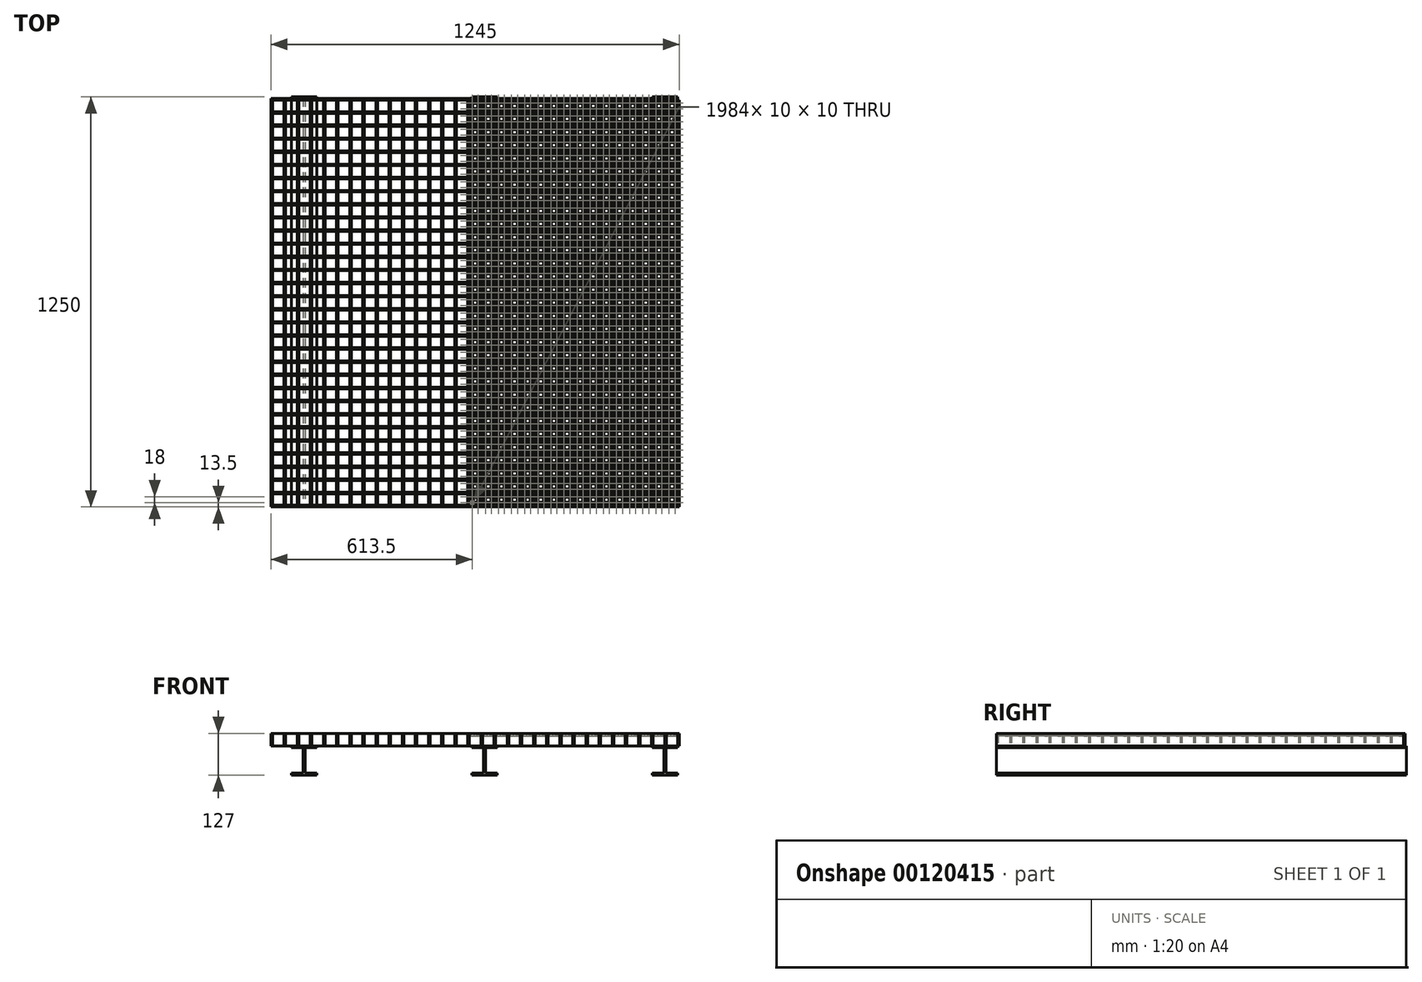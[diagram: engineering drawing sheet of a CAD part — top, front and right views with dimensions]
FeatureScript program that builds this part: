
annotation { "Feature Type Name" : "Feature", "Feature Type Description" : "" }
export const myFeature = defineFeature(function(context is Context, id is Id, definition is map)
    precondition{}
    {
        {
            var Q0;
            Q0=qCreatedBy(makeId("Top.planeOp"),FACE);
            var sketch = newSketch(context, id + "F0", { "sketchPlane" : qUnion([Q0])});
            skLineSegment(sketch, "E0.bottom", {"start": v(0, 0) * mm, "end": v(-1240, 0) * mm});
            skLineSegment(sketch, "E0.top", {"start": v(0, 5) * mm, "end": v(-1240, 5) * mm});
            skLineSegment(sketch, "E0.left", {"start": v(0, 0) * mm, "end": v(0, 5) * mm});
            skLineSegment(sketch, "E0.right", {"start": v(-1240, 0) * mm, "end": v(-1240, 5) * mm});
            skSolve(sketch);
        }
        {
            var Q0;
            Q0 = qSketchRegion(id + "F0", true);
            extrude(context, id + "F1", {"entities" : qUnion([Q0]), "depth" : 38 * mm});
        }
        {
            var Q0;
            Q0=makeQuery(id+"F1.opExtrude","SWEPT_BODY",BODY,{"disambiguationData":[OSD([sQuery(id+"F0.wireOp",EDGE,"E0.bottom"),sQuery(id+"F0.wireOp",EDGE,"E0.top"),sQuery(id+"F0.wireOp",EDGE,"E0.left"),sQuery(id+"F0.wireOp",EDGE,"E0.right")])]});
            transform(context, id + "F2", {"entities" : qUnion([Q0]), "transformType" : TransformType.TRANSLATION_3D, "dx" : 0 * mm, "dy" : 40 * mm, "dz" : 0 * mm, "makeCopy" : true});
        }
        {
            var Q0;
            Q0=makeQuery(id+"F1.opExtrude","SWEPT_BODY",BODY,{"disambiguationData":[OSD([sQuery(id+"F0.wireOp",EDGE,"E0.bottom"),sQuery(id+"F0.wireOp",EDGE,"E0.top"),sQuery(id+"F0.wireOp",EDGE,"E0.left"),sQuery(id+"F0.wireOp",EDGE,"E0.right")])]});
            var Q1;
            Q1=makeQuery(id+"F2.opPattern","COPY",BODY,{"derivedFrom":makeQuery(id+"F1.opExtrude","SWEPT_BODY",BODY,{"disambiguationData":[OSD([sQuery(id+"F0.wireOp",EDGE,"E0.bottom"),sQuery(id+"F0.wireOp",EDGE,"E0.top"),sQuery(id+"F0.wireOp",EDGE,"E0.left"),sQuery(id+"F0.wireOp",EDGE,"E0.right")])]}),"instanceName":"1"});
            transform(context, id + "F3", {"entities" : qUnion([Q0, Q1]), "transformType" : TransformType.TRANSLATION_3D, "dx" : 0 * mm, "dy" : 80 * mm, "dz" : 0 * mm, "makeCopy" : true});
        }
        {
            var Q0;
            Q0=makeQuery(id+"F1.opExtrude","SWEPT_BODY",BODY,{"disambiguationData":[OSD([sQuery(id+"F0.wireOp",EDGE,"E0.bottom"),sQuery(id+"F0.wireOp",EDGE,"E0.top"),sQuery(id+"F0.wireOp",EDGE,"E0.left"),sQuery(id+"F0.wireOp",EDGE,"E0.right")])]});
            var Q1;
            Q1=makeQuery(id+"F2.opPattern","COPY",BODY,{"derivedFrom":makeQuery(id+"F1.opExtrude","SWEPT_BODY",BODY,{"disambiguationData":[OSD([sQuery(id+"F0.wireOp",EDGE,"E0.bottom"),sQuery(id+"F0.wireOp",EDGE,"E0.top"),sQuery(id+"F0.wireOp",EDGE,"E0.left"),sQuery(id+"F0.wireOp",EDGE,"E0.right")])]}),"instanceName":"1"});
            var Q2;
            Q2=makeQuery(id+"F3.opPattern","COPY",BODY,{"derivedFrom":makeQuery(id+"F1.opExtrude","SWEPT_BODY",BODY,{"disambiguationData":[OSD([sQuery(id+"F0.wireOp",EDGE,"E0.bottom"),sQuery(id+"F0.wireOp",EDGE,"E0.top"),sQuery(id+"F0.wireOp",EDGE,"E0.left"),sQuery(id+"F0.wireOp",EDGE,"E0.right")])]}),"instanceName":"1"});
            var Q3;
            Q3=makeQuery(id+"F3.opPattern","COPY",BODY,{"derivedFrom":makeQuery(id+"F2.opPattern","COPY",BODY,{"derivedFrom":makeQuery(id+"F1.opExtrude","SWEPT_BODY",BODY,{"disambiguationData":[OSD([sQuery(id+"F0.wireOp",EDGE,"E0.bottom"),sQuery(id+"F0.wireOp",EDGE,"E0.top"),sQuery(id+"F0.wireOp",EDGE,"E0.left"),sQuery(id+"F0.wireOp",EDGE,"E0.right")])]}),"instanceName":"1"}),"instanceName":"1"});
            transform(context, id + "F4", {"entities" : qUnion([Q0, Q1, Q2, Q3]), "transformType" : TransformType.TRANSLATION_3D, "dx" : 0 * mm, "dy" : 160 * mm, "dz" : 0 * mm, "makeCopy" : true});
        }
        {
            var Q0;
            Q0=makeQuery(id+"F1.opExtrude","SWEPT_BODY",BODY,{"disambiguationData":[OSD([sQuery(id+"F0.wireOp",EDGE,"E0.bottom"),sQuery(id+"F0.wireOp",EDGE,"E0.top"),sQuery(id+"F0.wireOp",EDGE,"E0.left"),sQuery(id+"F0.wireOp",EDGE,"E0.right")])]});
            var Q1;
            Q1=makeQuery(id+"F2.opPattern","COPY",BODY,{"derivedFrom":makeQuery(id+"F1.opExtrude","SWEPT_BODY",BODY,{"disambiguationData":[OSD([sQuery(id+"F0.wireOp",EDGE,"E0.bottom"),sQuery(id+"F0.wireOp",EDGE,"E0.top"),sQuery(id+"F0.wireOp",EDGE,"E0.left"),sQuery(id+"F0.wireOp",EDGE,"E0.right")])]}),"instanceName":"1"});
            var Q2;
            Q2=makeQuery(id+"F4.opPattern","COPY",BODY,{"derivedFrom":makeQuery(id+"F3.opPattern","COPY",BODY,{"derivedFrom":makeQuery(id+"F2.opPattern","COPY",BODY,{"derivedFrom":makeQuery(id+"F1.opExtrude","SWEPT_BODY",BODY,{"disambiguationData":[OSD([sQuery(id+"F0.wireOp",EDGE,"E0.bottom"),sQuery(id+"F0.wireOp",EDGE,"E0.top"),sQuery(id+"F0.wireOp",EDGE,"E0.left"),sQuery(id+"F0.wireOp",EDGE,"E0.right")])]}),"instanceName":"1"}),"instanceName":"1"}),"instanceName":"1"});
            var Q3;
            Q3=makeQuery(id+"F4.opPattern","COPY",BODY,{"derivedFrom":makeQuery(id+"F3.opPattern","COPY",BODY,{"derivedFrom":makeQuery(id+"F1.opExtrude","SWEPT_BODY",BODY,{"disambiguationData":[OSD([sQuery(id+"F0.wireOp",EDGE,"E0.bottom"),sQuery(id+"F0.wireOp",EDGE,"E0.top"),sQuery(id+"F0.wireOp",EDGE,"E0.left"),sQuery(id+"F0.wireOp",EDGE,"E0.right")])]}),"instanceName":"1"}),"instanceName":"1"});
            var Q4;
            Q4=makeQuery(id+"F4.opPattern","COPY",BODY,{"derivedFrom":makeQuery(id+"F2.opPattern","COPY",BODY,{"derivedFrom":makeQuery(id+"F1.opExtrude","SWEPT_BODY",BODY,{"disambiguationData":[OSD([sQuery(id+"F0.wireOp",EDGE,"E0.bottom"),sQuery(id+"F0.wireOp",EDGE,"E0.top"),sQuery(id+"F0.wireOp",EDGE,"E0.left"),sQuery(id+"F0.wireOp",EDGE,"E0.right")])]}),"instanceName":"1"}),"instanceName":"1"});
            var Q5;
            Q5=makeQuery(id+"F4.opPattern","COPY",BODY,{"derivedFrom":makeQuery(id+"F1.opExtrude","SWEPT_BODY",BODY,{"disambiguationData":[OSD([sQuery(id+"F0.wireOp",EDGE,"E0.bottom"),sQuery(id+"F0.wireOp",EDGE,"E0.top"),sQuery(id+"F0.wireOp",EDGE,"E0.left"),sQuery(id+"F0.wireOp",EDGE,"E0.right")])]}),"instanceName":"1"});
            var Q6;
            Q6=makeQuery(id+"F3.opPattern","COPY",BODY,{"derivedFrom":makeQuery(id+"F1.opExtrude","SWEPT_BODY",BODY,{"disambiguationData":[OSD([sQuery(id+"F0.wireOp",EDGE,"E0.bottom"),sQuery(id+"F0.wireOp",EDGE,"E0.top"),sQuery(id+"F0.wireOp",EDGE,"E0.left"),sQuery(id+"F0.wireOp",EDGE,"E0.right")])]}),"instanceName":"1"});
            var Q7;
            Q7=makeQuery(id+"F3.opPattern","COPY",BODY,{"derivedFrom":makeQuery(id+"F2.opPattern","COPY",BODY,{"derivedFrom":makeQuery(id+"F1.opExtrude","SWEPT_BODY",BODY,{"disambiguationData":[OSD([sQuery(id+"F0.wireOp",EDGE,"E0.bottom"),sQuery(id+"F0.wireOp",EDGE,"E0.top"),sQuery(id+"F0.wireOp",EDGE,"E0.left"),sQuery(id+"F0.wireOp",EDGE,"E0.right")])]}),"instanceName":"1"}),"instanceName":"1"});
            transform(context, id + "F5", {"entities" : qUnion([Q0, Q1, Q2, Q3, Q4, Q5, Q6, Q7]), "transformType" : TransformType.TRANSLATION_3D, "dx" : 0 * mm, "dy" : 320 * mm, "dz" : 0 * mm, "makeCopy" : true});
        }
        {
            var Q0;
            Q0=makeQuery(id+"F1.opExtrude","SWEPT_BODY",BODY,{"disambiguationData":[OSD([sQuery(id+"F0.wireOp",EDGE,"E0.bottom"),sQuery(id+"F0.wireOp",EDGE,"E0.top"),sQuery(id+"F0.wireOp",EDGE,"E0.left"),sQuery(id+"F0.wireOp",EDGE,"E0.right")])]});
            var Q1;
            Q1=makeQuery(id+"F2.opPattern","COPY",BODY,{"derivedFrom":makeQuery(id+"F1.opExtrude","SWEPT_BODY",BODY,{"disambiguationData":[OSD([sQuery(id+"F0.wireOp",EDGE,"E0.bottom"),sQuery(id+"F0.wireOp",EDGE,"E0.top"),sQuery(id+"F0.wireOp",EDGE,"E0.left"),sQuery(id+"F0.wireOp",EDGE,"E0.right")])]}),"instanceName":"1"});
            var Q2;
            Q2=makeQuery(id+"F5.opPattern","COPY",BODY,{"derivedFrom":makeQuery(id+"F4.opPattern","COPY",BODY,{"derivedFrom":makeQuery(id+"F1.opExtrude","SWEPT_BODY",BODY,{"disambiguationData":[OSD([sQuery(id+"F0.wireOp",EDGE,"E0.bottom"),sQuery(id+"F0.wireOp",EDGE,"E0.top"),sQuery(id+"F0.wireOp",EDGE,"E0.left"),sQuery(id+"F0.wireOp",EDGE,"E0.right")])]}),"instanceName":"1"}),"instanceName":"1"});
            var Q3;
            Q3=makeQuery(id+"F5.opPattern","COPY",BODY,{"derivedFrom":makeQuery(id+"F4.opPattern","COPY",BODY,{"derivedFrom":makeQuery(id+"F2.opPattern","COPY",BODY,{"derivedFrom":makeQuery(id+"F1.opExtrude","SWEPT_BODY",BODY,{"disambiguationData":[OSD([sQuery(id+"F0.wireOp",EDGE,"E0.bottom"),sQuery(id+"F0.wireOp",EDGE,"E0.top"),sQuery(id+"F0.wireOp",EDGE,"E0.left"),sQuery(id+"F0.wireOp",EDGE,"E0.right")])]}),"instanceName":"1"}),"instanceName":"1"}),"instanceName":"1"});
            var Q4;
            Q4=makeQuery(id+"F5.opPattern","COPY",BODY,{"derivedFrom":makeQuery(id+"F4.opPattern","COPY",BODY,{"derivedFrom":makeQuery(id+"F3.opPattern","COPY",BODY,{"derivedFrom":makeQuery(id+"F1.opExtrude","SWEPT_BODY",BODY,{"disambiguationData":[OSD([sQuery(id+"F0.wireOp",EDGE,"E0.bottom"),sQuery(id+"F0.wireOp",EDGE,"E0.top"),sQuery(id+"F0.wireOp",EDGE,"E0.left"),sQuery(id+"F0.wireOp",EDGE,"E0.right")])]}),"instanceName":"1"}),"instanceName":"1"}),"instanceName":"1"});
            var Q5;
            Q5=makeQuery(id+"F4.opPattern","COPY",BODY,{"derivedFrom":makeQuery(id+"F3.opPattern","COPY",BODY,{"derivedFrom":makeQuery(id+"F2.opPattern","COPY",BODY,{"derivedFrom":makeQuery(id+"F1.opExtrude","SWEPT_BODY",BODY,{"disambiguationData":[OSD([sQuery(id+"F0.wireOp",EDGE,"E0.bottom"),sQuery(id+"F0.wireOp",EDGE,"E0.top"),sQuery(id+"F0.wireOp",EDGE,"E0.left"),sQuery(id+"F0.wireOp",EDGE,"E0.right")])]}),"instanceName":"1"}),"instanceName":"1"}),"instanceName":"1"});
            var Q6;
            Q6=makeQuery(id+"F4.opPattern","COPY",BODY,{"derivedFrom":makeQuery(id+"F3.opPattern","COPY",BODY,{"derivedFrom":makeQuery(id+"F1.opExtrude","SWEPT_BODY",BODY,{"disambiguationData":[OSD([sQuery(id+"F0.wireOp",EDGE,"E0.bottom"),sQuery(id+"F0.wireOp",EDGE,"E0.top"),sQuery(id+"F0.wireOp",EDGE,"E0.left"),sQuery(id+"F0.wireOp",EDGE,"E0.right")])]}),"instanceName":"1"}),"instanceName":"1"});
            var Q7;
            Q7=makeQuery(id+"F4.opPattern","COPY",BODY,{"derivedFrom":makeQuery(id+"F2.opPattern","COPY",BODY,{"derivedFrom":makeQuery(id+"F1.opExtrude","SWEPT_BODY",BODY,{"disambiguationData":[OSD([sQuery(id+"F0.wireOp",EDGE,"E0.bottom"),sQuery(id+"F0.wireOp",EDGE,"E0.top"),sQuery(id+"F0.wireOp",EDGE,"E0.left"),sQuery(id+"F0.wireOp",EDGE,"E0.right")])]}),"instanceName":"1"}),"instanceName":"1"});
            var Q8;
            Q8=makeQuery(id+"F4.opPattern","COPY",BODY,{"derivedFrom":makeQuery(id+"F1.opExtrude","SWEPT_BODY",BODY,{"disambiguationData":[OSD([sQuery(id+"F0.wireOp",EDGE,"E0.bottom"),sQuery(id+"F0.wireOp",EDGE,"E0.top"),sQuery(id+"F0.wireOp",EDGE,"E0.left"),sQuery(id+"F0.wireOp",EDGE,"E0.right")])]}),"instanceName":"1"});
            var Q9;
            Q9=makeQuery(id+"F3.opPattern","COPY",BODY,{"derivedFrom":makeQuery(id+"F1.opExtrude","SWEPT_BODY",BODY,{"disambiguationData":[OSD([sQuery(id+"F0.wireOp",EDGE,"E0.bottom"),sQuery(id+"F0.wireOp",EDGE,"E0.top"),sQuery(id+"F0.wireOp",EDGE,"E0.left"),sQuery(id+"F0.wireOp",EDGE,"E0.right")])]}),"instanceName":"1"});
            var Q10;
            Q10=makeQuery(id+"F3.opPattern","COPY",BODY,{"derivedFrom":makeQuery(id+"F2.opPattern","COPY",BODY,{"derivedFrom":makeQuery(id+"F1.opExtrude","SWEPT_BODY",BODY,{"disambiguationData":[OSD([sQuery(id+"F0.wireOp",EDGE,"E0.bottom"),sQuery(id+"F0.wireOp",EDGE,"E0.top"),sQuery(id+"F0.wireOp",EDGE,"E0.left"),sQuery(id+"F0.wireOp",EDGE,"E0.right")])]}),"instanceName":"1"}),"instanceName":"1"});
            var Q11;
            Q11=makeQuery(id+"F5.opPattern","COPY",BODY,{"derivedFrom":makeQuery(id+"F3.opPattern","COPY",BODY,{"derivedFrom":makeQuery(id+"F2.opPattern","COPY",BODY,{"derivedFrom":makeQuery(id+"F1.opExtrude","SWEPT_BODY",BODY,{"disambiguationData":[OSD([sQuery(id+"F0.wireOp",EDGE,"E0.bottom"),sQuery(id+"F0.wireOp",EDGE,"E0.top"),sQuery(id+"F0.wireOp",EDGE,"E0.left"),sQuery(id+"F0.wireOp",EDGE,"E0.right")])]}),"instanceName":"1"}),"instanceName":"1"}),"instanceName":"1"});
            var Q12;
            Q12=makeQuery(id+"F5.opPattern","COPY",BODY,{"derivedFrom":makeQuery(id+"F3.opPattern","COPY",BODY,{"derivedFrom":makeQuery(id+"F1.opExtrude","SWEPT_BODY",BODY,{"disambiguationData":[OSD([sQuery(id+"F0.wireOp",EDGE,"E0.bottom"),sQuery(id+"F0.wireOp",EDGE,"E0.top"),sQuery(id+"F0.wireOp",EDGE,"E0.left"),sQuery(id+"F0.wireOp",EDGE,"E0.right")])]}),"instanceName":"1"}),"instanceName":"1"});
            var Q13;
            Q13=makeQuery(id+"F5.opPattern","COPY",BODY,{"derivedFrom":makeQuery(id+"F2.opPattern","COPY",BODY,{"derivedFrom":makeQuery(id+"F1.opExtrude","SWEPT_BODY",BODY,{"disambiguationData":[OSD([sQuery(id+"F0.wireOp",EDGE,"E0.bottom"),sQuery(id+"F0.wireOp",EDGE,"E0.top"),sQuery(id+"F0.wireOp",EDGE,"E0.left"),sQuery(id+"F0.wireOp",EDGE,"E0.right")])]}),"instanceName":"1"}),"instanceName":"1"});
            var Q14;
            Q14=makeQuery(id+"F5.opPattern","COPY",BODY,{"derivedFrom":makeQuery(id+"F1.opExtrude","SWEPT_BODY",BODY,{"disambiguationData":[OSD([sQuery(id+"F0.wireOp",EDGE,"E0.bottom"),sQuery(id+"F0.wireOp",EDGE,"E0.top"),sQuery(id+"F0.wireOp",EDGE,"E0.left"),sQuery(id+"F0.wireOp",EDGE,"E0.right")])]}),"instanceName":"1"});
            var Q15;
            Q15=makeQuery(id+"F5.opPattern","COPY",BODY,{"derivedFrom":makeQuery(id+"F4.opPattern","COPY",BODY,{"derivedFrom":makeQuery(id+"F3.opPattern","COPY",BODY,{"derivedFrom":makeQuery(id+"F2.opPattern","COPY",BODY,{"derivedFrom":makeQuery(id+"F1.opExtrude","SWEPT_BODY",BODY,{"disambiguationData":[OSD([sQuery(id+"F0.wireOp",EDGE,"E0.bottom"),sQuery(id+"F0.wireOp",EDGE,"E0.top"),sQuery(id+"F0.wireOp",EDGE,"E0.left"),sQuery(id+"F0.wireOp",EDGE,"E0.right")])]}),"instanceName":"1"}),"instanceName":"1"}),"instanceName":"1"}),"instanceName":"1"});
            transform(context, id + "F6", {"entities" : qUnion([Q0, Q1, Q2, Q3, Q4, Q5, Q6, Q7, Q8, Q9, Q10, Q11, Q12, Q13, Q14, Q15]), "transformType" : TransformType.TRANSLATION_3D, "dx" : 0 * mm, "dy" : 640 * mm, "dz" : 0 * mm, "makeCopy" : true});
        }
        {
            var Q0;
            Q0=makeQuery(id+"F1.opExtrude","SWEPT_BODY",BODY,{"disambiguationData":[OSD([sQuery(id+"F0.wireOp",EDGE,"E0.bottom"),sQuery(id+"F0.wireOp",EDGE,"E0.top"),sQuery(id+"F0.wireOp",EDGE,"E0.left"),sQuery(id+"F0.wireOp",EDGE,"E0.right")])]});
            var Q1;
            Q1=makeQuery(id+"F2.opPattern","COPY",BODY,{"derivedFrom":makeQuery(id+"F1.opExtrude","SWEPT_BODY",BODY,{"disambiguationData":[OSD([sQuery(id+"F0.wireOp",EDGE,"E0.bottom"),sQuery(id+"F0.wireOp",EDGE,"E0.top"),sQuery(id+"F0.wireOp",EDGE,"E0.left"),sQuery(id+"F0.wireOp",EDGE,"E0.right")])]}),"instanceName":"1"});
            var Q2;
            Q2=makeQuery(id+"F5.opPattern","COPY",BODY,{"derivedFrom":makeQuery(id+"F4.opPattern","COPY",BODY,{"derivedFrom":makeQuery(id+"F1.opExtrude","SWEPT_BODY",BODY,{"disambiguationData":[OSD([sQuery(id+"F0.wireOp",EDGE,"E0.bottom"),sQuery(id+"F0.wireOp",EDGE,"E0.top"),sQuery(id+"F0.wireOp",EDGE,"E0.left"),sQuery(id+"F0.wireOp",EDGE,"E0.right")])]}),"instanceName":"1"}),"instanceName":"1"});
            var Q3;
            Q3=makeQuery(id+"F5.opPattern","COPY",BODY,{"derivedFrom":makeQuery(id+"F4.opPattern","COPY",BODY,{"derivedFrom":makeQuery(id+"F2.opPattern","COPY",BODY,{"derivedFrom":makeQuery(id+"F1.opExtrude","SWEPT_BODY",BODY,{"disambiguationData":[OSD([sQuery(id+"F0.wireOp",EDGE,"E0.bottom"),sQuery(id+"F0.wireOp",EDGE,"E0.top"),sQuery(id+"F0.wireOp",EDGE,"E0.left"),sQuery(id+"F0.wireOp",EDGE,"E0.right")])]}),"instanceName":"1"}),"instanceName":"1"}),"instanceName":"1"});
            var Q4;
            Q4=makeQuery(id+"F5.opPattern","COPY",BODY,{"derivedFrom":makeQuery(id+"F4.opPattern","COPY",BODY,{"derivedFrom":makeQuery(id+"F3.opPattern","COPY",BODY,{"derivedFrom":makeQuery(id+"F1.opExtrude","SWEPT_BODY",BODY,{"disambiguationData":[OSD([sQuery(id+"F0.wireOp",EDGE,"E0.bottom"),sQuery(id+"F0.wireOp",EDGE,"E0.top"),sQuery(id+"F0.wireOp",EDGE,"E0.left"),sQuery(id+"F0.wireOp",EDGE,"E0.right")])]}),"instanceName":"1"}),"instanceName":"1"}),"instanceName":"1"});
            var Q5;
            Q5=makeQuery(id+"F4.opPattern","COPY",BODY,{"derivedFrom":makeQuery(id+"F3.opPattern","COPY",BODY,{"derivedFrom":makeQuery(id+"F2.opPattern","COPY",BODY,{"derivedFrom":makeQuery(id+"F1.opExtrude","SWEPT_BODY",BODY,{"disambiguationData":[OSD([sQuery(id+"F0.wireOp",EDGE,"E0.bottom"),sQuery(id+"F0.wireOp",EDGE,"E0.top"),sQuery(id+"F0.wireOp",EDGE,"E0.left"),sQuery(id+"F0.wireOp",EDGE,"E0.right")])]}),"instanceName":"1"}),"instanceName":"1"}),"instanceName":"1"});
            var Q6;
            Q6=makeQuery(id+"F4.opPattern","COPY",BODY,{"derivedFrom":makeQuery(id+"F3.opPattern","COPY",BODY,{"derivedFrom":makeQuery(id+"F1.opExtrude","SWEPT_BODY",BODY,{"disambiguationData":[OSD([sQuery(id+"F0.wireOp",EDGE,"E0.bottom"),sQuery(id+"F0.wireOp",EDGE,"E0.top"),sQuery(id+"F0.wireOp",EDGE,"E0.left"),sQuery(id+"F0.wireOp",EDGE,"E0.right")])]}),"instanceName":"1"}),"instanceName":"1"});
            var Q7;
            Q7=makeQuery(id+"F4.opPattern","COPY",BODY,{"derivedFrom":makeQuery(id+"F2.opPattern","COPY",BODY,{"derivedFrom":makeQuery(id+"F1.opExtrude","SWEPT_BODY",BODY,{"disambiguationData":[OSD([sQuery(id+"F0.wireOp",EDGE,"E0.bottom"),sQuery(id+"F0.wireOp",EDGE,"E0.top"),sQuery(id+"F0.wireOp",EDGE,"E0.left"),sQuery(id+"F0.wireOp",EDGE,"E0.right")])]}),"instanceName":"1"}),"instanceName":"1"});
            var Q8;
            Q8=makeQuery(id+"F4.opPattern","COPY",BODY,{"derivedFrom":makeQuery(id+"F1.opExtrude","SWEPT_BODY",BODY,{"disambiguationData":[OSD([sQuery(id+"F0.wireOp",EDGE,"E0.bottom"),sQuery(id+"F0.wireOp",EDGE,"E0.top"),sQuery(id+"F0.wireOp",EDGE,"E0.left"),sQuery(id+"F0.wireOp",EDGE,"E0.right")])]}),"instanceName":"1"});
            var Q9;
            Q9=makeQuery(id+"F3.opPattern","COPY",BODY,{"derivedFrom":makeQuery(id+"F1.opExtrude","SWEPT_BODY",BODY,{"disambiguationData":[OSD([sQuery(id+"F0.wireOp",EDGE,"E0.bottom"),sQuery(id+"F0.wireOp",EDGE,"E0.top"),sQuery(id+"F0.wireOp",EDGE,"E0.left"),sQuery(id+"F0.wireOp",EDGE,"E0.right")])]}),"instanceName":"1"});
            var Q10;
            Q10=makeQuery(id+"F3.opPattern","COPY",BODY,{"derivedFrom":makeQuery(id+"F2.opPattern","COPY",BODY,{"derivedFrom":makeQuery(id+"F1.opExtrude","SWEPT_BODY",BODY,{"disambiguationData":[OSD([sQuery(id+"F0.wireOp",EDGE,"E0.bottom"),sQuery(id+"F0.wireOp",EDGE,"E0.top"),sQuery(id+"F0.wireOp",EDGE,"E0.left"),sQuery(id+"F0.wireOp",EDGE,"E0.right")])]}),"instanceName":"1"}),"instanceName":"1"});
            var Q11;
            Q11=makeQuery(id+"F5.opPattern","COPY",BODY,{"derivedFrom":makeQuery(id+"F3.opPattern","COPY",BODY,{"derivedFrom":makeQuery(id+"F2.opPattern","COPY",BODY,{"derivedFrom":makeQuery(id+"F1.opExtrude","SWEPT_BODY",BODY,{"disambiguationData":[OSD([sQuery(id+"F0.wireOp",EDGE,"E0.bottom"),sQuery(id+"F0.wireOp",EDGE,"E0.top"),sQuery(id+"F0.wireOp",EDGE,"E0.left"),sQuery(id+"F0.wireOp",EDGE,"E0.right")])]}),"instanceName":"1"}),"instanceName":"1"}),"instanceName":"1"});
            var Q12;
            Q12=makeQuery(id+"F5.opPattern","COPY",BODY,{"derivedFrom":makeQuery(id+"F3.opPattern","COPY",BODY,{"derivedFrom":makeQuery(id+"F1.opExtrude","SWEPT_BODY",BODY,{"disambiguationData":[OSD([sQuery(id+"F0.wireOp",EDGE,"E0.bottom"),sQuery(id+"F0.wireOp",EDGE,"E0.top"),sQuery(id+"F0.wireOp",EDGE,"E0.left"),sQuery(id+"F0.wireOp",EDGE,"E0.right")])]}),"instanceName":"1"}),"instanceName":"1"});
            var Q13;
            Q13=makeQuery(id+"F5.opPattern","COPY",BODY,{"derivedFrom":makeQuery(id+"F2.opPattern","COPY",BODY,{"derivedFrom":makeQuery(id+"F1.opExtrude","SWEPT_BODY",BODY,{"disambiguationData":[OSD([sQuery(id+"F0.wireOp",EDGE,"E0.bottom"),sQuery(id+"F0.wireOp",EDGE,"E0.top"),sQuery(id+"F0.wireOp",EDGE,"E0.left"),sQuery(id+"F0.wireOp",EDGE,"E0.right")])]}),"instanceName":"1"}),"instanceName":"1"});
            var Q14;
            Q14=makeQuery(id+"F5.opPattern","COPY",BODY,{"derivedFrom":makeQuery(id+"F1.opExtrude","SWEPT_BODY",BODY,{"disambiguationData":[OSD([sQuery(id+"F0.wireOp",EDGE,"E0.bottom"),sQuery(id+"F0.wireOp",EDGE,"E0.top"),sQuery(id+"F0.wireOp",EDGE,"E0.left"),sQuery(id+"F0.wireOp",EDGE,"E0.right")])]}),"instanceName":"1"});
            var Q15;
            Q15=makeQuery(id+"F5.opPattern","COPY",BODY,{"derivedFrom":makeQuery(id+"F4.opPattern","COPY",BODY,{"derivedFrom":makeQuery(id+"F3.opPattern","COPY",BODY,{"derivedFrom":makeQuery(id+"F2.opPattern","COPY",BODY,{"derivedFrom":makeQuery(id+"F1.opExtrude","SWEPT_BODY",BODY,{"disambiguationData":[OSD([sQuery(id+"F0.wireOp",EDGE,"E0.bottom"),sQuery(id+"F0.wireOp",EDGE,"E0.top"),sQuery(id+"F0.wireOp",EDGE,"E0.left"),sQuery(id+"F0.wireOp",EDGE,"E0.right")])]}),"instanceName":"1"}),"instanceName":"1"}),"instanceName":"1"}),"instanceName":"1"});
            var Q16;
            Q16=makeQuery(id+"F6.opPattern","COPY",BODY,{"derivedFrom":makeQuery(id+"F1.opExtrude","SWEPT_BODY",BODY,{"disambiguationData":[OSD([sQuery(id+"F0.wireOp",EDGE,"E0.bottom"),sQuery(id+"F0.wireOp",EDGE,"E0.top"),sQuery(id+"F0.wireOp",EDGE,"E0.left"),sQuery(id+"F0.wireOp",EDGE,"E0.right")])]}),"instanceName":"1"});
            var Q17;
            Q17=makeQuery(id+"F6.opPattern","COPY",BODY,{"derivedFrom":makeQuery(id+"F2.opPattern","COPY",BODY,{"derivedFrom":makeQuery(id+"F1.opExtrude","SWEPT_BODY",BODY,{"disambiguationData":[OSD([sQuery(id+"F0.wireOp",EDGE,"E0.bottom"),sQuery(id+"F0.wireOp",EDGE,"E0.top"),sQuery(id+"F0.wireOp",EDGE,"E0.left"),sQuery(id+"F0.wireOp",EDGE,"E0.right")])]}),"instanceName":"1"}),"instanceName":"1"});
            var Q18;
            Q18=makeQuery(id+"F6.opPattern","COPY",BODY,{"derivedFrom":makeQuery(id+"F3.opPattern","COPY",BODY,{"derivedFrom":makeQuery(id+"F1.opExtrude","SWEPT_BODY",BODY,{"disambiguationData":[OSD([sQuery(id+"F0.wireOp",EDGE,"E0.bottom"),sQuery(id+"F0.wireOp",EDGE,"E0.top"),sQuery(id+"F0.wireOp",EDGE,"E0.left"),sQuery(id+"F0.wireOp",EDGE,"E0.right")])]}),"instanceName":"1"}),"instanceName":"1"});
            var Q19;
            Q19=makeQuery(id+"F6.opPattern","COPY",BODY,{"derivedFrom":makeQuery(id+"F3.opPattern","COPY",BODY,{"derivedFrom":makeQuery(id+"F2.opPattern","COPY",BODY,{"derivedFrom":makeQuery(id+"F1.opExtrude","SWEPT_BODY",BODY,{"disambiguationData":[OSD([sQuery(id+"F0.wireOp",EDGE,"E0.bottom"),sQuery(id+"F0.wireOp",EDGE,"E0.top"),sQuery(id+"F0.wireOp",EDGE,"E0.left"),sQuery(id+"F0.wireOp",EDGE,"E0.right")])]}),"instanceName":"1"}),"instanceName":"1"}),"instanceName":"1"});
            var Q20;
            Q20=makeQuery(id+"F6.opPattern","COPY",BODY,{"derivedFrom":makeQuery(id+"F4.opPattern","COPY",BODY,{"derivedFrom":makeQuery(id+"F1.opExtrude","SWEPT_BODY",BODY,{"disambiguationData":[OSD([sQuery(id+"F0.wireOp",EDGE,"E0.bottom"),sQuery(id+"F0.wireOp",EDGE,"E0.top"),sQuery(id+"F0.wireOp",EDGE,"E0.left"),sQuery(id+"F0.wireOp",EDGE,"E0.right")])]}),"instanceName":"1"}),"instanceName":"1"});
            var Q21;
            Q21=makeQuery(id+"F6.opPattern","COPY",BODY,{"derivedFrom":makeQuery(id+"F4.opPattern","COPY",BODY,{"derivedFrom":makeQuery(id+"F2.opPattern","COPY",BODY,{"derivedFrom":makeQuery(id+"F1.opExtrude","SWEPT_BODY",BODY,{"disambiguationData":[OSD([sQuery(id+"F0.wireOp",EDGE,"E0.bottom"),sQuery(id+"F0.wireOp",EDGE,"E0.top"),sQuery(id+"F0.wireOp",EDGE,"E0.left"),sQuery(id+"F0.wireOp",EDGE,"E0.right")])]}),"instanceName":"1"}),"instanceName":"1"}),"instanceName":"1"});
            var Q22;
            Q22=makeQuery(id+"F6.opPattern","COPY",BODY,{"derivedFrom":makeQuery(id+"F4.opPattern","COPY",BODY,{"derivedFrom":makeQuery(id+"F3.opPattern","COPY",BODY,{"derivedFrom":makeQuery(id+"F1.opExtrude","SWEPT_BODY",BODY,{"disambiguationData":[OSD([sQuery(id+"F0.wireOp",EDGE,"E0.bottom"),sQuery(id+"F0.wireOp",EDGE,"E0.top"),sQuery(id+"F0.wireOp",EDGE,"E0.left"),sQuery(id+"F0.wireOp",EDGE,"E0.right")])]}),"instanceName":"1"}),"instanceName":"1"}),"instanceName":"1"});
            var Q23;
            Q23=makeQuery(id+"F6.opPattern","COPY",BODY,{"derivedFrom":makeQuery(id+"F4.opPattern","COPY",BODY,{"derivedFrom":makeQuery(id+"F3.opPattern","COPY",BODY,{"derivedFrom":makeQuery(id+"F2.opPattern","COPY",BODY,{"derivedFrom":makeQuery(id+"F1.opExtrude","SWEPT_BODY",BODY,{"disambiguationData":[OSD([sQuery(id+"F0.wireOp",EDGE,"E0.bottom"),sQuery(id+"F0.wireOp",EDGE,"E0.top"),sQuery(id+"F0.wireOp",EDGE,"E0.left"),sQuery(id+"F0.wireOp",EDGE,"E0.right")])]}),"instanceName":"1"}),"instanceName":"1"}),"instanceName":"1"}),"instanceName":"1"});
            var Q24;
            Q24=makeQuery(id+"F6.opPattern","COPY",BODY,{"derivedFrom":makeQuery(id+"F5.opPattern","COPY",BODY,{"derivedFrom":makeQuery(id+"F1.opExtrude","SWEPT_BODY",BODY,{"disambiguationData":[OSD([sQuery(id+"F0.wireOp",EDGE,"E0.bottom"),sQuery(id+"F0.wireOp",EDGE,"E0.top"),sQuery(id+"F0.wireOp",EDGE,"E0.left"),sQuery(id+"F0.wireOp",EDGE,"E0.right")])]}),"instanceName":"1"}),"instanceName":"1"});
            var Q25;
            Q25=makeQuery(id+"F6.opPattern","COPY",BODY,{"derivedFrom":makeQuery(id+"F5.opPattern","COPY",BODY,{"derivedFrom":makeQuery(id+"F2.opPattern","COPY",BODY,{"derivedFrom":makeQuery(id+"F1.opExtrude","SWEPT_BODY",BODY,{"disambiguationData":[OSD([sQuery(id+"F0.wireOp",EDGE,"E0.bottom"),sQuery(id+"F0.wireOp",EDGE,"E0.top"),sQuery(id+"F0.wireOp",EDGE,"E0.left"),sQuery(id+"F0.wireOp",EDGE,"E0.right")])]}),"instanceName":"1"}),"instanceName":"1"}),"instanceName":"1"});
            var Q26;
            Q26=makeQuery(id+"F6.opPattern","COPY",BODY,{"derivedFrom":makeQuery(id+"F5.opPattern","COPY",BODY,{"derivedFrom":makeQuery(id+"F3.opPattern","COPY",BODY,{"derivedFrom":makeQuery(id+"F1.opExtrude","SWEPT_BODY",BODY,{"disambiguationData":[OSD([sQuery(id+"F0.wireOp",EDGE,"E0.bottom"),sQuery(id+"F0.wireOp",EDGE,"E0.top"),sQuery(id+"F0.wireOp",EDGE,"E0.left"),sQuery(id+"F0.wireOp",EDGE,"E0.right")])]}),"instanceName":"1"}),"instanceName":"1"}),"instanceName":"1"});
            var Q27;
            Q27=makeQuery(id+"F6.opPattern","COPY",BODY,{"derivedFrom":makeQuery(id+"F5.opPattern","COPY",BODY,{"derivedFrom":makeQuery(id+"F3.opPattern","COPY",BODY,{"derivedFrom":makeQuery(id+"F2.opPattern","COPY",BODY,{"derivedFrom":makeQuery(id+"F1.opExtrude","SWEPT_BODY",BODY,{"disambiguationData":[OSD([sQuery(id+"F0.wireOp",EDGE,"E0.bottom"),sQuery(id+"F0.wireOp",EDGE,"E0.top"),sQuery(id+"F0.wireOp",EDGE,"E0.left"),sQuery(id+"F0.wireOp",EDGE,"E0.right")])]}),"instanceName":"1"}),"instanceName":"1"}),"instanceName":"1"}),"instanceName":"1"});
            var Q28;
            Q28=makeQuery(id+"F6.opPattern","COPY",BODY,{"derivedFrom":makeQuery(id+"F5.opPattern","COPY",BODY,{"derivedFrom":makeQuery(id+"F4.opPattern","COPY",BODY,{"derivedFrom":makeQuery(id+"F1.opExtrude","SWEPT_BODY",BODY,{"disambiguationData":[OSD([sQuery(id+"F0.wireOp",EDGE,"E0.bottom"),sQuery(id+"F0.wireOp",EDGE,"E0.top"),sQuery(id+"F0.wireOp",EDGE,"E0.left"),sQuery(id+"F0.wireOp",EDGE,"E0.right")])]}),"instanceName":"1"}),"instanceName":"1"}),"instanceName":"1"});
            var Q29;
            Q29=makeQuery(id+"F6.opPattern","COPY",BODY,{"derivedFrom":makeQuery(id+"F5.opPattern","COPY",BODY,{"derivedFrom":makeQuery(id+"F4.opPattern","COPY",BODY,{"derivedFrom":makeQuery(id+"F2.opPattern","COPY",BODY,{"derivedFrom":makeQuery(id+"F1.opExtrude","SWEPT_BODY",BODY,{"disambiguationData":[OSD([sQuery(id+"F0.wireOp",EDGE,"E0.bottom"),sQuery(id+"F0.wireOp",EDGE,"E0.top"),sQuery(id+"F0.wireOp",EDGE,"E0.left"),sQuery(id+"F0.wireOp",EDGE,"E0.right")])]}),"instanceName":"1"}),"instanceName":"1"}),"instanceName":"1"}),"instanceName":"1"});
            var Q30;
            Q30=makeQuery(id+"F6.opPattern","COPY",BODY,{"derivedFrom":makeQuery(id+"F5.opPattern","COPY",BODY,{"derivedFrom":makeQuery(id+"F4.opPattern","COPY",BODY,{"derivedFrom":makeQuery(id+"F3.opPattern","COPY",BODY,{"derivedFrom":makeQuery(id+"F1.opExtrude","SWEPT_BODY",BODY,{"disambiguationData":[OSD([sQuery(id+"F0.wireOp",EDGE,"E0.bottom"),sQuery(id+"F0.wireOp",EDGE,"E0.top"),sQuery(id+"F0.wireOp",EDGE,"E0.left"),sQuery(id+"F0.wireOp",EDGE,"E0.right")])]}),"instanceName":"1"}),"instanceName":"1"}),"instanceName":"1"}),"instanceName":"1"});
            var Q31;
            Q31=makeQuery(id+"F6.opPattern","COPY",BODY,{"derivedFrom":makeQuery(id+"F5.opPattern","COPY",BODY,{"derivedFrom":makeQuery(id+"F4.opPattern","COPY",BODY,{"derivedFrom":makeQuery(id+"F3.opPattern","COPY",BODY,{"derivedFrom":makeQuery(id+"F2.opPattern","COPY",BODY,{"derivedFrom":makeQuery(id+"F1.opExtrude","SWEPT_BODY",BODY,{"disambiguationData":[OSD([sQuery(id+"F0.wireOp",EDGE,"E0.bottom"),sQuery(id+"F0.wireOp",EDGE,"E0.top"),sQuery(id+"F0.wireOp",EDGE,"E0.left"),sQuery(id+"F0.wireOp",EDGE,"E0.right")])]}),"instanceName":"1"}),"instanceName":"1"}),"instanceName":"1"}),"instanceName":"1"}),"instanceName":"1"});
            var Q32;
            Q32=makeQuery(id+"F1.opExtrude","SWEPT_EDGE",EDGE,{"disambiguationData":[OSD([sQuery(id+"F0.wireOp",EDGE,"E0.bottom"),sQuery(id+"F0.wireOp",EDGE,"E0.left")])]});
            transform(context, id + "F7", {"entities" : qUnion([Q0, Q1, Q2, Q3, Q4, Q5, Q6, Q7, Q8, Q9, Q10, Q11, Q12, Q13, Q14, Q15, Q16, Q17, Q18, Q19, Q20, Q21, Q22, Q23, Q24, Q25, Q26, Q27, Q28, Q29, Q30, Q31]), "transformType" : TransformType.ROTATION, "transformAxis" : qUnion([Q32]), "angle" : 90 * degree, "makeCopy" : true});
        }
        {
            var Q0;
            Q0=makeQuery(id+"F7.opPattern","COPY",BODY,{"derivedFrom":makeQuery(id+"F2.opPattern","COPY",BODY,{"derivedFrom":makeQuery(id+"F1.opExtrude","SWEPT_BODY",BODY,{"disambiguationData":[OSD([sQuery(id+"F0.wireOp",EDGE,"E0.bottom"),sQuery(id+"F0.wireOp",EDGE,"E0.top"),sQuery(id+"F0.wireOp",EDGE,"E0.left"),sQuery(id+"F0.wireOp",EDGE,"E0.right")])]}),"instanceName":"1"}),"instanceName":"1"});
            var Q1;
            Q1=makeQuery(id+"F7.opPattern","COPY",BODY,{"derivedFrom":makeQuery(id+"F3.opPattern","COPY",BODY,{"derivedFrom":makeQuery(id+"F1.opExtrude","SWEPT_BODY",BODY,{"disambiguationData":[OSD([sQuery(id+"F0.wireOp",EDGE,"E0.bottom"),sQuery(id+"F0.wireOp",EDGE,"E0.top"),sQuery(id+"F0.wireOp",EDGE,"E0.left"),sQuery(id+"F0.wireOp",EDGE,"E0.right")])]}),"instanceName":"1"}),"instanceName":"1"});
            var Q2;
            Q2=makeQuery(id+"F7.opPattern","COPY",BODY,{"derivedFrom":makeQuery(id+"F3.opPattern","COPY",BODY,{"derivedFrom":makeQuery(id+"F2.opPattern","COPY",BODY,{"derivedFrom":makeQuery(id+"F1.opExtrude","SWEPT_BODY",BODY,{"disambiguationData":[OSD([sQuery(id+"F0.wireOp",EDGE,"E0.bottom"),sQuery(id+"F0.wireOp",EDGE,"E0.top"),sQuery(id+"F0.wireOp",EDGE,"E0.left"),sQuery(id+"F0.wireOp",EDGE,"E0.right")])]}),"instanceName":"1"}),"instanceName":"1"}),"instanceName":"1"});
            var Q3;
            Q3=makeQuery(id+"F7.opPattern","COPY",BODY,{"derivedFrom":makeQuery(id+"F4.opPattern","COPY",BODY,{"derivedFrom":makeQuery(id+"F1.opExtrude","SWEPT_BODY",BODY,{"disambiguationData":[OSD([sQuery(id+"F0.wireOp",EDGE,"E0.bottom"),sQuery(id+"F0.wireOp",EDGE,"E0.top"),sQuery(id+"F0.wireOp",EDGE,"E0.left"),sQuery(id+"F0.wireOp",EDGE,"E0.right")])]}),"instanceName":"1"}),"instanceName":"1"});
            var Q4;
            Q4=makeQuery(id+"F7.opPattern","COPY",BODY,{"derivedFrom":makeQuery(id+"F4.opPattern","COPY",BODY,{"derivedFrom":makeQuery(id+"F2.opPattern","COPY",BODY,{"derivedFrom":makeQuery(id+"F1.opExtrude","SWEPT_BODY",BODY,{"disambiguationData":[OSD([sQuery(id+"F0.wireOp",EDGE,"E0.bottom"),sQuery(id+"F0.wireOp",EDGE,"E0.top"),sQuery(id+"F0.wireOp",EDGE,"E0.left"),sQuery(id+"F0.wireOp",EDGE,"E0.right")])]}),"instanceName":"1"}),"instanceName":"1"}),"instanceName":"1"});
            var Q5;
            Q5=makeQuery(id+"F7.opPattern","COPY",BODY,{"derivedFrom":makeQuery(id+"F4.opPattern","COPY",BODY,{"derivedFrom":makeQuery(id+"F3.opPattern","COPY",BODY,{"derivedFrom":makeQuery(id+"F1.opExtrude","SWEPT_BODY",BODY,{"disambiguationData":[OSD([sQuery(id+"F0.wireOp",EDGE,"E0.bottom"),sQuery(id+"F0.wireOp",EDGE,"E0.top"),sQuery(id+"F0.wireOp",EDGE,"E0.left"),sQuery(id+"F0.wireOp",EDGE,"E0.right")])]}),"instanceName":"1"}),"instanceName":"1"}),"instanceName":"1"});
            var Q6;
            Q6=makeQuery(id+"F7.opPattern","COPY",BODY,{"derivedFrom":makeQuery(id+"F4.opPattern","COPY",BODY,{"derivedFrom":makeQuery(id+"F3.opPattern","COPY",BODY,{"derivedFrom":makeQuery(id+"F2.opPattern","COPY",BODY,{"derivedFrom":makeQuery(id+"F1.opExtrude","SWEPT_BODY",BODY,{"disambiguationData":[OSD([sQuery(id+"F0.wireOp",EDGE,"E0.bottom"),sQuery(id+"F0.wireOp",EDGE,"E0.top"),sQuery(id+"F0.wireOp",EDGE,"E0.left"),sQuery(id+"F0.wireOp",EDGE,"E0.right")])]}),"instanceName":"1"}),"instanceName":"1"}),"instanceName":"1"}),"instanceName":"1"});
            var Q7;
            Q7=makeQuery(id+"F7.opPattern","COPY",BODY,{"derivedFrom":makeQuery(id+"F5.opPattern","COPY",BODY,{"derivedFrom":makeQuery(id+"F1.opExtrude","SWEPT_BODY",BODY,{"disambiguationData":[OSD([sQuery(id+"F0.wireOp",EDGE,"E0.bottom"),sQuery(id+"F0.wireOp",EDGE,"E0.top"),sQuery(id+"F0.wireOp",EDGE,"E0.left"),sQuery(id+"F0.wireOp",EDGE,"E0.right")])]}),"instanceName":"1"}),"instanceName":"1"});
            var Q8;
            Q8=makeQuery(id+"F7.opPattern","COPY",BODY,{"derivedFrom":makeQuery(id+"F5.opPattern","COPY",BODY,{"derivedFrom":makeQuery(id+"F2.opPattern","COPY",BODY,{"derivedFrom":makeQuery(id+"F1.opExtrude","SWEPT_BODY",BODY,{"disambiguationData":[OSD([sQuery(id+"F0.wireOp",EDGE,"E0.bottom"),sQuery(id+"F0.wireOp",EDGE,"E0.top"),sQuery(id+"F0.wireOp",EDGE,"E0.left"),sQuery(id+"F0.wireOp",EDGE,"E0.right")])]}),"instanceName":"1"}),"instanceName":"1"}),"instanceName":"1"});
            var Q9;
            Q9=makeQuery(id+"F7.opPattern","COPY",BODY,{"derivedFrom":makeQuery(id+"F5.opPattern","COPY",BODY,{"derivedFrom":makeQuery(id+"F3.opPattern","COPY",BODY,{"derivedFrom":makeQuery(id+"F1.opExtrude","SWEPT_BODY",BODY,{"disambiguationData":[OSD([sQuery(id+"F0.wireOp",EDGE,"E0.bottom"),sQuery(id+"F0.wireOp",EDGE,"E0.top"),sQuery(id+"F0.wireOp",EDGE,"E0.left"),sQuery(id+"F0.wireOp",EDGE,"E0.right")])]}),"instanceName":"1"}),"instanceName":"1"}),"instanceName":"1"});
            var Q10;
            Q10=makeQuery(id+"F7.opPattern","COPY",BODY,{"derivedFrom":makeQuery(id+"F5.opPattern","COPY",BODY,{"derivedFrom":makeQuery(id+"F3.opPattern","COPY",BODY,{"derivedFrom":makeQuery(id+"F2.opPattern","COPY",BODY,{"derivedFrom":makeQuery(id+"F1.opExtrude","SWEPT_BODY",BODY,{"disambiguationData":[OSD([sQuery(id+"F0.wireOp",EDGE,"E0.bottom"),sQuery(id+"F0.wireOp",EDGE,"E0.top"),sQuery(id+"F0.wireOp",EDGE,"E0.left"),sQuery(id+"F0.wireOp",EDGE,"E0.right")])]}),"instanceName":"1"}),"instanceName":"1"}),"instanceName":"1"}),"instanceName":"1"});
            var Q11;
            Q11=makeQuery(id+"F7.opPattern","COPY",BODY,{"derivedFrom":makeQuery(id+"F5.opPattern","COPY",BODY,{"derivedFrom":makeQuery(id+"F4.opPattern","COPY",BODY,{"derivedFrom":makeQuery(id+"F1.opExtrude","SWEPT_BODY",BODY,{"disambiguationData":[OSD([sQuery(id+"F0.wireOp",EDGE,"E0.bottom"),sQuery(id+"F0.wireOp",EDGE,"E0.top"),sQuery(id+"F0.wireOp",EDGE,"E0.left"),sQuery(id+"F0.wireOp",EDGE,"E0.right")])]}),"instanceName":"1"}),"instanceName":"1"}),"instanceName":"1"});
            var Q12;
            Q12=makeQuery(id+"F7.opPattern","COPY",BODY,{"derivedFrom":makeQuery(id+"F5.opPattern","COPY",BODY,{"derivedFrom":makeQuery(id+"F4.opPattern","COPY",BODY,{"derivedFrom":makeQuery(id+"F2.opPattern","COPY",BODY,{"derivedFrom":makeQuery(id+"F1.opExtrude","SWEPT_BODY",BODY,{"disambiguationData":[OSD([sQuery(id+"F0.wireOp",EDGE,"E0.bottom"),sQuery(id+"F0.wireOp",EDGE,"E0.top"),sQuery(id+"F0.wireOp",EDGE,"E0.left"),sQuery(id+"F0.wireOp",EDGE,"E0.right")])]}),"instanceName":"1"}),"instanceName":"1"}),"instanceName":"1"}),"instanceName":"1"});
            var Q13;
            Q13=makeQuery(id+"F7.opPattern","COPY",BODY,{"derivedFrom":makeQuery(id+"F5.opPattern","COPY",BODY,{"derivedFrom":makeQuery(id+"F4.opPattern","COPY",BODY,{"derivedFrom":makeQuery(id+"F3.opPattern","COPY",BODY,{"derivedFrom":makeQuery(id+"F1.opExtrude","SWEPT_BODY",BODY,{"disambiguationData":[OSD([sQuery(id+"F0.wireOp",EDGE,"E0.bottom"),sQuery(id+"F0.wireOp",EDGE,"E0.top"),sQuery(id+"F0.wireOp",EDGE,"E0.left"),sQuery(id+"F0.wireOp",EDGE,"E0.right")])]}),"instanceName":"1"}),"instanceName":"1"}),"instanceName":"1"}),"instanceName":"1"});
            var Q14;
            Q14=makeQuery(id+"F7.opPattern","COPY",BODY,{"derivedFrom":makeQuery(id+"F5.opPattern","COPY",BODY,{"derivedFrom":makeQuery(id+"F4.opPattern","COPY",BODY,{"derivedFrom":makeQuery(id+"F3.opPattern","COPY",BODY,{"derivedFrom":makeQuery(id+"F2.opPattern","COPY",BODY,{"derivedFrom":makeQuery(id+"F1.opExtrude","SWEPT_BODY",BODY,{"disambiguationData":[OSD([sQuery(id+"F0.wireOp",EDGE,"E0.bottom"),sQuery(id+"F0.wireOp",EDGE,"E0.top"),sQuery(id+"F0.wireOp",EDGE,"E0.left"),sQuery(id+"F0.wireOp",EDGE,"E0.right")])]}),"instanceName":"1"}),"instanceName":"1"}),"instanceName":"1"}),"instanceName":"1"}),"instanceName":"1"});
            var Q15;
            Q15=makeQuery(id+"F7.opPattern","COPY",BODY,{"derivedFrom":makeQuery(id+"F6.opPattern","COPY",BODY,{"derivedFrom":makeQuery(id+"F1.opExtrude","SWEPT_BODY",BODY,{"disambiguationData":[OSD([sQuery(id+"F0.wireOp",EDGE,"E0.bottom"),sQuery(id+"F0.wireOp",EDGE,"E0.top"),sQuery(id+"F0.wireOp",EDGE,"E0.left"),sQuery(id+"F0.wireOp",EDGE,"E0.right")])]}),"instanceName":"1"}),"instanceName":"1"});
            var Q16;
            Q16=makeQuery(id+"F7.opPattern","COPY",BODY,{"derivedFrom":makeQuery(id+"F6.opPattern","COPY",BODY,{"derivedFrom":makeQuery(id+"F2.opPattern","COPY",BODY,{"derivedFrom":makeQuery(id+"F1.opExtrude","SWEPT_BODY",BODY,{"disambiguationData":[OSD([sQuery(id+"F0.wireOp",EDGE,"E0.bottom"),sQuery(id+"F0.wireOp",EDGE,"E0.top"),sQuery(id+"F0.wireOp",EDGE,"E0.left"),sQuery(id+"F0.wireOp",EDGE,"E0.right")])]}),"instanceName":"1"}),"instanceName":"1"}),"instanceName":"1"});
            var Q17;
            Q17=makeQuery(id+"F7.opPattern","COPY",BODY,{"derivedFrom":makeQuery(id+"F6.opPattern","COPY",BODY,{"derivedFrom":makeQuery(id+"F3.opPattern","COPY",BODY,{"derivedFrom":makeQuery(id+"F1.opExtrude","SWEPT_BODY",BODY,{"disambiguationData":[OSD([sQuery(id+"F0.wireOp",EDGE,"E0.bottom"),sQuery(id+"F0.wireOp",EDGE,"E0.top"),sQuery(id+"F0.wireOp",EDGE,"E0.left"),sQuery(id+"F0.wireOp",EDGE,"E0.right")])]}),"instanceName":"1"}),"instanceName":"1"}),"instanceName":"1"});
            var Q18;
            Q18=makeQuery(id+"F7.opPattern","COPY",BODY,{"derivedFrom":makeQuery(id+"F6.opPattern","COPY",BODY,{"derivedFrom":makeQuery(id+"F3.opPattern","COPY",BODY,{"derivedFrom":makeQuery(id+"F2.opPattern","COPY",BODY,{"derivedFrom":makeQuery(id+"F1.opExtrude","SWEPT_BODY",BODY,{"disambiguationData":[OSD([sQuery(id+"F0.wireOp",EDGE,"E0.bottom"),sQuery(id+"F0.wireOp",EDGE,"E0.top"),sQuery(id+"F0.wireOp",EDGE,"E0.left"),sQuery(id+"F0.wireOp",EDGE,"E0.right")])]}),"instanceName":"1"}),"instanceName":"1"}),"instanceName":"1"}),"instanceName":"1"});
            var Q19;
            Q19=makeQuery(id+"F7.opPattern","COPY",BODY,{"derivedFrom":makeQuery(id+"F6.opPattern","COPY",BODY,{"derivedFrom":makeQuery(id+"F4.opPattern","COPY",BODY,{"derivedFrom":makeQuery(id+"F1.opExtrude","SWEPT_BODY",BODY,{"disambiguationData":[OSD([sQuery(id+"F0.wireOp",EDGE,"E0.bottom"),sQuery(id+"F0.wireOp",EDGE,"E0.top"),sQuery(id+"F0.wireOp",EDGE,"E0.left"),sQuery(id+"F0.wireOp",EDGE,"E0.right")])]}),"instanceName":"1"}),"instanceName":"1"}),"instanceName":"1"});
            var Q20;
            Q20=makeQuery(id+"F7.opPattern","COPY",BODY,{"derivedFrom":makeQuery(id+"F6.opPattern","COPY",BODY,{"derivedFrom":makeQuery(id+"F4.opPattern","COPY",BODY,{"derivedFrom":makeQuery(id+"F2.opPattern","COPY",BODY,{"derivedFrom":makeQuery(id+"F1.opExtrude","SWEPT_BODY",BODY,{"disambiguationData":[OSD([sQuery(id+"F0.wireOp",EDGE,"E0.bottom"),sQuery(id+"F0.wireOp",EDGE,"E0.top"),sQuery(id+"F0.wireOp",EDGE,"E0.left"),sQuery(id+"F0.wireOp",EDGE,"E0.right")])]}),"instanceName":"1"}),"instanceName":"1"}),"instanceName":"1"}),"instanceName":"1"});
            var Q21;
            Q21=makeQuery(id+"F7.opPattern","COPY",BODY,{"derivedFrom":makeQuery(id+"F6.opPattern","COPY",BODY,{"derivedFrom":makeQuery(id+"F4.opPattern","COPY",BODY,{"derivedFrom":makeQuery(id+"F3.opPattern","COPY",BODY,{"derivedFrom":makeQuery(id+"F1.opExtrude","SWEPT_BODY",BODY,{"disambiguationData":[OSD([sQuery(id+"F0.wireOp",EDGE,"E0.bottom"),sQuery(id+"F0.wireOp",EDGE,"E0.top"),sQuery(id+"F0.wireOp",EDGE,"E0.left"),sQuery(id+"F0.wireOp",EDGE,"E0.right")])]}),"instanceName":"1"}),"instanceName":"1"}),"instanceName":"1"}),"instanceName":"1"});
            var Q22;
            Q22=makeQuery(id+"F7.opPattern","COPY",BODY,{"derivedFrom":makeQuery(id+"F6.opPattern","COPY",BODY,{"derivedFrom":makeQuery(id+"F4.opPattern","COPY",BODY,{"derivedFrom":makeQuery(id+"F3.opPattern","COPY",BODY,{"derivedFrom":makeQuery(id+"F2.opPattern","COPY",BODY,{"derivedFrom":makeQuery(id+"F1.opExtrude","SWEPT_BODY",BODY,{"disambiguationData":[OSD([sQuery(id+"F0.wireOp",EDGE,"E0.bottom"),sQuery(id+"F0.wireOp",EDGE,"E0.top"),sQuery(id+"F0.wireOp",EDGE,"E0.left"),sQuery(id+"F0.wireOp",EDGE,"E0.right")])]}),"instanceName":"1"}),"instanceName":"1"}),"instanceName":"1"}),"instanceName":"1"}),"instanceName":"1"});
            var Q23;
            Q23=makeQuery(id+"F7.opPattern","COPY",BODY,{"derivedFrom":makeQuery(id+"F6.opPattern","COPY",BODY,{"derivedFrom":makeQuery(id+"F5.opPattern","COPY",BODY,{"derivedFrom":makeQuery(id+"F1.opExtrude","SWEPT_BODY",BODY,{"disambiguationData":[OSD([sQuery(id+"F0.wireOp",EDGE,"E0.bottom"),sQuery(id+"F0.wireOp",EDGE,"E0.top"),sQuery(id+"F0.wireOp",EDGE,"E0.left"),sQuery(id+"F0.wireOp",EDGE,"E0.right")])]}),"instanceName":"1"}),"instanceName":"1"}),"instanceName":"1"});
            var Q24;
            Q24=makeQuery(id+"F7.opPattern","COPY",BODY,{"derivedFrom":makeQuery(id+"F6.opPattern","COPY",BODY,{"derivedFrom":makeQuery(id+"F5.opPattern","COPY",BODY,{"derivedFrom":makeQuery(id+"F2.opPattern","COPY",BODY,{"derivedFrom":makeQuery(id+"F1.opExtrude","SWEPT_BODY",BODY,{"disambiguationData":[OSD([sQuery(id+"F0.wireOp",EDGE,"E0.bottom"),sQuery(id+"F0.wireOp",EDGE,"E0.top"),sQuery(id+"F0.wireOp",EDGE,"E0.left"),sQuery(id+"F0.wireOp",EDGE,"E0.right")])]}),"instanceName":"1"}),"instanceName":"1"}),"instanceName":"1"}),"instanceName":"1"});
            var Q25;
            Q25=makeQuery(id+"F7.opPattern","COPY",BODY,{"derivedFrom":makeQuery(id+"F6.opPattern","COPY",BODY,{"derivedFrom":makeQuery(id+"F5.opPattern","COPY",BODY,{"derivedFrom":makeQuery(id+"F3.opPattern","COPY",BODY,{"derivedFrom":makeQuery(id+"F1.opExtrude","SWEPT_BODY",BODY,{"disambiguationData":[OSD([sQuery(id+"F0.wireOp",EDGE,"E0.bottom"),sQuery(id+"F0.wireOp",EDGE,"E0.top"),sQuery(id+"F0.wireOp",EDGE,"E0.left"),sQuery(id+"F0.wireOp",EDGE,"E0.right")])]}),"instanceName":"1"}),"instanceName":"1"}),"instanceName":"1"}),"instanceName":"1"});
            var Q26;
            Q26=makeQuery(id+"F7.opPattern","COPY",BODY,{"derivedFrom":makeQuery(id+"F6.opPattern","COPY",BODY,{"derivedFrom":makeQuery(id+"F5.opPattern","COPY",BODY,{"derivedFrom":makeQuery(id+"F3.opPattern","COPY",BODY,{"derivedFrom":makeQuery(id+"F2.opPattern","COPY",BODY,{"derivedFrom":makeQuery(id+"F1.opExtrude","SWEPT_BODY",BODY,{"disambiguationData":[OSD([sQuery(id+"F0.wireOp",EDGE,"E0.bottom"),sQuery(id+"F0.wireOp",EDGE,"E0.top"),sQuery(id+"F0.wireOp",EDGE,"E0.left"),sQuery(id+"F0.wireOp",EDGE,"E0.right")])]}),"instanceName":"1"}),"instanceName":"1"}),"instanceName":"1"}),"instanceName":"1"}),"instanceName":"1"});
            var Q27;
            Q27=makeQuery(id+"F7.opPattern","COPY",BODY,{"derivedFrom":makeQuery(id+"F6.opPattern","COPY",BODY,{"derivedFrom":makeQuery(id+"F5.opPattern","COPY",BODY,{"derivedFrom":makeQuery(id+"F4.opPattern","COPY",BODY,{"derivedFrom":makeQuery(id+"F1.opExtrude","SWEPT_BODY",BODY,{"disambiguationData":[OSD([sQuery(id+"F0.wireOp",EDGE,"E0.bottom"),sQuery(id+"F0.wireOp",EDGE,"E0.top"),sQuery(id+"F0.wireOp",EDGE,"E0.left"),sQuery(id+"F0.wireOp",EDGE,"E0.right")])]}),"instanceName":"1"}),"instanceName":"1"}),"instanceName":"1"}),"instanceName":"1"});
            var Q28;
            Q28=makeQuery(id+"F7.opPattern","COPY",BODY,{"derivedFrom":makeQuery(id+"F6.opPattern","COPY",BODY,{"derivedFrom":makeQuery(id+"F5.opPattern","COPY",BODY,{"derivedFrom":makeQuery(id+"F4.opPattern","COPY",BODY,{"derivedFrom":makeQuery(id+"F2.opPattern","COPY",BODY,{"derivedFrom":makeQuery(id+"F1.opExtrude","SWEPT_BODY",BODY,{"disambiguationData":[OSD([sQuery(id+"F0.wireOp",EDGE,"E0.bottom"),sQuery(id+"F0.wireOp",EDGE,"E0.top"),sQuery(id+"F0.wireOp",EDGE,"E0.left"),sQuery(id+"F0.wireOp",EDGE,"E0.right")])]}),"instanceName":"1"}),"instanceName":"1"}),"instanceName":"1"}),"instanceName":"1"}),"instanceName":"1"});
            var Q29;
            Q29=makeQuery(id+"F7.opPattern","COPY",BODY,{"derivedFrom":makeQuery(id+"F6.opPattern","COPY",BODY,{"derivedFrom":makeQuery(id+"F5.opPattern","COPY",BODY,{"derivedFrom":makeQuery(id+"F4.opPattern","COPY",BODY,{"derivedFrom":makeQuery(id+"F3.opPattern","COPY",BODY,{"derivedFrom":makeQuery(id+"F1.opExtrude","SWEPT_BODY",BODY,{"disambiguationData":[OSD([sQuery(id+"F0.wireOp",EDGE,"E0.bottom"),sQuery(id+"F0.wireOp",EDGE,"E0.top"),sQuery(id+"F0.wireOp",EDGE,"E0.left"),sQuery(id+"F0.wireOp",EDGE,"E0.right")])]}),"instanceName":"1"}),"instanceName":"1"}),"instanceName":"1"}),"instanceName":"1"}),"instanceName":"1"});
            var Q30;
            Q30=makeQuery(id+"F7.opPattern","COPY",BODY,{"derivedFrom":makeQuery(id+"F6.opPattern","COPY",BODY,{"derivedFrom":makeQuery(id+"F5.opPattern","COPY",BODY,{"derivedFrom":makeQuery(id+"F4.opPattern","COPY",BODY,{"derivedFrom":makeQuery(id+"F3.opPattern","COPY",BODY,{"derivedFrom":makeQuery(id+"F2.opPattern","COPY",BODY,{"derivedFrom":makeQuery(id+"F1.opExtrude","SWEPT_BODY",BODY,{"disambiguationData":[OSD([sQuery(id+"F0.wireOp",EDGE,"E0.bottom"),sQuery(id+"F0.wireOp",EDGE,"E0.top"),sQuery(id+"F0.wireOp",EDGE,"E0.left"),sQuery(id+"F0.wireOp",EDGE,"E0.right")])]}),"instanceName":"1"}),"instanceName":"1"}),"instanceName":"1"}),"instanceName":"1"}),"instanceName":"1"}),"instanceName":"1"});
            var Q31;
            Q31=makeQuery(id+"F7.opPattern","COPY",BODY,{"derivedFrom":makeQuery(id+"F1.opExtrude","SWEPT_BODY",BODY,{"disambiguationData":[OSD([sQuery(id+"F0.wireOp",EDGE,"E0.bottom"),sQuery(id+"F0.wireOp",EDGE,"E0.top"),sQuery(id+"F0.wireOp",EDGE,"E0.left"),sQuery(id+"F0.wireOp",EDGE,"E0.right")])]}),"instanceName":"1"});
            transform(context, id + "F8", {"entities" : qUnion([Q0, Q1, Q2, Q3, Q4, Q5, Q6, Q7, Q8, Q9, Q10, Q11, Q12, Q13, Q14, Q15, Q16, Q17, Q18, Q19, Q20, Q21, Q22, Q23, Q24, Q25, Q26, Q27, Q28, Q29, Q30, Q31]), "transformType" : TransformType.TRANSLATION_3D, "dx" : -1000 * mm, "dy" : 0 * mm, "dz" : 0 * mm, "makeCopy" : false});
        }
        {
            var Q0;
            Q0=makeQuery(id+"F7.opPattern","COPY",BODY,{"derivedFrom":makeQuery(id+"F1.opExtrude","SWEPT_BODY",BODY,{"disambiguationData":[OSD([sQuery(id+"F0.wireOp",EDGE,"E0.bottom"),sQuery(id+"F0.wireOp",EDGE,"E0.top"),sQuery(id+"F0.wireOp",EDGE,"E0.left"),sQuery(id+"F0.wireOp",EDGE,"E0.right")])]}),"instanceName":"1"});
            var Q1;
            Q1=makeQuery(id+"F7.opPattern","COPY",BODY,{"derivedFrom":makeQuery(id+"F2.opPattern","COPY",BODY,{"derivedFrom":makeQuery(id+"F1.opExtrude","SWEPT_BODY",BODY,{"disambiguationData":[OSD([sQuery(id+"F0.wireOp",EDGE,"E0.bottom"),sQuery(id+"F0.wireOp",EDGE,"E0.top"),sQuery(id+"F0.wireOp",EDGE,"E0.left"),sQuery(id+"F0.wireOp",EDGE,"E0.right")])]}),"instanceName":"1"}),"instanceName":"1"});
            var Q2;
            Q2=makeQuery(id+"F7.opPattern","COPY",BODY,{"derivedFrom":makeQuery(id+"F3.opPattern","COPY",BODY,{"derivedFrom":makeQuery(id+"F1.opExtrude","SWEPT_BODY",BODY,{"disambiguationData":[OSD([sQuery(id+"F0.wireOp",EDGE,"E0.bottom"),sQuery(id+"F0.wireOp",EDGE,"E0.top"),sQuery(id+"F0.wireOp",EDGE,"E0.left"),sQuery(id+"F0.wireOp",EDGE,"E0.right")])]}),"instanceName":"1"}),"instanceName":"1"});
            var Q3;
            Q3=makeQuery(id+"F7.opPattern","COPY",BODY,{"derivedFrom":makeQuery(id+"F3.opPattern","COPY",BODY,{"derivedFrom":makeQuery(id+"F2.opPattern","COPY",BODY,{"derivedFrom":makeQuery(id+"F1.opExtrude","SWEPT_BODY",BODY,{"disambiguationData":[OSD([sQuery(id+"F0.wireOp",EDGE,"E0.bottom"),sQuery(id+"F0.wireOp",EDGE,"E0.top"),sQuery(id+"F0.wireOp",EDGE,"E0.left"),sQuery(id+"F0.wireOp",EDGE,"E0.right")])]}),"instanceName":"1"}),"instanceName":"1"}),"instanceName":"1"});
            var Q4;
            Q4=makeQuery(id+"F7.opPattern","COPY",BODY,{"derivedFrom":makeQuery(id+"F4.opPattern","COPY",BODY,{"derivedFrom":makeQuery(id+"F1.opExtrude","SWEPT_BODY",BODY,{"disambiguationData":[OSD([sQuery(id+"F0.wireOp",EDGE,"E0.bottom"),sQuery(id+"F0.wireOp",EDGE,"E0.top"),sQuery(id+"F0.wireOp",EDGE,"E0.left"),sQuery(id+"F0.wireOp",EDGE,"E0.right")])]}),"instanceName":"1"}),"instanceName":"1"});
            var Q5;
            Q5=makeQuery(id+"F7.opPattern","COPY",BODY,{"derivedFrom":makeQuery(id+"F4.opPattern","COPY",BODY,{"derivedFrom":makeQuery(id+"F2.opPattern","COPY",BODY,{"derivedFrom":makeQuery(id+"F1.opExtrude","SWEPT_BODY",BODY,{"disambiguationData":[OSD([sQuery(id+"F0.wireOp",EDGE,"E0.bottom"),sQuery(id+"F0.wireOp",EDGE,"E0.top"),sQuery(id+"F0.wireOp",EDGE,"E0.left"),sQuery(id+"F0.wireOp",EDGE,"E0.right")])]}),"instanceName":"1"}),"instanceName":"1"}),"instanceName":"1"});
            var Q6;
            Q6=makeQuery(id+"F7.opPattern","COPY",BODY,{"derivedFrom":makeQuery(id+"F4.opPattern","COPY",BODY,{"derivedFrom":makeQuery(id+"F3.opPattern","COPY",BODY,{"derivedFrom":makeQuery(id+"F1.opExtrude","SWEPT_BODY",BODY,{"disambiguationData":[OSD([sQuery(id+"F0.wireOp",EDGE,"E0.bottom"),sQuery(id+"F0.wireOp",EDGE,"E0.top"),sQuery(id+"F0.wireOp",EDGE,"E0.left"),sQuery(id+"F0.wireOp",EDGE,"E0.right")])]}),"instanceName":"1"}),"instanceName":"1"}),"instanceName":"1"});
            var Q7;
            Q7=makeQuery(id+"F7.opPattern","COPY",BODY,{"derivedFrom":makeQuery(id+"F4.opPattern","COPY",BODY,{"derivedFrom":makeQuery(id+"F3.opPattern","COPY",BODY,{"derivedFrom":makeQuery(id+"F2.opPattern","COPY",BODY,{"derivedFrom":makeQuery(id+"F1.opExtrude","SWEPT_BODY",BODY,{"disambiguationData":[OSD([sQuery(id+"F0.wireOp",EDGE,"E0.bottom"),sQuery(id+"F0.wireOp",EDGE,"E0.top"),sQuery(id+"F0.wireOp",EDGE,"E0.left"),sQuery(id+"F0.wireOp",EDGE,"E0.right")])]}),"instanceName":"1"}),"instanceName":"1"}),"instanceName":"1"}),"instanceName":"1"});
            var Q8;
            Q8=makeQuery(id+"F7.opPattern","COPY",BODY,{"derivedFrom":makeQuery(id+"F5.opPattern","COPY",BODY,{"derivedFrom":makeQuery(id+"F1.opExtrude","SWEPT_BODY",BODY,{"disambiguationData":[OSD([sQuery(id+"F0.wireOp",EDGE,"E0.bottom"),sQuery(id+"F0.wireOp",EDGE,"E0.top"),sQuery(id+"F0.wireOp",EDGE,"E0.left"),sQuery(id+"F0.wireOp",EDGE,"E0.right")])]}),"instanceName":"1"}),"instanceName":"1"});
            var Q9;
            Q9=makeQuery(id+"F7.opPattern","COPY",BODY,{"derivedFrom":makeQuery(id+"F5.opPattern","COPY",BODY,{"derivedFrom":makeQuery(id+"F2.opPattern","COPY",BODY,{"derivedFrom":makeQuery(id+"F1.opExtrude","SWEPT_BODY",BODY,{"disambiguationData":[OSD([sQuery(id+"F0.wireOp",EDGE,"E0.bottom"),sQuery(id+"F0.wireOp",EDGE,"E0.top"),sQuery(id+"F0.wireOp",EDGE,"E0.left"),sQuery(id+"F0.wireOp",EDGE,"E0.right")])]}),"instanceName":"1"}),"instanceName":"1"}),"instanceName":"1"});
            var Q10;
            Q10=makeQuery(id+"F7.opPattern","COPY",BODY,{"derivedFrom":makeQuery(id+"F5.opPattern","COPY",BODY,{"derivedFrom":makeQuery(id+"F3.opPattern","COPY",BODY,{"derivedFrom":makeQuery(id+"F1.opExtrude","SWEPT_BODY",BODY,{"disambiguationData":[OSD([sQuery(id+"F0.wireOp",EDGE,"E0.bottom"),sQuery(id+"F0.wireOp",EDGE,"E0.top"),sQuery(id+"F0.wireOp",EDGE,"E0.left"),sQuery(id+"F0.wireOp",EDGE,"E0.right")])]}),"instanceName":"1"}),"instanceName":"1"}),"instanceName":"1"});
            var Q11;
            Q11=makeQuery(id+"F7.opPattern","COPY",BODY,{"derivedFrom":makeQuery(id+"F5.opPattern","COPY",BODY,{"derivedFrom":makeQuery(id+"F3.opPattern","COPY",BODY,{"derivedFrom":makeQuery(id+"F2.opPattern","COPY",BODY,{"derivedFrom":makeQuery(id+"F1.opExtrude","SWEPT_BODY",BODY,{"disambiguationData":[OSD([sQuery(id+"F0.wireOp",EDGE,"E0.bottom"),sQuery(id+"F0.wireOp",EDGE,"E0.top"),sQuery(id+"F0.wireOp",EDGE,"E0.left"),sQuery(id+"F0.wireOp",EDGE,"E0.right")])]}),"instanceName":"1"}),"instanceName":"1"}),"instanceName":"1"}),"instanceName":"1"});
            var Q12;
            Q12=makeQuery(id+"F7.opPattern","COPY",BODY,{"derivedFrom":makeQuery(id+"F5.opPattern","COPY",BODY,{"derivedFrom":makeQuery(id+"F4.opPattern","COPY",BODY,{"derivedFrom":makeQuery(id+"F1.opExtrude","SWEPT_BODY",BODY,{"disambiguationData":[OSD([sQuery(id+"F0.wireOp",EDGE,"E0.bottom"),sQuery(id+"F0.wireOp",EDGE,"E0.top"),sQuery(id+"F0.wireOp",EDGE,"E0.left"),sQuery(id+"F0.wireOp",EDGE,"E0.right")])]}),"instanceName":"1"}),"instanceName":"1"}),"instanceName":"1"});
            var Q13;
            Q13=makeQuery(id+"F7.opPattern","COPY",BODY,{"derivedFrom":makeQuery(id+"F5.opPattern","COPY",BODY,{"derivedFrom":makeQuery(id+"F4.opPattern","COPY",BODY,{"derivedFrom":makeQuery(id+"F2.opPattern","COPY",BODY,{"derivedFrom":makeQuery(id+"F1.opExtrude","SWEPT_BODY",BODY,{"disambiguationData":[OSD([sQuery(id+"F0.wireOp",EDGE,"E0.bottom"),sQuery(id+"F0.wireOp",EDGE,"E0.top"),sQuery(id+"F0.wireOp",EDGE,"E0.left"),sQuery(id+"F0.wireOp",EDGE,"E0.right")])]}),"instanceName":"1"}),"instanceName":"1"}),"instanceName":"1"}),"instanceName":"1"});
            var Q14;
            Q14=makeQuery(id+"F7.opPattern","COPY",BODY,{"derivedFrom":makeQuery(id+"F5.opPattern","COPY",BODY,{"derivedFrom":makeQuery(id+"F4.opPattern","COPY",BODY,{"derivedFrom":makeQuery(id+"F3.opPattern","COPY",BODY,{"derivedFrom":makeQuery(id+"F1.opExtrude","SWEPT_BODY",BODY,{"disambiguationData":[OSD([sQuery(id+"F0.wireOp",EDGE,"E0.bottom"),sQuery(id+"F0.wireOp",EDGE,"E0.top"),sQuery(id+"F0.wireOp",EDGE,"E0.left"),sQuery(id+"F0.wireOp",EDGE,"E0.right")])]}),"instanceName":"1"}),"instanceName":"1"}),"instanceName":"1"}),"instanceName":"1"});
            var Q15;
            Q15=makeQuery(id+"F7.opPattern","COPY",BODY,{"derivedFrom":makeQuery(id+"F5.opPattern","COPY",BODY,{"derivedFrom":makeQuery(id+"F4.opPattern","COPY",BODY,{"derivedFrom":makeQuery(id+"F3.opPattern","COPY",BODY,{"derivedFrom":makeQuery(id+"F2.opPattern","COPY",BODY,{"derivedFrom":makeQuery(id+"F1.opExtrude","SWEPT_BODY",BODY,{"disambiguationData":[OSD([sQuery(id+"F0.wireOp",EDGE,"E0.bottom"),sQuery(id+"F0.wireOp",EDGE,"E0.top"),sQuery(id+"F0.wireOp",EDGE,"E0.left"),sQuery(id+"F0.wireOp",EDGE,"E0.right")])]}),"instanceName":"1"}),"instanceName":"1"}),"instanceName":"1"}),"instanceName":"1"}),"instanceName":"1"});
            var Q16;
            Q16=makeQuery(id+"F7.opPattern","COPY",BODY,{"derivedFrom":makeQuery(id+"F6.opPattern","COPY",BODY,{"derivedFrom":makeQuery(id+"F1.opExtrude","SWEPT_BODY",BODY,{"disambiguationData":[OSD([sQuery(id+"F0.wireOp",EDGE,"E0.bottom"),sQuery(id+"F0.wireOp",EDGE,"E0.top"),sQuery(id+"F0.wireOp",EDGE,"E0.left"),sQuery(id+"F0.wireOp",EDGE,"E0.right")])]}),"instanceName":"1"}),"instanceName":"1"});
            var Q17;
            Q17=makeQuery(id+"F7.opPattern","COPY",BODY,{"derivedFrom":makeQuery(id+"F6.opPattern","COPY",BODY,{"derivedFrom":makeQuery(id+"F2.opPattern","COPY",BODY,{"derivedFrom":makeQuery(id+"F1.opExtrude","SWEPT_BODY",BODY,{"disambiguationData":[OSD([sQuery(id+"F0.wireOp",EDGE,"E0.bottom"),sQuery(id+"F0.wireOp",EDGE,"E0.top"),sQuery(id+"F0.wireOp",EDGE,"E0.left"),sQuery(id+"F0.wireOp",EDGE,"E0.right")])]}),"instanceName":"1"}),"instanceName":"1"}),"instanceName":"1"});
            var Q18;
            Q18=makeQuery(id+"F7.opPattern","COPY",BODY,{"derivedFrom":makeQuery(id+"F6.opPattern","COPY",BODY,{"derivedFrom":makeQuery(id+"F3.opPattern","COPY",BODY,{"derivedFrom":makeQuery(id+"F1.opExtrude","SWEPT_BODY",BODY,{"disambiguationData":[OSD([sQuery(id+"F0.wireOp",EDGE,"E0.bottom"),sQuery(id+"F0.wireOp",EDGE,"E0.top"),sQuery(id+"F0.wireOp",EDGE,"E0.left"),sQuery(id+"F0.wireOp",EDGE,"E0.right")])]}),"instanceName":"1"}),"instanceName":"1"}),"instanceName":"1"});
            var Q19;
            Q19=makeQuery(id+"F7.opPattern","COPY",BODY,{"derivedFrom":makeQuery(id+"F6.opPattern","COPY",BODY,{"derivedFrom":makeQuery(id+"F3.opPattern","COPY",BODY,{"derivedFrom":makeQuery(id+"F2.opPattern","COPY",BODY,{"derivedFrom":makeQuery(id+"F1.opExtrude","SWEPT_BODY",BODY,{"disambiguationData":[OSD([sQuery(id+"F0.wireOp",EDGE,"E0.bottom"),sQuery(id+"F0.wireOp",EDGE,"E0.top"),sQuery(id+"F0.wireOp",EDGE,"E0.left"),sQuery(id+"F0.wireOp",EDGE,"E0.right")])]}),"instanceName":"1"}),"instanceName":"1"}),"instanceName":"1"}),"instanceName":"1"});
            var Q20;
            Q20=makeQuery(id+"F7.opPattern","COPY",BODY,{"derivedFrom":makeQuery(id+"F6.opPattern","COPY",BODY,{"derivedFrom":makeQuery(id+"F4.opPattern","COPY",BODY,{"derivedFrom":makeQuery(id+"F1.opExtrude","SWEPT_BODY",BODY,{"disambiguationData":[OSD([sQuery(id+"F0.wireOp",EDGE,"E0.bottom"),sQuery(id+"F0.wireOp",EDGE,"E0.top"),sQuery(id+"F0.wireOp",EDGE,"E0.left"),sQuery(id+"F0.wireOp",EDGE,"E0.right")])]}),"instanceName":"1"}),"instanceName":"1"}),"instanceName":"1"});
            var Q21;
            Q21=makeQuery(id+"F7.opPattern","COPY",BODY,{"derivedFrom":makeQuery(id+"F6.opPattern","COPY",BODY,{"derivedFrom":makeQuery(id+"F4.opPattern","COPY",BODY,{"derivedFrom":makeQuery(id+"F2.opPattern","COPY",BODY,{"derivedFrom":makeQuery(id+"F1.opExtrude","SWEPT_BODY",BODY,{"disambiguationData":[OSD([sQuery(id+"F0.wireOp",EDGE,"E0.bottom"),sQuery(id+"F0.wireOp",EDGE,"E0.top"),sQuery(id+"F0.wireOp",EDGE,"E0.left"),sQuery(id+"F0.wireOp",EDGE,"E0.right")])]}),"instanceName":"1"}),"instanceName":"1"}),"instanceName":"1"}),"instanceName":"1"});
            var Q22;
            Q22=makeQuery(id+"F7.opPattern","COPY",BODY,{"derivedFrom":makeQuery(id+"F6.opPattern","COPY",BODY,{"derivedFrom":makeQuery(id+"F4.opPattern","COPY",BODY,{"derivedFrom":makeQuery(id+"F3.opPattern","COPY",BODY,{"derivedFrom":makeQuery(id+"F1.opExtrude","SWEPT_BODY",BODY,{"disambiguationData":[OSD([sQuery(id+"F0.wireOp",EDGE,"E0.bottom"),sQuery(id+"F0.wireOp",EDGE,"E0.top"),sQuery(id+"F0.wireOp",EDGE,"E0.left"),sQuery(id+"F0.wireOp",EDGE,"E0.right")])]}),"instanceName":"1"}),"instanceName":"1"}),"instanceName":"1"}),"instanceName":"1"});
            var Q23;
            Q23=makeQuery(id+"F7.opPattern","COPY",BODY,{"derivedFrom":makeQuery(id+"F6.opPattern","COPY",BODY,{"derivedFrom":makeQuery(id+"F4.opPattern","COPY",BODY,{"derivedFrom":makeQuery(id+"F3.opPattern","COPY",BODY,{"derivedFrom":makeQuery(id+"F2.opPattern","COPY",BODY,{"derivedFrom":makeQuery(id+"F1.opExtrude","SWEPT_BODY",BODY,{"disambiguationData":[OSD([sQuery(id+"F0.wireOp",EDGE,"E0.bottom"),sQuery(id+"F0.wireOp",EDGE,"E0.top"),sQuery(id+"F0.wireOp",EDGE,"E0.left"),sQuery(id+"F0.wireOp",EDGE,"E0.right")])]}),"instanceName":"1"}),"instanceName":"1"}),"instanceName":"1"}),"instanceName":"1"}),"instanceName":"1"});
            var Q24;
            Q24=makeQuery(id+"F7.opPattern","COPY",BODY,{"derivedFrom":makeQuery(id+"F6.opPattern","COPY",BODY,{"derivedFrom":makeQuery(id+"F5.opPattern","COPY",BODY,{"derivedFrom":makeQuery(id+"F1.opExtrude","SWEPT_BODY",BODY,{"disambiguationData":[OSD([sQuery(id+"F0.wireOp",EDGE,"E0.bottom"),sQuery(id+"F0.wireOp",EDGE,"E0.top"),sQuery(id+"F0.wireOp",EDGE,"E0.left"),sQuery(id+"F0.wireOp",EDGE,"E0.right")])]}),"instanceName":"1"}),"instanceName":"1"}),"instanceName":"1"});
            var Q25;
            Q25=makeQuery(id+"F7.opPattern","COPY",BODY,{"derivedFrom":makeQuery(id+"F6.opPattern","COPY",BODY,{"derivedFrom":makeQuery(id+"F5.opPattern","COPY",BODY,{"derivedFrom":makeQuery(id+"F2.opPattern","COPY",BODY,{"derivedFrom":makeQuery(id+"F1.opExtrude","SWEPT_BODY",BODY,{"disambiguationData":[OSD([sQuery(id+"F0.wireOp",EDGE,"E0.bottom"),sQuery(id+"F0.wireOp",EDGE,"E0.top"),sQuery(id+"F0.wireOp",EDGE,"E0.left"),sQuery(id+"F0.wireOp",EDGE,"E0.right")])]}),"instanceName":"1"}),"instanceName":"1"}),"instanceName":"1"}),"instanceName":"1"});
            var Q26;
            Q26=makeQuery(id+"F7.opPattern","COPY",BODY,{"derivedFrom":makeQuery(id+"F6.opPattern","COPY",BODY,{"derivedFrom":makeQuery(id+"F5.opPattern","COPY",BODY,{"derivedFrom":makeQuery(id+"F3.opPattern","COPY",BODY,{"derivedFrom":makeQuery(id+"F1.opExtrude","SWEPT_BODY",BODY,{"disambiguationData":[OSD([sQuery(id+"F0.wireOp",EDGE,"E0.bottom"),sQuery(id+"F0.wireOp",EDGE,"E0.top"),sQuery(id+"F0.wireOp",EDGE,"E0.left"),sQuery(id+"F0.wireOp",EDGE,"E0.right")])]}),"instanceName":"1"}),"instanceName":"1"}),"instanceName":"1"}),"instanceName":"1"});
            var Q27;
            Q27=makeQuery(id+"F7.opPattern","COPY",BODY,{"derivedFrom":makeQuery(id+"F6.opPattern","COPY",BODY,{"derivedFrom":makeQuery(id+"F5.opPattern","COPY",BODY,{"derivedFrom":makeQuery(id+"F3.opPattern","COPY",BODY,{"derivedFrom":makeQuery(id+"F2.opPattern","COPY",BODY,{"derivedFrom":makeQuery(id+"F1.opExtrude","SWEPT_BODY",BODY,{"disambiguationData":[OSD([sQuery(id+"F0.wireOp",EDGE,"E0.bottom"),sQuery(id+"F0.wireOp",EDGE,"E0.top"),sQuery(id+"F0.wireOp",EDGE,"E0.left"),sQuery(id+"F0.wireOp",EDGE,"E0.right")])]}),"instanceName":"1"}),"instanceName":"1"}),"instanceName":"1"}),"instanceName":"1"}),"instanceName":"1"});
            var Q28;
            Q28=makeQuery(id+"F7.opPattern","COPY",BODY,{"derivedFrom":makeQuery(id+"F6.opPattern","COPY",BODY,{"derivedFrom":makeQuery(id+"F5.opPattern","COPY",BODY,{"derivedFrom":makeQuery(id+"F4.opPattern","COPY",BODY,{"derivedFrom":makeQuery(id+"F1.opExtrude","SWEPT_BODY",BODY,{"disambiguationData":[OSD([sQuery(id+"F0.wireOp",EDGE,"E0.bottom"),sQuery(id+"F0.wireOp",EDGE,"E0.top"),sQuery(id+"F0.wireOp",EDGE,"E0.left"),sQuery(id+"F0.wireOp",EDGE,"E0.right")])]}),"instanceName":"1"}),"instanceName":"1"}),"instanceName":"1"}),"instanceName":"1"});
            var Q29;
            Q29=makeQuery(id+"F7.opPattern","COPY",BODY,{"derivedFrom":makeQuery(id+"F6.opPattern","COPY",BODY,{"derivedFrom":makeQuery(id+"F5.opPattern","COPY",BODY,{"derivedFrom":makeQuery(id+"F4.opPattern","COPY",BODY,{"derivedFrom":makeQuery(id+"F2.opPattern","COPY",BODY,{"derivedFrom":makeQuery(id+"F1.opExtrude","SWEPT_BODY",BODY,{"disambiguationData":[OSD([sQuery(id+"F0.wireOp",EDGE,"E0.bottom"),sQuery(id+"F0.wireOp",EDGE,"E0.top"),sQuery(id+"F0.wireOp",EDGE,"E0.left"),sQuery(id+"F0.wireOp",EDGE,"E0.right")])]}),"instanceName":"1"}),"instanceName":"1"}),"instanceName":"1"}),"instanceName":"1"}),"instanceName":"1"});
            var Q30;
            Q30=makeQuery(id+"F7.opPattern","COPY",BODY,{"derivedFrom":makeQuery(id+"F6.opPattern","COPY",BODY,{"derivedFrom":makeQuery(id+"F5.opPattern","COPY",BODY,{"derivedFrom":makeQuery(id+"F4.opPattern","COPY",BODY,{"derivedFrom":makeQuery(id+"F3.opPattern","COPY",BODY,{"derivedFrom":makeQuery(id+"F1.opExtrude","SWEPT_BODY",BODY,{"disambiguationData":[OSD([sQuery(id+"F0.wireOp",EDGE,"E0.bottom"),sQuery(id+"F0.wireOp",EDGE,"E0.top"),sQuery(id+"F0.wireOp",EDGE,"E0.left"),sQuery(id+"F0.wireOp",EDGE,"E0.right")])]}),"instanceName":"1"}),"instanceName":"1"}),"instanceName":"1"}),"instanceName":"1"}),"instanceName":"1"});
            var Q31;
            Q31=makeQuery(id+"F7.opPattern","COPY",BODY,{"derivedFrom":makeQuery(id+"F6.opPattern","COPY",BODY,{"derivedFrom":makeQuery(id+"F5.opPattern","COPY",BODY,{"derivedFrom":makeQuery(id+"F4.opPattern","COPY",BODY,{"derivedFrom":makeQuery(id+"F3.opPattern","COPY",BODY,{"derivedFrom":makeQuery(id+"F2.opPattern","COPY",BODY,{"derivedFrom":makeQuery(id+"F1.opExtrude","SWEPT_BODY",BODY,{"disambiguationData":[OSD([sQuery(id+"F0.wireOp",EDGE,"E0.bottom"),sQuery(id+"F0.wireOp",EDGE,"E0.top"),sQuery(id+"F0.wireOp",EDGE,"E0.left"),sQuery(id+"F0.wireOp",EDGE,"E0.right")])]}),"instanceName":"1"}),"instanceName":"1"}),"instanceName":"1"}),"instanceName":"1"}),"instanceName":"1"}),"instanceName":"1"});
            transform(context, id + "F9", {"entities" : qUnion([Q0, Q1, Q2, Q3, Q4, Q5, Q6, Q7, Q8, Q9, Q10, Q11, Q12, Q13, Q14, Q15, Q16, Q17, Q18, Q19, Q20, Q21, Q22, Q23, Q24, Q25, Q26, Q27, Q28, Q29, Q30, Q31]), "transformType" : TransformType.TRANSLATION_3D, "dx" : -240 * mm, "dy" : 0 * mm, "dz" : 0 * mm, "makeCopy" : false});
        }
        {
            var Q0;
            Q0=qCreatedBy(makeId("Front.planeOp"),FACE);
            var sketch = newSketch(context, id + "F10", { "sketchPlane" : qUnion([Q0])});
            skLineSegment(sketch, "E1", {"start": v(0, 0) * mm, "end": v(-78.09, 0) * mm});
            skLineSegment(sketch, "E2", {"start": v(-78.09, 0) * mm, "end": v(-78.09, -6) * mm});
            skLineSegment(sketch, "E3", {"start": v(-78.09, -6) * mm, "end": v(-41.83, -6) * mm});
            skLineSegment(sketch, "E4", {"start": v(-41.83, -6) * mm, "end": v(-41.83, -83) * mm});
            skLineSegment(sketch, "E5", {"start": v(-41.83, -83) * mm, "end": v(-78.09, -83) * mm});
            skLineSegment(sketch, "E6", {"start": v(-78.09, -83) * mm, "end": v(-78.09, -89) * mm});
            skLineSegment(sketch, "E7", {"start": v(-78.09, -89) * mm, "end": v(0, -89) * mm});
            skLineSegment(sketch, "E8", {"start": v(0, -89) * mm, "end": v(0, -83) * mm});
            skLineSegment(sketch, "E9", {"start": v(0, -83) * mm, "end": v(-36.26, -83) * mm});
            skLineSegment(sketch, "E10", {"start": v(-36.26, -83) * mm, "end": v(-36.26, -6) * mm});
            skLineSegment(sketch, "E11", {"start": v(-36.26, -6) * mm, "end": v(0, -6) * mm});
            skLineSegment(sketch, "E12", {"start": v(0, -6) * mm, "end": v(0, 0) * mm});
            skSolve(sketch);
        }
        {
            var Q0;
            Q0 = qSketchRegion(id + "F10", true);
            extrude(context, id + "F11", {"entities" : qUnion([Q0]), "oppositeDirection" : true, "depth" : 1250 * mm});
        }
        {
            var Q0;
            Q0=makeQuery(id+"F11.opExtrude","SWEPT_BODY",BODY,{"disambiguationData":[OSD([sQuery(id+"F10.wireOp",EDGE,"E1"),sQuery(id+"F10.wireOp",EDGE,"E2"),sQuery(id+"F10.wireOp",EDGE,"E3"),sQuery(id+"F10.wireOp",EDGE,"E4"),sQuery(id+"F10.wireOp",EDGE,"E5"),sQuery(id+"F10.wireOp",EDGE,"E6"),sQuery(id+"F10.wireOp",EDGE,"E7"),sQuery(id+"F10.wireOp",EDGE,"E8"),sQuery(id+"F10.wireOp",EDGE,"E9"),sQuery(id+"F10.wireOp",EDGE,"E10"),sQuery(id+"F10.wireOp",EDGE,"E11"),sQuery(id+"F10.wireOp",EDGE,"E12")])]});
            transform(context, id + "F12", {"entities" : qUnion([Q0]), "transformType" : TransformType.TRANSLATION_3D, "dx" : -550 * mm, "dy" : 0 * mm, "dz" : 0 * mm, "makeCopy" : true});
        }
        {
            var Q0;
            Q0=makeQuery(id+"F12.opPattern","COPY",BODY,{"derivedFrom":makeQuery(id+"F11.opExtrude","SWEPT_BODY",BODY,{"disambiguationData":[OSD([sQuery(id+"F10.wireOp",EDGE,"E1"),sQuery(id+"F10.wireOp",EDGE,"E2"),sQuery(id+"F10.wireOp",EDGE,"E3"),sQuery(id+"F10.wireOp",EDGE,"E4"),sQuery(id+"F10.wireOp",EDGE,"E5"),sQuery(id+"F10.wireOp",EDGE,"E6"),sQuery(id+"F10.wireOp",EDGE,"E7"),sQuery(id+"F10.wireOp",EDGE,"E8"),sQuery(id+"F10.wireOp",EDGE,"E9"),sQuery(id+"F10.wireOp",EDGE,"E10"),sQuery(id+"F10.wireOp",EDGE,"E11"),sQuery(id+"F10.wireOp",EDGE,"E12")])]}),"instanceName":"1"});
            transform(context, id + "F13", {"entities" : qUnion([Q0]), "transformType" : TransformType.TRANSLATION_3D, "dx" : -550 * mm, "dy" : 0 * mm, "dz" : 0 * mm, "makeCopy" : true});
        }
        {
            var Q0;
            Q0=qCreatedBy(makeId("Top.planeOp"),FACE);
            cPlane(context, id + "F14", {"entities" : qUnion([Q0]), "cplaneType" : CPlaneType.OFFSET, "offset" : 30 * mm, "width" : 150 * mm, "height" : 150 * mm});
        }
        {
            var Q0;
            Q0=qCreatedBy(id+"F14.planeOp",FACE);
            var sketch = newSketch(context, id + "F15", { "sketchPlane" : qUnion([Q0])});
            skLineSegment(sketch, "E13.bottom", {"start": v(-31.5, 18.5) * mm, "end": v(-21.5, 18.5) * mm});
            skLineSegment(sketch, "E13.top", {"start": v(-31.5, 8.5) * mm, "end": v(-21.5, 8.5) * mm});
            skLineSegment(sketch, "E13.left", {"start": v(-31.5, 18.5) * mm, "end": v(-31.5, 8.5) * mm});
            skLineSegment(sketch, "E13.right", {"start": v(-21.5, 18.5) * mm, "end": v(-21.5, 8.5) * mm});
            skLineSegment(sketch, "E14.bottom", {"start": v(-35, 40) * mm, "end": v(0, 40) * mm});
            skLineSegment(sketch, "E14.top", {"start": v(-35, 5) * mm, "end": v(0, 5) * mm});
            skLineSegment(sketch, "E14.left", {"start": v(-35, 40) * mm, "end": v(-35, 5) * mm});
            skLineSegment(sketch, "E14.right", {"start": v(0, 40) * mm, "end": v(0, 5) * mm});
            skLineSegment(sketch, "E15.MirrorCS", {"start": v(-3.5, 18.5) * mm, "end": v(-3.5, 8.5) * mm});
            skLineSegment(sketch, "E16.MirrorCS", {"start": v(-13.5, 18.5) * mm, "end": v(-13.5, 8.5) * mm});
            skLineSegment(sketch, "E17.MirrorCS", {"start": v(-3.5, 18.5) * mm, "end": v(-13.5, 18.5) * mm});
            skLineSegment(sketch, "E18.MirrorCS", {"start": v(-3.5, 8.5) * mm, "end": v(-13.5, 8.5) * mm});
            skLineSegment(sketch, "E19.MirrorCS", {"start": v(-31.5, 26.5) * mm, "end": v(-21.5, 26.5) * mm});
            skLineSegment(sketch, "E20.MirrorCS", {"start": v(-31.5, 26.5) * mm, "end": v(-31.5, 36.5) * mm});
            skLineSegment(sketch, "E21.MirrorCS", {"start": v(-31.5, 36.5) * mm, "end": v(-21.5, 36.5) * mm});
            skLineSegment(sketch, "E22.MirrorCS", {"start": v(-21.5, 26.5) * mm, "end": v(-21.5, 36.5) * mm});
            skLineSegment(sketch, "E23.MirrorCS", {"start": v(-3.5, 36.5) * mm, "end": v(-13.5, 36.5) * mm});
            skLineSegment(sketch, "E24.MirrorCS", {"start": v(-3.5, 26.5) * mm, "end": v(-3.5, 36.5) * mm});
            skLineSegment(sketch, "E25.MirrorCS", {"start": v(-13.5, 26.5) * mm, "end": v(-13.5, 36.5) * mm});
            skLineSegment(sketch, "E26.MirrorCS", {"start": v(-3.5, 26.5) * mm, "end": v(-13.5, 26.5) * mm});
            skSolve(sketch);
        }
        {
            var Q0;
            Q0 = qSketchRegion(id + "F15", true);
            extrude(context, id + "F16", {"entities" : qUnion([Q0]), "depth" : 8 * mm});
        }
        {
            var Q0;
            Q0=makeQuery(id+"F16.opExtrude","SWEPT_BODY",BODY,{"disambiguationData":[OSD([sQuery(id+"F15.wireOp",EDGE,"E13.bottom"),sQuery(id+"F15.wireOp",EDGE,"E13.top"),sQuery(id+"F15.wireOp",EDGE,"E13.left"),sQuery(id+"F15.wireOp",EDGE,"E13.right"),sQuery(id+"F15.wireOp",EDGE,"E14.bottom"),sQuery(id+"F15.wireOp",EDGE,"E14.top"),sQuery(id+"F15.wireOp",EDGE,"E14.left"),sQuery(id+"F15.wireOp",EDGE,"E14.right"),sQuery(id+"F15.wireOp",EDGE,"E15.MirrorCS"),sQuery(id+"F15.wireOp",EDGE,"E16.MirrorCS"),sQuery(id+"F15.wireOp",EDGE,"E17.MirrorCS"),sQuery(id+"F15.wireOp",EDGE,"E18.MirrorCS"),sQuery(id+"F15.wireOp",EDGE,"E19.MirrorCS"),sQuery(id+"F15.wireOp",EDGE,"E20.MirrorCS"),sQuery(id+"F15.wireOp",EDGE,"E21.MirrorCS"),sQuery(id+"F15.wireOp",EDGE,"E22.MirrorCS"),sQuery(id+"F15.wireOp",EDGE,"E23.MirrorCS"),sQuery(id+"F15.wireOp",EDGE,"E24.MirrorCS"),sQuery(id+"F15.wireOp",EDGE,"E25.MirrorCS"),sQuery(id+"F15.wireOp",EDGE,"E26.MirrorCS")])]});
            transform(context, id + "F17", {"entities" : qUnion([Q0]), "transformType" : TransformType.TRANSLATION_3D, "dx" : 0 * mm, "dy" : 40 * mm, "dz" : 0 * mm, "makeCopy" : true});
        }
        {
            var Q0;
            Q0=makeQuery(id+"F17.opPattern","COPY",BODY,{"derivedFrom":makeQuery(id+"F16.opExtrude","SWEPT_BODY",BODY,{"disambiguationData":[OSD([sQuery(id+"F15.wireOp",EDGE,"E13.bottom"),sQuery(id+"F15.wireOp",EDGE,"E13.top"),sQuery(id+"F15.wireOp",EDGE,"E13.left"),sQuery(id+"F15.wireOp",EDGE,"E13.right"),sQuery(id+"F15.wireOp",EDGE,"E14.bottom"),sQuery(id+"F15.wireOp",EDGE,"E14.top"),sQuery(id+"F15.wireOp",EDGE,"E14.left"),sQuery(id+"F15.wireOp",EDGE,"E14.right"),sQuery(id+"F15.wireOp",EDGE,"E15.MirrorCS"),sQuery(id+"F15.wireOp",EDGE,"E16.MirrorCS"),sQuery(id+"F15.wireOp",EDGE,"E17.MirrorCS"),sQuery(id+"F15.wireOp",EDGE,"E18.MirrorCS"),sQuery(id+"F15.wireOp",EDGE,"E19.MirrorCS"),sQuery(id+"F15.wireOp",EDGE,"E20.MirrorCS"),sQuery(id+"F15.wireOp",EDGE,"E21.MirrorCS"),sQuery(id+"F15.wireOp",EDGE,"E22.MirrorCS"),sQuery(id+"F15.wireOp",EDGE,"E23.MirrorCS"),sQuery(id+"F15.wireOp",EDGE,"E24.MirrorCS"),sQuery(id+"F15.wireOp",EDGE,"E25.MirrorCS"),sQuery(id+"F15.wireOp",EDGE,"E26.MirrorCS")])]}),"instanceName":"1"});
            var Q1;
            Q1=makeQuery(id+"F16.opExtrude","SWEPT_BODY",BODY,{"disambiguationData":[OSD([sQuery(id+"F15.wireOp",EDGE,"E13.bottom"),sQuery(id+"F15.wireOp",EDGE,"E13.top"),sQuery(id+"F15.wireOp",EDGE,"E13.left"),sQuery(id+"F15.wireOp",EDGE,"E13.right"),sQuery(id+"F15.wireOp",EDGE,"E14.bottom"),sQuery(id+"F15.wireOp",EDGE,"E14.top"),sQuery(id+"F15.wireOp",EDGE,"E14.left"),sQuery(id+"F15.wireOp",EDGE,"E14.right"),sQuery(id+"F15.wireOp",EDGE,"E15.MirrorCS"),sQuery(id+"F15.wireOp",EDGE,"E16.MirrorCS"),sQuery(id+"F15.wireOp",EDGE,"E17.MirrorCS"),sQuery(id+"F15.wireOp",EDGE,"E18.MirrorCS"),sQuery(id+"F15.wireOp",EDGE,"E19.MirrorCS"),sQuery(id+"F15.wireOp",EDGE,"E20.MirrorCS"),sQuery(id+"F15.wireOp",EDGE,"E21.MirrorCS"),sQuery(id+"F15.wireOp",EDGE,"E22.MirrorCS"),sQuery(id+"F15.wireOp",EDGE,"E23.MirrorCS"),sQuery(id+"F15.wireOp",EDGE,"E24.MirrorCS"),sQuery(id+"F15.wireOp",EDGE,"E25.MirrorCS"),sQuery(id+"F15.wireOp",EDGE,"E26.MirrorCS")])]});
            transform(context, id + "F18", {"entities" : qUnion([Q0, Q1]), "transformType" : TransformType.TRANSLATION_3D, "dx" : 0 * mm, "dy" : 80 * mm, "dz" : 0 * mm, "makeCopy" : true});
        }
        {
            var Q0;
            Q0=makeQuery(id+"F18.opPattern","COPY",BODY,{"derivedFrom":makeQuery(id+"F17.opPattern","COPY",BODY,{"derivedFrom":makeQuery(id+"F16.opExtrude","SWEPT_BODY",BODY,{"disambiguationData":[OSD([sQuery(id+"F15.wireOp",EDGE,"E13.bottom"),sQuery(id+"F15.wireOp",EDGE,"E13.top"),sQuery(id+"F15.wireOp",EDGE,"E13.left"),sQuery(id+"F15.wireOp",EDGE,"E13.right"),sQuery(id+"F15.wireOp",EDGE,"E14.bottom"),sQuery(id+"F15.wireOp",EDGE,"E14.top"),sQuery(id+"F15.wireOp",EDGE,"E14.left"),sQuery(id+"F15.wireOp",EDGE,"E14.right"),sQuery(id+"F15.wireOp",EDGE,"E15.MirrorCS"),sQuery(id+"F15.wireOp",EDGE,"E16.MirrorCS"),sQuery(id+"F15.wireOp",EDGE,"E17.MirrorCS"),sQuery(id+"F15.wireOp",EDGE,"E18.MirrorCS"),sQuery(id+"F15.wireOp",EDGE,"E19.MirrorCS"),sQuery(id+"F15.wireOp",EDGE,"E20.MirrorCS"),sQuery(id+"F15.wireOp",EDGE,"E21.MirrorCS"),sQuery(id+"F15.wireOp",EDGE,"E22.MirrorCS"),sQuery(id+"F15.wireOp",EDGE,"E23.MirrorCS"),sQuery(id+"F15.wireOp",EDGE,"E24.MirrorCS"),sQuery(id+"F15.wireOp",EDGE,"E25.MirrorCS"),sQuery(id+"F15.wireOp",EDGE,"E26.MirrorCS")])]}),"instanceName":"1"}),"instanceName":"1"});
            var Q1;
            Q1=makeQuery(id+"F18.opPattern","COPY",BODY,{"derivedFrom":makeQuery(id+"F16.opExtrude","SWEPT_BODY",BODY,{"disambiguationData":[OSD([sQuery(id+"F15.wireOp",EDGE,"E13.bottom"),sQuery(id+"F15.wireOp",EDGE,"E13.top"),sQuery(id+"F15.wireOp",EDGE,"E13.left"),sQuery(id+"F15.wireOp",EDGE,"E13.right"),sQuery(id+"F15.wireOp",EDGE,"E14.bottom"),sQuery(id+"F15.wireOp",EDGE,"E14.top"),sQuery(id+"F15.wireOp",EDGE,"E14.left"),sQuery(id+"F15.wireOp",EDGE,"E14.right"),sQuery(id+"F15.wireOp",EDGE,"E15.MirrorCS"),sQuery(id+"F15.wireOp",EDGE,"E16.MirrorCS"),sQuery(id+"F15.wireOp",EDGE,"E17.MirrorCS"),sQuery(id+"F15.wireOp",EDGE,"E18.MirrorCS"),sQuery(id+"F15.wireOp",EDGE,"E19.MirrorCS"),sQuery(id+"F15.wireOp",EDGE,"E20.MirrorCS"),sQuery(id+"F15.wireOp",EDGE,"E21.MirrorCS"),sQuery(id+"F15.wireOp",EDGE,"E22.MirrorCS"),sQuery(id+"F15.wireOp",EDGE,"E23.MirrorCS"),sQuery(id+"F15.wireOp",EDGE,"E24.MirrorCS"),sQuery(id+"F15.wireOp",EDGE,"E25.MirrorCS"),sQuery(id+"F15.wireOp",EDGE,"E26.MirrorCS")])]}),"instanceName":"1"});
            var Q2;
            Q2=makeQuery(id+"F17.opPattern","COPY",BODY,{"derivedFrom":makeQuery(id+"F16.opExtrude","SWEPT_BODY",BODY,{"disambiguationData":[OSD([sQuery(id+"F15.wireOp",EDGE,"E13.bottom"),sQuery(id+"F15.wireOp",EDGE,"E13.top"),sQuery(id+"F15.wireOp",EDGE,"E13.left"),sQuery(id+"F15.wireOp",EDGE,"E13.right"),sQuery(id+"F15.wireOp",EDGE,"E14.bottom"),sQuery(id+"F15.wireOp",EDGE,"E14.top"),sQuery(id+"F15.wireOp",EDGE,"E14.left"),sQuery(id+"F15.wireOp",EDGE,"E14.right"),sQuery(id+"F15.wireOp",EDGE,"E15.MirrorCS"),sQuery(id+"F15.wireOp",EDGE,"E16.MirrorCS"),sQuery(id+"F15.wireOp",EDGE,"E17.MirrorCS"),sQuery(id+"F15.wireOp",EDGE,"E18.MirrorCS"),sQuery(id+"F15.wireOp",EDGE,"E19.MirrorCS"),sQuery(id+"F15.wireOp",EDGE,"E20.MirrorCS"),sQuery(id+"F15.wireOp",EDGE,"E21.MirrorCS"),sQuery(id+"F15.wireOp",EDGE,"E22.MirrorCS"),sQuery(id+"F15.wireOp",EDGE,"E23.MirrorCS"),sQuery(id+"F15.wireOp",EDGE,"E24.MirrorCS"),sQuery(id+"F15.wireOp",EDGE,"E25.MirrorCS"),sQuery(id+"F15.wireOp",EDGE,"E26.MirrorCS")])]}),"instanceName":"1"});
            var Q3;
            Q3=makeQuery(id+"F16.opExtrude","SWEPT_BODY",BODY,{"disambiguationData":[OSD([sQuery(id+"F15.wireOp",EDGE,"E13.bottom"),sQuery(id+"F15.wireOp",EDGE,"E13.top"),sQuery(id+"F15.wireOp",EDGE,"E13.left"),sQuery(id+"F15.wireOp",EDGE,"E13.right"),sQuery(id+"F15.wireOp",EDGE,"E14.bottom"),sQuery(id+"F15.wireOp",EDGE,"E14.top"),sQuery(id+"F15.wireOp",EDGE,"E14.left"),sQuery(id+"F15.wireOp",EDGE,"E14.right"),sQuery(id+"F15.wireOp",EDGE,"E15.MirrorCS"),sQuery(id+"F15.wireOp",EDGE,"E16.MirrorCS"),sQuery(id+"F15.wireOp",EDGE,"E17.MirrorCS"),sQuery(id+"F15.wireOp",EDGE,"E18.MirrorCS"),sQuery(id+"F15.wireOp",EDGE,"E19.MirrorCS"),sQuery(id+"F15.wireOp",EDGE,"E20.MirrorCS"),sQuery(id+"F15.wireOp",EDGE,"E21.MirrorCS"),sQuery(id+"F15.wireOp",EDGE,"E22.MirrorCS"),sQuery(id+"F15.wireOp",EDGE,"E23.MirrorCS"),sQuery(id+"F15.wireOp",EDGE,"E24.MirrorCS"),sQuery(id+"F15.wireOp",EDGE,"E25.MirrorCS"),sQuery(id+"F15.wireOp",EDGE,"E26.MirrorCS")])]});
            transform(context, id + "F19", {"entities" : qUnion([Q0, Q1, Q2, Q3]), "transformType" : TransformType.TRANSLATION_3D, "dx" : 0 * mm, "dy" : 160 * mm, "dz" : 0 * mm, "makeCopy" : true});
        }
        {
            var Q0;
            Q0=makeQuery(id+"F19.opPattern","COPY",BODY,{"derivedFrom":makeQuery(id+"F18.opPattern","COPY",BODY,{"derivedFrom":makeQuery(id+"F17.opPattern","COPY",BODY,{"derivedFrom":makeQuery(id+"F16.opExtrude","SWEPT_BODY",BODY,{"disambiguationData":[OSD([sQuery(id+"F15.wireOp",EDGE,"E13.bottom"),sQuery(id+"F15.wireOp",EDGE,"E13.top"),sQuery(id+"F15.wireOp",EDGE,"E13.left"),sQuery(id+"F15.wireOp",EDGE,"E13.right"),sQuery(id+"F15.wireOp",EDGE,"E14.bottom"),sQuery(id+"F15.wireOp",EDGE,"E14.top"),sQuery(id+"F15.wireOp",EDGE,"E14.left"),sQuery(id+"F15.wireOp",EDGE,"E14.right"),sQuery(id+"F15.wireOp",EDGE,"E15.MirrorCS"),sQuery(id+"F15.wireOp",EDGE,"E16.MirrorCS"),sQuery(id+"F15.wireOp",EDGE,"E17.MirrorCS"),sQuery(id+"F15.wireOp",EDGE,"E18.MirrorCS"),sQuery(id+"F15.wireOp",EDGE,"E19.MirrorCS"),sQuery(id+"F15.wireOp",EDGE,"E20.MirrorCS"),sQuery(id+"F15.wireOp",EDGE,"E21.MirrorCS"),sQuery(id+"F15.wireOp",EDGE,"E22.MirrorCS"),sQuery(id+"F15.wireOp",EDGE,"E23.MirrorCS"),sQuery(id+"F15.wireOp",EDGE,"E24.MirrorCS"),sQuery(id+"F15.wireOp",EDGE,"E25.MirrorCS"),sQuery(id+"F15.wireOp",EDGE,"E26.MirrorCS")])]}),"instanceName":"1"}),"instanceName":"1"}),"instanceName":"1"});
            var Q1;
            Q1=makeQuery(id+"F19.opPattern","COPY",BODY,{"derivedFrom":makeQuery(id+"F18.opPattern","COPY",BODY,{"derivedFrom":makeQuery(id+"F16.opExtrude","SWEPT_BODY",BODY,{"disambiguationData":[OSD([sQuery(id+"F15.wireOp",EDGE,"E13.bottom"),sQuery(id+"F15.wireOp",EDGE,"E13.top"),sQuery(id+"F15.wireOp",EDGE,"E13.left"),sQuery(id+"F15.wireOp",EDGE,"E13.right"),sQuery(id+"F15.wireOp",EDGE,"E14.bottom"),sQuery(id+"F15.wireOp",EDGE,"E14.top"),sQuery(id+"F15.wireOp",EDGE,"E14.left"),sQuery(id+"F15.wireOp",EDGE,"E14.right"),sQuery(id+"F15.wireOp",EDGE,"E15.MirrorCS"),sQuery(id+"F15.wireOp",EDGE,"E16.MirrorCS"),sQuery(id+"F15.wireOp",EDGE,"E17.MirrorCS"),sQuery(id+"F15.wireOp",EDGE,"E18.MirrorCS"),sQuery(id+"F15.wireOp",EDGE,"E19.MirrorCS"),sQuery(id+"F15.wireOp",EDGE,"E20.MirrorCS"),sQuery(id+"F15.wireOp",EDGE,"E21.MirrorCS"),sQuery(id+"F15.wireOp",EDGE,"E22.MirrorCS"),sQuery(id+"F15.wireOp",EDGE,"E23.MirrorCS"),sQuery(id+"F15.wireOp",EDGE,"E24.MirrorCS"),sQuery(id+"F15.wireOp",EDGE,"E25.MirrorCS"),sQuery(id+"F15.wireOp",EDGE,"E26.MirrorCS")])]}),"instanceName":"1"}),"instanceName":"1"});
            var Q2;
            Q2=makeQuery(id+"F19.opPattern","COPY",BODY,{"derivedFrom":makeQuery(id+"F17.opPattern","COPY",BODY,{"derivedFrom":makeQuery(id+"F16.opExtrude","SWEPT_BODY",BODY,{"disambiguationData":[OSD([sQuery(id+"F15.wireOp",EDGE,"E13.bottom"),sQuery(id+"F15.wireOp",EDGE,"E13.top"),sQuery(id+"F15.wireOp",EDGE,"E13.left"),sQuery(id+"F15.wireOp",EDGE,"E13.right"),sQuery(id+"F15.wireOp",EDGE,"E14.bottom"),sQuery(id+"F15.wireOp",EDGE,"E14.top"),sQuery(id+"F15.wireOp",EDGE,"E14.left"),sQuery(id+"F15.wireOp",EDGE,"E14.right"),sQuery(id+"F15.wireOp",EDGE,"E15.MirrorCS"),sQuery(id+"F15.wireOp",EDGE,"E16.MirrorCS"),sQuery(id+"F15.wireOp",EDGE,"E17.MirrorCS"),sQuery(id+"F15.wireOp",EDGE,"E18.MirrorCS"),sQuery(id+"F15.wireOp",EDGE,"E19.MirrorCS"),sQuery(id+"F15.wireOp",EDGE,"E20.MirrorCS"),sQuery(id+"F15.wireOp",EDGE,"E21.MirrorCS"),sQuery(id+"F15.wireOp",EDGE,"E22.MirrorCS"),sQuery(id+"F15.wireOp",EDGE,"E23.MirrorCS"),sQuery(id+"F15.wireOp",EDGE,"E24.MirrorCS"),sQuery(id+"F15.wireOp",EDGE,"E25.MirrorCS"),sQuery(id+"F15.wireOp",EDGE,"E26.MirrorCS")])]}),"instanceName":"1"}),"instanceName":"1"});
            var Q3;
            Q3=makeQuery(id+"F19.opPattern","COPY",BODY,{"derivedFrom":makeQuery(id+"F16.opExtrude","SWEPT_BODY",BODY,{"disambiguationData":[OSD([sQuery(id+"F15.wireOp",EDGE,"E13.bottom"),sQuery(id+"F15.wireOp",EDGE,"E13.top"),sQuery(id+"F15.wireOp",EDGE,"E13.left"),sQuery(id+"F15.wireOp",EDGE,"E13.right"),sQuery(id+"F15.wireOp",EDGE,"E14.bottom"),sQuery(id+"F15.wireOp",EDGE,"E14.top"),sQuery(id+"F15.wireOp",EDGE,"E14.left"),sQuery(id+"F15.wireOp",EDGE,"E14.right"),sQuery(id+"F15.wireOp",EDGE,"E15.MirrorCS"),sQuery(id+"F15.wireOp",EDGE,"E16.MirrorCS"),sQuery(id+"F15.wireOp",EDGE,"E17.MirrorCS"),sQuery(id+"F15.wireOp",EDGE,"E18.MirrorCS"),sQuery(id+"F15.wireOp",EDGE,"E19.MirrorCS"),sQuery(id+"F15.wireOp",EDGE,"E20.MirrorCS"),sQuery(id+"F15.wireOp",EDGE,"E21.MirrorCS"),sQuery(id+"F15.wireOp",EDGE,"E22.MirrorCS"),sQuery(id+"F15.wireOp",EDGE,"E23.MirrorCS"),sQuery(id+"F15.wireOp",EDGE,"E24.MirrorCS"),sQuery(id+"F15.wireOp",EDGE,"E25.MirrorCS"),sQuery(id+"F15.wireOp",EDGE,"E26.MirrorCS")])]}),"instanceName":"1"});
            var Q4;
            Q4=makeQuery(id+"F18.opPattern","COPY",BODY,{"derivedFrom":makeQuery(id+"F17.opPattern","COPY",BODY,{"derivedFrom":makeQuery(id+"F16.opExtrude","SWEPT_BODY",BODY,{"disambiguationData":[OSD([sQuery(id+"F15.wireOp",EDGE,"E13.bottom"),sQuery(id+"F15.wireOp",EDGE,"E13.top"),sQuery(id+"F15.wireOp",EDGE,"E13.left"),sQuery(id+"F15.wireOp",EDGE,"E13.right"),sQuery(id+"F15.wireOp",EDGE,"E14.bottom"),sQuery(id+"F15.wireOp",EDGE,"E14.top"),sQuery(id+"F15.wireOp",EDGE,"E14.left"),sQuery(id+"F15.wireOp",EDGE,"E14.right"),sQuery(id+"F15.wireOp",EDGE,"E15.MirrorCS"),sQuery(id+"F15.wireOp",EDGE,"E16.MirrorCS"),sQuery(id+"F15.wireOp",EDGE,"E17.MirrorCS"),sQuery(id+"F15.wireOp",EDGE,"E18.MirrorCS"),sQuery(id+"F15.wireOp",EDGE,"E19.MirrorCS"),sQuery(id+"F15.wireOp",EDGE,"E20.MirrorCS"),sQuery(id+"F15.wireOp",EDGE,"E21.MirrorCS"),sQuery(id+"F15.wireOp",EDGE,"E22.MirrorCS"),sQuery(id+"F15.wireOp",EDGE,"E23.MirrorCS"),sQuery(id+"F15.wireOp",EDGE,"E24.MirrorCS"),sQuery(id+"F15.wireOp",EDGE,"E25.MirrorCS"),sQuery(id+"F15.wireOp",EDGE,"E26.MirrorCS")])]}),"instanceName":"1"}),"instanceName":"1"});
            var Q5;
            Q5=makeQuery(id+"F18.opPattern","COPY",BODY,{"derivedFrom":makeQuery(id+"F16.opExtrude","SWEPT_BODY",BODY,{"disambiguationData":[OSD([sQuery(id+"F15.wireOp",EDGE,"E13.bottom"),sQuery(id+"F15.wireOp",EDGE,"E13.top"),sQuery(id+"F15.wireOp",EDGE,"E13.left"),sQuery(id+"F15.wireOp",EDGE,"E13.right"),sQuery(id+"F15.wireOp",EDGE,"E14.bottom"),sQuery(id+"F15.wireOp",EDGE,"E14.top"),sQuery(id+"F15.wireOp",EDGE,"E14.left"),sQuery(id+"F15.wireOp",EDGE,"E14.right"),sQuery(id+"F15.wireOp",EDGE,"E15.MirrorCS"),sQuery(id+"F15.wireOp",EDGE,"E16.MirrorCS"),sQuery(id+"F15.wireOp",EDGE,"E17.MirrorCS"),sQuery(id+"F15.wireOp",EDGE,"E18.MirrorCS"),sQuery(id+"F15.wireOp",EDGE,"E19.MirrorCS"),sQuery(id+"F15.wireOp",EDGE,"E20.MirrorCS"),sQuery(id+"F15.wireOp",EDGE,"E21.MirrorCS"),sQuery(id+"F15.wireOp",EDGE,"E22.MirrorCS"),sQuery(id+"F15.wireOp",EDGE,"E23.MirrorCS"),sQuery(id+"F15.wireOp",EDGE,"E24.MirrorCS"),sQuery(id+"F15.wireOp",EDGE,"E25.MirrorCS"),sQuery(id+"F15.wireOp",EDGE,"E26.MirrorCS")])]}),"instanceName":"1"});
            var Q6;
            Q6=makeQuery(id+"F17.opPattern","COPY",BODY,{"derivedFrom":makeQuery(id+"F16.opExtrude","SWEPT_BODY",BODY,{"disambiguationData":[OSD([sQuery(id+"F15.wireOp",EDGE,"E13.bottom"),sQuery(id+"F15.wireOp",EDGE,"E13.top"),sQuery(id+"F15.wireOp",EDGE,"E13.left"),sQuery(id+"F15.wireOp",EDGE,"E13.right"),sQuery(id+"F15.wireOp",EDGE,"E14.bottom"),sQuery(id+"F15.wireOp",EDGE,"E14.top"),sQuery(id+"F15.wireOp",EDGE,"E14.left"),sQuery(id+"F15.wireOp",EDGE,"E14.right"),sQuery(id+"F15.wireOp",EDGE,"E15.MirrorCS"),sQuery(id+"F15.wireOp",EDGE,"E16.MirrorCS"),sQuery(id+"F15.wireOp",EDGE,"E17.MirrorCS"),sQuery(id+"F15.wireOp",EDGE,"E18.MirrorCS"),sQuery(id+"F15.wireOp",EDGE,"E19.MirrorCS"),sQuery(id+"F15.wireOp",EDGE,"E20.MirrorCS"),sQuery(id+"F15.wireOp",EDGE,"E21.MirrorCS"),sQuery(id+"F15.wireOp",EDGE,"E22.MirrorCS"),sQuery(id+"F15.wireOp",EDGE,"E23.MirrorCS"),sQuery(id+"F15.wireOp",EDGE,"E24.MirrorCS"),sQuery(id+"F15.wireOp",EDGE,"E25.MirrorCS"),sQuery(id+"F15.wireOp",EDGE,"E26.MirrorCS")])]}),"instanceName":"1"});
            var Q7;
            Q7=makeQuery(id+"F16.opExtrude","SWEPT_BODY",BODY,{"disambiguationData":[OSD([sQuery(id+"F15.wireOp",EDGE,"E13.bottom"),sQuery(id+"F15.wireOp",EDGE,"E13.top"),sQuery(id+"F15.wireOp",EDGE,"E13.left"),sQuery(id+"F15.wireOp",EDGE,"E13.right"),sQuery(id+"F15.wireOp",EDGE,"E14.bottom"),sQuery(id+"F15.wireOp",EDGE,"E14.top"),sQuery(id+"F15.wireOp",EDGE,"E14.left"),sQuery(id+"F15.wireOp",EDGE,"E14.right"),sQuery(id+"F15.wireOp",EDGE,"E15.MirrorCS"),sQuery(id+"F15.wireOp",EDGE,"E16.MirrorCS"),sQuery(id+"F15.wireOp",EDGE,"E17.MirrorCS"),sQuery(id+"F15.wireOp",EDGE,"E18.MirrorCS"),sQuery(id+"F15.wireOp",EDGE,"E19.MirrorCS"),sQuery(id+"F15.wireOp",EDGE,"E20.MirrorCS"),sQuery(id+"F15.wireOp",EDGE,"E21.MirrorCS"),sQuery(id+"F15.wireOp",EDGE,"E22.MirrorCS"),sQuery(id+"F15.wireOp",EDGE,"E23.MirrorCS"),sQuery(id+"F15.wireOp",EDGE,"E24.MirrorCS"),sQuery(id+"F15.wireOp",EDGE,"E25.MirrorCS"),sQuery(id+"F15.wireOp",EDGE,"E26.MirrorCS")])]});
            transform(context, id + "F20", {"entities" : qUnion([Q0, Q1, Q2, Q3, Q4, Q5, Q6, Q7]), "transformType" : TransformType.TRANSLATION_3D, "dx" : 0 * mm, "dy" : 320 * mm, "dz" : 0 * mm, "makeCopy" : true});
        }
        {
            var Q0;
            Q0=makeQuery(id+"F16.opExtrude","SWEPT_BODY",BODY,{"disambiguationData":[OSD([sQuery(id+"F15.wireOp",EDGE,"E13.bottom"),sQuery(id+"F15.wireOp",EDGE,"E13.top"),sQuery(id+"F15.wireOp",EDGE,"E13.left"),sQuery(id+"F15.wireOp",EDGE,"E13.right"),sQuery(id+"F15.wireOp",EDGE,"E14.bottom"),sQuery(id+"F15.wireOp",EDGE,"E14.top"),sQuery(id+"F15.wireOp",EDGE,"E14.left"),sQuery(id+"F15.wireOp",EDGE,"E14.right"),sQuery(id+"F15.wireOp",EDGE,"E15.MirrorCS"),sQuery(id+"F15.wireOp",EDGE,"E16.MirrorCS"),sQuery(id+"F15.wireOp",EDGE,"E17.MirrorCS"),sQuery(id+"F15.wireOp",EDGE,"E18.MirrorCS"),sQuery(id+"F15.wireOp",EDGE,"E19.MirrorCS"),sQuery(id+"F15.wireOp",EDGE,"E20.MirrorCS"),sQuery(id+"F15.wireOp",EDGE,"E21.MirrorCS"),sQuery(id+"F15.wireOp",EDGE,"E22.MirrorCS"),sQuery(id+"F15.wireOp",EDGE,"E23.MirrorCS"),sQuery(id+"F15.wireOp",EDGE,"E24.MirrorCS"),sQuery(id+"F15.wireOp",EDGE,"E25.MirrorCS"),sQuery(id+"F15.wireOp",EDGE,"E26.MirrorCS")])]});
            var Q1;
            Q1=makeQuery(id+"F17.opPattern","COPY",BODY,{"derivedFrom":makeQuery(id+"F16.opExtrude","SWEPT_BODY",BODY,{"disambiguationData":[OSD([sQuery(id+"F15.wireOp",EDGE,"E13.bottom"),sQuery(id+"F15.wireOp",EDGE,"E13.top"),sQuery(id+"F15.wireOp",EDGE,"E13.left"),sQuery(id+"F15.wireOp",EDGE,"E13.right"),sQuery(id+"F15.wireOp",EDGE,"E14.bottom"),sQuery(id+"F15.wireOp",EDGE,"E14.top"),sQuery(id+"F15.wireOp",EDGE,"E14.left"),sQuery(id+"F15.wireOp",EDGE,"E14.right"),sQuery(id+"F15.wireOp",EDGE,"E15.MirrorCS"),sQuery(id+"F15.wireOp",EDGE,"E16.MirrorCS"),sQuery(id+"F15.wireOp",EDGE,"E17.MirrorCS"),sQuery(id+"F15.wireOp",EDGE,"E18.MirrorCS"),sQuery(id+"F15.wireOp",EDGE,"E19.MirrorCS"),sQuery(id+"F15.wireOp",EDGE,"E20.MirrorCS"),sQuery(id+"F15.wireOp",EDGE,"E21.MirrorCS"),sQuery(id+"F15.wireOp",EDGE,"E22.MirrorCS"),sQuery(id+"F15.wireOp",EDGE,"E23.MirrorCS"),sQuery(id+"F15.wireOp",EDGE,"E24.MirrorCS"),sQuery(id+"F15.wireOp",EDGE,"E25.MirrorCS"),sQuery(id+"F15.wireOp",EDGE,"E26.MirrorCS")])]}),"instanceName":"1"});
            var Q2;
            Q2=makeQuery(id+"F18.opPattern","COPY",BODY,{"derivedFrom":makeQuery(id+"F16.opExtrude","SWEPT_BODY",BODY,{"disambiguationData":[OSD([sQuery(id+"F15.wireOp",EDGE,"E13.bottom"),sQuery(id+"F15.wireOp",EDGE,"E13.top"),sQuery(id+"F15.wireOp",EDGE,"E13.left"),sQuery(id+"F15.wireOp",EDGE,"E13.right"),sQuery(id+"F15.wireOp",EDGE,"E14.bottom"),sQuery(id+"F15.wireOp",EDGE,"E14.top"),sQuery(id+"F15.wireOp",EDGE,"E14.left"),sQuery(id+"F15.wireOp",EDGE,"E14.right"),sQuery(id+"F15.wireOp",EDGE,"E15.MirrorCS"),sQuery(id+"F15.wireOp",EDGE,"E16.MirrorCS"),sQuery(id+"F15.wireOp",EDGE,"E17.MirrorCS"),sQuery(id+"F15.wireOp",EDGE,"E18.MirrorCS"),sQuery(id+"F15.wireOp",EDGE,"E19.MirrorCS"),sQuery(id+"F15.wireOp",EDGE,"E20.MirrorCS"),sQuery(id+"F15.wireOp",EDGE,"E21.MirrorCS"),sQuery(id+"F15.wireOp",EDGE,"E22.MirrorCS"),sQuery(id+"F15.wireOp",EDGE,"E23.MirrorCS"),sQuery(id+"F15.wireOp",EDGE,"E24.MirrorCS"),sQuery(id+"F15.wireOp",EDGE,"E25.MirrorCS"),sQuery(id+"F15.wireOp",EDGE,"E26.MirrorCS")])]}),"instanceName":"1"});
            var Q3;
            Q3=makeQuery(id+"F18.opPattern","COPY",BODY,{"derivedFrom":makeQuery(id+"F17.opPattern","COPY",BODY,{"derivedFrom":makeQuery(id+"F16.opExtrude","SWEPT_BODY",BODY,{"disambiguationData":[OSD([sQuery(id+"F15.wireOp",EDGE,"E13.bottom"),sQuery(id+"F15.wireOp",EDGE,"E13.top"),sQuery(id+"F15.wireOp",EDGE,"E13.left"),sQuery(id+"F15.wireOp",EDGE,"E13.right"),sQuery(id+"F15.wireOp",EDGE,"E14.bottom"),sQuery(id+"F15.wireOp",EDGE,"E14.top"),sQuery(id+"F15.wireOp",EDGE,"E14.left"),sQuery(id+"F15.wireOp",EDGE,"E14.right"),sQuery(id+"F15.wireOp",EDGE,"E15.MirrorCS"),sQuery(id+"F15.wireOp",EDGE,"E16.MirrorCS"),sQuery(id+"F15.wireOp",EDGE,"E17.MirrorCS"),sQuery(id+"F15.wireOp",EDGE,"E18.MirrorCS"),sQuery(id+"F15.wireOp",EDGE,"E19.MirrorCS"),sQuery(id+"F15.wireOp",EDGE,"E20.MirrorCS"),sQuery(id+"F15.wireOp",EDGE,"E21.MirrorCS"),sQuery(id+"F15.wireOp",EDGE,"E22.MirrorCS"),sQuery(id+"F15.wireOp",EDGE,"E23.MirrorCS"),sQuery(id+"F15.wireOp",EDGE,"E24.MirrorCS"),sQuery(id+"F15.wireOp",EDGE,"E25.MirrorCS"),sQuery(id+"F15.wireOp",EDGE,"E26.MirrorCS")])]}),"instanceName":"1"}),"instanceName":"1"});
            var Q4;
            Q4=makeQuery(id+"F19.opPattern","COPY",BODY,{"derivedFrom":makeQuery(id+"F16.opExtrude","SWEPT_BODY",BODY,{"disambiguationData":[OSD([sQuery(id+"F15.wireOp",EDGE,"E13.bottom"),sQuery(id+"F15.wireOp",EDGE,"E13.top"),sQuery(id+"F15.wireOp",EDGE,"E13.left"),sQuery(id+"F15.wireOp",EDGE,"E13.right"),sQuery(id+"F15.wireOp",EDGE,"E14.bottom"),sQuery(id+"F15.wireOp",EDGE,"E14.top"),sQuery(id+"F15.wireOp",EDGE,"E14.left"),sQuery(id+"F15.wireOp",EDGE,"E14.right"),sQuery(id+"F15.wireOp",EDGE,"E15.MirrorCS"),sQuery(id+"F15.wireOp",EDGE,"E16.MirrorCS"),sQuery(id+"F15.wireOp",EDGE,"E17.MirrorCS"),sQuery(id+"F15.wireOp",EDGE,"E18.MirrorCS"),sQuery(id+"F15.wireOp",EDGE,"E19.MirrorCS"),sQuery(id+"F15.wireOp",EDGE,"E20.MirrorCS"),sQuery(id+"F15.wireOp",EDGE,"E21.MirrorCS"),sQuery(id+"F15.wireOp",EDGE,"E22.MirrorCS"),sQuery(id+"F15.wireOp",EDGE,"E23.MirrorCS"),sQuery(id+"F15.wireOp",EDGE,"E24.MirrorCS"),sQuery(id+"F15.wireOp",EDGE,"E25.MirrorCS"),sQuery(id+"F15.wireOp",EDGE,"E26.MirrorCS")])]}),"instanceName":"1"});
            var Q5;
            Q5=makeQuery(id+"F19.opPattern","COPY",BODY,{"derivedFrom":makeQuery(id+"F17.opPattern","COPY",BODY,{"derivedFrom":makeQuery(id+"F16.opExtrude","SWEPT_BODY",BODY,{"disambiguationData":[OSD([sQuery(id+"F15.wireOp",EDGE,"E13.bottom"),sQuery(id+"F15.wireOp",EDGE,"E13.top"),sQuery(id+"F15.wireOp",EDGE,"E13.left"),sQuery(id+"F15.wireOp",EDGE,"E13.right"),sQuery(id+"F15.wireOp",EDGE,"E14.bottom"),sQuery(id+"F15.wireOp",EDGE,"E14.top"),sQuery(id+"F15.wireOp",EDGE,"E14.left"),sQuery(id+"F15.wireOp",EDGE,"E14.right"),sQuery(id+"F15.wireOp",EDGE,"E15.MirrorCS"),sQuery(id+"F15.wireOp",EDGE,"E16.MirrorCS"),sQuery(id+"F15.wireOp",EDGE,"E17.MirrorCS"),sQuery(id+"F15.wireOp",EDGE,"E18.MirrorCS"),sQuery(id+"F15.wireOp",EDGE,"E19.MirrorCS"),sQuery(id+"F15.wireOp",EDGE,"E20.MirrorCS"),sQuery(id+"F15.wireOp",EDGE,"E21.MirrorCS"),sQuery(id+"F15.wireOp",EDGE,"E22.MirrorCS"),sQuery(id+"F15.wireOp",EDGE,"E23.MirrorCS"),sQuery(id+"F15.wireOp",EDGE,"E24.MirrorCS"),sQuery(id+"F15.wireOp",EDGE,"E25.MirrorCS"),sQuery(id+"F15.wireOp",EDGE,"E26.MirrorCS")])]}),"instanceName":"1"}),"instanceName":"1"});
            var Q6;
            Q6=makeQuery(id+"F19.opPattern","COPY",BODY,{"derivedFrom":makeQuery(id+"F18.opPattern","COPY",BODY,{"derivedFrom":makeQuery(id+"F16.opExtrude","SWEPT_BODY",BODY,{"disambiguationData":[OSD([sQuery(id+"F15.wireOp",EDGE,"E13.bottom"),sQuery(id+"F15.wireOp",EDGE,"E13.top"),sQuery(id+"F15.wireOp",EDGE,"E13.left"),sQuery(id+"F15.wireOp",EDGE,"E13.right"),sQuery(id+"F15.wireOp",EDGE,"E14.bottom"),sQuery(id+"F15.wireOp",EDGE,"E14.top"),sQuery(id+"F15.wireOp",EDGE,"E14.left"),sQuery(id+"F15.wireOp",EDGE,"E14.right"),sQuery(id+"F15.wireOp",EDGE,"E15.MirrorCS"),sQuery(id+"F15.wireOp",EDGE,"E16.MirrorCS"),sQuery(id+"F15.wireOp",EDGE,"E17.MirrorCS"),sQuery(id+"F15.wireOp",EDGE,"E18.MirrorCS"),sQuery(id+"F15.wireOp",EDGE,"E19.MirrorCS"),sQuery(id+"F15.wireOp",EDGE,"E20.MirrorCS"),sQuery(id+"F15.wireOp",EDGE,"E21.MirrorCS"),sQuery(id+"F15.wireOp",EDGE,"E22.MirrorCS"),sQuery(id+"F15.wireOp",EDGE,"E23.MirrorCS"),sQuery(id+"F15.wireOp",EDGE,"E24.MirrorCS"),sQuery(id+"F15.wireOp",EDGE,"E25.MirrorCS"),sQuery(id+"F15.wireOp",EDGE,"E26.MirrorCS")])]}),"instanceName":"1"}),"instanceName":"1"});
            var Q7;
            Q7=makeQuery(id+"F19.opPattern","COPY",BODY,{"derivedFrom":makeQuery(id+"F18.opPattern","COPY",BODY,{"derivedFrom":makeQuery(id+"F17.opPattern","COPY",BODY,{"derivedFrom":makeQuery(id+"F16.opExtrude","SWEPT_BODY",BODY,{"disambiguationData":[OSD([sQuery(id+"F15.wireOp",EDGE,"E13.bottom"),sQuery(id+"F15.wireOp",EDGE,"E13.top"),sQuery(id+"F15.wireOp",EDGE,"E13.left"),sQuery(id+"F15.wireOp",EDGE,"E13.right"),sQuery(id+"F15.wireOp",EDGE,"E14.bottom"),sQuery(id+"F15.wireOp",EDGE,"E14.top"),sQuery(id+"F15.wireOp",EDGE,"E14.left"),sQuery(id+"F15.wireOp",EDGE,"E14.right"),sQuery(id+"F15.wireOp",EDGE,"E15.MirrorCS"),sQuery(id+"F15.wireOp",EDGE,"E16.MirrorCS"),sQuery(id+"F15.wireOp",EDGE,"E17.MirrorCS"),sQuery(id+"F15.wireOp",EDGE,"E18.MirrorCS"),sQuery(id+"F15.wireOp",EDGE,"E19.MirrorCS"),sQuery(id+"F15.wireOp",EDGE,"E20.MirrorCS"),sQuery(id+"F15.wireOp",EDGE,"E21.MirrorCS"),sQuery(id+"F15.wireOp",EDGE,"E22.MirrorCS"),sQuery(id+"F15.wireOp",EDGE,"E23.MirrorCS"),sQuery(id+"F15.wireOp",EDGE,"E24.MirrorCS"),sQuery(id+"F15.wireOp",EDGE,"E25.MirrorCS"),sQuery(id+"F15.wireOp",EDGE,"E26.MirrorCS")])]}),"instanceName":"1"}),"instanceName":"1"}),"instanceName":"1"});
            var Q8;
            Q8=makeQuery(id+"F20.opPattern","COPY",BODY,{"derivedFrom":makeQuery(id+"F16.opExtrude","SWEPT_BODY",BODY,{"disambiguationData":[OSD([sQuery(id+"F15.wireOp",EDGE,"E13.bottom"),sQuery(id+"F15.wireOp",EDGE,"E13.top"),sQuery(id+"F15.wireOp",EDGE,"E13.left"),sQuery(id+"F15.wireOp",EDGE,"E13.right"),sQuery(id+"F15.wireOp",EDGE,"E14.bottom"),sQuery(id+"F15.wireOp",EDGE,"E14.top"),sQuery(id+"F15.wireOp",EDGE,"E14.left"),sQuery(id+"F15.wireOp",EDGE,"E14.right"),sQuery(id+"F15.wireOp",EDGE,"E15.MirrorCS"),sQuery(id+"F15.wireOp",EDGE,"E16.MirrorCS"),sQuery(id+"F15.wireOp",EDGE,"E17.MirrorCS"),sQuery(id+"F15.wireOp",EDGE,"E18.MirrorCS"),sQuery(id+"F15.wireOp",EDGE,"E19.MirrorCS"),sQuery(id+"F15.wireOp",EDGE,"E20.MirrorCS"),sQuery(id+"F15.wireOp",EDGE,"E21.MirrorCS"),sQuery(id+"F15.wireOp",EDGE,"E22.MirrorCS"),sQuery(id+"F15.wireOp",EDGE,"E23.MirrorCS"),sQuery(id+"F15.wireOp",EDGE,"E24.MirrorCS"),sQuery(id+"F15.wireOp",EDGE,"E25.MirrorCS"),sQuery(id+"F15.wireOp",EDGE,"E26.MirrorCS")])]}),"instanceName":"1"});
            var Q9;
            Q9=makeQuery(id+"F20.opPattern","COPY",BODY,{"derivedFrom":makeQuery(id+"F17.opPattern","COPY",BODY,{"derivedFrom":makeQuery(id+"F16.opExtrude","SWEPT_BODY",BODY,{"disambiguationData":[OSD([sQuery(id+"F15.wireOp",EDGE,"E13.bottom"),sQuery(id+"F15.wireOp",EDGE,"E13.top"),sQuery(id+"F15.wireOp",EDGE,"E13.left"),sQuery(id+"F15.wireOp",EDGE,"E13.right"),sQuery(id+"F15.wireOp",EDGE,"E14.bottom"),sQuery(id+"F15.wireOp",EDGE,"E14.top"),sQuery(id+"F15.wireOp",EDGE,"E14.left"),sQuery(id+"F15.wireOp",EDGE,"E14.right"),sQuery(id+"F15.wireOp",EDGE,"E15.MirrorCS"),sQuery(id+"F15.wireOp",EDGE,"E16.MirrorCS"),sQuery(id+"F15.wireOp",EDGE,"E17.MirrorCS"),sQuery(id+"F15.wireOp",EDGE,"E18.MirrorCS"),sQuery(id+"F15.wireOp",EDGE,"E19.MirrorCS"),sQuery(id+"F15.wireOp",EDGE,"E20.MirrorCS"),sQuery(id+"F15.wireOp",EDGE,"E21.MirrorCS"),sQuery(id+"F15.wireOp",EDGE,"E22.MirrorCS"),sQuery(id+"F15.wireOp",EDGE,"E23.MirrorCS"),sQuery(id+"F15.wireOp",EDGE,"E24.MirrorCS"),sQuery(id+"F15.wireOp",EDGE,"E25.MirrorCS"),sQuery(id+"F15.wireOp",EDGE,"E26.MirrorCS")])]}),"instanceName":"1"}),"instanceName":"1"});
            var Q10;
            Q10=makeQuery(id+"F20.opPattern","COPY",BODY,{"derivedFrom":makeQuery(id+"F18.opPattern","COPY",BODY,{"derivedFrom":makeQuery(id+"F16.opExtrude","SWEPT_BODY",BODY,{"disambiguationData":[OSD([sQuery(id+"F15.wireOp",EDGE,"E13.bottom"),sQuery(id+"F15.wireOp",EDGE,"E13.top"),sQuery(id+"F15.wireOp",EDGE,"E13.left"),sQuery(id+"F15.wireOp",EDGE,"E13.right"),sQuery(id+"F15.wireOp",EDGE,"E14.bottom"),sQuery(id+"F15.wireOp",EDGE,"E14.top"),sQuery(id+"F15.wireOp",EDGE,"E14.left"),sQuery(id+"F15.wireOp",EDGE,"E14.right"),sQuery(id+"F15.wireOp",EDGE,"E15.MirrorCS"),sQuery(id+"F15.wireOp",EDGE,"E16.MirrorCS"),sQuery(id+"F15.wireOp",EDGE,"E17.MirrorCS"),sQuery(id+"F15.wireOp",EDGE,"E18.MirrorCS"),sQuery(id+"F15.wireOp",EDGE,"E19.MirrorCS"),sQuery(id+"F15.wireOp",EDGE,"E20.MirrorCS"),sQuery(id+"F15.wireOp",EDGE,"E21.MirrorCS"),sQuery(id+"F15.wireOp",EDGE,"E22.MirrorCS"),sQuery(id+"F15.wireOp",EDGE,"E23.MirrorCS"),sQuery(id+"F15.wireOp",EDGE,"E24.MirrorCS"),sQuery(id+"F15.wireOp",EDGE,"E25.MirrorCS"),sQuery(id+"F15.wireOp",EDGE,"E26.MirrorCS")])]}),"instanceName":"1"}),"instanceName":"1"});
            var Q11;
            Q11=makeQuery(id+"F20.opPattern","COPY",BODY,{"derivedFrom":makeQuery(id+"F18.opPattern","COPY",BODY,{"derivedFrom":makeQuery(id+"F17.opPattern","COPY",BODY,{"derivedFrom":makeQuery(id+"F16.opExtrude","SWEPT_BODY",BODY,{"disambiguationData":[OSD([sQuery(id+"F15.wireOp",EDGE,"E13.bottom"),sQuery(id+"F15.wireOp",EDGE,"E13.top"),sQuery(id+"F15.wireOp",EDGE,"E13.left"),sQuery(id+"F15.wireOp",EDGE,"E13.right"),sQuery(id+"F15.wireOp",EDGE,"E14.bottom"),sQuery(id+"F15.wireOp",EDGE,"E14.top"),sQuery(id+"F15.wireOp",EDGE,"E14.left"),sQuery(id+"F15.wireOp",EDGE,"E14.right"),sQuery(id+"F15.wireOp",EDGE,"E15.MirrorCS"),sQuery(id+"F15.wireOp",EDGE,"E16.MirrorCS"),sQuery(id+"F15.wireOp",EDGE,"E17.MirrorCS"),sQuery(id+"F15.wireOp",EDGE,"E18.MirrorCS"),sQuery(id+"F15.wireOp",EDGE,"E19.MirrorCS"),sQuery(id+"F15.wireOp",EDGE,"E20.MirrorCS"),sQuery(id+"F15.wireOp",EDGE,"E21.MirrorCS"),sQuery(id+"F15.wireOp",EDGE,"E22.MirrorCS"),sQuery(id+"F15.wireOp",EDGE,"E23.MirrorCS"),sQuery(id+"F15.wireOp",EDGE,"E24.MirrorCS"),sQuery(id+"F15.wireOp",EDGE,"E25.MirrorCS"),sQuery(id+"F15.wireOp",EDGE,"E26.MirrorCS")])]}),"instanceName":"1"}),"instanceName":"1"}),"instanceName":"1"});
            var Q12;
            Q12=makeQuery(id+"F20.opPattern","COPY",BODY,{"derivedFrom":makeQuery(id+"F19.opPattern","COPY",BODY,{"derivedFrom":makeQuery(id+"F16.opExtrude","SWEPT_BODY",BODY,{"disambiguationData":[OSD([sQuery(id+"F15.wireOp",EDGE,"E13.bottom"),sQuery(id+"F15.wireOp",EDGE,"E13.top"),sQuery(id+"F15.wireOp",EDGE,"E13.left"),sQuery(id+"F15.wireOp",EDGE,"E13.right"),sQuery(id+"F15.wireOp",EDGE,"E14.bottom"),sQuery(id+"F15.wireOp",EDGE,"E14.top"),sQuery(id+"F15.wireOp",EDGE,"E14.left"),sQuery(id+"F15.wireOp",EDGE,"E14.right"),sQuery(id+"F15.wireOp",EDGE,"E15.MirrorCS"),sQuery(id+"F15.wireOp",EDGE,"E16.MirrorCS"),sQuery(id+"F15.wireOp",EDGE,"E17.MirrorCS"),sQuery(id+"F15.wireOp",EDGE,"E18.MirrorCS"),sQuery(id+"F15.wireOp",EDGE,"E19.MirrorCS"),sQuery(id+"F15.wireOp",EDGE,"E20.MirrorCS"),sQuery(id+"F15.wireOp",EDGE,"E21.MirrorCS"),sQuery(id+"F15.wireOp",EDGE,"E22.MirrorCS"),sQuery(id+"F15.wireOp",EDGE,"E23.MirrorCS"),sQuery(id+"F15.wireOp",EDGE,"E24.MirrorCS"),sQuery(id+"F15.wireOp",EDGE,"E25.MirrorCS"),sQuery(id+"F15.wireOp",EDGE,"E26.MirrorCS")])]}),"instanceName":"1"}),"instanceName":"1"});
            var Q13;
            Q13=makeQuery(id+"F20.opPattern","COPY",BODY,{"derivedFrom":makeQuery(id+"F19.opPattern","COPY",BODY,{"derivedFrom":makeQuery(id+"F17.opPattern","COPY",BODY,{"derivedFrom":makeQuery(id+"F16.opExtrude","SWEPT_BODY",BODY,{"disambiguationData":[OSD([sQuery(id+"F15.wireOp",EDGE,"E13.bottom"),sQuery(id+"F15.wireOp",EDGE,"E13.top"),sQuery(id+"F15.wireOp",EDGE,"E13.left"),sQuery(id+"F15.wireOp",EDGE,"E13.right"),sQuery(id+"F15.wireOp",EDGE,"E14.bottom"),sQuery(id+"F15.wireOp",EDGE,"E14.top"),sQuery(id+"F15.wireOp",EDGE,"E14.left"),sQuery(id+"F15.wireOp",EDGE,"E14.right"),sQuery(id+"F15.wireOp",EDGE,"E15.MirrorCS"),sQuery(id+"F15.wireOp",EDGE,"E16.MirrorCS"),sQuery(id+"F15.wireOp",EDGE,"E17.MirrorCS"),sQuery(id+"F15.wireOp",EDGE,"E18.MirrorCS"),sQuery(id+"F15.wireOp",EDGE,"E19.MirrorCS"),sQuery(id+"F15.wireOp",EDGE,"E20.MirrorCS"),sQuery(id+"F15.wireOp",EDGE,"E21.MirrorCS"),sQuery(id+"F15.wireOp",EDGE,"E22.MirrorCS"),sQuery(id+"F15.wireOp",EDGE,"E23.MirrorCS"),sQuery(id+"F15.wireOp",EDGE,"E24.MirrorCS"),sQuery(id+"F15.wireOp",EDGE,"E25.MirrorCS"),sQuery(id+"F15.wireOp",EDGE,"E26.MirrorCS")])]}),"instanceName":"1"}),"instanceName":"1"}),"instanceName":"1"});
            var Q14;
            Q14=makeQuery(id+"F20.opPattern","COPY",BODY,{"derivedFrom":makeQuery(id+"F19.opPattern","COPY",BODY,{"derivedFrom":makeQuery(id+"F18.opPattern","COPY",BODY,{"derivedFrom":makeQuery(id+"F16.opExtrude","SWEPT_BODY",BODY,{"disambiguationData":[OSD([sQuery(id+"F15.wireOp",EDGE,"E13.bottom"),sQuery(id+"F15.wireOp",EDGE,"E13.top"),sQuery(id+"F15.wireOp",EDGE,"E13.left"),sQuery(id+"F15.wireOp",EDGE,"E13.right"),sQuery(id+"F15.wireOp",EDGE,"E14.bottom"),sQuery(id+"F15.wireOp",EDGE,"E14.top"),sQuery(id+"F15.wireOp",EDGE,"E14.left"),sQuery(id+"F15.wireOp",EDGE,"E14.right"),sQuery(id+"F15.wireOp",EDGE,"E15.MirrorCS"),sQuery(id+"F15.wireOp",EDGE,"E16.MirrorCS"),sQuery(id+"F15.wireOp",EDGE,"E17.MirrorCS"),sQuery(id+"F15.wireOp",EDGE,"E18.MirrorCS"),sQuery(id+"F15.wireOp",EDGE,"E19.MirrorCS"),sQuery(id+"F15.wireOp",EDGE,"E20.MirrorCS"),sQuery(id+"F15.wireOp",EDGE,"E21.MirrorCS"),sQuery(id+"F15.wireOp",EDGE,"E22.MirrorCS"),sQuery(id+"F15.wireOp",EDGE,"E23.MirrorCS"),sQuery(id+"F15.wireOp",EDGE,"E24.MirrorCS"),sQuery(id+"F15.wireOp",EDGE,"E25.MirrorCS"),sQuery(id+"F15.wireOp",EDGE,"E26.MirrorCS")])]}),"instanceName":"1"}),"instanceName":"1"}),"instanceName":"1"});
            transform(context, id + "F21", {"entities" : qUnion([Q0, Q1, Q2, Q3, Q4, Q5, Q6, Q7, Q8, Q9, Q10, Q11, Q12, Q13, Q14]), "transformType" : TransformType.TRANSLATION_3D, "dx" : 0 * mm, "dy" : 640 * mm, "dz" : 0 * mm, "makeCopy" : true});
        }
        {
            var Q0;
            Q0=makeQuery(id+"F16.opExtrude","SWEPT_BODY",BODY,{"disambiguationData":[OSD([sQuery(id+"F15.wireOp",EDGE,"E13.bottom"),sQuery(id+"F15.wireOp",EDGE,"E13.top"),sQuery(id+"F15.wireOp",EDGE,"E13.left"),sQuery(id+"F15.wireOp",EDGE,"E13.right"),sQuery(id+"F15.wireOp",EDGE,"E14.bottom"),sQuery(id+"F15.wireOp",EDGE,"E14.top"),sQuery(id+"F15.wireOp",EDGE,"E14.left"),sQuery(id+"F15.wireOp",EDGE,"E14.right"),sQuery(id+"F15.wireOp",EDGE,"E15.MirrorCS"),sQuery(id+"F15.wireOp",EDGE,"E16.MirrorCS"),sQuery(id+"F15.wireOp",EDGE,"E17.MirrorCS"),sQuery(id+"F15.wireOp",EDGE,"E18.MirrorCS"),sQuery(id+"F15.wireOp",EDGE,"E19.MirrorCS"),sQuery(id+"F15.wireOp",EDGE,"E20.MirrorCS"),sQuery(id+"F15.wireOp",EDGE,"E21.MirrorCS"),sQuery(id+"F15.wireOp",EDGE,"E22.MirrorCS"),sQuery(id+"F15.wireOp",EDGE,"E23.MirrorCS"),sQuery(id+"F15.wireOp",EDGE,"E24.MirrorCS"),sQuery(id+"F15.wireOp",EDGE,"E25.MirrorCS"),sQuery(id+"F15.wireOp",EDGE,"E26.MirrorCS")])]});
            var Q1;
            Q1=makeQuery(id+"F17.opPattern","COPY",BODY,{"derivedFrom":makeQuery(id+"F16.opExtrude","SWEPT_BODY",BODY,{"disambiguationData":[OSD([sQuery(id+"F15.wireOp",EDGE,"E13.bottom"),sQuery(id+"F15.wireOp",EDGE,"E13.top"),sQuery(id+"F15.wireOp",EDGE,"E13.left"),sQuery(id+"F15.wireOp",EDGE,"E13.right"),sQuery(id+"F15.wireOp",EDGE,"E14.bottom"),sQuery(id+"F15.wireOp",EDGE,"E14.top"),sQuery(id+"F15.wireOp",EDGE,"E14.left"),sQuery(id+"F15.wireOp",EDGE,"E14.right"),sQuery(id+"F15.wireOp",EDGE,"E15.MirrorCS"),sQuery(id+"F15.wireOp",EDGE,"E16.MirrorCS"),sQuery(id+"F15.wireOp",EDGE,"E17.MirrorCS"),sQuery(id+"F15.wireOp",EDGE,"E18.MirrorCS"),sQuery(id+"F15.wireOp",EDGE,"E19.MirrorCS"),sQuery(id+"F15.wireOp",EDGE,"E20.MirrorCS"),sQuery(id+"F15.wireOp",EDGE,"E21.MirrorCS"),sQuery(id+"F15.wireOp",EDGE,"E22.MirrorCS"),sQuery(id+"F15.wireOp",EDGE,"E23.MirrorCS"),sQuery(id+"F15.wireOp",EDGE,"E24.MirrorCS"),sQuery(id+"F15.wireOp",EDGE,"E25.MirrorCS"),sQuery(id+"F15.wireOp",EDGE,"E26.MirrorCS")])]}),"instanceName":"1"});
            var Q2;
            Q2=makeQuery(id+"F18.opPattern","COPY",BODY,{"derivedFrom":makeQuery(id+"F16.opExtrude","SWEPT_BODY",BODY,{"disambiguationData":[OSD([sQuery(id+"F15.wireOp",EDGE,"E13.bottom"),sQuery(id+"F15.wireOp",EDGE,"E13.top"),sQuery(id+"F15.wireOp",EDGE,"E13.left"),sQuery(id+"F15.wireOp",EDGE,"E13.right"),sQuery(id+"F15.wireOp",EDGE,"E14.bottom"),sQuery(id+"F15.wireOp",EDGE,"E14.top"),sQuery(id+"F15.wireOp",EDGE,"E14.left"),sQuery(id+"F15.wireOp",EDGE,"E14.right"),sQuery(id+"F15.wireOp",EDGE,"E15.MirrorCS"),sQuery(id+"F15.wireOp",EDGE,"E16.MirrorCS"),sQuery(id+"F15.wireOp",EDGE,"E17.MirrorCS"),sQuery(id+"F15.wireOp",EDGE,"E18.MirrorCS"),sQuery(id+"F15.wireOp",EDGE,"E19.MirrorCS"),sQuery(id+"F15.wireOp",EDGE,"E20.MirrorCS"),sQuery(id+"F15.wireOp",EDGE,"E21.MirrorCS"),sQuery(id+"F15.wireOp",EDGE,"E22.MirrorCS"),sQuery(id+"F15.wireOp",EDGE,"E23.MirrorCS"),sQuery(id+"F15.wireOp",EDGE,"E24.MirrorCS"),sQuery(id+"F15.wireOp",EDGE,"E25.MirrorCS"),sQuery(id+"F15.wireOp",EDGE,"E26.MirrorCS")])]}),"instanceName":"1"});
            var Q3;
            Q3=makeQuery(id+"F18.opPattern","COPY",BODY,{"derivedFrom":makeQuery(id+"F17.opPattern","COPY",BODY,{"derivedFrom":makeQuery(id+"F16.opExtrude","SWEPT_BODY",BODY,{"disambiguationData":[OSD([sQuery(id+"F15.wireOp",EDGE,"E13.bottom"),sQuery(id+"F15.wireOp",EDGE,"E13.top"),sQuery(id+"F15.wireOp",EDGE,"E13.left"),sQuery(id+"F15.wireOp",EDGE,"E13.right"),sQuery(id+"F15.wireOp",EDGE,"E14.bottom"),sQuery(id+"F15.wireOp",EDGE,"E14.top"),sQuery(id+"F15.wireOp",EDGE,"E14.left"),sQuery(id+"F15.wireOp",EDGE,"E14.right"),sQuery(id+"F15.wireOp",EDGE,"E15.MirrorCS"),sQuery(id+"F15.wireOp",EDGE,"E16.MirrorCS"),sQuery(id+"F15.wireOp",EDGE,"E17.MirrorCS"),sQuery(id+"F15.wireOp",EDGE,"E18.MirrorCS"),sQuery(id+"F15.wireOp",EDGE,"E19.MirrorCS"),sQuery(id+"F15.wireOp",EDGE,"E20.MirrorCS"),sQuery(id+"F15.wireOp",EDGE,"E21.MirrorCS"),sQuery(id+"F15.wireOp",EDGE,"E22.MirrorCS"),sQuery(id+"F15.wireOp",EDGE,"E23.MirrorCS"),sQuery(id+"F15.wireOp",EDGE,"E24.MirrorCS"),sQuery(id+"F15.wireOp",EDGE,"E25.MirrorCS"),sQuery(id+"F15.wireOp",EDGE,"E26.MirrorCS")])]}),"instanceName":"1"}),"instanceName":"1"});
            var Q4;
            Q4=makeQuery(id+"F19.opPattern","COPY",BODY,{"derivedFrom":makeQuery(id+"F16.opExtrude","SWEPT_BODY",BODY,{"disambiguationData":[OSD([sQuery(id+"F15.wireOp",EDGE,"E13.bottom"),sQuery(id+"F15.wireOp",EDGE,"E13.top"),sQuery(id+"F15.wireOp",EDGE,"E13.left"),sQuery(id+"F15.wireOp",EDGE,"E13.right"),sQuery(id+"F15.wireOp",EDGE,"E14.bottom"),sQuery(id+"F15.wireOp",EDGE,"E14.top"),sQuery(id+"F15.wireOp",EDGE,"E14.left"),sQuery(id+"F15.wireOp",EDGE,"E14.right"),sQuery(id+"F15.wireOp",EDGE,"E15.MirrorCS"),sQuery(id+"F15.wireOp",EDGE,"E16.MirrorCS"),sQuery(id+"F15.wireOp",EDGE,"E17.MirrorCS"),sQuery(id+"F15.wireOp",EDGE,"E18.MirrorCS"),sQuery(id+"F15.wireOp",EDGE,"E19.MirrorCS"),sQuery(id+"F15.wireOp",EDGE,"E20.MirrorCS"),sQuery(id+"F15.wireOp",EDGE,"E21.MirrorCS"),sQuery(id+"F15.wireOp",EDGE,"E22.MirrorCS"),sQuery(id+"F15.wireOp",EDGE,"E23.MirrorCS"),sQuery(id+"F15.wireOp",EDGE,"E24.MirrorCS"),sQuery(id+"F15.wireOp",EDGE,"E25.MirrorCS"),sQuery(id+"F15.wireOp",EDGE,"E26.MirrorCS")])]}),"instanceName":"1"});
            var Q5;
            Q5=makeQuery(id+"F19.opPattern","COPY",BODY,{"derivedFrom":makeQuery(id+"F17.opPattern","COPY",BODY,{"derivedFrom":makeQuery(id+"F16.opExtrude","SWEPT_BODY",BODY,{"disambiguationData":[OSD([sQuery(id+"F15.wireOp",EDGE,"E13.bottom"),sQuery(id+"F15.wireOp",EDGE,"E13.top"),sQuery(id+"F15.wireOp",EDGE,"E13.left"),sQuery(id+"F15.wireOp",EDGE,"E13.right"),sQuery(id+"F15.wireOp",EDGE,"E14.bottom"),sQuery(id+"F15.wireOp",EDGE,"E14.top"),sQuery(id+"F15.wireOp",EDGE,"E14.left"),sQuery(id+"F15.wireOp",EDGE,"E14.right"),sQuery(id+"F15.wireOp",EDGE,"E15.MirrorCS"),sQuery(id+"F15.wireOp",EDGE,"E16.MirrorCS"),sQuery(id+"F15.wireOp",EDGE,"E17.MirrorCS"),sQuery(id+"F15.wireOp",EDGE,"E18.MirrorCS"),sQuery(id+"F15.wireOp",EDGE,"E19.MirrorCS"),sQuery(id+"F15.wireOp",EDGE,"E20.MirrorCS"),sQuery(id+"F15.wireOp",EDGE,"E21.MirrorCS"),sQuery(id+"F15.wireOp",EDGE,"E22.MirrorCS"),sQuery(id+"F15.wireOp",EDGE,"E23.MirrorCS"),sQuery(id+"F15.wireOp",EDGE,"E24.MirrorCS"),sQuery(id+"F15.wireOp",EDGE,"E25.MirrorCS"),sQuery(id+"F15.wireOp",EDGE,"E26.MirrorCS")])]}),"instanceName":"1"}),"instanceName":"1"});
            var Q6;
            Q6=makeQuery(id+"F19.opPattern","COPY",BODY,{"derivedFrom":makeQuery(id+"F18.opPattern","COPY",BODY,{"derivedFrom":makeQuery(id+"F16.opExtrude","SWEPT_BODY",BODY,{"disambiguationData":[OSD([sQuery(id+"F15.wireOp",EDGE,"E13.bottom"),sQuery(id+"F15.wireOp",EDGE,"E13.top"),sQuery(id+"F15.wireOp",EDGE,"E13.left"),sQuery(id+"F15.wireOp",EDGE,"E13.right"),sQuery(id+"F15.wireOp",EDGE,"E14.bottom"),sQuery(id+"F15.wireOp",EDGE,"E14.top"),sQuery(id+"F15.wireOp",EDGE,"E14.left"),sQuery(id+"F15.wireOp",EDGE,"E14.right"),sQuery(id+"F15.wireOp",EDGE,"E15.MirrorCS"),sQuery(id+"F15.wireOp",EDGE,"E16.MirrorCS"),sQuery(id+"F15.wireOp",EDGE,"E17.MirrorCS"),sQuery(id+"F15.wireOp",EDGE,"E18.MirrorCS"),sQuery(id+"F15.wireOp",EDGE,"E19.MirrorCS"),sQuery(id+"F15.wireOp",EDGE,"E20.MirrorCS"),sQuery(id+"F15.wireOp",EDGE,"E21.MirrorCS"),sQuery(id+"F15.wireOp",EDGE,"E22.MirrorCS"),sQuery(id+"F15.wireOp",EDGE,"E23.MirrorCS"),sQuery(id+"F15.wireOp",EDGE,"E24.MirrorCS"),sQuery(id+"F15.wireOp",EDGE,"E25.MirrorCS"),sQuery(id+"F15.wireOp",EDGE,"E26.MirrorCS")])]}),"instanceName":"1"}),"instanceName":"1"});
            var Q7;
            Q7=makeQuery(id+"F19.opPattern","COPY",BODY,{"derivedFrom":makeQuery(id+"F18.opPattern","COPY",BODY,{"derivedFrom":makeQuery(id+"F17.opPattern","COPY",BODY,{"derivedFrom":makeQuery(id+"F16.opExtrude","SWEPT_BODY",BODY,{"disambiguationData":[OSD([sQuery(id+"F15.wireOp",EDGE,"E13.bottom"),sQuery(id+"F15.wireOp",EDGE,"E13.top"),sQuery(id+"F15.wireOp",EDGE,"E13.left"),sQuery(id+"F15.wireOp",EDGE,"E13.right"),sQuery(id+"F15.wireOp",EDGE,"E14.bottom"),sQuery(id+"F15.wireOp",EDGE,"E14.top"),sQuery(id+"F15.wireOp",EDGE,"E14.left"),sQuery(id+"F15.wireOp",EDGE,"E14.right"),sQuery(id+"F15.wireOp",EDGE,"E15.MirrorCS"),sQuery(id+"F15.wireOp",EDGE,"E16.MirrorCS"),sQuery(id+"F15.wireOp",EDGE,"E17.MirrorCS"),sQuery(id+"F15.wireOp",EDGE,"E18.MirrorCS"),sQuery(id+"F15.wireOp",EDGE,"E19.MirrorCS"),sQuery(id+"F15.wireOp",EDGE,"E20.MirrorCS"),sQuery(id+"F15.wireOp",EDGE,"E21.MirrorCS"),sQuery(id+"F15.wireOp",EDGE,"E22.MirrorCS"),sQuery(id+"F15.wireOp",EDGE,"E23.MirrorCS"),sQuery(id+"F15.wireOp",EDGE,"E24.MirrorCS"),sQuery(id+"F15.wireOp",EDGE,"E25.MirrorCS"),sQuery(id+"F15.wireOp",EDGE,"E26.MirrorCS")])]}),"instanceName":"1"}),"instanceName":"1"}),"instanceName":"1"});
            var Q8;
            Q8=makeQuery(id+"F20.opPattern","COPY",BODY,{"derivedFrom":makeQuery(id+"F16.opExtrude","SWEPT_BODY",BODY,{"disambiguationData":[OSD([sQuery(id+"F15.wireOp",EDGE,"E13.bottom"),sQuery(id+"F15.wireOp",EDGE,"E13.top"),sQuery(id+"F15.wireOp",EDGE,"E13.left"),sQuery(id+"F15.wireOp",EDGE,"E13.right"),sQuery(id+"F15.wireOp",EDGE,"E14.bottom"),sQuery(id+"F15.wireOp",EDGE,"E14.top"),sQuery(id+"F15.wireOp",EDGE,"E14.left"),sQuery(id+"F15.wireOp",EDGE,"E14.right"),sQuery(id+"F15.wireOp",EDGE,"E15.MirrorCS"),sQuery(id+"F15.wireOp",EDGE,"E16.MirrorCS"),sQuery(id+"F15.wireOp",EDGE,"E17.MirrorCS"),sQuery(id+"F15.wireOp",EDGE,"E18.MirrorCS"),sQuery(id+"F15.wireOp",EDGE,"E19.MirrorCS"),sQuery(id+"F15.wireOp",EDGE,"E20.MirrorCS"),sQuery(id+"F15.wireOp",EDGE,"E21.MirrorCS"),sQuery(id+"F15.wireOp",EDGE,"E22.MirrorCS"),sQuery(id+"F15.wireOp",EDGE,"E23.MirrorCS"),sQuery(id+"F15.wireOp",EDGE,"E24.MirrorCS"),sQuery(id+"F15.wireOp",EDGE,"E25.MirrorCS"),sQuery(id+"F15.wireOp",EDGE,"E26.MirrorCS")])]}),"instanceName":"1"});
            var Q9;
            Q9=makeQuery(id+"F20.opPattern","COPY",BODY,{"derivedFrom":makeQuery(id+"F17.opPattern","COPY",BODY,{"derivedFrom":makeQuery(id+"F16.opExtrude","SWEPT_BODY",BODY,{"disambiguationData":[OSD([sQuery(id+"F15.wireOp",EDGE,"E13.bottom"),sQuery(id+"F15.wireOp",EDGE,"E13.top"),sQuery(id+"F15.wireOp",EDGE,"E13.left"),sQuery(id+"F15.wireOp",EDGE,"E13.right"),sQuery(id+"F15.wireOp",EDGE,"E14.bottom"),sQuery(id+"F15.wireOp",EDGE,"E14.top"),sQuery(id+"F15.wireOp",EDGE,"E14.left"),sQuery(id+"F15.wireOp",EDGE,"E14.right"),sQuery(id+"F15.wireOp",EDGE,"E15.MirrorCS"),sQuery(id+"F15.wireOp",EDGE,"E16.MirrorCS"),sQuery(id+"F15.wireOp",EDGE,"E17.MirrorCS"),sQuery(id+"F15.wireOp",EDGE,"E18.MirrorCS"),sQuery(id+"F15.wireOp",EDGE,"E19.MirrorCS"),sQuery(id+"F15.wireOp",EDGE,"E20.MirrorCS"),sQuery(id+"F15.wireOp",EDGE,"E21.MirrorCS"),sQuery(id+"F15.wireOp",EDGE,"E22.MirrorCS"),sQuery(id+"F15.wireOp",EDGE,"E23.MirrorCS"),sQuery(id+"F15.wireOp",EDGE,"E24.MirrorCS"),sQuery(id+"F15.wireOp",EDGE,"E25.MirrorCS"),sQuery(id+"F15.wireOp",EDGE,"E26.MirrorCS")])]}),"instanceName":"1"}),"instanceName":"1"});
            var Q10;
            Q10=makeQuery(id+"F20.opPattern","COPY",BODY,{"derivedFrom":makeQuery(id+"F18.opPattern","COPY",BODY,{"derivedFrom":makeQuery(id+"F16.opExtrude","SWEPT_BODY",BODY,{"disambiguationData":[OSD([sQuery(id+"F15.wireOp",EDGE,"E13.bottom"),sQuery(id+"F15.wireOp",EDGE,"E13.top"),sQuery(id+"F15.wireOp",EDGE,"E13.left"),sQuery(id+"F15.wireOp",EDGE,"E13.right"),sQuery(id+"F15.wireOp",EDGE,"E14.bottom"),sQuery(id+"F15.wireOp",EDGE,"E14.top"),sQuery(id+"F15.wireOp",EDGE,"E14.left"),sQuery(id+"F15.wireOp",EDGE,"E14.right"),sQuery(id+"F15.wireOp",EDGE,"E15.MirrorCS"),sQuery(id+"F15.wireOp",EDGE,"E16.MirrorCS"),sQuery(id+"F15.wireOp",EDGE,"E17.MirrorCS"),sQuery(id+"F15.wireOp",EDGE,"E18.MirrorCS"),sQuery(id+"F15.wireOp",EDGE,"E19.MirrorCS"),sQuery(id+"F15.wireOp",EDGE,"E20.MirrorCS"),sQuery(id+"F15.wireOp",EDGE,"E21.MirrorCS"),sQuery(id+"F15.wireOp",EDGE,"E22.MirrorCS"),sQuery(id+"F15.wireOp",EDGE,"E23.MirrorCS"),sQuery(id+"F15.wireOp",EDGE,"E24.MirrorCS"),sQuery(id+"F15.wireOp",EDGE,"E25.MirrorCS"),sQuery(id+"F15.wireOp",EDGE,"E26.MirrorCS")])]}),"instanceName":"1"}),"instanceName":"1"});
            var Q11;
            Q11=makeQuery(id+"F20.opPattern","COPY",BODY,{"derivedFrom":makeQuery(id+"F18.opPattern","COPY",BODY,{"derivedFrom":makeQuery(id+"F17.opPattern","COPY",BODY,{"derivedFrom":makeQuery(id+"F16.opExtrude","SWEPT_BODY",BODY,{"disambiguationData":[OSD([sQuery(id+"F15.wireOp",EDGE,"E13.bottom"),sQuery(id+"F15.wireOp",EDGE,"E13.top"),sQuery(id+"F15.wireOp",EDGE,"E13.left"),sQuery(id+"F15.wireOp",EDGE,"E13.right"),sQuery(id+"F15.wireOp",EDGE,"E14.bottom"),sQuery(id+"F15.wireOp",EDGE,"E14.top"),sQuery(id+"F15.wireOp",EDGE,"E14.left"),sQuery(id+"F15.wireOp",EDGE,"E14.right"),sQuery(id+"F15.wireOp",EDGE,"E15.MirrorCS"),sQuery(id+"F15.wireOp",EDGE,"E16.MirrorCS"),sQuery(id+"F15.wireOp",EDGE,"E17.MirrorCS"),sQuery(id+"F15.wireOp",EDGE,"E18.MirrorCS"),sQuery(id+"F15.wireOp",EDGE,"E19.MirrorCS"),sQuery(id+"F15.wireOp",EDGE,"E20.MirrorCS"),sQuery(id+"F15.wireOp",EDGE,"E21.MirrorCS"),sQuery(id+"F15.wireOp",EDGE,"E22.MirrorCS"),sQuery(id+"F15.wireOp",EDGE,"E23.MirrorCS"),sQuery(id+"F15.wireOp",EDGE,"E24.MirrorCS"),sQuery(id+"F15.wireOp",EDGE,"E25.MirrorCS"),sQuery(id+"F15.wireOp",EDGE,"E26.MirrorCS")])]}),"instanceName":"1"}),"instanceName":"1"}),"instanceName":"1"});
            var Q12;
            Q12=makeQuery(id+"F20.opPattern","COPY",BODY,{"derivedFrom":makeQuery(id+"F19.opPattern","COPY",BODY,{"derivedFrom":makeQuery(id+"F16.opExtrude","SWEPT_BODY",BODY,{"disambiguationData":[OSD([sQuery(id+"F15.wireOp",EDGE,"E13.bottom"),sQuery(id+"F15.wireOp",EDGE,"E13.top"),sQuery(id+"F15.wireOp",EDGE,"E13.left"),sQuery(id+"F15.wireOp",EDGE,"E13.right"),sQuery(id+"F15.wireOp",EDGE,"E14.bottom"),sQuery(id+"F15.wireOp",EDGE,"E14.top"),sQuery(id+"F15.wireOp",EDGE,"E14.left"),sQuery(id+"F15.wireOp",EDGE,"E14.right"),sQuery(id+"F15.wireOp",EDGE,"E15.MirrorCS"),sQuery(id+"F15.wireOp",EDGE,"E16.MirrorCS"),sQuery(id+"F15.wireOp",EDGE,"E17.MirrorCS"),sQuery(id+"F15.wireOp",EDGE,"E18.MirrorCS"),sQuery(id+"F15.wireOp",EDGE,"E19.MirrorCS"),sQuery(id+"F15.wireOp",EDGE,"E20.MirrorCS"),sQuery(id+"F15.wireOp",EDGE,"E21.MirrorCS"),sQuery(id+"F15.wireOp",EDGE,"E22.MirrorCS"),sQuery(id+"F15.wireOp",EDGE,"E23.MirrorCS"),sQuery(id+"F15.wireOp",EDGE,"E24.MirrorCS"),sQuery(id+"F15.wireOp",EDGE,"E25.MirrorCS"),sQuery(id+"F15.wireOp",EDGE,"E26.MirrorCS")])]}),"instanceName":"1"}),"instanceName":"1"});
            var Q13;
            Q13=makeQuery(id+"F20.opPattern","COPY",BODY,{"derivedFrom":makeQuery(id+"F19.opPattern","COPY",BODY,{"derivedFrom":makeQuery(id+"F17.opPattern","COPY",BODY,{"derivedFrom":makeQuery(id+"F16.opExtrude","SWEPT_BODY",BODY,{"disambiguationData":[OSD([sQuery(id+"F15.wireOp",EDGE,"E13.bottom"),sQuery(id+"F15.wireOp",EDGE,"E13.top"),sQuery(id+"F15.wireOp",EDGE,"E13.left"),sQuery(id+"F15.wireOp",EDGE,"E13.right"),sQuery(id+"F15.wireOp",EDGE,"E14.bottom"),sQuery(id+"F15.wireOp",EDGE,"E14.top"),sQuery(id+"F15.wireOp",EDGE,"E14.left"),sQuery(id+"F15.wireOp",EDGE,"E14.right"),sQuery(id+"F15.wireOp",EDGE,"E15.MirrorCS"),sQuery(id+"F15.wireOp",EDGE,"E16.MirrorCS"),sQuery(id+"F15.wireOp",EDGE,"E17.MirrorCS"),sQuery(id+"F15.wireOp",EDGE,"E18.MirrorCS"),sQuery(id+"F15.wireOp",EDGE,"E19.MirrorCS"),sQuery(id+"F15.wireOp",EDGE,"E20.MirrorCS"),sQuery(id+"F15.wireOp",EDGE,"E21.MirrorCS"),sQuery(id+"F15.wireOp",EDGE,"E22.MirrorCS"),sQuery(id+"F15.wireOp",EDGE,"E23.MirrorCS"),sQuery(id+"F15.wireOp",EDGE,"E24.MirrorCS"),sQuery(id+"F15.wireOp",EDGE,"E25.MirrorCS"),sQuery(id+"F15.wireOp",EDGE,"E26.MirrorCS")])]}),"instanceName":"1"}),"instanceName":"1"}),"instanceName":"1"});
            var Q14;
            Q14=makeQuery(id+"F20.opPattern","COPY",BODY,{"derivedFrom":makeQuery(id+"F19.opPattern","COPY",BODY,{"derivedFrom":makeQuery(id+"F18.opPattern","COPY",BODY,{"derivedFrom":makeQuery(id+"F16.opExtrude","SWEPT_BODY",BODY,{"disambiguationData":[OSD([sQuery(id+"F15.wireOp",EDGE,"E13.bottom"),sQuery(id+"F15.wireOp",EDGE,"E13.top"),sQuery(id+"F15.wireOp",EDGE,"E13.left"),sQuery(id+"F15.wireOp",EDGE,"E13.right"),sQuery(id+"F15.wireOp",EDGE,"E14.bottom"),sQuery(id+"F15.wireOp",EDGE,"E14.top"),sQuery(id+"F15.wireOp",EDGE,"E14.left"),sQuery(id+"F15.wireOp",EDGE,"E14.right"),sQuery(id+"F15.wireOp",EDGE,"E15.MirrorCS"),sQuery(id+"F15.wireOp",EDGE,"E16.MirrorCS"),sQuery(id+"F15.wireOp",EDGE,"E17.MirrorCS"),sQuery(id+"F15.wireOp",EDGE,"E18.MirrorCS"),sQuery(id+"F15.wireOp",EDGE,"E19.MirrorCS"),sQuery(id+"F15.wireOp",EDGE,"E20.MirrorCS"),sQuery(id+"F15.wireOp",EDGE,"E21.MirrorCS"),sQuery(id+"F15.wireOp",EDGE,"E22.MirrorCS"),sQuery(id+"F15.wireOp",EDGE,"E23.MirrorCS"),sQuery(id+"F15.wireOp",EDGE,"E24.MirrorCS"),sQuery(id+"F15.wireOp",EDGE,"E25.MirrorCS"),sQuery(id+"F15.wireOp",EDGE,"E26.MirrorCS")])]}),"instanceName":"1"}),"instanceName":"1"}),"instanceName":"1"});
            var Q15;
            Q15=makeQuery(id+"F20.opPattern","COPY",BODY,{"derivedFrom":makeQuery(id+"F19.opPattern","COPY",BODY,{"derivedFrom":makeQuery(id+"F18.opPattern","COPY",BODY,{"derivedFrom":makeQuery(id+"F17.opPattern","COPY",BODY,{"derivedFrom":makeQuery(id+"F16.opExtrude","SWEPT_BODY",BODY,{"disambiguationData":[OSD([sQuery(id+"F15.wireOp",EDGE,"E13.bottom"),sQuery(id+"F15.wireOp",EDGE,"E13.top"),sQuery(id+"F15.wireOp",EDGE,"E13.left"),sQuery(id+"F15.wireOp",EDGE,"E13.right"),sQuery(id+"F15.wireOp",EDGE,"E14.bottom"),sQuery(id+"F15.wireOp",EDGE,"E14.top"),sQuery(id+"F15.wireOp",EDGE,"E14.left"),sQuery(id+"F15.wireOp",EDGE,"E14.right"),sQuery(id+"F15.wireOp",EDGE,"E15.MirrorCS"),sQuery(id+"F15.wireOp",EDGE,"E16.MirrorCS"),sQuery(id+"F15.wireOp",EDGE,"E17.MirrorCS"),sQuery(id+"F15.wireOp",EDGE,"E18.MirrorCS"),sQuery(id+"F15.wireOp",EDGE,"E19.MirrorCS"),sQuery(id+"F15.wireOp",EDGE,"E20.MirrorCS"),sQuery(id+"F15.wireOp",EDGE,"E21.MirrorCS"),sQuery(id+"F15.wireOp",EDGE,"E22.MirrorCS"),sQuery(id+"F15.wireOp",EDGE,"E23.MirrorCS"),sQuery(id+"F15.wireOp",EDGE,"E24.MirrorCS"),sQuery(id+"F15.wireOp",EDGE,"E25.MirrorCS"),sQuery(id+"F15.wireOp",EDGE,"E26.MirrorCS")])]}),"instanceName":"1"}),"instanceName":"1"}),"instanceName":"1"}),"instanceName":"1"});
            var Q16;
            Q16=makeQuery(id+"F21.opPattern","COPY",BODY,{"derivedFrom":makeQuery(id+"F16.opExtrude","SWEPT_BODY",BODY,{"disambiguationData":[OSD([sQuery(id+"F15.wireOp",EDGE,"E13.bottom"),sQuery(id+"F15.wireOp",EDGE,"E13.top"),sQuery(id+"F15.wireOp",EDGE,"E13.left"),sQuery(id+"F15.wireOp",EDGE,"E13.right"),sQuery(id+"F15.wireOp",EDGE,"E14.bottom"),sQuery(id+"F15.wireOp",EDGE,"E14.top"),sQuery(id+"F15.wireOp",EDGE,"E14.left"),sQuery(id+"F15.wireOp",EDGE,"E14.right"),sQuery(id+"F15.wireOp",EDGE,"E15.MirrorCS"),sQuery(id+"F15.wireOp",EDGE,"E16.MirrorCS"),sQuery(id+"F15.wireOp",EDGE,"E17.MirrorCS"),sQuery(id+"F15.wireOp",EDGE,"E18.MirrorCS"),sQuery(id+"F15.wireOp",EDGE,"E19.MirrorCS"),sQuery(id+"F15.wireOp",EDGE,"E20.MirrorCS"),sQuery(id+"F15.wireOp",EDGE,"E21.MirrorCS"),sQuery(id+"F15.wireOp",EDGE,"E22.MirrorCS"),sQuery(id+"F15.wireOp",EDGE,"E23.MirrorCS"),sQuery(id+"F15.wireOp",EDGE,"E24.MirrorCS"),sQuery(id+"F15.wireOp",EDGE,"E25.MirrorCS"),sQuery(id+"F15.wireOp",EDGE,"E26.MirrorCS")])]}),"instanceName":"1"});
            var Q17;
            Q17=makeQuery(id+"F21.opPattern","COPY",BODY,{"derivedFrom":makeQuery(id+"F17.opPattern","COPY",BODY,{"derivedFrom":makeQuery(id+"F16.opExtrude","SWEPT_BODY",BODY,{"disambiguationData":[OSD([sQuery(id+"F15.wireOp",EDGE,"E13.bottom"),sQuery(id+"F15.wireOp",EDGE,"E13.top"),sQuery(id+"F15.wireOp",EDGE,"E13.left"),sQuery(id+"F15.wireOp",EDGE,"E13.right"),sQuery(id+"F15.wireOp",EDGE,"E14.bottom"),sQuery(id+"F15.wireOp",EDGE,"E14.top"),sQuery(id+"F15.wireOp",EDGE,"E14.left"),sQuery(id+"F15.wireOp",EDGE,"E14.right"),sQuery(id+"F15.wireOp",EDGE,"E15.MirrorCS"),sQuery(id+"F15.wireOp",EDGE,"E16.MirrorCS"),sQuery(id+"F15.wireOp",EDGE,"E17.MirrorCS"),sQuery(id+"F15.wireOp",EDGE,"E18.MirrorCS"),sQuery(id+"F15.wireOp",EDGE,"E19.MirrorCS"),sQuery(id+"F15.wireOp",EDGE,"E20.MirrorCS"),sQuery(id+"F15.wireOp",EDGE,"E21.MirrorCS"),sQuery(id+"F15.wireOp",EDGE,"E22.MirrorCS"),sQuery(id+"F15.wireOp",EDGE,"E23.MirrorCS"),sQuery(id+"F15.wireOp",EDGE,"E24.MirrorCS"),sQuery(id+"F15.wireOp",EDGE,"E25.MirrorCS"),sQuery(id+"F15.wireOp",EDGE,"E26.MirrorCS")])]}),"instanceName":"1"}),"instanceName":"1"});
            var Q18;
            Q18=makeQuery(id+"F21.opPattern","COPY",BODY,{"derivedFrom":makeQuery(id+"F18.opPattern","COPY",BODY,{"derivedFrom":makeQuery(id+"F16.opExtrude","SWEPT_BODY",BODY,{"disambiguationData":[OSD([sQuery(id+"F15.wireOp",EDGE,"E13.bottom"),sQuery(id+"F15.wireOp",EDGE,"E13.top"),sQuery(id+"F15.wireOp",EDGE,"E13.left"),sQuery(id+"F15.wireOp",EDGE,"E13.right"),sQuery(id+"F15.wireOp",EDGE,"E14.bottom"),sQuery(id+"F15.wireOp",EDGE,"E14.top"),sQuery(id+"F15.wireOp",EDGE,"E14.left"),sQuery(id+"F15.wireOp",EDGE,"E14.right"),sQuery(id+"F15.wireOp",EDGE,"E15.MirrorCS"),sQuery(id+"F15.wireOp",EDGE,"E16.MirrorCS"),sQuery(id+"F15.wireOp",EDGE,"E17.MirrorCS"),sQuery(id+"F15.wireOp",EDGE,"E18.MirrorCS"),sQuery(id+"F15.wireOp",EDGE,"E19.MirrorCS"),sQuery(id+"F15.wireOp",EDGE,"E20.MirrorCS"),sQuery(id+"F15.wireOp",EDGE,"E21.MirrorCS"),sQuery(id+"F15.wireOp",EDGE,"E22.MirrorCS"),sQuery(id+"F15.wireOp",EDGE,"E23.MirrorCS"),sQuery(id+"F15.wireOp",EDGE,"E24.MirrorCS"),sQuery(id+"F15.wireOp",EDGE,"E25.MirrorCS"),sQuery(id+"F15.wireOp",EDGE,"E26.MirrorCS")])]}),"instanceName":"1"}),"instanceName":"1"});
            var Q19;
            Q19=makeQuery(id+"F21.opPattern","COPY",BODY,{"derivedFrom":makeQuery(id+"F18.opPattern","COPY",BODY,{"derivedFrom":makeQuery(id+"F17.opPattern","COPY",BODY,{"derivedFrom":makeQuery(id+"F16.opExtrude","SWEPT_BODY",BODY,{"disambiguationData":[OSD([sQuery(id+"F15.wireOp",EDGE,"E13.bottom"),sQuery(id+"F15.wireOp",EDGE,"E13.top"),sQuery(id+"F15.wireOp",EDGE,"E13.left"),sQuery(id+"F15.wireOp",EDGE,"E13.right"),sQuery(id+"F15.wireOp",EDGE,"E14.bottom"),sQuery(id+"F15.wireOp",EDGE,"E14.top"),sQuery(id+"F15.wireOp",EDGE,"E14.left"),sQuery(id+"F15.wireOp",EDGE,"E14.right"),sQuery(id+"F15.wireOp",EDGE,"E15.MirrorCS"),sQuery(id+"F15.wireOp",EDGE,"E16.MirrorCS"),sQuery(id+"F15.wireOp",EDGE,"E17.MirrorCS"),sQuery(id+"F15.wireOp",EDGE,"E18.MirrorCS"),sQuery(id+"F15.wireOp",EDGE,"E19.MirrorCS"),sQuery(id+"F15.wireOp",EDGE,"E20.MirrorCS"),sQuery(id+"F15.wireOp",EDGE,"E21.MirrorCS"),sQuery(id+"F15.wireOp",EDGE,"E22.MirrorCS"),sQuery(id+"F15.wireOp",EDGE,"E23.MirrorCS"),sQuery(id+"F15.wireOp",EDGE,"E24.MirrorCS"),sQuery(id+"F15.wireOp",EDGE,"E25.MirrorCS"),sQuery(id+"F15.wireOp",EDGE,"E26.MirrorCS")])]}),"instanceName":"1"}),"instanceName":"1"}),"instanceName":"1"});
            var Q20;
            Q20=makeQuery(id+"F21.opPattern","COPY",BODY,{"derivedFrom":makeQuery(id+"F19.opPattern","COPY",BODY,{"derivedFrom":makeQuery(id+"F16.opExtrude","SWEPT_BODY",BODY,{"disambiguationData":[OSD([sQuery(id+"F15.wireOp",EDGE,"E13.bottom"),sQuery(id+"F15.wireOp",EDGE,"E13.top"),sQuery(id+"F15.wireOp",EDGE,"E13.left"),sQuery(id+"F15.wireOp",EDGE,"E13.right"),sQuery(id+"F15.wireOp",EDGE,"E14.bottom"),sQuery(id+"F15.wireOp",EDGE,"E14.top"),sQuery(id+"F15.wireOp",EDGE,"E14.left"),sQuery(id+"F15.wireOp",EDGE,"E14.right"),sQuery(id+"F15.wireOp",EDGE,"E15.MirrorCS"),sQuery(id+"F15.wireOp",EDGE,"E16.MirrorCS"),sQuery(id+"F15.wireOp",EDGE,"E17.MirrorCS"),sQuery(id+"F15.wireOp",EDGE,"E18.MirrorCS"),sQuery(id+"F15.wireOp",EDGE,"E19.MirrorCS"),sQuery(id+"F15.wireOp",EDGE,"E20.MirrorCS"),sQuery(id+"F15.wireOp",EDGE,"E21.MirrorCS"),sQuery(id+"F15.wireOp",EDGE,"E22.MirrorCS"),sQuery(id+"F15.wireOp",EDGE,"E23.MirrorCS"),sQuery(id+"F15.wireOp",EDGE,"E24.MirrorCS"),sQuery(id+"F15.wireOp",EDGE,"E25.MirrorCS"),sQuery(id+"F15.wireOp",EDGE,"E26.MirrorCS")])]}),"instanceName":"1"}),"instanceName":"1"});
            var Q21;
            Q21=makeQuery(id+"F21.opPattern","COPY",BODY,{"derivedFrom":makeQuery(id+"F19.opPattern","COPY",BODY,{"derivedFrom":makeQuery(id+"F17.opPattern","COPY",BODY,{"derivedFrom":makeQuery(id+"F16.opExtrude","SWEPT_BODY",BODY,{"disambiguationData":[OSD([sQuery(id+"F15.wireOp",EDGE,"E13.bottom"),sQuery(id+"F15.wireOp",EDGE,"E13.top"),sQuery(id+"F15.wireOp",EDGE,"E13.left"),sQuery(id+"F15.wireOp",EDGE,"E13.right"),sQuery(id+"F15.wireOp",EDGE,"E14.bottom"),sQuery(id+"F15.wireOp",EDGE,"E14.top"),sQuery(id+"F15.wireOp",EDGE,"E14.left"),sQuery(id+"F15.wireOp",EDGE,"E14.right"),sQuery(id+"F15.wireOp",EDGE,"E15.MirrorCS"),sQuery(id+"F15.wireOp",EDGE,"E16.MirrorCS"),sQuery(id+"F15.wireOp",EDGE,"E17.MirrorCS"),sQuery(id+"F15.wireOp",EDGE,"E18.MirrorCS"),sQuery(id+"F15.wireOp",EDGE,"E19.MirrorCS"),sQuery(id+"F15.wireOp",EDGE,"E20.MirrorCS"),sQuery(id+"F15.wireOp",EDGE,"E21.MirrorCS"),sQuery(id+"F15.wireOp",EDGE,"E22.MirrorCS"),sQuery(id+"F15.wireOp",EDGE,"E23.MirrorCS"),sQuery(id+"F15.wireOp",EDGE,"E24.MirrorCS"),sQuery(id+"F15.wireOp",EDGE,"E25.MirrorCS"),sQuery(id+"F15.wireOp",EDGE,"E26.MirrorCS")])]}),"instanceName":"1"}),"instanceName":"1"}),"instanceName":"1"});
            var Q22;
            Q22=makeQuery(id+"F21.opPattern","COPY",BODY,{"derivedFrom":makeQuery(id+"F19.opPattern","COPY",BODY,{"derivedFrom":makeQuery(id+"F18.opPattern","COPY",BODY,{"derivedFrom":makeQuery(id+"F16.opExtrude","SWEPT_BODY",BODY,{"disambiguationData":[OSD([sQuery(id+"F15.wireOp",EDGE,"E13.bottom"),sQuery(id+"F15.wireOp",EDGE,"E13.top"),sQuery(id+"F15.wireOp",EDGE,"E13.left"),sQuery(id+"F15.wireOp",EDGE,"E13.right"),sQuery(id+"F15.wireOp",EDGE,"E14.bottom"),sQuery(id+"F15.wireOp",EDGE,"E14.top"),sQuery(id+"F15.wireOp",EDGE,"E14.left"),sQuery(id+"F15.wireOp",EDGE,"E14.right"),sQuery(id+"F15.wireOp",EDGE,"E15.MirrorCS"),sQuery(id+"F15.wireOp",EDGE,"E16.MirrorCS"),sQuery(id+"F15.wireOp",EDGE,"E17.MirrorCS"),sQuery(id+"F15.wireOp",EDGE,"E18.MirrorCS"),sQuery(id+"F15.wireOp",EDGE,"E19.MirrorCS"),sQuery(id+"F15.wireOp",EDGE,"E20.MirrorCS"),sQuery(id+"F15.wireOp",EDGE,"E21.MirrorCS"),sQuery(id+"F15.wireOp",EDGE,"E22.MirrorCS"),sQuery(id+"F15.wireOp",EDGE,"E23.MirrorCS"),sQuery(id+"F15.wireOp",EDGE,"E24.MirrorCS"),sQuery(id+"F15.wireOp",EDGE,"E25.MirrorCS"),sQuery(id+"F15.wireOp",EDGE,"E26.MirrorCS")])]}),"instanceName":"1"}),"instanceName":"1"}),"instanceName":"1"});
            var Q23;
            Q23=makeQuery(id+"F21.opPattern","COPY",BODY,{"derivedFrom":makeQuery(id+"F19.opPattern","COPY",BODY,{"derivedFrom":makeQuery(id+"F18.opPattern","COPY",BODY,{"derivedFrom":makeQuery(id+"F17.opPattern","COPY",BODY,{"derivedFrom":makeQuery(id+"F16.opExtrude","SWEPT_BODY",BODY,{"disambiguationData":[OSD([sQuery(id+"F15.wireOp",EDGE,"E13.bottom"),sQuery(id+"F15.wireOp",EDGE,"E13.top"),sQuery(id+"F15.wireOp",EDGE,"E13.left"),sQuery(id+"F15.wireOp",EDGE,"E13.right"),sQuery(id+"F15.wireOp",EDGE,"E14.bottom"),sQuery(id+"F15.wireOp",EDGE,"E14.top"),sQuery(id+"F15.wireOp",EDGE,"E14.left"),sQuery(id+"F15.wireOp",EDGE,"E14.right"),sQuery(id+"F15.wireOp",EDGE,"E15.MirrorCS"),sQuery(id+"F15.wireOp",EDGE,"E16.MirrorCS"),sQuery(id+"F15.wireOp",EDGE,"E17.MirrorCS"),sQuery(id+"F15.wireOp",EDGE,"E18.MirrorCS"),sQuery(id+"F15.wireOp",EDGE,"E19.MirrorCS"),sQuery(id+"F15.wireOp",EDGE,"E20.MirrorCS"),sQuery(id+"F15.wireOp",EDGE,"E21.MirrorCS"),sQuery(id+"F15.wireOp",EDGE,"E22.MirrorCS"),sQuery(id+"F15.wireOp",EDGE,"E23.MirrorCS"),sQuery(id+"F15.wireOp",EDGE,"E24.MirrorCS"),sQuery(id+"F15.wireOp",EDGE,"E25.MirrorCS"),sQuery(id+"F15.wireOp",EDGE,"E26.MirrorCS")])]}),"instanceName":"1"}),"instanceName":"1"}),"instanceName":"1"}),"instanceName":"1"});
            var Q24;
            Q24=makeQuery(id+"F21.opPattern","COPY",BODY,{"derivedFrom":makeQuery(id+"F20.opPattern","COPY",BODY,{"derivedFrom":makeQuery(id+"F16.opExtrude","SWEPT_BODY",BODY,{"disambiguationData":[OSD([sQuery(id+"F15.wireOp",EDGE,"E13.bottom"),sQuery(id+"F15.wireOp",EDGE,"E13.top"),sQuery(id+"F15.wireOp",EDGE,"E13.left"),sQuery(id+"F15.wireOp",EDGE,"E13.right"),sQuery(id+"F15.wireOp",EDGE,"E14.bottom"),sQuery(id+"F15.wireOp",EDGE,"E14.top"),sQuery(id+"F15.wireOp",EDGE,"E14.left"),sQuery(id+"F15.wireOp",EDGE,"E14.right"),sQuery(id+"F15.wireOp",EDGE,"E15.MirrorCS"),sQuery(id+"F15.wireOp",EDGE,"E16.MirrorCS"),sQuery(id+"F15.wireOp",EDGE,"E17.MirrorCS"),sQuery(id+"F15.wireOp",EDGE,"E18.MirrorCS"),sQuery(id+"F15.wireOp",EDGE,"E19.MirrorCS"),sQuery(id+"F15.wireOp",EDGE,"E20.MirrorCS"),sQuery(id+"F15.wireOp",EDGE,"E21.MirrorCS"),sQuery(id+"F15.wireOp",EDGE,"E22.MirrorCS"),sQuery(id+"F15.wireOp",EDGE,"E23.MirrorCS"),sQuery(id+"F15.wireOp",EDGE,"E24.MirrorCS"),sQuery(id+"F15.wireOp",EDGE,"E25.MirrorCS"),sQuery(id+"F15.wireOp",EDGE,"E26.MirrorCS")])]}),"instanceName":"1"}),"instanceName":"1"});
            var Q25;
            Q25=makeQuery(id+"F21.opPattern","COPY",BODY,{"derivedFrom":makeQuery(id+"F20.opPattern","COPY",BODY,{"derivedFrom":makeQuery(id+"F17.opPattern","COPY",BODY,{"derivedFrom":makeQuery(id+"F16.opExtrude","SWEPT_BODY",BODY,{"disambiguationData":[OSD([sQuery(id+"F15.wireOp",EDGE,"E13.bottom"),sQuery(id+"F15.wireOp",EDGE,"E13.top"),sQuery(id+"F15.wireOp",EDGE,"E13.left"),sQuery(id+"F15.wireOp",EDGE,"E13.right"),sQuery(id+"F15.wireOp",EDGE,"E14.bottom"),sQuery(id+"F15.wireOp",EDGE,"E14.top"),sQuery(id+"F15.wireOp",EDGE,"E14.left"),sQuery(id+"F15.wireOp",EDGE,"E14.right"),sQuery(id+"F15.wireOp",EDGE,"E15.MirrorCS"),sQuery(id+"F15.wireOp",EDGE,"E16.MirrorCS"),sQuery(id+"F15.wireOp",EDGE,"E17.MirrorCS"),sQuery(id+"F15.wireOp",EDGE,"E18.MirrorCS"),sQuery(id+"F15.wireOp",EDGE,"E19.MirrorCS"),sQuery(id+"F15.wireOp",EDGE,"E20.MirrorCS"),sQuery(id+"F15.wireOp",EDGE,"E21.MirrorCS"),sQuery(id+"F15.wireOp",EDGE,"E22.MirrorCS"),sQuery(id+"F15.wireOp",EDGE,"E23.MirrorCS"),sQuery(id+"F15.wireOp",EDGE,"E24.MirrorCS"),sQuery(id+"F15.wireOp",EDGE,"E25.MirrorCS"),sQuery(id+"F15.wireOp",EDGE,"E26.MirrorCS")])]}),"instanceName":"1"}),"instanceName":"1"}),"instanceName":"1"});
            var Q26;
            Q26=makeQuery(id+"F21.opPattern","COPY",BODY,{"derivedFrom":makeQuery(id+"F20.opPattern","COPY",BODY,{"derivedFrom":makeQuery(id+"F18.opPattern","COPY",BODY,{"derivedFrom":makeQuery(id+"F16.opExtrude","SWEPT_BODY",BODY,{"disambiguationData":[OSD([sQuery(id+"F15.wireOp",EDGE,"E13.bottom"),sQuery(id+"F15.wireOp",EDGE,"E13.top"),sQuery(id+"F15.wireOp",EDGE,"E13.left"),sQuery(id+"F15.wireOp",EDGE,"E13.right"),sQuery(id+"F15.wireOp",EDGE,"E14.bottom"),sQuery(id+"F15.wireOp",EDGE,"E14.top"),sQuery(id+"F15.wireOp",EDGE,"E14.left"),sQuery(id+"F15.wireOp",EDGE,"E14.right"),sQuery(id+"F15.wireOp",EDGE,"E15.MirrorCS"),sQuery(id+"F15.wireOp",EDGE,"E16.MirrorCS"),sQuery(id+"F15.wireOp",EDGE,"E17.MirrorCS"),sQuery(id+"F15.wireOp",EDGE,"E18.MirrorCS"),sQuery(id+"F15.wireOp",EDGE,"E19.MirrorCS"),sQuery(id+"F15.wireOp",EDGE,"E20.MirrorCS"),sQuery(id+"F15.wireOp",EDGE,"E21.MirrorCS"),sQuery(id+"F15.wireOp",EDGE,"E22.MirrorCS"),sQuery(id+"F15.wireOp",EDGE,"E23.MirrorCS"),sQuery(id+"F15.wireOp",EDGE,"E24.MirrorCS"),sQuery(id+"F15.wireOp",EDGE,"E25.MirrorCS"),sQuery(id+"F15.wireOp",EDGE,"E26.MirrorCS")])]}),"instanceName":"1"}),"instanceName":"1"}),"instanceName":"1"});
            var Q27;
            Q27=makeQuery(id+"F21.opPattern","COPY",BODY,{"derivedFrom":makeQuery(id+"F20.opPattern","COPY",BODY,{"derivedFrom":makeQuery(id+"F18.opPattern","COPY",BODY,{"derivedFrom":makeQuery(id+"F17.opPattern","COPY",BODY,{"derivedFrom":makeQuery(id+"F16.opExtrude","SWEPT_BODY",BODY,{"disambiguationData":[OSD([sQuery(id+"F15.wireOp",EDGE,"E13.bottom"),sQuery(id+"F15.wireOp",EDGE,"E13.top"),sQuery(id+"F15.wireOp",EDGE,"E13.left"),sQuery(id+"F15.wireOp",EDGE,"E13.right"),sQuery(id+"F15.wireOp",EDGE,"E14.bottom"),sQuery(id+"F15.wireOp",EDGE,"E14.top"),sQuery(id+"F15.wireOp",EDGE,"E14.left"),sQuery(id+"F15.wireOp",EDGE,"E14.right"),sQuery(id+"F15.wireOp",EDGE,"E15.MirrorCS"),sQuery(id+"F15.wireOp",EDGE,"E16.MirrorCS"),sQuery(id+"F15.wireOp",EDGE,"E17.MirrorCS"),sQuery(id+"F15.wireOp",EDGE,"E18.MirrorCS"),sQuery(id+"F15.wireOp",EDGE,"E19.MirrorCS"),sQuery(id+"F15.wireOp",EDGE,"E20.MirrorCS"),sQuery(id+"F15.wireOp",EDGE,"E21.MirrorCS"),sQuery(id+"F15.wireOp",EDGE,"E22.MirrorCS"),sQuery(id+"F15.wireOp",EDGE,"E23.MirrorCS"),sQuery(id+"F15.wireOp",EDGE,"E24.MirrorCS"),sQuery(id+"F15.wireOp",EDGE,"E25.MirrorCS"),sQuery(id+"F15.wireOp",EDGE,"E26.MirrorCS")])]}),"instanceName":"1"}),"instanceName":"1"}),"instanceName":"1"}),"instanceName":"1"});
            var Q28;
            Q28=makeQuery(id+"F21.opPattern","COPY",BODY,{"derivedFrom":makeQuery(id+"F20.opPattern","COPY",BODY,{"derivedFrom":makeQuery(id+"F19.opPattern","COPY",BODY,{"derivedFrom":makeQuery(id+"F16.opExtrude","SWEPT_BODY",BODY,{"disambiguationData":[OSD([sQuery(id+"F15.wireOp",EDGE,"E13.bottom"),sQuery(id+"F15.wireOp",EDGE,"E13.top"),sQuery(id+"F15.wireOp",EDGE,"E13.left"),sQuery(id+"F15.wireOp",EDGE,"E13.right"),sQuery(id+"F15.wireOp",EDGE,"E14.bottom"),sQuery(id+"F15.wireOp",EDGE,"E14.top"),sQuery(id+"F15.wireOp",EDGE,"E14.left"),sQuery(id+"F15.wireOp",EDGE,"E14.right"),sQuery(id+"F15.wireOp",EDGE,"E15.MirrorCS"),sQuery(id+"F15.wireOp",EDGE,"E16.MirrorCS"),sQuery(id+"F15.wireOp",EDGE,"E17.MirrorCS"),sQuery(id+"F15.wireOp",EDGE,"E18.MirrorCS"),sQuery(id+"F15.wireOp",EDGE,"E19.MirrorCS"),sQuery(id+"F15.wireOp",EDGE,"E20.MirrorCS"),sQuery(id+"F15.wireOp",EDGE,"E21.MirrorCS"),sQuery(id+"F15.wireOp",EDGE,"E22.MirrorCS"),sQuery(id+"F15.wireOp",EDGE,"E23.MirrorCS"),sQuery(id+"F15.wireOp",EDGE,"E24.MirrorCS"),sQuery(id+"F15.wireOp",EDGE,"E25.MirrorCS"),sQuery(id+"F15.wireOp",EDGE,"E26.MirrorCS")])]}),"instanceName":"1"}),"instanceName":"1"}),"instanceName":"1"});
            var Q29;
            Q29=makeQuery(id+"F21.opPattern","COPY",BODY,{"derivedFrom":makeQuery(id+"F20.opPattern","COPY",BODY,{"derivedFrom":makeQuery(id+"F19.opPattern","COPY",BODY,{"derivedFrom":makeQuery(id+"F17.opPattern","COPY",BODY,{"derivedFrom":makeQuery(id+"F16.opExtrude","SWEPT_BODY",BODY,{"disambiguationData":[OSD([sQuery(id+"F15.wireOp",EDGE,"E13.bottom"),sQuery(id+"F15.wireOp",EDGE,"E13.top"),sQuery(id+"F15.wireOp",EDGE,"E13.left"),sQuery(id+"F15.wireOp",EDGE,"E13.right"),sQuery(id+"F15.wireOp",EDGE,"E14.bottom"),sQuery(id+"F15.wireOp",EDGE,"E14.top"),sQuery(id+"F15.wireOp",EDGE,"E14.left"),sQuery(id+"F15.wireOp",EDGE,"E14.right"),sQuery(id+"F15.wireOp",EDGE,"E15.MirrorCS"),sQuery(id+"F15.wireOp",EDGE,"E16.MirrorCS"),sQuery(id+"F15.wireOp",EDGE,"E17.MirrorCS"),sQuery(id+"F15.wireOp",EDGE,"E18.MirrorCS"),sQuery(id+"F15.wireOp",EDGE,"E19.MirrorCS"),sQuery(id+"F15.wireOp",EDGE,"E20.MirrorCS"),sQuery(id+"F15.wireOp",EDGE,"E21.MirrorCS"),sQuery(id+"F15.wireOp",EDGE,"E22.MirrorCS"),sQuery(id+"F15.wireOp",EDGE,"E23.MirrorCS"),sQuery(id+"F15.wireOp",EDGE,"E24.MirrorCS"),sQuery(id+"F15.wireOp",EDGE,"E25.MirrorCS"),sQuery(id+"F15.wireOp",EDGE,"E26.MirrorCS")])]}),"instanceName":"1"}),"instanceName":"1"}),"instanceName":"1"}),"instanceName":"1"});
            var Q30;
            Q30=makeQuery(id+"F21.opPattern","COPY",BODY,{"derivedFrom":makeQuery(id+"F20.opPattern","COPY",BODY,{"derivedFrom":makeQuery(id+"F19.opPattern","COPY",BODY,{"derivedFrom":makeQuery(id+"F18.opPattern","COPY",BODY,{"derivedFrom":makeQuery(id+"F16.opExtrude","SWEPT_BODY",BODY,{"disambiguationData":[OSD([sQuery(id+"F15.wireOp",EDGE,"E13.bottom"),sQuery(id+"F15.wireOp",EDGE,"E13.top"),sQuery(id+"F15.wireOp",EDGE,"E13.left"),sQuery(id+"F15.wireOp",EDGE,"E13.right"),sQuery(id+"F15.wireOp",EDGE,"E14.bottom"),sQuery(id+"F15.wireOp",EDGE,"E14.top"),sQuery(id+"F15.wireOp",EDGE,"E14.left"),sQuery(id+"F15.wireOp",EDGE,"E14.right"),sQuery(id+"F15.wireOp",EDGE,"E15.MirrorCS"),sQuery(id+"F15.wireOp",EDGE,"E16.MirrorCS"),sQuery(id+"F15.wireOp",EDGE,"E17.MirrorCS"),sQuery(id+"F15.wireOp",EDGE,"E18.MirrorCS"),sQuery(id+"F15.wireOp",EDGE,"E19.MirrorCS"),sQuery(id+"F15.wireOp",EDGE,"E20.MirrorCS"),sQuery(id+"F15.wireOp",EDGE,"E21.MirrorCS"),sQuery(id+"F15.wireOp",EDGE,"E22.MirrorCS"),sQuery(id+"F15.wireOp",EDGE,"E23.MirrorCS"),sQuery(id+"F15.wireOp",EDGE,"E24.MirrorCS"),sQuery(id+"F15.wireOp",EDGE,"E25.MirrorCS"),sQuery(id+"F15.wireOp",EDGE,"E26.MirrorCS")])]}),"instanceName":"1"}),"instanceName":"1"}),"instanceName":"1"}),"instanceName":"1"});
            transform(context, id + "F22", {"entities" : qUnion([Q0, Q1, Q2, Q3, Q4, Q5, Q6, Q7, Q8, Q9, Q10, Q11, Q12, Q13, Q14, Q15, Q16, Q17, Q18, Q19, Q20, Q21, Q22, Q23, Q24, Q25, Q26, Q27, Q28, Q29, Q30]), "transformType" : TransformType.TRANSLATION_3D, "dx" : -40 * mm, "dy" : 0 * mm, "dz" : 0 * mm, "makeCopy" : true});
        }
        {
            var Q0;
            Q0=makeQuery(id+"F16.opExtrude","SWEPT_BODY",BODY,{"disambiguationData":[OSD([sQuery(id+"F15.wireOp",EDGE,"E13.bottom"),sQuery(id+"F15.wireOp",EDGE,"E13.top"),sQuery(id+"F15.wireOp",EDGE,"E13.left"),sQuery(id+"F15.wireOp",EDGE,"E13.right"),sQuery(id+"F15.wireOp",EDGE,"E14.bottom"),sQuery(id+"F15.wireOp",EDGE,"E14.top"),sQuery(id+"F15.wireOp",EDGE,"E14.left"),sQuery(id+"F15.wireOp",EDGE,"E14.right"),sQuery(id+"F15.wireOp",EDGE,"E15.MirrorCS"),sQuery(id+"F15.wireOp",EDGE,"E16.MirrorCS"),sQuery(id+"F15.wireOp",EDGE,"E17.MirrorCS"),sQuery(id+"F15.wireOp",EDGE,"E18.MirrorCS"),sQuery(id+"F15.wireOp",EDGE,"E19.MirrorCS"),sQuery(id+"F15.wireOp",EDGE,"E20.MirrorCS"),sQuery(id+"F15.wireOp",EDGE,"E21.MirrorCS"),sQuery(id+"F15.wireOp",EDGE,"E22.MirrorCS"),sQuery(id+"F15.wireOp",EDGE,"E23.MirrorCS"),sQuery(id+"F15.wireOp",EDGE,"E24.MirrorCS"),sQuery(id+"F15.wireOp",EDGE,"E25.MirrorCS"),sQuery(id+"F15.wireOp",EDGE,"E26.MirrorCS")])]});
            var Q1;
            Q1=makeQuery(id+"F17.opPattern","COPY",BODY,{"derivedFrom":makeQuery(id+"F16.opExtrude","SWEPT_BODY",BODY,{"disambiguationData":[OSD([sQuery(id+"F15.wireOp",EDGE,"E13.bottom"),sQuery(id+"F15.wireOp",EDGE,"E13.top"),sQuery(id+"F15.wireOp",EDGE,"E13.left"),sQuery(id+"F15.wireOp",EDGE,"E13.right"),sQuery(id+"F15.wireOp",EDGE,"E14.bottom"),sQuery(id+"F15.wireOp",EDGE,"E14.top"),sQuery(id+"F15.wireOp",EDGE,"E14.left"),sQuery(id+"F15.wireOp",EDGE,"E14.right"),sQuery(id+"F15.wireOp",EDGE,"E15.MirrorCS"),sQuery(id+"F15.wireOp",EDGE,"E16.MirrorCS"),sQuery(id+"F15.wireOp",EDGE,"E17.MirrorCS"),sQuery(id+"F15.wireOp",EDGE,"E18.MirrorCS"),sQuery(id+"F15.wireOp",EDGE,"E19.MirrorCS"),sQuery(id+"F15.wireOp",EDGE,"E20.MirrorCS"),sQuery(id+"F15.wireOp",EDGE,"E21.MirrorCS"),sQuery(id+"F15.wireOp",EDGE,"E22.MirrorCS"),sQuery(id+"F15.wireOp",EDGE,"E23.MirrorCS"),sQuery(id+"F15.wireOp",EDGE,"E24.MirrorCS"),sQuery(id+"F15.wireOp",EDGE,"E25.MirrorCS"),sQuery(id+"F15.wireOp",EDGE,"E26.MirrorCS")])]}),"instanceName":"1"});
            var Q2;
            Q2=makeQuery(id+"F18.opPattern","COPY",BODY,{"derivedFrom":makeQuery(id+"F16.opExtrude","SWEPT_BODY",BODY,{"disambiguationData":[OSD([sQuery(id+"F15.wireOp",EDGE,"E13.bottom"),sQuery(id+"F15.wireOp",EDGE,"E13.top"),sQuery(id+"F15.wireOp",EDGE,"E13.left"),sQuery(id+"F15.wireOp",EDGE,"E13.right"),sQuery(id+"F15.wireOp",EDGE,"E14.bottom"),sQuery(id+"F15.wireOp",EDGE,"E14.top"),sQuery(id+"F15.wireOp",EDGE,"E14.left"),sQuery(id+"F15.wireOp",EDGE,"E14.right"),sQuery(id+"F15.wireOp",EDGE,"E15.MirrorCS"),sQuery(id+"F15.wireOp",EDGE,"E16.MirrorCS"),sQuery(id+"F15.wireOp",EDGE,"E17.MirrorCS"),sQuery(id+"F15.wireOp",EDGE,"E18.MirrorCS"),sQuery(id+"F15.wireOp",EDGE,"E19.MirrorCS"),sQuery(id+"F15.wireOp",EDGE,"E20.MirrorCS"),sQuery(id+"F15.wireOp",EDGE,"E21.MirrorCS"),sQuery(id+"F15.wireOp",EDGE,"E22.MirrorCS"),sQuery(id+"F15.wireOp",EDGE,"E23.MirrorCS"),sQuery(id+"F15.wireOp",EDGE,"E24.MirrorCS"),sQuery(id+"F15.wireOp",EDGE,"E25.MirrorCS"),sQuery(id+"F15.wireOp",EDGE,"E26.MirrorCS")])]}),"instanceName":"1"});
            var Q3;
            Q3=makeQuery(id+"F18.opPattern","COPY",BODY,{"derivedFrom":makeQuery(id+"F17.opPattern","COPY",BODY,{"derivedFrom":makeQuery(id+"F16.opExtrude","SWEPT_BODY",BODY,{"disambiguationData":[OSD([sQuery(id+"F15.wireOp",EDGE,"E13.bottom"),sQuery(id+"F15.wireOp",EDGE,"E13.top"),sQuery(id+"F15.wireOp",EDGE,"E13.left"),sQuery(id+"F15.wireOp",EDGE,"E13.right"),sQuery(id+"F15.wireOp",EDGE,"E14.bottom"),sQuery(id+"F15.wireOp",EDGE,"E14.top"),sQuery(id+"F15.wireOp",EDGE,"E14.left"),sQuery(id+"F15.wireOp",EDGE,"E14.right"),sQuery(id+"F15.wireOp",EDGE,"E15.MirrorCS"),sQuery(id+"F15.wireOp",EDGE,"E16.MirrorCS"),sQuery(id+"F15.wireOp",EDGE,"E17.MirrorCS"),sQuery(id+"F15.wireOp",EDGE,"E18.MirrorCS"),sQuery(id+"F15.wireOp",EDGE,"E19.MirrorCS"),sQuery(id+"F15.wireOp",EDGE,"E20.MirrorCS"),sQuery(id+"F15.wireOp",EDGE,"E21.MirrorCS"),sQuery(id+"F15.wireOp",EDGE,"E22.MirrorCS"),sQuery(id+"F15.wireOp",EDGE,"E23.MirrorCS"),sQuery(id+"F15.wireOp",EDGE,"E24.MirrorCS"),sQuery(id+"F15.wireOp",EDGE,"E25.MirrorCS"),sQuery(id+"F15.wireOp",EDGE,"E26.MirrorCS")])]}),"instanceName":"1"}),"instanceName":"1"});
            var Q4;
            Q4=makeQuery(id+"F19.opPattern","COPY",BODY,{"derivedFrom":makeQuery(id+"F16.opExtrude","SWEPT_BODY",BODY,{"disambiguationData":[OSD([sQuery(id+"F15.wireOp",EDGE,"E13.bottom"),sQuery(id+"F15.wireOp",EDGE,"E13.top"),sQuery(id+"F15.wireOp",EDGE,"E13.left"),sQuery(id+"F15.wireOp",EDGE,"E13.right"),sQuery(id+"F15.wireOp",EDGE,"E14.bottom"),sQuery(id+"F15.wireOp",EDGE,"E14.top"),sQuery(id+"F15.wireOp",EDGE,"E14.left"),sQuery(id+"F15.wireOp",EDGE,"E14.right"),sQuery(id+"F15.wireOp",EDGE,"E15.MirrorCS"),sQuery(id+"F15.wireOp",EDGE,"E16.MirrorCS"),sQuery(id+"F15.wireOp",EDGE,"E17.MirrorCS"),sQuery(id+"F15.wireOp",EDGE,"E18.MirrorCS"),sQuery(id+"F15.wireOp",EDGE,"E19.MirrorCS"),sQuery(id+"F15.wireOp",EDGE,"E20.MirrorCS"),sQuery(id+"F15.wireOp",EDGE,"E21.MirrorCS"),sQuery(id+"F15.wireOp",EDGE,"E22.MirrorCS"),sQuery(id+"F15.wireOp",EDGE,"E23.MirrorCS"),sQuery(id+"F15.wireOp",EDGE,"E24.MirrorCS"),sQuery(id+"F15.wireOp",EDGE,"E25.MirrorCS"),sQuery(id+"F15.wireOp",EDGE,"E26.MirrorCS")])]}),"instanceName":"1"});
            var Q5;
            Q5=makeQuery(id+"F19.opPattern","COPY",BODY,{"derivedFrom":makeQuery(id+"F17.opPattern","COPY",BODY,{"derivedFrom":makeQuery(id+"F16.opExtrude","SWEPT_BODY",BODY,{"disambiguationData":[OSD([sQuery(id+"F15.wireOp",EDGE,"E13.bottom"),sQuery(id+"F15.wireOp",EDGE,"E13.top"),sQuery(id+"F15.wireOp",EDGE,"E13.left"),sQuery(id+"F15.wireOp",EDGE,"E13.right"),sQuery(id+"F15.wireOp",EDGE,"E14.bottom"),sQuery(id+"F15.wireOp",EDGE,"E14.top"),sQuery(id+"F15.wireOp",EDGE,"E14.left"),sQuery(id+"F15.wireOp",EDGE,"E14.right"),sQuery(id+"F15.wireOp",EDGE,"E15.MirrorCS"),sQuery(id+"F15.wireOp",EDGE,"E16.MirrorCS"),sQuery(id+"F15.wireOp",EDGE,"E17.MirrorCS"),sQuery(id+"F15.wireOp",EDGE,"E18.MirrorCS"),sQuery(id+"F15.wireOp",EDGE,"E19.MirrorCS"),sQuery(id+"F15.wireOp",EDGE,"E20.MirrorCS"),sQuery(id+"F15.wireOp",EDGE,"E21.MirrorCS"),sQuery(id+"F15.wireOp",EDGE,"E22.MirrorCS"),sQuery(id+"F15.wireOp",EDGE,"E23.MirrorCS"),sQuery(id+"F15.wireOp",EDGE,"E24.MirrorCS"),sQuery(id+"F15.wireOp",EDGE,"E25.MirrorCS"),sQuery(id+"F15.wireOp",EDGE,"E26.MirrorCS")])]}),"instanceName":"1"}),"instanceName":"1"});
            var Q6;
            Q6=makeQuery(id+"F19.opPattern","COPY",BODY,{"derivedFrom":makeQuery(id+"F18.opPattern","COPY",BODY,{"derivedFrom":makeQuery(id+"F16.opExtrude","SWEPT_BODY",BODY,{"disambiguationData":[OSD([sQuery(id+"F15.wireOp",EDGE,"E13.bottom"),sQuery(id+"F15.wireOp",EDGE,"E13.top"),sQuery(id+"F15.wireOp",EDGE,"E13.left"),sQuery(id+"F15.wireOp",EDGE,"E13.right"),sQuery(id+"F15.wireOp",EDGE,"E14.bottom"),sQuery(id+"F15.wireOp",EDGE,"E14.top"),sQuery(id+"F15.wireOp",EDGE,"E14.left"),sQuery(id+"F15.wireOp",EDGE,"E14.right"),sQuery(id+"F15.wireOp",EDGE,"E15.MirrorCS"),sQuery(id+"F15.wireOp",EDGE,"E16.MirrorCS"),sQuery(id+"F15.wireOp",EDGE,"E17.MirrorCS"),sQuery(id+"F15.wireOp",EDGE,"E18.MirrorCS"),sQuery(id+"F15.wireOp",EDGE,"E19.MirrorCS"),sQuery(id+"F15.wireOp",EDGE,"E20.MirrorCS"),sQuery(id+"F15.wireOp",EDGE,"E21.MirrorCS"),sQuery(id+"F15.wireOp",EDGE,"E22.MirrorCS"),sQuery(id+"F15.wireOp",EDGE,"E23.MirrorCS"),sQuery(id+"F15.wireOp",EDGE,"E24.MirrorCS"),sQuery(id+"F15.wireOp",EDGE,"E25.MirrorCS"),sQuery(id+"F15.wireOp",EDGE,"E26.MirrorCS")])]}),"instanceName":"1"}),"instanceName":"1"});
            var Q7;
            Q7=makeQuery(id+"F19.opPattern","COPY",BODY,{"derivedFrom":makeQuery(id+"F18.opPattern","COPY",BODY,{"derivedFrom":makeQuery(id+"F17.opPattern","COPY",BODY,{"derivedFrom":makeQuery(id+"F16.opExtrude","SWEPT_BODY",BODY,{"disambiguationData":[OSD([sQuery(id+"F15.wireOp",EDGE,"E13.bottom"),sQuery(id+"F15.wireOp",EDGE,"E13.top"),sQuery(id+"F15.wireOp",EDGE,"E13.left"),sQuery(id+"F15.wireOp",EDGE,"E13.right"),sQuery(id+"F15.wireOp",EDGE,"E14.bottom"),sQuery(id+"F15.wireOp",EDGE,"E14.top"),sQuery(id+"F15.wireOp",EDGE,"E14.left"),sQuery(id+"F15.wireOp",EDGE,"E14.right"),sQuery(id+"F15.wireOp",EDGE,"E15.MirrorCS"),sQuery(id+"F15.wireOp",EDGE,"E16.MirrorCS"),sQuery(id+"F15.wireOp",EDGE,"E17.MirrorCS"),sQuery(id+"F15.wireOp",EDGE,"E18.MirrorCS"),sQuery(id+"F15.wireOp",EDGE,"E19.MirrorCS"),sQuery(id+"F15.wireOp",EDGE,"E20.MirrorCS"),sQuery(id+"F15.wireOp",EDGE,"E21.MirrorCS"),sQuery(id+"F15.wireOp",EDGE,"E22.MirrorCS"),sQuery(id+"F15.wireOp",EDGE,"E23.MirrorCS"),sQuery(id+"F15.wireOp",EDGE,"E24.MirrorCS"),sQuery(id+"F15.wireOp",EDGE,"E25.MirrorCS"),sQuery(id+"F15.wireOp",EDGE,"E26.MirrorCS")])]}),"instanceName":"1"}),"instanceName":"1"}),"instanceName":"1"});
            var Q8;
            Q8=makeQuery(id+"F20.opPattern","COPY",BODY,{"derivedFrom":makeQuery(id+"F16.opExtrude","SWEPT_BODY",BODY,{"disambiguationData":[OSD([sQuery(id+"F15.wireOp",EDGE,"E13.bottom"),sQuery(id+"F15.wireOp",EDGE,"E13.top"),sQuery(id+"F15.wireOp",EDGE,"E13.left"),sQuery(id+"F15.wireOp",EDGE,"E13.right"),sQuery(id+"F15.wireOp",EDGE,"E14.bottom"),sQuery(id+"F15.wireOp",EDGE,"E14.top"),sQuery(id+"F15.wireOp",EDGE,"E14.left"),sQuery(id+"F15.wireOp",EDGE,"E14.right"),sQuery(id+"F15.wireOp",EDGE,"E15.MirrorCS"),sQuery(id+"F15.wireOp",EDGE,"E16.MirrorCS"),sQuery(id+"F15.wireOp",EDGE,"E17.MirrorCS"),sQuery(id+"F15.wireOp",EDGE,"E18.MirrorCS"),sQuery(id+"F15.wireOp",EDGE,"E19.MirrorCS"),sQuery(id+"F15.wireOp",EDGE,"E20.MirrorCS"),sQuery(id+"F15.wireOp",EDGE,"E21.MirrorCS"),sQuery(id+"F15.wireOp",EDGE,"E22.MirrorCS"),sQuery(id+"F15.wireOp",EDGE,"E23.MirrorCS"),sQuery(id+"F15.wireOp",EDGE,"E24.MirrorCS"),sQuery(id+"F15.wireOp",EDGE,"E25.MirrorCS"),sQuery(id+"F15.wireOp",EDGE,"E26.MirrorCS")])]}),"instanceName":"1"});
            var Q9;
            Q9=makeQuery(id+"F20.opPattern","COPY",BODY,{"derivedFrom":makeQuery(id+"F17.opPattern","COPY",BODY,{"derivedFrom":makeQuery(id+"F16.opExtrude","SWEPT_BODY",BODY,{"disambiguationData":[OSD([sQuery(id+"F15.wireOp",EDGE,"E13.bottom"),sQuery(id+"F15.wireOp",EDGE,"E13.top"),sQuery(id+"F15.wireOp",EDGE,"E13.left"),sQuery(id+"F15.wireOp",EDGE,"E13.right"),sQuery(id+"F15.wireOp",EDGE,"E14.bottom"),sQuery(id+"F15.wireOp",EDGE,"E14.top"),sQuery(id+"F15.wireOp",EDGE,"E14.left"),sQuery(id+"F15.wireOp",EDGE,"E14.right"),sQuery(id+"F15.wireOp",EDGE,"E15.MirrorCS"),sQuery(id+"F15.wireOp",EDGE,"E16.MirrorCS"),sQuery(id+"F15.wireOp",EDGE,"E17.MirrorCS"),sQuery(id+"F15.wireOp",EDGE,"E18.MirrorCS"),sQuery(id+"F15.wireOp",EDGE,"E19.MirrorCS"),sQuery(id+"F15.wireOp",EDGE,"E20.MirrorCS"),sQuery(id+"F15.wireOp",EDGE,"E21.MirrorCS"),sQuery(id+"F15.wireOp",EDGE,"E22.MirrorCS"),sQuery(id+"F15.wireOp",EDGE,"E23.MirrorCS"),sQuery(id+"F15.wireOp",EDGE,"E24.MirrorCS"),sQuery(id+"F15.wireOp",EDGE,"E25.MirrorCS"),sQuery(id+"F15.wireOp",EDGE,"E26.MirrorCS")])]}),"instanceName":"1"}),"instanceName":"1"});
            var Q10;
            Q10=makeQuery(id+"F20.opPattern","COPY",BODY,{"derivedFrom":makeQuery(id+"F18.opPattern","COPY",BODY,{"derivedFrom":makeQuery(id+"F16.opExtrude","SWEPT_BODY",BODY,{"disambiguationData":[OSD([sQuery(id+"F15.wireOp",EDGE,"E13.bottom"),sQuery(id+"F15.wireOp",EDGE,"E13.top"),sQuery(id+"F15.wireOp",EDGE,"E13.left"),sQuery(id+"F15.wireOp",EDGE,"E13.right"),sQuery(id+"F15.wireOp",EDGE,"E14.bottom"),sQuery(id+"F15.wireOp",EDGE,"E14.top"),sQuery(id+"F15.wireOp",EDGE,"E14.left"),sQuery(id+"F15.wireOp",EDGE,"E14.right"),sQuery(id+"F15.wireOp",EDGE,"E15.MirrorCS"),sQuery(id+"F15.wireOp",EDGE,"E16.MirrorCS"),sQuery(id+"F15.wireOp",EDGE,"E17.MirrorCS"),sQuery(id+"F15.wireOp",EDGE,"E18.MirrorCS"),sQuery(id+"F15.wireOp",EDGE,"E19.MirrorCS"),sQuery(id+"F15.wireOp",EDGE,"E20.MirrorCS"),sQuery(id+"F15.wireOp",EDGE,"E21.MirrorCS"),sQuery(id+"F15.wireOp",EDGE,"E22.MirrorCS"),sQuery(id+"F15.wireOp",EDGE,"E23.MirrorCS"),sQuery(id+"F15.wireOp",EDGE,"E24.MirrorCS"),sQuery(id+"F15.wireOp",EDGE,"E25.MirrorCS"),sQuery(id+"F15.wireOp",EDGE,"E26.MirrorCS")])]}),"instanceName":"1"}),"instanceName":"1"});
            var Q11;
            Q11=makeQuery(id+"F20.opPattern","COPY",BODY,{"derivedFrom":makeQuery(id+"F18.opPattern","COPY",BODY,{"derivedFrom":makeQuery(id+"F17.opPattern","COPY",BODY,{"derivedFrom":makeQuery(id+"F16.opExtrude","SWEPT_BODY",BODY,{"disambiguationData":[OSD([sQuery(id+"F15.wireOp",EDGE,"E13.bottom"),sQuery(id+"F15.wireOp",EDGE,"E13.top"),sQuery(id+"F15.wireOp",EDGE,"E13.left"),sQuery(id+"F15.wireOp",EDGE,"E13.right"),sQuery(id+"F15.wireOp",EDGE,"E14.bottom"),sQuery(id+"F15.wireOp",EDGE,"E14.top"),sQuery(id+"F15.wireOp",EDGE,"E14.left"),sQuery(id+"F15.wireOp",EDGE,"E14.right"),sQuery(id+"F15.wireOp",EDGE,"E15.MirrorCS"),sQuery(id+"F15.wireOp",EDGE,"E16.MirrorCS"),sQuery(id+"F15.wireOp",EDGE,"E17.MirrorCS"),sQuery(id+"F15.wireOp",EDGE,"E18.MirrorCS"),sQuery(id+"F15.wireOp",EDGE,"E19.MirrorCS"),sQuery(id+"F15.wireOp",EDGE,"E20.MirrorCS"),sQuery(id+"F15.wireOp",EDGE,"E21.MirrorCS"),sQuery(id+"F15.wireOp",EDGE,"E22.MirrorCS"),sQuery(id+"F15.wireOp",EDGE,"E23.MirrorCS"),sQuery(id+"F15.wireOp",EDGE,"E24.MirrorCS"),sQuery(id+"F15.wireOp",EDGE,"E25.MirrorCS"),sQuery(id+"F15.wireOp",EDGE,"E26.MirrorCS")])]}),"instanceName":"1"}),"instanceName":"1"}),"instanceName":"1"});
            var Q12;
            Q12=makeQuery(id+"F20.opPattern","COPY",BODY,{"derivedFrom":makeQuery(id+"F19.opPattern","COPY",BODY,{"derivedFrom":makeQuery(id+"F16.opExtrude","SWEPT_BODY",BODY,{"disambiguationData":[OSD([sQuery(id+"F15.wireOp",EDGE,"E13.bottom"),sQuery(id+"F15.wireOp",EDGE,"E13.top"),sQuery(id+"F15.wireOp",EDGE,"E13.left"),sQuery(id+"F15.wireOp",EDGE,"E13.right"),sQuery(id+"F15.wireOp",EDGE,"E14.bottom"),sQuery(id+"F15.wireOp",EDGE,"E14.top"),sQuery(id+"F15.wireOp",EDGE,"E14.left"),sQuery(id+"F15.wireOp",EDGE,"E14.right"),sQuery(id+"F15.wireOp",EDGE,"E15.MirrorCS"),sQuery(id+"F15.wireOp",EDGE,"E16.MirrorCS"),sQuery(id+"F15.wireOp",EDGE,"E17.MirrorCS"),sQuery(id+"F15.wireOp",EDGE,"E18.MirrorCS"),sQuery(id+"F15.wireOp",EDGE,"E19.MirrorCS"),sQuery(id+"F15.wireOp",EDGE,"E20.MirrorCS"),sQuery(id+"F15.wireOp",EDGE,"E21.MirrorCS"),sQuery(id+"F15.wireOp",EDGE,"E22.MirrorCS"),sQuery(id+"F15.wireOp",EDGE,"E23.MirrorCS"),sQuery(id+"F15.wireOp",EDGE,"E24.MirrorCS"),sQuery(id+"F15.wireOp",EDGE,"E25.MirrorCS"),sQuery(id+"F15.wireOp",EDGE,"E26.MirrorCS")])]}),"instanceName":"1"}),"instanceName":"1"});
            var Q13;
            Q13=makeQuery(id+"F20.opPattern","COPY",BODY,{"derivedFrom":makeQuery(id+"F19.opPattern","COPY",BODY,{"derivedFrom":makeQuery(id+"F17.opPattern","COPY",BODY,{"derivedFrom":makeQuery(id+"F16.opExtrude","SWEPT_BODY",BODY,{"disambiguationData":[OSD([sQuery(id+"F15.wireOp",EDGE,"E13.bottom"),sQuery(id+"F15.wireOp",EDGE,"E13.top"),sQuery(id+"F15.wireOp",EDGE,"E13.left"),sQuery(id+"F15.wireOp",EDGE,"E13.right"),sQuery(id+"F15.wireOp",EDGE,"E14.bottom"),sQuery(id+"F15.wireOp",EDGE,"E14.top"),sQuery(id+"F15.wireOp",EDGE,"E14.left"),sQuery(id+"F15.wireOp",EDGE,"E14.right"),sQuery(id+"F15.wireOp",EDGE,"E15.MirrorCS"),sQuery(id+"F15.wireOp",EDGE,"E16.MirrorCS"),sQuery(id+"F15.wireOp",EDGE,"E17.MirrorCS"),sQuery(id+"F15.wireOp",EDGE,"E18.MirrorCS"),sQuery(id+"F15.wireOp",EDGE,"E19.MirrorCS"),sQuery(id+"F15.wireOp",EDGE,"E20.MirrorCS"),sQuery(id+"F15.wireOp",EDGE,"E21.MirrorCS"),sQuery(id+"F15.wireOp",EDGE,"E22.MirrorCS"),sQuery(id+"F15.wireOp",EDGE,"E23.MirrorCS"),sQuery(id+"F15.wireOp",EDGE,"E24.MirrorCS"),sQuery(id+"F15.wireOp",EDGE,"E25.MirrorCS"),sQuery(id+"F15.wireOp",EDGE,"E26.MirrorCS")])]}),"instanceName":"1"}),"instanceName":"1"}),"instanceName":"1"});
            var Q14;
            Q14=makeQuery(id+"F20.opPattern","COPY",BODY,{"derivedFrom":makeQuery(id+"F19.opPattern","COPY",BODY,{"derivedFrom":makeQuery(id+"F18.opPattern","COPY",BODY,{"derivedFrom":makeQuery(id+"F16.opExtrude","SWEPT_BODY",BODY,{"disambiguationData":[OSD([sQuery(id+"F15.wireOp",EDGE,"E13.bottom"),sQuery(id+"F15.wireOp",EDGE,"E13.top"),sQuery(id+"F15.wireOp",EDGE,"E13.left"),sQuery(id+"F15.wireOp",EDGE,"E13.right"),sQuery(id+"F15.wireOp",EDGE,"E14.bottom"),sQuery(id+"F15.wireOp",EDGE,"E14.top"),sQuery(id+"F15.wireOp",EDGE,"E14.left"),sQuery(id+"F15.wireOp",EDGE,"E14.right"),sQuery(id+"F15.wireOp",EDGE,"E15.MirrorCS"),sQuery(id+"F15.wireOp",EDGE,"E16.MirrorCS"),sQuery(id+"F15.wireOp",EDGE,"E17.MirrorCS"),sQuery(id+"F15.wireOp",EDGE,"E18.MirrorCS"),sQuery(id+"F15.wireOp",EDGE,"E19.MirrorCS"),sQuery(id+"F15.wireOp",EDGE,"E20.MirrorCS"),sQuery(id+"F15.wireOp",EDGE,"E21.MirrorCS"),sQuery(id+"F15.wireOp",EDGE,"E22.MirrorCS"),sQuery(id+"F15.wireOp",EDGE,"E23.MirrorCS"),sQuery(id+"F15.wireOp",EDGE,"E24.MirrorCS"),sQuery(id+"F15.wireOp",EDGE,"E25.MirrorCS"),sQuery(id+"F15.wireOp",EDGE,"E26.MirrorCS")])]}),"instanceName":"1"}),"instanceName":"1"}),"instanceName":"1"});
            var Q15;
            Q15=makeQuery(id+"F20.opPattern","COPY",BODY,{"derivedFrom":makeQuery(id+"F19.opPattern","COPY",BODY,{"derivedFrom":makeQuery(id+"F18.opPattern","COPY",BODY,{"derivedFrom":makeQuery(id+"F17.opPattern","COPY",BODY,{"derivedFrom":makeQuery(id+"F16.opExtrude","SWEPT_BODY",BODY,{"disambiguationData":[OSD([sQuery(id+"F15.wireOp",EDGE,"E13.bottom"),sQuery(id+"F15.wireOp",EDGE,"E13.top"),sQuery(id+"F15.wireOp",EDGE,"E13.left"),sQuery(id+"F15.wireOp",EDGE,"E13.right"),sQuery(id+"F15.wireOp",EDGE,"E14.bottom"),sQuery(id+"F15.wireOp",EDGE,"E14.top"),sQuery(id+"F15.wireOp",EDGE,"E14.left"),sQuery(id+"F15.wireOp",EDGE,"E14.right"),sQuery(id+"F15.wireOp",EDGE,"E15.MirrorCS"),sQuery(id+"F15.wireOp",EDGE,"E16.MirrorCS"),sQuery(id+"F15.wireOp",EDGE,"E17.MirrorCS"),sQuery(id+"F15.wireOp",EDGE,"E18.MirrorCS"),sQuery(id+"F15.wireOp",EDGE,"E19.MirrorCS"),sQuery(id+"F15.wireOp",EDGE,"E20.MirrorCS"),sQuery(id+"F15.wireOp",EDGE,"E21.MirrorCS"),sQuery(id+"F15.wireOp",EDGE,"E22.MirrorCS"),sQuery(id+"F15.wireOp",EDGE,"E23.MirrorCS"),sQuery(id+"F15.wireOp",EDGE,"E24.MirrorCS"),sQuery(id+"F15.wireOp",EDGE,"E25.MirrorCS"),sQuery(id+"F15.wireOp",EDGE,"E26.MirrorCS")])]}),"instanceName":"1"}),"instanceName":"1"}),"instanceName":"1"}),"instanceName":"1"});
            var Q16;
            Q16=makeQuery(id+"F21.opPattern","COPY",BODY,{"derivedFrom":makeQuery(id+"F16.opExtrude","SWEPT_BODY",BODY,{"disambiguationData":[OSD([sQuery(id+"F15.wireOp",EDGE,"E13.bottom"),sQuery(id+"F15.wireOp",EDGE,"E13.top"),sQuery(id+"F15.wireOp",EDGE,"E13.left"),sQuery(id+"F15.wireOp",EDGE,"E13.right"),sQuery(id+"F15.wireOp",EDGE,"E14.bottom"),sQuery(id+"F15.wireOp",EDGE,"E14.top"),sQuery(id+"F15.wireOp",EDGE,"E14.left"),sQuery(id+"F15.wireOp",EDGE,"E14.right"),sQuery(id+"F15.wireOp",EDGE,"E15.MirrorCS"),sQuery(id+"F15.wireOp",EDGE,"E16.MirrorCS"),sQuery(id+"F15.wireOp",EDGE,"E17.MirrorCS"),sQuery(id+"F15.wireOp",EDGE,"E18.MirrorCS"),sQuery(id+"F15.wireOp",EDGE,"E19.MirrorCS"),sQuery(id+"F15.wireOp",EDGE,"E20.MirrorCS"),sQuery(id+"F15.wireOp",EDGE,"E21.MirrorCS"),sQuery(id+"F15.wireOp",EDGE,"E22.MirrorCS"),sQuery(id+"F15.wireOp",EDGE,"E23.MirrorCS"),sQuery(id+"F15.wireOp",EDGE,"E24.MirrorCS"),sQuery(id+"F15.wireOp",EDGE,"E25.MirrorCS"),sQuery(id+"F15.wireOp",EDGE,"E26.MirrorCS")])]}),"instanceName":"1"});
            var Q17;
            Q17=makeQuery(id+"F21.opPattern","COPY",BODY,{"derivedFrom":makeQuery(id+"F17.opPattern","COPY",BODY,{"derivedFrom":makeQuery(id+"F16.opExtrude","SWEPT_BODY",BODY,{"disambiguationData":[OSD([sQuery(id+"F15.wireOp",EDGE,"E13.bottom"),sQuery(id+"F15.wireOp",EDGE,"E13.top"),sQuery(id+"F15.wireOp",EDGE,"E13.left"),sQuery(id+"F15.wireOp",EDGE,"E13.right"),sQuery(id+"F15.wireOp",EDGE,"E14.bottom"),sQuery(id+"F15.wireOp",EDGE,"E14.top"),sQuery(id+"F15.wireOp",EDGE,"E14.left"),sQuery(id+"F15.wireOp",EDGE,"E14.right"),sQuery(id+"F15.wireOp",EDGE,"E15.MirrorCS"),sQuery(id+"F15.wireOp",EDGE,"E16.MirrorCS"),sQuery(id+"F15.wireOp",EDGE,"E17.MirrorCS"),sQuery(id+"F15.wireOp",EDGE,"E18.MirrorCS"),sQuery(id+"F15.wireOp",EDGE,"E19.MirrorCS"),sQuery(id+"F15.wireOp",EDGE,"E20.MirrorCS"),sQuery(id+"F15.wireOp",EDGE,"E21.MirrorCS"),sQuery(id+"F15.wireOp",EDGE,"E22.MirrorCS"),sQuery(id+"F15.wireOp",EDGE,"E23.MirrorCS"),sQuery(id+"F15.wireOp",EDGE,"E24.MirrorCS"),sQuery(id+"F15.wireOp",EDGE,"E25.MirrorCS"),sQuery(id+"F15.wireOp",EDGE,"E26.MirrorCS")])]}),"instanceName":"1"}),"instanceName":"1"});
            var Q18;
            Q18=makeQuery(id+"F21.opPattern","COPY",BODY,{"derivedFrom":makeQuery(id+"F18.opPattern","COPY",BODY,{"derivedFrom":makeQuery(id+"F16.opExtrude","SWEPT_BODY",BODY,{"disambiguationData":[OSD([sQuery(id+"F15.wireOp",EDGE,"E13.bottom"),sQuery(id+"F15.wireOp",EDGE,"E13.top"),sQuery(id+"F15.wireOp",EDGE,"E13.left"),sQuery(id+"F15.wireOp",EDGE,"E13.right"),sQuery(id+"F15.wireOp",EDGE,"E14.bottom"),sQuery(id+"F15.wireOp",EDGE,"E14.top"),sQuery(id+"F15.wireOp",EDGE,"E14.left"),sQuery(id+"F15.wireOp",EDGE,"E14.right"),sQuery(id+"F15.wireOp",EDGE,"E15.MirrorCS"),sQuery(id+"F15.wireOp",EDGE,"E16.MirrorCS"),sQuery(id+"F15.wireOp",EDGE,"E17.MirrorCS"),sQuery(id+"F15.wireOp",EDGE,"E18.MirrorCS"),sQuery(id+"F15.wireOp",EDGE,"E19.MirrorCS"),sQuery(id+"F15.wireOp",EDGE,"E20.MirrorCS"),sQuery(id+"F15.wireOp",EDGE,"E21.MirrorCS"),sQuery(id+"F15.wireOp",EDGE,"E22.MirrorCS"),sQuery(id+"F15.wireOp",EDGE,"E23.MirrorCS"),sQuery(id+"F15.wireOp",EDGE,"E24.MirrorCS"),sQuery(id+"F15.wireOp",EDGE,"E25.MirrorCS"),sQuery(id+"F15.wireOp",EDGE,"E26.MirrorCS")])]}),"instanceName":"1"}),"instanceName":"1"});
            var Q19;
            Q19=makeQuery(id+"F21.opPattern","COPY",BODY,{"derivedFrom":makeQuery(id+"F18.opPattern","COPY",BODY,{"derivedFrom":makeQuery(id+"F17.opPattern","COPY",BODY,{"derivedFrom":makeQuery(id+"F16.opExtrude","SWEPT_BODY",BODY,{"disambiguationData":[OSD([sQuery(id+"F15.wireOp",EDGE,"E13.bottom"),sQuery(id+"F15.wireOp",EDGE,"E13.top"),sQuery(id+"F15.wireOp",EDGE,"E13.left"),sQuery(id+"F15.wireOp",EDGE,"E13.right"),sQuery(id+"F15.wireOp",EDGE,"E14.bottom"),sQuery(id+"F15.wireOp",EDGE,"E14.top"),sQuery(id+"F15.wireOp",EDGE,"E14.left"),sQuery(id+"F15.wireOp",EDGE,"E14.right"),sQuery(id+"F15.wireOp",EDGE,"E15.MirrorCS"),sQuery(id+"F15.wireOp",EDGE,"E16.MirrorCS"),sQuery(id+"F15.wireOp",EDGE,"E17.MirrorCS"),sQuery(id+"F15.wireOp",EDGE,"E18.MirrorCS"),sQuery(id+"F15.wireOp",EDGE,"E19.MirrorCS"),sQuery(id+"F15.wireOp",EDGE,"E20.MirrorCS"),sQuery(id+"F15.wireOp",EDGE,"E21.MirrorCS"),sQuery(id+"F15.wireOp",EDGE,"E22.MirrorCS"),sQuery(id+"F15.wireOp",EDGE,"E23.MirrorCS"),sQuery(id+"F15.wireOp",EDGE,"E24.MirrorCS"),sQuery(id+"F15.wireOp",EDGE,"E25.MirrorCS"),sQuery(id+"F15.wireOp",EDGE,"E26.MirrorCS")])]}),"instanceName":"1"}),"instanceName":"1"}),"instanceName":"1"});
            var Q20;
            Q20=makeQuery(id+"F21.opPattern","COPY",BODY,{"derivedFrom":makeQuery(id+"F19.opPattern","COPY",BODY,{"derivedFrom":makeQuery(id+"F16.opExtrude","SWEPT_BODY",BODY,{"disambiguationData":[OSD([sQuery(id+"F15.wireOp",EDGE,"E13.bottom"),sQuery(id+"F15.wireOp",EDGE,"E13.top"),sQuery(id+"F15.wireOp",EDGE,"E13.left"),sQuery(id+"F15.wireOp",EDGE,"E13.right"),sQuery(id+"F15.wireOp",EDGE,"E14.bottom"),sQuery(id+"F15.wireOp",EDGE,"E14.top"),sQuery(id+"F15.wireOp",EDGE,"E14.left"),sQuery(id+"F15.wireOp",EDGE,"E14.right"),sQuery(id+"F15.wireOp",EDGE,"E15.MirrorCS"),sQuery(id+"F15.wireOp",EDGE,"E16.MirrorCS"),sQuery(id+"F15.wireOp",EDGE,"E17.MirrorCS"),sQuery(id+"F15.wireOp",EDGE,"E18.MirrorCS"),sQuery(id+"F15.wireOp",EDGE,"E19.MirrorCS"),sQuery(id+"F15.wireOp",EDGE,"E20.MirrorCS"),sQuery(id+"F15.wireOp",EDGE,"E21.MirrorCS"),sQuery(id+"F15.wireOp",EDGE,"E22.MirrorCS"),sQuery(id+"F15.wireOp",EDGE,"E23.MirrorCS"),sQuery(id+"F15.wireOp",EDGE,"E24.MirrorCS"),sQuery(id+"F15.wireOp",EDGE,"E25.MirrorCS"),sQuery(id+"F15.wireOp",EDGE,"E26.MirrorCS")])]}),"instanceName":"1"}),"instanceName":"1"});
            var Q21;
            Q21=makeQuery(id+"F21.opPattern","COPY",BODY,{"derivedFrom":makeQuery(id+"F19.opPattern","COPY",BODY,{"derivedFrom":makeQuery(id+"F17.opPattern","COPY",BODY,{"derivedFrom":makeQuery(id+"F16.opExtrude","SWEPT_BODY",BODY,{"disambiguationData":[OSD([sQuery(id+"F15.wireOp",EDGE,"E13.bottom"),sQuery(id+"F15.wireOp",EDGE,"E13.top"),sQuery(id+"F15.wireOp",EDGE,"E13.left"),sQuery(id+"F15.wireOp",EDGE,"E13.right"),sQuery(id+"F15.wireOp",EDGE,"E14.bottom"),sQuery(id+"F15.wireOp",EDGE,"E14.top"),sQuery(id+"F15.wireOp",EDGE,"E14.left"),sQuery(id+"F15.wireOp",EDGE,"E14.right"),sQuery(id+"F15.wireOp",EDGE,"E15.MirrorCS"),sQuery(id+"F15.wireOp",EDGE,"E16.MirrorCS"),sQuery(id+"F15.wireOp",EDGE,"E17.MirrorCS"),sQuery(id+"F15.wireOp",EDGE,"E18.MirrorCS"),sQuery(id+"F15.wireOp",EDGE,"E19.MirrorCS"),sQuery(id+"F15.wireOp",EDGE,"E20.MirrorCS"),sQuery(id+"F15.wireOp",EDGE,"E21.MirrorCS"),sQuery(id+"F15.wireOp",EDGE,"E22.MirrorCS"),sQuery(id+"F15.wireOp",EDGE,"E23.MirrorCS"),sQuery(id+"F15.wireOp",EDGE,"E24.MirrorCS"),sQuery(id+"F15.wireOp",EDGE,"E25.MirrorCS"),sQuery(id+"F15.wireOp",EDGE,"E26.MirrorCS")])]}),"instanceName":"1"}),"instanceName":"1"}),"instanceName":"1"});
            var Q22;
            Q22=makeQuery(id+"F21.opPattern","COPY",BODY,{"derivedFrom":makeQuery(id+"F19.opPattern","COPY",BODY,{"derivedFrom":makeQuery(id+"F18.opPattern","COPY",BODY,{"derivedFrom":makeQuery(id+"F16.opExtrude","SWEPT_BODY",BODY,{"disambiguationData":[OSD([sQuery(id+"F15.wireOp",EDGE,"E13.bottom"),sQuery(id+"F15.wireOp",EDGE,"E13.top"),sQuery(id+"F15.wireOp",EDGE,"E13.left"),sQuery(id+"F15.wireOp",EDGE,"E13.right"),sQuery(id+"F15.wireOp",EDGE,"E14.bottom"),sQuery(id+"F15.wireOp",EDGE,"E14.top"),sQuery(id+"F15.wireOp",EDGE,"E14.left"),sQuery(id+"F15.wireOp",EDGE,"E14.right"),sQuery(id+"F15.wireOp",EDGE,"E15.MirrorCS"),sQuery(id+"F15.wireOp",EDGE,"E16.MirrorCS"),sQuery(id+"F15.wireOp",EDGE,"E17.MirrorCS"),sQuery(id+"F15.wireOp",EDGE,"E18.MirrorCS"),sQuery(id+"F15.wireOp",EDGE,"E19.MirrorCS"),sQuery(id+"F15.wireOp",EDGE,"E20.MirrorCS"),sQuery(id+"F15.wireOp",EDGE,"E21.MirrorCS"),sQuery(id+"F15.wireOp",EDGE,"E22.MirrorCS"),sQuery(id+"F15.wireOp",EDGE,"E23.MirrorCS"),sQuery(id+"F15.wireOp",EDGE,"E24.MirrorCS"),sQuery(id+"F15.wireOp",EDGE,"E25.MirrorCS"),sQuery(id+"F15.wireOp",EDGE,"E26.MirrorCS")])]}),"instanceName":"1"}),"instanceName":"1"}),"instanceName":"1"});
            var Q23;
            Q23=makeQuery(id+"F21.opPattern","COPY",BODY,{"derivedFrom":makeQuery(id+"F19.opPattern","COPY",BODY,{"derivedFrom":makeQuery(id+"F18.opPattern","COPY",BODY,{"derivedFrom":makeQuery(id+"F17.opPattern","COPY",BODY,{"derivedFrom":makeQuery(id+"F16.opExtrude","SWEPT_BODY",BODY,{"disambiguationData":[OSD([sQuery(id+"F15.wireOp",EDGE,"E13.bottom"),sQuery(id+"F15.wireOp",EDGE,"E13.top"),sQuery(id+"F15.wireOp",EDGE,"E13.left"),sQuery(id+"F15.wireOp",EDGE,"E13.right"),sQuery(id+"F15.wireOp",EDGE,"E14.bottom"),sQuery(id+"F15.wireOp",EDGE,"E14.top"),sQuery(id+"F15.wireOp",EDGE,"E14.left"),sQuery(id+"F15.wireOp",EDGE,"E14.right"),sQuery(id+"F15.wireOp",EDGE,"E15.MirrorCS"),sQuery(id+"F15.wireOp",EDGE,"E16.MirrorCS"),sQuery(id+"F15.wireOp",EDGE,"E17.MirrorCS"),sQuery(id+"F15.wireOp",EDGE,"E18.MirrorCS"),sQuery(id+"F15.wireOp",EDGE,"E19.MirrorCS"),sQuery(id+"F15.wireOp",EDGE,"E20.MirrorCS"),sQuery(id+"F15.wireOp",EDGE,"E21.MirrorCS"),sQuery(id+"F15.wireOp",EDGE,"E22.MirrorCS"),sQuery(id+"F15.wireOp",EDGE,"E23.MirrorCS"),sQuery(id+"F15.wireOp",EDGE,"E24.MirrorCS"),sQuery(id+"F15.wireOp",EDGE,"E25.MirrorCS"),sQuery(id+"F15.wireOp",EDGE,"E26.MirrorCS")])]}),"instanceName":"1"}),"instanceName":"1"}),"instanceName":"1"}),"instanceName":"1"});
            var Q24;
            Q24=makeQuery(id+"F21.opPattern","COPY",BODY,{"derivedFrom":makeQuery(id+"F20.opPattern","COPY",BODY,{"derivedFrom":makeQuery(id+"F16.opExtrude","SWEPT_BODY",BODY,{"disambiguationData":[OSD([sQuery(id+"F15.wireOp",EDGE,"E13.bottom"),sQuery(id+"F15.wireOp",EDGE,"E13.top"),sQuery(id+"F15.wireOp",EDGE,"E13.left"),sQuery(id+"F15.wireOp",EDGE,"E13.right"),sQuery(id+"F15.wireOp",EDGE,"E14.bottom"),sQuery(id+"F15.wireOp",EDGE,"E14.top"),sQuery(id+"F15.wireOp",EDGE,"E14.left"),sQuery(id+"F15.wireOp",EDGE,"E14.right"),sQuery(id+"F15.wireOp",EDGE,"E15.MirrorCS"),sQuery(id+"F15.wireOp",EDGE,"E16.MirrorCS"),sQuery(id+"F15.wireOp",EDGE,"E17.MirrorCS"),sQuery(id+"F15.wireOp",EDGE,"E18.MirrorCS"),sQuery(id+"F15.wireOp",EDGE,"E19.MirrorCS"),sQuery(id+"F15.wireOp",EDGE,"E20.MirrorCS"),sQuery(id+"F15.wireOp",EDGE,"E21.MirrorCS"),sQuery(id+"F15.wireOp",EDGE,"E22.MirrorCS"),sQuery(id+"F15.wireOp",EDGE,"E23.MirrorCS"),sQuery(id+"F15.wireOp",EDGE,"E24.MirrorCS"),sQuery(id+"F15.wireOp",EDGE,"E25.MirrorCS"),sQuery(id+"F15.wireOp",EDGE,"E26.MirrorCS")])]}),"instanceName":"1"}),"instanceName":"1"});
            var Q25;
            Q25=makeQuery(id+"F21.opPattern","COPY",BODY,{"derivedFrom":makeQuery(id+"F20.opPattern","COPY",BODY,{"derivedFrom":makeQuery(id+"F17.opPattern","COPY",BODY,{"derivedFrom":makeQuery(id+"F16.opExtrude","SWEPT_BODY",BODY,{"disambiguationData":[OSD([sQuery(id+"F15.wireOp",EDGE,"E13.bottom"),sQuery(id+"F15.wireOp",EDGE,"E13.top"),sQuery(id+"F15.wireOp",EDGE,"E13.left"),sQuery(id+"F15.wireOp",EDGE,"E13.right"),sQuery(id+"F15.wireOp",EDGE,"E14.bottom"),sQuery(id+"F15.wireOp",EDGE,"E14.top"),sQuery(id+"F15.wireOp",EDGE,"E14.left"),sQuery(id+"F15.wireOp",EDGE,"E14.right"),sQuery(id+"F15.wireOp",EDGE,"E15.MirrorCS"),sQuery(id+"F15.wireOp",EDGE,"E16.MirrorCS"),sQuery(id+"F15.wireOp",EDGE,"E17.MirrorCS"),sQuery(id+"F15.wireOp",EDGE,"E18.MirrorCS"),sQuery(id+"F15.wireOp",EDGE,"E19.MirrorCS"),sQuery(id+"F15.wireOp",EDGE,"E20.MirrorCS"),sQuery(id+"F15.wireOp",EDGE,"E21.MirrorCS"),sQuery(id+"F15.wireOp",EDGE,"E22.MirrorCS"),sQuery(id+"F15.wireOp",EDGE,"E23.MirrorCS"),sQuery(id+"F15.wireOp",EDGE,"E24.MirrorCS"),sQuery(id+"F15.wireOp",EDGE,"E25.MirrorCS"),sQuery(id+"F15.wireOp",EDGE,"E26.MirrorCS")])]}),"instanceName":"1"}),"instanceName":"1"}),"instanceName":"1"});
            var Q26;
            Q26=makeQuery(id+"F21.opPattern","COPY",BODY,{"derivedFrom":makeQuery(id+"F20.opPattern","COPY",BODY,{"derivedFrom":makeQuery(id+"F18.opPattern","COPY",BODY,{"derivedFrom":makeQuery(id+"F16.opExtrude","SWEPT_BODY",BODY,{"disambiguationData":[OSD([sQuery(id+"F15.wireOp",EDGE,"E13.bottom"),sQuery(id+"F15.wireOp",EDGE,"E13.top"),sQuery(id+"F15.wireOp",EDGE,"E13.left"),sQuery(id+"F15.wireOp",EDGE,"E13.right"),sQuery(id+"F15.wireOp",EDGE,"E14.bottom"),sQuery(id+"F15.wireOp",EDGE,"E14.top"),sQuery(id+"F15.wireOp",EDGE,"E14.left"),sQuery(id+"F15.wireOp",EDGE,"E14.right"),sQuery(id+"F15.wireOp",EDGE,"E15.MirrorCS"),sQuery(id+"F15.wireOp",EDGE,"E16.MirrorCS"),sQuery(id+"F15.wireOp",EDGE,"E17.MirrorCS"),sQuery(id+"F15.wireOp",EDGE,"E18.MirrorCS"),sQuery(id+"F15.wireOp",EDGE,"E19.MirrorCS"),sQuery(id+"F15.wireOp",EDGE,"E20.MirrorCS"),sQuery(id+"F15.wireOp",EDGE,"E21.MirrorCS"),sQuery(id+"F15.wireOp",EDGE,"E22.MirrorCS"),sQuery(id+"F15.wireOp",EDGE,"E23.MirrorCS"),sQuery(id+"F15.wireOp",EDGE,"E24.MirrorCS"),sQuery(id+"F15.wireOp",EDGE,"E25.MirrorCS"),sQuery(id+"F15.wireOp",EDGE,"E26.MirrorCS")])]}),"instanceName":"1"}),"instanceName":"1"}),"instanceName":"1"});
            var Q27;
            Q27=makeQuery(id+"F21.opPattern","COPY",BODY,{"derivedFrom":makeQuery(id+"F20.opPattern","COPY",BODY,{"derivedFrom":makeQuery(id+"F18.opPattern","COPY",BODY,{"derivedFrom":makeQuery(id+"F17.opPattern","COPY",BODY,{"derivedFrom":makeQuery(id+"F16.opExtrude","SWEPT_BODY",BODY,{"disambiguationData":[OSD([sQuery(id+"F15.wireOp",EDGE,"E13.bottom"),sQuery(id+"F15.wireOp",EDGE,"E13.top"),sQuery(id+"F15.wireOp",EDGE,"E13.left"),sQuery(id+"F15.wireOp",EDGE,"E13.right"),sQuery(id+"F15.wireOp",EDGE,"E14.bottom"),sQuery(id+"F15.wireOp",EDGE,"E14.top"),sQuery(id+"F15.wireOp",EDGE,"E14.left"),sQuery(id+"F15.wireOp",EDGE,"E14.right"),sQuery(id+"F15.wireOp",EDGE,"E15.MirrorCS"),sQuery(id+"F15.wireOp",EDGE,"E16.MirrorCS"),sQuery(id+"F15.wireOp",EDGE,"E17.MirrorCS"),sQuery(id+"F15.wireOp",EDGE,"E18.MirrorCS"),sQuery(id+"F15.wireOp",EDGE,"E19.MirrorCS"),sQuery(id+"F15.wireOp",EDGE,"E20.MirrorCS"),sQuery(id+"F15.wireOp",EDGE,"E21.MirrorCS"),sQuery(id+"F15.wireOp",EDGE,"E22.MirrorCS"),sQuery(id+"F15.wireOp",EDGE,"E23.MirrorCS"),sQuery(id+"F15.wireOp",EDGE,"E24.MirrorCS"),sQuery(id+"F15.wireOp",EDGE,"E25.MirrorCS"),sQuery(id+"F15.wireOp",EDGE,"E26.MirrorCS")])]}),"instanceName":"1"}),"instanceName":"1"}),"instanceName":"1"}),"instanceName":"1"});
            var Q28;
            Q28=makeQuery(id+"F21.opPattern","COPY",BODY,{"derivedFrom":makeQuery(id+"F20.opPattern","COPY",BODY,{"derivedFrom":makeQuery(id+"F19.opPattern","COPY",BODY,{"derivedFrom":makeQuery(id+"F16.opExtrude","SWEPT_BODY",BODY,{"disambiguationData":[OSD([sQuery(id+"F15.wireOp",EDGE,"E13.bottom"),sQuery(id+"F15.wireOp",EDGE,"E13.top"),sQuery(id+"F15.wireOp",EDGE,"E13.left"),sQuery(id+"F15.wireOp",EDGE,"E13.right"),sQuery(id+"F15.wireOp",EDGE,"E14.bottom"),sQuery(id+"F15.wireOp",EDGE,"E14.top"),sQuery(id+"F15.wireOp",EDGE,"E14.left"),sQuery(id+"F15.wireOp",EDGE,"E14.right"),sQuery(id+"F15.wireOp",EDGE,"E15.MirrorCS"),sQuery(id+"F15.wireOp",EDGE,"E16.MirrorCS"),sQuery(id+"F15.wireOp",EDGE,"E17.MirrorCS"),sQuery(id+"F15.wireOp",EDGE,"E18.MirrorCS"),sQuery(id+"F15.wireOp",EDGE,"E19.MirrorCS"),sQuery(id+"F15.wireOp",EDGE,"E20.MirrorCS"),sQuery(id+"F15.wireOp",EDGE,"E21.MirrorCS"),sQuery(id+"F15.wireOp",EDGE,"E22.MirrorCS"),sQuery(id+"F15.wireOp",EDGE,"E23.MirrorCS"),sQuery(id+"F15.wireOp",EDGE,"E24.MirrorCS"),sQuery(id+"F15.wireOp",EDGE,"E25.MirrorCS"),sQuery(id+"F15.wireOp",EDGE,"E26.MirrorCS")])]}),"instanceName":"1"}),"instanceName":"1"}),"instanceName":"1"});
            var Q29;
            Q29=makeQuery(id+"F21.opPattern","COPY",BODY,{"derivedFrom":makeQuery(id+"F20.opPattern","COPY",BODY,{"derivedFrom":makeQuery(id+"F19.opPattern","COPY",BODY,{"derivedFrom":makeQuery(id+"F17.opPattern","COPY",BODY,{"derivedFrom":makeQuery(id+"F16.opExtrude","SWEPT_BODY",BODY,{"disambiguationData":[OSD([sQuery(id+"F15.wireOp",EDGE,"E13.bottom"),sQuery(id+"F15.wireOp",EDGE,"E13.top"),sQuery(id+"F15.wireOp",EDGE,"E13.left"),sQuery(id+"F15.wireOp",EDGE,"E13.right"),sQuery(id+"F15.wireOp",EDGE,"E14.bottom"),sQuery(id+"F15.wireOp",EDGE,"E14.top"),sQuery(id+"F15.wireOp",EDGE,"E14.left"),sQuery(id+"F15.wireOp",EDGE,"E14.right"),sQuery(id+"F15.wireOp",EDGE,"E15.MirrorCS"),sQuery(id+"F15.wireOp",EDGE,"E16.MirrorCS"),sQuery(id+"F15.wireOp",EDGE,"E17.MirrorCS"),sQuery(id+"F15.wireOp",EDGE,"E18.MirrorCS"),sQuery(id+"F15.wireOp",EDGE,"E19.MirrorCS"),sQuery(id+"F15.wireOp",EDGE,"E20.MirrorCS"),sQuery(id+"F15.wireOp",EDGE,"E21.MirrorCS"),sQuery(id+"F15.wireOp",EDGE,"E22.MirrorCS"),sQuery(id+"F15.wireOp",EDGE,"E23.MirrorCS"),sQuery(id+"F15.wireOp",EDGE,"E24.MirrorCS"),sQuery(id+"F15.wireOp",EDGE,"E25.MirrorCS"),sQuery(id+"F15.wireOp",EDGE,"E26.MirrorCS")])]}),"instanceName":"1"}),"instanceName":"1"}),"instanceName":"1"}),"instanceName":"1"});
            var Q30;
            Q30=makeQuery(id+"F21.opPattern","COPY",BODY,{"derivedFrom":makeQuery(id+"F20.opPattern","COPY",BODY,{"derivedFrom":makeQuery(id+"F19.opPattern","COPY",BODY,{"derivedFrom":makeQuery(id+"F18.opPattern","COPY",BODY,{"derivedFrom":makeQuery(id+"F16.opExtrude","SWEPT_BODY",BODY,{"disambiguationData":[OSD([sQuery(id+"F15.wireOp",EDGE,"E13.bottom"),sQuery(id+"F15.wireOp",EDGE,"E13.top"),sQuery(id+"F15.wireOp",EDGE,"E13.left"),sQuery(id+"F15.wireOp",EDGE,"E13.right"),sQuery(id+"F15.wireOp",EDGE,"E14.bottom"),sQuery(id+"F15.wireOp",EDGE,"E14.top"),sQuery(id+"F15.wireOp",EDGE,"E14.left"),sQuery(id+"F15.wireOp",EDGE,"E14.right"),sQuery(id+"F15.wireOp",EDGE,"E15.MirrorCS"),sQuery(id+"F15.wireOp",EDGE,"E16.MirrorCS"),sQuery(id+"F15.wireOp",EDGE,"E17.MirrorCS"),sQuery(id+"F15.wireOp",EDGE,"E18.MirrorCS"),sQuery(id+"F15.wireOp",EDGE,"E19.MirrorCS"),sQuery(id+"F15.wireOp",EDGE,"E20.MirrorCS"),sQuery(id+"F15.wireOp",EDGE,"E21.MirrorCS"),sQuery(id+"F15.wireOp",EDGE,"E22.MirrorCS"),sQuery(id+"F15.wireOp",EDGE,"E23.MirrorCS"),sQuery(id+"F15.wireOp",EDGE,"E24.MirrorCS"),sQuery(id+"F15.wireOp",EDGE,"E25.MirrorCS"),sQuery(id+"F15.wireOp",EDGE,"E26.MirrorCS")])]}),"instanceName":"1"}),"instanceName":"1"}),"instanceName":"1"}),"instanceName":"1"});
            var Q31;
            Q31=makeQuery(id+"F22.opPattern","COPY",BODY,{"derivedFrom":makeQuery(id+"F16.opExtrude","SWEPT_BODY",BODY,{"disambiguationData":[OSD([sQuery(id+"F15.wireOp",EDGE,"E13.bottom"),sQuery(id+"F15.wireOp",EDGE,"E13.top"),sQuery(id+"F15.wireOp",EDGE,"E13.left"),sQuery(id+"F15.wireOp",EDGE,"E13.right"),sQuery(id+"F15.wireOp",EDGE,"E14.bottom"),sQuery(id+"F15.wireOp",EDGE,"E14.top"),sQuery(id+"F15.wireOp",EDGE,"E14.left"),sQuery(id+"F15.wireOp",EDGE,"E14.right"),sQuery(id+"F15.wireOp",EDGE,"E15.MirrorCS"),sQuery(id+"F15.wireOp",EDGE,"E16.MirrorCS"),sQuery(id+"F15.wireOp",EDGE,"E17.MirrorCS"),sQuery(id+"F15.wireOp",EDGE,"E18.MirrorCS"),sQuery(id+"F15.wireOp",EDGE,"E19.MirrorCS"),sQuery(id+"F15.wireOp",EDGE,"E20.MirrorCS"),sQuery(id+"F15.wireOp",EDGE,"E21.MirrorCS"),sQuery(id+"F15.wireOp",EDGE,"E22.MirrorCS"),sQuery(id+"F15.wireOp",EDGE,"E23.MirrorCS"),sQuery(id+"F15.wireOp",EDGE,"E24.MirrorCS"),sQuery(id+"F15.wireOp",EDGE,"E25.MirrorCS"),sQuery(id+"F15.wireOp",EDGE,"E26.MirrorCS")])]}),"instanceName":"1"});
            var Q32;
            Q32=makeQuery(id+"F22.opPattern","COPY",BODY,{"derivedFrom":makeQuery(id+"F17.opPattern","COPY",BODY,{"derivedFrom":makeQuery(id+"F16.opExtrude","SWEPT_BODY",BODY,{"disambiguationData":[OSD([sQuery(id+"F15.wireOp",EDGE,"E13.bottom"),sQuery(id+"F15.wireOp",EDGE,"E13.top"),sQuery(id+"F15.wireOp",EDGE,"E13.left"),sQuery(id+"F15.wireOp",EDGE,"E13.right"),sQuery(id+"F15.wireOp",EDGE,"E14.bottom"),sQuery(id+"F15.wireOp",EDGE,"E14.top"),sQuery(id+"F15.wireOp",EDGE,"E14.left"),sQuery(id+"F15.wireOp",EDGE,"E14.right"),sQuery(id+"F15.wireOp",EDGE,"E15.MirrorCS"),sQuery(id+"F15.wireOp",EDGE,"E16.MirrorCS"),sQuery(id+"F15.wireOp",EDGE,"E17.MirrorCS"),sQuery(id+"F15.wireOp",EDGE,"E18.MirrorCS"),sQuery(id+"F15.wireOp",EDGE,"E19.MirrorCS"),sQuery(id+"F15.wireOp",EDGE,"E20.MirrorCS"),sQuery(id+"F15.wireOp",EDGE,"E21.MirrorCS"),sQuery(id+"F15.wireOp",EDGE,"E22.MirrorCS"),sQuery(id+"F15.wireOp",EDGE,"E23.MirrorCS"),sQuery(id+"F15.wireOp",EDGE,"E24.MirrorCS"),sQuery(id+"F15.wireOp",EDGE,"E25.MirrorCS"),sQuery(id+"F15.wireOp",EDGE,"E26.MirrorCS")])]}),"instanceName":"1"}),"instanceName":"1"});
            var Q33;
            Q33=makeQuery(id+"F22.opPattern","COPY",BODY,{"derivedFrom":makeQuery(id+"F18.opPattern","COPY",BODY,{"derivedFrom":makeQuery(id+"F16.opExtrude","SWEPT_BODY",BODY,{"disambiguationData":[OSD([sQuery(id+"F15.wireOp",EDGE,"E13.bottom"),sQuery(id+"F15.wireOp",EDGE,"E13.top"),sQuery(id+"F15.wireOp",EDGE,"E13.left"),sQuery(id+"F15.wireOp",EDGE,"E13.right"),sQuery(id+"F15.wireOp",EDGE,"E14.bottom"),sQuery(id+"F15.wireOp",EDGE,"E14.top"),sQuery(id+"F15.wireOp",EDGE,"E14.left"),sQuery(id+"F15.wireOp",EDGE,"E14.right"),sQuery(id+"F15.wireOp",EDGE,"E15.MirrorCS"),sQuery(id+"F15.wireOp",EDGE,"E16.MirrorCS"),sQuery(id+"F15.wireOp",EDGE,"E17.MirrorCS"),sQuery(id+"F15.wireOp",EDGE,"E18.MirrorCS"),sQuery(id+"F15.wireOp",EDGE,"E19.MirrorCS"),sQuery(id+"F15.wireOp",EDGE,"E20.MirrorCS"),sQuery(id+"F15.wireOp",EDGE,"E21.MirrorCS"),sQuery(id+"F15.wireOp",EDGE,"E22.MirrorCS"),sQuery(id+"F15.wireOp",EDGE,"E23.MirrorCS"),sQuery(id+"F15.wireOp",EDGE,"E24.MirrorCS"),sQuery(id+"F15.wireOp",EDGE,"E25.MirrorCS"),sQuery(id+"F15.wireOp",EDGE,"E26.MirrorCS")])]}),"instanceName":"1"}),"instanceName":"1"});
            var Q34;
            Q34=makeQuery(id+"F22.opPattern","COPY",BODY,{"derivedFrom":makeQuery(id+"F18.opPattern","COPY",BODY,{"derivedFrom":makeQuery(id+"F17.opPattern","COPY",BODY,{"derivedFrom":makeQuery(id+"F16.opExtrude","SWEPT_BODY",BODY,{"disambiguationData":[OSD([sQuery(id+"F15.wireOp",EDGE,"E13.bottom"),sQuery(id+"F15.wireOp",EDGE,"E13.top"),sQuery(id+"F15.wireOp",EDGE,"E13.left"),sQuery(id+"F15.wireOp",EDGE,"E13.right"),sQuery(id+"F15.wireOp",EDGE,"E14.bottom"),sQuery(id+"F15.wireOp",EDGE,"E14.top"),sQuery(id+"F15.wireOp",EDGE,"E14.left"),sQuery(id+"F15.wireOp",EDGE,"E14.right"),sQuery(id+"F15.wireOp",EDGE,"E15.MirrorCS"),sQuery(id+"F15.wireOp",EDGE,"E16.MirrorCS"),sQuery(id+"F15.wireOp",EDGE,"E17.MirrorCS"),sQuery(id+"F15.wireOp",EDGE,"E18.MirrorCS"),sQuery(id+"F15.wireOp",EDGE,"E19.MirrorCS"),sQuery(id+"F15.wireOp",EDGE,"E20.MirrorCS"),sQuery(id+"F15.wireOp",EDGE,"E21.MirrorCS"),sQuery(id+"F15.wireOp",EDGE,"E22.MirrorCS"),sQuery(id+"F15.wireOp",EDGE,"E23.MirrorCS"),sQuery(id+"F15.wireOp",EDGE,"E24.MirrorCS"),sQuery(id+"F15.wireOp",EDGE,"E25.MirrorCS"),sQuery(id+"F15.wireOp",EDGE,"E26.MirrorCS")])]}),"instanceName":"1"}),"instanceName":"1"}),"instanceName":"1"});
            var Q35;
            Q35=makeQuery(id+"F22.opPattern","COPY",BODY,{"derivedFrom":makeQuery(id+"F19.opPattern","COPY",BODY,{"derivedFrom":makeQuery(id+"F16.opExtrude","SWEPT_BODY",BODY,{"disambiguationData":[OSD([sQuery(id+"F15.wireOp",EDGE,"E13.bottom"),sQuery(id+"F15.wireOp",EDGE,"E13.top"),sQuery(id+"F15.wireOp",EDGE,"E13.left"),sQuery(id+"F15.wireOp",EDGE,"E13.right"),sQuery(id+"F15.wireOp",EDGE,"E14.bottom"),sQuery(id+"F15.wireOp",EDGE,"E14.top"),sQuery(id+"F15.wireOp",EDGE,"E14.left"),sQuery(id+"F15.wireOp",EDGE,"E14.right"),sQuery(id+"F15.wireOp",EDGE,"E15.MirrorCS"),sQuery(id+"F15.wireOp",EDGE,"E16.MirrorCS"),sQuery(id+"F15.wireOp",EDGE,"E17.MirrorCS"),sQuery(id+"F15.wireOp",EDGE,"E18.MirrorCS"),sQuery(id+"F15.wireOp",EDGE,"E19.MirrorCS"),sQuery(id+"F15.wireOp",EDGE,"E20.MirrorCS"),sQuery(id+"F15.wireOp",EDGE,"E21.MirrorCS"),sQuery(id+"F15.wireOp",EDGE,"E22.MirrorCS"),sQuery(id+"F15.wireOp",EDGE,"E23.MirrorCS"),sQuery(id+"F15.wireOp",EDGE,"E24.MirrorCS"),sQuery(id+"F15.wireOp",EDGE,"E25.MirrorCS"),sQuery(id+"F15.wireOp",EDGE,"E26.MirrorCS")])]}),"instanceName":"1"}),"instanceName":"1"});
            var Q36;
            Q36=makeQuery(id+"F22.opPattern","COPY",BODY,{"derivedFrom":makeQuery(id+"F19.opPattern","COPY",BODY,{"derivedFrom":makeQuery(id+"F17.opPattern","COPY",BODY,{"derivedFrom":makeQuery(id+"F16.opExtrude","SWEPT_BODY",BODY,{"disambiguationData":[OSD([sQuery(id+"F15.wireOp",EDGE,"E13.bottom"),sQuery(id+"F15.wireOp",EDGE,"E13.top"),sQuery(id+"F15.wireOp",EDGE,"E13.left"),sQuery(id+"F15.wireOp",EDGE,"E13.right"),sQuery(id+"F15.wireOp",EDGE,"E14.bottom"),sQuery(id+"F15.wireOp",EDGE,"E14.top"),sQuery(id+"F15.wireOp",EDGE,"E14.left"),sQuery(id+"F15.wireOp",EDGE,"E14.right"),sQuery(id+"F15.wireOp",EDGE,"E15.MirrorCS"),sQuery(id+"F15.wireOp",EDGE,"E16.MirrorCS"),sQuery(id+"F15.wireOp",EDGE,"E17.MirrorCS"),sQuery(id+"F15.wireOp",EDGE,"E18.MirrorCS"),sQuery(id+"F15.wireOp",EDGE,"E19.MirrorCS"),sQuery(id+"F15.wireOp",EDGE,"E20.MirrorCS"),sQuery(id+"F15.wireOp",EDGE,"E21.MirrorCS"),sQuery(id+"F15.wireOp",EDGE,"E22.MirrorCS"),sQuery(id+"F15.wireOp",EDGE,"E23.MirrorCS"),sQuery(id+"F15.wireOp",EDGE,"E24.MirrorCS"),sQuery(id+"F15.wireOp",EDGE,"E25.MirrorCS"),sQuery(id+"F15.wireOp",EDGE,"E26.MirrorCS")])]}),"instanceName":"1"}),"instanceName":"1"}),"instanceName":"1"});
            var Q37;
            Q37=makeQuery(id+"F22.opPattern","COPY",BODY,{"derivedFrom":makeQuery(id+"F19.opPattern","COPY",BODY,{"derivedFrom":makeQuery(id+"F18.opPattern","COPY",BODY,{"derivedFrom":makeQuery(id+"F16.opExtrude","SWEPT_BODY",BODY,{"disambiguationData":[OSD([sQuery(id+"F15.wireOp",EDGE,"E13.bottom"),sQuery(id+"F15.wireOp",EDGE,"E13.top"),sQuery(id+"F15.wireOp",EDGE,"E13.left"),sQuery(id+"F15.wireOp",EDGE,"E13.right"),sQuery(id+"F15.wireOp",EDGE,"E14.bottom"),sQuery(id+"F15.wireOp",EDGE,"E14.top"),sQuery(id+"F15.wireOp",EDGE,"E14.left"),sQuery(id+"F15.wireOp",EDGE,"E14.right"),sQuery(id+"F15.wireOp",EDGE,"E15.MirrorCS"),sQuery(id+"F15.wireOp",EDGE,"E16.MirrorCS"),sQuery(id+"F15.wireOp",EDGE,"E17.MirrorCS"),sQuery(id+"F15.wireOp",EDGE,"E18.MirrorCS"),sQuery(id+"F15.wireOp",EDGE,"E19.MirrorCS"),sQuery(id+"F15.wireOp",EDGE,"E20.MirrorCS"),sQuery(id+"F15.wireOp",EDGE,"E21.MirrorCS"),sQuery(id+"F15.wireOp",EDGE,"E22.MirrorCS"),sQuery(id+"F15.wireOp",EDGE,"E23.MirrorCS"),sQuery(id+"F15.wireOp",EDGE,"E24.MirrorCS"),sQuery(id+"F15.wireOp",EDGE,"E25.MirrorCS"),sQuery(id+"F15.wireOp",EDGE,"E26.MirrorCS")])]}),"instanceName":"1"}),"instanceName":"1"}),"instanceName":"1"});
            var Q38;
            Q38=makeQuery(id+"F22.opPattern","COPY",BODY,{"derivedFrom":makeQuery(id+"F19.opPattern","COPY",BODY,{"derivedFrom":makeQuery(id+"F18.opPattern","COPY",BODY,{"derivedFrom":makeQuery(id+"F17.opPattern","COPY",BODY,{"derivedFrom":makeQuery(id+"F16.opExtrude","SWEPT_BODY",BODY,{"disambiguationData":[OSD([sQuery(id+"F15.wireOp",EDGE,"E13.bottom"),sQuery(id+"F15.wireOp",EDGE,"E13.top"),sQuery(id+"F15.wireOp",EDGE,"E13.left"),sQuery(id+"F15.wireOp",EDGE,"E13.right"),sQuery(id+"F15.wireOp",EDGE,"E14.bottom"),sQuery(id+"F15.wireOp",EDGE,"E14.top"),sQuery(id+"F15.wireOp",EDGE,"E14.left"),sQuery(id+"F15.wireOp",EDGE,"E14.right"),sQuery(id+"F15.wireOp",EDGE,"E15.MirrorCS"),sQuery(id+"F15.wireOp",EDGE,"E16.MirrorCS"),sQuery(id+"F15.wireOp",EDGE,"E17.MirrorCS"),sQuery(id+"F15.wireOp",EDGE,"E18.MirrorCS"),sQuery(id+"F15.wireOp",EDGE,"E19.MirrorCS"),sQuery(id+"F15.wireOp",EDGE,"E20.MirrorCS"),sQuery(id+"F15.wireOp",EDGE,"E21.MirrorCS"),sQuery(id+"F15.wireOp",EDGE,"E22.MirrorCS"),sQuery(id+"F15.wireOp",EDGE,"E23.MirrorCS"),sQuery(id+"F15.wireOp",EDGE,"E24.MirrorCS"),sQuery(id+"F15.wireOp",EDGE,"E25.MirrorCS"),sQuery(id+"F15.wireOp",EDGE,"E26.MirrorCS")])]}),"instanceName":"1"}),"instanceName":"1"}),"instanceName":"1"}),"instanceName":"1"});
            var Q39;
            Q39=makeQuery(id+"F22.opPattern","COPY",BODY,{"derivedFrom":makeQuery(id+"F20.opPattern","COPY",BODY,{"derivedFrom":makeQuery(id+"F16.opExtrude","SWEPT_BODY",BODY,{"disambiguationData":[OSD([sQuery(id+"F15.wireOp",EDGE,"E13.bottom"),sQuery(id+"F15.wireOp",EDGE,"E13.top"),sQuery(id+"F15.wireOp",EDGE,"E13.left"),sQuery(id+"F15.wireOp",EDGE,"E13.right"),sQuery(id+"F15.wireOp",EDGE,"E14.bottom"),sQuery(id+"F15.wireOp",EDGE,"E14.top"),sQuery(id+"F15.wireOp",EDGE,"E14.left"),sQuery(id+"F15.wireOp",EDGE,"E14.right"),sQuery(id+"F15.wireOp",EDGE,"E15.MirrorCS"),sQuery(id+"F15.wireOp",EDGE,"E16.MirrorCS"),sQuery(id+"F15.wireOp",EDGE,"E17.MirrorCS"),sQuery(id+"F15.wireOp",EDGE,"E18.MirrorCS"),sQuery(id+"F15.wireOp",EDGE,"E19.MirrorCS"),sQuery(id+"F15.wireOp",EDGE,"E20.MirrorCS"),sQuery(id+"F15.wireOp",EDGE,"E21.MirrorCS"),sQuery(id+"F15.wireOp",EDGE,"E22.MirrorCS"),sQuery(id+"F15.wireOp",EDGE,"E23.MirrorCS"),sQuery(id+"F15.wireOp",EDGE,"E24.MirrorCS"),sQuery(id+"F15.wireOp",EDGE,"E25.MirrorCS"),sQuery(id+"F15.wireOp",EDGE,"E26.MirrorCS")])]}),"instanceName":"1"}),"instanceName":"1"});
            var Q40;
            Q40=makeQuery(id+"F22.opPattern","COPY",BODY,{"derivedFrom":makeQuery(id+"F20.opPattern","COPY",BODY,{"derivedFrom":makeQuery(id+"F17.opPattern","COPY",BODY,{"derivedFrom":makeQuery(id+"F16.opExtrude","SWEPT_BODY",BODY,{"disambiguationData":[OSD([sQuery(id+"F15.wireOp",EDGE,"E13.bottom"),sQuery(id+"F15.wireOp",EDGE,"E13.top"),sQuery(id+"F15.wireOp",EDGE,"E13.left"),sQuery(id+"F15.wireOp",EDGE,"E13.right"),sQuery(id+"F15.wireOp",EDGE,"E14.bottom"),sQuery(id+"F15.wireOp",EDGE,"E14.top"),sQuery(id+"F15.wireOp",EDGE,"E14.left"),sQuery(id+"F15.wireOp",EDGE,"E14.right"),sQuery(id+"F15.wireOp",EDGE,"E15.MirrorCS"),sQuery(id+"F15.wireOp",EDGE,"E16.MirrorCS"),sQuery(id+"F15.wireOp",EDGE,"E17.MirrorCS"),sQuery(id+"F15.wireOp",EDGE,"E18.MirrorCS"),sQuery(id+"F15.wireOp",EDGE,"E19.MirrorCS"),sQuery(id+"F15.wireOp",EDGE,"E20.MirrorCS"),sQuery(id+"F15.wireOp",EDGE,"E21.MirrorCS"),sQuery(id+"F15.wireOp",EDGE,"E22.MirrorCS"),sQuery(id+"F15.wireOp",EDGE,"E23.MirrorCS"),sQuery(id+"F15.wireOp",EDGE,"E24.MirrorCS"),sQuery(id+"F15.wireOp",EDGE,"E25.MirrorCS"),sQuery(id+"F15.wireOp",EDGE,"E26.MirrorCS")])]}),"instanceName":"1"}),"instanceName":"1"}),"instanceName":"1"});
            var Q41;
            Q41=makeQuery(id+"F22.opPattern","COPY",BODY,{"derivedFrom":makeQuery(id+"F20.opPattern","COPY",BODY,{"derivedFrom":makeQuery(id+"F18.opPattern","COPY",BODY,{"derivedFrom":makeQuery(id+"F16.opExtrude","SWEPT_BODY",BODY,{"disambiguationData":[OSD([sQuery(id+"F15.wireOp",EDGE,"E13.bottom"),sQuery(id+"F15.wireOp",EDGE,"E13.top"),sQuery(id+"F15.wireOp",EDGE,"E13.left"),sQuery(id+"F15.wireOp",EDGE,"E13.right"),sQuery(id+"F15.wireOp",EDGE,"E14.bottom"),sQuery(id+"F15.wireOp",EDGE,"E14.top"),sQuery(id+"F15.wireOp",EDGE,"E14.left"),sQuery(id+"F15.wireOp",EDGE,"E14.right"),sQuery(id+"F15.wireOp",EDGE,"E15.MirrorCS"),sQuery(id+"F15.wireOp",EDGE,"E16.MirrorCS"),sQuery(id+"F15.wireOp",EDGE,"E17.MirrorCS"),sQuery(id+"F15.wireOp",EDGE,"E18.MirrorCS"),sQuery(id+"F15.wireOp",EDGE,"E19.MirrorCS"),sQuery(id+"F15.wireOp",EDGE,"E20.MirrorCS"),sQuery(id+"F15.wireOp",EDGE,"E21.MirrorCS"),sQuery(id+"F15.wireOp",EDGE,"E22.MirrorCS"),sQuery(id+"F15.wireOp",EDGE,"E23.MirrorCS"),sQuery(id+"F15.wireOp",EDGE,"E24.MirrorCS"),sQuery(id+"F15.wireOp",EDGE,"E25.MirrorCS"),sQuery(id+"F15.wireOp",EDGE,"E26.MirrorCS")])]}),"instanceName":"1"}),"instanceName":"1"}),"instanceName":"1"});
            var Q42;
            Q42=makeQuery(id+"F22.opPattern","COPY",BODY,{"derivedFrom":makeQuery(id+"F20.opPattern","COPY",BODY,{"derivedFrom":makeQuery(id+"F18.opPattern","COPY",BODY,{"derivedFrom":makeQuery(id+"F17.opPattern","COPY",BODY,{"derivedFrom":makeQuery(id+"F16.opExtrude","SWEPT_BODY",BODY,{"disambiguationData":[OSD([sQuery(id+"F15.wireOp",EDGE,"E13.bottom"),sQuery(id+"F15.wireOp",EDGE,"E13.top"),sQuery(id+"F15.wireOp",EDGE,"E13.left"),sQuery(id+"F15.wireOp",EDGE,"E13.right"),sQuery(id+"F15.wireOp",EDGE,"E14.bottom"),sQuery(id+"F15.wireOp",EDGE,"E14.top"),sQuery(id+"F15.wireOp",EDGE,"E14.left"),sQuery(id+"F15.wireOp",EDGE,"E14.right"),sQuery(id+"F15.wireOp",EDGE,"E15.MirrorCS"),sQuery(id+"F15.wireOp",EDGE,"E16.MirrorCS"),sQuery(id+"F15.wireOp",EDGE,"E17.MirrorCS"),sQuery(id+"F15.wireOp",EDGE,"E18.MirrorCS"),sQuery(id+"F15.wireOp",EDGE,"E19.MirrorCS"),sQuery(id+"F15.wireOp",EDGE,"E20.MirrorCS"),sQuery(id+"F15.wireOp",EDGE,"E21.MirrorCS"),sQuery(id+"F15.wireOp",EDGE,"E22.MirrorCS"),sQuery(id+"F15.wireOp",EDGE,"E23.MirrorCS"),sQuery(id+"F15.wireOp",EDGE,"E24.MirrorCS"),sQuery(id+"F15.wireOp",EDGE,"E25.MirrorCS"),sQuery(id+"F15.wireOp",EDGE,"E26.MirrorCS")])]}),"instanceName":"1"}),"instanceName":"1"}),"instanceName":"1"}),"instanceName":"1"});
            var Q43;
            Q43=makeQuery(id+"F22.opPattern","COPY",BODY,{"derivedFrom":makeQuery(id+"F20.opPattern","COPY",BODY,{"derivedFrom":makeQuery(id+"F19.opPattern","COPY",BODY,{"derivedFrom":makeQuery(id+"F16.opExtrude","SWEPT_BODY",BODY,{"disambiguationData":[OSD([sQuery(id+"F15.wireOp",EDGE,"E13.bottom"),sQuery(id+"F15.wireOp",EDGE,"E13.top"),sQuery(id+"F15.wireOp",EDGE,"E13.left"),sQuery(id+"F15.wireOp",EDGE,"E13.right"),sQuery(id+"F15.wireOp",EDGE,"E14.bottom"),sQuery(id+"F15.wireOp",EDGE,"E14.top"),sQuery(id+"F15.wireOp",EDGE,"E14.left"),sQuery(id+"F15.wireOp",EDGE,"E14.right"),sQuery(id+"F15.wireOp",EDGE,"E15.MirrorCS"),sQuery(id+"F15.wireOp",EDGE,"E16.MirrorCS"),sQuery(id+"F15.wireOp",EDGE,"E17.MirrorCS"),sQuery(id+"F15.wireOp",EDGE,"E18.MirrorCS"),sQuery(id+"F15.wireOp",EDGE,"E19.MirrorCS"),sQuery(id+"F15.wireOp",EDGE,"E20.MirrorCS"),sQuery(id+"F15.wireOp",EDGE,"E21.MirrorCS"),sQuery(id+"F15.wireOp",EDGE,"E22.MirrorCS"),sQuery(id+"F15.wireOp",EDGE,"E23.MirrorCS"),sQuery(id+"F15.wireOp",EDGE,"E24.MirrorCS"),sQuery(id+"F15.wireOp",EDGE,"E25.MirrorCS"),sQuery(id+"F15.wireOp",EDGE,"E26.MirrorCS")])]}),"instanceName":"1"}),"instanceName":"1"}),"instanceName":"1"});
            var Q44;
            Q44=makeQuery(id+"F22.opPattern","COPY",BODY,{"derivedFrom":makeQuery(id+"F20.opPattern","COPY",BODY,{"derivedFrom":makeQuery(id+"F19.opPattern","COPY",BODY,{"derivedFrom":makeQuery(id+"F17.opPattern","COPY",BODY,{"derivedFrom":makeQuery(id+"F16.opExtrude","SWEPT_BODY",BODY,{"disambiguationData":[OSD([sQuery(id+"F15.wireOp",EDGE,"E13.bottom"),sQuery(id+"F15.wireOp",EDGE,"E13.top"),sQuery(id+"F15.wireOp",EDGE,"E13.left"),sQuery(id+"F15.wireOp",EDGE,"E13.right"),sQuery(id+"F15.wireOp",EDGE,"E14.bottom"),sQuery(id+"F15.wireOp",EDGE,"E14.top"),sQuery(id+"F15.wireOp",EDGE,"E14.left"),sQuery(id+"F15.wireOp",EDGE,"E14.right"),sQuery(id+"F15.wireOp",EDGE,"E15.MirrorCS"),sQuery(id+"F15.wireOp",EDGE,"E16.MirrorCS"),sQuery(id+"F15.wireOp",EDGE,"E17.MirrorCS"),sQuery(id+"F15.wireOp",EDGE,"E18.MirrorCS"),sQuery(id+"F15.wireOp",EDGE,"E19.MirrorCS"),sQuery(id+"F15.wireOp",EDGE,"E20.MirrorCS"),sQuery(id+"F15.wireOp",EDGE,"E21.MirrorCS"),sQuery(id+"F15.wireOp",EDGE,"E22.MirrorCS"),sQuery(id+"F15.wireOp",EDGE,"E23.MirrorCS"),sQuery(id+"F15.wireOp",EDGE,"E24.MirrorCS"),sQuery(id+"F15.wireOp",EDGE,"E25.MirrorCS"),sQuery(id+"F15.wireOp",EDGE,"E26.MirrorCS")])]}),"instanceName":"1"}),"instanceName":"1"}),"instanceName":"1"}),"instanceName":"1"});
            var Q45;
            Q45=makeQuery(id+"F22.opPattern","COPY",BODY,{"derivedFrom":makeQuery(id+"F20.opPattern","COPY",BODY,{"derivedFrom":makeQuery(id+"F19.opPattern","COPY",BODY,{"derivedFrom":makeQuery(id+"F18.opPattern","COPY",BODY,{"derivedFrom":makeQuery(id+"F16.opExtrude","SWEPT_BODY",BODY,{"disambiguationData":[OSD([sQuery(id+"F15.wireOp",EDGE,"E13.bottom"),sQuery(id+"F15.wireOp",EDGE,"E13.top"),sQuery(id+"F15.wireOp",EDGE,"E13.left"),sQuery(id+"F15.wireOp",EDGE,"E13.right"),sQuery(id+"F15.wireOp",EDGE,"E14.bottom"),sQuery(id+"F15.wireOp",EDGE,"E14.top"),sQuery(id+"F15.wireOp",EDGE,"E14.left"),sQuery(id+"F15.wireOp",EDGE,"E14.right"),sQuery(id+"F15.wireOp",EDGE,"E15.MirrorCS"),sQuery(id+"F15.wireOp",EDGE,"E16.MirrorCS"),sQuery(id+"F15.wireOp",EDGE,"E17.MirrorCS"),sQuery(id+"F15.wireOp",EDGE,"E18.MirrorCS"),sQuery(id+"F15.wireOp",EDGE,"E19.MirrorCS"),sQuery(id+"F15.wireOp",EDGE,"E20.MirrorCS"),sQuery(id+"F15.wireOp",EDGE,"E21.MirrorCS"),sQuery(id+"F15.wireOp",EDGE,"E22.MirrorCS"),sQuery(id+"F15.wireOp",EDGE,"E23.MirrorCS"),sQuery(id+"F15.wireOp",EDGE,"E24.MirrorCS"),sQuery(id+"F15.wireOp",EDGE,"E25.MirrorCS"),sQuery(id+"F15.wireOp",EDGE,"E26.MirrorCS")])]}),"instanceName":"1"}),"instanceName":"1"}),"instanceName":"1"}),"instanceName":"1"});
            var Q46;
            Q46=makeQuery(id+"F22.opPattern","COPY",BODY,{"derivedFrom":makeQuery(id+"F20.opPattern","COPY",BODY,{"derivedFrom":makeQuery(id+"F19.opPattern","COPY",BODY,{"derivedFrom":makeQuery(id+"F18.opPattern","COPY",BODY,{"derivedFrom":makeQuery(id+"F17.opPattern","COPY",BODY,{"derivedFrom":makeQuery(id+"F16.opExtrude","SWEPT_BODY",BODY,{"disambiguationData":[OSD([sQuery(id+"F15.wireOp",EDGE,"E13.bottom"),sQuery(id+"F15.wireOp",EDGE,"E13.top"),sQuery(id+"F15.wireOp",EDGE,"E13.left"),sQuery(id+"F15.wireOp",EDGE,"E13.right"),sQuery(id+"F15.wireOp",EDGE,"E14.bottom"),sQuery(id+"F15.wireOp",EDGE,"E14.top"),sQuery(id+"F15.wireOp",EDGE,"E14.left"),sQuery(id+"F15.wireOp",EDGE,"E14.right"),sQuery(id+"F15.wireOp",EDGE,"E15.MirrorCS"),sQuery(id+"F15.wireOp",EDGE,"E16.MirrorCS"),sQuery(id+"F15.wireOp",EDGE,"E17.MirrorCS"),sQuery(id+"F15.wireOp",EDGE,"E18.MirrorCS"),sQuery(id+"F15.wireOp",EDGE,"E19.MirrorCS"),sQuery(id+"F15.wireOp",EDGE,"E20.MirrorCS"),sQuery(id+"F15.wireOp",EDGE,"E21.MirrorCS"),sQuery(id+"F15.wireOp",EDGE,"E22.MirrorCS"),sQuery(id+"F15.wireOp",EDGE,"E23.MirrorCS"),sQuery(id+"F15.wireOp",EDGE,"E24.MirrorCS"),sQuery(id+"F15.wireOp",EDGE,"E25.MirrorCS"),sQuery(id+"F15.wireOp",EDGE,"E26.MirrorCS")])]}),"instanceName":"1"}),"instanceName":"1"}),"instanceName":"1"}),"instanceName":"1"}),"instanceName":"1"});
            var Q47;
            Q47=makeQuery(id+"F22.opPattern","COPY",BODY,{"derivedFrom":makeQuery(id+"F21.opPattern","COPY",BODY,{"derivedFrom":makeQuery(id+"F16.opExtrude","SWEPT_BODY",BODY,{"disambiguationData":[OSD([sQuery(id+"F15.wireOp",EDGE,"E13.bottom"),sQuery(id+"F15.wireOp",EDGE,"E13.top"),sQuery(id+"F15.wireOp",EDGE,"E13.left"),sQuery(id+"F15.wireOp",EDGE,"E13.right"),sQuery(id+"F15.wireOp",EDGE,"E14.bottom"),sQuery(id+"F15.wireOp",EDGE,"E14.top"),sQuery(id+"F15.wireOp",EDGE,"E14.left"),sQuery(id+"F15.wireOp",EDGE,"E14.right"),sQuery(id+"F15.wireOp",EDGE,"E15.MirrorCS"),sQuery(id+"F15.wireOp",EDGE,"E16.MirrorCS"),sQuery(id+"F15.wireOp",EDGE,"E17.MirrorCS"),sQuery(id+"F15.wireOp",EDGE,"E18.MirrorCS"),sQuery(id+"F15.wireOp",EDGE,"E19.MirrorCS"),sQuery(id+"F15.wireOp",EDGE,"E20.MirrorCS"),sQuery(id+"F15.wireOp",EDGE,"E21.MirrorCS"),sQuery(id+"F15.wireOp",EDGE,"E22.MirrorCS"),sQuery(id+"F15.wireOp",EDGE,"E23.MirrorCS"),sQuery(id+"F15.wireOp",EDGE,"E24.MirrorCS"),sQuery(id+"F15.wireOp",EDGE,"E25.MirrorCS"),sQuery(id+"F15.wireOp",EDGE,"E26.MirrorCS")])]}),"instanceName":"1"}),"instanceName":"1"});
            var Q48;
            Q48=makeQuery(id+"F22.opPattern","COPY",BODY,{"derivedFrom":makeQuery(id+"F21.opPattern","COPY",BODY,{"derivedFrom":makeQuery(id+"F17.opPattern","COPY",BODY,{"derivedFrom":makeQuery(id+"F16.opExtrude","SWEPT_BODY",BODY,{"disambiguationData":[OSD([sQuery(id+"F15.wireOp",EDGE,"E13.bottom"),sQuery(id+"F15.wireOp",EDGE,"E13.top"),sQuery(id+"F15.wireOp",EDGE,"E13.left"),sQuery(id+"F15.wireOp",EDGE,"E13.right"),sQuery(id+"F15.wireOp",EDGE,"E14.bottom"),sQuery(id+"F15.wireOp",EDGE,"E14.top"),sQuery(id+"F15.wireOp",EDGE,"E14.left"),sQuery(id+"F15.wireOp",EDGE,"E14.right"),sQuery(id+"F15.wireOp",EDGE,"E15.MirrorCS"),sQuery(id+"F15.wireOp",EDGE,"E16.MirrorCS"),sQuery(id+"F15.wireOp",EDGE,"E17.MirrorCS"),sQuery(id+"F15.wireOp",EDGE,"E18.MirrorCS"),sQuery(id+"F15.wireOp",EDGE,"E19.MirrorCS"),sQuery(id+"F15.wireOp",EDGE,"E20.MirrorCS"),sQuery(id+"F15.wireOp",EDGE,"E21.MirrorCS"),sQuery(id+"F15.wireOp",EDGE,"E22.MirrorCS"),sQuery(id+"F15.wireOp",EDGE,"E23.MirrorCS"),sQuery(id+"F15.wireOp",EDGE,"E24.MirrorCS"),sQuery(id+"F15.wireOp",EDGE,"E25.MirrorCS"),sQuery(id+"F15.wireOp",EDGE,"E26.MirrorCS")])]}),"instanceName":"1"}),"instanceName":"1"}),"instanceName":"1"});
            var Q49;
            Q49=makeQuery(id+"F22.opPattern","COPY",BODY,{"derivedFrom":makeQuery(id+"F21.opPattern","COPY",BODY,{"derivedFrom":makeQuery(id+"F18.opPattern","COPY",BODY,{"derivedFrom":makeQuery(id+"F16.opExtrude","SWEPT_BODY",BODY,{"disambiguationData":[OSD([sQuery(id+"F15.wireOp",EDGE,"E13.bottom"),sQuery(id+"F15.wireOp",EDGE,"E13.top"),sQuery(id+"F15.wireOp",EDGE,"E13.left"),sQuery(id+"F15.wireOp",EDGE,"E13.right"),sQuery(id+"F15.wireOp",EDGE,"E14.bottom"),sQuery(id+"F15.wireOp",EDGE,"E14.top"),sQuery(id+"F15.wireOp",EDGE,"E14.left"),sQuery(id+"F15.wireOp",EDGE,"E14.right"),sQuery(id+"F15.wireOp",EDGE,"E15.MirrorCS"),sQuery(id+"F15.wireOp",EDGE,"E16.MirrorCS"),sQuery(id+"F15.wireOp",EDGE,"E17.MirrorCS"),sQuery(id+"F15.wireOp",EDGE,"E18.MirrorCS"),sQuery(id+"F15.wireOp",EDGE,"E19.MirrorCS"),sQuery(id+"F15.wireOp",EDGE,"E20.MirrorCS"),sQuery(id+"F15.wireOp",EDGE,"E21.MirrorCS"),sQuery(id+"F15.wireOp",EDGE,"E22.MirrorCS"),sQuery(id+"F15.wireOp",EDGE,"E23.MirrorCS"),sQuery(id+"F15.wireOp",EDGE,"E24.MirrorCS"),sQuery(id+"F15.wireOp",EDGE,"E25.MirrorCS"),sQuery(id+"F15.wireOp",EDGE,"E26.MirrorCS")])]}),"instanceName":"1"}),"instanceName":"1"}),"instanceName":"1"});
            var Q50;
            Q50=makeQuery(id+"F22.opPattern","COPY",BODY,{"derivedFrom":makeQuery(id+"F21.opPattern","COPY",BODY,{"derivedFrom":makeQuery(id+"F18.opPattern","COPY",BODY,{"derivedFrom":makeQuery(id+"F17.opPattern","COPY",BODY,{"derivedFrom":makeQuery(id+"F16.opExtrude","SWEPT_BODY",BODY,{"disambiguationData":[OSD([sQuery(id+"F15.wireOp",EDGE,"E13.bottom"),sQuery(id+"F15.wireOp",EDGE,"E13.top"),sQuery(id+"F15.wireOp",EDGE,"E13.left"),sQuery(id+"F15.wireOp",EDGE,"E13.right"),sQuery(id+"F15.wireOp",EDGE,"E14.bottom"),sQuery(id+"F15.wireOp",EDGE,"E14.top"),sQuery(id+"F15.wireOp",EDGE,"E14.left"),sQuery(id+"F15.wireOp",EDGE,"E14.right"),sQuery(id+"F15.wireOp",EDGE,"E15.MirrorCS"),sQuery(id+"F15.wireOp",EDGE,"E16.MirrorCS"),sQuery(id+"F15.wireOp",EDGE,"E17.MirrorCS"),sQuery(id+"F15.wireOp",EDGE,"E18.MirrorCS"),sQuery(id+"F15.wireOp",EDGE,"E19.MirrorCS"),sQuery(id+"F15.wireOp",EDGE,"E20.MirrorCS"),sQuery(id+"F15.wireOp",EDGE,"E21.MirrorCS"),sQuery(id+"F15.wireOp",EDGE,"E22.MirrorCS"),sQuery(id+"F15.wireOp",EDGE,"E23.MirrorCS"),sQuery(id+"F15.wireOp",EDGE,"E24.MirrorCS"),sQuery(id+"F15.wireOp",EDGE,"E25.MirrorCS"),sQuery(id+"F15.wireOp",EDGE,"E26.MirrorCS")])]}),"instanceName":"1"}),"instanceName":"1"}),"instanceName":"1"}),"instanceName":"1"});
            var Q51;
            Q51=makeQuery(id+"F22.opPattern","COPY",BODY,{"derivedFrom":makeQuery(id+"F21.opPattern","COPY",BODY,{"derivedFrom":makeQuery(id+"F19.opPattern","COPY",BODY,{"derivedFrom":makeQuery(id+"F16.opExtrude","SWEPT_BODY",BODY,{"disambiguationData":[OSD([sQuery(id+"F15.wireOp",EDGE,"E13.bottom"),sQuery(id+"F15.wireOp",EDGE,"E13.top"),sQuery(id+"F15.wireOp",EDGE,"E13.left"),sQuery(id+"F15.wireOp",EDGE,"E13.right"),sQuery(id+"F15.wireOp",EDGE,"E14.bottom"),sQuery(id+"F15.wireOp",EDGE,"E14.top"),sQuery(id+"F15.wireOp",EDGE,"E14.left"),sQuery(id+"F15.wireOp",EDGE,"E14.right"),sQuery(id+"F15.wireOp",EDGE,"E15.MirrorCS"),sQuery(id+"F15.wireOp",EDGE,"E16.MirrorCS"),sQuery(id+"F15.wireOp",EDGE,"E17.MirrorCS"),sQuery(id+"F15.wireOp",EDGE,"E18.MirrorCS"),sQuery(id+"F15.wireOp",EDGE,"E19.MirrorCS"),sQuery(id+"F15.wireOp",EDGE,"E20.MirrorCS"),sQuery(id+"F15.wireOp",EDGE,"E21.MirrorCS"),sQuery(id+"F15.wireOp",EDGE,"E22.MirrorCS"),sQuery(id+"F15.wireOp",EDGE,"E23.MirrorCS"),sQuery(id+"F15.wireOp",EDGE,"E24.MirrorCS"),sQuery(id+"F15.wireOp",EDGE,"E25.MirrorCS"),sQuery(id+"F15.wireOp",EDGE,"E26.MirrorCS")])]}),"instanceName":"1"}),"instanceName":"1"}),"instanceName":"1"});
            var Q52;
            Q52=makeQuery(id+"F22.opPattern","COPY",BODY,{"derivedFrom":makeQuery(id+"F21.opPattern","COPY",BODY,{"derivedFrom":makeQuery(id+"F19.opPattern","COPY",BODY,{"derivedFrom":makeQuery(id+"F17.opPattern","COPY",BODY,{"derivedFrom":makeQuery(id+"F16.opExtrude","SWEPT_BODY",BODY,{"disambiguationData":[OSD([sQuery(id+"F15.wireOp",EDGE,"E13.bottom"),sQuery(id+"F15.wireOp",EDGE,"E13.top"),sQuery(id+"F15.wireOp",EDGE,"E13.left"),sQuery(id+"F15.wireOp",EDGE,"E13.right"),sQuery(id+"F15.wireOp",EDGE,"E14.bottom"),sQuery(id+"F15.wireOp",EDGE,"E14.top"),sQuery(id+"F15.wireOp",EDGE,"E14.left"),sQuery(id+"F15.wireOp",EDGE,"E14.right"),sQuery(id+"F15.wireOp",EDGE,"E15.MirrorCS"),sQuery(id+"F15.wireOp",EDGE,"E16.MirrorCS"),sQuery(id+"F15.wireOp",EDGE,"E17.MirrorCS"),sQuery(id+"F15.wireOp",EDGE,"E18.MirrorCS"),sQuery(id+"F15.wireOp",EDGE,"E19.MirrorCS"),sQuery(id+"F15.wireOp",EDGE,"E20.MirrorCS"),sQuery(id+"F15.wireOp",EDGE,"E21.MirrorCS"),sQuery(id+"F15.wireOp",EDGE,"E22.MirrorCS"),sQuery(id+"F15.wireOp",EDGE,"E23.MirrorCS"),sQuery(id+"F15.wireOp",EDGE,"E24.MirrorCS"),sQuery(id+"F15.wireOp",EDGE,"E25.MirrorCS"),sQuery(id+"F15.wireOp",EDGE,"E26.MirrorCS")])]}),"instanceName":"1"}),"instanceName":"1"}),"instanceName":"1"}),"instanceName":"1"});
            var Q53;
            Q53=makeQuery(id+"F22.opPattern","COPY",BODY,{"derivedFrom":makeQuery(id+"F21.opPattern","COPY",BODY,{"derivedFrom":makeQuery(id+"F19.opPattern","COPY",BODY,{"derivedFrom":makeQuery(id+"F18.opPattern","COPY",BODY,{"derivedFrom":makeQuery(id+"F16.opExtrude","SWEPT_BODY",BODY,{"disambiguationData":[OSD([sQuery(id+"F15.wireOp",EDGE,"E13.bottom"),sQuery(id+"F15.wireOp",EDGE,"E13.top"),sQuery(id+"F15.wireOp",EDGE,"E13.left"),sQuery(id+"F15.wireOp",EDGE,"E13.right"),sQuery(id+"F15.wireOp",EDGE,"E14.bottom"),sQuery(id+"F15.wireOp",EDGE,"E14.top"),sQuery(id+"F15.wireOp",EDGE,"E14.left"),sQuery(id+"F15.wireOp",EDGE,"E14.right"),sQuery(id+"F15.wireOp",EDGE,"E15.MirrorCS"),sQuery(id+"F15.wireOp",EDGE,"E16.MirrorCS"),sQuery(id+"F15.wireOp",EDGE,"E17.MirrorCS"),sQuery(id+"F15.wireOp",EDGE,"E18.MirrorCS"),sQuery(id+"F15.wireOp",EDGE,"E19.MirrorCS"),sQuery(id+"F15.wireOp",EDGE,"E20.MirrorCS"),sQuery(id+"F15.wireOp",EDGE,"E21.MirrorCS"),sQuery(id+"F15.wireOp",EDGE,"E22.MirrorCS"),sQuery(id+"F15.wireOp",EDGE,"E23.MirrorCS"),sQuery(id+"F15.wireOp",EDGE,"E24.MirrorCS"),sQuery(id+"F15.wireOp",EDGE,"E25.MirrorCS"),sQuery(id+"F15.wireOp",EDGE,"E26.MirrorCS")])]}),"instanceName":"1"}),"instanceName":"1"}),"instanceName":"1"}),"instanceName":"1"});
            var Q54;
            Q54=makeQuery(id+"F22.opPattern","COPY",BODY,{"derivedFrom":makeQuery(id+"F21.opPattern","COPY",BODY,{"derivedFrom":makeQuery(id+"F19.opPattern","COPY",BODY,{"derivedFrom":makeQuery(id+"F18.opPattern","COPY",BODY,{"derivedFrom":makeQuery(id+"F17.opPattern","COPY",BODY,{"derivedFrom":makeQuery(id+"F16.opExtrude","SWEPT_BODY",BODY,{"disambiguationData":[OSD([sQuery(id+"F15.wireOp",EDGE,"E13.bottom"),sQuery(id+"F15.wireOp",EDGE,"E13.top"),sQuery(id+"F15.wireOp",EDGE,"E13.left"),sQuery(id+"F15.wireOp",EDGE,"E13.right"),sQuery(id+"F15.wireOp",EDGE,"E14.bottom"),sQuery(id+"F15.wireOp",EDGE,"E14.top"),sQuery(id+"F15.wireOp",EDGE,"E14.left"),sQuery(id+"F15.wireOp",EDGE,"E14.right"),sQuery(id+"F15.wireOp",EDGE,"E15.MirrorCS"),sQuery(id+"F15.wireOp",EDGE,"E16.MirrorCS"),sQuery(id+"F15.wireOp",EDGE,"E17.MirrorCS"),sQuery(id+"F15.wireOp",EDGE,"E18.MirrorCS"),sQuery(id+"F15.wireOp",EDGE,"E19.MirrorCS"),sQuery(id+"F15.wireOp",EDGE,"E20.MirrorCS"),sQuery(id+"F15.wireOp",EDGE,"E21.MirrorCS"),sQuery(id+"F15.wireOp",EDGE,"E22.MirrorCS"),sQuery(id+"F15.wireOp",EDGE,"E23.MirrorCS"),sQuery(id+"F15.wireOp",EDGE,"E24.MirrorCS"),sQuery(id+"F15.wireOp",EDGE,"E25.MirrorCS"),sQuery(id+"F15.wireOp",EDGE,"E26.MirrorCS")])]}),"instanceName":"1"}),"instanceName":"1"}),"instanceName":"1"}),"instanceName":"1"}),"instanceName":"1"});
            var Q55;
            Q55=makeQuery(id+"F22.opPattern","COPY",BODY,{"derivedFrom":makeQuery(id+"F21.opPattern","COPY",BODY,{"derivedFrom":makeQuery(id+"F20.opPattern","COPY",BODY,{"derivedFrom":makeQuery(id+"F16.opExtrude","SWEPT_BODY",BODY,{"disambiguationData":[OSD([sQuery(id+"F15.wireOp",EDGE,"E13.bottom"),sQuery(id+"F15.wireOp",EDGE,"E13.top"),sQuery(id+"F15.wireOp",EDGE,"E13.left"),sQuery(id+"F15.wireOp",EDGE,"E13.right"),sQuery(id+"F15.wireOp",EDGE,"E14.bottom"),sQuery(id+"F15.wireOp",EDGE,"E14.top"),sQuery(id+"F15.wireOp",EDGE,"E14.left"),sQuery(id+"F15.wireOp",EDGE,"E14.right"),sQuery(id+"F15.wireOp",EDGE,"E15.MirrorCS"),sQuery(id+"F15.wireOp",EDGE,"E16.MirrorCS"),sQuery(id+"F15.wireOp",EDGE,"E17.MirrorCS"),sQuery(id+"F15.wireOp",EDGE,"E18.MirrorCS"),sQuery(id+"F15.wireOp",EDGE,"E19.MirrorCS"),sQuery(id+"F15.wireOp",EDGE,"E20.MirrorCS"),sQuery(id+"F15.wireOp",EDGE,"E21.MirrorCS"),sQuery(id+"F15.wireOp",EDGE,"E22.MirrorCS"),sQuery(id+"F15.wireOp",EDGE,"E23.MirrorCS"),sQuery(id+"F15.wireOp",EDGE,"E24.MirrorCS"),sQuery(id+"F15.wireOp",EDGE,"E25.MirrorCS"),sQuery(id+"F15.wireOp",EDGE,"E26.MirrorCS")])]}),"instanceName":"1"}),"instanceName":"1"}),"instanceName":"1"});
            var Q56;
            Q56=makeQuery(id+"F22.opPattern","COPY",BODY,{"derivedFrom":makeQuery(id+"F21.opPattern","COPY",BODY,{"derivedFrom":makeQuery(id+"F20.opPattern","COPY",BODY,{"derivedFrom":makeQuery(id+"F17.opPattern","COPY",BODY,{"derivedFrom":makeQuery(id+"F16.opExtrude","SWEPT_BODY",BODY,{"disambiguationData":[OSD([sQuery(id+"F15.wireOp",EDGE,"E13.bottom"),sQuery(id+"F15.wireOp",EDGE,"E13.top"),sQuery(id+"F15.wireOp",EDGE,"E13.left"),sQuery(id+"F15.wireOp",EDGE,"E13.right"),sQuery(id+"F15.wireOp",EDGE,"E14.bottom"),sQuery(id+"F15.wireOp",EDGE,"E14.top"),sQuery(id+"F15.wireOp",EDGE,"E14.left"),sQuery(id+"F15.wireOp",EDGE,"E14.right"),sQuery(id+"F15.wireOp",EDGE,"E15.MirrorCS"),sQuery(id+"F15.wireOp",EDGE,"E16.MirrorCS"),sQuery(id+"F15.wireOp",EDGE,"E17.MirrorCS"),sQuery(id+"F15.wireOp",EDGE,"E18.MirrorCS"),sQuery(id+"F15.wireOp",EDGE,"E19.MirrorCS"),sQuery(id+"F15.wireOp",EDGE,"E20.MirrorCS"),sQuery(id+"F15.wireOp",EDGE,"E21.MirrorCS"),sQuery(id+"F15.wireOp",EDGE,"E22.MirrorCS"),sQuery(id+"F15.wireOp",EDGE,"E23.MirrorCS"),sQuery(id+"F15.wireOp",EDGE,"E24.MirrorCS"),sQuery(id+"F15.wireOp",EDGE,"E25.MirrorCS"),sQuery(id+"F15.wireOp",EDGE,"E26.MirrorCS")])]}),"instanceName":"1"}),"instanceName":"1"}),"instanceName":"1"}),"instanceName":"1"});
            var Q57;
            Q57=makeQuery(id+"F22.opPattern","COPY",BODY,{"derivedFrom":makeQuery(id+"F21.opPattern","COPY",BODY,{"derivedFrom":makeQuery(id+"F20.opPattern","COPY",BODY,{"derivedFrom":makeQuery(id+"F18.opPattern","COPY",BODY,{"derivedFrom":makeQuery(id+"F16.opExtrude","SWEPT_BODY",BODY,{"disambiguationData":[OSD([sQuery(id+"F15.wireOp",EDGE,"E13.bottom"),sQuery(id+"F15.wireOp",EDGE,"E13.top"),sQuery(id+"F15.wireOp",EDGE,"E13.left"),sQuery(id+"F15.wireOp",EDGE,"E13.right"),sQuery(id+"F15.wireOp",EDGE,"E14.bottom"),sQuery(id+"F15.wireOp",EDGE,"E14.top"),sQuery(id+"F15.wireOp",EDGE,"E14.left"),sQuery(id+"F15.wireOp",EDGE,"E14.right"),sQuery(id+"F15.wireOp",EDGE,"E15.MirrorCS"),sQuery(id+"F15.wireOp",EDGE,"E16.MirrorCS"),sQuery(id+"F15.wireOp",EDGE,"E17.MirrorCS"),sQuery(id+"F15.wireOp",EDGE,"E18.MirrorCS"),sQuery(id+"F15.wireOp",EDGE,"E19.MirrorCS"),sQuery(id+"F15.wireOp",EDGE,"E20.MirrorCS"),sQuery(id+"F15.wireOp",EDGE,"E21.MirrorCS"),sQuery(id+"F15.wireOp",EDGE,"E22.MirrorCS"),sQuery(id+"F15.wireOp",EDGE,"E23.MirrorCS"),sQuery(id+"F15.wireOp",EDGE,"E24.MirrorCS"),sQuery(id+"F15.wireOp",EDGE,"E25.MirrorCS"),sQuery(id+"F15.wireOp",EDGE,"E26.MirrorCS")])]}),"instanceName":"1"}),"instanceName":"1"}),"instanceName":"1"}),"instanceName":"1"});
            var Q58;
            Q58=makeQuery(id+"F22.opPattern","COPY",BODY,{"derivedFrom":makeQuery(id+"F21.opPattern","COPY",BODY,{"derivedFrom":makeQuery(id+"F20.opPattern","COPY",BODY,{"derivedFrom":makeQuery(id+"F18.opPattern","COPY",BODY,{"derivedFrom":makeQuery(id+"F17.opPattern","COPY",BODY,{"derivedFrom":makeQuery(id+"F16.opExtrude","SWEPT_BODY",BODY,{"disambiguationData":[OSD([sQuery(id+"F15.wireOp",EDGE,"E13.bottom"),sQuery(id+"F15.wireOp",EDGE,"E13.top"),sQuery(id+"F15.wireOp",EDGE,"E13.left"),sQuery(id+"F15.wireOp",EDGE,"E13.right"),sQuery(id+"F15.wireOp",EDGE,"E14.bottom"),sQuery(id+"F15.wireOp",EDGE,"E14.top"),sQuery(id+"F15.wireOp",EDGE,"E14.left"),sQuery(id+"F15.wireOp",EDGE,"E14.right"),sQuery(id+"F15.wireOp",EDGE,"E15.MirrorCS"),sQuery(id+"F15.wireOp",EDGE,"E16.MirrorCS"),sQuery(id+"F15.wireOp",EDGE,"E17.MirrorCS"),sQuery(id+"F15.wireOp",EDGE,"E18.MirrorCS"),sQuery(id+"F15.wireOp",EDGE,"E19.MirrorCS"),sQuery(id+"F15.wireOp",EDGE,"E20.MirrorCS"),sQuery(id+"F15.wireOp",EDGE,"E21.MirrorCS"),sQuery(id+"F15.wireOp",EDGE,"E22.MirrorCS"),sQuery(id+"F15.wireOp",EDGE,"E23.MirrorCS"),sQuery(id+"F15.wireOp",EDGE,"E24.MirrorCS"),sQuery(id+"F15.wireOp",EDGE,"E25.MirrorCS"),sQuery(id+"F15.wireOp",EDGE,"E26.MirrorCS")])]}),"instanceName":"1"}),"instanceName":"1"}),"instanceName":"1"}),"instanceName":"1"}),"instanceName":"1"});
            var Q59;
            Q59=makeQuery(id+"F22.opPattern","COPY",BODY,{"derivedFrom":makeQuery(id+"F21.opPattern","COPY",BODY,{"derivedFrom":makeQuery(id+"F20.opPattern","COPY",BODY,{"derivedFrom":makeQuery(id+"F19.opPattern","COPY",BODY,{"derivedFrom":makeQuery(id+"F16.opExtrude","SWEPT_BODY",BODY,{"disambiguationData":[OSD([sQuery(id+"F15.wireOp",EDGE,"E13.bottom"),sQuery(id+"F15.wireOp",EDGE,"E13.top"),sQuery(id+"F15.wireOp",EDGE,"E13.left"),sQuery(id+"F15.wireOp",EDGE,"E13.right"),sQuery(id+"F15.wireOp",EDGE,"E14.bottom"),sQuery(id+"F15.wireOp",EDGE,"E14.top"),sQuery(id+"F15.wireOp",EDGE,"E14.left"),sQuery(id+"F15.wireOp",EDGE,"E14.right"),sQuery(id+"F15.wireOp",EDGE,"E15.MirrorCS"),sQuery(id+"F15.wireOp",EDGE,"E16.MirrorCS"),sQuery(id+"F15.wireOp",EDGE,"E17.MirrorCS"),sQuery(id+"F15.wireOp",EDGE,"E18.MirrorCS"),sQuery(id+"F15.wireOp",EDGE,"E19.MirrorCS"),sQuery(id+"F15.wireOp",EDGE,"E20.MirrorCS"),sQuery(id+"F15.wireOp",EDGE,"E21.MirrorCS"),sQuery(id+"F15.wireOp",EDGE,"E22.MirrorCS"),sQuery(id+"F15.wireOp",EDGE,"E23.MirrorCS"),sQuery(id+"F15.wireOp",EDGE,"E24.MirrorCS"),sQuery(id+"F15.wireOp",EDGE,"E25.MirrorCS"),sQuery(id+"F15.wireOp",EDGE,"E26.MirrorCS")])]}),"instanceName":"1"}),"instanceName":"1"}),"instanceName":"1"}),"instanceName":"1"});
            var Q60;
            Q60=makeQuery(id+"F22.opPattern","COPY",BODY,{"derivedFrom":makeQuery(id+"F21.opPattern","COPY",BODY,{"derivedFrom":makeQuery(id+"F20.opPattern","COPY",BODY,{"derivedFrom":makeQuery(id+"F19.opPattern","COPY",BODY,{"derivedFrom":makeQuery(id+"F17.opPattern","COPY",BODY,{"derivedFrom":makeQuery(id+"F16.opExtrude","SWEPT_BODY",BODY,{"disambiguationData":[OSD([sQuery(id+"F15.wireOp",EDGE,"E13.bottom"),sQuery(id+"F15.wireOp",EDGE,"E13.top"),sQuery(id+"F15.wireOp",EDGE,"E13.left"),sQuery(id+"F15.wireOp",EDGE,"E13.right"),sQuery(id+"F15.wireOp",EDGE,"E14.bottom"),sQuery(id+"F15.wireOp",EDGE,"E14.top"),sQuery(id+"F15.wireOp",EDGE,"E14.left"),sQuery(id+"F15.wireOp",EDGE,"E14.right"),sQuery(id+"F15.wireOp",EDGE,"E15.MirrorCS"),sQuery(id+"F15.wireOp",EDGE,"E16.MirrorCS"),sQuery(id+"F15.wireOp",EDGE,"E17.MirrorCS"),sQuery(id+"F15.wireOp",EDGE,"E18.MirrorCS"),sQuery(id+"F15.wireOp",EDGE,"E19.MirrorCS"),sQuery(id+"F15.wireOp",EDGE,"E20.MirrorCS"),sQuery(id+"F15.wireOp",EDGE,"E21.MirrorCS"),sQuery(id+"F15.wireOp",EDGE,"E22.MirrorCS"),sQuery(id+"F15.wireOp",EDGE,"E23.MirrorCS"),sQuery(id+"F15.wireOp",EDGE,"E24.MirrorCS"),sQuery(id+"F15.wireOp",EDGE,"E25.MirrorCS"),sQuery(id+"F15.wireOp",EDGE,"E26.MirrorCS")])]}),"instanceName":"1"}),"instanceName":"1"}),"instanceName":"1"}),"instanceName":"1"}),"instanceName":"1"});
            var Q61;
            Q61=makeQuery(id+"F22.opPattern","COPY",BODY,{"derivedFrom":makeQuery(id+"F21.opPattern","COPY",BODY,{"derivedFrom":makeQuery(id+"F20.opPattern","COPY",BODY,{"derivedFrom":makeQuery(id+"F19.opPattern","COPY",BODY,{"derivedFrom":makeQuery(id+"F18.opPattern","COPY",BODY,{"derivedFrom":makeQuery(id+"F16.opExtrude","SWEPT_BODY",BODY,{"disambiguationData":[OSD([sQuery(id+"F15.wireOp",EDGE,"E13.bottom"),sQuery(id+"F15.wireOp",EDGE,"E13.top"),sQuery(id+"F15.wireOp",EDGE,"E13.left"),sQuery(id+"F15.wireOp",EDGE,"E13.right"),sQuery(id+"F15.wireOp",EDGE,"E14.bottom"),sQuery(id+"F15.wireOp",EDGE,"E14.top"),sQuery(id+"F15.wireOp",EDGE,"E14.left"),sQuery(id+"F15.wireOp",EDGE,"E14.right"),sQuery(id+"F15.wireOp",EDGE,"E15.MirrorCS"),sQuery(id+"F15.wireOp",EDGE,"E16.MirrorCS"),sQuery(id+"F15.wireOp",EDGE,"E17.MirrorCS"),sQuery(id+"F15.wireOp",EDGE,"E18.MirrorCS"),sQuery(id+"F15.wireOp",EDGE,"E19.MirrorCS"),sQuery(id+"F15.wireOp",EDGE,"E20.MirrorCS"),sQuery(id+"F15.wireOp",EDGE,"E21.MirrorCS"),sQuery(id+"F15.wireOp",EDGE,"E22.MirrorCS"),sQuery(id+"F15.wireOp",EDGE,"E23.MirrorCS"),sQuery(id+"F15.wireOp",EDGE,"E24.MirrorCS"),sQuery(id+"F15.wireOp",EDGE,"E25.MirrorCS"),sQuery(id+"F15.wireOp",EDGE,"E26.MirrorCS")])]}),"instanceName":"1"}),"instanceName":"1"}),"instanceName":"1"}),"instanceName":"1"}),"instanceName":"1"});
            transform(context, id + "F23", {"entities" : qUnion([Q0, Q1, Q2, Q3, Q4, Q5, Q6, Q7, Q8, Q9, Q10, Q11, Q12, Q13, Q14, Q15, Q16, Q17, Q18, Q19, Q20, Q21, Q22, Q23, Q24, Q25, Q26, Q27, Q28, Q29, Q30, Q31, Q32, Q33, Q34, Q35, Q36, Q37, Q38, Q39, Q40, Q41, Q42, Q43, Q44, Q45, Q46, Q47, Q48, Q49, Q50, Q51, Q52, Q53, Q54, Q55, Q56, Q57, Q58, Q59, Q60, Q61]), "transformType" : TransformType.TRANSLATION_3D, "dx" : -80 * mm, "dy" : 0 * mm, "dz" : 0 * mm, "makeCopy" : true});
        }
        {
            var Q0;
            Q0=makeQuery(id+"F16.opExtrude","SWEPT_BODY",BODY,{"disambiguationData":[OSD([sQuery(id+"F15.wireOp",EDGE,"E13.bottom"),sQuery(id+"F15.wireOp",EDGE,"E13.top"),sQuery(id+"F15.wireOp",EDGE,"E13.left"),sQuery(id+"F15.wireOp",EDGE,"E13.right"),sQuery(id+"F15.wireOp",EDGE,"E14.bottom"),sQuery(id+"F15.wireOp",EDGE,"E14.top"),sQuery(id+"F15.wireOp",EDGE,"E14.left"),sQuery(id+"F15.wireOp",EDGE,"E14.right"),sQuery(id+"F15.wireOp",EDGE,"E15.MirrorCS"),sQuery(id+"F15.wireOp",EDGE,"E16.MirrorCS"),sQuery(id+"F15.wireOp",EDGE,"E17.MirrorCS"),sQuery(id+"F15.wireOp",EDGE,"E18.MirrorCS"),sQuery(id+"F15.wireOp",EDGE,"E19.MirrorCS"),sQuery(id+"F15.wireOp",EDGE,"E20.MirrorCS"),sQuery(id+"F15.wireOp",EDGE,"E21.MirrorCS"),sQuery(id+"F15.wireOp",EDGE,"E22.MirrorCS"),sQuery(id+"F15.wireOp",EDGE,"E23.MirrorCS"),sQuery(id+"F15.wireOp",EDGE,"E24.MirrorCS"),sQuery(id+"F15.wireOp",EDGE,"E25.MirrorCS"),sQuery(id+"F15.wireOp",EDGE,"E26.MirrorCS")])]});
            var Q1;
            Q1=makeQuery(id+"F17.opPattern","COPY",BODY,{"derivedFrom":makeQuery(id+"F16.opExtrude","SWEPT_BODY",BODY,{"disambiguationData":[OSD([sQuery(id+"F15.wireOp",EDGE,"E13.bottom"),sQuery(id+"F15.wireOp",EDGE,"E13.top"),sQuery(id+"F15.wireOp",EDGE,"E13.left"),sQuery(id+"F15.wireOp",EDGE,"E13.right"),sQuery(id+"F15.wireOp",EDGE,"E14.bottom"),sQuery(id+"F15.wireOp",EDGE,"E14.top"),sQuery(id+"F15.wireOp",EDGE,"E14.left"),sQuery(id+"F15.wireOp",EDGE,"E14.right"),sQuery(id+"F15.wireOp",EDGE,"E15.MirrorCS"),sQuery(id+"F15.wireOp",EDGE,"E16.MirrorCS"),sQuery(id+"F15.wireOp",EDGE,"E17.MirrorCS"),sQuery(id+"F15.wireOp",EDGE,"E18.MirrorCS"),sQuery(id+"F15.wireOp",EDGE,"E19.MirrorCS"),sQuery(id+"F15.wireOp",EDGE,"E20.MirrorCS"),sQuery(id+"F15.wireOp",EDGE,"E21.MirrorCS"),sQuery(id+"F15.wireOp",EDGE,"E22.MirrorCS"),sQuery(id+"F15.wireOp",EDGE,"E23.MirrorCS"),sQuery(id+"F15.wireOp",EDGE,"E24.MirrorCS"),sQuery(id+"F15.wireOp",EDGE,"E25.MirrorCS"),sQuery(id+"F15.wireOp",EDGE,"E26.MirrorCS")])]}),"instanceName":"1"});
            var Q2;
            Q2=makeQuery(id+"F18.opPattern","COPY",BODY,{"derivedFrom":makeQuery(id+"F16.opExtrude","SWEPT_BODY",BODY,{"disambiguationData":[OSD([sQuery(id+"F15.wireOp",EDGE,"E13.bottom"),sQuery(id+"F15.wireOp",EDGE,"E13.top"),sQuery(id+"F15.wireOp",EDGE,"E13.left"),sQuery(id+"F15.wireOp",EDGE,"E13.right"),sQuery(id+"F15.wireOp",EDGE,"E14.bottom"),sQuery(id+"F15.wireOp",EDGE,"E14.top"),sQuery(id+"F15.wireOp",EDGE,"E14.left"),sQuery(id+"F15.wireOp",EDGE,"E14.right"),sQuery(id+"F15.wireOp",EDGE,"E15.MirrorCS"),sQuery(id+"F15.wireOp",EDGE,"E16.MirrorCS"),sQuery(id+"F15.wireOp",EDGE,"E17.MirrorCS"),sQuery(id+"F15.wireOp",EDGE,"E18.MirrorCS"),sQuery(id+"F15.wireOp",EDGE,"E19.MirrorCS"),sQuery(id+"F15.wireOp",EDGE,"E20.MirrorCS"),sQuery(id+"F15.wireOp",EDGE,"E21.MirrorCS"),sQuery(id+"F15.wireOp",EDGE,"E22.MirrorCS"),sQuery(id+"F15.wireOp",EDGE,"E23.MirrorCS"),sQuery(id+"F15.wireOp",EDGE,"E24.MirrorCS"),sQuery(id+"F15.wireOp",EDGE,"E25.MirrorCS"),sQuery(id+"F15.wireOp",EDGE,"E26.MirrorCS")])]}),"instanceName":"1"});
            var Q3;
            Q3=makeQuery(id+"F18.opPattern","COPY",BODY,{"derivedFrom":makeQuery(id+"F17.opPattern","COPY",BODY,{"derivedFrom":makeQuery(id+"F16.opExtrude","SWEPT_BODY",BODY,{"disambiguationData":[OSD([sQuery(id+"F15.wireOp",EDGE,"E13.bottom"),sQuery(id+"F15.wireOp",EDGE,"E13.top"),sQuery(id+"F15.wireOp",EDGE,"E13.left"),sQuery(id+"F15.wireOp",EDGE,"E13.right"),sQuery(id+"F15.wireOp",EDGE,"E14.bottom"),sQuery(id+"F15.wireOp",EDGE,"E14.top"),sQuery(id+"F15.wireOp",EDGE,"E14.left"),sQuery(id+"F15.wireOp",EDGE,"E14.right"),sQuery(id+"F15.wireOp",EDGE,"E15.MirrorCS"),sQuery(id+"F15.wireOp",EDGE,"E16.MirrorCS"),sQuery(id+"F15.wireOp",EDGE,"E17.MirrorCS"),sQuery(id+"F15.wireOp",EDGE,"E18.MirrorCS"),sQuery(id+"F15.wireOp",EDGE,"E19.MirrorCS"),sQuery(id+"F15.wireOp",EDGE,"E20.MirrorCS"),sQuery(id+"F15.wireOp",EDGE,"E21.MirrorCS"),sQuery(id+"F15.wireOp",EDGE,"E22.MirrorCS"),sQuery(id+"F15.wireOp",EDGE,"E23.MirrorCS"),sQuery(id+"F15.wireOp",EDGE,"E24.MirrorCS"),sQuery(id+"F15.wireOp",EDGE,"E25.MirrorCS"),sQuery(id+"F15.wireOp",EDGE,"E26.MirrorCS")])]}),"instanceName":"1"}),"instanceName":"1"});
            var Q4;
            Q4=makeQuery(id+"F19.opPattern","COPY",BODY,{"derivedFrom":makeQuery(id+"F16.opExtrude","SWEPT_BODY",BODY,{"disambiguationData":[OSD([sQuery(id+"F15.wireOp",EDGE,"E13.bottom"),sQuery(id+"F15.wireOp",EDGE,"E13.top"),sQuery(id+"F15.wireOp",EDGE,"E13.left"),sQuery(id+"F15.wireOp",EDGE,"E13.right"),sQuery(id+"F15.wireOp",EDGE,"E14.bottom"),sQuery(id+"F15.wireOp",EDGE,"E14.top"),sQuery(id+"F15.wireOp",EDGE,"E14.left"),sQuery(id+"F15.wireOp",EDGE,"E14.right"),sQuery(id+"F15.wireOp",EDGE,"E15.MirrorCS"),sQuery(id+"F15.wireOp",EDGE,"E16.MirrorCS"),sQuery(id+"F15.wireOp",EDGE,"E17.MirrorCS"),sQuery(id+"F15.wireOp",EDGE,"E18.MirrorCS"),sQuery(id+"F15.wireOp",EDGE,"E19.MirrorCS"),sQuery(id+"F15.wireOp",EDGE,"E20.MirrorCS"),sQuery(id+"F15.wireOp",EDGE,"E21.MirrorCS"),sQuery(id+"F15.wireOp",EDGE,"E22.MirrorCS"),sQuery(id+"F15.wireOp",EDGE,"E23.MirrorCS"),sQuery(id+"F15.wireOp",EDGE,"E24.MirrorCS"),sQuery(id+"F15.wireOp",EDGE,"E25.MirrorCS"),sQuery(id+"F15.wireOp",EDGE,"E26.MirrorCS")])]}),"instanceName":"1"});
            var Q5;
            Q5=makeQuery(id+"F19.opPattern","COPY",BODY,{"derivedFrom":makeQuery(id+"F17.opPattern","COPY",BODY,{"derivedFrom":makeQuery(id+"F16.opExtrude","SWEPT_BODY",BODY,{"disambiguationData":[OSD([sQuery(id+"F15.wireOp",EDGE,"E13.bottom"),sQuery(id+"F15.wireOp",EDGE,"E13.top"),sQuery(id+"F15.wireOp",EDGE,"E13.left"),sQuery(id+"F15.wireOp",EDGE,"E13.right"),sQuery(id+"F15.wireOp",EDGE,"E14.bottom"),sQuery(id+"F15.wireOp",EDGE,"E14.top"),sQuery(id+"F15.wireOp",EDGE,"E14.left"),sQuery(id+"F15.wireOp",EDGE,"E14.right"),sQuery(id+"F15.wireOp",EDGE,"E15.MirrorCS"),sQuery(id+"F15.wireOp",EDGE,"E16.MirrorCS"),sQuery(id+"F15.wireOp",EDGE,"E17.MirrorCS"),sQuery(id+"F15.wireOp",EDGE,"E18.MirrorCS"),sQuery(id+"F15.wireOp",EDGE,"E19.MirrorCS"),sQuery(id+"F15.wireOp",EDGE,"E20.MirrorCS"),sQuery(id+"F15.wireOp",EDGE,"E21.MirrorCS"),sQuery(id+"F15.wireOp",EDGE,"E22.MirrorCS"),sQuery(id+"F15.wireOp",EDGE,"E23.MirrorCS"),sQuery(id+"F15.wireOp",EDGE,"E24.MirrorCS"),sQuery(id+"F15.wireOp",EDGE,"E25.MirrorCS"),sQuery(id+"F15.wireOp",EDGE,"E26.MirrorCS")])]}),"instanceName":"1"}),"instanceName":"1"});
            var Q6;
            Q6=makeQuery(id+"F19.opPattern","COPY",BODY,{"derivedFrom":makeQuery(id+"F18.opPattern","COPY",BODY,{"derivedFrom":makeQuery(id+"F16.opExtrude","SWEPT_BODY",BODY,{"disambiguationData":[OSD([sQuery(id+"F15.wireOp",EDGE,"E13.bottom"),sQuery(id+"F15.wireOp",EDGE,"E13.top"),sQuery(id+"F15.wireOp",EDGE,"E13.left"),sQuery(id+"F15.wireOp",EDGE,"E13.right"),sQuery(id+"F15.wireOp",EDGE,"E14.bottom"),sQuery(id+"F15.wireOp",EDGE,"E14.top"),sQuery(id+"F15.wireOp",EDGE,"E14.left"),sQuery(id+"F15.wireOp",EDGE,"E14.right"),sQuery(id+"F15.wireOp",EDGE,"E15.MirrorCS"),sQuery(id+"F15.wireOp",EDGE,"E16.MirrorCS"),sQuery(id+"F15.wireOp",EDGE,"E17.MirrorCS"),sQuery(id+"F15.wireOp",EDGE,"E18.MirrorCS"),sQuery(id+"F15.wireOp",EDGE,"E19.MirrorCS"),sQuery(id+"F15.wireOp",EDGE,"E20.MirrorCS"),sQuery(id+"F15.wireOp",EDGE,"E21.MirrorCS"),sQuery(id+"F15.wireOp",EDGE,"E22.MirrorCS"),sQuery(id+"F15.wireOp",EDGE,"E23.MirrorCS"),sQuery(id+"F15.wireOp",EDGE,"E24.MirrorCS"),sQuery(id+"F15.wireOp",EDGE,"E25.MirrorCS"),sQuery(id+"F15.wireOp",EDGE,"E26.MirrorCS")])]}),"instanceName":"1"}),"instanceName":"1"});
            var Q7;
            Q7=makeQuery(id+"F19.opPattern","COPY",BODY,{"derivedFrom":makeQuery(id+"F18.opPattern","COPY",BODY,{"derivedFrom":makeQuery(id+"F17.opPattern","COPY",BODY,{"derivedFrom":makeQuery(id+"F16.opExtrude","SWEPT_BODY",BODY,{"disambiguationData":[OSD([sQuery(id+"F15.wireOp",EDGE,"E13.bottom"),sQuery(id+"F15.wireOp",EDGE,"E13.top"),sQuery(id+"F15.wireOp",EDGE,"E13.left"),sQuery(id+"F15.wireOp",EDGE,"E13.right"),sQuery(id+"F15.wireOp",EDGE,"E14.bottom"),sQuery(id+"F15.wireOp",EDGE,"E14.top"),sQuery(id+"F15.wireOp",EDGE,"E14.left"),sQuery(id+"F15.wireOp",EDGE,"E14.right"),sQuery(id+"F15.wireOp",EDGE,"E15.MirrorCS"),sQuery(id+"F15.wireOp",EDGE,"E16.MirrorCS"),sQuery(id+"F15.wireOp",EDGE,"E17.MirrorCS"),sQuery(id+"F15.wireOp",EDGE,"E18.MirrorCS"),sQuery(id+"F15.wireOp",EDGE,"E19.MirrorCS"),sQuery(id+"F15.wireOp",EDGE,"E20.MirrorCS"),sQuery(id+"F15.wireOp",EDGE,"E21.MirrorCS"),sQuery(id+"F15.wireOp",EDGE,"E22.MirrorCS"),sQuery(id+"F15.wireOp",EDGE,"E23.MirrorCS"),sQuery(id+"F15.wireOp",EDGE,"E24.MirrorCS"),sQuery(id+"F15.wireOp",EDGE,"E25.MirrorCS"),sQuery(id+"F15.wireOp",EDGE,"E26.MirrorCS")])]}),"instanceName":"1"}),"instanceName":"1"}),"instanceName":"1"});
            var Q8;
            Q8=makeQuery(id+"F20.opPattern","COPY",BODY,{"derivedFrom":makeQuery(id+"F16.opExtrude","SWEPT_BODY",BODY,{"disambiguationData":[OSD([sQuery(id+"F15.wireOp",EDGE,"E13.bottom"),sQuery(id+"F15.wireOp",EDGE,"E13.top"),sQuery(id+"F15.wireOp",EDGE,"E13.left"),sQuery(id+"F15.wireOp",EDGE,"E13.right"),sQuery(id+"F15.wireOp",EDGE,"E14.bottom"),sQuery(id+"F15.wireOp",EDGE,"E14.top"),sQuery(id+"F15.wireOp",EDGE,"E14.left"),sQuery(id+"F15.wireOp",EDGE,"E14.right"),sQuery(id+"F15.wireOp",EDGE,"E15.MirrorCS"),sQuery(id+"F15.wireOp",EDGE,"E16.MirrorCS"),sQuery(id+"F15.wireOp",EDGE,"E17.MirrorCS"),sQuery(id+"F15.wireOp",EDGE,"E18.MirrorCS"),sQuery(id+"F15.wireOp",EDGE,"E19.MirrorCS"),sQuery(id+"F15.wireOp",EDGE,"E20.MirrorCS"),sQuery(id+"F15.wireOp",EDGE,"E21.MirrorCS"),sQuery(id+"F15.wireOp",EDGE,"E22.MirrorCS"),sQuery(id+"F15.wireOp",EDGE,"E23.MirrorCS"),sQuery(id+"F15.wireOp",EDGE,"E24.MirrorCS"),sQuery(id+"F15.wireOp",EDGE,"E25.MirrorCS"),sQuery(id+"F15.wireOp",EDGE,"E26.MirrorCS")])]}),"instanceName":"1"});
            var Q9;
            Q9=makeQuery(id+"F20.opPattern","COPY",BODY,{"derivedFrom":makeQuery(id+"F17.opPattern","COPY",BODY,{"derivedFrom":makeQuery(id+"F16.opExtrude","SWEPT_BODY",BODY,{"disambiguationData":[OSD([sQuery(id+"F15.wireOp",EDGE,"E13.bottom"),sQuery(id+"F15.wireOp",EDGE,"E13.top"),sQuery(id+"F15.wireOp",EDGE,"E13.left"),sQuery(id+"F15.wireOp",EDGE,"E13.right"),sQuery(id+"F15.wireOp",EDGE,"E14.bottom"),sQuery(id+"F15.wireOp",EDGE,"E14.top"),sQuery(id+"F15.wireOp",EDGE,"E14.left"),sQuery(id+"F15.wireOp",EDGE,"E14.right"),sQuery(id+"F15.wireOp",EDGE,"E15.MirrorCS"),sQuery(id+"F15.wireOp",EDGE,"E16.MirrorCS"),sQuery(id+"F15.wireOp",EDGE,"E17.MirrorCS"),sQuery(id+"F15.wireOp",EDGE,"E18.MirrorCS"),sQuery(id+"F15.wireOp",EDGE,"E19.MirrorCS"),sQuery(id+"F15.wireOp",EDGE,"E20.MirrorCS"),sQuery(id+"F15.wireOp",EDGE,"E21.MirrorCS"),sQuery(id+"F15.wireOp",EDGE,"E22.MirrorCS"),sQuery(id+"F15.wireOp",EDGE,"E23.MirrorCS"),sQuery(id+"F15.wireOp",EDGE,"E24.MirrorCS"),sQuery(id+"F15.wireOp",EDGE,"E25.MirrorCS"),sQuery(id+"F15.wireOp",EDGE,"E26.MirrorCS")])]}),"instanceName":"1"}),"instanceName":"1"});
            var Q10;
            Q10=makeQuery(id+"F20.opPattern","COPY",BODY,{"derivedFrom":makeQuery(id+"F18.opPattern","COPY",BODY,{"derivedFrom":makeQuery(id+"F16.opExtrude","SWEPT_BODY",BODY,{"disambiguationData":[OSD([sQuery(id+"F15.wireOp",EDGE,"E13.bottom"),sQuery(id+"F15.wireOp",EDGE,"E13.top"),sQuery(id+"F15.wireOp",EDGE,"E13.left"),sQuery(id+"F15.wireOp",EDGE,"E13.right"),sQuery(id+"F15.wireOp",EDGE,"E14.bottom"),sQuery(id+"F15.wireOp",EDGE,"E14.top"),sQuery(id+"F15.wireOp",EDGE,"E14.left"),sQuery(id+"F15.wireOp",EDGE,"E14.right"),sQuery(id+"F15.wireOp",EDGE,"E15.MirrorCS"),sQuery(id+"F15.wireOp",EDGE,"E16.MirrorCS"),sQuery(id+"F15.wireOp",EDGE,"E17.MirrorCS"),sQuery(id+"F15.wireOp",EDGE,"E18.MirrorCS"),sQuery(id+"F15.wireOp",EDGE,"E19.MirrorCS"),sQuery(id+"F15.wireOp",EDGE,"E20.MirrorCS"),sQuery(id+"F15.wireOp",EDGE,"E21.MirrorCS"),sQuery(id+"F15.wireOp",EDGE,"E22.MirrorCS"),sQuery(id+"F15.wireOp",EDGE,"E23.MirrorCS"),sQuery(id+"F15.wireOp",EDGE,"E24.MirrorCS"),sQuery(id+"F15.wireOp",EDGE,"E25.MirrorCS"),sQuery(id+"F15.wireOp",EDGE,"E26.MirrorCS")])]}),"instanceName":"1"}),"instanceName":"1"});
            var Q11;
            Q11=makeQuery(id+"F20.opPattern","COPY",BODY,{"derivedFrom":makeQuery(id+"F18.opPattern","COPY",BODY,{"derivedFrom":makeQuery(id+"F17.opPattern","COPY",BODY,{"derivedFrom":makeQuery(id+"F16.opExtrude","SWEPT_BODY",BODY,{"disambiguationData":[OSD([sQuery(id+"F15.wireOp",EDGE,"E13.bottom"),sQuery(id+"F15.wireOp",EDGE,"E13.top"),sQuery(id+"F15.wireOp",EDGE,"E13.left"),sQuery(id+"F15.wireOp",EDGE,"E13.right"),sQuery(id+"F15.wireOp",EDGE,"E14.bottom"),sQuery(id+"F15.wireOp",EDGE,"E14.top"),sQuery(id+"F15.wireOp",EDGE,"E14.left"),sQuery(id+"F15.wireOp",EDGE,"E14.right"),sQuery(id+"F15.wireOp",EDGE,"E15.MirrorCS"),sQuery(id+"F15.wireOp",EDGE,"E16.MirrorCS"),sQuery(id+"F15.wireOp",EDGE,"E17.MirrorCS"),sQuery(id+"F15.wireOp",EDGE,"E18.MirrorCS"),sQuery(id+"F15.wireOp",EDGE,"E19.MirrorCS"),sQuery(id+"F15.wireOp",EDGE,"E20.MirrorCS"),sQuery(id+"F15.wireOp",EDGE,"E21.MirrorCS"),sQuery(id+"F15.wireOp",EDGE,"E22.MirrorCS"),sQuery(id+"F15.wireOp",EDGE,"E23.MirrorCS"),sQuery(id+"F15.wireOp",EDGE,"E24.MirrorCS"),sQuery(id+"F15.wireOp",EDGE,"E25.MirrorCS"),sQuery(id+"F15.wireOp",EDGE,"E26.MirrorCS")])]}),"instanceName":"1"}),"instanceName":"1"}),"instanceName":"1"});
            var Q12;
            Q12=makeQuery(id+"F20.opPattern","COPY",BODY,{"derivedFrom":makeQuery(id+"F19.opPattern","COPY",BODY,{"derivedFrom":makeQuery(id+"F16.opExtrude","SWEPT_BODY",BODY,{"disambiguationData":[OSD([sQuery(id+"F15.wireOp",EDGE,"E13.bottom"),sQuery(id+"F15.wireOp",EDGE,"E13.top"),sQuery(id+"F15.wireOp",EDGE,"E13.left"),sQuery(id+"F15.wireOp",EDGE,"E13.right"),sQuery(id+"F15.wireOp",EDGE,"E14.bottom"),sQuery(id+"F15.wireOp",EDGE,"E14.top"),sQuery(id+"F15.wireOp",EDGE,"E14.left"),sQuery(id+"F15.wireOp",EDGE,"E14.right"),sQuery(id+"F15.wireOp",EDGE,"E15.MirrorCS"),sQuery(id+"F15.wireOp",EDGE,"E16.MirrorCS"),sQuery(id+"F15.wireOp",EDGE,"E17.MirrorCS"),sQuery(id+"F15.wireOp",EDGE,"E18.MirrorCS"),sQuery(id+"F15.wireOp",EDGE,"E19.MirrorCS"),sQuery(id+"F15.wireOp",EDGE,"E20.MirrorCS"),sQuery(id+"F15.wireOp",EDGE,"E21.MirrorCS"),sQuery(id+"F15.wireOp",EDGE,"E22.MirrorCS"),sQuery(id+"F15.wireOp",EDGE,"E23.MirrorCS"),sQuery(id+"F15.wireOp",EDGE,"E24.MirrorCS"),sQuery(id+"F15.wireOp",EDGE,"E25.MirrorCS"),sQuery(id+"F15.wireOp",EDGE,"E26.MirrorCS")])]}),"instanceName":"1"}),"instanceName":"1"});
            var Q13;
            Q13=makeQuery(id+"F20.opPattern","COPY",BODY,{"derivedFrom":makeQuery(id+"F19.opPattern","COPY",BODY,{"derivedFrom":makeQuery(id+"F17.opPattern","COPY",BODY,{"derivedFrom":makeQuery(id+"F16.opExtrude","SWEPT_BODY",BODY,{"disambiguationData":[OSD([sQuery(id+"F15.wireOp",EDGE,"E13.bottom"),sQuery(id+"F15.wireOp",EDGE,"E13.top"),sQuery(id+"F15.wireOp",EDGE,"E13.left"),sQuery(id+"F15.wireOp",EDGE,"E13.right"),sQuery(id+"F15.wireOp",EDGE,"E14.bottom"),sQuery(id+"F15.wireOp",EDGE,"E14.top"),sQuery(id+"F15.wireOp",EDGE,"E14.left"),sQuery(id+"F15.wireOp",EDGE,"E14.right"),sQuery(id+"F15.wireOp",EDGE,"E15.MirrorCS"),sQuery(id+"F15.wireOp",EDGE,"E16.MirrorCS"),sQuery(id+"F15.wireOp",EDGE,"E17.MirrorCS"),sQuery(id+"F15.wireOp",EDGE,"E18.MirrorCS"),sQuery(id+"F15.wireOp",EDGE,"E19.MirrorCS"),sQuery(id+"F15.wireOp",EDGE,"E20.MirrorCS"),sQuery(id+"F15.wireOp",EDGE,"E21.MirrorCS"),sQuery(id+"F15.wireOp",EDGE,"E22.MirrorCS"),sQuery(id+"F15.wireOp",EDGE,"E23.MirrorCS"),sQuery(id+"F15.wireOp",EDGE,"E24.MirrorCS"),sQuery(id+"F15.wireOp",EDGE,"E25.MirrorCS"),sQuery(id+"F15.wireOp",EDGE,"E26.MirrorCS")])]}),"instanceName":"1"}),"instanceName":"1"}),"instanceName":"1"});
            var Q14;
            Q14=makeQuery(id+"F20.opPattern","COPY",BODY,{"derivedFrom":makeQuery(id+"F19.opPattern","COPY",BODY,{"derivedFrom":makeQuery(id+"F18.opPattern","COPY",BODY,{"derivedFrom":makeQuery(id+"F16.opExtrude","SWEPT_BODY",BODY,{"disambiguationData":[OSD([sQuery(id+"F15.wireOp",EDGE,"E13.bottom"),sQuery(id+"F15.wireOp",EDGE,"E13.top"),sQuery(id+"F15.wireOp",EDGE,"E13.left"),sQuery(id+"F15.wireOp",EDGE,"E13.right"),sQuery(id+"F15.wireOp",EDGE,"E14.bottom"),sQuery(id+"F15.wireOp",EDGE,"E14.top"),sQuery(id+"F15.wireOp",EDGE,"E14.left"),sQuery(id+"F15.wireOp",EDGE,"E14.right"),sQuery(id+"F15.wireOp",EDGE,"E15.MirrorCS"),sQuery(id+"F15.wireOp",EDGE,"E16.MirrorCS"),sQuery(id+"F15.wireOp",EDGE,"E17.MirrorCS"),sQuery(id+"F15.wireOp",EDGE,"E18.MirrorCS"),sQuery(id+"F15.wireOp",EDGE,"E19.MirrorCS"),sQuery(id+"F15.wireOp",EDGE,"E20.MirrorCS"),sQuery(id+"F15.wireOp",EDGE,"E21.MirrorCS"),sQuery(id+"F15.wireOp",EDGE,"E22.MirrorCS"),sQuery(id+"F15.wireOp",EDGE,"E23.MirrorCS"),sQuery(id+"F15.wireOp",EDGE,"E24.MirrorCS"),sQuery(id+"F15.wireOp",EDGE,"E25.MirrorCS"),sQuery(id+"F15.wireOp",EDGE,"E26.MirrorCS")])]}),"instanceName":"1"}),"instanceName":"1"}),"instanceName":"1"});
            var Q15;
            Q15=makeQuery(id+"F20.opPattern","COPY",BODY,{"derivedFrom":makeQuery(id+"F19.opPattern","COPY",BODY,{"derivedFrom":makeQuery(id+"F18.opPattern","COPY",BODY,{"derivedFrom":makeQuery(id+"F17.opPattern","COPY",BODY,{"derivedFrom":makeQuery(id+"F16.opExtrude","SWEPT_BODY",BODY,{"disambiguationData":[OSD([sQuery(id+"F15.wireOp",EDGE,"E13.bottom"),sQuery(id+"F15.wireOp",EDGE,"E13.top"),sQuery(id+"F15.wireOp",EDGE,"E13.left"),sQuery(id+"F15.wireOp",EDGE,"E13.right"),sQuery(id+"F15.wireOp",EDGE,"E14.bottom"),sQuery(id+"F15.wireOp",EDGE,"E14.top"),sQuery(id+"F15.wireOp",EDGE,"E14.left"),sQuery(id+"F15.wireOp",EDGE,"E14.right"),sQuery(id+"F15.wireOp",EDGE,"E15.MirrorCS"),sQuery(id+"F15.wireOp",EDGE,"E16.MirrorCS"),sQuery(id+"F15.wireOp",EDGE,"E17.MirrorCS"),sQuery(id+"F15.wireOp",EDGE,"E18.MirrorCS"),sQuery(id+"F15.wireOp",EDGE,"E19.MirrorCS"),sQuery(id+"F15.wireOp",EDGE,"E20.MirrorCS"),sQuery(id+"F15.wireOp",EDGE,"E21.MirrorCS"),sQuery(id+"F15.wireOp",EDGE,"E22.MirrorCS"),sQuery(id+"F15.wireOp",EDGE,"E23.MirrorCS"),sQuery(id+"F15.wireOp",EDGE,"E24.MirrorCS"),sQuery(id+"F15.wireOp",EDGE,"E25.MirrorCS"),sQuery(id+"F15.wireOp",EDGE,"E26.MirrorCS")])]}),"instanceName":"1"}),"instanceName":"1"}),"instanceName":"1"}),"instanceName":"1"});
            var Q16;
            Q16=makeQuery(id+"F21.opPattern","COPY",BODY,{"derivedFrom":makeQuery(id+"F16.opExtrude","SWEPT_BODY",BODY,{"disambiguationData":[OSD([sQuery(id+"F15.wireOp",EDGE,"E13.bottom"),sQuery(id+"F15.wireOp",EDGE,"E13.top"),sQuery(id+"F15.wireOp",EDGE,"E13.left"),sQuery(id+"F15.wireOp",EDGE,"E13.right"),sQuery(id+"F15.wireOp",EDGE,"E14.bottom"),sQuery(id+"F15.wireOp",EDGE,"E14.top"),sQuery(id+"F15.wireOp",EDGE,"E14.left"),sQuery(id+"F15.wireOp",EDGE,"E14.right"),sQuery(id+"F15.wireOp",EDGE,"E15.MirrorCS"),sQuery(id+"F15.wireOp",EDGE,"E16.MirrorCS"),sQuery(id+"F15.wireOp",EDGE,"E17.MirrorCS"),sQuery(id+"F15.wireOp",EDGE,"E18.MirrorCS"),sQuery(id+"F15.wireOp",EDGE,"E19.MirrorCS"),sQuery(id+"F15.wireOp",EDGE,"E20.MirrorCS"),sQuery(id+"F15.wireOp",EDGE,"E21.MirrorCS"),sQuery(id+"F15.wireOp",EDGE,"E22.MirrorCS"),sQuery(id+"F15.wireOp",EDGE,"E23.MirrorCS"),sQuery(id+"F15.wireOp",EDGE,"E24.MirrorCS"),sQuery(id+"F15.wireOp",EDGE,"E25.MirrorCS"),sQuery(id+"F15.wireOp",EDGE,"E26.MirrorCS")])]}),"instanceName":"1"});
            var Q17;
            Q17=makeQuery(id+"F21.opPattern","COPY",BODY,{"derivedFrom":makeQuery(id+"F17.opPattern","COPY",BODY,{"derivedFrom":makeQuery(id+"F16.opExtrude","SWEPT_BODY",BODY,{"disambiguationData":[OSD([sQuery(id+"F15.wireOp",EDGE,"E13.bottom"),sQuery(id+"F15.wireOp",EDGE,"E13.top"),sQuery(id+"F15.wireOp",EDGE,"E13.left"),sQuery(id+"F15.wireOp",EDGE,"E13.right"),sQuery(id+"F15.wireOp",EDGE,"E14.bottom"),sQuery(id+"F15.wireOp",EDGE,"E14.top"),sQuery(id+"F15.wireOp",EDGE,"E14.left"),sQuery(id+"F15.wireOp",EDGE,"E14.right"),sQuery(id+"F15.wireOp",EDGE,"E15.MirrorCS"),sQuery(id+"F15.wireOp",EDGE,"E16.MirrorCS"),sQuery(id+"F15.wireOp",EDGE,"E17.MirrorCS"),sQuery(id+"F15.wireOp",EDGE,"E18.MirrorCS"),sQuery(id+"F15.wireOp",EDGE,"E19.MirrorCS"),sQuery(id+"F15.wireOp",EDGE,"E20.MirrorCS"),sQuery(id+"F15.wireOp",EDGE,"E21.MirrorCS"),sQuery(id+"F15.wireOp",EDGE,"E22.MirrorCS"),sQuery(id+"F15.wireOp",EDGE,"E23.MirrorCS"),sQuery(id+"F15.wireOp",EDGE,"E24.MirrorCS"),sQuery(id+"F15.wireOp",EDGE,"E25.MirrorCS"),sQuery(id+"F15.wireOp",EDGE,"E26.MirrorCS")])]}),"instanceName":"1"}),"instanceName":"1"});
            var Q18;
            Q18=makeQuery(id+"F21.opPattern","COPY",BODY,{"derivedFrom":makeQuery(id+"F18.opPattern","COPY",BODY,{"derivedFrom":makeQuery(id+"F16.opExtrude","SWEPT_BODY",BODY,{"disambiguationData":[OSD([sQuery(id+"F15.wireOp",EDGE,"E13.bottom"),sQuery(id+"F15.wireOp",EDGE,"E13.top"),sQuery(id+"F15.wireOp",EDGE,"E13.left"),sQuery(id+"F15.wireOp",EDGE,"E13.right"),sQuery(id+"F15.wireOp",EDGE,"E14.bottom"),sQuery(id+"F15.wireOp",EDGE,"E14.top"),sQuery(id+"F15.wireOp",EDGE,"E14.left"),sQuery(id+"F15.wireOp",EDGE,"E14.right"),sQuery(id+"F15.wireOp",EDGE,"E15.MirrorCS"),sQuery(id+"F15.wireOp",EDGE,"E16.MirrorCS"),sQuery(id+"F15.wireOp",EDGE,"E17.MirrorCS"),sQuery(id+"F15.wireOp",EDGE,"E18.MirrorCS"),sQuery(id+"F15.wireOp",EDGE,"E19.MirrorCS"),sQuery(id+"F15.wireOp",EDGE,"E20.MirrorCS"),sQuery(id+"F15.wireOp",EDGE,"E21.MirrorCS"),sQuery(id+"F15.wireOp",EDGE,"E22.MirrorCS"),sQuery(id+"F15.wireOp",EDGE,"E23.MirrorCS"),sQuery(id+"F15.wireOp",EDGE,"E24.MirrorCS"),sQuery(id+"F15.wireOp",EDGE,"E25.MirrorCS"),sQuery(id+"F15.wireOp",EDGE,"E26.MirrorCS")])]}),"instanceName":"1"}),"instanceName":"1"});
            var Q19;
            Q19=makeQuery(id+"F21.opPattern","COPY",BODY,{"derivedFrom":makeQuery(id+"F18.opPattern","COPY",BODY,{"derivedFrom":makeQuery(id+"F17.opPattern","COPY",BODY,{"derivedFrom":makeQuery(id+"F16.opExtrude","SWEPT_BODY",BODY,{"disambiguationData":[OSD([sQuery(id+"F15.wireOp",EDGE,"E13.bottom"),sQuery(id+"F15.wireOp",EDGE,"E13.top"),sQuery(id+"F15.wireOp",EDGE,"E13.left"),sQuery(id+"F15.wireOp",EDGE,"E13.right"),sQuery(id+"F15.wireOp",EDGE,"E14.bottom"),sQuery(id+"F15.wireOp",EDGE,"E14.top"),sQuery(id+"F15.wireOp",EDGE,"E14.left"),sQuery(id+"F15.wireOp",EDGE,"E14.right"),sQuery(id+"F15.wireOp",EDGE,"E15.MirrorCS"),sQuery(id+"F15.wireOp",EDGE,"E16.MirrorCS"),sQuery(id+"F15.wireOp",EDGE,"E17.MirrorCS"),sQuery(id+"F15.wireOp",EDGE,"E18.MirrorCS"),sQuery(id+"F15.wireOp",EDGE,"E19.MirrorCS"),sQuery(id+"F15.wireOp",EDGE,"E20.MirrorCS"),sQuery(id+"F15.wireOp",EDGE,"E21.MirrorCS"),sQuery(id+"F15.wireOp",EDGE,"E22.MirrorCS"),sQuery(id+"F15.wireOp",EDGE,"E23.MirrorCS"),sQuery(id+"F15.wireOp",EDGE,"E24.MirrorCS"),sQuery(id+"F15.wireOp",EDGE,"E25.MirrorCS"),sQuery(id+"F15.wireOp",EDGE,"E26.MirrorCS")])]}),"instanceName":"1"}),"instanceName":"1"}),"instanceName":"1"});
            var Q20;
            Q20=makeQuery(id+"F21.opPattern","COPY",BODY,{"derivedFrom":makeQuery(id+"F19.opPattern","COPY",BODY,{"derivedFrom":makeQuery(id+"F16.opExtrude","SWEPT_BODY",BODY,{"disambiguationData":[OSD([sQuery(id+"F15.wireOp",EDGE,"E13.bottom"),sQuery(id+"F15.wireOp",EDGE,"E13.top"),sQuery(id+"F15.wireOp",EDGE,"E13.left"),sQuery(id+"F15.wireOp",EDGE,"E13.right"),sQuery(id+"F15.wireOp",EDGE,"E14.bottom"),sQuery(id+"F15.wireOp",EDGE,"E14.top"),sQuery(id+"F15.wireOp",EDGE,"E14.left"),sQuery(id+"F15.wireOp",EDGE,"E14.right"),sQuery(id+"F15.wireOp",EDGE,"E15.MirrorCS"),sQuery(id+"F15.wireOp",EDGE,"E16.MirrorCS"),sQuery(id+"F15.wireOp",EDGE,"E17.MirrorCS"),sQuery(id+"F15.wireOp",EDGE,"E18.MirrorCS"),sQuery(id+"F15.wireOp",EDGE,"E19.MirrorCS"),sQuery(id+"F15.wireOp",EDGE,"E20.MirrorCS"),sQuery(id+"F15.wireOp",EDGE,"E21.MirrorCS"),sQuery(id+"F15.wireOp",EDGE,"E22.MirrorCS"),sQuery(id+"F15.wireOp",EDGE,"E23.MirrorCS"),sQuery(id+"F15.wireOp",EDGE,"E24.MirrorCS"),sQuery(id+"F15.wireOp",EDGE,"E25.MirrorCS"),sQuery(id+"F15.wireOp",EDGE,"E26.MirrorCS")])]}),"instanceName":"1"}),"instanceName":"1"});
            var Q21;
            Q21=makeQuery(id+"F21.opPattern","COPY",BODY,{"derivedFrom":makeQuery(id+"F19.opPattern","COPY",BODY,{"derivedFrom":makeQuery(id+"F17.opPattern","COPY",BODY,{"derivedFrom":makeQuery(id+"F16.opExtrude","SWEPT_BODY",BODY,{"disambiguationData":[OSD([sQuery(id+"F15.wireOp",EDGE,"E13.bottom"),sQuery(id+"F15.wireOp",EDGE,"E13.top"),sQuery(id+"F15.wireOp",EDGE,"E13.left"),sQuery(id+"F15.wireOp",EDGE,"E13.right"),sQuery(id+"F15.wireOp",EDGE,"E14.bottom"),sQuery(id+"F15.wireOp",EDGE,"E14.top"),sQuery(id+"F15.wireOp",EDGE,"E14.left"),sQuery(id+"F15.wireOp",EDGE,"E14.right"),sQuery(id+"F15.wireOp",EDGE,"E15.MirrorCS"),sQuery(id+"F15.wireOp",EDGE,"E16.MirrorCS"),sQuery(id+"F15.wireOp",EDGE,"E17.MirrorCS"),sQuery(id+"F15.wireOp",EDGE,"E18.MirrorCS"),sQuery(id+"F15.wireOp",EDGE,"E19.MirrorCS"),sQuery(id+"F15.wireOp",EDGE,"E20.MirrorCS"),sQuery(id+"F15.wireOp",EDGE,"E21.MirrorCS"),sQuery(id+"F15.wireOp",EDGE,"E22.MirrorCS"),sQuery(id+"F15.wireOp",EDGE,"E23.MirrorCS"),sQuery(id+"F15.wireOp",EDGE,"E24.MirrorCS"),sQuery(id+"F15.wireOp",EDGE,"E25.MirrorCS"),sQuery(id+"F15.wireOp",EDGE,"E26.MirrorCS")])]}),"instanceName":"1"}),"instanceName":"1"}),"instanceName":"1"});
            var Q22;
            Q22=makeQuery(id+"F21.opPattern","COPY",BODY,{"derivedFrom":makeQuery(id+"F19.opPattern","COPY",BODY,{"derivedFrom":makeQuery(id+"F18.opPattern","COPY",BODY,{"derivedFrom":makeQuery(id+"F16.opExtrude","SWEPT_BODY",BODY,{"disambiguationData":[OSD([sQuery(id+"F15.wireOp",EDGE,"E13.bottom"),sQuery(id+"F15.wireOp",EDGE,"E13.top"),sQuery(id+"F15.wireOp",EDGE,"E13.left"),sQuery(id+"F15.wireOp",EDGE,"E13.right"),sQuery(id+"F15.wireOp",EDGE,"E14.bottom"),sQuery(id+"F15.wireOp",EDGE,"E14.top"),sQuery(id+"F15.wireOp",EDGE,"E14.left"),sQuery(id+"F15.wireOp",EDGE,"E14.right"),sQuery(id+"F15.wireOp",EDGE,"E15.MirrorCS"),sQuery(id+"F15.wireOp",EDGE,"E16.MirrorCS"),sQuery(id+"F15.wireOp",EDGE,"E17.MirrorCS"),sQuery(id+"F15.wireOp",EDGE,"E18.MirrorCS"),sQuery(id+"F15.wireOp",EDGE,"E19.MirrorCS"),sQuery(id+"F15.wireOp",EDGE,"E20.MirrorCS"),sQuery(id+"F15.wireOp",EDGE,"E21.MirrorCS"),sQuery(id+"F15.wireOp",EDGE,"E22.MirrorCS"),sQuery(id+"F15.wireOp",EDGE,"E23.MirrorCS"),sQuery(id+"F15.wireOp",EDGE,"E24.MirrorCS"),sQuery(id+"F15.wireOp",EDGE,"E25.MirrorCS"),sQuery(id+"F15.wireOp",EDGE,"E26.MirrorCS")])]}),"instanceName":"1"}),"instanceName":"1"}),"instanceName":"1"});
            var Q23;
            Q23=makeQuery(id+"F21.opPattern","COPY",BODY,{"derivedFrom":makeQuery(id+"F19.opPattern","COPY",BODY,{"derivedFrom":makeQuery(id+"F18.opPattern","COPY",BODY,{"derivedFrom":makeQuery(id+"F17.opPattern","COPY",BODY,{"derivedFrom":makeQuery(id+"F16.opExtrude","SWEPT_BODY",BODY,{"disambiguationData":[OSD([sQuery(id+"F15.wireOp",EDGE,"E13.bottom"),sQuery(id+"F15.wireOp",EDGE,"E13.top"),sQuery(id+"F15.wireOp",EDGE,"E13.left"),sQuery(id+"F15.wireOp",EDGE,"E13.right"),sQuery(id+"F15.wireOp",EDGE,"E14.bottom"),sQuery(id+"F15.wireOp",EDGE,"E14.top"),sQuery(id+"F15.wireOp",EDGE,"E14.left"),sQuery(id+"F15.wireOp",EDGE,"E14.right"),sQuery(id+"F15.wireOp",EDGE,"E15.MirrorCS"),sQuery(id+"F15.wireOp",EDGE,"E16.MirrorCS"),sQuery(id+"F15.wireOp",EDGE,"E17.MirrorCS"),sQuery(id+"F15.wireOp",EDGE,"E18.MirrorCS"),sQuery(id+"F15.wireOp",EDGE,"E19.MirrorCS"),sQuery(id+"F15.wireOp",EDGE,"E20.MirrorCS"),sQuery(id+"F15.wireOp",EDGE,"E21.MirrorCS"),sQuery(id+"F15.wireOp",EDGE,"E22.MirrorCS"),sQuery(id+"F15.wireOp",EDGE,"E23.MirrorCS"),sQuery(id+"F15.wireOp",EDGE,"E24.MirrorCS"),sQuery(id+"F15.wireOp",EDGE,"E25.MirrorCS"),sQuery(id+"F15.wireOp",EDGE,"E26.MirrorCS")])]}),"instanceName":"1"}),"instanceName":"1"}),"instanceName":"1"}),"instanceName":"1"});
            var Q24;
            Q24=makeQuery(id+"F21.opPattern","COPY",BODY,{"derivedFrom":makeQuery(id+"F20.opPattern","COPY",BODY,{"derivedFrom":makeQuery(id+"F16.opExtrude","SWEPT_BODY",BODY,{"disambiguationData":[OSD([sQuery(id+"F15.wireOp",EDGE,"E13.bottom"),sQuery(id+"F15.wireOp",EDGE,"E13.top"),sQuery(id+"F15.wireOp",EDGE,"E13.left"),sQuery(id+"F15.wireOp",EDGE,"E13.right"),sQuery(id+"F15.wireOp",EDGE,"E14.bottom"),sQuery(id+"F15.wireOp",EDGE,"E14.top"),sQuery(id+"F15.wireOp",EDGE,"E14.left"),sQuery(id+"F15.wireOp",EDGE,"E14.right"),sQuery(id+"F15.wireOp",EDGE,"E15.MirrorCS"),sQuery(id+"F15.wireOp",EDGE,"E16.MirrorCS"),sQuery(id+"F15.wireOp",EDGE,"E17.MirrorCS"),sQuery(id+"F15.wireOp",EDGE,"E18.MirrorCS"),sQuery(id+"F15.wireOp",EDGE,"E19.MirrorCS"),sQuery(id+"F15.wireOp",EDGE,"E20.MirrorCS"),sQuery(id+"F15.wireOp",EDGE,"E21.MirrorCS"),sQuery(id+"F15.wireOp",EDGE,"E22.MirrorCS"),sQuery(id+"F15.wireOp",EDGE,"E23.MirrorCS"),sQuery(id+"F15.wireOp",EDGE,"E24.MirrorCS"),sQuery(id+"F15.wireOp",EDGE,"E25.MirrorCS"),sQuery(id+"F15.wireOp",EDGE,"E26.MirrorCS")])]}),"instanceName":"1"}),"instanceName":"1"});
            var Q25;
            Q25=makeQuery(id+"F21.opPattern","COPY",BODY,{"derivedFrom":makeQuery(id+"F20.opPattern","COPY",BODY,{"derivedFrom":makeQuery(id+"F17.opPattern","COPY",BODY,{"derivedFrom":makeQuery(id+"F16.opExtrude","SWEPT_BODY",BODY,{"disambiguationData":[OSD([sQuery(id+"F15.wireOp",EDGE,"E13.bottom"),sQuery(id+"F15.wireOp",EDGE,"E13.top"),sQuery(id+"F15.wireOp",EDGE,"E13.left"),sQuery(id+"F15.wireOp",EDGE,"E13.right"),sQuery(id+"F15.wireOp",EDGE,"E14.bottom"),sQuery(id+"F15.wireOp",EDGE,"E14.top"),sQuery(id+"F15.wireOp",EDGE,"E14.left"),sQuery(id+"F15.wireOp",EDGE,"E14.right"),sQuery(id+"F15.wireOp",EDGE,"E15.MirrorCS"),sQuery(id+"F15.wireOp",EDGE,"E16.MirrorCS"),sQuery(id+"F15.wireOp",EDGE,"E17.MirrorCS"),sQuery(id+"F15.wireOp",EDGE,"E18.MirrorCS"),sQuery(id+"F15.wireOp",EDGE,"E19.MirrorCS"),sQuery(id+"F15.wireOp",EDGE,"E20.MirrorCS"),sQuery(id+"F15.wireOp",EDGE,"E21.MirrorCS"),sQuery(id+"F15.wireOp",EDGE,"E22.MirrorCS"),sQuery(id+"F15.wireOp",EDGE,"E23.MirrorCS"),sQuery(id+"F15.wireOp",EDGE,"E24.MirrorCS"),sQuery(id+"F15.wireOp",EDGE,"E25.MirrorCS"),sQuery(id+"F15.wireOp",EDGE,"E26.MirrorCS")])]}),"instanceName":"1"}),"instanceName":"1"}),"instanceName":"1"});
            var Q26;
            Q26=makeQuery(id+"F21.opPattern","COPY",BODY,{"derivedFrom":makeQuery(id+"F20.opPattern","COPY",BODY,{"derivedFrom":makeQuery(id+"F18.opPattern","COPY",BODY,{"derivedFrom":makeQuery(id+"F16.opExtrude","SWEPT_BODY",BODY,{"disambiguationData":[OSD([sQuery(id+"F15.wireOp",EDGE,"E13.bottom"),sQuery(id+"F15.wireOp",EDGE,"E13.top"),sQuery(id+"F15.wireOp",EDGE,"E13.left"),sQuery(id+"F15.wireOp",EDGE,"E13.right"),sQuery(id+"F15.wireOp",EDGE,"E14.bottom"),sQuery(id+"F15.wireOp",EDGE,"E14.top"),sQuery(id+"F15.wireOp",EDGE,"E14.left"),sQuery(id+"F15.wireOp",EDGE,"E14.right"),sQuery(id+"F15.wireOp",EDGE,"E15.MirrorCS"),sQuery(id+"F15.wireOp",EDGE,"E16.MirrorCS"),sQuery(id+"F15.wireOp",EDGE,"E17.MirrorCS"),sQuery(id+"F15.wireOp",EDGE,"E18.MirrorCS"),sQuery(id+"F15.wireOp",EDGE,"E19.MirrorCS"),sQuery(id+"F15.wireOp",EDGE,"E20.MirrorCS"),sQuery(id+"F15.wireOp",EDGE,"E21.MirrorCS"),sQuery(id+"F15.wireOp",EDGE,"E22.MirrorCS"),sQuery(id+"F15.wireOp",EDGE,"E23.MirrorCS"),sQuery(id+"F15.wireOp",EDGE,"E24.MirrorCS"),sQuery(id+"F15.wireOp",EDGE,"E25.MirrorCS"),sQuery(id+"F15.wireOp",EDGE,"E26.MirrorCS")])]}),"instanceName":"1"}),"instanceName":"1"}),"instanceName":"1"});
            var Q27;
            Q27=makeQuery(id+"F21.opPattern","COPY",BODY,{"derivedFrom":makeQuery(id+"F20.opPattern","COPY",BODY,{"derivedFrom":makeQuery(id+"F18.opPattern","COPY",BODY,{"derivedFrom":makeQuery(id+"F17.opPattern","COPY",BODY,{"derivedFrom":makeQuery(id+"F16.opExtrude","SWEPT_BODY",BODY,{"disambiguationData":[OSD([sQuery(id+"F15.wireOp",EDGE,"E13.bottom"),sQuery(id+"F15.wireOp",EDGE,"E13.top"),sQuery(id+"F15.wireOp",EDGE,"E13.left"),sQuery(id+"F15.wireOp",EDGE,"E13.right"),sQuery(id+"F15.wireOp",EDGE,"E14.bottom"),sQuery(id+"F15.wireOp",EDGE,"E14.top"),sQuery(id+"F15.wireOp",EDGE,"E14.left"),sQuery(id+"F15.wireOp",EDGE,"E14.right"),sQuery(id+"F15.wireOp",EDGE,"E15.MirrorCS"),sQuery(id+"F15.wireOp",EDGE,"E16.MirrorCS"),sQuery(id+"F15.wireOp",EDGE,"E17.MirrorCS"),sQuery(id+"F15.wireOp",EDGE,"E18.MirrorCS"),sQuery(id+"F15.wireOp",EDGE,"E19.MirrorCS"),sQuery(id+"F15.wireOp",EDGE,"E20.MirrorCS"),sQuery(id+"F15.wireOp",EDGE,"E21.MirrorCS"),sQuery(id+"F15.wireOp",EDGE,"E22.MirrorCS"),sQuery(id+"F15.wireOp",EDGE,"E23.MirrorCS"),sQuery(id+"F15.wireOp",EDGE,"E24.MirrorCS"),sQuery(id+"F15.wireOp",EDGE,"E25.MirrorCS"),sQuery(id+"F15.wireOp",EDGE,"E26.MirrorCS")])]}),"instanceName":"1"}),"instanceName":"1"}),"instanceName":"1"}),"instanceName":"1"});
            var Q28;
            Q28=makeQuery(id+"F21.opPattern","COPY",BODY,{"derivedFrom":makeQuery(id+"F20.opPattern","COPY",BODY,{"derivedFrom":makeQuery(id+"F19.opPattern","COPY",BODY,{"derivedFrom":makeQuery(id+"F16.opExtrude","SWEPT_BODY",BODY,{"disambiguationData":[OSD([sQuery(id+"F15.wireOp",EDGE,"E13.bottom"),sQuery(id+"F15.wireOp",EDGE,"E13.top"),sQuery(id+"F15.wireOp",EDGE,"E13.left"),sQuery(id+"F15.wireOp",EDGE,"E13.right"),sQuery(id+"F15.wireOp",EDGE,"E14.bottom"),sQuery(id+"F15.wireOp",EDGE,"E14.top"),sQuery(id+"F15.wireOp",EDGE,"E14.left"),sQuery(id+"F15.wireOp",EDGE,"E14.right"),sQuery(id+"F15.wireOp",EDGE,"E15.MirrorCS"),sQuery(id+"F15.wireOp",EDGE,"E16.MirrorCS"),sQuery(id+"F15.wireOp",EDGE,"E17.MirrorCS"),sQuery(id+"F15.wireOp",EDGE,"E18.MirrorCS"),sQuery(id+"F15.wireOp",EDGE,"E19.MirrorCS"),sQuery(id+"F15.wireOp",EDGE,"E20.MirrorCS"),sQuery(id+"F15.wireOp",EDGE,"E21.MirrorCS"),sQuery(id+"F15.wireOp",EDGE,"E22.MirrorCS"),sQuery(id+"F15.wireOp",EDGE,"E23.MirrorCS"),sQuery(id+"F15.wireOp",EDGE,"E24.MirrorCS"),sQuery(id+"F15.wireOp",EDGE,"E25.MirrorCS"),sQuery(id+"F15.wireOp",EDGE,"E26.MirrorCS")])]}),"instanceName":"1"}),"instanceName":"1"}),"instanceName":"1"});
            var Q29;
            Q29=makeQuery(id+"F21.opPattern","COPY",BODY,{"derivedFrom":makeQuery(id+"F20.opPattern","COPY",BODY,{"derivedFrom":makeQuery(id+"F19.opPattern","COPY",BODY,{"derivedFrom":makeQuery(id+"F17.opPattern","COPY",BODY,{"derivedFrom":makeQuery(id+"F16.opExtrude","SWEPT_BODY",BODY,{"disambiguationData":[OSD([sQuery(id+"F15.wireOp",EDGE,"E13.bottom"),sQuery(id+"F15.wireOp",EDGE,"E13.top"),sQuery(id+"F15.wireOp",EDGE,"E13.left"),sQuery(id+"F15.wireOp",EDGE,"E13.right"),sQuery(id+"F15.wireOp",EDGE,"E14.bottom"),sQuery(id+"F15.wireOp",EDGE,"E14.top"),sQuery(id+"F15.wireOp",EDGE,"E14.left"),sQuery(id+"F15.wireOp",EDGE,"E14.right"),sQuery(id+"F15.wireOp",EDGE,"E15.MirrorCS"),sQuery(id+"F15.wireOp",EDGE,"E16.MirrorCS"),sQuery(id+"F15.wireOp",EDGE,"E17.MirrorCS"),sQuery(id+"F15.wireOp",EDGE,"E18.MirrorCS"),sQuery(id+"F15.wireOp",EDGE,"E19.MirrorCS"),sQuery(id+"F15.wireOp",EDGE,"E20.MirrorCS"),sQuery(id+"F15.wireOp",EDGE,"E21.MirrorCS"),sQuery(id+"F15.wireOp",EDGE,"E22.MirrorCS"),sQuery(id+"F15.wireOp",EDGE,"E23.MirrorCS"),sQuery(id+"F15.wireOp",EDGE,"E24.MirrorCS"),sQuery(id+"F15.wireOp",EDGE,"E25.MirrorCS"),sQuery(id+"F15.wireOp",EDGE,"E26.MirrorCS")])]}),"instanceName":"1"}),"instanceName":"1"}),"instanceName":"1"}),"instanceName":"1"});
            var Q30;
            Q30=makeQuery(id+"F21.opPattern","COPY",BODY,{"derivedFrom":makeQuery(id+"F20.opPattern","COPY",BODY,{"derivedFrom":makeQuery(id+"F19.opPattern","COPY",BODY,{"derivedFrom":makeQuery(id+"F18.opPattern","COPY",BODY,{"derivedFrom":makeQuery(id+"F16.opExtrude","SWEPT_BODY",BODY,{"disambiguationData":[OSD([sQuery(id+"F15.wireOp",EDGE,"E13.bottom"),sQuery(id+"F15.wireOp",EDGE,"E13.top"),sQuery(id+"F15.wireOp",EDGE,"E13.left"),sQuery(id+"F15.wireOp",EDGE,"E13.right"),sQuery(id+"F15.wireOp",EDGE,"E14.bottom"),sQuery(id+"F15.wireOp",EDGE,"E14.top"),sQuery(id+"F15.wireOp",EDGE,"E14.left"),sQuery(id+"F15.wireOp",EDGE,"E14.right"),sQuery(id+"F15.wireOp",EDGE,"E15.MirrorCS"),sQuery(id+"F15.wireOp",EDGE,"E16.MirrorCS"),sQuery(id+"F15.wireOp",EDGE,"E17.MirrorCS"),sQuery(id+"F15.wireOp",EDGE,"E18.MirrorCS"),sQuery(id+"F15.wireOp",EDGE,"E19.MirrorCS"),sQuery(id+"F15.wireOp",EDGE,"E20.MirrorCS"),sQuery(id+"F15.wireOp",EDGE,"E21.MirrorCS"),sQuery(id+"F15.wireOp",EDGE,"E22.MirrorCS"),sQuery(id+"F15.wireOp",EDGE,"E23.MirrorCS"),sQuery(id+"F15.wireOp",EDGE,"E24.MirrorCS"),sQuery(id+"F15.wireOp",EDGE,"E25.MirrorCS"),sQuery(id+"F15.wireOp",EDGE,"E26.MirrorCS")])]}),"instanceName":"1"}),"instanceName":"1"}),"instanceName":"1"}),"instanceName":"1"});
            var Q31;
            Q31=makeQuery(id+"F22.opPattern","COPY",BODY,{"derivedFrom":makeQuery(id+"F16.opExtrude","SWEPT_BODY",BODY,{"disambiguationData":[OSD([sQuery(id+"F15.wireOp",EDGE,"E13.bottom"),sQuery(id+"F15.wireOp",EDGE,"E13.top"),sQuery(id+"F15.wireOp",EDGE,"E13.left"),sQuery(id+"F15.wireOp",EDGE,"E13.right"),sQuery(id+"F15.wireOp",EDGE,"E14.bottom"),sQuery(id+"F15.wireOp",EDGE,"E14.top"),sQuery(id+"F15.wireOp",EDGE,"E14.left"),sQuery(id+"F15.wireOp",EDGE,"E14.right"),sQuery(id+"F15.wireOp",EDGE,"E15.MirrorCS"),sQuery(id+"F15.wireOp",EDGE,"E16.MirrorCS"),sQuery(id+"F15.wireOp",EDGE,"E17.MirrorCS"),sQuery(id+"F15.wireOp",EDGE,"E18.MirrorCS"),sQuery(id+"F15.wireOp",EDGE,"E19.MirrorCS"),sQuery(id+"F15.wireOp",EDGE,"E20.MirrorCS"),sQuery(id+"F15.wireOp",EDGE,"E21.MirrorCS"),sQuery(id+"F15.wireOp",EDGE,"E22.MirrorCS"),sQuery(id+"F15.wireOp",EDGE,"E23.MirrorCS"),sQuery(id+"F15.wireOp",EDGE,"E24.MirrorCS"),sQuery(id+"F15.wireOp",EDGE,"E25.MirrorCS"),sQuery(id+"F15.wireOp",EDGE,"E26.MirrorCS")])]}),"instanceName":"1"});
            var Q32;
            Q32=makeQuery(id+"F22.opPattern","COPY",BODY,{"derivedFrom":makeQuery(id+"F17.opPattern","COPY",BODY,{"derivedFrom":makeQuery(id+"F16.opExtrude","SWEPT_BODY",BODY,{"disambiguationData":[OSD([sQuery(id+"F15.wireOp",EDGE,"E13.bottom"),sQuery(id+"F15.wireOp",EDGE,"E13.top"),sQuery(id+"F15.wireOp",EDGE,"E13.left"),sQuery(id+"F15.wireOp",EDGE,"E13.right"),sQuery(id+"F15.wireOp",EDGE,"E14.bottom"),sQuery(id+"F15.wireOp",EDGE,"E14.top"),sQuery(id+"F15.wireOp",EDGE,"E14.left"),sQuery(id+"F15.wireOp",EDGE,"E14.right"),sQuery(id+"F15.wireOp",EDGE,"E15.MirrorCS"),sQuery(id+"F15.wireOp",EDGE,"E16.MirrorCS"),sQuery(id+"F15.wireOp",EDGE,"E17.MirrorCS"),sQuery(id+"F15.wireOp",EDGE,"E18.MirrorCS"),sQuery(id+"F15.wireOp",EDGE,"E19.MirrorCS"),sQuery(id+"F15.wireOp",EDGE,"E20.MirrorCS"),sQuery(id+"F15.wireOp",EDGE,"E21.MirrorCS"),sQuery(id+"F15.wireOp",EDGE,"E22.MirrorCS"),sQuery(id+"F15.wireOp",EDGE,"E23.MirrorCS"),sQuery(id+"F15.wireOp",EDGE,"E24.MirrorCS"),sQuery(id+"F15.wireOp",EDGE,"E25.MirrorCS"),sQuery(id+"F15.wireOp",EDGE,"E26.MirrorCS")])]}),"instanceName":"1"}),"instanceName":"1"});
            var Q33;
            Q33=makeQuery(id+"F22.opPattern","COPY",BODY,{"derivedFrom":makeQuery(id+"F18.opPattern","COPY",BODY,{"derivedFrom":makeQuery(id+"F16.opExtrude","SWEPT_BODY",BODY,{"disambiguationData":[OSD([sQuery(id+"F15.wireOp",EDGE,"E13.bottom"),sQuery(id+"F15.wireOp",EDGE,"E13.top"),sQuery(id+"F15.wireOp",EDGE,"E13.left"),sQuery(id+"F15.wireOp",EDGE,"E13.right"),sQuery(id+"F15.wireOp",EDGE,"E14.bottom"),sQuery(id+"F15.wireOp",EDGE,"E14.top"),sQuery(id+"F15.wireOp",EDGE,"E14.left"),sQuery(id+"F15.wireOp",EDGE,"E14.right"),sQuery(id+"F15.wireOp",EDGE,"E15.MirrorCS"),sQuery(id+"F15.wireOp",EDGE,"E16.MirrorCS"),sQuery(id+"F15.wireOp",EDGE,"E17.MirrorCS"),sQuery(id+"F15.wireOp",EDGE,"E18.MirrorCS"),sQuery(id+"F15.wireOp",EDGE,"E19.MirrorCS"),sQuery(id+"F15.wireOp",EDGE,"E20.MirrorCS"),sQuery(id+"F15.wireOp",EDGE,"E21.MirrorCS"),sQuery(id+"F15.wireOp",EDGE,"E22.MirrorCS"),sQuery(id+"F15.wireOp",EDGE,"E23.MirrorCS"),sQuery(id+"F15.wireOp",EDGE,"E24.MirrorCS"),sQuery(id+"F15.wireOp",EDGE,"E25.MirrorCS"),sQuery(id+"F15.wireOp",EDGE,"E26.MirrorCS")])]}),"instanceName":"1"}),"instanceName":"1"});
            var Q34;
            Q34=makeQuery(id+"F22.opPattern","COPY",BODY,{"derivedFrom":makeQuery(id+"F18.opPattern","COPY",BODY,{"derivedFrom":makeQuery(id+"F17.opPattern","COPY",BODY,{"derivedFrom":makeQuery(id+"F16.opExtrude","SWEPT_BODY",BODY,{"disambiguationData":[OSD([sQuery(id+"F15.wireOp",EDGE,"E13.bottom"),sQuery(id+"F15.wireOp",EDGE,"E13.top"),sQuery(id+"F15.wireOp",EDGE,"E13.left"),sQuery(id+"F15.wireOp",EDGE,"E13.right"),sQuery(id+"F15.wireOp",EDGE,"E14.bottom"),sQuery(id+"F15.wireOp",EDGE,"E14.top"),sQuery(id+"F15.wireOp",EDGE,"E14.left"),sQuery(id+"F15.wireOp",EDGE,"E14.right"),sQuery(id+"F15.wireOp",EDGE,"E15.MirrorCS"),sQuery(id+"F15.wireOp",EDGE,"E16.MirrorCS"),sQuery(id+"F15.wireOp",EDGE,"E17.MirrorCS"),sQuery(id+"F15.wireOp",EDGE,"E18.MirrorCS"),sQuery(id+"F15.wireOp",EDGE,"E19.MirrorCS"),sQuery(id+"F15.wireOp",EDGE,"E20.MirrorCS"),sQuery(id+"F15.wireOp",EDGE,"E21.MirrorCS"),sQuery(id+"F15.wireOp",EDGE,"E22.MirrorCS"),sQuery(id+"F15.wireOp",EDGE,"E23.MirrorCS"),sQuery(id+"F15.wireOp",EDGE,"E24.MirrorCS"),sQuery(id+"F15.wireOp",EDGE,"E25.MirrorCS"),sQuery(id+"F15.wireOp",EDGE,"E26.MirrorCS")])]}),"instanceName":"1"}),"instanceName":"1"}),"instanceName":"1"});
            var Q35;
            Q35=makeQuery(id+"F22.opPattern","COPY",BODY,{"derivedFrom":makeQuery(id+"F19.opPattern","COPY",BODY,{"derivedFrom":makeQuery(id+"F16.opExtrude","SWEPT_BODY",BODY,{"disambiguationData":[OSD([sQuery(id+"F15.wireOp",EDGE,"E13.bottom"),sQuery(id+"F15.wireOp",EDGE,"E13.top"),sQuery(id+"F15.wireOp",EDGE,"E13.left"),sQuery(id+"F15.wireOp",EDGE,"E13.right"),sQuery(id+"F15.wireOp",EDGE,"E14.bottom"),sQuery(id+"F15.wireOp",EDGE,"E14.top"),sQuery(id+"F15.wireOp",EDGE,"E14.left"),sQuery(id+"F15.wireOp",EDGE,"E14.right"),sQuery(id+"F15.wireOp",EDGE,"E15.MirrorCS"),sQuery(id+"F15.wireOp",EDGE,"E16.MirrorCS"),sQuery(id+"F15.wireOp",EDGE,"E17.MirrorCS"),sQuery(id+"F15.wireOp",EDGE,"E18.MirrorCS"),sQuery(id+"F15.wireOp",EDGE,"E19.MirrorCS"),sQuery(id+"F15.wireOp",EDGE,"E20.MirrorCS"),sQuery(id+"F15.wireOp",EDGE,"E21.MirrorCS"),sQuery(id+"F15.wireOp",EDGE,"E22.MirrorCS"),sQuery(id+"F15.wireOp",EDGE,"E23.MirrorCS"),sQuery(id+"F15.wireOp",EDGE,"E24.MirrorCS"),sQuery(id+"F15.wireOp",EDGE,"E25.MirrorCS"),sQuery(id+"F15.wireOp",EDGE,"E26.MirrorCS")])]}),"instanceName":"1"}),"instanceName":"1"});
            var Q36;
            Q36=makeQuery(id+"F22.opPattern","COPY",BODY,{"derivedFrom":makeQuery(id+"F19.opPattern","COPY",BODY,{"derivedFrom":makeQuery(id+"F17.opPattern","COPY",BODY,{"derivedFrom":makeQuery(id+"F16.opExtrude","SWEPT_BODY",BODY,{"disambiguationData":[OSD([sQuery(id+"F15.wireOp",EDGE,"E13.bottom"),sQuery(id+"F15.wireOp",EDGE,"E13.top"),sQuery(id+"F15.wireOp",EDGE,"E13.left"),sQuery(id+"F15.wireOp",EDGE,"E13.right"),sQuery(id+"F15.wireOp",EDGE,"E14.bottom"),sQuery(id+"F15.wireOp",EDGE,"E14.top"),sQuery(id+"F15.wireOp",EDGE,"E14.left"),sQuery(id+"F15.wireOp",EDGE,"E14.right"),sQuery(id+"F15.wireOp",EDGE,"E15.MirrorCS"),sQuery(id+"F15.wireOp",EDGE,"E16.MirrorCS"),sQuery(id+"F15.wireOp",EDGE,"E17.MirrorCS"),sQuery(id+"F15.wireOp",EDGE,"E18.MirrorCS"),sQuery(id+"F15.wireOp",EDGE,"E19.MirrorCS"),sQuery(id+"F15.wireOp",EDGE,"E20.MirrorCS"),sQuery(id+"F15.wireOp",EDGE,"E21.MirrorCS"),sQuery(id+"F15.wireOp",EDGE,"E22.MirrorCS"),sQuery(id+"F15.wireOp",EDGE,"E23.MirrorCS"),sQuery(id+"F15.wireOp",EDGE,"E24.MirrorCS"),sQuery(id+"F15.wireOp",EDGE,"E25.MirrorCS"),sQuery(id+"F15.wireOp",EDGE,"E26.MirrorCS")])]}),"instanceName":"1"}),"instanceName":"1"}),"instanceName":"1"});
            var Q37;
            Q37=makeQuery(id+"F22.opPattern","COPY",BODY,{"derivedFrom":makeQuery(id+"F19.opPattern","COPY",BODY,{"derivedFrom":makeQuery(id+"F18.opPattern","COPY",BODY,{"derivedFrom":makeQuery(id+"F16.opExtrude","SWEPT_BODY",BODY,{"disambiguationData":[OSD([sQuery(id+"F15.wireOp",EDGE,"E13.bottom"),sQuery(id+"F15.wireOp",EDGE,"E13.top"),sQuery(id+"F15.wireOp",EDGE,"E13.left"),sQuery(id+"F15.wireOp",EDGE,"E13.right"),sQuery(id+"F15.wireOp",EDGE,"E14.bottom"),sQuery(id+"F15.wireOp",EDGE,"E14.top"),sQuery(id+"F15.wireOp",EDGE,"E14.left"),sQuery(id+"F15.wireOp",EDGE,"E14.right"),sQuery(id+"F15.wireOp",EDGE,"E15.MirrorCS"),sQuery(id+"F15.wireOp",EDGE,"E16.MirrorCS"),sQuery(id+"F15.wireOp",EDGE,"E17.MirrorCS"),sQuery(id+"F15.wireOp",EDGE,"E18.MirrorCS"),sQuery(id+"F15.wireOp",EDGE,"E19.MirrorCS"),sQuery(id+"F15.wireOp",EDGE,"E20.MirrorCS"),sQuery(id+"F15.wireOp",EDGE,"E21.MirrorCS"),sQuery(id+"F15.wireOp",EDGE,"E22.MirrorCS"),sQuery(id+"F15.wireOp",EDGE,"E23.MirrorCS"),sQuery(id+"F15.wireOp",EDGE,"E24.MirrorCS"),sQuery(id+"F15.wireOp",EDGE,"E25.MirrorCS"),sQuery(id+"F15.wireOp",EDGE,"E26.MirrorCS")])]}),"instanceName":"1"}),"instanceName":"1"}),"instanceName":"1"});
            var Q38;
            Q38=makeQuery(id+"F22.opPattern","COPY",BODY,{"derivedFrom":makeQuery(id+"F19.opPattern","COPY",BODY,{"derivedFrom":makeQuery(id+"F18.opPattern","COPY",BODY,{"derivedFrom":makeQuery(id+"F17.opPattern","COPY",BODY,{"derivedFrom":makeQuery(id+"F16.opExtrude","SWEPT_BODY",BODY,{"disambiguationData":[OSD([sQuery(id+"F15.wireOp",EDGE,"E13.bottom"),sQuery(id+"F15.wireOp",EDGE,"E13.top"),sQuery(id+"F15.wireOp",EDGE,"E13.left"),sQuery(id+"F15.wireOp",EDGE,"E13.right"),sQuery(id+"F15.wireOp",EDGE,"E14.bottom"),sQuery(id+"F15.wireOp",EDGE,"E14.top"),sQuery(id+"F15.wireOp",EDGE,"E14.left"),sQuery(id+"F15.wireOp",EDGE,"E14.right"),sQuery(id+"F15.wireOp",EDGE,"E15.MirrorCS"),sQuery(id+"F15.wireOp",EDGE,"E16.MirrorCS"),sQuery(id+"F15.wireOp",EDGE,"E17.MirrorCS"),sQuery(id+"F15.wireOp",EDGE,"E18.MirrorCS"),sQuery(id+"F15.wireOp",EDGE,"E19.MirrorCS"),sQuery(id+"F15.wireOp",EDGE,"E20.MirrorCS"),sQuery(id+"F15.wireOp",EDGE,"E21.MirrorCS"),sQuery(id+"F15.wireOp",EDGE,"E22.MirrorCS"),sQuery(id+"F15.wireOp",EDGE,"E23.MirrorCS"),sQuery(id+"F15.wireOp",EDGE,"E24.MirrorCS"),sQuery(id+"F15.wireOp",EDGE,"E25.MirrorCS"),sQuery(id+"F15.wireOp",EDGE,"E26.MirrorCS")])]}),"instanceName":"1"}),"instanceName":"1"}),"instanceName":"1"}),"instanceName":"1"});
            var Q39;
            Q39=makeQuery(id+"F22.opPattern","COPY",BODY,{"derivedFrom":makeQuery(id+"F20.opPattern","COPY",BODY,{"derivedFrom":makeQuery(id+"F16.opExtrude","SWEPT_BODY",BODY,{"disambiguationData":[OSD([sQuery(id+"F15.wireOp",EDGE,"E13.bottom"),sQuery(id+"F15.wireOp",EDGE,"E13.top"),sQuery(id+"F15.wireOp",EDGE,"E13.left"),sQuery(id+"F15.wireOp",EDGE,"E13.right"),sQuery(id+"F15.wireOp",EDGE,"E14.bottom"),sQuery(id+"F15.wireOp",EDGE,"E14.top"),sQuery(id+"F15.wireOp",EDGE,"E14.left"),sQuery(id+"F15.wireOp",EDGE,"E14.right"),sQuery(id+"F15.wireOp",EDGE,"E15.MirrorCS"),sQuery(id+"F15.wireOp",EDGE,"E16.MirrorCS"),sQuery(id+"F15.wireOp",EDGE,"E17.MirrorCS"),sQuery(id+"F15.wireOp",EDGE,"E18.MirrorCS"),sQuery(id+"F15.wireOp",EDGE,"E19.MirrorCS"),sQuery(id+"F15.wireOp",EDGE,"E20.MirrorCS"),sQuery(id+"F15.wireOp",EDGE,"E21.MirrorCS"),sQuery(id+"F15.wireOp",EDGE,"E22.MirrorCS"),sQuery(id+"F15.wireOp",EDGE,"E23.MirrorCS"),sQuery(id+"F15.wireOp",EDGE,"E24.MirrorCS"),sQuery(id+"F15.wireOp",EDGE,"E25.MirrorCS"),sQuery(id+"F15.wireOp",EDGE,"E26.MirrorCS")])]}),"instanceName":"1"}),"instanceName":"1"});
            var Q40;
            Q40=makeQuery(id+"F22.opPattern","COPY",BODY,{"derivedFrom":makeQuery(id+"F20.opPattern","COPY",BODY,{"derivedFrom":makeQuery(id+"F17.opPattern","COPY",BODY,{"derivedFrom":makeQuery(id+"F16.opExtrude","SWEPT_BODY",BODY,{"disambiguationData":[OSD([sQuery(id+"F15.wireOp",EDGE,"E13.bottom"),sQuery(id+"F15.wireOp",EDGE,"E13.top"),sQuery(id+"F15.wireOp",EDGE,"E13.left"),sQuery(id+"F15.wireOp",EDGE,"E13.right"),sQuery(id+"F15.wireOp",EDGE,"E14.bottom"),sQuery(id+"F15.wireOp",EDGE,"E14.top"),sQuery(id+"F15.wireOp",EDGE,"E14.left"),sQuery(id+"F15.wireOp",EDGE,"E14.right"),sQuery(id+"F15.wireOp",EDGE,"E15.MirrorCS"),sQuery(id+"F15.wireOp",EDGE,"E16.MirrorCS"),sQuery(id+"F15.wireOp",EDGE,"E17.MirrorCS"),sQuery(id+"F15.wireOp",EDGE,"E18.MirrorCS"),sQuery(id+"F15.wireOp",EDGE,"E19.MirrorCS"),sQuery(id+"F15.wireOp",EDGE,"E20.MirrorCS"),sQuery(id+"F15.wireOp",EDGE,"E21.MirrorCS"),sQuery(id+"F15.wireOp",EDGE,"E22.MirrorCS"),sQuery(id+"F15.wireOp",EDGE,"E23.MirrorCS"),sQuery(id+"F15.wireOp",EDGE,"E24.MirrorCS"),sQuery(id+"F15.wireOp",EDGE,"E25.MirrorCS"),sQuery(id+"F15.wireOp",EDGE,"E26.MirrorCS")])]}),"instanceName":"1"}),"instanceName":"1"}),"instanceName":"1"});
            var Q41;
            Q41=makeQuery(id+"F22.opPattern","COPY",BODY,{"derivedFrom":makeQuery(id+"F20.opPattern","COPY",BODY,{"derivedFrom":makeQuery(id+"F18.opPattern","COPY",BODY,{"derivedFrom":makeQuery(id+"F16.opExtrude","SWEPT_BODY",BODY,{"disambiguationData":[OSD([sQuery(id+"F15.wireOp",EDGE,"E13.bottom"),sQuery(id+"F15.wireOp",EDGE,"E13.top"),sQuery(id+"F15.wireOp",EDGE,"E13.left"),sQuery(id+"F15.wireOp",EDGE,"E13.right"),sQuery(id+"F15.wireOp",EDGE,"E14.bottom"),sQuery(id+"F15.wireOp",EDGE,"E14.top"),sQuery(id+"F15.wireOp",EDGE,"E14.left"),sQuery(id+"F15.wireOp",EDGE,"E14.right"),sQuery(id+"F15.wireOp",EDGE,"E15.MirrorCS"),sQuery(id+"F15.wireOp",EDGE,"E16.MirrorCS"),sQuery(id+"F15.wireOp",EDGE,"E17.MirrorCS"),sQuery(id+"F15.wireOp",EDGE,"E18.MirrorCS"),sQuery(id+"F15.wireOp",EDGE,"E19.MirrorCS"),sQuery(id+"F15.wireOp",EDGE,"E20.MirrorCS"),sQuery(id+"F15.wireOp",EDGE,"E21.MirrorCS"),sQuery(id+"F15.wireOp",EDGE,"E22.MirrorCS"),sQuery(id+"F15.wireOp",EDGE,"E23.MirrorCS"),sQuery(id+"F15.wireOp",EDGE,"E24.MirrorCS"),sQuery(id+"F15.wireOp",EDGE,"E25.MirrorCS"),sQuery(id+"F15.wireOp",EDGE,"E26.MirrorCS")])]}),"instanceName":"1"}),"instanceName":"1"}),"instanceName":"1"});
            var Q42;
            Q42=makeQuery(id+"F22.opPattern","COPY",BODY,{"derivedFrom":makeQuery(id+"F20.opPattern","COPY",BODY,{"derivedFrom":makeQuery(id+"F18.opPattern","COPY",BODY,{"derivedFrom":makeQuery(id+"F17.opPattern","COPY",BODY,{"derivedFrom":makeQuery(id+"F16.opExtrude","SWEPT_BODY",BODY,{"disambiguationData":[OSD([sQuery(id+"F15.wireOp",EDGE,"E13.bottom"),sQuery(id+"F15.wireOp",EDGE,"E13.top"),sQuery(id+"F15.wireOp",EDGE,"E13.left"),sQuery(id+"F15.wireOp",EDGE,"E13.right"),sQuery(id+"F15.wireOp",EDGE,"E14.bottom"),sQuery(id+"F15.wireOp",EDGE,"E14.top"),sQuery(id+"F15.wireOp",EDGE,"E14.left"),sQuery(id+"F15.wireOp",EDGE,"E14.right"),sQuery(id+"F15.wireOp",EDGE,"E15.MirrorCS"),sQuery(id+"F15.wireOp",EDGE,"E16.MirrorCS"),sQuery(id+"F15.wireOp",EDGE,"E17.MirrorCS"),sQuery(id+"F15.wireOp",EDGE,"E18.MirrorCS"),sQuery(id+"F15.wireOp",EDGE,"E19.MirrorCS"),sQuery(id+"F15.wireOp",EDGE,"E20.MirrorCS"),sQuery(id+"F15.wireOp",EDGE,"E21.MirrorCS"),sQuery(id+"F15.wireOp",EDGE,"E22.MirrorCS"),sQuery(id+"F15.wireOp",EDGE,"E23.MirrorCS"),sQuery(id+"F15.wireOp",EDGE,"E24.MirrorCS"),sQuery(id+"F15.wireOp",EDGE,"E25.MirrorCS"),sQuery(id+"F15.wireOp",EDGE,"E26.MirrorCS")])]}),"instanceName":"1"}),"instanceName":"1"}),"instanceName":"1"}),"instanceName":"1"});
            var Q43;
            Q43=makeQuery(id+"F22.opPattern","COPY",BODY,{"derivedFrom":makeQuery(id+"F20.opPattern","COPY",BODY,{"derivedFrom":makeQuery(id+"F19.opPattern","COPY",BODY,{"derivedFrom":makeQuery(id+"F16.opExtrude","SWEPT_BODY",BODY,{"disambiguationData":[OSD([sQuery(id+"F15.wireOp",EDGE,"E13.bottom"),sQuery(id+"F15.wireOp",EDGE,"E13.top"),sQuery(id+"F15.wireOp",EDGE,"E13.left"),sQuery(id+"F15.wireOp",EDGE,"E13.right"),sQuery(id+"F15.wireOp",EDGE,"E14.bottom"),sQuery(id+"F15.wireOp",EDGE,"E14.top"),sQuery(id+"F15.wireOp",EDGE,"E14.left"),sQuery(id+"F15.wireOp",EDGE,"E14.right"),sQuery(id+"F15.wireOp",EDGE,"E15.MirrorCS"),sQuery(id+"F15.wireOp",EDGE,"E16.MirrorCS"),sQuery(id+"F15.wireOp",EDGE,"E17.MirrorCS"),sQuery(id+"F15.wireOp",EDGE,"E18.MirrorCS"),sQuery(id+"F15.wireOp",EDGE,"E19.MirrorCS"),sQuery(id+"F15.wireOp",EDGE,"E20.MirrorCS"),sQuery(id+"F15.wireOp",EDGE,"E21.MirrorCS"),sQuery(id+"F15.wireOp",EDGE,"E22.MirrorCS"),sQuery(id+"F15.wireOp",EDGE,"E23.MirrorCS"),sQuery(id+"F15.wireOp",EDGE,"E24.MirrorCS"),sQuery(id+"F15.wireOp",EDGE,"E25.MirrorCS"),sQuery(id+"F15.wireOp",EDGE,"E26.MirrorCS")])]}),"instanceName":"1"}),"instanceName":"1"}),"instanceName":"1"});
            var Q44;
            Q44=makeQuery(id+"F22.opPattern","COPY",BODY,{"derivedFrom":makeQuery(id+"F20.opPattern","COPY",BODY,{"derivedFrom":makeQuery(id+"F19.opPattern","COPY",BODY,{"derivedFrom":makeQuery(id+"F17.opPattern","COPY",BODY,{"derivedFrom":makeQuery(id+"F16.opExtrude","SWEPT_BODY",BODY,{"disambiguationData":[OSD([sQuery(id+"F15.wireOp",EDGE,"E13.bottom"),sQuery(id+"F15.wireOp",EDGE,"E13.top"),sQuery(id+"F15.wireOp",EDGE,"E13.left"),sQuery(id+"F15.wireOp",EDGE,"E13.right"),sQuery(id+"F15.wireOp",EDGE,"E14.bottom"),sQuery(id+"F15.wireOp",EDGE,"E14.top"),sQuery(id+"F15.wireOp",EDGE,"E14.left"),sQuery(id+"F15.wireOp",EDGE,"E14.right"),sQuery(id+"F15.wireOp",EDGE,"E15.MirrorCS"),sQuery(id+"F15.wireOp",EDGE,"E16.MirrorCS"),sQuery(id+"F15.wireOp",EDGE,"E17.MirrorCS"),sQuery(id+"F15.wireOp",EDGE,"E18.MirrorCS"),sQuery(id+"F15.wireOp",EDGE,"E19.MirrorCS"),sQuery(id+"F15.wireOp",EDGE,"E20.MirrorCS"),sQuery(id+"F15.wireOp",EDGE,"E21.MirrorCS"),sQuery(id+"F15.wireOp",EDGE,"E22.MirrorCS"),sQuery(id+"F15.wireOp",EDGE,"E23.MirrorCS"),sQuery(id+"F15.wireOp",EDGE,"E24.MirrorCS"),sQuery(id+"F15.wireOp",EDGE,"E25.MirrorCS"),sQuery(id+"F15.wireOp",EDGE,"E26.MirrorCS")])]}),"instanceName":"1"}),"instanceName":"1"}),"instanceName":"1"}),"instanceName":"1"});
            var Q45;
            Q45=makeQuery(id+"F22.opPattern","COPY",BODY,{"derivedFrom":makeQuery(id+"F20.opPattern","COPY",BODY,{"derivedFrom":makeQuery(id+"F19.opPattern","COPY",BODY,{"derivedFrom":makeQuery(id+"F18.opPattern","COPY",BODY,{"derivedFrom":makeQuery(id+"F16.opExtrude","SWEPT_BODY",BODY,{"disambiguationData":[OSD([sQuery(id+"F15.wireOp",EDGE,"E13.bottom"),sQuery(id+"F15.wireOp",EDGE,"E13.top"),sQuery(id+"F15.wireOp",EDGE,"E13.left"),sQuery(id+"F15.wireOp",EDGE,"E13.right"),sQuery(id+"F15.wireOp",EDGE,"E14.bottom"),sQuery(id+"F15.wireOp",EDGE,"E14.top"),sQuery(id+"F15.wireOp",EDGE,"E14.left"),sQuery(id+"F15.wireOp",EDGE,"E14.right"),sQuery(id+"F15.wireOp",EDGE,"E15.MirrorCS"),sQuery(id+"F15.wireOp",EDGE,"E16.MirrorCS"),sQuery(id+"F15.wireOp",EDGE,"E17.MirrorCS"),sQuery(id+"F15.wireOp",EDGE,"E18.MirrorCS"),sQuery(id+"F15.wireOp",EDGE,"E19.MirrorCS"),sQuery(id+"F15.wireOp",EDGE,"E20.MirrorCS"),sQuery(id+"F15.wireOp",EDGE,"E21.MirrorCS"),sQuery(id+"F15.wireOp",EDGE,"E22.MirrorCS"),sQuery(id+"F15.wireOp",EDGE,"E23.MirrorCS"),sQuery(id+"F15.wireOp",EDGE,"E24.MirrorCS"),sQuery(id+"F15.wireOp",EDGE,"E25.MirrorCS"),sQuery(id+"F15.wireOp",EDGE,"E26.MirrorCS")])]}),"instanceName":"1"}),"instanceName":"1"}),"instanceName":"1"}),"instanceName":"1"});
            var Q46;
            Q46=makeQuery(id+"F22.opPattern","COPY",BODY,{"derivedFrom":makeQuery(id+"F20.opPattern","COPY",BODY,{"derivedFrom":makeQuery(id+"F19.opPattern","COPY",BODY,{"derivedFrom":makeQuery(id+"F18.opPattern","COPY",BODY,{"derivedFrom":makeQuery(id+"F17.opPattern","COPY",BODY,{"derivedFrom":makeQuery(id+"F16.opExtrude","SWEPT_BODY",BODY,{"disambiguationData":[OSD([sQuery(id+"F15.wireOp",EDGE,"E13.bottom"),sQuery(id+"F15.wireOp",EDGE,"E13.top"),sQuery(id+"F15.wireOp",EDGE,"E13.left"),sQuery(id+"F15.wireOp",EDGE,"E13.right"),sQuery(id+"F15.wireOp",EDGE,"E14.bottom"),sQuery(id+"F15.wireOp",EDGE,"E14.top"),sQuery(id+"F15.wireOp",EDGE,"E14.left"),sQuery(id+"F15.wireOp",EDGE,"E14.right"),sQuery(id+"F15.wireOp",EDGE,"E15.MirrorCS"),sQuery(id+"F15.wireOp",EDGE,"E16.MirrorCS"),sQuery(id+"F15.wireOp",EDGE,"E17.MirrorCS"),sQuery(id+"F15.wireOp",EDGE,"E18.MirrorCS"),sQuery(id+"F15.wireOp",EDGE,"E19.MirrorCS"),sQuery(id+"F15.wireOp",EDGE,"E20.MirrorCS"),sQuery(id+"F15.wireOp",EDGE,"E21.MirrorCS"),sQuery(id+"F15.wireOp",EDGE,"E22.MirrorCS"),sQuery(id+"F15.wireOp",EDGE,"E23.MirrorCS"),sQuery(id+"F15.wireOp",EDGE,"E24.MirrorCS"),sQuery(id+"F15.wireOp",EDGE,"E25.MirrorCS"),sQuery(id+"F15.wireOp",EDGE,"E26.MirrorCS")])]}),"instanceName":"1"}),"instanceName":"1"}),"instanceName":"1"}),"instanceName":"1"}),"instanceName":"1"});
            var Q47;
            Q47=makeQuery(id+"F22.opPattern","COPY",BODY,{"derivedFrom":makeQuery(id+"F21.opPattern","COPY",BODY,{"derivedFrom":makeQuery(id+"F16.opExtrude","SWEPT_BODY",BODY,{"disambiguationData":[OSD([sQuery(id+"F15.wireOp",EDGE,"E13.bottom"),sQuery(id+"F15.wireOp",EDGE,"E13.top"),sQuery(id+"F15.wireOp",EDGE,"E13.left"),sQuery(id+"F15.wireOp",EDGE,"E13.right"),sQuery(id+"F15.wireOp",EDGE,"E14.bottom"),sQuery(id+"F15.wireOp",EDGE,"E14.top"),sQuery(id+"F15.wireOp",EDGE,"E14.left"),sQuery(id+"F15.wireOp",EDGE,"E14.right"),sQuery(id+"F15.wireOp",EDGE,"E15.MirrorCS"),sQuery(id+"F15.wireOp",EDGE,"E16.MirrorCS"),sQuery(id+"F15.wireOp",EDGE,"E17.MirrorCS"),sQuery(id+"F15.wireOp",EDGE,"E18.MirrorCS"),sQuery(id+"F15.wireOp",EDGE,"E19.MirrorCS"),sQuery(id+"F15.wireOp",EDGE,"E20.MirrorCS"),sQuery(id+"F15.wireOp",EDGE,"E21.MirrorCS"),sQuery(id+"F15.wireOp",EDGE,"E22.MirrorCS"),sQuery(id+"F15.wireOp",EDGE,"E23.MirrorCS"),sQuery(id+"F15.wireOp",EDGE,"E24.MirrorCS"),sQuery(id+"F15.wireOp",EDGE,"E25.MirrorCS"),sQuery(id+"F15.wireOp",EDGE,"E26.MirrorCS")])]}),"instanceName":"1"}),"instanceName":"1"});
            var Q48;
            Q48=makeQuery(id+"F22.opPattern","COPY",BODY,{"derivedFrom":makeQuery(id+"F21.opPattern","COPY",BODY,{"derivedFrom":makeQuery(id+"F17.opPattern","COPY",BODY,{"derivedFrom":makeQuery(id+"F16.opExtrude","SWEPT_BODY",BODY,{"disambiguationData":[OSD([sQuery(id+"F15.wireOp",EDGE,"E13.bottom"),sQuery(id+"F15.wireOp",EDGE,"E13.top"),sQuery(id+"F15.wireOp",EDGE,"E13.left"),sQuery(id+"F15.wireOp",EDGE,"E13.right"),sQuery(id+"F15.wireOp",EDGE,"E14.bottom"),sQuery(id+"F15.wireOp",EDGE,"E14.top"),sQuery(id+"F15.wireOp",EDGE,"E14.left"),sQuery(id+"F15.wireOp",EDGE,"E14.right"),sQuery(id+"F15.wireOp",EDGE,"E15.MirrorCS"),sQuery(id+"F15.wireOp",EDGE,"E16.MirrorCS"),sQuery(id+"F15.wireOp",EDGE,"E17.MirrorCS"),sQuery(id+"F15.wireOp",EDGE,"E18.MirrorCS"),sQuery(id+"F15.wireOp",EDGE,"E19.MirrorCS"),sQuery(id+"F15.wireOp",EDGE,"E20.MirrorCS"),sQuery(id+"F15.wireOp",EDGE,"E21.MirrorCS"),sQuery(id+"F15.wireOp",EDGE,"E22.MirrorCS"),sQuery(id+"F15.wireOp",EDGE,"E23.MirrorCS"),sQuery(id+"F15.wireOp",EDGE,"E24.MirrorCS"),sQuery(id+"F15.wireOp",EDGE,"E25.MirrorCS"),sQuery(id+"F15.wireOp",EDGE,"E26.MirrorCS")])]}),"instanceName":"1"}),"instanceName":"1"}),"instanceName":"1"});
            var Q49;
            Q49=makeQuery(id+"F22.opPattern","COPY",BODY,{"derivedFrom":makeQuery(id+"F21.opPattern","COPY",BODY,{"derivedFrom":makeQuery(id+"F18.opPattern","COPY",BODY,{"derivedFrom":makeQuery(id+"F16.opExtrude","SWEPT_BODY",BODY,{"disambiguationData":[OSD([sQuery(id+"F15.wireOp",EDGE,"E13.bottom"),sQuery(id+"F15.wireOp",EDGE,"E13.top"),sQuery(id+"F15.wireOp",EDGE,"E13.left"),sQuery(id+"F15.wireOp",EDGE,"E13.right"),sQuery(id+"F15.wireOp",EDGE,"E14.bottom"),sQuery(id+"F15.wireOp",EDGE,"E14.top"),sQuery(id+"F15.wireOp",EDGE,"E14.left"),sQuery(id+"F15.wireOp",EDGE,"E14.right"),sQuery(id+"F15.wireOp",EDGE,"E15.MirrorCS"),sQuery(id+"F15.wireOp",EDGE,"E16.MirrorCS"),sQuery(id+"F15.wireOp",EDGE,"E17.MirrorCS"),sQuery(id+"F15.wireOp",EDGE,"E18.MirrorCS"),sQuery(id+"F15.wireOp",EDGE,"E19.MirrorCS"),sQuery(id+"F15.wireOp",EDGE,"E20.MirrorCS"),sQuery(id+"F15.wireOp",EDGE,"E21.MirrorCS"),sQuery(id+"F15.wireOp",EDGE,"E22.MirrorCS"),sQuery(id+"F15.wireOp",EDGE,"E23.MirrorCS"),sQuery(id+"F15.wireOp",EDGE,"E24.MirrorCS"),sQuery(id+"F15.wireOp",EDGE,"E25.MirrorCS"),sQuery(id+"F15.wireOp",EDGE,"E26.MirrorCS")])]}),"instanceName":"1"}),"instanceName":"1"}),"instanceName":"1"});
            var Q50;
            Q50=makeQuery(id+"F22.opPattern","COPY",BODY,{"derivedFrom":makeQuery(id+"F21.opPattern","COPY",BODY,{"derivedFrom":makeQuery(id+"F18.opPattern","COPY",BODY,{"derivedFrom":makeQuery(id+"F17.opPattern","COPY",BODY,{"derivedFrom":makeQuery(id+"F16.opExtrude","SWEPT_BODY",BODY,{"disambiguationData":[OSD([sQuery(id+"F15.wireOp",EDGE,"E13.bottom"),sQuery(id+"F15.wireOp",EDGE,"E13.top"),sQuery(id+"F15.wireOp",EDGE,"E13.left"),sQuery(id+"F15.wireOp",EDGE,"E13.right"),sQuery(id+"F15.wireOp",EDGE,"E14.bottom"),sQuery(id+"F15.wireOp",EDGE,"E14.top"),sQuery(id+"F15.wireOp",EDGE,"E14.left"),sQuery(id+"F15.wireOp",EDGE,"E14.right"),sQuery(id+"F15.wireOp",EDGE,"E15.MirrorCS"),sQuery(id+"F15.wireOp",EDGE,"E16.MirrorCS"),sQuery(id+"F15.wireOp",EDGE,"E17.MirrorCS"),sQuery(id+"F15.wireOp",EDGE,"E18.MirrorCS"),sQuery(id+"F15.wireOp",EDGE,"E19.MirrorCS"),sQuery(id+"F15.wireOp",EDGE,"E20.MirrorCS"),sQuery(id+"F15.wireOp",EDGE,"E21.MirrorCS"),sQuery(id+"F15.wireOp",EDGE,"E22.MirrorCS"),sQuery(id+"F15.wireOp",EDGE,"E23.MirrorCS"),sQuery(id+"F15.wireOp",EDGE,"E24.MirrorCS"),sQuery(id+"F15.wireOp",EDGE,"E25.MirrorCS"),sQuery(id+"F15.wireOp",EDGE,"E26.MirrorCS")])]}),"instanceName":"1"}),"instanceName":"1"}),"instanceName":"1"}),"instanceName":"1"});
            var Q51;
            Q51=makeQuery(id+"F22.opPattern","COPY",BODY,{"derivedFrom":makeQuery(id+"F21.opPattern","COPY",BODY,{"derivedFrom":makeQuery(id+"F19.opPattern","COPY",BODY,{"derivedFrom":makeQuery(id+"F16.opExtrude","SWEPT_BODY",BODY,{"disambiguationData":[OSD([sQuery(id+"F15.wireOp",EDGE,"E13.bottom"),sQuery(id+"F15.wireOp",EDGE,"E13.top"),sQuery(id+"F15.wireOp",EDGE,"E13.left"),sQuery(id+"F15.wireOp",EDGE,"E13.right"),sQuery(id+"F15.wireOp",EDGE,"E14.bottom"),sQuery(id+"F15.wireOp",EDGE,"E14.top"),sQuery(id+"F15.wireOp",EDGE,"E14.left"),sQuery(id+"F15.wireOp",EDGE,"E14.right"),sQuery(id+"F15.wireOp",EDGE,"E15.MirrorCS"),sQuery(id+"F15.wireOp",EDGE,"E16.MirrorCS"),sQuery(id+"F15.wireOp",EDGE,"E17.MirrorCS"),sQuery(id+"F15.wireOp",EDGE,"E18.MirrorCS"),sQuery(id+"F15.wireOp",EDGE,"E19.MirrorCS"),sQuery(id+"F15.wireOp",EDGE,"E20.MirrorCS"),sQuery(id+"F15.wireOp",EDGE,"E21.MirrorCS"),sQuery(id+"F15.wireOp",EDGE,"E22.MirrorCS"),sQuery(id+"F15.wireOp",EDGE,"E23.MirrorCS"),sQuery(id+"F15.wireOp",EDGE,"E24.MirrorCS"),sQuery(id+"F15.wireOp",EDGE,"E25.MirrorCS"),sQuery(id+"F15.wireOp",EDGE,"E26.MirrorCS")])]}),"instanceName":"1"}),"instanceName":"1"}),"instanceName":"1"});
            var Q52;
            Q52=makeQuery(id+"F22.opPattern","COPY",BODY,{"derivedFrom":makeQuery(id+"F21.opPattern","COPY",BODY,{"derivedFrom":makeQuery(id+"F19.opPattern","COPY",BODY,{"derivedFrom":makeQuery(id+"F17.opPattern","COPY",BODY,{"derivedFrom":makeQuery(id+"F16.opExtrude","SWEPT_BODY",BODY,{"disambiguationData":[OSD([sQuery(id+"F15.wireOp",EDGE,"E13.bottom"),sQuery(id+"F15.wireOp",EDGE,"E13.top"),sQuery(id+"F15.wireOp",EDGE,"E13.left"),sQuery(id+"F15.wireOp",EDGE,"E13.right"),sQuery(id+"F15.wireOp",EDGE,"E14.bottom"),sQuery(id+"F15.wireOp",EDGE,"E14.top"),sQuery(id+"F15.wireOp",EDGE,"E14.left"),sQuery(id+"F15.wireOp",EDGE,"E14.right"),sQuery(id+"F15.wireOp",EDGE,"E15.MirrorCS"),sQuery(id+"F15.wireOp",EDGE,"E16.MirrorCS"),sQuery(id+"F15.wireOp",EDGE,"E17.MirrorCS"),sQuery(id+"F15.wireOp",EDGE,"E18.MirrorCS"),sQuery(id+"F15.wireOp",EDGE,"E19.MirrorCS"),sQuery(id+"F15.wireOp",EDGE,"E20.MirrorCS"),sQuery(id+"F15.wireOp",EDGE,"E21.MirrorCS"),sQuery(id+"F15.wireOp",EDGE,"E22.MirrorCS"),sQuery(id+"F15.wireOp",EDGE,"E23.MirrorCS"),sQuery(id+"F15.wireOp",EDGE,"E24.MirrorCS"),sQuery(id+"F15.wireOp",EDGE,"E25.MirrorCS"),sQuery(id+"F15.wireOp",EDGE,"E26.MirrorCS")])]}),"instanceName":"1"}),"instanceName":"1"}),"instanceName":"1"}),"instanceName":"1"});
            var Q53;
            Q53=makeQuery(id+"F22.opPattern","COPY",BODY,{"derivedFrom":makeQuery(id+"F21.opPattern","COPY",BODY,{"derivedFrom":makeQuery(id+"F19.opPattern","COPY",BODY,{"derivedFrom":makeQuery(id+"F18.opPattern","COPY",BODY,{"derivedFrom":makeQuery(id+"F16.opExtrude","SWEPT_BODY",BODY,{"disambiguationData":[OSD([sQuery(id+"F15.wireOp",EDGE,"E13.bottom"),sQuery(id+"F15.wireOp",EDGE,"E13.top"),sQuery(id+"F15.wireOp",EDGE,"E13.left"),sQuery(id+"F15.wireOp",EDGE,"E13.right"),sQuery(id+"F15.wireOp",EDGE,"E14.bottom"),sQuery(id+"F15.wireOp",EDGE,"E14.top"),sQuery(id+"F15.wireOp",EDGE,"E14.left"),sQuery(id+"F15.wireOp",EDGE,"E14.right"),sQuery(id+"F15.wireOp",EDGE,"E15.MirrorCS"),sQuery(id+"F15.wireOp",EDGE,"E16.MirrorCS"),sQuery(id+"F15.wireOp",EDGE,"E17.MirrorCS"),sQuery(id+"F15.wireOp",EDGE,"E18.MirrorCS"),sQuery(id+"F15.wireOp",EDGE,"E19.MirrorCS"),sQuery(id+"F15.wireOp",EDGE,"E20.MirrorCS"),sQuery(id+"F15.wireOp",EDGE,"E21.MirrorCS"),sQuery(id+"F15.wireOp",EDGE,"E22.MirrorCS"),sQuery(id+"F15.wireOp",EDGE,"E23.MirrorCS"),sQuery(id+"F15.wireOp",EDGE,"E24.MirrorCS"),sQuery(id+"F15.wireOp",EDGE,"E25.MirrorCS"),sQuery(id+"F15.wireOp",EDGE,"E26.MirrorCS")])]}),"instanceName":"1"}),"instanceName":"1"}),"instanceName":"1"}),"instanceName":"1"});
            var Q54;
            Q54=makeQuery(id+"F22.opPattern","COPY",BODY,{"derivedFrom":makeQuery(id+"F21.opPattern","COPY",BODY,{"derivedFrom":makeQuery(id+"F19.opPattern","COPY",BODY,{"derivedFrom":makeQuery(id+"F18.opPattern","COPY",BODY,{"derivedFrom":makeQuery(id+"F17.opPattern","COPY",BODY,{"derivedFrom":makeQuery(id+"F16.opExtrude","SWEPT_BODY",BODY,{"disambiguationData":[OSD([sQuery(id+"F15.wireOp",EDGE,"E13.bottom"),sQuery(id+"F15.wireOp",EDGE,"E13.top"),sQuery(id+"F15.wireOp",EDGE,"E13.left"),sQuery(id+"F15.wireOp",EDGE,"E13.right"),sQuery(id+"F15.wireOp",EDGE,"E14.bottom"),sQuery(id+"F15.wireOp",EDGE,"E14.top"),sQuery(id+"F15.wireOp",EDGE,"E14.left"),sQuery(id+"F15.wireOp",EDGE,"E14.right"),sQuery(id+"F15.wireOp",EDGE,"E15.MirrorCS"),sQuery(id+"F15.wireOp",EDGE,"E16.MirrorCS"),sQuery(id+"F15.wireOp",EDGE,"E17.MirrorCS"),sQuery(id+"F15.wireOp",EDGE,"E18.MirrorCS"),sQuery(id+"F15.wireOp",EDGE,"E19.MirrorCS"),sQuery(id+"F15.wireOp",EDGE,"E20.MirrorCS"),sQuery(id+"F15.wireOp",EDGE,"E21.MirrorCS"),sQuery(id+"F15.wireOp",EDGE,"E22.MirrorCS"),sQuery(id+"F15.wireOp",EDGE,"E23.MirrorCS"),sQuery(id+"F15.wireOp",EDGE,"E24.MirrorCS"),sQuery(id+"F15.wireOp",EDGE,"E25.MirrorCS"),sQuery(id+"F15.wireOp",EDGE,"E26.MirrorCS")])]}),"instanceName":"1"}),"instanceName":"1"}),"instanceName":"1"}),"instanceName":"1"}),"instanceName":"1"});
            var Q55;
            Q55=makeQuery(id+"F22.opPattern","COPY",BODY,{"derivedFrom":makeQuery(id+"F21.opPattern","COPY",BODY,{"derivedFrom":makeQuery(id+"F20.opPattern","COPY",BODY,{"derivedFrom":makeQuery(id+"F16.opExtrude","SWEPT_BODY",BODY,{"disambiguationData":[OSD([sQuery(id+"F15.wireOp",EDGE,"E13.bottom"),sQuery(id+"F15.wireOp",EDGE,"E13.top"),sQuery(id+"F15.wireOp",EDGE,"E13.left"),sQuery(id+"F15.wireOp",EDGE,"E13.right"),sQuery(id+"F15.wireOp",EDGE,"E14.bottom"),sQuery(id+"F15.wireOp",EDGE,"E14.top"),sQuery(id+"F15.wireOp",EDGE,"E14.left"),sQuery(id+"F15.wireOp",EDGE,"E14.right"),sQuery(id+"F15.wireOp",EDGE,"E15.MirrorCS"),sQuery(id+"F15.wireOp",EDGE,"E16.MirrorCS"),sQuery(id+"F15.wireOp",EDGE,"E17.MirrorCS"),sQuery(id+"F15.wireOp",EDGE,"E18.MirrorCS"),sQuery(id+"F15.wireOp",EDGE,"E19.MirrorCS"),sQuery(id+"F15.wireOp",EDGE,"E20.MirrorCS"),sQuery(id+"F15.wireOp",EDGE,"E21.MirrorCS"),sQuery(id+"F15.wireOp",EDGE,"E22.MirrorCS"),sQuery(id+"F15.wireOp",EDGE,"E23.MirrorCS"),sQuery(id+"F15.wireOp",EDGE,"E24.MirrorCS"),sQuery(id+"F15.wireOp",EDGE,"E25.MirrorCS"),sQuery(id+"F15.wireOp",EDGE,"E26.MirrorCS")])]}),"instanceName":"1"}),"instanceName":"1"}),"instanceName":"1"});
            var Q56;
            Q56=makeQuery(id+"F22.opPattern","COPY",BODY,{"derivedFrom":makeQuery(id+"F21.opPattern","COPY",BODY,{"derivedFrom":makeQuery(id+"F20.opPattern","COPY",BODY,{"derivedFrom":makeQuery(id+"F17.opPattern","COPY",BODY,{"derivedFrom":makeQuery(id+"F16.opExtrude","SWEPT_BODY",BODY,{"disambiguationData":[OSD([sQuery(id+"F15.wireOp",EDGE,"E13.bottom"),sQuery(id+"F15.wireOp",EDGE,"E13.top"),sQuery(id+"F15.wireOp",EDGE,"E13.left"),sQuery(id+"F15.wireOp",EDGE,"E13.right"),sQuery(id+"F15.wireOp",EDGE,"E14.bottom"),sQuery(id+"F15.wireOp",EDGE,"E14.top"),sQuery(id+"F15.wireOp",EDGE,"E14.left"),sQuery(id+"F15.wireOp",EDGE,"E14.right"),sQuery(id+"F15.wireOp",EDGE,"E15.MirrorCS"),sQuery(id+"F15.wireOp",EDGE,"E16.MirrorCS"),sQuery(id+"F15.wireOp",EDGE,"E17.MirrorCS"),sQuery(id+"F15.wireOp",EDGE,"E18.MirrorCS"),sQuery(id+"F15.wireOp",EDGE,"E19.MirrorCS"),sQuery(id+"F15.wireOp",EDGE,"E20.MirrorCS"),sQuery(id+"F15.wireOp",EDGE,"E21.MirrorCS"),sQuery(id+"F15.wireOp",EDGE,"E22.MirrorCS"),sQuery(id+"F15.wireOp",EDGE,"E23.MirrorCS"),sQuery(id+"F15.wireOp",EDGE,"E24.MirrorCS"),sQuery(id+"F15.wireOp",EDGE,"E25.MirrorCS"),sQuery(id+"F15.wireOp",EDGE,"E26.MirrorCS")])]}),"instanceName":"1"}),"instanceName":"1"}),"instanceName":"1"}),"instanceName":"1"});
            var Q57;
            Q57=makeQuery(id+"F22.opPattern","COPY",BODY,{"derivedFrom":makeQuery(id+"F21.opPattern","COPY",BODY,{"derivedFrom":makeQuery(id+"F20.opPattern","COPY",BODY,{"derivedFrom":makeQuery(id+"F18.opPattern","COPY",BODY,{"derivedFrom":makeQuery(id+"F16.opExtrude","SWEPT_BODY",BODY,{"disambiguationData":[OSD([sQuery(id+"F15.wireOp",EDGE,"E13.bottom"),sQuery(id+"F15.wireOp",EDGE,"E13.top"),sQuery(id+"F15.wireOp",EDGE,"E13.left"),sQuery(id+"F15.wireOp",EDGE,"E13.right"),sQuery(id+"F15.wireOp",EDGE,"E14.bottom"),sQuery(id+"F15.wireOp",EDGE,"E14.top"),sQuery(id+"F15.wireOp",EDGE,"E14.left"),sQuery(id+"F15.wireOp",EDGE,"E14.right"),sQuery(id+"F15.wireOp",EDGE,"E15.MirrorCS"),sQuery(id+"F15.wireOp",EDGE,"E16.MirrorCS"),sQuery(id+"F15.wireOp",EDGE,"E17.MirrorCS"),sQuery(id+"F15.wireOp",EDGE,"E18.MirrorCS"),sQuery(id+"F15.wireOp",EDGE,"E19.MirrorCS"),sQuery(id+"F15.wireOp",EDGE,"E20.MirrorCS"),sQuery(id+"F15.wireOp",EDGE,"E21.MirrorCS"),sQuery(id+"F15.wireOp",EDGE,"E22.MirrorCS"),sQuery(id+"F15.wireOp",EDGE,"E23.MirrorCS"),sQuery(id+"F15.wireOp",EDGE,"E24.MirrorCS"),sQuery(id+"F15.wireOp",EDGE,"E25.MirrorCS"),sQuery(id+"F15.wireOp",EDGE,"E26.MirrorCS")])]}),"instanceName":"1"}),"instanceName":"1"}),"instanceName":"1"}),"instanceName":"1"});
            var Q58;
            Q58=makeQuery(id+"F22.opPattern","COPY",BODY,{"derivedFrom":makeQuery(id+"F21.opPattern","COPY",BODY,{"derivedFrom":makeQuery(id+"F20.opPattern","COPY",BODY,{"derivedFrom":makeQuery(id+"F18.opPattern","COPY",BODY,{"derivedFrom":makeQuery(id+"F17.opPattern","COPY",BODY,{"derivedFrom":makeQuery(id+"F16.opExtrude","SWEPT_BODY",BODY,{"disambiguationData":[OSD([sQuery(id+"F15.wireOp",EDGE,"E13.bottom"),sQuery(id+"F15.wireOp",EDGE,"E13.top"),sQuery(id+"F15.wireOp",EDGE,"E13.left"),sQuery(id+"F15.wireOp",EDGE,"E13.right"),sQuery(id+"F15.wireOp",EDGE,"E14.bottom"),sQuery(id+"F15.wireOp",EDGE,"E14.top"),sQuery(id+"F15.wireOp",EDGE,"E14.left"),sQuery(id+"F15.wireOp",EDGE,"E14.right"),sQuery(id+"F15.wireOp",EDGE,"E15.MirrorCS"),sQuery(id+"F15.wireOp",EDGE,"E16.MirrorCS"),sQuery(id+"F15.wireOp",EDGE,"E17.MirrorCS"),sQuery(id+"F15.wireOp",EDGE,"E18.MirrorCS"),sQuery(id+"F15.wireOp",EDGE,"E19.MirrorCS"),sQuery(id+"F15.wireOp",EDGE,"E20.MirrorCS"),sQuery(id+"F15.wireOp",EDGE,"E21.MirrorCS"),sQuery(id+"F15.wireOp",EDGE,"E22.MirrorCS"),sQuery(id+"F15.wireOp",EDGE,"E23.MirrorCS"),sQuery(id+"F15.wireOp",EDGE,"E24.MirrorCS"),sQuery(id+"F15.wireOp",EDGE,"E25.MirrorCS"),sQuery(id+"F15.wireOp",EDGE,"E26.MirrorCS")])]}),"instanceName":"1"}),"instanceName":"1"}),"instanceName":"1"}),"instanceName":"1"}),"instanceName":"1"});
            var Q59;
            Q59=makeQuery(id+"F22.opPattern","COPY",BODY,{"derivedFrom":makeQuery(id+"F21.opPattern","COPY",BODY,{"derivedFrom":makeQuery(id+"F20.opPattern","COPY",BODY,{"derivedFrom":makeQuery(id+"F19.opPattern","COPY",BODY,{"derivedFrom":makeQuery(id+"F16.opExtrude","SWEPT_BODY",BODY,{"disambiguationData":[OSD([sQuery(id+"F15.wireOp",EDGE,"E13.bottom"),sQuery(id+"F15.wireOp",EDGE,"E13.top"),sQuery(id+"F15.wireOp",EDGE,"E13.left"),sQuery(id+"F15.wireOp",EDGE,"E13.right"),sQuery(id+"F15.wireOp",EDGE,"E14.bottom"),sQuery(id+"F15.wireOp",EDGE,"E14.top"),sQuery(id+"F15.wireOp",EDGE,"E14.left"),sQuery(id+"F15.wireOp",EDGE,"E14.right"),sQuery(id+"F15.wireOp",EDGE,"E15.MirrorCS"),sQuery(id+"F15.wireOp",EDGE,"E16.MirrorCS"),sQuery(id+"F15.wireOp",EDGE,"E17.MirrorCS"),sQuery(id+"F15.wireOp",EDGE,"E18.MirrorCS"),sQuery(id+"F15.wireOp",EDGE,"E19.MirrorCS"),sQuery(id+"F15.wireOp",EDGE,"E20.MirrorCS"),sQuery(id+"F15.wireOp",EDGE,"E21.MirrorCS"),sQuery(id+"F15.wireOp",EDGE,"E22.MirrorCS"),sQuery(id+"F15.wireOp",EDGE,"E23.MirrorCS"),sQuery(id+"F15.wireOp",EDGE,"E24.MirrorCS"),sQuery(id+"F15.wireOp",EDGE,"E25.MirrorCS"),sQuery(id+"F15.wireOp",EDGE,"E26.MirrorCS")])]}),"instanceName":"1"}),"instanceName":"1"}),"instanceName":"1"}),"instanceName":"1"});
            var Q60;
            Q60=makeQuery(id+"F22.opPattern","COPY",BODY,{"derivedFrom":makeQuery(id+"F21.opPattern","COPY",BODY,{"derivedFrom":makeQuery(id+"F20.opPattern","COPY",BODY,{"derivedFrom":makeQuery(id+"F19.opPattern","COPY",BODY,{"derivedFrom":makeQuery(id+"F17.opPattern","COPY",BODY,{"derivedFrom":makeQuery(id+"F16.opExtrude","SWEPT_BODY",BODY,{"disambiguationData":[OSD([sQuery(id+"F15.wireOp",EDGE,"E13.bottom"),sQuery(id+"F15.wireOp",EDGE,"E13.top"),sQuery(id+"F15.wireOp",EDGE,"E13.left"),sQuery(id+"F15.wireOp",EDGE,"E13.right"),sQuery(id+"F15.wireOp",EDGE,"E14.bottom"),sQuery(id+"F15.wireOp",EDGE,"E14.top"),sQuery(id+"F15.wireOp",EDGE,"E14.left"),sQuery(id+"F15.wireOp",EDGE,"E14.right"),sQuery(id+"F15.wireOp",EDGE,"E15.MirrorCS"),sQuery(id+"F15.wireOp",EDGE,"E16.MirrorCS"),sQuery(id+"F15.wireOp",EDGE,"E17.MirrorCS"),sQuery(id+"F15.wireOp",EDGE,"E18.MirrorCS"),sQuery(id+"F15.wireOp",EDGE,"E19.MirrorCS"),sQuery(id+"F15.wireOp",EDGE,"E20.MirrorCS"),sQuery(id+"F15.wireOp",EDGE,"E21.MirrorCS"),sQuery(id+"F15.wireOp",EDGE,"E22.MirrorCS"),sQuery(id+"F15.wireOp",EDGE,"E23.MirrorCS"),sQuery(id+"F15.wireOp",EDGE,"E24.MirrorCS"),sQuery(id+"F15.wireOp",EDGE,"E25.MirrorCS"),sQuery(id+"F15.wireOp",EDGE,"E26.MirrorCS")])]}),"instanceName":"1"}),"instanceName":"1"}),"instanceName":"1"}),"instanceName":"1"}),"instanceName":"1"});
            var Q61;
            Q61=makeQuery(id+"F22.opPattern","COPY",BODY,{"derivedFrom":makeQuery(id+"F21.opPattern","COPY",BODY,{"derivedFrom":makeQuery(id+"F20.opPattern","COPY",BODY,{"derivedFrom":makeQuery(id+"F19.opPattern","COPY",BODY,{"derivedFrom":makeQuery(id+"F18.opPattern","COPY",BODY,{"derivedFrom":makeQuery(id+"F16.opExtrude","SWEPT_BODY",BODY,{"disambiguationData":[OSD([sQuery(id+"F15.wireOp",EDGE,"E13.bottom"),sQuery(id+"F15.wireOp",EDGE,"E13.top"),sQuery(id+"F15.wireOp",EDGE,"E13.left"),sQuery(id+"F15.wireOp",EDGE,"E13.right"),sQuery(id+"F15.wireOp",EDGE,"E14.bottom"),sQuery(id+"F15.wireOp",EDGE,"E14.top"),sQuery(id+"F15.wireOp",EDGE,"E14.left"),sQuery(id+"F15.wireOp",EDGE,"E14.right"),sQuery(id+"F15.wireOp",EDGE,"E15.MirrorCS"),sQuery(id+"F15.wireOp",EDGE,"E16.MirrorCS"),sQuery(id+"F15.wireOp",EDGE,"E17.MirrorCS"),sQuery(id+"F15.wireOp",EDGE,"E18.MirrorCS"),sQuery(id+"F15.wireOp",EDGE,"E19.MirrorCS"),sQuery(id+"F15.wireOp",EDGE,"E20.MirrorCS"),sQuery(id+"F15.wireOp",EDGE,"E21.MirrorCS"),sQuery(id+"F15.wireOp",EDGE,"E22.MirrorCS"),sQuery(id+"F15.wireOp",EDGE,"E23.MirrorCS"),sQuery(id+"F15.wireOp",EDGE,"E24.MirrorCS"),sQuery(id+"F15.wireOp",EDGE,"E25.MirrorCS"),sQuery(id+"F15.wireOp",EDGE,"E26.MirrorCS")])]}),"instanceName":"1"}),"instanceName":"1"}),"instanceName":"1"}),"instanceName":"1"}),"instanceName":"1"});
            var Q62;
            Q62=makeQuery(id+"F23.opPattern","COPY",BODY,{"derivedFrom":makeQuery(id+"F16.opExtrude","SWEPT_BODY",BODY,{"disambiguationData":[OSD([sQuery(id+"F15.wireOp",EDGE,"E13.bottom"),sQuery(id+"F15.wireOp",EDGE,"E13.top"),sQuery(id+"F15.wireOp",EDGE,"E13.left"),sQuery(id+"F15.wireOp",EDGE,"E13.right"),sQuery(id+"F15.wireOp",EDGE,"E14.bottom"),sQuery(id+"F15.wireOp",EDGE,"E14.top"),sQuery(id+"F15.wireOp",EDGE,"E14.left"),sQuery(id+"F15.wireOp",EDGE,"E14.right"),sQuery(id+"F15.wireOp",EDGE,"E15.MirrorCS"),sQuery(id+"F15.wireOp",EDGE,"E16.MirrorCS"),sQuery(id+"F15.wireOp",EDGE,"E17.MirrorCS"),sQuery(id+"F15.wireOp",EDGE,"E18.MirrorCS"),sQuery(id+"F15.wireOp",EDGE,"E19.MirrorCS"),sQuery(id+"F15.wireOp",EDGE,"E20.MirrorCS"),sQuery(id+"F15.wireOp",EDGE,"E21.MirrorCS"),sQuery(id+"F15.wireOp",EDGE,"E22.MirrorCS"),sQuery(id+"F15.wireOp",EDGE,"E23.MirrorCS"),sQuery(id+"F15.wireOp",EDGE,"E24.MirrorCS"),sQuery(id+"F15.wireOp",EDGE,"E25.MirrorCS"),sQuery(id+"F15.wireOp",EDGE,"E26.MirrorCS")])]}),"instanceName":"1"});
            var Q63;
            Q63=makeQuery(id+"F23.opPattern","COPY",BODY,{"derivedFrom":makeQuery(id+"F17.opPattern","COPY",BODY,{"derivedFrom":makeQuery(id+"F16.opExtrude","SWEPT_BODY",BODY,{"disambiguationData":[OSD([sQuery(id+"F15.wireOp",EDGE,"E13.bottom"),sQuery(id+"F15.wireOp",EDGE,"E13.top"),sQuery(id+"F15.wireOp",EDGE,"E13.left"),sQuery(id+"F15.wireOp",EDGE,"E13.right"),sQuery(id+"F15.wireOp",EDGE,"E14.bottom"),sQuery(id+"F15.wireOp",EDGE,"E14.top"),sQuery(id+"F15.wireOp",EDGE,"E14.left"),sQuery(id+"F15.wireOp",EDGE,"E14.right"),sQuery(id+"F15.wireOp",EDGE,"E15.MirrorCS"),sQuery(id+"F15.wireOp",EDGE,"E16.MirrorCS"),sQuery(id+"F15.wireOp",EDGE,"E17.MirrorCS"),sQuery(id+"F15.wireOp",EDGE,"E18.MirrorCS"),sQuery(id+"F15.wireOp",EDGE,"E19.MirrorCS"),sQuery(id+"F15.wireOp",EDGE,"E20.MirrorCS"),sQuery(id+"F15.wireOp",EDGE,"E21.MirrorCS"),sQuery(id+"F15.wireOp",EDGE,"E22.MirrorCS"),sQuery(id+"F15.wireOp",EDGE,"E23.MirrorCS"),sQuery(id+"F15.wireOp",EDGE,"E24.MirrorCS"),sQuery(id+"F15.wireOp",EDGE,"E25.MirrorCS"),sQuery(id+"F15.wireOp",EDGE,"E26.MirrorCS")])]}),"instanceName":"1"}),"instanceName":"1"});
            var Q64;
            Q64=makeQuery(id+"F23.opPattern","COPY",BODY,{"derivedFrom":makeQuery(id+"F18.opPattern","COPY",BODY,{"derivedFrom":makeQuery(id+"F16.opExtrude","SWEPT_BODY",BODY,{"disambiguationData":[OSD([sQuery(id+"F15.wireOp",EDGE,"E13.bottom"),sQuery(id+"F15.wireOp",EDGE,"E13.top"),sQuery(id+"F15.wireOp",EDGE,"E13.left"),sQuery(id+"F15.wireOp",EDGE,"E13.right"),sQuery(id+"F15.wireOp",EDGE,"E14.bottom"),sQuery(id+"F15.wireOp",EDGE,"E14.top"),sQuery(id+"F15.wireOp",EDGE,"E14.left"),sQuery(id+"F15.wireOp",EDGE,"E14.right"),sQuery(id+"F15.wireOp",EDGE,"E15.MirrorCS"),sQuery(id+"F15.wireOp",EDGE,"E16.MirrorCS"),sQuery(id+"F15.wireOp",EDGE,"E17.MirrorCS"),sQuery(id+"F15.wireOp",EDGE,"E18.MirrorCS"),sQuery(id+"F15.wireOp",EDGE,"E19.MirrorCS"),sQuery(id+"F15.wireOp",EDGE,"E20.MirrorCS"),sQuery(id+"F15.wireOp",EDGE,"E21.MirrorCS"),sQuery(id+"F15.wireOp",EDGE,"E22.MirrorCS"),sQuery(id+"F15.wireOp",EDGE,"E23.MirrorCS"),sQuery(id+"F15.wireOp",EDGE,"E24.MirrorCS"),sQuery(id+"F15.wireOp",EDGE,"E25.MirrorCS"),sQuery(id+"F15.wireOp",EDGE,"E26.MirrorCS")])]}),"instanceName":"1"}),"instanceName":"1"});
            var Q65;
            Q65=makeQuery(id+"F23.opPattern","COPY",BODY,{"derivedFrom":makeQuery(id+"F18.opPattern","COPY",BODY,{"derivedFrom":makeQuery(id+"F17.opPattern","COPY",BODY,{"derivedFrom":makeQuery(id+"F16.opExtrude","SWEPT_BODY",BODY,{"disambiguationData":[OSD([sQuery(id+"F15.wireOp",EDGE,"E13.bottom"),sQuery(id+"F15.wireOp",EDGE,"E13.top"),sQuery(id+"F15.wireOp",EDGE,"E13.left"),sQuery(id+"F15.wireOp",EDGE,"E13.right"),sQuery(id+"F15.wireOp",EDGE,"E14.bottom"),sQuery(id+"F15.wireOp",EDGE,"E14.top"),sQuery(id+"F15.wireOp",EDGE,"E14.left"),sQuery(id+"F15.wireOp",EDGE,"E14.right"),sQuery(id+"F15.wireOp",EDGE,"E15.MirrorCS"),sQuery(id+"F15.wireOp",EDGE,"E16.MirrorCS"),sQuery(id+"F15.wireOp",EDGE,"E17.MirrorCS"),sQuery(id+"F15.wireOp",EDGE,"E18.MirrorCS"),sQuery(id+"F15.wireOp",EDGE,"E19.MirrorCS"),sQuery(id+"F15.wireOp",EDGE,"E20.MirrorCS"),sQuery(id+"F15.wireOp",EDGE,"E21.MirrorCS"),sQuery(id+"F15.wireOp",EDGE,"E22.MirrorCS"),sQuery(id+"F15.wireOp",EDGE,"E23.MirrorCS"),sQuery(id+"F15.wireOp",EDGE,"E24.MirrorCS"),sQuery(id+"F15.wireOp",EDGE,"E25.MirrorCS"),sQuery(id+"F15.wireOp",EDGE,"E26.MirrorCS")])]}),"instanceName":"1"}),"instanceName":"1"}),"instanceName":"1"});
            var Q66;
            Q66=makeQuery(id+"F23.opPattern","COPY",BODY,{"derivedFrom":makeQuery(id+"F19.opPattern","COPY",BODY,{"derivedFrom":makeQuery(id+"F16.opExtrude","SWEPT_BODY",BODY,{"disambiguationData":[OSD([sQuery(id+"F15.wireOp",EDGE,"E13.bottom"),sQuery(id+"F15.wireOp",EDGE,"E13.top"),sQuery(id+"F15.wireOp",EDGE,"E13.left"),sQuery(id+"F15.wireOp",EDGE,"E13.right"),sQuery(id+"F15.wireOp",EDGE,"E14.bottom"),sQuery(id+"F15.wireOp",EDGE,"E14.top"),sQuery(id+"F15.wireOp",EDGE,"E14.left"),sQuery(id+"F15.wireOp",EDGE,"E14.right"),sQuery(id+"F15.wireOp",EDGE,"E15.MirrorCS"),sQuery(id+"F15.wireOp",EDGE,"E16.MirrorCS"),sQuery(id+"F15.wireOp",EDGE,"E17.MirrorCS"),sQuery(id+"F15.wireOp",EDGE,"E18.MirrorCS"),sQuery(id+"F15.wireOp",EDGE,"E19.MirrorCS"),sQuery(id+"F15.wireOp",EDGE,"E20.MirrorCS"),sQuery(id+"F15.wireOp",EDGE,"E21.MirrorCS"),sQuery(id+"F15.wireOp",EDGE,"E22.MirrorCS"),sQuery(id+"F15.wireOp",EDGE,"E23.MirrorCS"),sQuery(id+"F15.wireOp",EDGE,"E24.MirrorCS"),sQuery(id+"F15.wireOp",EDGE,"E25.MirrorCS"),sQuery(id+"F15.wireOp",EDGE,"E26.MirrorCS")])]}),"instanceName":"1"}),"instanceName":"1"});
            var Q67;
            Q67=makeQuery(id+"F23.opPattern","COPY",BODY,{"derivedFrom":makeQuery(id+"F19.opPattern","COPY",BODY,{"derivedFrom":makeQuery(id+"F17.opPattern","COPY",BODY,{"derivedFrom":makeQuery(id+"F16.opExtrude","SWEPT_BODY",BODY,{"disambiguationData":[OSD([sQuery(id+"F15.wireOp",EDGE,"E13.bottom"),sQuery(id+"F15.wireOp",EDGE,"E13.top"),sQuery(id+"F15.wireOp",EDGE,"E13.left"),sQuery(id+"F15.wireOp",EDGE,"E13.right"),sQuery(id+"F15.wireOp",EDGE,"E14.bottom"),sQuery(id+"F15.wireOp",EDGE,"E14.top"),sQuery(id+"F15.wireOp",EDGE,"E14.left"),sQuery(id+"F15.wireOp",EDGE,"E14.right"),sQuery(id+"F15.wireOp",EDGE,"E15.MirrorCS"),sQuery(id+"F15.wireOp",EDGE,"E16.MirrorCS"),sQuery(id+"F15.wireOp",EDGE,"E17.MirrorCS"),sQuery(id+"F15.wireOp",EDGE,"E18.MirrorCS"),sQuery(id+"F15.wireOp",EDGE,"E19.MirrorCS"),sQuery(id+"F15.wireOp",EDGE,"E20.MirrorCS"),sQuery(id+"F15.wireOp",EDGE,"E21.MirrorCS"),sQuery(id+"F15.wireOp",EDGE,"E22.MirrorCS"),sQuery(id+"F15.wireOp",EDGE,"E23.MirrorCS"),sQuery(id+"F15.wireOp",EDGE,"E24.MirrorCS"),sQuery(id+"F15.wireOp",EDGE,"E25.MirrorCS"),sQuery(id+"F15.wireOp",EDGE,"E26.MirrorCS")])]}),"instanceName":"1"}),"instanceName":"1"}),"instanceName":"1"});
            var Q68;
            Q68=makeQuery(id+"F23.opPattern","COPY",BODY,{"derivedFrom":makeQuery(id+"F19.opPattern","COPY",BODY,{"derivedFrom":makeQuery(id+"F18.opPattern","COPY",BODY,{"derivedFrom":makeQuery(id+"F16.opExtrude","SWEPT_BODY",BODY,{"disambiguationData":[OSD([sQuery(id+"F15.wireOp",EDGE,"E13.bottom"),sQuery(id+"F15.wireOp",EDGE,"E13.top"),sQuery(id+"F15.wireOp",EDGE,"E13.left"),sQuery(id+"F15.wireOp",EDGE,"E13.right"),sQuery(id+"F15.wireOp",EDGE,"E14.bottom"),sQuery(id+"F15.wireOp",EDGE,"E14.top"),sQuery(id+"F15.wireOp",EDGE,"E14.left"),sQuery(id+"F15.wireOp",EDGE,"E14.right"),sQuery(id+"F15.wireOp",EDGE,"E15.MirrorCS"),sQuery(id+"F15.wireOp",EDGE,"E16.MirrorCS"),sQuery(id+"F15.wireOp",EDGE,"E17.MirrorCS"),sQuery(id+"F15.wireOp",EDGE,"E18.MirrorCS"),sQuery(id+"F15.wireOp",EDGE,"E19.MirrorCS"),sQuery(id+"F15.wireOp",EDGE,"E20.MirrorCS"),sQuery(id+"F15.wireOp",EDGE,"E21.MirrorCS"),sQuery(id+"F15.wireOp",EDGE,"E22.MirrorCS"),sQuery(id+"F15.wireOp",EDGE,"E23.MirrorCS"),sQuery(id+"F15.wireOp",EDGE,"E24.MirrorCS"),sQuery(id+"F15.wireOp",EDGE,"E25.MirrorCS"),sQuery(id+"F15.wireOp",EDGE,"E26.MirrorCS")])]}),"instanceName":"1"}),"instanceName":"1"}),"instanceName":"1"});
            var Q69;
            Q69=makeQuery(id+"F23.opPattern","COPY",BODY,{"derivedFrom":makeQuery(id+"F19.opPattern","COPY",BODY,{"derivedFrom":makeQuery(id+"F18.opPattern","COPY",BODY,{"derivedFrom":makeQuery(id+"F17.opPattern","COPY",BODY,{"derivedFrom":makeQuery(id+"F16.opExtrude","SWEPT_BODY",BODY,{"disambiguationData":[OSD([sQuery(id+"F15.wireOp",EDGE,"E13.bottom"),sQuery(id+"F15.wireOp",EDGE,"E13.top"),sQuery(id+"F15.wireOp",EDGE,"E13.left"),sQuery(id+"F15.wireOp",EDGE,"E13.right"),sQuery(id+"F15.wireOp",EDGE,"E14.bottom"),sQuery(id+"F15.wireOp",EDGE,"E14.top"),sQuery(id+"F15.wireOp",EDGE,"E14.left"),sQuery(id+"F15.wireOp",EDGE,"E14.right"),sQuery(id+"F15.wireOp",EDGE,"E15.MirrorCS"),sQuery(id+"F15.wireOp",EDGE,"E16.MirrorCS"),sQuery(id+"F15.wireOp",EDGE,"E17.MirrorCS"),sQuery(id+"F15.wireOp",EDGE,"E18.MirrorCS"),sQuery(id+"F15.wireOp",EDGE,"E19.MirrorCS"),sQuery(id+"F15.wireOp",EDGE,"E20.MirrorCS"),sQuery(id+"F15.wireOp",EDGE,"E21.MirrorCS"),sQuery(id+"F15.wireOp",EDGE,"E22.MirrorCS"),sQuery(id+"F15.wireOp",EDGE,"E23.MirrorCS"),sQuery(id+"F15.wireOp",EDGE,"E24.MirrorCS"),sQuery(id+"F15.wireOp",EDGE,"E25.MirrorCS"),sQuery(id+"F15.wireOp",EDGE,"E26.MirrorCS")])]}),"instanceName":"1"}),"instanceName":"1"}),"instanceName":"1"}),"instanceName":"1"});
            var Q70;
            Q70=makeQuery(id+"F23.opPattern","COPY",BODY,{"derivedFrom":makeQuery(id+"F20.opPattern","COPY",BODY,{"derivedFrom":makeQuery(id+"F16.opExtrude","SWEPT_BODY",BODY,{"disambiguationData":[OSD([sQuery(id+"F15.wireOp",EDGE,"E13.bottom"),sQuery(id+"F15.wireOp",EDGE,"E13.top"),sQuery(id+"F15.wireOp",EDGE,"E13.left"),sQuery(id+"F15.wireOp",EDGE,"E13.right"),sQuery(id+"F15.wireOp",EDGE,"E14.bottom"),sQuery(id+"F15.wireOp",EDGE,"E14.top"),sQuery(id+"F15.wireOp",EDGE,"E14.left"),sQuery(id+"F15.wireOp",EDGE,"E14.right"),sQuery(id+"F15.wireOp",EDGE,"E15.MirrorCS"),sQuery(id+"F15.wireOp",EDGE,"E16.MirrorCS"),sQuery(id+"F15.wireOp",EDGE,"E17.MirrorCS"),sQuery(id+"F15.wireOp",EDGE,"E18.MirrorCS"),sQuery(id+"F15.wireOp",EDGE,"E19.MirrorCS"),sQuery(id+"F15.wireOp",EDGE,"E20.MirrorCS"),sQuery(id+"F15.wireOp",EDGE,"E21.MirrorCS"),sQuery(id+"F15.wireOp",EDGE,"E22.MirrorCS"),sQuery(id+"F15.wireOp",EDGE,"E23.MirrorCS"),sQuery(id+"F15.wireOp",EDGE,"E24.MirrorCS"),sQuery(id+"F15.wireOp",EDGE,"E25.MirrorCS"),sQuery(id+"F15.wireOp",EDGE,"E26.MirrorCS")])]}),"instanceName":"1"}),"instanceName":"1"});
            var Q71;
            Q71=makeQuery(id+"F23.opPattern","COPY",BODY,{"derivedFrom":makeQuery(id+"F20.opPattern","COPY",BODY,{"derivedFrom":makeQuery(id+"F17.opPattern","COPY",BODY,{"derivedFrom":makeQuery(id+"F16.opExtrude","SWEPT_BODY",BODY,{"disambiguationData":[OSD([sQuery(id+"F15.wireOp",EDGE,"E13.bottom"),sQuery(id+"F15.wireOp",EDGE,"E13.top"),sQuery(id+"F15.wireOp",EDGE,"E13.left"),sQuery(id+"F15.wireOp",EDGE,"E13.right"),sQuery(id+"F15.wireOp",EDGE,"E14.bottom"),sQuery(id+"F15.wireOp",EDGE,"E14.top"),sQuery(id+"F15.wireOp",EDGE,"E14.left"),sQuery(id+"F15.wireOp",EDGE,"E14.right"),sQuery(id+"F15.wireOp",EDGE,"E15.MirrorCS"),sQuery(id+"F15.wireOp",EDGE,"E16.MirrorCS"),sQuery(id+"F15.wireOp",EDGE,"E17.MirrorCS"),sQuery(id+"F15.wireOp",EDGE,"E18.MirrorCS"),sQuery(id+"F15.wireOp",EDGE,"E19.MirrorCS"),sQuery(id+"F15.wireOp",EDGE,"E20.MirrorCS"),sQuery(id+"F15.wireOp",EDGE,"E21.MirrorCS"),sQuery(id+"F15.wireOp",EDGE,"E22.MirrorCS"),sQuery(id+"F15.wireOp",EDGE,"E23.MirrorCS"),sQuery(id+"F15.wireOp",EDGE,"E24.MirrorCS"),sQuery(id+"F15.wireOp",EDGE,"E25.MirrorCS"),sQuery(id+"F15.wireOp",EDGE,"E26.MirrorCS")])]}),"instanceName":"1"}),"instanceName":"1"}),"instanceName":"1"});
            var Q72;
            Q72=makeQuery(id+"F23.opPattern","COPY",BODY,{"derivedFrom":makeQuery(id+"F20.opPattern","COPY",BODY,{"derivedFrom":makeQuery(id+"F18.opPattern","COPY",BODY,{"derivedFrom":makeQuery(id+"F16.opExtrude","SWEPT_BODY",BODY,{"disambiguationData":[OSD([sQuery(id+"F15.wireOp",EDGE,"E13.bottom"),sQuery(id+"F15.wireOp",EDGE,"E13.top"),sQuery(id+"F15.wireOp",EDGE,"E13.left"),sQuery(id+"F15.wireOp",EDGE,"E13.right"),sQuery(id+"F15.wireOp",EDGE,"E14.bottom"),sQuery(id+"F15.wireOp",EDGE,"E14.top"),sQuery(id+"F15.wireOp",EDGE,"E14.left"),sQuery(id+"F15.wireOp",EDGE,"E14.right"),sQuery(id+"F15.wireOp",EDGE,"E15.MirrorCS"),sQuery(id+"F15.wireOp",EDGE,"E16.MirrorCS"),sQuery(id+"F15.wireOp",EDGE,"E17.MirrorCS"),sQuery(id+"F15.wireOp",EDGE,"E18.MirrorCS"),sQuery(id+"F15.wireOp",EDGE,"E19.MirrorCS"),sQuery(id+"F15.wireOp",EDGE,"E20.MirrorCS"),sQuery(id+"F15.wireOp",EDGE,"E21.MirrorCS"),sQuery(id+"F15.wireOp",EDGE,"E22.MirrorCS"),sQuery(id+"F15.wireOp",EDGE,"E23.MirrorCS"),sQuery(id+"F15.wireOp",EDGE,"E24.MirrorCS"),sQuery(id+"F15.wireOp",EDGE,"E25.MirrorCS"),sQuery(id+"F15.wireOp",EDGE,"E26.MirrorCS")])]}),"instanceName":"1"}),"instanceName":"1"}),"instanceName":"1"});
            var Q73;
            Q73=makeQuery(id+"F23.opPattern","COPY",BODY,{"derivedFrom":makeQuery(id+"F20.opPattern","COPY",BODY,{"derivedFrom":makeQuery(id+"F18.opPattern","COPY",BODY,{"derivedFrom":makeQuery(id+"F17.opPattern","COPY",BODY,{"derivedFrom":makeQuery(id+"F16.opExtrude","SWEPT_BODY",BODY,{"disambiguationData":[OSD([sQuery(id+"F15.wireOp",EDGE,"E13.bottom"),sQuery(id+"F15.wireOp",EDGE,"E13.top"),sQuery(id+"F15.wireOp",EDGE,"E13.left"),sQuery(id+"F15.wireOp",EDGE,"E13.right"),sQuery(id+"F15.wireOp",EDGE,"E14.bottom"),sQuery(id+"F15.wireOp",EDGE,"E14.top"),sQuery(id+"F15.wireOp",EDGE,"E14.left"),sQuery(id+"F15.wireOp",EDGE,"E14.right"),sQuery(id+"F15.wireOp",EDGE,"E15.MirrorCS"),sQuery(id+"F15.wireOp",EDGE,"E16.MirrorCS"),sQuery(id+"F15.wireOp",EDGE,"E17.MirrorCS"),sQuery(id+"F15.wireOp",EDGE,"E18.MirrorCS"),sQuery(id+"F15.wireOp",EDGE,"E19.MirrorCS"),sQuery(id+"F15.wireOp",EDGE,"E20.MirrorCS"),sQuery(id+"F15.wireOp",EDGE,"E21.MirrorCS"),sQuery(id+"F15.wireOp",EDGE,"E22.MirrorCS"),sQuery(id+"F15.wireOp",EDGE,"E23.MirrorCS"),sQuery(id+"F15.wireOp",EDGE,"E24.MirrorCS"),sQuery(id+"F15.wireOp",EDGE,"E25.MirrorCS"),sQuery(id+"F15.wireOp",EDGE,"E26.MirrorCS")])]}),"instanceName":"1"}),"instanceName":"1"}),"instanceName":"1"}),"instanceName":"1"});
            var Q74;
            Q74=makeQuery(id+"F23.opPattern","COPY",BODY,{"derivedFrom":makeQuery(id+"F20.opPattern","COPY",BODY,{"derivedFrom":makeQuery(id+"F19.opPattern","COPY",BODY,{"derivedFrom":makeQuery(id+"F16.opExtrude","SWEPT_BODY",BODY,{"disambiguationData":[OSD([sQuery(id+"F15.wireOp",EDGE,"E13.bottom"),sQuery(id+"F15.wireOp",EDGE,"E13.top"),sQuery(id+"F15.wireOp",EDGE,"E13.left"),sQuery(id+"F15.wireOp",EDGE,"E13.right"),sQuery(id+"F15.wireOp",EDGE,"E14.bottom"),sQuery(id+"F15.wireOp",EDGE,"E14.top"),sQuery(id+"F15.wireOp",EDGE,"E14.left"),sQuery(id+"F15.wireOp",EDGE,"E14.right"),sQuery(id+"F15.wireOp",EDGE,"E15.MirrorCS"),sQuery(id+"F15.wireOp",EDGE,"E16.MirrorCS"),sQuery(id+"F15.wireOp",EDGE,"E17.MirrorCS"),sQuery(id+"F15.wireOp",EDGE,"E18.MirrorCS"),sQuery(id+"F15.wireOp",EDGE,"E19.MirrorCS"),sQuery(id+"F15.wireOp",EDGE,"E20.MirrorCS"),sQuery(id+"F15.wireOp",EDGE,"E21.MirrorCS"),sQuery(id+"F15.wireOp",EDGE,"E22.MirrorCS"),sQuery(id+"F15.wireOp",EDGE,"E23.MirrorCS"),sQuery(id+"F15.wireOp",EDGE,"E24.MirrorCS"),sQuery(id+"F15.wireOp",EDGE,"E25.MirrorCS"),sQuery(id+"F15.wireOp",EDGE,"E26.MirrorCS")])]}),"instanceName":"1"}),"instanceName":"1"}),"instanceName":"1"});
            var Q75;
            Q75=makeQuery(id+"F23.opPattern","COPY",BODY,{"derivedFrom":makeQuery(id+"F20.opPattern","COPY",BODY,{"derivedFrom":makeQuery(id+"F19.opPattern","COPY",BODY,{"derivedFrom":makeQuery(id+"F17.opPattern","COPY",BODY,{"derivedFrom":makeQuery(id+"F16.opExtrude","SWEPT_BODY",BODY,{"disambiguationData":[OSD([sQuery(id+"F15.wireOp",EDGE,"E13.bottom"),sQuery(id+"F15.wireOp",EDGE,"E13.top"),sQuery(id+"F15.wireOp",EDGE,"E13.left"),sQuery(id+"F15.wireOp",EDGE,"E13.right"),sQuery(id+"F15.wireOp",EDGE,"E14.bottom"),sQuery(id+"F15.wireOp",EDGE,"E14.top"),sQuery(id+"F15.wireOp",EDGE,"E14.left"),sQuery(id+"F15.wireOp",EDGE,"E14.right"),sQuery(id+"F15.wireOp",EDGE,"E15.MirrorCS"),sQuery(id+"F15.wireOp",EDGE,"E16.MirrorCS"),sQuery(id+"F15.wireOp",EDGE,"E17.MirrorCS"),sQuery(id+"F15.wireOp",EDGE,"E18.MirrorCS"),sQuery(id+"F15.wireOp",EDGE,"E19.MirrorCS"),sQuery(id+"F15.wireOp",EDGE,"E20.MirrorCS"),sQuery(id+"F15.wireOp",EDGE,"E21.MirrorCS"),sQuery(id+"F15.wireOp",EDGE,"E22.MirrorCS"),sQuery(id+"F15.wireOp",EDGE,"E23.MirrorCS"),sQuery(id+"F15.wireOp",EDGE,"E24.MirrorCS"),sQuery(id+"F15.wireOp",EDGE,"E25.MirrorCS"),sQuery(id+"F15.wireOp",EDGE,"E26.MirrorCS")])]}),"instanceName":"1"}),"instanceName":"1"}),"instanceName":"1"}),"instanceName":"1"});
            var Q76;
            Q76=makeQuery(id+"F23.opPattern","COPY",BODY,{"derivedFrom":makeQuery(id+"F20.opPattern","COPY",BODY,{"derivedFrom":makeQuery(id+"F19.opPattern","COPY",BODY,{"derivedFrom":makeQuery(id+"F18.opPattern","COPY",BODY,{"derivedFrom":makeQuery(id+"F16.opExtrude","SWEPT_BODY",BODY,{"disambiguationData":[OSD([sQuery(id+"F15.wireOp",EDGE,"E13.bottom"),sQuery(id+"F15.wireOp",EDGE,"E13.top"),sQuery(id+"F15.wireOp",EDGE,"E13.left"),sQuery(id+"F15.wireOp",EDGE,"E13.right"),sQuery(id+"F15.wireOp",EDGE,"E14.bottom"),sQuery(id+"F15.wireOp",EDGE,"E14.top"),sQuery(id+"F15.wireOp",EDGE,"E14.left"),sQuery(id+"F15.wireOp",EDGE,"E14.right"),sQuery(id+"F15.wireOp",EDGE,"E15.MirrorCS"),sQuery(id+"F15.wireOp",EDGE,"E16.MirrorCS"),sQuery(id+"F15.wireOp",EDGE,"E17.MirrorCS"),sQuery(id+"F15.wireOp",EDGE,"E18.MirrorCS"),sQuery(id+"F15.wireOp",EDGE,"E19.MirrorCS"),sQuery(id+"F15.wireOp",EDGE,"E20.MirrorCS"),sQuery(id+"F15.wireOp",EDGE,"E21.MirrorCS"),sQuery(id+"F15.wireOp",EDGE,"E22.MirrorCS"),sQuery(id+"F15.wireOp",EDGE,"E23.MirrorCS"),sQuery(id+"F15.wireOp",EDGE,"E24.MirrorCS"),sQuery(id+"F15.wireOp",EDGE,"E25.MirrorCS"),sQuery(id+"F15.wireOp",EDGE,"E26.MirrorCS")])]}),"instanceName":"1"}),"instanceName":"1"}),"instanceName":"1"}),"instanceName":"1"});
            var Q77;
            Q77=makeQuery(id+"F23.opPattern","COPY",BODY,{"derivedFrom":makeQuery(id+"F20.opPattern","COPY",BODY,{"derivedFrom":makeQuery(id+"F19.opPattern","COPY",BODY,{"derivedFrom":makeQuery(id+"F18.opPattern","COPY",BODY,{"derivedFrom":makeQuery(id+"F17.opPattern","COPY",BODY,{"derivedFrom":makeQuery(id+"F16.opExtrude","SWEPT_BODY",BODY,{"disambiguationData":[OSD([sQuery(id+"F15.wireOp",EDGE,"E13.bottom"),sQuery(id+"F15.wireOp",EDGE,"E13.top"),sQuery(id+"F15.wireOp",EDGE,"E13.left"),sQuery(id+"F15.wireOp",EDGE,"E13.right"),sQuery(id+"F15.wireOp",EDGE,"E14.bottom"),sQuery(id+"F15.wireOp",EDGE,"E14.top"),sQuery(id+"F15.wireOp",EDGE,"E14.left"),sQuery(id+"F15.wireOp",EDGE,"E14.right"),sQuery(id+"F15.wireOp",EDGE,"E15.MirrorCS"),sQuery(id+"F15.wireOp",EDGE,"E16.MirrorCS"),sQuery(id+"F15.wireOp",EDGE,"E17.MirrorCS"),sQuery(id+"F15.wireOp",EDGE,"E18.MirrorCS"),sQuery(id+"F15.wireOp",EDGE,"E19.MirrorCS"),sQuery(id+"F15.wireOp",EDGE,"E20.MirrorCS"),sQuery(id+"F15.wireOp",EDGE,"E21.MirrorCS"),sQuery(id+"F15.wireOp",EDGE,"E22.MirrorCS"),sQuery(id+"F15.wireOp",EDGE,"E23.MirrorCS"),sQuery(id+"F15.wireOp",EDGE,"E24.MirrorCS"),sQuery(id+"F15.wireOp",EDGE,"E25.MirrorCS"),sQuery(id+"F15.wireOp",EDGE,"E26.MirrorCS")])]}),"instanceName":"1"}),"instanceName":"1"}),"instanceName":"1"}),"instanceName":"1"}),"instanceName":"1"});
            var Q78;
            Q78=makeQuery(id+"F23.opPattern","COPY",BODY,{"derivedFrom":makeQuery(id+"F21.opPattern","COPY",BODY,{"derivedFrom":makeQuery(id+"F16.opExtrude","SWEPT_BODY",BODY,{"disambiguationData":[OSD([sQuery(id+"F15.wireOp",EDGE,"E13.bottom"),sQuery(id+"F15.wireOp",EDGE,"E13.top"),sQuery(id+"F15.wireOp",EDGE,"E13.left"),sQuery(id+"F15.wireOp",EDGE,"E13.right"),sQuery(id+"F15.wireOp",EDGE,"E14.bottom"),sQuery(id+"F15.wireOp",EDGE,"E14.top"),sQuery(id+"F15.wireOp",EDGE,"E14.left"),sQuery(id+"F15.wireOp",EDGE,"E14.right"),sQuery(id+"F15.wireOp",EDGE,"E15.MirrorCS"),sQuery(id+"F15.wireOp",EDGE,"E16.MirrorCS"),sQuery(id+"F15.wireOp",EDGE,"E17.MirrorCS"),sQuery(id+"F15.wireOp",EDGE,"E18.MirrorCS"),sQuery(id+"F15.wireOp",EDGE,"E19.MirrorCS"),sQuery(id+"F15.wireOp",EDGE,"E20.MirrorCS"),sQuery(id+"F15.wireOp",EDGE,"E21.MirrorCS"),sQuery(id+"F15.wireOp",EDGE,"E22.MirrorCS"),sQuery(id+"F15.wireOp",EDGE,"E23.MirrorCS"),sQuery(id+"F15.wireOp",EDGE,"E24.MirrorCS"),sQuery(id+"F15.wireOp",EDGE,"E25.MirrorCS"),sQuery(id+"F15.wireOp",EDGE,"E26.MirrorCS")])]}),"instanceName":"1"}),"instanceName":"1"});
            var Q79;
            Q79=makeQuery(id+"F23.opPattern","COPY",BODY,{"derivedFrom":makeQuery(id+"F21.opPattern","COPY",BODY,{"derivedFrom":makeQuery(id+"F17.opPattern","COPY",BODY,{"derivedFrom":makeQuery(id+"F16.opExtrude","SWEPT_BODY",BODY,{"disambiguationData":[OSD([sQuery(id+"F15.wireOp",EDGE,"E13.bottom"),sQuery(id+"F15.wireOp",EDGE,"E13.top"),sQuery(id+"F15.wireOp",EDGE,"E13.left"),sQuery(id+"F15.wireOp",EDGE,"E13.right"),sQuery(id+"F15.wireOp",EDGE,"E14.bottom"),sQuery(id+"F15.wireOp",EDGE,"E14.top"),sQuery(id+"F15.wireOp",EDGE,"E14.left"),sQuery(id+"F15.wireOp",EDGE,"E14.right"),sQuery(id+"F15.wireOp",EDGE,"E15.MirrorCS"),sQuery(id+"F15.wireOp",EDGE,"E16.MirrorCS"),sQuery(id+"F15.wireOp",EDGE,"E17.MirrorCS"),sQuery(id+"F15.wireOp",EDGE,"E18.MirrorCS"),sQuery(id+"F15.wireOp",EDGE,"E19.MirrorCS"),sQuery(id+"F15.wireOp",EDGE,"E20.MirrorCS"),sQuery(id+"F15.wireOp",EDGE,"E21.MirrorCS"),sQuery(id+"F15.wireOp",EDGE,"E22.MirrorCS"),sQuery(id+"F15.wireOp",EDGE,"E23.MirrorCS"),sQuery(id+"F15.wireOp",EDGE,"E24.MirrorCS"),sQuery(id+"F15.wireOp",EDGE,"E25.MirrorCS"),sQuery(id+"F15.wireOp",EDGE,"E26.MirrorCS")])]}),"instanceName":"1"}),"instanceName":"1"}),"instanceName":"1"});
            var Q80;
            Q80=makeQuery(id+"F23.opPattern","COPY",BODY,{"derivedFrom":makeQuery(id+"F21.opPattern","COPY",BODY,{"derivedFrom":makeQuery(id+"F18.opPattern","COPY",BODY,{"derivedFrom":makeQuery(id+"F16.opExtrude","SWEPT_BODY",BODY,{"disambiguationData":[OSD([sQuery(id+"F15.wireOp",EDGE,"E13.bottom"),sQuery(id+"F15.wireOp",EDGE,"E13.top"),sQuery(id+"F15.wireOp",EDGE,"E13.left"),sQuery(id+"F15.wireOp",EDGE,"E13.right"),sQuery(id+"F15.wireOp",EDGE,"E14.bottom"),sQuery(id+"F15.wireOp",EDGE,"E14.top"),sQuery(id+"F15.wireOp",EDGE,"E14.left"),sQuery(id+"F15.wireOp",EDGE,"E14.right"),sQuery(id+"F15.wireOp",EDGE,"E15.MirrorCS"),sQuery(id+"F15.wireOp",EDGE,"E16.MirrorCS"),sQuery(id+"F15.wireOp",EDGE,"E17.MirrorCS"),sQuery(id+"F15.wireOp",EDGE,"E18.MirrorCS"),sQuery(id+"F15.wireOp",EDGE,"E19.MirrorCS"),sQuery(id+"F15.wireOp",EDGE,"E20.MirrorCS"),sQuery(id+"F15.wireOp",EDGE,"E21.MirrorCS"),sQuery(id+"F15.wireOp",EDGE,"E22.MirrorCS"),sQuery(id+"F15.wireOp",EDGE,"E23.MirrorCS"),sQuery(id+"F15.wireOp",EDGE,"E24.MirrorCS"),sQuery(id+"F15.wireOp",EDGE,"E25.MirrorCS"),sQuery(id+"F15.wireOp",EDGE,"E26.MirrorCS")])]}),"instanceName":"1"}),"instanceName":"1"}),"instanceName":"1"});
            var Q81;
            Q81=makeQuery(id+"F23.opPattern","COPY",BODY,{"derivedFrom":makeQuery(id+"F21.opPattern","COPY",BODY,{"derivedFrom":makeQuery(id+"F18.opPattern","COPY",BODY,{"derivedFrom":makeQuery(id+"F17.opPattern","COPY",BODY,{"derivedFrom":makeQuery(id+"F16.opExtrude","SWEPT_BODY",BODY,{"disambiguationData":[OSD([sQuery(id+"F15.wireOp",EDGE,"E13.bottom"),sQuery(id+"F15.wireOp",EDGE,"E13.top"),sQuery(id+"F15.wireOp",EDGE,"E13.left"),sQuery(id+"F15.wireOp",EDGE,"E13.right"),sQuery(id+"F15.wireOp",EDGE,"E14.bottom"),sQuery(id+"F15.wireOp",EDGE,"E14.top"),sQuery(id+"F15.wireOp",EDGE,"E14.left"),sQuery(id+"F15.wireOp",EDGE,"E14.right"),sQuery(id+"F15.wireOp",EDGE,"E15.MirrorCS"),sQuery(id+"F15.wireOp",EDGE,"E16.MirrorCS"),sQuery(id+"F15.wireOp",EDGE,"E17.MirrorCS"),sQuery(id+"F15.wireOp",EDGE,"E18.MirrorCS"),sQuery(id+"F15.wireOp",EDGE,"E19.MirrorCS"),sQuery(id+"F15.wireOp",EDGE,"E20.MirrorCS"),sQuery(id+"F15.wireOp",EDGE,"E21.MirrorCS"),sQuery(id+"F15.wireOp",EDGE,"E22.MirrorCS"),sQuery(id+"F15.wireOp",EDGE,"E23.MirrorCS"),sQuery(id+"F15.wireOp",EDGE,"E24.MirrorCS"),sQuery(id+"F15.wireOp",EDGE,"E25.MirrorCS"),sQuery(id+"F15.wireOp",EDGE,"E26.MirrorCS")])]}),"instanceName":"1"}),"instanceName":"1"}),"instanceName":"1"}),"instanceName":"1"});
            var Q82;
            Q82=makeQuery(id+"F23.opPattern","COPY",BODY,{"derivedFrom":makeQuery(id+"F21.opPattern","COPY",BODY,{"derivedFrom":makeQuery(id+"F19.opPattern","COPY",BODY,{"derivedFrom":makeQuery(id+"F16.opExtrude","SWEPT_BODY",BODY,{"disambiguationData":[OSD([sQuery(id+"F15.wireOp",EDGE,"E13.bottom"),sQuery(id+"F15.wireOp",EDGE,"E13.top"),sQuery(id+"F15.wireOp",EDGE,"E13.left"),sQuery(id+"F15.wireOp",EDGE,"E13.right"),sQuery(id+"F15.wireOp",EDGE,"E14.bottom"),sQuery(id+"F15.wireOp",EDGE,"E14.top"),sQuery(id+"F15.wireOp",EDGE,"E14.left"),sQuery(id+"F15.wireOp",EDGE,"E14.right"),sQuery(id+"F15.wireOp",EDGE,"E15.MirrorCS"),sQuery(id+"F15.wireOp",EDGE,"E16.MirrorCS"),sQuery(id+"F15.wireOp",EDGE,"E17.MirrorCS"),sQuery(id+"F15.wireOp",EDGE,"E18.MirrorCS"),sQuery(id+"F15.wireOp",EDGE,"E19.MirrorCS"),sQuery(id+"F15.wireOp",EDGE,"E20.MirrorCS"),sQuery(id+"F15.wireOp",EDGE,"E21.MirrorCS"),sQuery(id+"F15.wireOp",EDGE,"E22.MirrorCS"),sQuery(id+"F15.wireOp",EDGE,"E23.MirrorCS"),sQuery(id+"F15.wireOp",EDGE,"E24.MirrorCS"),sQuery(id+"F15.wireOp",EDGE,"E25.MirrorCS"),sQuery(id+"F15.wireOp",EDGE,"E26.MirrorCS")])]}),"instanceName":"1"}),"instanceName":"1"}),"instanceName":"1"});
            var Q83;
            Q83=makeQuery(id+"F23.opPattern","COPY",BODY,{"derivedFrom":makeQuery(id+"F21.opPattern","COPY",BODY,{"derivedFrom":makeQuery(id+"F19.opPattern","COPY",BODY,{"derivedFrom":makeQuery(id+"F17.opPattern","COPY",BODY,{"derivedFrom":makeQuery(id+"F16.opExtrude","SWEPT_BODY",BODY,{"disambiguationData":[OSD([sQuery(id+"F15.wireOp",EDGE,"E13.bottom"),sQuery(id+"F15.wireOp",EDGE,"E13.top"),sQuery(id+"F15.wireOp",EDGE,"E13.left"),sQuery(id+"F15.wireOp",EDGE,"E13.right"),sQuery(id+"F15.wireOp",EDGE,"E14.bottom"),sQuery(id+"F15.wireOp",EDGE,"E14.top"),sQuery(id+"F15.wireOp",EDGE,"E14.left"),sQuery(id+"F15.wireOp",EDGE,"E14.right"),sQuery(id+"F15.wireOp",EDGE,"E15.MirrorCS"),sQuery(id+"F15.wireOp",EDGE,"E16.MirrorCS"),sQuery(id+"F15.wireOp",EDGE,"E17.MirrorCS"),sQuery(id+"F15.wireOp",EDGE,"E18.MirrorCS"),sQuery(id+"F15.wireOp",EDGE,"E19.MirrorCS"),sQuery(id+"F15.wireOp",EDGE,"E20.MirrorCS"),sQuery(id+"F15.wireOp",EDGE,"E21.MirrorCS"),sQuery(id+"F15.wireOp",EDGE,"E22.MirrorCS"),sQuery(id+"F15.wireOp",EDGE,"E23.MirrorCS"),sQuery(id+"F15.wireOp",EDGE,"E24.MirrorCS"),sQuery(id+"F15.wireOp",EDGE,"E25.MirrorCS"),sQuery(id+"F15.wireOp",EDGE,"E26.MirrorCS")])]}),"instanceName":"1"}),"instanceName":"1"}),"instanceName":"1"}),"instanceName":"1"});
            var Q84;
            Q84=makeQuery(id+"F23.opPattern","COPY",BODY,{"derivedFrom":makeQuery(id+"F21.opPattern","COPY",BODY,{"derivedFrom":makeQuery(id+"F19.opPattern","COPY",BODY,{"derivedFrom":makeQuery(id+"F18.opPattern","COPY",BODY,{"derivedFrom":makeQuery(id+"F16.opExtrude","SWEPT_BODY",BODY,{"disambiguationData":[OSD([sQuery(id+"F15.wireOp",EDGE,"E13.bottom"),sQuery(id+"F15.wireOp",EDGE,"E13.top"),sQuery(id+"F15.wireOp",EDGE,"E13.left"),sQuery(id+"F15.wireOp",EDGE,"E13.right"),sQuery(id+"F15.wireOp",EDGE,"E14.bottom"),sQuery(id+"F15.wireOp",EDGE,"E14.top"),sQuery(id+"F15.wireOp",EDGE,"E14.left"),sQuery(id+"F15.wireOp",EDGE,"E14.right"),sQuery(id+"F15.wireOp",EDGE,"E15.MirrorCS"),sQuery(id+"F15.wireOp",EDGE,"E16.MirrorCS"),sQuery(id+"F15.wireOp",EDGE,"E17.MirrorCS"),sQuery(id+"F15.wireOp",EDGE,"E18.MirrorCS"),sQuery(id+"F15.wireOp",EDGE,"E19.MirrorCS"),sQuery(id+"F15.wireOp",EDGE,"E20.MirrorCS"),sQuery(id+"F15.wireOp",EDGE,"E21.MirrorCS"),sQuery(id+"F15.wireOp",EDGE,"E22.MirrorCS"),sQuery(id+"F15.wireOp",EDGE,"E23.MirrorCS"),sQuery(id+"F15.wireOp",EDGE,"E24.MirrorCS"),sQuery(id+"F15.wireOp",EDGE,"E25.MirrorCS"),sQuery(id+"F15.wireOp",EDGE,"E26.MirrorCS")])]}),"instanceName":"1"}),"instanceName":"1"}),"instanceName":"1"}),"instanceName":"1"});
            var Q85;
            Q85=makeQuery(id+"F23.opPattern","COPY",BODY,{"derivedFrom":makeQuery(id+"F21.opPattern","COPY",BODY,{"derivedFrom":makeQuery(id+"F19.opPattern","COPY",BODY,{"derivedFrom":makeQuery(id+"F18.opPattern","COPY",BODY,{"derivedFrom":makeQuery(id+"F17.opPattern","COPY",BODY,{"derivedFrom":makeQuery(id+"F16.opExtrude","SWEPT_BODY",BODY,{"disambiguationData":[OSD([sQuery(id+"F15.wireOp",EDGE,"E13.bottom"),sQuery(id+"F15.wireOp",EDGE,"E13.top"),sQuery(id+"F15.wireOp",EDGE,"E13.left"),sQuery(id+"F15.wireOp",EDGE,"E13.right"),sQuery(id+"F15.wireOp",EDGE,"E14.bottom"),sQuery(id+"F15.wireOp",EDGE,"E14.top"),sQuery(id+"F15.wireOp",EDGE,"E14.left"),sQuery(id+"F15.wireOp",EDGE,"E14.right"),sQuery(id+"F15.wireOp",EDGE,"E15.MirrorCS"),sQuery(id+"F15.wireOp",EDGE,"E16.MirrorCS"),sQuery(id+"F15.wireOp",EDGE,"E17.MirrorCS"),sQuery(id+"F15.wireOp",EDGE,"E18.MirrorCS"),sQuery(id+"F15.wireOp",EDGE,"E19.MirrorCS"),sQuery(id+"F15.wireOp",EDGE,"E20.MirrorCS"),sQuery(id+"F15.wireOp",EDGE,"E21.MirrorCS"),sQuery(id+"F15.wireOp",EDGE,"E22.MirrorCS"),sQuery(id+"F15.wireOp",EDGE,"E23.MirrorCS"),sQuery(id+"F15.wireOp",EDGE,"E24.MirrorCS"),sQuery(id+"F15.wireOp",EDGE,"E25.MirrorCS"),sQuery(id+"F15.wireOp",EDGE,"E26.MirrorCS")])]}),"instanceName":"1"}),"instanceName":"1"}),"instanceName":"1"}),"instanceName":"1"}),"instanceName":"1"});
            var Q86;
            Q86=makeQuery(id+"F23.opPattern","COPY",BODY,{"derivedFrom":makeQuery(id+"F21.opPattern","COPY",BODY,{"derivedFrom":makeQuery(id+"F20.opPattern","COPY",BODY,{"derivedFrom":makeQuery(id+"F16.opExtrude","SWEPT_BODY",BODY,{"disambiguationData":[OSD([sQuery(id+"F15.wireOp",EDGE,"E13.bottom"),sQuery(id+"F15.wireOp",EDGE,"E13.top"),sQuery(id+"F15.wireOp",EDGE,"E13.left"),sQuery(id+"F15.wireOp",EDGE,"E13.right"),sQuery(id+"F15.wireOp",EDGE,"E14.bottom"),sQuery(id+"F15.wireOp",EDGE,"E14.top"),sQuery(id+"F15.wireOp",EDGE,"E14.left"),sQuery(id+"F15.wireOp",EDGE,"E14.right"),sQuery(id+"F15.wireOp",EDGE,"E15.MirrorCS"),sQuery(id+"F15.wireOp",EDGE,"E16.MirrorCS"),sQuery(id+"F15.wireOp",EDGE,"E17.MirrorCS"),sQuery(id+"F15.wireOp",EDGE,"E18.MirrorCS"),sQuery(id+"F15.wireOp",EDGE,"E19.MirrorCS"),sQuery(id+"F15.wireOp",EDGE,"E20.MirrorCS"),sQuery(id+"F15.wireOp",EDGE,"E21.MirrorCS"),sQuery(id+"F15.wireOp",EDGE,"E22.MirrorCS"),sQuery(id+"F15.wireOp",EDGE,"E23.MirrorCS"),sQuery(id+"F15.wireOp",EDGE,"E24.MirrorCS"),sQuery(id+"F15.wireOp",EDGE,"E25.MirrorCS"),sQuery(id+"F15.wireOp",EDGE,"E26.MirrorCS")])]}),"instanceName":"1"}),"instanceName":"1"}),"instanceName":"1"});
            var Q87;
            Q87=makeQuery(id+"F23.opPattern","COPY",BODY,{"derivedFrom":makeQuery(id+"F21.opPattern","COPY",BODY,{"derivedFrom":makeQuery(id+"F20.opPattern","COPY",BODY,{"derivedFrom":makeQuery(id+"F17.opPattern","COPY",BODY,{"derivedFrom":makeQuery(id+"F16.opExtrude","SWEPT_BODY",BODY,{"disambiguationData":[OSD([sQuery(id+"F15.wireOp",EDGE,"E13.bottom"),sQuery(id+"F15.wireOp",EDGE,"E13.top"),sQuery(id+"F15.wireOp",EDGE,"E13.left"),sQuery(id+"F15.wireOp",EDGE,"E13.right"),sQuery(id+"F15.wireOp",EDGE,"E14.bottom"),sQuery(id+"F15.wireOp",EDGE,"E14.top"),sQuery(id+"F15.wireOp",EDGE,"E14.left"),sQuery(id+"F15.wireOp",EDGE,"E14.right"),sQuery(id+"F15.wireOp",EDGE,"E15.MirrorCS"),sQuery(id+"F15.wireOp",EDGE,"E16.MirrorCS"),sQuery(id+"F15.wireOp",EDGE,"E17.MirrorCS"),sQuery(id+"F15.wireOp",EDGE,"E18.MirrorCS"),sQuery(id+"F15.wireOp",EDGE,"E19.MirrorCS"),sQuery(id+"F15.wireOp",EDGE,"E20.MirrorCS"),sQuery(id+"F15.wireOp",EDGE,"E21.MirrorCS"),sQuery(id+"F15.wireOp",EDGE,"E22.MirrorCS"),sQuery(id+"F15.wireOp",EDGE,"E23.MirrorCS"),sQuery(id+"F15.wireOp",EDGE,"E24.MirrorCS"),sQuery(id+"F15.wireOp",EDGE,"E25.MirrorCS"),sQuery(id+"F15.wireOp",EDGE,"E26.MirrorCS")])]}),"instanceName":"1"}),"instanceName":"1"}),"instanceName":"1"}),"instanceName":"1"});
            var Q88;
            Q88=makeQuery(id+"F23.opPattern","COPY",BODY,{"derivedFrom":makeQuery(id+"F21.opPattern","COPY",BODY,{"derivedFrom":makeQuery(id+"F20.opPattern","COPY",BODY,{"derivedFrom":makeQuery(id+"F18.opPattern","COPY",BODY,{"derivedFrom":makeQuery(id+"F16.opExtrude","SWEPT_BODY",BODY,{"disambiguationData":[OSD([sQuery(id+"F15.wireOp",EDGE,"E13.bottom"),sQuery(id+"F15.wireOp",EDGE,"E13.top"),sQuery(id+"F15.wireOp",EDGE,"E13.left"),sQuery(id+"F15.wireOp",EDGE,"E13.right"),sQuery(id+"F15.wireOp",EDGE,"E14.bottom"),sQuery(id+"F15.wireOp",EDGE,"E14.top"),sQuery(id+"F15.wireOp",EDGE,"E14.left"),sQuery(id+"F15.wireOp",EDGE,"E14.right"),sQuery(id+"F15.wireOp",EDGE,"E15.MirrorCS"),sQuery(id+"F15.wireOp",EDGE,"E16.MirrorCS"),sQuery(id+"F15.wireOp",EDGE,"E17.MirrorCS"),sQuery(id+"F15.wireOp",EDGE,"E18.MirrorCS"),sQuery(id+"F15.wireOp",EDGE,"E19.MirrorCS"),sQuery(id+"F15.wireOp",EDGE,"E20.MirrorCS"),sQuery(id+"F15.wireOp",EDGE,"E21.MirrorCS"),sQuery(id+"F15.wireOp",EDGE,"E22.MirrorCS"),sQuery(id+"F15.wireOp",EDGE,"E23.MirrorCS"),sQuery(id+"F15.wireOp",EDGE,"E24.MirrorCS"),sQuery(id+"F15.wireOp",EDGE,"E25.MirrorCS"),sQuery(id+"F15.wireOp",EDGE,"E26.MirrorCS")])]}),"instanceName":"1"}),"instanceName":"1"}),"instanceName":"1"}),"instanceName":"1"});
            var Q89;
            Q89=makeQuery(id+"F23.opPattern","COPY",BODY,{"derivedFrom":makeQuery(id+"F21.opPattern","COPY",BODY,{"derivedFrom":makeQuery(id+"F20.opPattern","COPY",BODY,{"derivedFrom":makeQuery(id+"F18.opPattern","COPY",BODY,{"derivedFrom":makeQuery(id+"F17.opPattern","COPY",BODY,{"derivedFrom":makeQuery(id+"F16.opExtrude","SWEPT_BODY",BODY,{"disambiguationData":[OSD([sQuery(id+"F15.wireOp",EDGE,"E13.bottom"),sQuery(id+"F15.wireOp",EDGE,"E13.top"),sQuery(id+"F15.wireOp",EDGE,"E13.left"),sQuery(id+"F15.wireOp",EDGE,"E13.right"),sQuery(id+"F15.wireOp",EDGE,"E14.bottom"),sQuery(id+"F15.wireOp",EDGE,"E14.top"),sQuery(id+"F15.wireOp",EDGE,"E14.left"),sQuery(id+"F15.wireOp",EDGE,"E14.right"),sQuery(id+"F15.wireOp",EDGE,"E15.MirrorCS"),sQuery(id+"F15.wireOp",EDGE,"E16.MirrorCS"),sQuery(id+"F15.wireOp",EDGE,"E17.MirrorCS"),sQuery(id+"F15.wireOp",EDGE,"E18.MirrorCS"),sQuery(id+"F15.wireOp",EDGE,"E19.MirrorCS"),sQuery(id+"F15.wireOp",EDGE,"E20.MirrorCS"),sQuery(id+"F15.wireOp",EDGE,"E21.MirrorCS"),sQuery(id+"F15.wireOp",EDGE,"E22.MirrorCS"),sQuery(id+"F15.wireOp",EDGE,"E23.MirrorCS"),sQuery(id+"F15.wireOp",EDGE,"E24.MirrorCS"),sQuery(id+"F15.wireOp",EDGE,"E25.MirrorCS"),sQuery(id+"F15.wireOp",EDGE,"E26.MirrorCS")])]}),"instanceName":"1"}),"instanceName":"1"}),"instanceName":"1"}),"instanceName":"1"}),"instanceName":"1"});
            var Q90;
            Q90=makeQuery(id+"F23.opPattern","COPY",BODY,{"derivedFrom":makeQuery(id+"F21.opPattern","COPY",BODY,{"derivedFrom":makeQuery(id+"F20.opPattern","COPY",BODY,{"derivedFrom":makeQuery(id+"F19.opPattern","COPY",BODY,{"derivedFrom":makeQuery(id+"F16.opExtrude","SWEPT_BODY",BODY,{"disambiguationData":[OSD([sQuery(id+"F15.wireOp",EDGE,"E13.bottom"),sQuery(id+"F15.wireOp",EDGE,"E13.top"),sQuery(id+"F15.wireOp",EDGE,"E13.left"),sQuery(id+"F15.wireOp",EDGE,"E13.right"),sQuery(id+"F15.wireOp",EDGE,"E14.bottom"),sQuery(id+"F15.wireOp",EDGE,"E14.top"),sQuery(id+"F15.wireOp",EDGE,"E14.left"),sQuery(id+"F15.wireOp",EDGE,"E14.right"),sQuery(id+"F15.wireOp",EDGE,"E15.MirrorCS"),sQuery(id+"F15.wireOp",EDGE,"E16.MirrorCS"),sQuery(id+"F15.wireOp",EDGE,"E17.MirrorCS"),sQuery(id+"F15.wireOp",EDGE,"E18.MirrorCS"),sQuery(id+"F15.wireOp",EDGE,"E19.MirrorCS"),sQuery(id+"F15.wireOp",EDGE,"E20.MirrorCS"),sQuery(id+"F15.wireOp",EDGE,"E21.MirrorCS"),sQuery(id+"F15.wireOp",EDGE,"E22.MirrorCS"),sQuery(id+"F15.wireOp",EDGE,"E23.MirrorCS"),sQuery(id+"F15.wireOp",EDGE,"E24.MirrorCS"),sQuery(id+"F15.wireOp",EDGE,"E25.MirrorCS"),sQuery(id+"F15.wireOp",EDGE,"E26.MirrorCS")])]}),"instanceName":"1"}),"instanceName":"1"}),"instanceName":"1"}),"instanceName":"1"});
            var Q91;
            Q91=makeQuery(id+"F23.opPattern","COPY",BODY,{"derivedFrom":makeQuery(id+"F21.opPattern","COPY",BODY,{"derivedFrom":makeQuery(id+"F20.opPattern","COPY",BODY,{"derivedFrom":makeQuery(id+"F19.opPattern","COPY",BODY,{"derivedFrom":makeQuery(id+"F17.opPattern","COPY",BODY,{"derivedFrom":makeQuery(id+"F16.opExtrude","SWEPT_BODY",BODY,{"disambiguationData":[OSD([sQuery(id+"F15.wireOp",EDGE,"E13.bottom"),sQuery(id+"F15.wireOp",EDGE,"E13.top"),sQuery(id+"F15.wireOp",EDGE,"E13.left"),sQuery(id+"F15.wireOp",EDGE,"E13.right"),sQuery(id+"F15.wireOp",EDGE,"E14.bottom"),sQuery(id+"F15.wireOp",EDGE,"E14.top"),sQuery(id+"F15.wireOp",EDGE,"E14.left"),sQuery(id+"F15.wireOp",EDGE,"E14.right"),sQuery(id+"F15.wireOp",EDGE,"E15.MirrorCS"),sQuery(id+"F15.wireOp",EDGE,"E16.MirrorCS"),sQuery(id+"F15.wireOp",EDGE,"E17.MirrorCS"),sQuery(id+"F15.wireOp",EDGE,"E18.MirrorCS"),sQuery(id+"F15.wireOp",EDGE,"E19.MirrorCS"),sQuery(id+"F15.wireOp",EDGE,"E20.MirrorCS"),sQuery(id+"F15.wireOp",EDGE,"E21.MirrorCS"),sQuery(id+"F15.wireOp",EDGE,"E22.MirrorCS"),sQuery(id+"F15.wireOp",EDGE,"E23.MirrorCS"),sQuery(id+"F15.wireOp",EDGE,"E24.MirrorCS"),sQuery(id+"F15.wireOp",EDGE,"E25.MirrorCS"),sQuery(id+"F15.wireOp",EDGE,"E26.MirrorCS")])]}),"instanceName":"1"}),"instanceName":"1"}),"instanceName":"1"}),"instanceName":"1"}),"instanceName":"1"});
            var Q92;
            Q92=makeQuery(id+"F23.opPattern","COPY",BODY,{"derivedFrom":makeQuery(id+"F21.opPattern","COPY",BODY,{"derivedFrom":makeQuery(id+"F20.opPattern","COPY",BODY,{"derivedFrom":makeQuery(id+"F19.opPattern","COPY",BODY,{"derivedFrom":makeQuery(id+"F18.opPattern","COPY",BODY,{"derivedFrom":makeQuery(id+"F16.opExtrude","SWEPT_BODY",BODY,{"disambiguationData":[OSD([sQuery(id+"F15.wireOp",EDGE,"E13.bottom"),sQuery(id+"F15.wireOp",EDGE,"E13.top"),sQuery(id+"F15.wireOp",EDGE,"E13.left"),sQuery(id+"F15.wireOp",EDGE,"E13.right"),sQuery(id+"F15.wireOp",EDGE,"E14.bottom"),sQuery(id+"F15.wireOp",EDGE,"E14.top"),sQuery(id+"F15.wireOp",EDGE,"E14.left"),sQuery(id+"F15.wireOp",EDGE,"E14.right"),sQuery(id+"F15.wireOp",EDGE,"E15.MirrorCS"),sQuery(id+"F15.wireOp",EDGE,"E16.MirrorCS"),sQuery(id+"F15.wireOp",EDGE,"E17.MirrorCS"),sQuery(id+"F15.wireOp",EDGE,"E18.MirrorCS"),sQuery(id+"F15.wireOp",EDGE,"E19.MirrorCS"),sQuery(id+"F15.wireOp",EDGE,"E20.MirrorCS"),sQuery(id+"F15.wireOp",EDGE,"E21.MirrorCS"),sQuery(id+"F15.wireOp",EDGE,"E22.MirrorCS"),sQuery(id+"F15.wireOp",EDGE,"E23.MirrorCS"),sQuery(id+"F15.wireOp",EDGE,"E24.MirrorCS"),sQuery(id+"F15.wireOp",EDGE,"E25.MirrorCS"),sQuery(id+"F15.wireOp",EDGE,"E26.MirrorCS")])]}),"instanceName":"1"}),"instanceName":"1"}),"instanceName":"1"}),"instanceName":"1"}),"instanceName":"1"});
            var Q93;
            Q93=makeQuery(id+"F23.opPattern","COPY",BODY,{"derivedFrom":makeQuery(id+"F22.opPattern","COPY",BODY,{"derivedFrom":makeQuery(id+"F16.opExtrude","SWEPT_BODY",BODY,{"disambiguationData":[OSD([sQuery(id+"F15.wireOp",EDGE,"E13.bottom"),sQuery(id+"F15.wireOp",EDGE,"E13.top"),sQuery(id+"F15.wireOp",EDGE,"E13.left"),sQuery(id+"F15.wireOp",EDGE,"E13.right"),sQuery(id+"F15.wireOp",EDGE,"E14.bottom"),sQuery(id+"F15.wireOp",EDGE,"E14.top"),sQuery(id+"F15.wireOp",EDGE,"E14.left"),sQuery(id+"F15.wireOp",EDGE,"E14.right"),sQuery(id+"F15.wireOp",EDGE,"E15.MirrorCS"),sQuery(id+"F15.wireOp",EDGE,"E16.MirrorCS"),sQuery(id+"F15.wireOp",EDGE,"E17.MirrorCS"),sQuery(id+"F15.wireOp",EDGE,"E18.MirrorCS"),sQuery(id+"F15.wireOp",EDGE,"E19.MirrorCS"),sQuery(id+"F15.wireOp",EDGE,"E20.MirrorCS"),sQuery(id+"F15.wireOp",EDGE,"E21.MirrorCS"),sQuery(id+"F15.wireOp",EDGE,"E22.MirrorCS"),sQuery(id+"F15.wireOp",EDGE,"E23.MirrorCS"),sQuery(id+"F15.wireOp",EDGE,"E24.MirrorCS"),sQuery(id+"F15.wireOp",EDGE,"E25.MirrorCS"),sQuery(id+"F15.wireOp",EDGE,"E26.MirrorCS")])]}),"instanceName":"1"}),"instanceName":"1"});
            var Q94;
            Q94=makeQuery(id+"F23.opPattern","COPY",BODY,{"derivedFrom":makeQuery(id+"F22.opPattern","COPY",BODY,{"derivedFrom":makeQuery(id+"F17.opPattern","COPY",BODY,{"derivedFrom":makeQuery(id+"F16.opExtrude","SWEPT_BODY",BODY,{"disambiguationData":[OSD([sQuery(id+"F15.wireOp",EDGE,"E13.bottom"),sQuery(id+"F15.wireOp",EDGE,"E13.top"),sQuery(id+"F15.wireOp",EDGE,"E13.left"),sQuery(id+"F15.wireOp",EDGE,"E13.right"),sQuery(id+"F15.wireOp",EDGE,"E14.bottom"),sQuery(id+"F15.wireOp",EDGE,"E14.top"),sQuery(id+"F15.wireOp",EDGE,"E14.left"),sQuery(id+"F15.wireOp",EDGE,"E14.right"),sQuery(id+"F15.wireOp",EDGE,"E15.MirrorCS"),sQuery(id+"F15.wireOp",EDGE,"E16.MirrorCS"),sQuery(id+"F15.wireOp",EDGE,"E17.MirrorCS"),sQuery(id+"F15.wireOp",EDGE,"E18.MirrorCS"),sQuery(id+"F15.wireOp",EDGE,"E19.MirrorCS"),sQuery(id+"F15.wireOp",EDGE,"E20.MirrorCS"),sQuery(id+"F15.wireOp",EDGE,"E21.MirrorCS"),sQuery(id+"F15.wireOp",EDGE,"E22.MirrorCS"),sQuery(id+"F15.wireOp",EDGE,"E23.MirrorCS"),sQuery(id+"F15.wireOp",EDGE,"E24.MirrorCS"),sQuery(id+"F15.wireOp",EDGE,"E25.MirrorCS"),sQuery(id+"F15.wireOp",EDGE,"E26.MirrorCS")])]}),"instanceName":"1"}),"instanceName":"1"}),"instanceName":"1"});
            var Q95;
            Q95=makeQuery(id+"F23.opPattern","COPY",BODY,{"derivedFrom":makeQuery(id+"F22.opPattern","COPY",BODY,{"derivedFrom":makeQuery(id+"F18.opPattern","COPY",BODY,{"derivedFrom":makeQuery(id+"F16.opExtrude","SWEPT_BODY",BODY,{"disambiguationData":[OSD([sQuery(id+"F15.wireOp",EDGE,"E13.bottom"),sQuery(id+"F15.wireOp",EDGE,"E13.top"),sQuery(id+"F15.wireOp",EDGE,"E13.left"),sQuery(id+"F15.wireOp",EDGE,"E13.right"),sQuery(id+"F15.wireOp",EDGE,"E14.bottom"),sQuery(id+"F15.wireOp",EDGE,"E14.top"),sQuery(id+"F15.wireOp",EDGE,"E14.left"),sQuery(id+"F15.wireOp",EDGE,"E14.right"),sQuery(id+"F15.wireOp",EDGE,"E15.MirrorCS"),sQuery(id+"F15.wireOp",EDGE,"E16.MirrorCS"),sQuery(id+"F15.wireOp",EDGE,"E17.MirrorCS"),sQuery(id+"F15.wireOp",EDGE,"E18.MirrorCS"),sQuery(id+"F15.wireOp",EDGE,"E19.MirrorCS"),sQuery(id+"F15.wireOp",EDGE,"E20.MirrorCS"),sQuery(id+"F15.wireOp",EDGE,"E21.MirrorCS"),sQuery(id+"F15.wireOp",EDGE,"E22.MirrorCS"),sQuery(id+"F15.wireOp",EDGE,"E23.MirrorCS"),sQuery(id+"F15.wireOp",EDGE,"E24.MirrorCS"),sQuery(id+"F15.wireOp",EDGE,"E25.MirrorCS"),sQuery(id+"F15.wireOp",EDGE,"E26.MirrorCS")])]}),"instanceName":"1"}),"instanceName":"1"}),"instanceName":"1"});
            var Q96;
            Q96=makeQuery(id+"F23.opPattern","COPY",BODY,{"derivedFrom":makeQuery(id+"F22.opPattern","COPY",BODY,{"derivedFrom":makeQuery(id+"F18.opPattern","COPY",BODY,{"derivedFrom":makeQuery(id+"F17.opPattern","COPY",BODY,{"derivedFrom":makeQuery(id+"F16.opExtrude","SWEPT_BODY",BODY,{"disambiguationData":[OSD([sQuery(id+"F15.wireOp",EDGE,"E13.bottom"),sQuery(id+"F15.wireOp",EDGE,"E13.top"),sQuery(id+"F15.wireOp",EDGE,"E13.left"),sQuery(id+"F15.wireOp",EDGE,"E13.right"),sQuery(id+"F15.wireOp",EDGE,"E14.bottom"),sQuery(id+"F15.wireOp",EDGE,"E14.top"),sQuery(id+"F15.wireOp",EDGE,"E14.left"),sQuery(id+"F15.wireOp",EDGE,"E14.right"),sQuery(id+"F15.wireOp",EDGE,"E15.MirrorCS"),sQuery(id+"F15.wireOp",EDGE,"E16.MirrorCS"),sQuery(id+"F15.wireOp",EDGE,"E17.MirrorCS"),sQuery(id+"F15.wireOp",EDGE,"E18.MirrorCS"),sQuery(id+"F15.wireOp",EDGE,"E19.MirrorCS"),sQuery(id+"F15.wireOp",EDGE,"E20.MirrorCS"),sQuery(id+"F15.wireOp",EDGE,"E21.MirrorCS"),sQuery(id+"F15.wireOp",EDGE,"E22.MirrorCS"),sQuery(id+"F15.wireOp",EDGE,"E23.MirrorCS"),sQuery(id+"F15.wireOp",EDGE,"E24.MirrorCS"),sQuery(id+"F15.wireOp",EDGE,"E25.MirrorCS"),sQuery(id+"F15.wireOp",EDGE,"E26.MirrorCS")])]}),"instanceName":"1"}),"instanceName":"1"}),"instanceName":"1"}),"instanceName":"1"});
            var Q97;
            Q97=makeQuery(id+"F23.opPattern","COPY",BODY,{"derivedFrom":makeQuery(id+"F22.opPattern","COPY",BODY,{"derivedFrom":makeQuery(id+"F19.opPattern","COPY",BODY,{"derivedFrom":makeQuery(id+"F16.opExtrude","SWEPT_BODY",BODY,{"disambiguationData":[OSD([sQuery(id+"F15.wireOp",EDGE,"E13.bottom"),sQuery(id+"F15.wireOp",EDGE,"E13.top"),sQuery(id+"F15.wireOp",EDGE,"E13.left"),sQuery(id+"F15.wireOp",EDGE,"E13.right"),sQuery(id+"F15.wireOp",EDGE,"E14.bottom"),sQuery(id+"F15.wireOp",EDGE,"E14.top"),sQuery(id+"F15.wireOp",EDGE,"E14.left"),sQuery(id+"F15.wireOp",EDGE,"E14.right"),sQuery(id+"F15.wireOp",EDGE,"E15.MirrorCS"),sQuery(id+"F15.wireOp",EDGE,"E16.MirrorCS"),sQuery(id+"F15.wireOp",EDGE,"E17.MirrorCS"),sQuery(id+"F15.wireOp",EDGE,"E18.MirrorCS"),sQuery(id+"F15.wireOp",EDGE,"E19.MirrorCS"),sQuery(id+"F15.wireOp",EDGE,"E20.MirrorCS"),sQuery(id+"F15.wireOp",EDGE,"E21.MirrorCS"),sQuery(id+"F15.wireOp",EDGE,"E22.MirrorCS"),sQuery(id+"F15.wireOp",EDGE,"E23.MirrorCS"),sQuery(id+"F15.wireOp",EDGE,"E24.MirrorCS"),sQuery(id+"F15.wireOp",EDGE,"E25.MirrorCS"),sQuery(id+"F15.wireOp",EDGE,"E26.MirrorCS")])]}),"instanceName":"1"}),"instanceName":"1"}),"instanceName":"1"});
            var Q98;
            Q98=makeQuery(id+"F23.opPattern","COPY",BODY,{"derivedFrom":makeQuery(id+"F22.opPattern","COPY",BODY,{"derivedFrom":makeQuery(id+"F19.opPattern","COPY",BODY,{"derivedFrom":makeQuery(id+"F17.opPattern","COPY",BODY,{"derivedFrom":makeQuery(id+"F16.opExtrude","SWEPT_BODY",BODY,{"disambiguationData":[OSD([sQuery(id+"F15.wireOp",EDGE,"E13.bottom"),sQuery(id+"F15.wireOp",EDGE,"E13.top"),sQuery(id+"F15.wireOp",EDGE,"E13.left"),sQuery(id+"F15.wireOp",EDGE,"E13.right"),sQuery(id+"F15.wireOp",EDGE,"E14.bottom"),sQuery(id+"F15.wireOp",EDGE,"E14.top"),sQuery(id+"F15.wireOp",EDGE,"E14.left"),sQuery(id+"F15.wireOp",EDGE,"E14.right"),sQuery(id+"F15.wireOp",EDGE,"E15.MirrorCS"),sQuery(id+"F15.wireOp",EDGE,"E16.MirrorCS"),sQuery(id+"F15.wireOp",EDGE,"E17.MirrorCS"),sQuery(id+"F15.wireOp",EDGE,"E18.MirrorCS"),sQuery(id+"F15.wireOp",EDGE,"E19.MirrorCS"),sQuery(id+"F15.wireOp",EDGE,"E20.MirrorCS"),sQuery(id+"F15.wireOp",EDGE,"E21.MirrorCS"),sQuery(id+"F15.wireOp",EDGE,"E22.MirrorCS"),sQuery(id+"F15.wireOp",EDGE,"E23.MirrorCS"),sQuery(id+"F15.wireOp",EDGE,"E24.MirrorCS"),sQuery(id+"F15.wireOp",EDGE,"E25.MirrorCS"),sQuery(id+"F15.wireOp",EDGE,"E26.MirrorCS")])]}),"instanceName":"1"}),"instanceName":"1"}),"instanceName":"1"}),"instanceName":"1"});
            var Q99;
            Q99=makeQuery(id+"F23.opPattern","COPY",BODY,{"derivedFrom":makeQuery(id+"F22.opPattern","COPY",BODY,{"derivedFrom":makeQuery(id+"F19.opPattern","COPY",BODY,{"derivedFrom":makeQuery(id+"F18.opPattern","COPY",BODY,{"derivedFrom":makeQuery(id+"F16.opExtrude","SWEPT_BODY",BODY,{"disambiguationData":[OSD([sQuery(id+"F15.wireOp",EDGE,"E13.bottom"),sQuery(id+"F15.wireOp",EDGE,"E13.top"),sQuery(id+"F15.wireOp",EDGE,"E13.left"),sQuery(id+"F15.wireOp",EDGE,"E13.right"),sQuery(id+"F15.wireOp",EDGE,"E14.bottom"),sQuery(id+"F15.wireOp",EDGE,"E14.top"),sQuery(id+"F15.wireOp",EDGE,"E14.left"),sQuery(id+"F15.wireOp",EDGE,"E14.right"),sQuery(id+"F15.wireOp",EDGE,"E15.MirrorCS"),sQuery(id+"F15.wireOp",EDGE,"E16.MirrorCS"),sQuery(id+"F15.wireOp",EDGE,"E17.MirrorCS"),sQuery(id+"F15.wireOp",EDGE,"E18.MirrorCS"),sQuery(id+"F15.wireOp",EDGE,"E19.MirrorCS"),sQuery(id+"F15.wireOp",EDGE,"E20.MirrorCS"),sQuery(id+"F15.wireOp",EDGE,"E21.MirrorCS"),sQuery(id+"F15.wireOp",EDGE,"E22.MirrorCS"),sQuery(id+"F15.wireOp",EDGE,"E23.MirrorCS"),sQuery(id+"F15.wireOp",EDGE,"E24.MirrorCS"),sQuery(id+"F15.wireOp",EDGE,"E25.MirrorCS"),sQuery(id+"F15.wireOp",EDGE,"E26.MirrorCS")])]}),"instanceName":"1"}),"instanceName":"1"}),"instanceName":"1"}),"instanceName":"1"});
            var Q100;
            Q100=makeQuery(id+"F23.opPattern","COPY",BODY,{"derivedFrom":makeQuery(id+"F22.opPattern","COPY",BODY,{"derivedFrom":makeQuery(id+"F19.opPattern","COPY",BODY,{"derivedFrom":makeQuery(id+"F18.opPattern","COPY",BODY,{"derivedFrom":makeQuery(id+"F17.opPattern","COPY",BODY,{"derivedFrom":makeQuery(id+"F16.opExtrude","SWEPT_BODY",BODY,{"disambiguationData":[OSD([sQuery(id+"F15.wireOp",EDGE,"E13.bottom"),sQuery(id+"F15.wireOp",EDGE,"E13.top"),sQuery(id+"F15.wireOp",EDGE,"E13.left"),sQuery(id+"F15.wireOp",EDGE,"E13.right"),sQuery(id+"F15.wireOp",EDGE,"E14.bottom"),sQuery(id+"F15.wireOp",EDGE,"E14.top"),sQuery(id+"F15.wireOp",EDGE,"E14.left"),sQuery(id+"F15.wireOp",EDGE,"E14.right"),sQuery(id+"F15.wireOp",EDGE,"E15.MirrorCS"),sQuery(id+"F15.wireOp",EDGE,"E16.MirrorCS"),sQuery(id+"F15.wireOp",EDGE,"E17.MirrorCS"),sQuery(id+"F15.wireOp",EDGE,"E18.MirrorCS"),sQuery(id+"F15.wireOp",EDGE,"E19.MirrorCS"),sQuery(id+"F15.wireOp",EDGE,"E20.MirrorCS"),sQuery(id+"F15.wireOp",EDGE,"E21.MirrorCS"),sQuery(id+"F15.wireOp",EDGE,"E22.MirrorCS"),sQuery(id+"F15.wireOp",EDGE,"E23.MirrorCS"),sQuery(id+"F15.wireOp",EDGE,"E24.MirrorCS"),sQuery(id+"F15.wireOp",EDGE,"E25.MirrorCS"),sQuery(id+"F15.wireOp",EDGE,"E26.MirrorCS")])]}),"instanceName":"1"}),"instanceName":"1"}),"instanceName":"1"}),"instanceName":"1"}),"instanceName":"1"});
            var Q101;
            Q101=makeQuery(id+"F23.opPattern","COPY",BODY,{"derivedFrom":makeQuery(id+"F22.opPattern","COPY",BODY,{"derivedFrom":makeQuery(id+"F20.opPattern","COPY",BODY,{"derivedFrom":makeQuery(id+"F16.opExtrude","SWEPT_BODY",BODY,{"disambiguationData":[OSD([sQuery(id+"F15.wireOp",EDGE,"E13.bottom"),sQuery(id+"F15.wireOp",EDGE,"E13.top"),sQuery(id+"F15.wireOp",EDGE,"E13.left"),sQuery(id+"F15.wireOp",EDGE,"E13.right"),sQuery(id+"F15.wireOp",EDGE,"E14.bottom"),sQuery(id+"F15.wireOp",EDGE,"E14.top"),sQuery(id+"F15.wireOp",EDGE,"E14.left"),sQuery(id+"F15.wireOp",EDGE,"E14.right"),sQuery(id+"F15.wireOp",EDGE,"E15.MirrorCS"),sQuery(id+"F15.wireOp",EDGE,"E16.MirrorCS"),sQuery(id+"F15.wireOp",EDGE,"E17.MirrorCS"),sQuery(id+"F15.wireOp",EDGE,"E18.MirrorCS"),sQuery(id+"F15.wireOp",EDGE,"E19.MirrorCS"),sQuery(id+"F15.wireOp",EDGE,"E20.MirrorCS"),sQuery(id+"F15.wireOp",EDGE,"E21.MirrorCS"),sQuery(id+"F15.wireOp",EDGE,"E22.MirrorCS"),sQuery(id+"F15.wireOp",EDGE,"E23.MirrorCS"),sQuery(id+"F15.wireOp",EDGE,"E24.MirrorCS"),sQuery(id+"F15.wireOp",EDGE,"E25.MirrorCS"),sQuery(id+"F15.wireOp",EDGE,"E26.MirrorCS")])]}),"instanceName":"1"}),"instanceName":"1"}),"instanceName":"1"});
            var Q102;
            Q102=makeQuery(id+"F23.opPattern","COPY",BODY,{"derivedFrom":makeQuery(id+"F22.opPattern","COPY",BODY,{"derivedFrom":makeQuery(id+"F20.opPattern","COPY",BODY,{"derivedFrom":makeQuery(id+"F17.opPattern","COPY",BODY,{"derivedFrom":makeQuery(id+"F16.opExtrude","SWEPT_BODY",BODY,{"disambiguationData":[OSD([sQuery(id+"F15.wireOp",EDGE,"E13.bottom"),sQuery(id+"F15.wireOp",EDGE,"E13.top"),sQuery(id+"F15.wireOp",EDGE,"E13.left"),sQuery(id+"F15.wireOp",EDGE,"E13.right"),sQuery(id+"F15.wireOp",EDGE,"E14.bottom"),sQuery(id+"F15.wireOp",EDGE,"E14.top"),sQuery(id+"F15.wireOp",EDGE,"E14.left"),sQuery(id+"F15.wireOp",EDGE,"E14.right"),sQuery(id+"F15.wireOp",EDGE,"E15.MirrorCS"),sQuery(id+"F15.wireOp",EDGE,"E16.MirrorCS"),sQuery(id+"F15.wireOp",EDGE,"E17.MirrorCS"),sQuery(id+"F15.wireOp",EDGE,"E18.MirrorCS"),sQuery(id+"F15.wireOp",EDGE,"E19.MirrorCS"),sQuery(id+"F15.wireOp",EDGE,"E20.MirrorCS"),sQuery(id+"F15.wireOp",EDGE,"E21.MirrorCS"),sQuery(id+"F15.wireOp",EDGE,"E22.MirrorCS"),sQuery(id+"F15.wireOp",EDGE,"E23.MirrorCS"),sQuery(id+"F15.wireOp",EDGE,"E24.MirrorCS"),sQuery(id+"F15.wireOp",EDGE,"E25.MirrorCS"),sQuery(id+"F15.wireOp",EDGE,"E26.MirrorCS")])]}),"instanceName":"1"}),"instanceName":"1"}),"instanceName":"1"}),"instanceName":"1"});
            var Q103;
            Q103=makeQuery(id+"F23.opPattern","COPY",BODY,{"derivedFrom":makeQuery(id+"F22.opPattern","COPY",BODY,{"derivedFrom":makeQuery(id+"F20.opPattern","COPY",BODY,{"derivedFrom":makeQuery(id+"F18.opPattern","COPY",BODY,{"derivedFrom":makeQuery(id+"F16.opExtrude","SWEPT_BODY",BODY,{"disambiguationData":[OSD([sQuery(id+"F15.wireOp",EDGE,"E13.bottom"),sQuery(id+"F15.wireOp",EDGE,"E13.top"),sQuery(id+"F15.wireOp",EDGE,"E13.left"),sQuery(id+"F15.wireOp",EDGE,"E13.right"),sQuery(id+"F15.wireOp",EDGE,"E14.bottom"),sQuery(id+"F15.wireOp",EDGE,"E14.top"),sQuery(id+"F15.wireOp",EDGE,"E14.left"),sQuery(id+"F15.wireOp",EDGE,"E14.right"),sQuery(id+"F15.wireOp",EDGE,"E15.MirrorCS"),sQuery(id+"F15.wireOp",EDGE,"E16.MirrorCS"),sQuery(id+"F15.wireOp",EDGE,"E17.MirrorCS"),sQuery(id+"F15.wireOp",EDGE,"E18.MirrorCS"),sQuery(id+"F15.wireOp",EDGE,"E19.MirrorCS"),sQuery(id+"F15.wireOp",EDGE,"E20.MirrorCS"),sQuery(id+"F15.wireOp",EDGE,"E21.MirrorCS"),sQuery(id+"F15.wireOp",EDGE,"E22.MirrorCS"),sQuery(id+"F15.wireOp",EDGE,"E23.MirrorCS"),sQuery(id+"F15.wireOp",EDGE,"E24.MirrorCS"),sQuery(id+"F15.wireOp",EDGE,"E25.MirrorCS"),sQuery(id+"F15.wireOp",EDGE,"E26.MirrorCS")])]}),"instanceName":"1"}),"instanceName":"1"}),"instanceName":"1"}),"instanceName":"1"});
            var Q104;
            Q104=makeQuery(id+"F23.opPattern","COPY",BODY,{"derivedFrom":makeQuery(id+"F22.opPattern","COPY",BODY,{"derivedFrom":makeQuery(id+"F20.opPattern","COPY",BODY,{"derivedFrom":makeQuery(id+"F18.opPattern","COPY",BODY,{"derivedFrom":makeQuery(id+"F17.opPattern","COPY",BODY,{"derivedFrom":makeQuery(id+"F16.opExtrude","SWEPT_BODY",BODY,{"disambiguationData":[OSD([sQuery(id+"F15.wireOp",EDGE,"E13.bottom"),sQuery(id+"F15.wireOp",EDGE,"E13.top"),sQuery(id+"F15.wireOp",EDGE,"E13.left"),sQuery(id+"F15.wireOp",EDGE,"E13.right"),sQuery(id+"F15.wireOp",EDGE,"E14.bottom"),sQuery(id+"F15.wireOp",EDGE,"E14.top"),sQuery(id+"F15.wireOp",EDGE,"E14.left"),sQuery(id+"F15.wireOp",EDGE,"E14.right"),sQuery(id+"F15.wireOp",EDGE,"E15.MirrorCS"),sQuery(id+"F15.wireOp",EDGE,"E16.MirrorCS"),sQuery(id+"F15.wireOp",EDGE,"E17.MirrorCS"),sQuery(id+"F15.wireOp",EDGE,"E18.MirrorCS"),sQuery(id+"F15.wireOp",EDGE,"E19.MirrorCS"),sQuery(id+"F15.wireOp",EDGE,"E20.MirrorCS"),sQuery(id+"F15.wireOp",EDGE,"E21.MirrorCS"),sQuery(id+"F15.wireOp",EDGE,"E22.MirrorCS"),sQuery(id+"F15.wireOp",EDGE,"E23.MirrorCS"),sQuery(id+"F15.wireOp",EDGE,"E24.MirrorCS"),sQuery(id+"F15.wireOp",EDGE,"E25.MirrorCS"),sQuery(id+"F15.wireOp",EDGE,"E26.MirrorCS")])]}),"instanceName":"1"}),"instanceName":"1"}),"instanceName":"1"}),"instanceName":"1"}),"instanceName":"1"});
            var Q105;
            Q105=makeQuery(id+"F23.opPattern","COPY",BODY,{"derivedFrom":makeQuery(id+"F22.opPattern","COPY",BODY,{"derivedFrom":makeQuery(id+"F20.opPattern","COPY",BODY,{"derivedFrom":makeQuery(id+"F19.opPattern","COPY",BODY,{"derivedFrom":makeQuery(id+"F16.opExtrude","SWEPT_BODY",BODY,{"disambiguationData":[OSD([sQuery(id+"F15.wireOp",EDGE,"E13.bottom"),sQuery(id+"F15.wireOp",EDGE,"E13.top"),sQuery(id+"F15.wireOp",EDGE,"E13.left"),sQuery(id+"F15.wireOp",EDGE,"E13.right"),sQuery(id+"F15.wireOp",EDGE,"E14.bottom"),sQuery(id+"F15.wireOp",EDGE,"E14.top"),sQuery(id+"F15.wireOp",EDGE,"E14.left"),sQuery(id+"F15.wireOp",EDGE,"E14.right"),sQuery(id+"F15.wireOp",EDGE,"E15.MirrorCS"),sQuery(id+"F15.wireOp",EDGE,"E16.MirrorCS"),sQuery(id+"F15.wireOp",EDGE,"E17.MirrorCS"),sQuery(id+"F15.wireOp",EDGE,"E18.MirrorCS"),sQuery(id+"F15.wireOp",EDGE,"E19.MirrorCS"),sQuery(id+"F15.wireOp",EDGE,"E20.MirrorCS"),sQuery(id+"F15.wireOp",EDGE,"E21.MirrorCS"),sQuery(id+"F15.wireOp",EDGE,"E22.MirrorCS"),sQuery(id+"F15.wireOp",EDGE,"E23.MirrorCS"),sQuery(id+"F15.wireOp",EDGE,"E24.MirrorCS"),sQuery(id+"F15.wireOp",EDGE,"E25.MirrorCS"),sQuery(id+"F15.wireOp",EDGE,"E26.MirrorCS")])]}),"instanceName":"1"}),"instanceName":"1"}),"instanceName":"1"}),"instanceName":"1"});
            var Q106;
            Q106=makeQuery(id+"F23.opPattern","COPY",BODY,{"derivedFrom":makeQuery(id+"F22.opPattern","COPY",BODY,{"derivedFrom":makeQuery(id+"F20.opPattern","COPY",BODY,{"derivedFrom":makeQuery(id+"F19.opPattern","COPY",BODY,{"derivedFrom":makeQuery(id+"F17.opPattern","COPY",BODY,{"derivedFrom":makeQuery(id+"F16.opExtrude","SWEPT_BODY",BODY,{"disambiguationData":[OSD([sQuery(id+"F15.wireOp",EDGE,"E13.bottom"),sQuery(id+"F15.wireOp",EDGE,"E13.top"),sQuery(id+"F15.wireOp",EDGE,"E13.left"),sQuery(id+"F15.wireOp",EDGE,"E13.right"),sQuery(id+"F15.wireOp",EDGE,"E14.bottom"),sQuery(id+"F15.wireOp",EDGE,"E14.top"),sQuery(id+"F15.wireOp",EDGE,"E14.left"),sQuery(id+"F15.wireOp",EDGE,"E14.right"),sQuery(id+"F15.wireOp",EDGE,"E15.MirrorCS"),sQuery(id+"F15.wireOp",EDGE,"E16.MirrorCS"),sQuery(id+"F15.wireOp",EDGE,"E17.MirrorCS"),sQuery(id+"F15.wireOp",EDGE,"E18.MirrorCS"),sQuery(id+"F15.wireOp",EDGE,"E19.MirrorCS"),sQuery(id+"F15.wireOp",EDGE,"E20.MirrorCS"),sQuery(id+"F15.wireOp",EDGE,"E21.MirrorCS"),sQuery(id+"F15.wireOp",EDGE,"E22.MirrorCS"),sQuery(id+"F15.wireOp",EDGE,"E23.MirrorCS"),sQuery(id+"F15.wireOp",EDGE,"E24.MirrorCS"),sQuery(id+"F15.wireOp",EDGE,"E25.MirrorCS"),sQuery(id+"F15.wireOp",EDGE,"E26.MirrorCS")])]}),"instanceName":"1"}),"instanceName":"1"}),"instanceName":"1"}),"instanceName":"1"}),"instanceName":"1"});
            var Q107;
            Q107=makeQuery(id+"F23.opPattern","COPY",BODY,{"derivedFrom":makeQuery(id+"F22.opPattern","COPY",BODY,{"derivedFrom":makeQuery(id+"F20.opPattern","COPY",BODY,{"derivedFrom":makeQuery(id+"F19.opPattern","COPY",BODY,{"derivedFrom":makeQuery(id+"F18.opPattern","COPY",BODY,{"derivedFrom":makeQuery(id+"F16.opExtrude","SWEPT_BODY",BODY,{"disambiguationData":[OSD([sQuery(id+"F15.wireOp",EDGE,"E13.bottom"),sQuery(id+"F15.wireOp",EDGE,"E13.top"),sQuery(id+"F15.wireOp",EDGE,"E13.left"),sQuery(id+"F15.wireOp",EDGE,"E13.right"),sQuery(id+"F15.wireOp",EDGE,"E14.bottom"),sQuery(id+"F15.wireOp",EDGE,"E14.top"),sQuery(id+"F15.wireOp",EDGE,"E14.left"),sQuery(id+"F15.wireOp",EDGE,"E14.right"),sQuery(id+"F15.wireOp",EDGE,"E15.MirrorCS"),sQuery(id+"F15.wireOp",EDGE,"E16.MirrorCS"),sQuery(id+"F15.wireOp",EDGE,"E17.MirrorCS"),sQuery(id+"F15.wireOp",EDGE,"E18.MirrorCS"),sQuery(id+"F15.wireOp",EDGE,"E19.MirrorCS"),sQuery(id+"F15.wireOp",EDGE,"E20.MirrorCS"),sQuery(id+"F15.wireOp",EDGE,"E21.MirrorCS"),sQuery(id+"F15.wireOp",EDGE,"E22.MirrorCS"),sQuery(id+"F15.wireOp",EDGE,"E23.MirrorCS"),sQuery(id+"F15.wireOp",EDGE,"E24.MirrorCS"),sQuery(id+"F15.wireOp",EDGE,"E25.MirrorCS"),sQuery(id+"F15.wireOp",EDGE,"E26.MirrorCS")])]}),"instanceName":"1"}),"instanceName":"1"}),"instanceName":"1"}),"instanceName":"1"}),"instanceName":"1"});
            var Q108;
            Q108=makeQuery(id+"F23.opPattern","COPY",BODY,{"derivedFrom":makeQuery(id+"F22.opPattern","COPY",BODY,{"derivedFrom":makeQuery(id+"F20.opPattern","COPY",BODY,{"derivedFrom":makeQuery(id+"F19.opPattern","COPY",BODY,{"derivedFrom":makeQuery(id+"F18.opPattern","COPY",BODY,{"derivedFrom":makeQuery(id+"F17.opPattern","COPY",BODY,{"derivedFrom":makeQuery(id+"F16.opExtrude","SWEPT_BODY",BODY,{"disambiguationData":[OSD([sQuery(id+"F15.wireOp",EDGE,"E13.bottom"),sQuery(id+"F15.wireOp",EDGE,"E13.top"),sQuery(id+"F15.wireOp",EDGE,"E13.left"),sQuery(id+"F15.wireOp",EDGE,"E13.right"),sQuery(id+"F15.wireOp",EDGE,"E14.bottom"),sQuery(id+"F15.wireOp",EDGE,"E14.top"),sQuery(id+"F15.wireOp",EDGE,"E14.left"),sQuery(id+"F15.wireOp",EDGE,"E14.right"),sQuery(id+"F15.wireOp",EDGE,"E15.MirrorCS"),sQuery(id+"F15.wireOp",EDGE,"E16.MirrorCS"),sQuery(id+"F15.wireOp",EDGE,"E17.MirrorCS"),sQuery(id+"F15.wireOp",EDGE,"E18.MirrorCS"),sQuery(id+"F15.wireOp",EDGE,"E19.MirrorCS"),sQuery(id+"F15.wireOp",EDGE,"E20.MirrorCS"),sQuery(id+"F15.wireOp",EDGE,"E21.MirrorCS"),sQuery(id+"F15.wireOp",EDGE,"E22.MirrorCS"),sQuery(id+"F15.wireOp",EDGE,"E23.MirrorCS"),sQuery(id+"F15.wireOp",EDGE,"E24.MirrorCS"),sQuery(id+"F15.wireOp",EDGE,"E25.MirrorCS"),sQuery(id+"F15.wireOp",EDGE,"E26.MirrorCS")])]}),"instanceName":"1"}),"instanceName":"1"}),"instanceName":"1"}),"instanceName":"1"}),"instanceName":"1"}),"instanceName":"1"});
            var Q109;
            Q109=makeQuery(id+"F23.opPattern","COPY",BODY,{"derivedFrom":makeQuery(id+"F22.opPattern","COPY",BODY,{"derivedFrom":makeQuery(id+"F21.opPattern","COPY",BODY,{"derivedFrom":makeQuery(id+"F16.opExtrude","SWEPT_BODY",BODY,{"disambiguationData":[OSD([sQuery(id+"F15.wireOp",EDGE,"E13.bottom"),sQuery(id+"F15.wireOp",EDGE,"E13.top"),sQuery(id+"F15.wireOp",EDGE,"E13.left"),sQuery(id+"F15.wireOp",EDGE,"E13.right"),sQuery(id+"F15.wireOp",EDGE,"E14.bottom"),sQuery(id+"F15.wireOp",EDGE,"E14.top"),sQuery(id+"F15.wireOp",EDGE,"E14.left"),sQuery(id+"F15.wireOp",EDGE,"E14.right"),sQuery(id+"F15.wireOp",EDGE,"E15.MirrorCS"),sQuery(id+"F15.wireOp",EDGE,"E16.MirrorCS"),sQuery(id+"F15.wireOp",EDGE,"E17.MirrorCS"),sQuery(id+"F15.wireOp",EDGE,"E18.MirrorCS"),sQuery(id+"F15.wireOp",EDGE,"E19.MirrorCS"),sQuery(id+"F15.wireOp",EDGE,"E20.MirrorCS"),sQuery(id+"F15.wireOp",EDGE,"E21.MirrorCS"),sQuery(id+"F15.wireOp",EDGE,"E22.MirrorCS"),sQuery(id+"F15.wireOp",EDGE,"E23.MirrorCS"),sQuery(id+"F15.wireOp",EDGE,"E24.MirrorCS"),sQuery(id+"F15.wireOp",EDGE,"E25.MirrorCS"),sQuery(id+"F15.wireOp",EDGE,"E26.MirrorCS")])]}),"instanceName":"1"}),"instanceName":"1"}),"instanceName":"1"});
            var Q110;
            Q110=makeQuery(id+"F23.opPattern","COPY",BODY,{"derivedFrom":makeQuery(id+"F22.opPattern","COPY",BODY,{"derivedFrom":makeQuery(id+"F21.opPattern","COPY",BODY,{"derivedFrom":makeQuery(id+"F17.opPattern","COPY",BODY,{"derivedFrom":makeQuery(id+"F16.opExtrude","SWEPT_BODY",BODY,{"disambiguationData":[OSD([sQuery(id+"F15.wireOp",EDGE,"E13.bottom"),sQuery(id+"F15.wireOp",EDGE,"E13.top"),sQuery(id+"F15.wireOp",EDGE,"E13.left"),sQuery(id+"F15.wireOp",EDGE,"E13.right"),sQuery(id+"F15.wireOp",EDGE,"E14.bottom"),sQuery(id+"F15.wireOp",EDGE,"E14.top"),sQuery(id+"F15.wireOp",EDGE,"E14.left"),sQuery(id+"F15.wireOp",EDGE,"E14.right"),sQuery(id+"F15.wireOp",EDGE,"E15.MirrorCS"),sQuery(id+"F15.wireOp",EDGE,"E16.MirrorCS"),sQuery(id+"F15.wireOp",EDGE,"E17.MirrorCS"),sQuery(id+"F15.wireOp",EDGE,"E18.MirrorCS"),sQuery(id+"F15.wireOp",EDGE,"E19.MirrorCS"),sQuery(id+"F15.wireOp",EDGE,"E20.MirrorCS"),sQuery(id+"F15.wireOp",EDGE,"E21.MirrorCS"),sQuery(id+"F15.wireOp",EDGE,"E22.MirrorCS"),sQuery(id+"F15.wireOp",EDGE,"E23.MirrorCS"),sQuery(id+"F15.wireOp",EDGE,"E24.MirrorCS"),sQuery(id+"F15.wireOp",EDGE,"E25.MirrorCS"),sQuery(id+"F15.wireOp",EDGE,"E26.MirrorCS")])]}),"instanceName":"1"}),"instanceName":"1"}),"instanceName":"1"}),"instanceName":"1"});
            var Q111;
            Q111=makeQuery(id+"F23.opPattern","COPY",BODY,{"derivedFrom":makeQuery(id+"F22.opPattern","COPY",BODY,{"derivedFrom":makeQuery(id+"F21.opPattern","COPY",BODY,{"derivedFrom":makeQuery(id+"F18.opPattern","COPY",BODY,{"derivedFrom":makeQuery(id+"F16.opExtrude","SWEPT_BODY",BODY,{"disambiguationData":[OSD([sQuery(id+"F15.wireOp",EDGE,"E13.bottom"),sQuery(id+"F15.wireOp",EDGE,"E13.top"),sQuery(id+"F15.wireOp",EDGE,"E13.left"),sQuery(id+"F15.wireOp",EDGE,"E13.right"),sQuery(id+"F15.wireOp",EDGE,"E14.bottom"),sQuery(id+"F15.wireOp",EDGE,"E14.top"),sQuery(id+"F15.wireOp",EDGE,"E14.left"),sQuery(id+"F15.wireOp",EDGE,"E14.right"),sQuery(id+"F15.wireOp",EDGE,"E15.MirrorCS"),sQuery(id+"F15.wireOp",EDGE,"E16.MirrorCS"),sQuery(id+"F15.wireOp",EDGE,"E17.MirrorCS"),sQuery(id+"F15.wireOp",EDGE,"E18.MirrorCS"),sQuery(id+"F15.wireOp",EDGE,"E19.MirrorCS"),sQuery(id+"F15.wireOp",EDGE,"E20.MirrorCS"),sQuery(id+"F15.wireOp",EDGE,"E21.MirrorCS"),sQuery(id+"F15.wireOp",EDGE,"E22.MirrorCS"),sQuery(id+"F15.wireOp",EDGE,"E23.MirrorCS"),sQuery(id+"F15.wireOp",EDGE,"E24.MirrorCS"),sQuery(id+"F15.wireOp",EDGE,"E25.MirrorCS"),sQuery(id+"F15.wireOp",EDGE,"E26.MirrorCS")])]}),"instanceName":"1"}),"instanceName":"1"}),"instanceName":"1"}),"instanceName":"1"});
            var Q112;
            Q112=makeQuery(id+"F23.opPattern","COPY",BODY,{"derivedFrom":makeQuery(id+"F22.opPattern","COPY",BODY,{"derivedFrom":makeQuery(id+"F21.opPattern","COPY",BODY,{"derivedFrom":makeQuery(id+"F18.opPattern","COPY",BODY,{"derivedFrom":makeQuery(id+"F17.opPattern","COPY",BODY,{"derivedFrom":makeQuery(id+"F16.opExtrude","SWEPT_BODY",BODY,{"disambiguationData":[OSD([sQuery(id+"F15.wireOp",EDGE,"E13.bottom"),sQuery(id+"F15.wireOp",EDGE,"E13.top"),sQuery(id+"F15.wireOp",EDGE,"E13.left"),sQuery(id+"F15.wireOp",EDGE,"E13.right"),sQuery(id+"F15.wireOp",EDGE,"E14.bottom"),sQuery(id+"F15.wireOp",EDGE,"E14.top"),sQuery(id+"F15.wireOp",EDGE,"E14.left"),sQuery(id+"F15.wireOp",EDGE,"E14.right"),sQuery(id+"F15.wireOp",EDGE,"E15.MirrorCS"),sQuery(id+"F15.wireOp",EDGE,"E16.MirrorCS"),sQuery(id+"F15.wireOp",EDGE,"E17.MirrorCS"),sQuery(id+"F15.wireOp",EDGE,"E18.MirrorCS"),sQuery(id+"F15.wireOp",EDGE,"E19.MirrorCS"),sQuery(id+"F15.wireOp",EDGE,"E20.MirrorCS"),sQuery(id+"F15.wireOp",EDGE,"E21.MirrorCS"),sQuery(id+"F15.wireOp",EDGE,"E22.MirrorCS"),sQuery(id+"F15.wireOp",EDGE,"E23.MirrorCS"),sQuery(id+"F15.wireOp",EDGE,"E24.MirrorCS"),sQuery(id+"F15.wireOp",EDGE,"E25.MirrorCS"),sQuery(id+"F15.wireOp",EDGE,"E26.MirrorCS")])]}),"instanceName":"1"}),"instanceName":"1"}),"instanceName":"1"}),"instanceName":"1"}),"instanceName":"1"});
            var Q113;
            Q113=makeQuery(id+"F23.opPattern","COPY",BODY,{"derivedFrom":makeQuery(id+"F22.opPattern","COPY",BODY,{"derivedFrom":makeQuery(id+"F21.opPattern","COPY",BODY,{"derivedFrom":makeQuery(id+"F19.opPattern","COPY",BODY,{"derivedFrom":makeQuery(id+"F16.opExtrude","SWEPT_BODY",BODY,{"disambiguationData":[OSD([sQuery(id+"F15.wireOp",EDGE,"E13.bottom"),sQuery(id+"F15.wireOp",EDGE,"E13.top"),sQuery(id+"F15.wireOp",EDGE,"E13.left"),sQuery(id+"F15.wireOp",EDGE,"E13.right"),sQuery(id+"F15.wireOp",EDGE,"E14.bottom"),sQuery(id+"F15.wireOp",EDGE,"E14.top"),sQuery(id+"F15.wireOp",EDGE,"E14.left"),sQuery(id+"F15.wireOp",EDGE,"E14.right"),sQuery(id+"F15.wireOp",EDGE,"E15.MirrorCS"),sQuery(id+"F15.wireOp",EDGE,"E16.MirrorCS"),sQuery(id+"F15.wireOp",EDGE,"E17.MirrorCS"),sQuery(id+"F15.wireOp",EDGE,"E18.MirrorCS"),sQuery(id+"F15.wireOp",EDGE,"E19.MirrorCS"),sQuery(id+"F15.wireOp",EDGE,"E20.MirrorCS"),sQuery(id+"F15.wireOp",EDGE,"E21.MirrorCS"),sQuery(id+"F15.wireOp",EDGE,"E22.MirrorCS"),sQuery(id+"F15.wireOp",EDGE,"E23.MirrorCS"),sQuery(id+"F15.wireOp",EDGE,"E24.MirrorCS"),sQuery(id+"F15.wireOp",EDGE,"E25.MirrorCS"),sQuery(id+"F15.wireOp",EDGE,"E26.MirrorCS")])]}),"instanceName":"1"}),"instanceName":"1"}),"instanceName":"1"}),"instanceName":"1"});
            var Q114;
            Q114=makeQuery(id+"F23.opPattern","COPY",BODY,{"derivedFrom":makeQuery(id+"F22.opPattern","COPY",BODY,{"derivedFrom":makeQuery(id+"F21.opPattern","COPY",BODY,{"derivedFrom":makeQuery(id+"F19.opPattern","COPY",BODY,{"derivedFrom":makeQuery(id+"F17.opPattern","COPY",BODY,{"derivedFrom":makeQuery(id+"F16.opExtrude","SWEPT_BODY",BODY,{"disambiguationData":[OSD([sQuery(id+"F15.wireOp",EDGE,"E13.bottom"),sQuery(id+"F15.wireOp",EDGE,"E13.top"),sQuery(id+"F15.wireOp",EDGE,"E13.left"),sQuery(id+"F15.wireOp",EDGE,"E13.right"),sQuery(id+"F15.wireOp",EDGE,"E14.bottom"),sQuery(id+"F15.wireOp",EDGE,"E14.top"),sQuery(id+"F15.wireOp",EDGE,"E14.left"),sQuery(id+"F15.wireOp",EDGE,"E14.right"),sQuery(id+"F15.wireOp",EDGE,"E15.MirrorCS"),sQuery(id+"F15.wireOp",EDGE,"E16.MirrorCS"),sQuery(id+"F15.wireOp",EDGE,"E17.MirrorCS"),sQuery(id+"F15.wireOp",EDGE,"E18.MirrorCS"),sQuery(id+"F15.wireOp",EDGE,"E19.MirrorCS"),sQuery(id+"F15.wireOp",EDGE,"E20.MirrorCS"),sQuery(id+"F15.wireOp",EDGE,"E21.MirrorCS"),sQuery(id+"F15.wireOp",EDGE,"E22.MirrorCS"),sQuery(id+"F15.wireOp",EDGE,"E23.MirrorCS"),sQuery(id+"F15.wireOp",EDGE,"E24.MirrorCS"),sQuery(id+"F15.wireOp",EDGE,"E25.MirrorCS"),sQuery(id+"F15.wireOp",EDGE,"E26.MirrorCS")])]}),"instanceName":"1"}),"instanceName":"1"}),"instanceName":"1"}),"instanceName":"1"}),"instanceName":"1"});
            var Q115;
            Q115=makeQuery(id+"F23.opPattern","COPY",BODY,{"derivedFrom":makeQuery(id+"F22.opPattern","COPY",BODY,{"derivedFrom":makeQuery(id+"F21.opPattern","COPY",BODY,{"derivedFrom":makeQuery(id+"F19.opPattern","COPY",BODY,{"derivedFrom":makeQuery(id+"F18.opPattern","COPY",BODY,{"derivedFrom":makeQuery(id+"F16.opExtrude","SWEPT_BODY",BODY,{"disambiguationData":[OSD([sQuery(id+"F15.wireOp",EDGE,"E13.bottom"),sQuery(id+"F15.wireOp",EDGE,"E13.top"),sQuery(id+"F15.wireOp",EDGE,"E13.left"),sQuery(id+"F15.wireOp",EDGE,"E13.right"),sQuery(id+"F15.wireOp",EDGE,"E14.bottom"),sQuery(id+"F15.wireOp",EDGE,"E14.top"),sQuery(id+"F15.wireOp",EDGE,"E14.left"),sQuery(id+"F15.wireOp",EDGE,"E14.right"),sQuery(id+"F15.wireOp",EDGE,"E15.MirrorCS"),sQuery(id+"F15.wireOp",EDGE,"E16.MirrorCS"),sQuery(id+"F15.wireOp",EDGE,"E17.MirrorCS"),sQuery(id+"F15.wireOp",EDGE,"E18.MirrorCS"),sQuery(id+"F15.wireOp",EDGE,"E19.MirrorCS"),sQuery(id+"F15.wireOp",EDGE,"E20.MirrorCS"),sQuery(id+"F15.wireOp",EDGE,"E21.MirrorCS"),sQuery(id+"F15.wireOp",EDGE,"E22.MirrorCS"),sQuery(id+"F15.wireOp",EDGE,"E23.MirrorCS"),sQuery(id+"F15.wireOp",EDGE,"E24.MirrorCS"),sQuery(id+"F15.wireOp",EDGE,"E25.MirrorCS"),sQuery(id+"F15.wireOp",EDGE,"E26.MirrorCS")])]}),"instanceName":"1"}),"instanceName":"1"}),"instanceName":"1"}),"instanceName":"1"}),"instanceName":"1"});
            var Q116;
            Q116=makeQuery(id+"F23.opPattern","COPY",BODY,{"derivedFrom":makeQuery(id+"F22.opPattern","COPY",BODY,{"derivedFrom":makeQuery(id+"F21.opPattern","COPY",BODY,{"derivedFrom":makeQuery(id+"F19.opPattern","COPY",BODY,{"derivedFrom":makeQuery(id+"F18.opPattern","COPY",BODY,{"derivedFrom":makeQuery(id+"F17.opPattern","COPY",BODY,{"derivedFrom":makeQuery(id+"F16.opExtrude","SWEPT_BODY",BODY,{"disambiguationData":[OSD([sQuery(id+"F15.wireOp",EDGE,"E13.bottom"),sQuery(id+"F15.wireOp",EDGE,"E13.top"),sQuery(id+"F15.wireOp",EDGE,"E13.left"),sQuery(id+"F15.wireOp",EDGE,"E13.right"),sQuery(id+"F15.wireOp",EDGE,"E14.bottom"),sQuery(id+"F15.wireOp",EDGE,"E14.top"),sQuery(id+"F15.wireOp",EDGE,"E14.left"),sQuery(id+"F15.wireOp",EDGE,"E14.right"),sQuery(id+"F15.wireOp",EDGE,"E15.MirrorCS"),sQuery(id+"F15.wireOp",EDGE,"E16.MirrorCS"),sQuery(id+"F15.wireOp",EDGE,"E17.MirrorCS"),sQuery(id+"F15.wireOp",EDGE,"E18.MirrorCS"),sQuery(id+"F15.wireOp",EDGE,"E19.MirrorCS"),sQuery(id+"F15.wireOp",EDGE,"E20.MirrorCS"),sQuery(id+"F15.wireOp",EDGE,"E21.MirrorCS"),sQuery(id+"F15.wireOp",EDGE,"E22.MirrorCS"),sQuery(id+"F15.wireOp",EDGE,"E23.MirrorCS"),sQuery(id+"F15.wireOp",EDGE,"E24.MirrorCS"),sQuery(id+"F15.wireOp",EDGE,"E25.MirrorCS"),sQuery(id+"F15.wireOp",EDGE,"E26.MirrorCS")])]}),"instanceName":"1"}),"instanceName":"1"}),"instanceName":"1"}),"instanceName":"1"}),"instanceName":"1"}),"instanceName":"1"});
            var Q117;
            Q117=makeQuery(id+"F23.opPattern","COPY",BODY,{"derivedFrom":makeQuery(id+"F22.opPattern","COPY",BODY,{"derivedFrom":makeQuery(id+"F21.opPattern","COPY",BODY,{"derivedFrom":makeQuery(id+"F20.opPattern","COPY",BODY,{"derivedFrom":makeQuery(id+"F16.opExtrude","SWEPT_BODY",BODY,{"disambiguationData":[OSD([sQuery(id+"F15.wireOp",EDGE,"E13.bottom"),sQuery(id+"F15.wireOp",EDGE,"E13.top"),sQuery(id+"F15.wireOp",EDGE,"E13.left"),sQuery(id+"F15.wireOp",EDGE,"E13.right"),sQuery(id+"F15.wireOp",EDGE,"E14.bottom"),sQuery(id+"F15.wireOp",EDGE,"E14.top"),sQuery(id+"F15.wireOp",EDGE,"E14.left"),sQuery(id+"F15.wireOp",EDGE,"E14.right"),sQuery(id+"F15.wireOp",EDGE,"E15.MirrorCS"),sQuery(id+"F15.wireOp",EDGE,"E16.MirrorCS"),sQuery(id+"F15.wireOp",EDGE,"E17.MirrorCS"),sQuery(id+"F15.wireOp",EDGE,"E18.MirrorCS"),sQuery(id+"F15.wireOp",EDGE,"E19.MirrorCS"),sQuery(id+"F15.wireOp",EDGE,"E20.MirrorCS"),sQuery(id+"F15.wireOp",EDGE,"E21.MirrorCS"),sQuery(id+"F15.wireOp",EDGE,"E22.MirrorCS"),sQuery(id+"F15.wireOp",EDGE,"E23.MirrorCS"),sQuery(id+"F15.wireOp",EDGE,"E24.MirrorCS"),sQuery(id+"F15.wireOp",EDGE,"E25.MirrorCS"),sQuery(id+"F15.wireOp",EDGE,"E26.MirrorCS")])]}),"instanceName":"1"}),"instanceName":"1"}),"instanceName":"1"}),"instanceName":"1"});
            var Q118;
            Q118=makeQuery(id+"F23.opPattern","COPY",BODY,{"derivedFrom":makeQuery(id+"F22.opPattern","COPY",BODY,{"derivedFrom":makeQuery(id+"F21.opPattern","COPY",BODY,{"derivedFrom":makeQuery(id+"F20.opPattern","COPY",BODY,{"derivedFrom":makeQuery(id+"F17.opPattern","COPY",BODY,{"derivedFrom":makeQuery(id+"F16.opExtrude","SWEPT_BODY",BODY,{"disambiguationData":[OSD([sQuery(id+"F15.wireOp",EDGE,"E13.bottom"),sQuery(id+"F15.wireOp",EDGE,"E13.top"),sQuery(id+"F15.wireOp",EDGE,"E13.left"),sQuery(id+"F15.wireOp",EDGE,"E13.right"),sQuery(id+"F15.wireOp",EDGE,"E14.bottom"),sQuery(id+"F15.wireOp",EDGE,"E14.top"),sQuery(id+"F15.wireOp",EDGE,"E14.left"),sQuery(id+"F15.wireOp",EDGE,"E14.right"),sQuery(id+"F15.wireOp",EDGE,"E15.MirrorCS"),sQuery(id+"F15.wireOp",EDGE,"E16.MirrorCS"),sQuery(id+"F15.wireOp",EDGE,"E17.MirrorCS"),sQuery(id+"F15.wireOp",EDGE,"E18.MirrorCS"),sQuery(id+"F15.wireOp",EDGE,"E19.MirrorCS"),sQuery(id+"F15.wireOp",EDGE,"E20.MirrorCS"),sQuery(id+"F15.wireOp",EDGE,"E21.MirrorCS"),sQuery(id+"F15.wireOp",EDGE,"E22.MirrorCS"),sQuery(id+"F15.wireOp",EDGE,"E23.MirrorCS"),sQuery(id+"F15.wireOp",EDGE,"E24.MirrorCS"),sQuery(id+"F15.wireOp",EDGE,"E25.MirrorCS"),sQuery(id+"F15.wireOp",EDGE,"E26.MirrorCS")])]}),"instanceName":"1"}),"instanceName":"1"}),"instanceName":"1"}),"instanceName":"1"}),"instanceName":"1"});
            var Q119;
            Q119=makeQuery(id+"F23.opPattern","COPY",BODY,{"derivedFrom":makeQuery(id+"F22.opPattern","COPY",BODY,{"derivedFrom":makeQuery(id+"F21.opPattern","COPY",BODY,{"derivedFrom":makeQuery(id+"F20.opPattern","COPY",BODY,{"derivedFrom":makeQuery(id+"F18.opPattern","COPY",BODY,{"derivedFrom":makeQuery(id+"F16.opExtrude","SWEPT_BODY",BODY,{"disambiguationData":[OSD([sQuery(id+"F15.wireOp",EDGE,"E13.bottom"),sQuery(id+"F15.wireOp",EDGE,"E13.top"),sQuery(id+"F15.wireOp",EDGE,"E13.left"),sQuery(id+"F15.wireOp",EDGE,"E13.right"),sQuery(id+"F15.wireOp",EDGE,"E14.bottom"),sQuery(id+"F15.wireOp",EDGE,"E14.top"),sQuery(id+"F15.wireOp",EDGE,"E14.left"),sQuery(id+"F15.wireOp",EDGE,"E14.right"),sQuery(id+"F15.wireOp",EDGE,"E15.MirrorCS"),sQuery(id+"F15.wireOp",EDGE,"E16.MirrorCS"),sQuery(id+"F15.wireOp",EDGE,"E17.MirrorCS"),sQuery(id+"F15.wireOp",EDGE,"E18.MirrorCS"),sQuery(id+"F15.wireOp",EDGE,"E19.MirrorCS"),sQuery(id+"F15.wireOp",EDGE,"E20.MirrorCS"),sQuery(id+"F15.wireOp",EDGE,"E21.MirrorCS"),sQuery(id+"F15.wireOp",EDGE,"E22.MirrorCS"),sQuery(id+"F15.wireOp",EDGE,"E23.MirrorCS"),sQuery(id+"F15.wireOp",EDGE,"E24.MirrorCS"),sQuery(id+"F15.wireOp",EDGE,"E25.MirrorCS"),sQuery(id+"F15.wireOp",EDGE,"E26.MirrorCS")])]}),"instanceName":"1"}),"instanceName":"1"}),"instanceName":"1"}),"instanceName":"1"}),"instanceName":"1"});
            var Q120;
            Q120=makeQuery(id+"F23.opPattern","COPY",BODY,{"derivedFrom":makeQuery(id+"F22.opPattern","COPY",BODY,{"derivedFrom":makeQuery(id+"F21.opPattern","COPY",BODY,{"derivedFrom":makeQuery(id+"F20.opPattern","COPY",BODY,{"derivedFrom":makeQuery(id+"F18.opPattern","COPY",BODY,{"derivedFrom":makeQuery(id+"F17.opPattern","COPY",BODY,{"derivedFrom":makeQuery(id+"F16.opExtrude","SWEPT_BODY",BODY,{"disambiguationData":[OSD([sQuery(id+"F15.wireOp",EDGE,"E13.bottom"),sQuery(id+"F15.wireOp",EDGE,"E13.top"),sQuery(id+"F15.wireOp",EDGE,"E13.left"),sQuery(id+"F15.wireOp",EDGE,"E13.right"),sQuery(id+"F15.wireOp",EDGE,"E14.bottom"),sQuery(id+"F15.wireOp",EDGE,"E14.top"),sQuery(id+"F15.wireOp",EDGE,"E14.left"),sQuery(id+"F15.wireOp",EDGE,"E14.right"),sQuery(id+"F15.wireOp",EDGE,"E15.MirrorCS"),sQuery(id+"F15.wireOp",EDGE,"E16.MirrorCS"),sQuery(id+"F15.wireOp",EDGE,"E17.MirrorCS"),sQuery(id+"F15.wireOp",EDGE,"E18.MirrorCS"),sQuery(id+"F15.wireOp",EDGE,"E19.MirrorCS"),sQuery(id+"F15.wireOp",EDGE,"E20.MirrorCS"),sQuery(id+"F15.wireOp",EDGE,"E21.MirrorCS"),sQuery(id+"F15.wireOp",EDGE,"E22.MirrorCS"),sQuery(id+"F15.wireOp",EDGE,"E23.MirrorCS"),sQuery(id+"F15.wireOp",EDGE,"E24.MirrorCS"),sQuery(id+"F15.wireOp",EDGE,"E25.MirrorCS"),sQuery(id+"F15.wireOp",EDGE,"E26.MirrorCS")])]}),"instanceName":"1"}),"instanceName":"1"}),"instanceName":"1"}),"instanceName":"1"}),"instanceName":"1"}),"instanceName":"1"});
            var Q121;
            Q121=makeQuery(id+"F23.opPattern","COPY",BODY,{"derivedFrom":makeQuery(id+"F22.opPattern","COPY",BODY,{"derivedFrom":makeQuery(id+"F21.opPattern","COPY",BODY,{"derivedFrom":makeQuery(id+"F20.opPattern","COPY",BODY,{"derivedFrom":makeQuery(id+"F19.opPattern","COPY",BODY,{"derivedFrom":makeQuery(id+"F16.opExtrude","SWEPT_BODY",BODY,{"disambiguationData":[OSD([sQuery(id+"F15.wireOp",EDGE,"E13.bottom"),sQuery(id+"F15.wireOp",EDGE,"E13.top"),sQuery(id+"F15.wireOp",EDGE,"E13.left"),sQuery(id+"F15.wireOp",EDGE,"E13.right"),sQuery(id+"F15.wireOp",EDGE,"E14.bottom"),sQuery(id+"F15.wireOp",EDGE,"E14.top"),sQuery(id+"F15.wireOp",EDGE,"E14.left"),sQuery(id+"F15.wireOp",EDGE,"E14.right"),sQuery(id+"F15.wireOp",EDGE,"E15.MirrorCS"),sQuery(id+"F15.wireOp",EDGE,"E16.MirrorCS"),sQuery(id+"F15.wireOp",EDGE,"E17.MirrorCS"),sQuery(id+"F15.wireOp",EDGE,"E18.MirrorCS"),sQuery(id+"F15.wireOp",EDGE,"E19.MirrorCS"),sQuery(id+"F15.wireOp",EDGE,"E20.MirrorCS"),sQuery(id+"F15.wireOp",EDGE,"E21.MirrorCS"),sQuery(id+"F15.wireOp",EDGE,"E22.MirrorCS"),sQuery(id+"F15.wireOp",EDGE,"E23.MirrorCS"),sQuery(id+"F15.wireOp",EDGE,"E24.MirrorCS"),sQuery(id+"F15.wireOp",EDGE,"E25.MirrorCS"),sQuery(id+"F15.wireOp",EDGE,"E26.MirrorCS")])]}),"instanceName":"1"}),"instanceName":"1"}),"instanceName":"1"}),"instanceName":"1"}),"instanceName":"1"});
            var Q122;
            Q122=makeQuery(id+"F23.opPattern","COPY",BODY,{"derivedFrom":makeQuery(id+"F22.opPattern","COPY",BODY,{"derivedFrom":makeQuery(id+"F21.opPattern","COPY",BODY,{"derivedFrom":makeQuery(id+"F20.opPattern","COPY",BODY,{"derivedFrom":makeQuery(id+"F19.opPattern","COPY",BODY,{"derivedFrom":makeQuery(id+"F17.opPattern","COPY",BODY,{"derivedFrom":makeQuery(id+"F16.opExtrude","SWEPT_BODY",BODY,{"disambiguationData":[OSD([sQuery(id+"F15.wireOp",EDGE,"E13.bottom"),sQuery(id+"F15.wireOp",EDGE,"E13.top"),sQuery(id+"F15.wireOp",EDGE,"E13.left"),sQuery(id+"F15.wireOp",EDGE,"E13.right"),sQuery(id+"F15.wireOp",EDGE,"E14.bottom"),sQuery(id+"F15.wireOp",EDGE,"E14.top"),sQuery(id+"F15.wireOp",EDGE,"E14.left"),sQuery(id+"F15.wireOp",EDGE,"E14.right"),sQuery(id+"F15.wireOp",EDGE,"E15.MirrorCS"),sQuery(id+"F15.wireOp",EDGE,"E16.MirrorCS"),sQuery(id+"F15.wireOp",EDGE,"E17.MirrorCS"),sQuery(id+"F15.wireOp",EDGE,"E18.MirrorCS"),sQuery(id+"F15.wireOp",EDGE,"E19.MirrorCS"),sQuery(id+"F15.wireOp",EDGE,"E20.MirrorCS"),sQuery(id+"F15.wireOp",EDGE,"E21.MirrorCS"),sQuery(id+"F15.wireOp",EDGE,"E22.MirrorCS"),sQuery(id+"F15.wireOp",EDGE,"E23.MirrorCS"),sQuery(id+"F15.wireOp",EDGE,"E24.MirrorCS"),sQuery(id+"F15.wireOp",EDGE,"E25.MirrorCS"),sQuery(id+"F15.wireOp",EDGE,"E26.MirrorCS")])]}),"instanceName":"1"}),"instanceName":"1"}),"instanceName":"1"}),"instanceName":"1"}),"instanceName":"1"}),"instanceName":"1"});
            var Q123;
            Q123=makeQuery(id+"F23.opPattern","COPY",BODY,{"derivedFrom":makeQuery(id+"F22.opPattern","COPY",BODY,{"derivedFrom":makeQuery(id+"F21.opPattern","COPY",BODY,{"derivedFrom":makeQuery(id+"F20.opPattern","COPY",BODY,{"derivedFrom":makeQuery(id+"F19.opPattern","COPY",BODY,{"derivedFrom":makeQuery(id+"F18.opPattern","COPY",BODY,{"derivedFrom":makeQuery(id+"F16.opExtrude","SWEPT_BODY",BODY,{"disambiguationData":[OSD([sQuery(id+"F15.wireOp",EDGE,"E13.bottom"),sQuery(id+"F15.wireOp",EDGE,"E13.top"),sQuery(id+"F15.wireOp",EDGE,"E13.left"),sQuery(id+"F15.wireOp",EDGE,"E13.right"),sQuery(id+"F15.wireOp",EDGE,"E14.bottom"),sQuery(id+"F15.wireOp",EDGE,"E14.top"),sQuery(id+"F15.wireOp",EDGE,"E14.left"),sQuery(id+"F15.wireOp",EDGE,"E14.right"),sQuery(id+"F15.wireOp",EDGE,"E15.MirrorCS"),sQuery(id+"F15.wireOp",EDGE,"E16.MirrorCS"),sQuery(id+"F15.wireOp",EDGE,"E17.MirrorCS"),sQuery(id+"F15.wireOp",EDGE,"E18.MirrorCS"),sQuery(id+"F15.wireOp",EDGE,"E19.MirrorCS"),sQuery(id+"F15.wireOp",EDGE,"E20.MirrorCS"),sQuery(id+"F15.wireOp",EDGE,"E21.MirrorCS"),sQuery(id+"F15.wireOp",EDGE,"E22.MirrorCS"),sQuery(id+"F15.wireOp",EDGE,"E23.MirrorCS"),sQuery(id+"F15.wireOp",EDGE,"E24.MirrorCS"),sQuery(id+"F15.wireOp",EDGE,"E25.MirrorCS"),sQuery(id+"F15.wireOp",EDGE,"E26.MirrorCS")])]}),"instanceName":"1"}),"instanceName":"1"}),"instanceName":"1"}),"instanceName":"1"}),"instanceName":"1"}),"instanceName":"1"});
            transform(context, id + "F24", {"entities" : qUnion([Q0, Q1, Q2, Q3, Q4, Q5, Q6, Q7, Q8, Q9, Q10, Q11, Q12, Q13, Q14, Q15, Q16, Q17, Q18, Q19, Q20, Q21, Q22, Q23, Q24, Q25, Q26, Q27, Q28, Q29, Q30, Q31, Q32, Q33, Q34, Q35, Q36, Q37, Q38, Q39, Q40, Q41, Q42, Q43, Q44, Q45, Q46, Q47, Q48, Q49, Q50, Q51, Q52, Q53, Q54, Q55, Q56, Q57, Q58, Q59, Q60, Q61, Q62, Q63, Q64, Q65, Q66, Q67, Q68, Q69, Q70, Q71, Q72, Q73, Q74, Q75, Q76, Q77, Q78, Q79, Q80, Q81, Q82, Q83, Q84, Q85, Q86, Q87, Q88, Q89, Q90, Q91, Q92, Q93, Q94, Q95, Q96, Q97, Q98, Q99, Q100, Q101, Q102, Q103, Q104, Q105, Q106, Q107, Q108, Q109, Q110, Q111, Q112, Q113, Q114, Q115, Q116, Q117, Q118, Q119, Q120, Q121, Q122, Q123]), "transformType" : TransformType.TRANSLATION_3D, "dx" : -160 * mm, "dy" : 0 * mm, "dz" : 0 * mm, "makeCopy" : true});
        }
        {
            var Q0;
            Q0=makeQuery(id+"F21.opPattern","COPY",BODY,{"derivedFrom":makeQuery(id+"F20.opPattern","COPY",BODY,{"derivedFrom":makeQuery(id+"F16.opExtrude","SWEPT_BODY",BODY,{"disambiguationData":[OSD([sQuery(id+"F15.wireOp",EDGE,"E13.bottom"),sQuery(id+"F15.wireOp",EDGE,"E13.top"),sQuery(id+"F15.wireOp",EDGE,"E13.left"),sQuery(id+"F15.wireOp",EDGE,"E13.right"),sQuery(id+"F15.wireOp",EDGE,"E14.bottom"),sQuery(id+"F15.wireOp",EDGE,"E14.top"),sQuery(id+"F15.wireOp",EDGE,"E14.left"),sQuery(id+"F15.wireOp",EDGE,"E14.right"),sQuery(id+"F15.wireOp",EDGE,"E15.MirrorCS"),sQuery(id+"F15.wireOp",EDGE,"E16.MirrorCS"),sQuery(id+"F15.wireOp",EDGE,"E17.MirrorCS"),sQuery(id+"F15.wireOp",EDGE,"E18.MirrorCS"),sQuery(id+"F15.wireOp",EDGE,"E19.MirrorCS"),sQuery(id+"F15.wireOp",EDGE,"E20.MirrorCS"),sQuery(id+"F15.wireOp",EDGE,"E21.MirrorCS"),sQuery(id+"F15.wireOp",EDGE,"E22.MirrorCS"),sQuery(id+"F15.wireOp",EDGE,"E23.MirrorCS"),sQuery(id+"F15.wireOp",EDGE,"E24.MirrorCS"),sQuery(id+"F15.wireOp",EDGE,"E25.MirrorCS"),sQuery(id+"F15.wireOp",EDGE,"E26.MirrorCS")])]}),"instanceName":"1"}),"instanceName":"1"});
            var Q1;
            Q1=makeQuery(id+"F21.opPattern","COPY",BODY,{"derivedFrom":makeQuery(id+"F20.opPattern","COPY",BODY,{"derivedFrom":makeQuery(id+"F17.opPattern","COPY",BODY,{"derivedFrom":makeQuery(id+"F16.opExtrude","SWEPT_BODY",BODY,{"disambiguationData":[OSD([sQuery(id+"F15.wireOp",EDGE,"E13.bottom"),sQuery(id+"F15.wireOp",EDGE,"E13.top"),sQuery(id+"F15.wireOp",EDGE,"E13.left"),sQuery(id+"F15.wireOp",EDGE,"E13.right"),sQuery(id+"F15.wireOp",EDGE,"E14.bottom"),sQuery(id+"F15.wireOp",EDGE,"E14.top"),sQuery(id+"F15.wireOp",EDGE,"E14.left"),sQuery(id+"F15.wireOp",EDGE,"E14.right"),sQuery(id+"F15.wireOp",EDGE,"E15.MirrorCS"),sQuery(id+"F15.wireOp",EDGE,"E16.MirrorCS"),sQuery(id+"F15.wireOp",EDGE,"E17.MirrorCS"),sQuery(id+"F15.wireOp",EDGE,"E18.MirrorCS"),sQuery(id+"F15.wireOp",EDGE,"E19.MirrorCS"),sQuery(id+"F15.wireOp",EDGE,"E20.MirrorCS"),sQuery(id+"F15.wireOp",EDGE,"E21.MirrorCS"),sQuery(id+"F15.wireOp",EDGE,"E22.MirrorCS"),sQuery(id+"F15.wireOp",EDGE,"E23.MirrorCS"),sQuery(id+"F15.wireOp",EDGE,"E24.MirrorCS"),sQuery(id+"F15.wireOp",EDGE,"E25.MirrorCS"),sQuery(id+"F15.wireOp",EDGE,"E26.MirrorCS")])]}),"instanceName":"1"}),"instanceName":"1"}),"instanceName":"1"});
            var Q2;
            Q2=makeQuery(id+"F21.opPattern","COPY",BODY,{"derivedFrom":makeQuery(id+"F20.opPattern","COPY",BODY,{"derivedFrom":makeQuery(id+"F18.opPattern","COPY",BODY,{"derivedFrom":makeQuery(id+"F16.opExtrude","SWEPT_BODY",BODY,{"disambiguationData":[OSD([sQuery(id+"F15.wireOp",EDGE,"E13.bottom"),sQuery(id+"F15.wireOp",EDGE,"E13.top"),sQuery(id+"F15.wireOp",EDGE,"E13.left"),sQuery(id+"F15.wireOp",EDGE,"E13.right"),sQuery(id+"F15.wireOp",EDGE,"E14.bottom"),sQuery(id+"F15.wireOp",EDGE,"E14.top"),sQuery(id+"F15.wireOp",EDGE,"E14.left"),sQuery(id+"F15.wireOp",EDGE,"E14.right"),sQuery(id+"F15.wireOp",EDGE,"E15.MirrorCS"),sQuery(id+"F15.wireOp",EDGE,"E16.MirrorCS"),sQuery(id+"F15.wireOp",EDGE,"E17.MirrorCS"),sQuery(id+"F15.wireOp",EDGE,"E18.MirrorCS"),sQuery(id+"F15.wireOp",EDGE,"E19.MirrorCS"),sQuery(id+"F15.wireOp",EDGE,"E20.MirrorCS"),sQuery(id+"F15.wireOp",EDGE,"E21.MirrorCS"),sQuery(id+"F15.wireOp",EDGE,"E22.MirrorCS"),sQuery(id+"F15.wireOp",EDGE,"E23.MirrorCS"),sQuery(id+"F15.wireOp",EDGE,"E24.MirrorCS"),sQuery(id+"F15.wireOp",EDGE,"E25.MirrorCS"),sQuery(id+"F15.wireOp",EDGE,"E26.MirrorCS")])]}),"instanceName":"1"}),"instanceName":"1"}),"instanceName":"1"});
            var Q3;
            Q3=makeQuery(id+"F21.opPattern","COPY",BODY,{"derivedFrom":makeQuery(id+"F20.opPattern","COPY",BODY,{"derivedFrom":makeQuery(id+"F18.opPattern","COPY",BODY,{"derivedFrom":makeQuery(id+"F17.opPattern","COPY",BODY,{"derivedFrom":makeQuery(id+"F16.opExtrude","SWEPT_BODY",BODY,{"disambiguationData":[OSD([sQuery(id+"F15.wireOp",EDGE,"E13.bottom"),sQuery(id+"F15.wireOp",EDGE,"E13.top"),sQuery(id+"F15.wireOp",EDGE,"E13.left"),sQuery(id+"F15.wireOp",EDGE,"E13.right"),sQuery(id+"F15.wireOp",EDGE,"E14.bottom"),sQuery(id+"F15.wireOp",EDGE,"E14.top"),sQuery(id+"F15.wireOp",EDGE,"E14.left"),sQuery(id+"F15.wireOp",EDGE,"E14.right"),sQuery(id+"F15.wireOp",EDGE,"E15.MirrorCS"),sQuery(id+"F15.wireOp",EDGE,"E16.MirrorCS"),sQuery(id+"F15.wireOp",EDGE,"E17.MirrorCS"),sQuery(id+"F15.wireOp",EDGE,"E18.MirrorCS"),sQuery(id+"F15.wireOp",EDGE,"E19.MirrorCS"),sQuery(id+"F15.wireOp",EDGE,"E20.MirrorCS"),sQuery(id+"F15.wireOp",EDGE,"E21.MirrorCS"),sQuery(id+"F15.wireOp",EDGE,"E22.MirrorCS"),sQuery(id+"F15.wireOp",EDGE,"E23.MirrorCS"),sQuery(id+"F15.wireOp",EDGE,"E24.MirrorCS"),sQuery(id+"F15.wireOp",EDGE,"E25.MirrorCS"),sQuery(id+"F15.wireOp",EDGE,"E26.MirrorCS")])]}),"instanceName":"1"}),"instanceName":"1"}),"instanceName":"1"}),"instanceName":"1"});
            var Q4;
            Q4=makeQuery(id+"F21.opPattern","COPY",BODY,{"derivedFrom":makeQuery(id+"F20.opPattern","COPY",BODY,{"derivedFrom":makeQuery(id+"F19.opPattern","COPY",BODY,{"derivedFrom":makeQuery(id+"F16.opExtrude","SWEPT_BODY",BODY,{"disambiguationData":[OSD([sQuery(id+"F15.wireOp",EDGE,"E13.bottom"),sQuery(id+"F15.wireOp",EDGE,"E13.top"),sQuery(id+"F15.wireOp",EDGE,"E13.left"),sQuery(id+"F15.wireOp",EDGE,"E13.right"),sQuery(id+"F15.wireOp",EDGE,"E14.bottom"),sQuery(id+"F15.wireOp",EDGE,"E14.top"),sQuery(id+"F15.wireOp",EDGE,"E14.left"),sQuery(id+"F15.wireOp",EDGE,"E14.right"),sQuery(id+"F15.wireOp",EDGE,"E15.MirrorCS"),sQuery(id+"F15.wireOp",EDGE,"E16.MirrorCS"),sQuery(id+"F15.wireOp",EDGE,"E17.MirrorCS"),sQuery(id+"F15.wireOp",EDGE,"E18.MirrorCS"),sQuery(id+"F15.wireOp",EDGE,"E19.MirrorCS"),sQuery(id+"F15.wireOp",EDGE,"E20.MirrorCS"),sQuery(id+"F15.wireOp",EDGE,"E21.MirrorCS"),sQuery(id+"F15.wireOp",EDGE,"E22.MirrorCS"),sQuery(id+"F15.wireOp",EDGE,"E23.MirrorCS"),sQuery(id+"F15.wireOp",EDGE,"E24.MirrorCS"),sQuery(id+"F15.wireOp",EDGE,"E25.MirrorCS"),sQuery(id+"F15.wireOp",EDGE,"E26.MirrorCS")])]}),"instanceName":"1"}),"instanceName":"1"}),"instanceName":"1"});
            var Q5;
            Q5=makeQuery(id+"F21.opPattern","COPY",BODY,{"derivedFrom":makeQuery(id+"F20.opPattern","COPY",BODY,{"derivedFrom":makeQuery(id+"F19.opPattern","COPY",BODY,{"derivedFrom":makeQuery(id+"F17.opPattern","COPY",BODY,{"derivedFrom":makeQuery(id+"F16.opExtrude","SWEPT_BODY",BODY,{"disambiguationData":[OSD([sQuery(id+"F15.wireOp",EDGE,"E13.bottom"),sQuery(id+"F15.wireOp",EDGE,"E13.top"),sQuery(id+"F15.wireOp",EDGE,"E13.left"),sQuery(id+"F15.wireOp",EDGE,"E13.right"),sQuery(id+"F15.wireOp",EDGE,"E14.bottom"),sQuery(id+"F15.wireOp",EDGE,"E14.top"),sQuery(id+"F15.wireOp",EDGE,"E14.left"),sQuery(id+"F15.wireOp",EDGE,"E14.right"),sQuery(id+"F15.wireOp",EDGE,"E15.MirrorCS"),sQuery(id+"F15.wireOp",EDGE,"E16.MirrorCS"),sQuery(id+"F15.wireOp",EDGE,"E17.MirrorCS"),sQuery(id+"F15.wireOp",EDGE,"E18.MirrorCS"),sQuery(id+"F15.wireOp",EDGE,"E19.MirrorCS"),sQuery(id+"F15.wireOp",EDGE,"E20.MirrorCS"),sQuery(id+"F15.wireOp",EDGE,"E21.MirrorCS"),sQuery(id+"F15.wireOp",EDGE,"E22.MirrorCS"),sQuery(id+"F15.wireOp",EDGE,"E23.MirrorCS"),sQuery(id+"F15.wireOp",EDGE,"E24.MirrorCS"),sQuery(id+"F15.wireOp",EDGE,"E25.MirrorCS"),sQuery(id+"F15.wireOp",EDGE,"E26.MirrorCS")])]}),"instanceName":"1"}),"instanceName":"1"}),"instanceName":"1"}),"instanceName":"1"});
            var Q6;
            Q6=makeQuery(id+"F21.opPattern","COPY",BODY,{"derivedFrom":makeQuery(id+"F20.opPattern","COPY",BODY,{"derivedFrom":makeQuery(id+"F19.opPattern","COPY",BODY,{"derivedFrom":makeQuery(id+"F18.opPattern","COPY",BODY,{"derivedFrom":makeQuery(id+"F16.opExtrude","SWEPT_BODY",BODY,{"disambiguationData":[OSD([sQuery(id+"F15.wireOp",EDGE,"E13.bottom"),sQuery(id+"F15.wireOp",EDGE,"E13.top"),sQuery(id+"F15.wireOp",EDGE,"E13.left"),sQuery(id+"F15.wireOp",EDGE,"E13.right"),sQuery(id+"F15.wireOp",EDGE,"E14.bottom"),sQuery(id+"F15.wireOp",EDGE,"E14.top"),sQuery(id+"F15.wireOp",EDGE,"E14.left"),sQuery(id+"F15.wireOp",EDGE,"E14.right"),sQuery(id+"F15.wireOp",EDGE,"E15.MirrorCS"),sQuery(id+"F15.wireOp",EDGE,"E16.MirrorCS"),sQuery(id+"F15.wireOp",EDGE,"E17.MirrorCS"),sQuery(id+"F15.wireOp",EDGE,"E18.MirrorCS"),sQuery(id+"F15.wireOp",EDGE,"E19.MirrorCS"),sQuery(id+"F15.wireOp",EDGE,"E20.MirrorCS"),sQuery(id+"F15.wireOp",EDGE,"E21.MirrorCS"),sQuery(id+"F15.wireOp",EDGE,"E22.MirrorCS"),sQuery(id+"F15.wireOp",EDGE,"E23.MirrorCS"),sQuery(id+"F15.wireOp",EDGE,"E24.MirrorCS"),sQuery(id+"F15.wireOp",EDGE,"E25.MirrorCS"),sQuery(id+"F15.wireOp",EDGE,"E26.MirrorCS")])]}),"instanceName":"1"}),"instanceName":"1"}),"instanceName":"1"}),"instanceName":"1"});
            var Q7;
            Q7=makeQuery(id+"F22.opPattern","COPY",BODY,{"derivedFrom":makeQuery(id+"F21.opPattern","COPY",BODY,{"derivedFrom":makeQuery(id+"F20.opPattern","COPY",BODY,{"derivedFrom":makeQuery(id+"F16.opExtrude","SWEPT_BODY",BODY,{"disambiguationData":[OSD([sQuery(id+"F15.wireOp",EDGE,"E13.bottom"),sQuery(id+"F15.wireOp",EDGE,"E13.top"),sQuery(id+"F15.wireOp",EDGE,"E13.left"),sQuery(id+"F15.wireOp",EDGE,"E13.right"),sQuery(id+"F15.wireOp",EDGE,"E14.bottom"),sQuery(id+"F15.wireOp",EDGE,"E14.top"),sQuery(id+"F15.wireOp",EDGE,"E14.left"),sQuery(id+"F15.wireOp",EDGE,"E14.right"),sQuery(id+"F15.wireOp",EDGE,"E15.MirrorCS"),sQuery(id+"F15.wireOp",EDGE,"E16.MirrorCS"),sQuery(id+"F15.wireOp",EDGE,"E17.MirrorCS"),sQuery(id+"F15.wireOp",EDGE,"E18.MirrorCS"),sQuery(id+"F15.wireOp",EDGE,"E19.MirrorCS"),sQuery(id+"F15.wireOp",EDGE,"E20.MirrorCS"),sQuery(id+"F15.wireOp",EDGE,"E21.MirrorCS"),sQuery(id+"F15.wireOp",EDGE,"E22.MirrorCS"),sQuery(id+"F15.wireOp",EDGE,"E23.MirrorCS"),sQuery(id+"F15.wireOp",EDGE,"E24.MirrorCS"),sQuery(id+"F15.wireOp",EDGE,"E25.MirrorCS"),sQuery(id+"F15.wireOp",EDGE,"E26.MirrorCS")])]}),"instanceName":"1"}),"instanceName":"1"}),"instanceName":"1"});
            var Q8;
            Q8=makeQuery(id+"F22.opPattern","COPY",BODY,{"derivedFrom":makeQuery(id+"F21.opPattern","COPY",BODY,{"derivedFrom":makeQuery(id+"F20.opPattern","COPY",BODY,{"derivedFrom":makeQuery(id+"F17.opPattern","COPY",BODY,{"derivedFrom":makeQuery(id+"F16.opExtrude","SWEPT_BODY",BODY,{"disambiguationData":[OSD([sQuery(id+"F15.wireOp",EDGE,"E13.bottom"),sQuery(id+"F15.wireOp",EDGE,"E13.top"),sQuery(id+"F15.wireOp",EDGE,"E13.left"),sQuery(id+"F15.wireOp",EDGE,"E13.right"),sQuery(id+"F15.wireOp",EDGE,"E14.bottom"),sQuery(id+"F15.wireOp",EDGE,"E14.top"),sQuery(id+"F15.wireOp",EDGE,"E14.left"),sQuery(id+"F15.wireOp",EDGE,"E14.right"),sQuery(id+"F15.wireOp",EDGE,"E15.MirrorCS"),sQuery(id+"F15.wireOp",EDGE,"E16.MirrorCS"),sQuery(id+"F15.wireOp",EDGE,"E17.MirrorCS"),sQuery(id+"F15.wireOp",EDGE,"E18.MirrorCS"),sQuery(id+"F15.wireOp",EDGE,"E19.MirrorCS"),sQuery(id+"F15.wireOp",EDGE,"E20.MirrorCS"),sQuery(id+"F15.wireOp",EDGE,"E21.MirrorCS"),sQuery(id+"F15.wireOp",EDGE,"E22.MirrorCS"),sQuery(id+"F15.wireOp",EDGE,"E23.MirrorCS"),sQuery(id+"F15.wireOp",EDGE,"E24.MirrorCS"),sQuery(id+"F15.wireOp",EDGE,"E25.MirrorCS"),sQuery(id+"F15.wireOp",EDGE,"E26.MirrorCS")])]}),"instanceName":"1"}),"instanceName":"1"}),"instanceName":"1"}),"instanceName":"1"});
            var Q9;
            Q9=makeQuery(id+"F22.opPattern","COPY",BODY,{"derivedFrom":makeQuery(id+"F21.opPattern","COPY",BODY,{"derivedFrom":makeQuery(id+"F20.opPattern","COPY",BODY,{"derivedFrom":makeQuery(id+"F18.opPattern","COPY",BODY,{"derivedFrom":makeQuery(id+"F16.opExtrude","SWEPT_BODY",BODY,{"disambiguationData":[OSD([sQuery(id+"F15.wireOp",EDGE,"E13.bottom"),sQuery(id+"F15.wireOp",EDGE,"E13.top"),sQuery(id+"F15.wireOp",EDGE,"E13.left"),sQuery(id+"F15.wireOp",EDGE,"E13.right"),sQuery(id+"F15.wireOp",EDGE,"E14.bottom"),sQuery(id+"F15.wireOp",EDGE,"E14.top"),sQuery(id+"F15.wireOp",EDGE,"E14.left"),sQuery(id+"F15.wireOp",EDGE,"E14.right"),sQuery(id+"F15.wireOp",EDGE,"E15.MirrorCS"),sQuery(id+"F15.wireOp",EDGE,"E16.MirrorCS"),sQuery(id+"F15.wireOp",EDGE,"E17.MirrorCS"),sQuery(id+"F15.wireOp",EDGE,"E18.MirrorCS"),sQuery(id+"F15.wireOp",EDGE,"E19.MirrorCS"),sQuery(id+"F15.wireOp",EDGE,"E20.MirrorCS"),sQuery(id+"F15.wireOp",EDGE,"E21.MirrorCS"),sQuery(id+"F15.wireOp",EDGE,"E22.MirrorCS"),sQuery(id+"F15.wireOp",EDGE,"E23.MirrorCS"),sQuery(id+"F15.wireOp",EDGE,"E24.MirrorCS"),sQuery(id+"F15.wireOp",EDGE,"E25.MirrorCS"),sQuery(id+"F15.wireOp",EDGE,"E26.MirrorCS")])]}),"instanceName":"1"}),"instanceName":"1"}),"instanceName":"1"}),"instanceName":"1"});
            var Q10;
            Q10=makeQuery(id+"F22.opPattern","COPY",BODY,{"derivedFrom":makeQuery(id+"F21.opPattern","COPY",BODY,{"derivedFrom":makeQuery(id+"F20.opPattern","COPY",BODY,{"derivedFrom":makeQuery(id+"F18.opPattern","COPY",BODY,{"derivedFrom":makeQuery(id+"F17.opPattern","COPY",BODY,{"derivedFrom":makeQuery(id+"F16.opExtrude","SWEPT_BODY",BODY,{"disambiguationData":[OSD([sQuery(id+"F15.wireOp",EDGE,"E13.bottom"),sQuery(id+"F15.wireOp",EDGE,"E13.top"),sQuery(id+"F15.wireOp",EDGE,"E13.left"),sQuery(id+"F15.wireOp",EDGE,"E13.right"),sQuery(id+"F15.wireOp",EDGE,"E14.bottom"),sQuery(id+"F15.wireOp",EDGE,"E14.top"),sQuery(id+"F15.wireOp",EDGE,"E14.left"),sQuery(id+"F15.wireOp",EDGE,"E14.right"),sQuery(id+"F15.wireOp",EDGE,"E15.MirrorCS"),sQuery(id+"F15.wireOp",EDGE,"E16.MirrorCS"),sQuery(id+"F15.wireOp",EDGE,"E17.MirrorCS"),sQuery(id+"F15.wireOp",EDGE,"E18.MirrorCS"),sQuery(id+"F15.wireOp",EDGE,"E19.MirrorCS"),sQuery(id+"F15.wireOp",EDGE,"E20.MirrorCS"),sQuery(id+"F15.wireOp",EDGE,"E21.MirrorCS"),sQuery(id+"F15.wireOp",EDGE,"E22.MirrorCS"),sQuery(id+"F15.wireOp",EDGE,"E23.MirrorCS"),sQuery(id+"F15.wireOp",EDGE,"E24.MirrorCS"),sQuery(id+"F15.wireOp",EDGE,"E25.MirrorCS"),sQuery(id+"F15.wireOp",EDGE,"E26.MirrorCS")])]}),"instanceName":"1"}),"instanceName":"1"}),"instanceName":"1"}),"instanceName":"1"}),"instanceName":"1"});
            var Q11;
            Q11=makeQuery(id+"F22.opPattern","COPY",BODY,{"derivedFrom":makeQuery(id+"F21.opPattern","COPY",BODY,{"derivedFrom":makeQuery(id+"F20.opPattern","COPY",BODY,{"derivedFrom":makeQuery(id+"F19.opPattern","COPY",BODY,{"derivedFrom":makeQuery(id+"F16.opExtrude","SWEPT_BODY",BODY,{"disambiguationData":[OSD([sQuery(id+"F15.wireOp",EDGE,"E13.bottom"),sQuery(id+"F15.wireOp",EDGE,"E13.top"),sQuery(id+"F15.wireOp",EDGE,"E13.left"),sQuery(id+"F15.wireOp",EDGE,"E13.right"),sQuery(id+"F15.wireOp",EDGE,"E14.bottom"),sQuery(id+"F15.wireOp",EDGE,"E14.top"),sQuery(id+"F15.wireOp",EDGE,"E14.left"),sQuery(id+"F15.wireOp",EDGE,"E14.right"),sQuery(id+"F15.wireOp",EDGE,"E15.MirrorCS"),sQuery(id+"F15.wireOp",EDGE,"E16.MirrorCS"),sQuery(id+"F15.wireOp",EDGE,"E17.MirrorCS"),sQuery(id+"F15.wireOp",EDGE,"E18.MirrorCS"),sQuery(id+"F15.wireOp",EDGE,"E19.MirrorCS"),sQuery(id+"F15.wireOp",EDGE,"E20.MirrorCS"),sQuery(id+"F15.wireOp",EDGE,"E21.MirrorCS"),sQuery(id+"F15.wireOp",EDGE,"E22.MirrorCS"),sQuery(id+"F15.wireOp",EDGE,"E23.MirrorCS"),sQuery(id+"F15.wireOp",EDGE,"E24.MirrorCS"),sQuery(id+"F15.wireOp",EDGE,"E25.MirrorCS"),sQuery(id+"F15.wireOp",EDGE,"E26.MirrorCS")])]}),"instanceName":"1"}),"instanceName":"1"}),"instanceName":"1"}),"instanceName":"1"});
            var Q12;
            Q12=makeQuery(id+"F22.opPattern","COPY",BODY,{"derivedFrom":makeQuery(id+"F21.opPattern","COPY",BODY,{"derivedFrom":makeQuery(id+"F20.opPattern","COPY",BODY,{"derivedFrom":makeQuery(id+"F19.opPattern","COPY",BODY,{"derivedFrom":makeQuery(id+"F17.opPattern","COPY",BODY,{"derivedFrom":makeQuery(id+"F16.opExtrude","SWEPT_BODY",BODY,{"disambiguationData":[OSD([sQuery(id+"F15.wireOp",EDGE,"E13.bottom"),sQuery(id+"F15.wireOp",EDGE,"E13.top"),sQuery(id+"F15.wireOp",EDGE,"E13.left"),sQuery(id+"F15.wireOp",EDGE,"E13.right"),sQuery(id+"F15.wireOp",EDGE,"E14.bottom"),sQuery(id+"F15.wireOp",EDGE,"E14.top"),sQuery(id+"F15.wireOp",EDGE,"E14.left"),sQuery(id+"F15.wireOp",EDGE,"E14.right"),sQuery(id+"F15.wireOp",EDGE,"E15.MirrorCS"),sQuery(id+"F15.wireOp",EDGE,"E16.MirrorCS"),sQuery(id+"F15.wireOp",EDGE,"E17.MirrorCS"),sQuery(id+"F15.wireOp",EDGE,"E18.MirrorCS"),sQuery(id+"F15.wireOp",EDGE,"E19.MirrorCS"),sQuery(id+"F15.wireOp",EDGE,"E20.MirrorCS"),sQuery(id+"F15.wireOp",EDGE,"E21.MirrorCS"),sQuery(id+"F15.wireOp",EDGE,"E22.MirrorCS"),sQuery(id+"F15.wireOp",EDGE,"E23.MirrorCS"),sQuery(id+"F15.wireOp",EDGE,"E24.MirrorCS"),sQuery(id+"F15.wireOp",EDGE,"E25.MirrorCS"),sQuery(id+"F15.wireOp",EDGE,"E26.MirrorCS")])]}),"instanceName":"1"}),"instanceName":"1"}),"instanceName":"1"}),"instanceName":"1"}),"instanceName":"1"});
            var Q13;
            Q13=makeQuery(id+"F22.opPattern","COPY",BODY,{"derivedFrom":makeQuery(id+"F21.opPattern","COPY",BODY,{"derivedFrom":makeQuery(id+"F20.opPattern","COPY",BODY,{"derivedFrom":makeQuery(id+"F19.opPattern","COPY",BODY,{"derivedFrom":makeQuery(id+"F18.opPattern","COPY",BODY,{"derivedFrom":makeQuery(id+"F16.opExtrude","SWEPT_BODY",BODY,{"disambiguationData":[OSD([sQuery(id+"F15.wireOp",EDGE,"E13.bottom"),sQuery(id+"F15.wireOp",EDGE,"E13.top"),sQuery(id+"F15.wireOp",EDGE,"E13.left"),sQuery(id+"F15.wireOp",EDGE,"E13.right"),sQuery(id+"F15.wireOp",EDGE,"E14.bottom"),sQuery(id+"F15.wireOp",EDGE,"E14.top"),sQuery(id+"F15.wireOp",EDGE,"E14.left"),sQuery(id+"F15.wireOp",EDGE,"E14.right"),sQuery(id+"F15.wireOp",EDGE,"E15.MirrorCS"),sQuery(id+"F15.wireOp",EDGE,"E16.MirrorCS"),sQuery(id+"F15.wireOp",EDGE,"E17.MirrorCS"),sQuery(id+"F15.wireOp",EDGE,"E18.MirrorCS"),sQuery(id+"F15.wireOp",EDGE,"E19.MirrorCS"),sQuery(id+"F15.wireOp",EDGE,"E20.MirrorCS"),sQuery(id+"F15.wireOp",EDGE,"E21.MirrorCS"),sQuery(id+"F15.wireOp",EDGE,"E22.MirrorCS"),sQuery(id+"F15.wireOp",EDGE,"E23.MirrorCS"),sQuery(id+"F15.wireOp",EDGE,"E24.MirrorCS"),sQuery(id+"F15.wireOp",EDGE,"E25.MirrorCS"),sQuery(id+"F15.wireOp",EDGE,"E26.MirrorCS")])]}),"instanceName":"1"}),"instanceName":"1"}),"instanceName":"1"}),"instanceName":"1"}),"instanceName":"1"});
            var Q14;
            Q14=makeQuery(id+"F23.opPattern","COPY",BODY,{"derivedFrom":makeQuery(id+"F21.opPattern","COPY",BODY,{"derivedFrom":makeQuery(id+"F20.opPattern","COPY",BODY,{"derivedFrom":makeQuery(id+"F16.opExtrude","SWEPT_BODY",BODY,{"disambiguationData":[OSD([sQuery(id+"F15.wireOp",EDGE,"E13.bottom"),sQuery(id+"F15.wireOp",EDGE,"E13.top"),sQuery(id+"F15.wireOp",EDGE,"E13.left"),sQuery(id+"F15.wireOp",EDGE,"E13.right"),sQuery(id+"F15.wireOp",EDGE,"E14.bottom"),sQuery(id+"F15.wireOp",EDGE,"E14.top"),sQuery(id+"F15.wireOp",EDGE,"E14.left"),sQuery(id+"F15.wireOp",EDGE,"E14.right"),sQuery(id+"F15.wireOp",EDGE,"E15.MirrorCS"),sQuery(id+"F15.wireOp",EDGE,"E16.MirrorCS"),sQuery(id+"F15.wireOp",EDGE,"E17.MirrorCS"),sQuery(id+"F15.wireOp",EDGE,"E18.MirrorCS"),sQuery(id+"F15.wireOp",EDGE,"E19.MirrorCS"),sQuery(id+"F15.wireOp",EDGE,"E20.MirrorCS"),sQuery(id+"F15.wireOp",EDGE,"E21.MirrorCS"),sQuery(id+"F15.wireOp",EDGE,"E22.MirrorCS"),sQuery(id+"F15.wireOp",EDGE,"E23.MirrorCS"),sQuery(id+"F15.wireOp",EDGE,"E24.MirrorCS"),sQuery(id+"F15.wireOp",EDGE,"E25.MirrorCS"),sQuery(id+"F15.wireOp",EDGE,"E26.MirrorCS")])]}),"instanceName":"1"}),"instanceName":"1"}),"instanceName":"1"});
            var Q15;
            Q15=makeQuery(id+"F23.opPattern","COPY",BODY,{"derivedFrom":makeQuery(id+"F21.opPattern","COPY",BODY,{"derivedFrom":makeQuery(id+"F20.opPattern","COPY",BODY,{"derivedFrom":makeQuery(id+"F17.opPattern","COPY",BODY,{"derivedFrom":makeQuery(id+"F16.opExtrude","SWEPT_BODY",BODY,{"disambiguationData":[OSD([sQuery(id+"F15.wireOp",EDGE,"E13.bottom"),sQuery(id+"F15.wireOp",EDGE,"E13.top"),sQuery(id+"F15.wireOp",EDGE,"E13.left"),sQuery(id+"F15.wireOp",EDGE,"E13.right"),sQuery(id+"F15.wireOp",EDGE,"E14.bottom"),sQuery(id+"F15.wireOp",EDGE,"E14.top"),sQuery(id+"F15.wireOp",EDGE,"E14.left"),sQuery(id+"F15.wireOp",EDGE,"E14.right"),sQuery(id+"F15.wireOp",EDGE,"E15.MirrorCS"),sQuery(id+"F15.wireOp",EDGE,"E16.MirrorCS"),sQuery(id+"F15.wireOp",EDGE,"E17.MirrorCS"),sQuery(id+"F15.wireOp",EDGE,"E18.MirrorCS"),sQuery(id+"F15.wireOp",EDGE,"E19.MirrorCS"),sQuery(id+"F15.wireOp",EDGE,"E20.MirrorCS"),sQuery(id+"F15.wireOp",EDGE,"E21.MirrorCS"),sQuery(id+"F15.wireOp",EDGE,"E22.MirrorCS"),sQuery(id+"F15.wireOp",EDGE,"E23.MirrorCS"),sQuery(id+"F15.wireOp",EDGE,"E24.MirrorCS"),sQuery(id+"F15.wireOp",EDGE,"E25.MirrorCS"),sQuery(id+"F15.wireOp",EDGE,"E26.MirrorCS")])]}),"instanceName":"1"}),"instanceName":"1"}),"instanceName":"1"}),"instanceName":"1"});
            var Q16;
            Q16=makeQuery(id+"F23.opPattern","COPY",BODY,{"derivedFrom":makeQuery(id+"F21.opPattern","COPY",BODY,{"derivedFrom":makeQuery(id+"F20.opPattern","COPY",BODY,{"derivedFrom":makeQuery(id+"F18.opPattern","COPY",BODY,{"derivedFrom":makeQuery(id+"F16.opExtrude","SWEPT_BODY",BODY,{"disambiguationData":[OSD([sQuery(id+"F15.wireOp",EDGE,"E13.bottom"),sQuery(id+"F15.wireOp",EDGE,"E13.top"),sQuery(id+"F15.wireOp",EDGE,"E13.left"),sQuery(id+"F15.wireOp",EDGE,"E13.right"),sQuery(id+"F15.wireOp",EDGE,"E14.bottom"),sQuery(id+"F15.wireOp",EDGE,"E14.top"),sQuery(id+"F15.wireOp",EDGE,"E14.left"),sQuery(id+"F15.wireOp",EDGE,"E14.right"),sQuery(id+"F15.wireOp",EDGE,"E15.MirrorCS"),sQuery(id+"F15.wireOp",EDGE,"E16.MirrorCS"),sQuery(id+"F15.wireOp",EDGE,"E17.MirrorCS"),sQuery(id+"F15.wireOp",EDGE,"E18.MirrorCS"),sQuery(id+"F15.wireOp",EDGE,"E19.MirrorCS"),sQuery(id+"F15.wireOp",EDGE,"E20.MirrorCS"),sQuery(id+"F15.wireOp",EDGE,"E21.MirrorCS"),sQuery(id+"F15.wireOp",EDGE,"E22.MirrorCS"),sQuery(id+"F15.wireOp",EDGE,"E23.MirrorCS"),sQuery(id+"F15.wireOp",EDGE,"E24.MirrorCS"),sQuery(id+"F15.wireOp",EDGE,"E25.MirrorCS"),sQuery(id+"F15.wireOp",EDGE,"E26.MirrorCS")])]}),"instanceName":"1"}),"instanceName":"1"}),"instanceName":"1"}),"instanceName":"1"});
            var Q17;
            Q17=makeQuery(id+"F23.opPattern","COPY",BODY,{"derivedFrom":makeQuery(id+"F21.opPattern","COPY",BODY,{"derivedFrom":makeQuery(id+"F20.opPattern","COPY",BODY,{"derivedFrom":makeQuery(id+"F18.opPattern","COPY",BODY,{"derivedFrom":makeQuery(id+"F17.opPattern","COPY",BODY,{"derivedFrom":makeQuery(id+"F16.opExtrude","SWEPT_BODY",BODY,{"disambiguationData":[OSD([sQuery(id+"F15.wireOp",EDGE,"E13.bottom"),sQuery(id+"F15.wireOp",EDGE,"E13.top"),sQuery(id+"F15.wireOp",EDGE,"E13.left"),sQuery(id+"F15.wireOp",EDGE,"E13.right"),sQuery(id+"F15.wireOp",EDGE,"E14.bottom"),sQuery(id+"F15.wireOp",EDGE,"E14.top"),sQuery(id+"F15.wireOp",EDGE,"E14.left"),sQuery(id+"F15.wireOp",EDGE,"E14.right"),sQuery(id+"F15.wireOp",EDGE,"E15.MirrorCS"),sQuery(id+"F15.wireOp",EDGE,"E16.MirrorCS"),sQuery(id+"F15.wireOp",EDGE,"E17.MirrorCS"),sQuery(id+"F15.wireOp",EDGE,"E18.MirrorCS"),sQuery(id+"F15.wireOp",EDGE,"E19.MirrorCS"),sQuery(id+"F15.wireOp",EDGE,"E20.MirrorCS"),sQuery(id+"F15.wireOp",EDGE,"E21.MirrorCS"),sQuery(id+"F15.wireOp",EDGE,"E22.MirrorCS"),sQuery(id+"F15.wireOp",EDGE,"E23.MirrorCS"),sQuery(id+"F15.wireOp",EDGE,"E24.MirrorCS"),sQuery(id+"F15.wireOp",EDGE,"E25.MirrorCS"),sQuery(id+"F15.wireOp",EDGE,"E26.MirrorCS")])]}),"instanceName":"1"}),"instanceName":"1"}),"instanceName":"1"}),"instanceName":"1"}),"instanceName":"1"});
            var Q18;
            Q18=makeQuery(id+"F23.opPattern","COPY",BODY,{"derivedFrom":makeQuery(id+"F21.opPattern","COPY",BODY,{"derivedFrom":makeQuery(id+"F20.opPattern","COPY",BODY,{"derivedFrom":makeQuery(id+"F19.opPattern","COPY",BODY,{"derivedFrom":makeQuery(id+"F16.opExtrude","SWEPT_BODY",BODY,{"disambiguationData":[OSD([sQuery(id+"F15.wireOp",EDGE,"E13.bottom"),sQuery(id+"F15.wireOp",EDGE,"E13.top"),sQuery(id+"F15.wireOp",EDGE,"E13.left"),sQuery(id+"F15.wireOp",EDGE,"E13.right"),sQuery(id+"F15.wireOp",EDGE,"E14.bottom"),sQuery(id+"F15.wireOp",EDGE,"E14.top"),sQuery(id+"F15.wireOp",EDGE,"E14.left"),sQuery(id+"F15.wireOp",EDGE,"E14.right"),sQuery(id+"F15.wireOp",EDGE,"E15.MirrorCS"),sQuery(id+"F15.wireOp",EDGE,"E16.MirrorCS"),sQuery(id+"F15.wireOp",EDGE,"E17.MirrorCS"),sQuery(id+"F15.wireOp",EDGE,"E18.MirrorCS"),sQuery(id+"F15.wireOp",EDGE,"E19.MirrorCS"),sQuery(id+"F15.wireOp",EDGE,"E20.MirrorCS"),sQuery(id+"F15.wireOp",EDGE,"E21.MirrorCS"),sQuery(id+"F15.wireOp",EDGE,"E22.MirrorCS"),sQuery(id+"F15.wireOp",EDGE,"E23.MirrorCS"),sQuery(id+"F15.wireOp",EDGE,"E24.MirrorCS"),sQuery(id+"F15.wireOp",EDGE,"E25.MirrorCS"),sQuery(id+"F15.wireOp",EDGE,"E26.MirrorCS")])]}),"instanceName":"1"}),"instanceName":"1"}),"instanceName":"1"}),"instanceName":"1"});
            var Q19;
            Q19=makeQuery(id+"F23.opPattern","COPY",BODY,{"derivedFrom":makeQuery(id+"F21.opPattern","COPY",BODY,{"derivedFrom":makeQuery(id+"F20.opPattern","COPY",BODY,{"derivedFrom":makeQuery(id+"F19.opPattern","COPY",BODY,{"derivedFrom":makeQuery(id+"F17.opPattern","COPY",BODY,{"derivedFrom":makeQuery(id+"F16.opExtrude","SWEPT_BODY",BODY,{"disambiguationData":[OSD([sQuery(id+"F15.wireOp",EDGE,"E13.bottom"),sQuery(id+"F15.wireOp",EDGE,"E13.top"),sQuery(id+"F15.wireOp",EDGE,"E13.left"),sQuery(id+"F15.wireOp",EDGE,"E13.right"),sQuery(id+"F15.wireOp",EDGE,"E14.bottom"),sQuery(id+"F15.wireOp",EDGE,"E14.top"),sQuery(id+"F15.wireOp",EDGE,"E14.left"),sQuery(id+"F15.wireOp",EDGE,"E14.right"),sQuery(id+"F15.wireOp",EDGE,"E15.MirrorCS"),sQuery(id+"F15.wireOp",EDGE,"E16.MirrorCS"),sQuery(id+"F15.wireOp",EDGE,"E17.MirrorCS"),sQuery(id+"F15.wireOp",EDGE,"E18.MirrorCS"),sQuery(id+"F15.wireOp",EDGE,"E19.MirrorCS"),sQuery(id+"F15.wireOp",EDGE,"E20.MirrorCS"),sQuery(id+"F15.wireOp",EDGE,"E21.MirrorCS"),sQuery(id+"F15.wireOp",EDGE,"E22.MirrorCS"),sQuery(id+"F15.wireOp",EDGE,"E23.MirrorCS"),sQuery(id+"F15.wireOp",EDGE,"E24.MirrorCS"),sQuery(id+"F15.wireOp",EDGE,"E25.MirrorCS"),sQuery(id+"F15.wireOp",EDGE,"E26.MirrorCS")])]}),"instanceName":"1"}),"instanceName":"1"}),"instanceName":"1"}),"instanceName":"1"}),"instanceName":"1"});
            var Q20;
            Q20=makeQuery(id+"F23.opPattern","COPY",BODY,{"derivedFrom":makeQuery(id+"F21.opPattern","COPY",BODY,{"derivedFrom":makeQuery(id+"F20.opPattern","COPY",BODY,{"derivedFrom":makeQuery(id+"F19.opPattern","COPY",BODY,{"derivedFrom":makeQuery(id+"F18.opPattern","COPY",BODY,{"derivedFrom":makeQuery(id+"F16.opExtrude","SWEPT_BODY",BODY,{"disambiguationData":[OSD([sQuery(id+"F15.wireOp",EDGE,"E13.bottom"),sQuery(id+"F15.wireOp",EDGE,"E13.top"),sQuery(id+"F15.wireOp",EDGE,"E13.left"),sQuery(id+"F15.wireOp",EDGE,"E13.right"),sQuery(id+"F15.wireOp",EDGE,"E14.bottom"),sQuery(id+"F15.wireOp",EDGE,"E14.top"),sQuery(id+"F15.wireOp",EDGE,"E14.left"),sQuery(id+"F15.wireOp",EDGE,"E14.right"),sQuery(id+"F15.wireOp",EDGE,"E15.MirrorCS"),sQuery(id+"F15.wireOp",EDGE,"E16.MirrorCS"),sQuery(id+"F15.wireOp",EDGE,"E17.MirrorCS"),sQuery(id+"F15.wireOp",EDGE,"E18.MirrorCS"),sQuery(id+"F15.wireOp",EDGE,"E19.MirrorCS"),sQuery(id+"F15.wireOp",EDGE,"E20.MirrorCS"),sQuery(id+"F15.wireOp",EDGE,"E21.MirrorCS"),sQuery(id+"F15.wireOp",EDGE,"E22.MirrorCS"),sQuery(id+"F15.wireOp",EDGE,"E23.MirrorCS"),sQuery(id+"F15.wireOp",EDGE,"E24.MirrorCS"),sQuery(id+"F15.wireOp",EDGE,"E25.MirrorCS"),sQuery(id+"F15.wireOp",EDGE,"E26.MirrorCS")])]}),"instanceName":"1"}),"instanceName":"1"}),"instanceName":"1"}),"instanceName":"1"}),"instanceName":"1"});
            var Q21;
            Q21=makeQuery(id+"F23.opPattern","COPY",BODY,{"derivedFrom":makeQuery(id+"F22.opPattern","COPY",BODY,{"derivedFrom":makeQuery(id+"F21.opPattern","COPY",BODY,{"derivedFrom":makeQuery(id+"F20.opPattern","COPY",BODY,{"derivedFrom":makeQuery(id+"F16.opExtrude","SWEPT_BODY",BODY,{"disambiguationData":[OSD([sQuery(id+"F15.wireOp",EDGE,"E13.bottom"),sQuery(id+"F15.wireOp",EDGE,"E13.top"),sQuery(id+"F15.wireOp",EDGE,"E13.left"),sQuery(id+"F15.wireOp",EDGE,"E13.right"),sQuery(id+"F15.wireOp",EDGE,"E14.bottom"),sQuery(id+"F15.wireOp",EDGE,"E14.top"),sQuery(id+"F15.wireOp",EDGE,"E14.left"),sQuery(id+"F15.wireOp",EDGE,"E14.right"),sQuery(id+"F15.wireOp",EDGE,"E15.MirrorCS"),sQuery(id+"F15.wireOp",EDGE,"E16.MirrorCS"),sQuery(id+"F15.wireOp",EDGE,"E17.MirrorCS"),sQuery(id+"F15.wireOp",EDGE,"E18.MirrorCS"),sQuery(id+"F15.wireOp",EDGE,"E19.MirrorCS"),sQuery(id+"F15.wireOp",EDGE,"E20.MirrorCS"),sQuery(id+"F15.wireOp",EDGE,"E21.MirrorCS"),sQuery(id+"F15.wireOp",EDGE,"E22.MirrorCS"),sQuery(id+"F15.wireOp",EDGE,"E23.MirrorCS"),sQuery(id+"F15.wireOp",EDGE,"E24.MirrorCS"),sQuery(id+"F15.wireOp",EDGE,"E25.MirrorCS"),sQuery(id+"F15.wireOp",EDGE,"E26.MirrorCS")])]}),"instanceName":"1"}),"instanceName":"1"}),"instanceName":"1"}),"instanceName":"1"});
            var Q22;
            Q22=makeQuery(id+"F23.opPattern","COPY",BODY,{"derivedFrom":makeQuery(id+"F22.opPattern","COPY",BODY,{"derivedFrom":makeQuery(id+"F21.opPattern","COPY",BODY,{"derivedFrom":makeQuery(id+"F20.opPattern","COPY",BODY,{"derivedFrom":makeQuery(id+"F17.opPattern","COPY",BODY,{"derivedFrom":makeQuery(id+"F16.opExtrude","SWEPT_BODY",BODY,{"disambiguationData":[OSD([sQuery(id+"F15.wireOp",EDGE,"E13.bottom"),sQuery(id+"F15.wireOp",EDGE,"E13.top"),sQuery(id+"F15.wireOp",EDGE,"E13.left"),sQuery(id+"F15.wireOp",EDGE,"E13.right"),sQuery(id+"F15.wireOp",EDGE,"E14.bottom"),sQuery(id+"F15.wireOp",EDGE,"E14.top"),sQuery(id+"F15.wireOp",EDGE,"E14.left"),sQuery(id+"F15.wireOp",EDGE,"E14.right"),sQuery(id+"F15.wireOp",EDGE,"E15.MirrorCS"),sQuery(id+"F15.wireOp",EDGE,"E16.MirrorCS"),sQuery(id+"F15.wireOp",EDGE,"E17.MirrorCS"),sQuery(id+"F15.wireOp",EDGE,"E18.MirrorCS"),sQuery(id+"F15.wireOp",EDGE,"E19.MirrorCS"),sQuery(id+"F15.wireOp",EDGE,"E20.MirrorCS"),sQuery(id+"F15.wireOp",EDGE,"E21.MirrorCS"),sQuery(id+"F15.wireOp",EDGE,"E22.MirrorCS"),sQuery(id+"F15.wireOp",EDGE,"E23.MirrorCS"),sQuery(id+"F15.wireOp",EDGE,"E24.MirrorCS"),sQuery(id+"F15.wireOp",EDGE,"E25.MirrorCS"),sQuery(id+"F15.wireOp",EDGE,"E26.MirrorCS")])]}),"instanceName":"1"}),"instanceName":"1"}),"instanceName":"1"}),"instanceName":"1"}),"instanceName":"1"});
            var Q23;
            Q23=makeQuery(id+"F23.opPattern","COPY",BODY,{"derivedFrom":makeQuery(id+"F22.opPattern","COPY",BODY,{"derivedFrom":makeQuery(id+"F21.opPattern","COPY",BODY,{"derivedFrom":makeQuery(id+"F20.opPattern","COPY",BODY,{"derivedFrom":makeQuery(id+"F18.opPattern","COPY",BODY,{"derivedFrom":makeQuery(id+"F16.opExtrude","SWEPT_BODY",BODY,{"disambiguationData":[OSD([sQuery(id+"F15.wireOp",EDGE,"E13.bottom"),sQuery(id+"F15.wireOp",EDGE,"E13.top"),sQuery(id+"F15.wireOp",EDGE,"E13.left"),sQuery(id+"F15.wireOp",EDGE,"E13.right"),sQuery(id+"F15.wireOp",EDGE,"E14.bottom"),sQuery(id+"F15.wireOp",EDGE,"E14.top"),sQuery(id+"F15.wireOp",EDGE,"E14.left"),sQuery(id+"F15.wireOp",EDGE,"E14.right"),sQuery(id+"F15.wireOp",EDGE,"E15.MirrorCS"),sQuery(id+"F15.wireOp",EDGE,"E16.MirrorCS"),sQuery(id+"F15.wireOp",EDGE,"E17.MirrorCS"),sQuery(id+"F15.wireOp",EDGE,"E18.MirrorCS"),sQuery(id+"F15.wireOp",EDGE,"E19.MirrorCS"),sQuery(id+"F15.wireOp",EDGE,"E20.MirrorCS"),sQuery(id+"F15.wireOp",EDGE,"E21.MirrorCS"),sQuery(id+"F15.wireOp",EDGE,"E22.MirrorCS"),sQuery(id+"F15.wireOp",EDGE,"E23.MirrorCS"),sQuery(id+"F15.wireOp",EDGE,"E24.MirrorCS"),sQuery(id+"F15.wireOp",EDGE,"E25.MirrorCS"),sQuery(id+"F15.wireOp",EDGE,"E26.MirrorCS")])]}),"instanceName":"1"}),"instanceName":"1"}),"instanceName":"1"}),"instanceName":"1"}),"instanceName":"1"});
            var Q24;
            Q24=makeQuery(id+"F23.opPattern","COPY",BODY,{"derivedFrom":makeQuery(id+"F22.opPattern","COPY",BODY,{"derivedFrom":makeQuery(id+"F21.opPattern","COPY",BODY,{"derivedFrom":makeQuery(id+"F20.opPattern","COPY",BODY,{"derivedFrom":makeQuery(id+"F18.opPattern","COPY",BODY,{"derivedFrom":makeQuery(id+"F17.opPattern","COPY",BODY,{"derivedFrom":makeQuery(id+"F16.opExtrude","SWEPT_BODY",BODY,{"disambiguationData":[OSD([sQuery(id+"F15.wireOp",EDGE,"E13.bottom"),sQuery(id+"F15.wireOp",EDGE,"E13.top"),sQuery(id+"F15.wireOp",EDGE,"E13.left"),sQuery(id+"F15.wireOp",EDGE,"E13.right"),sQuery(id+"F15.wireOp",EDGE,"E14.bottom"),sQuery(id+"F15.wireOp",EDGE,"E14.top"),sQuery(id+"F15.wireOp",EDGE,"E14.left"),sQuery(id+"F15.wireOp",EDGE,"E14.right"),sQuery(id+"F15.wireOp",EDGE,"E15.MirrorCS"),sQuery(id+"F15.wireOp",EDGE,"E16.MirrorCS"),sQuery(id+"F15.wireOp",EDGE,"E17.MirrorCS"),sQuery(id+"F15.wireOp",EDGE,"E18.MirrorCS"),sQuery(id+"F15.wireOp",EDGE,"E19.MirrorCS"),sQuery(id+"F15.wireOp",EDGE,"E20.MirrorCS"),sQuery(id+"F15.wireOp",EDGE,"E21.MirrorCS"),sQuery(id+"F15.wireOp",EDGE,"E22.MirrorCS"),sQuery(id+"F15.wireOp",EDGE,"E23.MirrorCS"),sQuery(id+"F15.wireOp",EDGE,"E24.MirrorCS"),sQuery(id+"F15.wireOp",EDGE,"E25.MirrorCS"),sQuery(id+"F15.wireOp",EDGE,"E26.MirrorCS")])]}),"instanceName":"1"}),"instanceName":"1"}),"instanceName":"1"}),"instanceName":"1"}),"instanceName":"1"}),"instanceName":"1"});
            var Q25;
            Q25=makeQuery(id+"F23.opPattern","COPY",BODY,{"derivedFrom":makeQuery(id+"F22.opPattern","COPY",BODY,{"derivedFrom":makeQuery(id+"F21.opPattern","COPY",BODY,{"derivedFrom":makeQuery(id+"F20.opPattern","COPY",BODY,{"derivedFrom":makeQuery(id+"F19.opPattern","COPY",BODY,{"derivedFrom":makeQuery(id+"F16.opExtrude","SWEPT_BODY",BODY,{"disambiguationData":[OSD([sQuery(id+"F15.wireOp",EDGE,"E13.bottom"),sQuery(id+"F15.wireOp",EDGE,"E13.top"),sQuery(id+"F15.wireOp",EDGE,"E13.left"),sQuery(id+"F15.wireOp",EDGE,"E13.right"),sQuery(id+"F15.wireOp",EDGE,"E14.bottom"),sQuery(id+"F15.wireOp",EDGE,"E14.top"),sQuery(id+"F15.wireOp",EDGE,"E14.left"),sQuery(id+"F15.wireOp",EDGE,"E14.right"),sQuery(id+"F15.wireOp",EDGE,"E15.MirrorCS"),sQuery(id+"F15.wireOp",EDGE,"E16.MirrorCS"),sQuery(id+"F15.wireOp",EDGE,"E17.MirrorCS"),sQuery(id+"F15.wireOp",EDGE,"E18.MirrorCS"),sQuery(id+"F15.wireOp",EDGE,"E19.MirrorCS"),sQuery(id+"F15.wireOp",EDGE,"E20.MirrorCS"),sQuery(id+"F15.wireOp",EDGE,"E21.MirrorCS"),sQuery(id+"F15.wireOp",EDGE,"E22.MirrorCS"),sQuery(id+"F15.wireOp",EDGE,"E23.MirrorCS"),sQuery(id+"F15.wireOp",EDGE,"E24.MirrorCS"),sQuery(id+"F15.wireOp",EDGE,"E25.MirrorCS"),sQuery(id+"F15.wireOp",EDGE,"E26.MirrorCS")])]}),"instanceName":"1"}),"instanceName":"1"}),"instanceName":"1"}),"instanceName":"1"}),"instanceName":"1"});
            var Q26;
            Q26=makeQuery(id+"F23.opPattern","COPY",BODY,{"derivedFrom":makeQuery(id+"F22.opPattern","COPY",BODY,{"derivedFrom":makeQuery(id+"F21.opPattern","COPY",BODY,{"derivedFrom":makeQuery(id+"F20.opPattern","COPY",BODY,{"derivedFrom":makeQuery(id+"F19.opPattern","COPY",BODY,{"derivedFrom":makeQuery(id+"F17.opPattern","COPY",BODY,{"derivedFrom":makeQuery(id+"F16.opExtrude","SWEPT_BODY",BODY,{"disambiguationData":[OSD([sQuery(id+"F15.wireOp",EDGE,"E13.bottom"),sQuery(id+"F15.wireOp",EDGE,"E13.top"),sQuery(id+"F15.wireOp",EDGE,"E13.left"),sQuery(id+"F15.wireOp",EDGE,"E13.right"),sQuery(id+"F15.wireOp",EDGE,"E14.bottom"),sQuery(id+"F15.wireOp",EDGE,"E14.top"),sQuery(id+"F15.wireOp",EDGE,"E14.left"),sQuery(id+"F15.wireOp",EDGE,"E14.right"),sQuery(id+"F15.wireOp",EDGE,"E15.MirrorCS"),sQuery(id+"F15.wireOp",EDGE,"E16.MirrorCS"),sQuery(id+"F15.wireOp",EDGE,"E17.MirrorCS"),sQuery(id+"F15.wireOp",EDGE,"E18.MirrorCS"),sQuery(id+"F15.wireOp",EDGE,"E19.MirrorCS"),sQuery(id+"F15.wireOp",EDGE,"E20.MirrorCS"),sQuery(id+"F15.wireOp",EDGE,"E21.MirrorCS"),sQuery(id+"F15.wireOp",EDGE,"E22.MirrorCS"),sQuery(id+"F15.wireOp",EDGE,"E23.MirrorCS"),sQuery(id+"F15.wireOp",EDGE,"E24.MirrorCS"),sQuery(id+"F15.wireOp",EDGE,"E25.MirrorCS"),sQuery(id+"F15.wireOp",EDGE,"E26.MirrorCS")])]}),"instanceName":"1"}),"instanceName":"1"}),"instanceName":"1"}),"instanceName":"1"}),"instanceName":"1"}),"instanceName":"1"});
            var Q27;
            Q27=makeQuery(id+"F23.opPattern","COPY",BODY,{"derivedFrom":makeQuery(id+"F22.opPattern","COPY",BODY,{"derivedFrom":makeQuery(id+"F21.opPattern","COPY",BODY,{"derivedFrom":makeQuery(id+"F20.opPattern","COPY",BODY,{"derivedFrom":makeQuery(id+"F19.opPattern","COPY",BODY,{"derivedFrom":makeQuery(id+"F18.opPattern","COPY",BODY,{"derivedFrom":makeQuery(id+"F16.opExtrude","SWEPT_BODY",BODY,{"disambiguationData":[OSD([sQuery(id+"F15.wireOp",EDGE,"E13.bottom"),sQuery(id+"F15.wireOp",EDGE,"E13.top"),sQuery(id+"F15.wireOp",EDGE,"E13.left"),sQuery(id+"F15.wireOp",EDGE,"E13.right"),sQuery(id+"F15.wireOp",EDGE,"E14.bottom"),sQuery(id+"F15.wireOp",EDGE,"E14.top"),sQuery(id+"F15.wireOp",EDGE,"E14.left"),sQuery(id+"F15.wireOp",EDGE,"E14.right"),sQuery(id+"F15.wireOp",EDGE,"E15.MirrorCS"),sQuery(id+"F15.wireOp",EDGE,"E16.MirrorCS"),sQuery(id+"F15.wireOp",EDGE,"E17.MirrorCS"),sQuery(id+"F15.wireOp",EDGE,"E18.MirrorCS"),sQuery(id+"F15.wireOp",EDGE,"E19.MirrorCS"),sQuery(id+"F15.wireOp",EDGE,"E20.MirrorCS"),sQuery(id+"F15.wireOp",EDGE,"E21.MirrorCS"),sQuery(id+"F15.wireOp",EDGE,"E22.MirrorCS"),sQuery(id+"F15.wireOp",EDGE,"E23.MirrorCS"),sQuery(id+"F15.wireOp",EDGE,"E24.MirrorCS"),sQuery(id+"F15.wireOp",EDGE,"E25.MirrorCS"),sQuery(id+"F15.wireOp",EDGE,"E26.MirrorCS")])]}),"instanceName":"1"}),"instanceName":"1"}),"instanceName":"1"}),"instanceName":"1"}),"instanceName":"1"}),"instanceName":"1"});
            var Q28;
            Q28=makeQuery(id+"F24.opPattern","COPY",BODY,{"derivedFrom":makeQuery(id+"F21.opPattern","COPY",BODY,{"derivedFrom":makeQuery(id+"F20.opPattern","COPY",BODY,{"derivedFrom":makeQuery(id+"F16.opExtrude","SWEPT_BODY",BODY,{"disambiguationData":[OSD([sQuery(id+"F15.wireOp",EDGE,"E13.bottom"),sQuery(id+"F15.wireOp",EDGE,"E13.top"),sQuery(id+"F15.wireOp",EDGE,"E13.left"),sQuery(id+"F15.wireOp",EDGE,"E13.right"),sQuery(id+"F15.wireOp",EDGE,"E14.bottom"),sQuery(id+"F15.wireOp",EDGE,"E14.top"),sQuery(id+"F15.wireOp",EDGE,"E14.left"),sQuery(id+"F15.wireOp",EDGE,"E14.right"),sQuery(id+"F15.wireOp",EDGE,"E15.MirrorCS"),sQuery(id+"F15.wireOp",EDGE,"E16.MirrorCS"),sQuery(id+"F15.wireOp",EDGE,"E17.MirrorCS"),sQuery(id+"F15.wireOp",EDGE,"E18.MirrorCS"),sQuery(id+"F15.wireOp",EDGE,"E19.MirrorCS"),sQuery(id+"F15.wireOp",EDGE,"E20.MirrorCS"),sQuery(id+"F15.wireOp",EDGE,"E21.MirrorCS"),sQuery(id+"F15.wireOp",EDGE,"E22.MirrorCS"),sQuery(id+"F15.wireOp",EDGE,"E23.MirrorCS"),sQuery(id+"F15.wireOp",EDGE,"E24.MirrorCS"),sQuery(id+"F15.wireOp",EDGE,"E25.MirrorCS"),sQuery(id+"F15.wireOp",EDGE,"E26.MirrorCS")])]}),"instanceName":"1"}),"instanceName":"1"}),"instanceName":"1"});
            var Q29;
            Q29=makeQuery(id+"F24.opPattern","COPY",BODY,{"derivedFrom":makeQuery(id+"F21.opPattern","COPY",BODY,{"derivedFrom":makeQuery(id+"F20.opPattern","COPY",BODY,{"derivedFrom":makeQuery(id+"F17.opPattern","COPY",BODY,{"derivedFrom":makeQuery(id+"F16.opExtrude","SWEPT_BODY",BODY,{"disambiguationData":[OSD([sQuery(id+"F15.wireOp",EDGE,"E13.bottom"),sQuery(id+"F15.wireOp",EDGE,"E13.top"),sQuery(id+"F15.wireOp",EDGE,"E13.left"),sQuery(id+"F15.wireOp",EDGE,"E13.right"),sQuery(id+"F15.wireOp",EDGE,"E14.bottom"),sQuery(id+"F15.wireOp",EDGE,"E14.top"),sQuery(id+"F15.wireOp",EDGE,"E14.left"),sQuery(id+"F15.wireOp",EDGE,"E14.right"),sQuery(id+"F15.wireOp",EDGE,"E15.MirrorCS"),sQuery(id+"F15.wireOp",EDGE,"E16.MirrorCS"),sQuery(id+"F15.wireOp",EDGE,"E17.MirrorCS"),sQuery(id+"F15.wireOp",EDGE,"E18.MirrorCS"),sQuery(id+"F15.wireOp",EDGE,"E19.MirrorCS"),sQuery(id+"F15.wireOp",EDGE,"E20.MirrorCS"),sQuery(id+"F15.wireOp",EDGE,"E21.MirrorCS"),sQuery(id+"F15.wireOp",EDGE,"E22.MirrorCS"),sQuery(id+"F15.wireOp",EDGE,"E23.MirrorCS"),sQuery(id+"F15.wireOp",EDGE,"E24.MirrorCS"),sQuery(id+"F15.wireOp",EDGE,"E25.MirrorCS"),sQuery(id+"F15.wireOp",EDGE,"E26.MirrorCS")])]}),"instanceName":"1"}),"instanceName":"1"}),"instanceName":"1"}),"instanceName":"1"});
            var Q30;
            Q30=makeQuery(id+"F24.opPattern","COPY",BODY,{"derivedFrom":makeQuery(id+"F21.opPattern","COPY",BODY,{"derivedFrom":makeQuery(id+"F20.opPattern","COPY",BODY,{"derivedFrom":makeQuery(id+"F18.opPattern","COPY",BODY,{"derivedFrom":makeQuery(id+"F16.opExtrude","SWEPT_BODY",BODY,{"disambiguationData":[OSD([sQuery(id+"F15.wireOp",EDGE,"E13.bottom"),sQuery(id+"F15.wireOp",EDGE,"E13.top"),sQuery(id+"F15.wireOp",EDGE,"E13.left"),sQuery(id+"F15.wireOp",EDGE,"E13.right"),sQuery(id+"F15.wireOp",EDGE,"E14.bottom"),sQuery(id+"F15.wireOp",EDGE,"E14.top"),sQuery(id+"F15.wireOp",EDGE,"E14.left"),sQuery(id+"F15.wireOp",EDGE,"E14.right"),sQuery(id+"F15.wireOp",EDGE,"E15.MirrorCS"),sQuery(id+"F15.wireOp",EDGE,"E16.MirrorCS"),sQuery(id+"F15.wireOp",EDGE,"E17.MirrorCS"),sQuery(id+"F15.wireOp",EDGE,"E18.MirrorCS"),sQuery(id+"F15.wireOp",EDGE,"E19.MirrorCS"),sQuery(id+"F15.wireOp",EDGE,"E20.MirrorCS"),sQuery(id+"F15.wireOp",EDGE,"E21.MirrorCS"),sQuery(id+"F15.wireOp",EDGE,"E22.MirrorCS"),sQuery(id+"F15.wireOp",EDGE,"E23.MirrorCS"),sQuery(id+"F15.wireOp",EDGE,"E24.MirrorCS"),sQuery(id+"F15.wireOp",EDGE,"E25.MirrorCS"),sQuery(id+"F15.wireOp",EDGE,"E26.MirrorCS")])]}),"instanceName":"1"}),"instanceName":"1"}),"instanceName":"1"}),"instanceName":"1"});
            var Q31;
            Q31=makeQuery(id+"F24.opPattern","COPY",BODY,{"derivedFrom":makeQuery(id+"F21.opPattern","COPY",BODY,{"derivedFrom":makeQuery(id+"F20.opPattern","COPY",BODY,{"derivedFrom":makeQuery(id+"F18.opPattern","COPY",BODY,{"derivedFrom":makeQuery(id+"F17.opPattern","COPY",BODY,{"derivedFrom":makeQuery(id+"F16.opExtrude","SWEPT_BODY",BODY,{"disambiguationData":[OSD([sQuery(id+"F15.wireOp",EDGE,"E13.bottom"),sQuery(id+"F15.wireOp",EDGE,"E13.top"),sQuery(id+"F15.wireOp",EDGE,"E13.left"),sQuery(id+"F15.wireOp",EDGE,"E13.right"),sQuery(id+"F15.wireOp",EDGE,"E14.bottom"),sQuery(id+"F15.wireOp",EDGE,"E14.top"),sQuery(id+"F15.wireOp",EDGE,"E14.left"),sQuery(id+"F15.wireOp",EDGE,"E14.right"),sQuery(id+"F15.wireOp",EDGE,"E15.MirrorCS"),sQuery(id+"F15.wireOp",EDGE,"E16.MirrorCS"),sQuery(id+"F15.wireOp",EDGE,"E17.MirrorCS"),sQuery(id+"F15.wireOp",EDGE,"E18.MirrorCS"),sQuery(id+"F15.wireOp",EDGE,"E19.MirrorCS"),sQuery(id+"F15.wireOp",EDGE,"E20.MirrorCS"),sQuery(id+"F15.wireOp",EDGE,"E21.MirrorCS"),sQuery(id+"F15.wireOp",EDGE,"E22.MirrorCS"),sQuery(id+"F15.wireOp",EDGE,"E23.MirrorCS"),sQuery(id+"F15.wireOp",EDGE,"E24.MirrorCS"),sQuery(id+"F15.wireOp",EDGE,"E25.MirrorCS"),sQuery(id+"F15.wireOp",EDGE,"E26.MirrorCS")])]}),"instanceName":"1"}),"instanceName":"1"}),"instanceName":"1"}),"instanceName":"1"}),"instanceName":"1"});
            var Q32;
            Q32=makeQuery(id+"F24.opPattern","COPY",BODY,{"derivedFrom":makeQuery(id+"F21.opPattern","COPY",BODY,{"derivedFrom":makeQuery(id+"F20.opPattern","COPY",BODY,{"derivedFrom":makeQuery(id+"F19.opPattern","COPY",BODY,{"derivedFrom":makeQuery(id+"F16.opExtrude","SWEPT_BODY",BODY,{"disambiguationData":[OSD([sQuery(id+"F15.wireOp",EDGE,"E13.bottom"),sQuery(id+"F15.wireOp",EDGE,"E13.top"),sQuery(id+"F15.wireOp",EDGE,"E13.left"),sQuery(id+"F15.wireOp",EDGE,"E13.right"),sQuery(id+"F15.wireOp",EDGE,"E14.bottom"),sQuery(id+"F15.wireOp",EDGE,"E14.top"),sQuery(id+"F15.wireOp",EDGE,"E14.left"),sQuery(id+"F15.wireOp",EDGE,"E14.right"),sQuery(id+"F15.wireOp",EDGE,"E15.MirrorCS"),sQuery(id+"F15.wireOp",EDGE,"E16.MirrorCS"),sQuery(id+"F15.wireOp",EDGE,"E17.MirrorCS"),sQuery(id+"F15.wireOp",EDGE,"E18.MirrorCS"),sQuery(id+"F15.wireOp",EDGE,"E19.MirrorCS"),sQuery(id+"F15.wireOp",EDGE,"E20.MirrorCS"),sQuery(id+"F15.wireOp",EDGE,"E21.MirrorCS"),sQuery(id+"F15.wireOp",EDGE,"E22.MirrorCS"),sQuery(id+"F15.wireOp",EDGE,"E23.MirrorCS"),sQuery(id+"F15.wireOp",EDGE,"E24.MirrorCS"),sQuery(id+"F15.wireOp",EDGE,"E25.MirrorCS"),sQuery(id+"F15.wireOp",EDGE,"E26.MirrorCS")])]}),"instanceName":"1"}),"instanceName":"1"}),"instanceName":"1"}),"instanceName":"1"});
            var Q33;
            Q33=makeQuery(id+"F24.opPattern","COPY",BODY,{"derivedFrom":makeQuery(id+"F21.opPattern","COPY",BODY,{"derivedFrom":makeQuery(id+"F20.opPattern","COPY",BODY,{"derivedFrom":makeQuery(id+"F19.opPattern","COPY",BODY,{"derivedFrom":makeQuery(id+"F17.opPattern","COPY",BODY,{"derivedFrom":makeQuery(id+"F16.opExtrude","SWEPT_BODY",BODY,{"disambiguationData":[OSD([sQuery(id+"F15.wireOp",EDGE,"E13.bottom"),sQuery(id+"F15.wireOp",EDGE,"E13.top"),sQuery(id+"F15.wireOp",EDGE,"E13.left"),sQuery(id+"F15.wireOp",EDGE,"E13.right"),sQuery(id+"F15.wireOp",EDGE,"E14.bottom"),sQuery(id+"F15.wireOp",EDGE,"E14.top"),sQuery(id+"F15.wireOp",EDGE,"E14.left"),sQuery(id+"F15.wireOp",EDGE,"E14.right"),sQuery(id+"F15.wireOp",EDGE,"E15.MirrorCS"),sQuery(id+"F15.wireOp",EDGE,"E16.MirrorCS"),sQuery(id+"F15.wireOp",EDGE,"E17.MirrorCS"),sQuery(id+"F15.wireOp",EDGE,"E18.MirrorCS"),sQuery(id+"F15.wireOp",EDGE,"E19.MirrorCS"),sQuery(id+"F15.wireOp",EDGE,"E20.MirrorCS"),sQuery(id+"F15.wireOp",EDGE,"E21.MirrorCS"),sQuery(id+"F15.wireOp",EDGE,"E22.MirrorCS"),sQuery(id+"F15.wireOp",EDGE,"E23.MirrorCS"),sQuery(id+"F15.wireOp",EDGE,"E24.MirrorCS"),sQuery(id+"F15.wireOp",EDGE,"E25.MirrorCS"),sQuery(id+"F15.wireOp",EDGE,"E26.MirrorCS")])]}),"instanceName":"1"}),"instanceName":"1"}),"instanceName":"1"}),"instanceName":"1"}),"instanceName":"1"});
            var Q34;
            Q34=makeQuery(id+"F24.opPattern","COPY",BODY,{"derivedFrom":makeQuery(id+"F21.opPattern","COPY",BODY,{"derivedFrom":makeQuery(id+"F20.opPattern","COPY",BODY,{"derivedFrom":makeQuery(id+"F19.opPattern","COPY",BODY,{"derivedFrom":makeQuery(id+"F18.opPattern","COPY",BODY,{"derivedFrom":makeQuery(id+"F16.opExtrude","SWEPT_BODY",BODY,{"disambiguationData":[OSD([sQuery(id+"F15.wireOp",EDGE,"E13.bottom"),sQuery(id+"F15.wireOp",EDGE,"E13.top"),sQuery(id+"F15.wireOp",EDGE,"E13.left"),sQuery(id+"F15.wireOp",EDGE,"E13.right"),sQuery(id+"F15.wireOp",EDGE,"E14.bottom"),sQuery(id+"F15.wireOp",EDGE,"E14.top"),sQuery(id+"F15.wireOp",EDGE,"E14.left"),sQuery(id+"F15.wireOp",EDGE,"E14.right"),sQuery(id+"F15.wireOp",EDGE,"E15.MirrorCS"),sQuery(id+"F15.wireOp",EDGE,"E16.MirrorCS"),sQuery(id+"F15.wireOp",EDGE,"E17.MirrorCS"),sQuery(id+"F15.wireOp",EDGE,"E18.MirrorCS"),sQuery(id+"F15.wireOp",EDGE,"E19.MirrorCS"),sQuery(id+"F15.wireOp",EDGE,"E20.MirrorCS"),sQuery(id+"F15.wireOp",EDGE,"E21.MirrorCS"),sQuery(id+"F15.wireOp",EDGE,"E22.MirrorCS"),sQuery(id+"F15.wireOp",EDGE,"E23.MirrorCS"),sQuery(id+"F15.wireOp",EDGE,"E24.MirrorCS"),sQuery(id+"F15.wireOp",EDGE,"E25.MirrorCS"),sQuery(id+"F15.wireOp",EDGE,"E26.MirrorCS")])]}),"instanceName":"1"}),"instanceName":"1"}),"instanceName":"1"}),"instanceName":"1"}),"instanceName":"1"});
            var Q35;
            Q35=makeQuery(id+"F24.opPattern","COPY",BODY,{"derivedFrom":makeQuery(id+"F22.opPattern","COPY",BODY,{"derivedFrom":makeQuery(id+"F21.opPattern","COPY",BODY,{"derivedFrom":makeQuery(id+"F20.opPattern","COPY",BODY,{"derivedFrom":makeQuery(id+"F16.opExtrude","SWEPT_BODY",BODY,{"disambiguationData":[OSD([sQuery(id+"F15.wireOp",EDGE,"E13.bottom"),sQuery(id+"F15.wireOp",EDGE,"E13.top"),sQuery(id+"F15.wireOp",EDGE,"E13.left"),sQuery(id+"F15.wireOp",EDGE,"E13.right"),sQuery(id+"F15.wireOp",EDGE,"E14.bottom"),sQuery(id+"F15.wireOp",EDGE,"E14.top"),sQuery(id+"F15.wireOp",EDGE,"E14.left"),sQuery(id+"F15.wireOp",EDGE,"E14.right"),sQuery(id+"F15.wireOp",EDGE,"E15.MirrorCS"),sQuery(id+"F15.wireOp",EDGE,"E16.MirrorCS"),sQuery(id+"F15.wireOp",EDGE,"E17.MirrorCS"),sQuery(id+"F15.wireOp",EDGE,"E18.MirrorCS"),sQuery(id+"F15.wireOp",EDGE,"E19.MirrorCS"),sQuery(id+"F15.wireOp",EDGE,"E20.MirrorCS"),sQuery(id+"F15.wireOp",EDGE,"E21.MirrorCS"),sQuery(id+"F15.wireOp",EDGE,"E22.MirrorCS"),sQuery(id+"F15.wireOp",EDGE,"E23.MirrorCS"),sQuery(id+"F15.wireOp",EDGE,"E24.MirrorCS"),sQuery(id+"F15.wireOp",EDGE,"E25.MirrorCS"),sQuery(id+"F15.wireOp",EDGE,"E26.MirrorCS")])]}),"instanceName":"1"}),"instanceName":"1"}),"instanceName":"1"}),"instanceName":"1"});
            var Q36;
            Q36=makeQuery(id+"F24.opPattern","COPY",BODY,{"derivedFrom":makeQuery(id+"F22.opPattern","COPY",BODY,{"derivedFrom":makeQuery(id+"F21.opPattern","COPY",BODY,{"derivedFrom":makeQuery(id+"F20.opPattern","COPY",BODY,{"derivedFrom":makeQuery(id+"F17.opPattern","COPY",BODY,{"derivedFrom":makeQuery(id+"F16.opExtrude","SWEPT_BODY",BODY,{"disambiguationData":[OSD([sQuery(id+"F15.wireOp",EDGE,"E13.bottom"),sQuery(id+"F15.wireOp",EDGE,"E13.top"),sQuery(id+"F15.wireOp",EDGE,"E13.left"),sQuery(id+"F15.wireOp",EDGE,"E13.right"),sQuery(id+"F15.wireOp",EDGE,"E14.bottom"),sQuery(id+"F15.wireOp",EDGE,"E14.top"),sQuery(id+"F15.wireOp",EDGE,"E14.left"),sQuery(id+"F15.wireOp",EDGE,"E14.right"),sQuery(id+"F15.wireOp",EDGE,"E15.MirrorCS"),sQuery(id+"F15.wireOp",EDGE,"E16.MirrorCS"),sQuery(id+"F15.wireOp",EDGE,"E17.MirrorCS"),sQuery(id+"F15.wireOp",EDGE,"E18.MirrorCS"),sQuery(id+"F15.wireOp",EDGE,"E19.MirrorCS"),sQuery(id+"F15.wireOp",EDGE,"E20.MirrorCS"),sQuery(id+"F15.wireOp",EDGE,"E21.MirrorCS"),sQuery(id+"F15.wireOp",EDGE,"E22.MirrorCS"),sQuery(id+"F15.wireOp",EDGE,"E23.MirrorCS"),sQuery(id+"F15.wireOp",EDGE,"E24.MirrorCS"),sQuery(id+"F15.wireOp",EDGE,"E25.MirrorCS"),sQuery(id+"F15.wireOp",EDGE,"E26.MirrorCS")])]}),"instanceName":"1"}),"instanceName":"1"}),"instanceName":"1"}),"instanceName":"1"}),"instanceName":"1"});
            var Q37;
            Q37=makeQuery(id+"F24.opPattern","COPY",BODY,{"derivedFrom":makeQuery(id+"F22.opPattern","COPY",BODY,{"derivedFrom":makeQuery(id+"F21.opPattern","COPY",BODY,{"derivedFrom":makeQuery(id+"F20.opPattern","COPY",BODY,{"derivedFrom":makeQuery(id+"F18.opPattern","COPY",BODY,{"derivedFrom":makeQuery(id+"F16.opExtrude","SWEPT_BODY",BODY,{"disambiguationData":[OSD([sQuery(id+"F15.wireOp",EDGE,"E13.bottom"),sQuery(id+"F15.wireOp",EDGE,"E13.top"),sQuery(id+"F15.wireOp",EDGE,"E13.left"),sQuery(id+"F15.wireOp",EDGE,"E13.right"),sQuery(id+"F15.wireOp",EDGE,"E14.bottom"),sQuery(id+"F15.wireOp",EDGE,"E14.top"),sQuery(id+"F15.wireOp",EDGE,"E14.left"),sQuery(id+"F15.wireOp",EDGE,"E14.right"),sQuery(id+"F15.wireOp",EDGE,"E15.MirrorCS"),sQuery(id+"F15.wireOp",EDGE,"E16.MirrorCS"),sQuery(id+"F15.wireOp",EDGE,"E17.MirrorCS"),sQuery(id+"F15.wireOp",EDGE,"E18.MirrorCS"),sQuery(id+"F15.wireOp",EDGE,"E19.MirrorCS"),sQuery(id+"F15.wireOp",EDGE,"E20.MirrorCS"),sQuery(id+"F15.wireOp",EDGE,"E21.MirrorCS"),sQuery(id+"F15.wireOp",EDGE,"E22.MirrorCS"),sQuery(id+"F15.wireOp",EDGE,"E23.MirrorCS"),sQuery(id+"F15.wireOp",EDGE,"E24.MirrorCS"),sQuery(id+"F15.wireOp",EDGE,"E25.MirrorCS"),sQuery(id+"F15.wireOp",EDGE,"E26.MirrorCS")])]}),"instanceName":"1"}),"instanceName":"1"}),"instanceName":"1"}),"instanceName":"1"}),"instanceName":"1"});
            var Q38;
            Q38=makeQuery(id+"F24.opPattern","COPY",BODY,{"derivedFrom":makeQuery(id+"F22.opPattern","COPY",BODY,{"derivedFrom":makeQuery(id+"F21.opPattern","COPY",BODY,{"derivedFrom":makeQuery(id+"F20.opPattern","COPY",BODY,{"derivedFrom":makeQuery(id+"F18.opPattern","COPY",BODY,{"derivedFrom":makeQuery(id+"F17.opPattern","COPY",BODY,{"derivedFrom":makeQuery(id+"F16.opExtrude","SWEPT_BODY",BODY,{"disambiguationData":[OSD([sQuery(id+"F15.wireOp",EDGE,"E13.bottom"),sQuery(id+"F15.wireOp",EDGE,"E13.top"),sQuery(id+"F15.wireOp",EDGE,"E13.left"),sQuery(id+"F15.wireOp",EDGE,"E13.right"),sQuery(id+"F15.wireOp",EDGE,"E14.bottom"),sQuery(id+"F15.wireOp",EDGE,"E14.top"),sQuery(id+"F15.wireOp",EDGE,"E14.left"),sQuery(id+"F15.wireOp",EDGE,"E14.right"),sQuery(id+"F15.wireOp",EDGE,"E15.MirrorCS"),sQuery(id+"F15.wireOp",EDGE,"E16.MirrorCS"),sQuery(id+"F15.wireOp",EDGE,"E17.MirrorCS"),sQuery(id+"F15.wireOp",EDGE,"E18.MirrorCS"),sQuery(id+"F15.wireOp",EDGE,"E19.MirrorCS"),sQuery(id+"F15.wireOp",EDGE,"E20.MirrorCS"),sQuery(id+"F15.wireOp",EDGE,"E21.MirrorCS"),sQuery(id+"F15.wireOp",EDGE,"E22.MirrorCS"),sQuery(id+"F15.wireOp",EDGE,"E23.MirrorCS"),sQuery(id+"F15.wireOp",EDGE,"E24.MirrorCS"),sQuery(id+"F15.wireOp",EDGE,"E25.MirrorCS"),sQuery(id+"F15.wireOp",EDGE,"E26.MirrorCS")])]}),"instanceName":"1"}),"instanceName":"1"}),"instanceName":"1"}),"instanceName":"1"}),"instanceName":"1"}),"instanceName":"1"});
            var Q39;
            Q39=makeQuery(id+"F24.opPattern","COPY",BODY,{"derivedFrom":makeQuery(id+"F22.opPattern","COPY",BODY,{"derivedFrom":makeQuery(id+"F21.opPattern","COPY",BODY,{"derivedFrom":makeQuery(id+"F20.opPattern","COPY",BODY,{"derivedFrom":makeQuery(id+"F19.opPattern","COPY",BODY,{"derivedFrom":makeQuery(id+"F16.opExtrude","SWEPT_BODY",BODY,{"disambiguationData":[OSD([sQuery(id+"F15.wireOp",EDGE,"E13.bottom"),sQuery(id+"F15.wireOp",EDGE,"E13.top"),sQuery(id+"F15.wireOp",EDGE,"E13.left"),sQuery(id+"F15.wireOp",EDGE,"E13.right"),sQuery(id+"F15.wireOp",EDGE,"E14.bottom"),sQuery(id+"F15.wireOp",EDGE,"E14.top"),sQuery(id+"F15.wireOp",EDGE,"E14.left"),sQuery(id+"F15.wireOp",EDGE,"E14.right"),sQuery(id+"F15.wireOp",EDGE,"E15.MirrorCS"),sQuery(id+"F15.wireOp",EDGE,"E16.MirrorCS"),sQuery(id+"F15.wireOp",EDGE,"E17.MirrorCS"),sQuery(id+"F15.wireOp",EDGE,"E18.MirrorCS"),sQuery(id+"F15.wireOp",EDGE,"E19.MirrorCS"),sQuery(id+"F15.wireOp",EDGE,"E20.MirrorCS"),sQuery(id+"F15.wireOp",EDGE,"E21.MirrorCS"),sQuery(id+"F15.wireOp",EDGE,"E22.MirrorCS"),sQuery(id+"F15.wireOp",EDGE,"E23.MirrorCS"),sQuery(id+"F15.wireOp",EDGE,"E24.MirrorCS"),sQuery(id+"F15.wireOp",EDGE,"E25.MirrorCS"),sQuery(id+"F15.wireOp",EDGE,"E26.MirrorCS")])]}),"instanceName":"1"}),"instanceName":"1"}),"instanceName":"1"}),"instanceName":"1"}),"instanceName":"1"});
            var Q40;
            Q40=makeQuery(id+"F24.opPattern","COPY",BODY,{"derivedFrom":makeQuery(id+"F22.opPattern","COPY",BODY,{"derivedFrom":makeQuery(id+"F21.opPattern","COPY",BODY,{"derivedFrom":makeQuery(id+"F20.opPattern","COPY",BODY,{"derivedFrom":makeQuery(id+"F19.opPattern","COPY",BODY,{"derivedFrom":makeQuery(id+"F17.opPattern","COPY",BODY,{"derivedFrom":makeQuery(id+"F16.opExtrude","SWEPT_BODY",BODY,{"disambiguationData":[OSD([sQuery(id+"F15.wireOp",EDGE,"E13.bottom"),sQuery(id+"F15.wireOp",EDGE,"E13.top"),sQuery(id+"F15.wireOp",EDGE,"E13.left"),sQuery(id+"F15.wireOp",EDGE,"E13.right"),sQuery(id+"F15.wireOp",EDGE,"E14.bottom"),sQuery(id+"F15.wireOp",EDGE,"E14.top"),sQuery(id+"F15.wireOp",EDGE,"E14.left"),sQuery(id+"F15.wireOp",EDGE,"E14.right"),sQuery(id+"F15.wireOp",EDGE,"E15.MirrorCS"),sQuery(id+"F15.wireOp",EDGE,"E16.MirrorCS"),sQuery(id+"F15.wireOp",EDGE,"E17.MirrorCS"),sQuery(id+"F15.wireOp",EDGE,"E18.MirrorCS"),sQuery(id+"F15.wireOp",EDGE,"E19.MirrorCS"),sQuery(id+"F15.wireOp",EDGE,"E20.MirrorCS"),sQuery(id+"F15.wireOp",EDGE,"E21.MirrorCS"),sQuery(id+"F15.wireOp",EDGE,"E22.MirrorCS"),sQuery(id+"F15.wireOp",EDGE,"E23.MirrorCS"),sQuery(id+"F15.wireOp",EDGE,"E24.MirrorCS"),sQuery(id+"F15.wireOp",EDGE,"E25.MirrorCS"),sQuery(id+"F15.wireOp",EDGE,"E26.MirrorCS")])]}),"instanceName":"1"}),"instanceName":"1"}),"instanceName":"1"}),"instanceName":"1"}),"instanceName":"1"}),"instanceName":"1"});
            var Q41;
            Q41=makeQuery(id+"F24.opPattern","COPY",BODY,{"derivedFrom":makeQuery(id+"F22.opPattern","COPY",BODY,{"derivedFrom":makeQuery(id+"F21.opPattern","COPY",BODY,{"derivedFrom":makeQuery(id+"F20.opPattern","COPY",BODY,{"derivedFrom":makeQuery(id+"F19.opPattern","COPY",BODY,{"derivedFrom":makeQuery(id+"F18.opPattern","COPY",BODY,{"derivedFrom":makeQuery(id+"F16.opExtrude","SWEPT_BODY",BODY,{"disambiguationData":[OSD([sQuery(id+"F15.wireOp",EDGE,"E13.bottom"),sQuery(id+"F15.wireOp",EDGE,"E13.top"),sQuery(id+"F15.wireOp",EDGE,"E13.left"),sQuery(id+"F15.wireOp",EDGE,"E13.right"),sQuery(id+"F15.wireOp",EDGE,"E14.bottom"),sQuery(id+"F15.wireOp",EDGE,"E14.top"),sQuery(id+"F15.wireOp",EDGE,"E14.left"),sQuery(id+"F15.wireOp",EDGE,"E14.right"),sQuery(id+"F15.wireOp",EDGE,"E15.MirrorCS"),sQuery(id+"F15.wireOp",EDGE,"E16.MirrorCS"),sQuery(id+"F15.wireOp",EDGE,"E17.MirrorCS"),sQuery(id+"F15.wireOp",EDGE,"E18.MirrorCS"),sQuery(id+"F15.wireOp",EDGE,"E19.MirrorCS"),sQuery(id+"F15.wireOp",EDGE,"E20.MirrorCS"),sQuery(id+"F15.wireOp",EDGE,"E21.MirrorCS"),sQuery(id+"F15.wireOp",EDGE,"E22.MirrorCS"),sQuery(id+"F15.wireOp",EDGE,"E23.MirrorCS"),sQuery(id+"F15.wireOp",EDGE,"E24.MirrorCS"),sQuery(id+"F15.wireOp",EDGE,"E25.MirrorCS"),sQuery(id+"F15.wireOp",EDGE,"E26.MirrorCS")])]}),"instanceName":"1"}),"instanceName":"1"}),"instanceName":"1"}),"instanceName":"1"}),"instanceName":"1"}),"instanceName":"1"});
            var Q42;
            Q42=makeQuery(id+"F24.opPattern","COPY",BODY,{"derivedFrom":makeQuery(id+"F23.opPattern","COPY",BODY,{"derivedFrom":makeQuery(id+"F21.opPattern","COPY",BODY,{"derivedFrom":makeQuery(id+"F20.opPattern","COPY",BODY,{"derivedFrom":makeQuery(id+"F16.opExtrude","SWEPT_BODY",BODY,{"disambiguationData":[OSD([sQuery(id+"F15.wireOp",EDGE,"E13.bottom"),sQuery(id+"F15.wireOp",EDGE,"E13.top"),sQuery(id+"F15.wireOp",EDGE,"E13.left"),sQuery(id+"F15.wireOp",EDGE,"E13.right"),sQuery(id+"F15.wireOp",EDGE,"E14.bottom"),sQuery(id+"F15.wireOp",EDGE,"E14.top"),sQuery(id+"F15.wireOp",EDGE,"E14.left"),sQuery(id+"F15.wireOp",EDGE,"E14.right"),sQuery(id+"F15.wireOp",EDGE,"E15.MirrorCS"),sQuery(id+"F15.wireOp",EDGE,"E16.MirrorCS"),sQuery(id+"F15.wireOp",EDGE,"E17.MirrorCS"),sQuery(id+"F15.wireOp",EDGE,"E18.MirrorCS"),sQuery(id+"F15.wireOp",EDGE,"E19.MirrorCS"),sQuery(id+"F15.wireOp",EDGE,"E20.MirrorCS"),sQuery(id+"F15.wireOp",EDGE,"E21.MirrorCS"),sQuery(id+"F15.wireOp",EDGE,"E22.MirrorCS"),sQuery(id+"F15.wireOp",EDGE,"E23.MirrorCS"),sQuery(id+"F15.wireOp",EDGE,"E24.MirrorCS"),sQuery(id+"F15.wireOp",EDGE,"E25.MirrorCS"),sQuery(id+"F15.wireOp",EDGE,"E26.MirrorCS")])]}),"instanceName":"1"}),"instanceName":"1"}),"instanceName":"1"}),"instanceName":"1"});
            var Q43;
            Q43=makeQuery(id+"F24.opPattern","COPY",BODY,{"derivedFrom":makeQuery(id+"F23.opPattern","COPY",BODY,{"derivedFrom":makeQuery(id+"F21.opPattern","COPY",BODY,{"derivedFrom":makeQuery(id+"F20.opPattern","COPY",BODY,{"derivedFrom":makeQuery(id+"F17.opPattern","COPY",BODY,{"derivedFrom":makeQuery(id+"F16.opExtrude","SWEPT_BODY",BODY,{"disambiguationData":[OSD([sQuery(id+"F15.wireOp",EDGE,"E13.bottom"),sQuery(id+"F15.wireOp",EDGE,"E13.top"),sQuery(id+"F15.wireOp",EDGE,"E13.left"),sQuery(id+"F15.wireOp",EDGE,"E13.right"),sQuery(id+"F15.wireOp",EDGE,"E14.bottom"),sQuery(id+"F15.wireOp",EDGE,"E14.top"),sQuery(id+"F15.wireOp",EDGE,"E14.left"),sQuery(id+"F15.wireOp",EDGE,"E14.right"),sQuery(id+"F15.wireOp",EDGE,"E15.MirrorCS"),sQuery(id+"F15.wireOp",EDGE,"E16.MirrorCS"),sQuery(id+"F15.wireOp",EDGE,"E17.MirrorCS"),sQuery(id+"F15.wireOp",EDGE,"E18.MirrorCS"),sQuery(id+"F15.wireOp",EDGE,"E19.MirrorCS"),sQuery(id+"F15.wireOp",EDGE,"E20.MirrorCS"),sQuery(id+"F15.wireOp",EDGE,"E21.MirrorCS"),sQuery(id+"F15.wireOp",EDGE,"E22.MirrorCS"),sQuery(id+"F15.wireOp",EDGE,"E23.MirrorCS"),sQuery(id+"F15.wireOp",EDGE,"E24.MirrorCS"),sQuery(id+"F15.wireOp",EDGE,"E25.MirrorCS"),sQuery(id+"F15.wireOp",EDGE,"E26.MirrorCS")])]}),"instanceName":"1"}),"instanceName":"1"}),"instanceName":"1"}),"instanceName":"1"}),"instanceName":"1"});
            var Q44;
            Q44=makeQuery(id+"F24.opPattern","COPY",BODY,{"derivedFrom":makeQuery(id+"F23.opPattern","COPY",BODY,{"derivedFrom":makeQuery(id+"F21.opPattern","COPY",BODY,{"derivedFrom":makeQuery(id+"F20.opPattern","COPY",BODY,{"derivedFrom":makeQuery(id+"F18.opPattern","COPY",BODY,{"derivedFrom":makeQuery(id+"F16.opExtrude","SWEPT_BODY",BODY,{"disambiguationData":[OSD([sQuery(id+"F15.wireOp",EDGE,"E13.bottom"),sQuery(id+"F15.wireOp",EDGE,"E13.top"),sQuery(id+"F15.wireOp",EDGE,"E13.left"),sQuery(id+"F15.wireOp",EDGE,"E13.right"),sQuery(id+"F15.wireOp",EDGE,"E14.bottom"),sQuery(id+"F15.wireOp",EDGE,"E14.top"),sQuery(id+"F15.wireOp",EDGE,"E14.left"),sQuery(id+"F15.wireOp",EDGE,"E14.right"),sQuery(id+"F15.wireOp",EDGE,"E15.MirrorCS"),sQuery(id+"F15.wireOp",EDGE,"E16.MirrorCS"),sQuery(id+"F15.wireOp",EDGE,"E17.MirrorCS"),sQuery(id+"F15.wireOp",EDGE,"E18.MirrorCS"),sQuery(id+"F15.wireOp",EDGE,"E19.MirrorCS"),sQuery(id+"F15.wireOp",EDGE,"E20.MirrorCS"),sQuery(id+"F15.wireOp",EDGE,"E21.MirrorCS"),sQuery(id+"F15.wireOp",EDGE,"E22.MirrorCS"),sQuery(id+"F15.wireOp",EDGE,"E23.MirrorCS"),sQuery(id+"F15.wireOp",EDGE,"E24.MirrorCS"),sQuery(id+"F15.wireOp",EDGE,"E25.MirrorCS"),sQuery(id+"F15.wireOp",EDGE,"E26.MirrorCS")])]}),"instanceName":"1"}),"instanceName":"1"}),"instanceName":"1"}),"instanceName":"1"}),"instanceName":"1"});
            var Q45;
            Q45=makeQuery(id+"F24.opPattern","COPY",BODY,{"derivedFrom":makeQuery(id+"F23.opPattern","COPY",BODY,{"derivedFrom":makeQuery(id+"F21.opPattern","COPY",BODY,{"derivedFrom":makeQuery(id+"F20.opPattern","COPY",BODY,{"derivedFrom":makeQuery(id+"F18.opPattern","COPY",BODY,{"derivedFrom":makeQuery(id+"F17.opPattern","COPY",BODY,{"derivedFrom":makeQuery(id+"F16.opExtrude","SWEPT_BODY",BODY,{"disambiguationData":[OSD([sQuery(id+"F15.wireOp",EDGE,"E13.bottom"),sQuery(id+"F15.wireOp",EDGE,"E13.top"),sQuery(id+"F15.wireOp",EDGE,"E13.left"),sQuery(id+"F15.wireOp",EDGE,"E13.right"),sQuery(id+"F15.wireOp",EDGE,"E14.bottom"),sQuery(id+"F15.wireOp",EDGE,"E14.top"),sQuery(id+"F15.wireOp",EDGE,"E14.left"),sQuery(id+"F15.wireOp",EDGE,"E14.right"),sQuery(id+"F15.wireOp",EDGE,"E15.MirrorCS"),sQuery(id+"F15.wireOp",EDGE,"E16.MirrorCS"),sQuery(id+"F15.wireOp",EDGE,"E17.MirrorCS"),sQuery(id+"F15.wireOp",EDGE,"E18.MirrorCS"),sQuery(id+"F15.wireOp",EDGE,"E19.MirrorCS"),sQuery(id+"F15.wireOp",EDGE,"E20.MirrorCS"),sQuery(id+"F15.wireOp",EDGE,"E21.MirrorCS"),sQuery(id+"F15.wireOp",EDGE,"E22.MirrorCS"),sQuery(id+"F15.wireOp",EDGE,"E23.MirrorCS"),sQuery(id+"F15.wireOp",EDGE,"E24.MirrorCS"),sQuery(id+"F15.wireOp",EDGE,"E25.MirrorCS"),sQuery(id+"F15.wireOp",EDGE,"E26.MirrorCS")])]}),"instanceName":"1"}),"instanceName":"1"}),"instanceName":"1"}),"instanceName":"1"}),"instanceName":"1"}),"instanceName":"1"});
            var Q46;
            Q46=makeQuery(id+"F24.opPattern","COPY",BODY,{"derivedFrom":makeQuery(id+"F23.opPattern","COPY",BODY,{"derivedFrom":makeQuery(id+"F21.opPattern","COPY",BODY,{"derivedFrom":makeQuery(id+"F20.opPattern","COPY",BODY,{"derivedFrom":makeQuery(id+"F19.opPattern","COPY",BODY,{"derivedFrom":makeQuery(id+"F16.opExtrude","SWEPT_BODY",BODY,{"disambiguationData":[OSD([sQuery(id+"F15.wireOp",EDGE,"E13.bottom"),sQuery(id+"F15.wireOp",EDGE,"E13.top"),sQuery(id+"F15.wireOp",EDGE,"E13.left"),sQuery(id+"F15.wireOp",EDGE,"E13.right"),sQuery(id+"F15.wireOp",EDGE,"E14.bottom"),sQuery(id+"F15.wireOp",EDGE,"E14.top"),sQuery(id+"F15.wireOp",EDGE,"E14.left"),sQuery(id+"F15.wireOp",EDGE,"E14.right"),sQuery(id+"F15.wireOp",EDGE,"E15.MirrorCS"),sQuery(id+"F15.wireOp",EDGE,"E16.MirrorCS"),sQuery(id+"F15.wireOp",EDGE,"E17.MirrorCS"),sQuery(id+"F15.wireOp",EDGE,"E18.MirrorCS"),sQuery(id+"F15.wireOp",EDGE,"E19.MirrorCS"),sQuery(id+"F15.wireOp",EDGE,"E20.MirrorCS"),sQuery(id+"F15.wireOp",EDGE,"E21.MirrorCS"),sQuery(id+"F15.wireOp",EDGE,"E22.MirrorCS"),sQuery(id+"F15.wireOp",EDGE,"E23.MirrorCS"),sQuery(id+"F15.wireOp",EDGE,"E24.MirrorCS"),sQuery(id+"F15.wireOp",EDGE,"E25.MirrorCS"),sQuery(id+"F15.wireOp",EDGE,"E26.MirrorCS")])]}),"instanceName":"1"}),"instanceName":"1"}),"instanceName":"1"}),"instanceName":"1"}),"instanceName":"1"});
            var Q47;
            Q47=makeQuery(id+"F24.opPattern","COPY",BODY,{"derivedFrom":makeQuery(id+"F23.opPattern","COPY",BODY,{"derivedFrom":makeQuery(id+"F21.opPattern","COPY",BODY,{"derivedFrom":makeQuery(id+"F20.opPattern","COPY",BODY,{"derivedFrom":makeQuery(id+"F19.opPattern","COPY",BODY,{"derivedFrom":makeQuery(id+"F17.opPattern","COPY",BODY,{"derivedFrom":makeQuery(id+"F16.opExtrude","SWEPT_BODY",BODY,{"disambiguationData":[OSD([sQuery(id+"F15.wireOp",EDGE,"E13.bottom"),sQuery(id+"F15.wireOp",EDGE,"E13.top"),sQuery(id+"F15.wireOp",EDGE,"E13.left"),sQuery(id+"F15.wireOp",EDGE,"E13.right"),sQuery(id+"F15.wireOp",EDGE,"E14.bottom"),sQuery(id+"F15.wireOp",EDGE,"E14.top"),sQuery(id+"F15.wireOp",EDGE,"E14.left"),sQuery(id+"F15.wireOp",EDGE,"E14.right"),sQuery(id+"F15.wireOp",EDGE,"E15.MirrorCS"),sQuery(id+"F15.wireOp",EDGE,"E16.MirrorCS"),sQuery(id+"F15.wireOp",EDGE,"E17.MirrorCS"),sQuery(id+"F15.wireOp",EDGE,"E18.MirrorCS"),sQuery(id+"F15.wireOp",EDGE,"E19.MirrorCS"),sQuery(id+"F15.wireOp",EDGE,"E20.MirrorCS"),sQuery(id+"F15.wireOp",EDGE,"E21.MirrorCS"),sQuery(id+"F15.wireOp",EDGE,"E22.MirrorCS"),sQuery(id+"F15.wireOp",EDGE,"E23.MirrorCS"),sQuery(id+"F15.wireOp",EDGE,"E24.MirrorCS"),sQuery(id+"F15.wireOp",EDGE,"E25.MirrorCS"),sQuery(id+"F15.wireOp",EDGE,"E26.MirrorCS")])]}),"instanceName":"1"}),"instanceName":"1"}),"instanceName":"1"}),"instanceName":"1"}),"instanceName":"1"}),"instanceName":"1"});
            var Q48;
            Q48=makeQuery(id+"F24.opPattern","COPY",BODY,{"derivedFrom":makeQuery(id+"F23.opPattern","COPY",BODY,{"derivedFrom":makeQuery(id+"F21.opPattern","COPY",BODY,{"derivedFrom":makeQuery(id+"F20.opPattern","COPY",BODY,{"derivedFrom":makeQuery(id+"F19.opPattern","COPY",BODY,{"derivedFrom":makeQuery(id+"F18.opPattern","COPY",BODY,{"derivedFrom":makeQuery(id+"F16.opExtrude","SWEPT_BODY",BODY,{"disambiguationData":[OSD([sQuery(id+"F15.wireOp",EDGE,"E13.bottom"),sQuery(id+"F15.wireOp",EDGE,"E13.top"),sQuery(id+"F15.wireOp",EDGE,"E13.left"),sQuery(id+"F15.wireOp",EDGE,"E13.right"),sQuery(id+"F15.wireOp",EDGE,"E14.bottom"),sQuery(id+"F15.wireOp",EDGE,"E14.top"),sQuery(id+"F15.wireOp",EDGE,"E14.left"),sQuery(id+"F15.wireOp",EDGE,"E14.right"),sQuery(id+"F15.wireOp",EDGE,"E15.MirrorCS"),sQuery(id+"F15.wireOp",EDGE,"E16.MirrorCS"),sQuery(id+"F15.wireOp",EDGE,"E17.MirrorCS"),sQuery(id+"F15.wireOp",EDGE,"E18.MirrorCS"),sQuery(id+"F15.wireOp",EDGE,"E19.MirrorCS"),sQuery(id+"F15.wireOp",EDGE,"E20.MirrorCS"),sQuery(id+"F15.wireOp",EDGE,"E21.MirrorCS"),sQuery(id+"F15.wireOp",EDGE,"E22.MirrorCS"),sQuery(id+"F15.wireOp",EDGE,"E23.MirrorCS"),sQuery(id+"F15.wireOp",EDGE,"E24.MirrorCS"),sQuery(id+"F15.wireOp",EDGE,"E25.MirrorCS"),sQuery(id+"F15.wireOp",EDGE,"E26.MirrorCS")])]}),"instanceName":"1"}),"instanceName":"1"}),"instanceName":"1"}),"instanceName":"1"}),"instanceName":"1"}),"instanceName":"1"});
            var Q49;
            Q49=makeQuery(id+"F24.opPattern","COPY",BODY,{"derivedFrom":makeQuery(id+"F23.opPattern","COPY",BODY,{"derivedFrom":makeQuery(id+"F22.opPattern","COPY",BODY,{"derivedFrom":makeQuery(id+"F21.opPattern","COPY",BODY,{"derivedFrom":makeQuery(id+"F20.opPattern","COPY",BODY,{"derivedFrom":makeQuery(id+"F16.opExtrude","SWEPT_BODY",BODY,{"disambiguationData":[OSD([sQuery(id+"F15.wireOp",EDGE,"E13.bottom"),sQuery(id+"F15.wireOp",EDGE,"E13.top"),sQuery(id+"F15.wireOp",EDGE,"E13.left"),sQuery(id+"F15.wireOp",EDGE,"E13.right"),sQuery(id+"F15.wireOp",EDGE,"E14.bottom"),sQuery(id+"F15.wireOp",EDGE,"E14.top"),sQuery(id+"F15.wireOp",EDGE,"E14.left"),sQuery(id+"F15.wireOp",EDGE,"E14.right"),sQuery(id+"F15.wireOp",EDGE,"E15.MirrorCS"),sQuery(id+"F15.wireOp",EDGE,"E16.MirrorCS"),sQuery(id+"F15.wireOp",EDGE,"E17.MirrorCS"),sQuery(id+"F15.wireOp",EDGE,"E18.MirrorCS"),sQuery(id+"F15.wireOp",EDGE,"E19.MirrorCS"),sQuery(id+"F15.wireOp",EDGE,"E20.MirrorCS"),sQuery(id+"F15.wireOp",EDGE,"E21.MirrorCS"),sQuery(id+"F15.wireOp",EDGE,"E22.MirrorCS"),sQuery(id+"F15.wireOp",EDGE,"E23.MirrorCS"),sQuery(id+"F15.wireOp",EDGE,"E24.MirrorCS"),sQuery(id+"F15.wireOp",EDGE,"E25.MirrorCS"),sQuery(id+"F15.wireOp",EDGE,"E26.MirrorCS")])]}),"instanceName":"1"}),"instanceName":"1"}),"instanceName":"1"}),"instanceName":"1"}),"instanceName":"1"});
            var Q50;
            Q50=makeQuery(id+"F24.opPattern","COPY",BODY,{"derivedFrom":makeQuery(id+"F23.opPattern","COPY",BODY,{"derivedFrom":makeQuery(id+"F22.opPattern","COPY",BODY,{"derivedFrom":makeQuery(id+"F21.opPattern","COPY",BODY,{"derivedFrom":makeQuery(id+"F20.opPattern","COPY",BODY,{"derivedFrom":makeQuery(id+"F17.opPattern","COPY",BODY,{"derivedFrom":makeQuery(id+"F16.opExtrude","SWEPT_BODY",BODY,{"disambiguationData":[OSD([sQuery(id+"F15.wireOp",EDGE,"E13.bottom"),sQuery(id+"F15.wireOp",EDGE,"E13.top"),sQuery(id+"F15.wireOp",EDGE,"E13.left"),sQuery(id+"F15.wireOp",EDGE,"E13.right"),sQuery(id+"F15.wireOp",EDGE,"E14.bottom"),sQuery(id+"F15.wireOp",EDGE,"E14.top"),sQuery(id+"F15.wireOp",EDGE,"E14.left"),sQuery(id+"F15.wireOp",EDGE,"E14.right"),sQuery(id+"F15.wireOp",EDGE,"E15.MirrorCS"),sQuery(id+"F15.wireOp",EDGE,"E16.MirrorCS"),sQuery(id+"F15.wireOp",EDGE,"E17.MirrorCS"),sQuery(id+"F15.wireOp",EDGE,"E18.MirrorCS"),sQuery(id+"F15.wireOp",EDGE,"E19.MirrorCS"),sQuery(id+"F15.wireOp",EDGE,"E20.MirrorCS"),sQuery(id+"F15.wireOp",EDGE,"E21.MirrorCS"),sQuery(id+"F15.wireOp",EDGE,"E22.MirrorCS"),sQuery(id+"F15.wireOp",EDGE,"E23.MirrorCS"),sQuery(id+"F15.wireOp",EDGE,"E24.MirrorCS"),sQuery(id+"F15.wireOp",EDGE,"E25.MirrorCS"),sQuery(id+"F15.wireOp",EDGE,"E26.MirrorCS")])]}),"instanceName":"1"}),"instanceName":"1"}),"instanceName":"1"}),"instanceName":"1"}),"instanceName":"1"}),"instanceName":"1"});
            var Q51;
            Q51=makeQuery(id+"F24.opPattern","COPY",BODY,{"derivedFrom":makeQuery(id+"F23.opPattern","COPY",BODY,{"derivedFrom":makeQuery(id+"F22.opPattern","COPY",BODY,{"derivedFrom":makeQuery(id+"F21.opPattern","COPY",BODY,{"derivedFrom":makeQuery(id+"F20.opPattern","COPY",BODY,{"derivedFrom":makeQuery(id+"F18.opPattern","COPY",BODY,{"derivedFrom":makeQuery(id+"F16.opExtrude","SWEPT_BODY",BODY,{"disambiguationData":[OSD([sQuery(id+"F15.wireOp",EDGE,"E13.bottom"),sQuery(id+"F15.wireOp",EDGE,"E13.top"),sQuery(id+"F15.wireOp",EDGE,"E13.left"),sQuery(id+"F15.wireOp",EDGE,"E13.right"),sQuery(id+"F15.wireOp",EDGE,"E14.bottom"),sQuery(id+"F15.wireOp",EDGE,"E14.top"),sQuery(id+"F15.wireOp",EDGE,"E14.left"),sQuery(id+"F15.wireOp",EDGE,"E14.right"),sQuery(id+"F15.wireOp",EDGE,"E15.MirrorCS"),sQuery(id+"F15.wireOp",EDGE,"E16.MirrorCS"),sQuery(id+"F15.wireOp",EDGE,"E17.MirrorCS"),sQuery(id+"F15.wireOp",EDGE,"E18.MirrorCS"),sQuery(id+"F15.wireOp",EDGE,"E19.MirrorCS"),sQuery(id+"F15.wireOp",EDGE,"E20.MirrorCS"),sQuery(id+"F15.wireOp",EDGE,"E21.MirrorCS"),sQuery(id+"F15.wireOp",EDGE,"E22.MirrorCS"),sQuery(id+"F15.wireOp",EDGE,"E23.MirrorCS"),sQuery(id+"F15.wireOp",EDGE,"E24.MirrorCS"),sQuery(id+"F15.wireOp",EDGE,"E25.MirrorCS"),sQuery(id+"F15.wireOp",EDGE,"E26.MirrorCS")])]}),"instanceName":"1"}),"instanceName":"1"}),"instanceName":"1"}),"instanceName":"1"}),"instanceName":"1"}),"instanceName":"1"});
            var Q52;
            Q52=makeQuery(id+"F24.opPattern","COPY",BODY,{"derivedFrom":makeQuery(id+"F23.opPattern","COPY",BODY,{"derivedFrom":makeQuery(id+"F22.opPattern","COPY",BODY,{"derivedFrom":makeQuery(id+"F21.opPattern","COPY",BODY,{"derivedFrom":makeQuery(id+"F20.opPattern","COPY",BODY,{"derivedFrom":makeQuery(id+"F18.opPattern","COPY",BODY,{"derivedFrom":makeQuery(id+"F17.opPattern","COPY",BODY,{"derivedFrom":makeQuery(id+"F16.opExtrude","SWEPT_BODY",BODY,{"disambiguationData":[OSD([sQuery(id+"F15.wireOp",EDGE,"E13.bottom"),sQuery(id+"F15.wireOp",EDGE,"E13.top"),sQuery(id+"F15.wireOp",EDGE,"E13.left"),sQuery(id+"F15.wireOp",EDGE,"E13.right"),sQuery(id+"F15.wireOp",EDGE,"E14.bottom"),sQuery(id+"F15.wireOp",EDGE,"E14.top"),sQuery(id+"F15.wireOp",EDGE,"E14.left"),sQuery(id+"F15.wireOp",EDGE,"E14.right"),sQuery(id+"F15.wireOp",EDGE,"E15.MirrorCS"),sQuery(id+"F15.wireOp",EDGE,"E16.MirrorCS"),sQuery(id+"F15.wireOp",EDGE,"E17.MirrorCS"),sQuery(id+"F15.wireOp",EDGE,"E18.MirrorCS"),sQuery(id+"F15.wireOp",EDGE,"E19.MirrorCS"),sQuery(id+"F15.wireOp",EDGE,"E20.MirrorCS"),sQuery(id+"F15.wireOp",EDGE,"E21.MirrorCS"),sQuery(id+"F15.wireOp",EDGE,"E22.MirrorCS"),sQuery(id+"F15.wireOp",EDGE,"E23.MirrorCS"),sQuery(id+"F15.wireOp",EDGE,"E24.MirrorCS"),sQuery(id+"F15.wireOp",EDGE,"E25.MirrorCS"),sQuery(id+"F15.wireOp",EDGE,"E26.MirrorCS")])]}),"instanceName":"1"}),"instanceName":"1"}),"instanceName":"1"}),"instanceName":"1"}),"instanceName":"1"}),"instanceName":"1"}),"instanceName":"1"});
            var Q53;
            Q53=makeQuery(id+"F24.opPattern","COPY",BODY,{"derivedFrom":makeQuery(id+"F23.opPattern","COPY",BODY,{"derivedFrom":makeQuery(id+"F22.opPattern","COPY",BODY,{"derivedFrom":makeQuery(id+"F21.opPattern","COPY",BODY,{"derivedFrom":makeQuery(id+"F20.opPattern","COPY",BODY,{"derivedFrom":makeQuery(id+"F19.opPattern","COPY",BODY,{"derivedFrom":makeQuery(id+"F16.opExtrude","SWEPT_BODY",BODY,{"disambiguationData":[OSD([sQuery(id+"F15.wireOp",EDGE,"E13.bottom"),sQuery(id+"F15.wireOp",EDGE,"E13.top"),sQuery(id+"F15.wireOp",EDGE,"E13.left"),sQuery(id+"F15.wireOp",EDGE,"E13.right"),sQuery(id+"F15.wireOp",EDGE,"E14.bottom"),sQuery(id+"F15.wireOp",EDGE,"E14.top"),sQuery(id+"F15.wireOp",EDGE,"E14.left"),sQuery(id+"F15.wireOp",EDGE,"E14.right"),sQuery(id+"F15.wireOp",EDGE,"E15.MirrorCS"),sQuery(id+"F15.wireOp",EDGE,"E16.MirrorCS"),sQuery(id+"F15.wireOp",EDGE,"E17.MirrorCS"),sQuery(id+"F15.wireOp",EDGE,"E18.MirrorCS"),sQuery(id+"F15.wireOp",EDGE,"E19.MirrorCS"),sQuery(id+"F15.wireOp",EDGE,"E20.MirrorCS"),sQuery(id+"F15.wireOp",EDGE,"E21.MirrorCS"),sQuery(id+"F15.wireOp",EDGE,"E22.MirrorCS"),sQuery(id+"F15.wireOp",EDGE,"E23.MirrorCS"),sQuery(id+"F15.wireOp",EDGE,"E24.MirrorCS"),sQuery(id+"F15.wireOp",EDGE,"E25.MirrorCS"),sQuery(id+"F15.wireOp",EDGE,"E26.MirrorCS")])]}),"instanceName":"1"}),"instanceName":"1"}),"instanceName":"1"}),"instanceName":"1"}),"instanceName":"1"}),"instanceName":"1"});
            var Q54;
            Q54=makeQuery(id+"F24.opPattern","COPY",BODY,{"derivedFrom":makeQuery(id+"F23.opPattern","COPY",BODY,{"derivedFrom":makeQuery(id+"F22.opPattern","COPY",BODY,{"derivedFrom":makeQuery(id+"F21.opPattern","COPY",BODY,{"derivedFrom":makeQuery(id+"F20.opPattern","COPY",BODY,{"derivedFrom":makeQuery(id+"F19.opPattern","COPY",BODY,{"derivedFrom":makeQuery(id+"F17.opPattern","COPY",BODY,{"derivedFrom":makeQuery(id+"F16.opExtrude","SWEPT_BODY",BODY,{"disambiguationData":[OSD([sQuery(id+"F15.wireOp",EDGE,"E13.bottom"),sQuery(id+"F15.wireOp",EDGE,"E13.top"),sQuery(id+"F15.wireOp",EDGE,"E13.left"),sQuery(id+"F15.wireOp",EDGE,"E13.right"),sQuery(id+"F15.wireOp",EDGE,"E14.bottom"),sQuery(id+"F15.wireOp",EDGE,"E14.top"),sQuery(id+"F15.wireOp",EDGE,"E14.left"),sQuery(id+"F15.wireOp",EDGE,"E14.right"),sQuery(id+"F15.wireOp",EDGE,"E15.MirrorCS"),sQuery(id+"F15.wireOp",EDGE,"E16.MirrorCS"),sQuery(id+"F15.wireOp",EDGE,"E17.MirrorCS"),sQuery(id+"F15.wireOp",EDGE,"E18.MirrorCS"),sQuery(id+"F15.wireOp",EDGE,"E19.MirrorCS"),sQuery(id+"F15.wireOp",EDGE,"E20.MirrorCS"),sQuery(id+"F15.wireOp",EDGE,"E21.MirrorCS"),sQuery(id+"F15.wireOp",EDGE,"E22.MirrorCS"),sQuery(id+"F15.wireOp",EDGE,"E23.MirrorCS"),sQuery(id+"F15.wireOp",EDGE,"E24.MirrorCS"),sQuery(id+"F15.wireOp",EDGE,"E25.MirrorCS"),sQuery(id+"F15.wireOp",EDGE,"E26.MirrorCS")])]}),"instanceName":"1"}),"instanceName":"1"}),"instanceName":"1"}),"instanceName":"1"}),"instanceName":"1"}),"instanceName":"1"}),"instanceName":"1"});
            var Q55;
            Q55=makeQuery(id+"F24.opPattern","COPY",BODY,{"derivedFrom":makeQuery(id+"F23.opPattern","COPY",BODY,{"derivedFrom":makeQuery(id+"F22.opPattern","COPY",BODY,{"derivedFrom":makeQuery(id+"F21.opPattern","COPY",BODY,{"derivedFrom":makeQuery(id+"F20.opPattern","COPY",BODY,{"derivedFrom":makeQuery(id+"F19.opPattern","COPY",BODY,{"derivedFrom":makeQuery(id+"F18.opPattern","COPY",BODY,{"derivedFrom":makeQuery(id+"F16.opExtrude","SWEPT_BODY",BODY,{"disambiguationData":[OSD([sQuery(id+"F15.wireOp",EDGE,"E13.bottom"),sQuery(id+"F15.wireOp",EDGE,"E13.top"),sQuery(id+"F15.wireOp",EDGE,"E13.left"),sQuery(id+"F15.wireOp",EDGE,"E13.right"),sQuery(id+"F15.wireOp",EDGE,"E14.bottom"),sQuery(id+"F15.wireOp",EDGE,"E14.top"),sQuery(id+"F15.wireOp",EDGE,"E14.left"),sQuery(id+"F15.wireOp",EDGE,"E14.right"),sQuery(id+"F15.wireOp",EDGE,"E15.MirrorCS"),sQuery(id+"F15.wireOp",EDGE,"E16.MirrorCS"),sQuery(id+"F15.wireOp",EDGE,"E17.MirrorCS"),sQuery(id+"F15.wireOp",EDGE,"E18.MirrorCS"),sQuery(id+"F15.wireOp",EDGE,"E19.MirrorCS"),sQuery(id+"F15.wireOp",EDGE,"E20.MirrorCS"),sQuery(id+"F15.wireOp",EDGE,"E21.MirrorCS"),sQuery(id+"F15.wireOp",EDGE,"E22.MirrorCS"),sQuery(id+"F15.wireOp",EDGE,"E23.MirrorCS"),sQuery(id+"F15.wireOp",EDGE,"E24.MirrorCS"),sQuery(id+"F15.wireOp",EDGE,"E25.MirrorCS"),sQuery(id+"F15.wireOp",EDGE,"E26.MirrorCS")])]}),"instanceName":"1"}),"instanceName":"1"}),"instanceName":"1"}),"instanceName":"1"}),"instanceName":"1"}),"instanceName":"1"}),"instanceName":"1"});
            var Q56;
            Q56=makeQuery(id+"F19.opPattern","COPY",BODY,{"derivedFrom":makeQuery(id+"F16.opExtrude","SWEPT_BODY",BODY,{"disambiguationData":[OSD([sQuery(id+"F15.wireOp",EDGE,"E13.bottom"),sQuery(id+"F15.wireOp",EDGE,"E13.top"),sQuery(id+"F15.wireOp",EDGE,"E13.left"),sQuery(id+"F15.wireOp",EDGE,"E13.right"),sQuery(id+"F15.wireOp",EDGE,"E14.bottom"),sQuery(id+"F15.wireOp",EDGE,"E14.top"),sQuery(id+"F15.wireOp",EDGE,"E14.left"),sQuery(id+"F15.wireOp",EDGE,"E14.right"),sQuery(id+"F15.wireOp",EDGE,"E15.MirrorCS"),sQuery(id+"F15.wireOp",EDGE,"E16.MirrorCS"),sQuery(id+"F15.wireOp",EDGE,"E17.MirrorCS"),sQuery(id+"F15.wireOp",EDGE,"E18.MirrorCS"),sQuery(id+"F15.wireOp",EDGE,"E19.MirrorCS"),sQuery(id+"F15.wireOp",EDGE,"E20.MirrorCS"),sQuery(id+"F15.wireOp",EDGE,"E21.MirrorCS"),sQuery(id+"F15.wireOp",EDGE,"E22.MirrorCS"),sQuery(id+"F15.wireOp",EDGE,"E23.MirrorCS"),sQuery(id+"F15.wireOp",EDGE,"E24.MirrorCS"),sQuery(id+"F15.wireOp",EDGE,"E25.MirrorCS"),sQuery(id+"F15.wireOp",EDGE,"E26.MirrorCS")])]}),"instanceName":"1"});
            var Q57;
            Q57=makeQuery(id+"F19.opPattern","COPY",BODY,{"derivedFrom":makeQuery(id+"F17.opPattern","COPY",BODY,{"derivedFrom":makeQuery(id+"F16.opExtrude","SWEPT_BODY",BODY,{"disambiguationData":[OSD([sQuery(id+"F15.wireOp",EDGE,"E13.bottom"),sQuery(id+"F15.wireOp",EDGE,"E13.top"),sQuery(id+"F15.wireOp",EDGE,"E13.left"),sQuery(id+"F15.wireOp",EDGE,"E13.right"),sQuery(id+"F15.wireOp",EDGE,"E14.bottom"),sQuery(id+"F15.wireOp",EDGE,"E14.top"),sQuery(id+"F15.wireOp",EDGE,"E14.left"),sQuery(id+"F15.wireOp",EDGE,"E14.right"),sQuery(id+"F15.wireOp",EDGE,"E15.MirrorCS"),sQuery(id+"F15.wireOp",EDGE,"E16.MirrorCS"),sQuery(id+"F15.wireOp",EDGE,"E17.MirrorCS"),sQuery(id+"F15.wireOp",EDGE,"E18.MirrorCS"),sQuery(id+"F15.wireOp",EDGE,"E19.MirrorCS"),sQuery(id+"F15.wireOp",EDGE,"E20.MirrorCS"),sQuery(id+"F15.wireOp",EDGE,"E21.MirrorCS"),sQuery(id+"F15.wireOp",EDGE,"E22.MirrorCS"),sQuery(id+"F15.wireOp",EDGE,"E23.MirrorCS"),sQuery(id+"F15.wireOp",EDGE,"E24.MirrorCS"),sQuery(id+"F15.wireOp",EDGE,"E25.MirrorCS"),sQuery(id+"F15.wireOp",EDGE,"E26.MirrorCS")])]}),"instanceName":"1"}),"instanceName":"1"});
            var Q58;
            Q58=makeQuery(id+"F19.opPattern","COPY",BODY,{"derivedFrom":makeQuery(id+"F18.opPattern","COPY",BODY,{"derivedFrom":makeQuery(id+"F16.opExtrude","SWEPT_BODY",BODY,{"disambiguationData":[OSD([sQuery(id+"F15.wireOp",EDGE,"E13.bottom"),sQuery(id+"F15.wireOp",EDGE,"E13.top"),sQuery(id+"F15.wireOp",EDGE,"E13.left"),sQuery(id+"F15.wireOp",EDGE,"E13.right"),sQuery(id+"F15.wireOp",EDGE,"E14.bottom"),sQuery(id+"F15.wireOp",EDGE,"E14.top"),sQuery(id+"F15.wireOp",EDGE,"E14.left"),sQuery(id+"F15.wireOp",EDGE,"E14.right"),sQuery(id+"F15.wireOp",EDGE,"E15.MirrorCS"),sQuery(id+"F15.wireOp",EDGE,"E16.MirrorCS"),sQuery(id+"F15.wireOp",EDGE,"E17.MirrorCS"),sQuery(id+"F15.wireOp",EDGE,"E18.MirrorCS"),sQuery(id+"F15.wireOp",EDGE,"E19.MirrorCS"),sQuery(id+"F15.wireOp",EDGE,"E20.MirrorCS"),sQuery(id+"F15.wireOp",EDGE,"E21.MirrorCS"),sQuery(id+"F15.wireOp",EDGE,"E22.MirrorCS"),sQuery(id+"F15.wireOp",EDGE,"E23.MirrorCS"),sQuery(id+"F15.wireOp",EDGE,"E24.MirrorCS"),sQuery(id+"F15.wireOp",EDGE,"E25.MirrorCS"),sQuery(id+"F15.wireOp",EDGE,"E26.MirrorCS")])]}),"instanceName":"1"}),"instanceName":"1"});
            var Q59;
            Q59=makeQuery(id+"F19.opPattern","COPY",BODY,{"derivedFrom":makeQuery(id+"F18.opPattern","COPY",BODY,{"derivedFrom":makeQuery(id+"F17.opPattern","COPY",BODY,{"derivedFrom":makeQuery(id+"F16.opExtrude","SWEPT_BODY",BODY,{"disambiguationData":[OSD([sQuery(id+"F15.wireOp",EDGE,"E13.bottom"),sQuery(id+"F15.wireOp",EDGE,"E13.top"),sQuery(id+"F15.wireOp",EDGE,"E13.left"),sQuery(id+"F15.wireOp",EDGE,"E13.right"),sQuery(id+"F15.wireOp",EDGE,"E14.bottom"),sQuery(id+"F15.wireOp",EDGE,"E14.top"),sQuery(id+"F15.wireOp",EDGE,"E14.left"),sQuery(id+"F15.wireOp",EDGE,"E14.right"),sQuery(id+"F15.wireOp",EDGE,"E15.MirrorCS"),sQuery(id+"F15.wireOp",EDGE,"E16.MirrorCS"),sQuery(id+"F15.wireOp",EDGE,"E17.MirrorCS"),sQuery(id+"F15.wireOp",EDGE,"E18.MirrorCS"),sQuery(id+"F15.wireOp",EDGE,"E19.MirrorCS"),sQuery(id+"F15.wireOp",EDGE,"E20.MirrorCS"),sQuery(id+"F15.wireOp",EDGE,"E21.MirrorCS"),sQuery(id+"F15.wireOp",EDGE,"E22.MirrorCS"),sQuery(id+"F15.wireOp",EDGE,"E23.MirrorCS"),sQuery(id+"F15.wireOp",EDGE,"E24.MirrorCS"),sQuery(id+"F15.wireOp",EDGE,"E25.MirrorCS"),sQuery(id+"F15.wireOp",EDGE,"E26.MirrorCS")])]}),"instanceName":"1"}),"instanceName":"1"}),"instanceName":"1"});
            var Q60;
            Q60=makeQuery(id+"F20.opPattern","COPY",BODY,{"derivedFrom":makeQuery(id+"F16.opExtrude","SWEPT_BODY",BODY,{"disambiguationData":[OSD([sQuery(id+"F15.wireOp",EDGE,"E13.bottom"),sQuery(id+"F15.wireOp",EDGE,"E13.top"),sQuery(id+"F15.wireOp",EDGE,"E13.left"),sQuery(id+"F15.wireOp",EDGE,"E13.right"),sQuery(id+"F15.wireOp",EDGE,"E14.bottom"),sQuery(id+"F15.wireOp",EDGE,"E14.top"),sQuery(id+"F15.wireOp",EDGE,"E14.left"),sQuery(id+"F15.wireOp",EDGE,"E14.right"),sQuery(id+"F15.wireOp",EDGE,"E15.MirrorCS"),sQuery(id+"F15.wireOp",EDGE,"E16.MirrorCS"),sQuery(id+"F15.wireOp",EDGE,"E17.MirrorCS"),sQuery(id+"F15.wireOp",EDGE,"E18.MirrorCS"),sQuery(id+"F15.wireOp",EDGE,"E19.MirrorCS"),sQuery(id+"F15.wireOp",EDGE,"E20.MirrorCS"),sQuery(id+"F15.wireOp",EDGE,"E21.MirrorCS"),sQuery(id+"F15.wireOp",EDGE,"E22.MirrorCS"),sQuery(id+"F15.wireOp",EDGE,"E23.MirrorCS"),sQuery(id+"F15.wireOp",EDGE,"E24.MirrorCS"),sQuery(id+"F15.wireOp",EDGE,"E25.MirrorCS"),sQuery(id+"F15.wireOp",EDGE,"E26.MirrorCS")])]}),"instanceName":"1"});
            var Q61;
            Q61=makeQuery(id+"F20.opPattern","COPY",BODY,{"derivedFrom":makeQuery(id+"F17.opPattern","COPY",BODY,{"derivedFrom":makeQuery(id+"F16.opExtrude","SWEPT_BODY",BODY,{"disambiguationData":[OSD([sQuery(id+"F15.wireOp",EDGE,"E13.bottom"),sQuery(id+"F15.wireOp",EDGE,"E13.top"),sQuery(id+"F15.wireOp",EDGE,"E13.left"),sQuery(id+"F15.wireOp",EDGE,"E13.right"),sQuery(id+"F15.wireOp",EDGE,"E14.bottom"),sQuery(id+"F15.wireOp",EDGE,"E14.top"),sQuery(id+"F15.wireOp",EDGE,"E14.left"),sQuery(id+"F15.wireOp",EDGE,"E14.right"),sQuery(id+"F15.wireOp",EDGE,"E15.MirrorCS"),sQuery(id+"F15.wireOp",EDGE,"E16.MirrorCS"),sQuery(id+"F15.wireOp",EDGE,"E17.MirrorCS"),sQuery(id+"F15.wireOp",EDGE,"E18.MirrorCS"),sQuery(id+"F15.wireOp",EDGE,"E19.MirrorCS"),sQuery(id+"F15.wireOp",EDGE,"E20.MirrorCS"),sQuery(id+"F15.wireOp",EDGE,"E21.MirrorCS"),sQuery(id+"F15.wireOp",EDGE,"E22.MirrorCS"),sQuery(id+"F15.wireOp",EDGE,"E23.MirrorCS"),sQuery(id+"F15.wireOp",EDGE,"E24.MirrorCS"),sQuery(id+"F15.wireOp",EDGE,"E25.MirrorCS"),sQuery(id+"F15.wireOp",EDGE,"E26.MirrorCS")])]}),"instanceName":"1"}),"instanceName":"1"});
            var Q62;
            Q62=makeQuery(id+"F20.opPattern","COPY",BODY,{"derivedFrom":makeQuery(id+"F18.opPattern","COPY",BODY,{"derivedFrom":makeQuery(id+"F16.opExtrude","SWEPT_BODY",BODY,{"disambiguationData":[OSD([sQuery(id+"F15.wireOp",EDGE,"E13.bottom"),sQuery(id+"F15.wireOp",EDGE,"E13.top"),sQuery(id+"F15.wireOp",EDGE,"E13.left"),sQuery(id+"F15.wireOp",EDGE,"E13.right"),sQuery(id+"F15.wireOp",EDGE,"E14.bottom"),sQuery(id+"F15.wireOp",EDGE,"E14.top"),sQuery(id+"F15.wireOp",EDGE,"E14.left"),sQuery(id+"F15.wireOp",EDGE,"E14.right"),sQuery(id+"F15.wireOp",EDGE,"E15.MirrorCS"),sQuery(id+"F15.wireOp",EDGE,"E16.MirrorCS"),sQuery(id+"F15.wireOp",EDGE,"E17.MirrorCS"),sQuery(id+"F15.wireOp",EDGE,"E18.MirrorCS"),sQuery(id+"F15.wireOp",EDGE,"E19.MirrorCS"),sQuery(id+"F15.wireOp",EDGE,"E20.MirrorCS"),sQuery(id+"F15.wireOp",EDGE,"E21.MirrorCS"),sQuery(id+"F15.wireOp",EDGE,"E22.MirrorCS"),sQuery(id+"F15.wireOp",EDGE,"E23.MirrorCS"),sQuery(id+"F15.wireOp",EDGE,"E24.MirrorCS"),sQuery(id+"F15.wireOp",EDGE,"E25.MirrorCS"),sQuery(id+"F15.wireOp",EDGE,"E26.MirrorCS")])]}),"instanceName":"1"}),"instanceName":"1"});
            var Q63;
            Q63=makeQuery(id+"F20.opPattern","COPY",BODY,{"derivedFrom":makeQuery(id+"F18.opPattern","COPY",BODY,{"derivedFrom":makeQuery(id+"F17.opPattern","COPY",BODY,{"derivedFrom":makeQuery(id+"F16.opExtrude","SWEPT_BODY",BODY,{"disambiguationData":[OSD([sQuery(id+"F15.wireOp",EDGE,"E13.bottom"),sQuery(id+"F15.wireOp",EDGE,"E13.top"),sQuery(id+"F15.wireOp",EDGE,"E13.left"),sQuery(id+"F15.wireOp",EDGE,"E13.right"),sQuery(id+"F15.wireOp",EDGE,"E14.bottom"),sQuery(id+"F15.wireOp",EDGE,"E14.top"),sQuery(id+"F15.wireOp",EDGE,"E14.left"),sQuery(id+"F15.wireOp",EDGE,"E14.right"),sQuery(id+"F15.wireOp",EDGE,"E15.MirrorCS"),sQuery(id+"F15.wireOp",EDGE,"E16.MirrorCS"),sQuery(id+"F15.wireOp",EDGE,"E17.MirrorCS"),sQuery(id+"F15.wireOp",EDGE,"E18.MirrorCS"),sQuery(id+"F15.wireOp",EDGE,"E19.MirrorCS"),sQuery(id+"F15.wireOp",EDGE,"E20.MirrorCS"),sQuery(id+"F15.wireOp",EDGE,"E21.MirrorCS"),sQuery(id+"F15.wireOp",EDGE,"E22.MirrorCS"),sQuery(id+"F15.wireOp",EDGE,"E23.MirrorCS"),sQuery(id+"F15.wireOp",EDGE,"E24.MirrorCS"),sQuery(id+"F15.wireOp",EDGE,"E25.MirrorCS"),sQuery(id+"F15.wireOp",EDGE,"E26.MirrorCS")])]}),"instanceName":"1"}),"instanceName":"1"}),"instanceName":"1"});
            var Q64;
            Q64=makeQuery(id+"F20.opPattern","COPY",BODY,{"derivedFrom":makeQuery(id+"F19.opPattern","COPY",BODY,{"derivedFrom":makeQuery(id+"F16.opExtrude","SWEPT_BODY",BODY,{"disambiguationData":[OSD([sQuery(id+"F15.wireOp",EDGE,"E13.bottom"),sQuery(id+"F15.wireOp",EDGE,"E13.top"),sQuery(id+"F15.wireOp",EDGE,"E13.left"),sQuery(id+"F15.wireOp",EDGE,"E13.right"),sQuery(id+"F15.wireOp",EDGE,"E14.bottom"),sQuery(id+"F15.wireOp",EDGE,"E14.top"),sQuery(id+"F15.wireOp",EDGE,"E14.left"),sQuery(id+"F15.wireOp",EDGE,"E14.right"),sQuery(id+"F15.wireOp",EDGE,"E15.MirrorCS"),sQuery(id+"F15.wireOp",EDGE,"E16.MirrorCS"),sQuery(id+"F15.wireOp",EDGE,"E17.MirrorCS"),sQuery(id+"F15.wireOp",EDGE,"E18.MirrorCS"),sQuery(id+"F15.wireOp",EDGE,"E19.MirrorCS"),sQuery(id+"F15.wireOp",EDGE,"E20.MirrorCS"),sQuery(id+"F15.wireOp",EDGE,"E21.MirrorCS"),sQuery(id+"F15.wireOp",EDGE,"E22.MirrorCS"),sQuery(id+"F15.wireOp",EDGE,"E23.MirrorCS"),sQuery(id+"F15.wireOp",EDGE,"E24.MirrorCS"),sQuery(id+"F15.wireOp",EDGE,"E25.MirrorCS"),sQuery(id+"F15.wireOp",EDGE,"E26.MirrorCS")])]}),"instanceName":"1"}),"instanceName":"1"});
            var Q65;
            Q65=makeQuery(id+"F20.opPattern","COPY",BODY,{"derivedFrom":makeQuery(id+"F19.opPattern","COPY",BODY,{"derivedFrom":makeQuery(id+"F17.opPattern","COPY",BODY,{"derivedFrom":makeQuery(id+"F16.opExtrude","SWEPT_BODY",BODY,{"disambiguationData":[OSD([sQuery(id+"F15.wireOp",EDGE,"E13.bottom"),sQuery(id+"F15.wireOp",EDGE,"E13.top"),sQuery(id+"F15.wireOp",EDGE,"E13.left"),sQuery(id+"F15.wireOp",EDGE,"E13.right"),sQuery(id+"F15.wireOp",EDGE,"E14.bottom"),sQuery(id+"F15.wireOp",EDGE,"E14.top"),sQuery(id+"F15.wireOp",EDGE,"E14.left"),sQuery(id+"F15.wireOp",EDGE,"E14.right"),sQuery(id+"F15.wireOp",EDGE,"E15.MirrorCS"),sQuery(id+"F15.wireOp",EDGE,"E16.MirrorCS"),sQuery(id+"F15.wireOp",EDGE,"E17.MirrorCS"),sQuery(id+"F15.wireOp",EDGE,"E18.MirrorCS"),sQuery(id+"F15.wireOp",EDGE,"E19.MirrorCS"),sQuery(id+"F15.wireOp",EDGE,"E20.MirrorCS"),sQuery(id+"F15.wireOp",EDGE,"E21.MirrorCS"),sQuery(id+"F15.wireOp",EDGE,"E22.MirrorCS"),sQuery(id+"F15.wireOp",EDGE,"E23.MirrorCS"),sQuery(id+"F15.wireOp",EDGE,"E24.MirrorCS"),sQuery(id+"F15.wireOp",EDGE,"E25.MirrorCS"),sQuery(id+"F15.wireOp",EDGE,"E26.MirrorCS")])]}),"instanceName":"1"}),"instanceName":"1"}),"instanceName":"1"});
            var Q66;
            Q66=makeQuery(id+"F20.opPattern","COPY",BODY,{"derivedFrom":makeQuery(id+"F19.opPattern","COPY",BODY,{"derivedFrom":makeQuery(id+"F18.opPattern","COPY",BODY,{"derivedFrom":makeQuery(id+"F16.opExtrude","SWEPT_BODY",BODY,{"disambiguationData":[OSD([sQuery(id+"F15.wireOp",EDGE,"E13.bottom"),sQuery(id+"F15.wireOp",EDGE,"E13.top"),sQuery(id+"F15.wireOp",EDGE,"E13.left"),sQuery(id+"F15.wireOp",EDGE,"E13.right"),sQuery(id+"F15.wireOp",EDGE,"E14.bottom"),sQuery(id+"F15.wireOp",EDGE,"E14.top"),sQuery(id+"F15.wireOp",EDGE,"E14.left"),sQuery(id+"F15.wireOp",EDGE,"E14.right"),sQuery(id+"F15.wireOp",EDGE,"E15.MirrorCS"),sQuery(id+"F15.wireOp",EDGE,"E16.MirrorCS"),sQuery(id+"F15.wireOp",EDGE,"E17.MirrorCS"),sQuery(id+"F15.wireOp",EDGE,"E18.MirrorCS"),sQuery(id+"F15.wireOp",EDGE,"E19.MirrorCS"),sQuery(id+"F15.wireOp",EDGE,"E20.MirrorCS"),sQuery(id+"F15.wireOp",EDGE,"E21.MirrorCS"),sQuery(id+"F15.wireOp",EDGE,"E22.MirrorCS"),sQuery(id+"F15.wireOp",EDGE,"E23.MirrorCS"),sQuery(id+"F15.wireOp",EDGE,"E24.MirrorCS"),sQuery(id+"F15.wireOp",EDGE,"E25.MirrorCS"),sQuery(id+"F15.wireOp",EDGE,"E26.MirrorCS")])]}),"instanceName":"1"}),"instanceName":"1"}),"instanceName":"1"});
            var Q67;
            Q67=makeQuery(id+"F20.opPattern","COPY",BODY,{"derivedFrom":makeQuery(id+"F19.opPattern","COPY",BODY,{"derivedFrom":makeQuery(id+"F18.opPattern","COPY",BODY,{"derivedFrom":makeQuery(id+"F17.opPattern","COPY",BODY,{"derivedFrom":makeQuery(id+"F16.opExtrude","SWEPT_BODY",BODY,{"disambiguationData":[OSD([sQuery(id+"F15.wireOp",EDGE,"E13.bottom"),sQuery(id+"F15.wireOp",EDGE,"E13.top"),sQuery(id+"F15.wireOp",EDGE,"E13.left"),sQuery(id+"F15.wireOp",EDGE,"E13.right"),sQuery(id+"F15.wireOp",EDGE,"E14.bottom"),sQuery(id+"F15.wireOp",EDGE,"E14.top"),sQuery(id+"F15.wireOp",EDGE,"E14.left"),sQuery(id+"F15.wireOp",EDGE,"E14.right"),sQuery(id+"F15.wireOp",EDGE,"E15.MirrorCS"),sQuery(id+"F15.wireOp",EDGE,"E16.MirrorCS"),sQuery(id+"F15.wireOp",EDGE,"E17.MirrorCS"),sQuery(id+"F15.wireOp",EDGE,"E18.MirrorCS"),sQuery(id+"F15.wireOp",EDGE,"E19.MirrorCS"),sQuery(id+"F15.wireOp",EDGE,"E20.MirrorCS"),sQuery(id+"F15.wireOp",EDGE,"E21.MirrorCS"),sQuery(id+"F15.wireOp",EDGE,"E22.MirrorCS"),sQuery(id+"F15.wireOp",EDGE,"E23.MirrorCS"),sQuery(id+"F15.wireOp",EDGE,"E24.MirrorCS"),sQuery(id+"F15.wireOp",EDGE,"E25.MirrorCS"),sQuery(id+"F15.wireOp",EDGE,"E26.MirrorCS")])]}),"instanceName":"1"}),"instanceName":"1"}),"instanceName":"1"}),"instanceName":"1"});
            var Q68;
            Q68=makeQuery(id+"F21.opPattern","COPY",BODY,{"derivedFrom":makeQuery(id+"F16.opExtrude","SWEPT_BODY",BODY,{"disambiguationData":[OSD([sQuery(id+"F15.wireOp",EDGE,"E13.bottom"),sQuery(id+"F15.wireOp",EDGE,"E13.top"),sQuery(id+"F15.wireOp",EDGE,"E13.left"),sQuery(id+"F15.wireOp",EDGE,"E13.right"),sQuery(id+"F15.wireOp",EDGE,"E14.bottom"),sQuery(id+"F15.wireOp",EDGE,"E14.top"),sQuery(id+"F15.wireOp",EDGE,"E14.left"),sQuery(id+"F15.wireOp",EDGE,"E14.right"),sQuery(id+"F15.wireOp",EDGE,"E15.MirrorCS"),sQuery(id+"F15.wireOp",EDGE,"E16.MirrorCS"),sQuery(id+"F15.wireOp",EDGE,"E17.MirrorCS"),sQuery(id+"F15.wireOp",EDGE,"E18.MirrorCS"),sQuery(id+"F15.wireOp",EDGE,"E19.MirrorCS"),sQuery(id+"F15.wireOp",EDGE,"E20.MirrorCS"),sQuery(id+"F15.wireOp",EDGE,"E21.MirrorCS"),sQuery(id+"F15.wireOp",EDGE,"E22.MirrorCS"),sQuery(id+"F15.wireOp",EDGE,"E23.MirrorCS"),sQuery(id+"F15.wireOp",EDGE,"E24.MirrorCS"),sQuery(id+"F15.wireOp",EDGE,"E25.MirrorCS"),sQuery(id+"F15.wireOp",EDGE,"E26.MirrorCS")])]}),"instanceName":"1"});
            var Q69;
            Q69=makeQuery(id+"F21.opPattern","COPY",BODY,{"derivedFrom":makeQuery(id+"F17.opPattern","COPY",BODY,{"derivedFrom":makeQuery(id+"F16.opExtrude","SWEPT_BODY",BODY,{"disambiguationData":[OSD([sQuery(id+"F15.wireOp",EDGE,"E13.bottom"),sQuery(id+"F15.wireOp",EDGE,"E13.top"),sQuery(id+"F15.wireOp",EDGE,"E13.left"),sQuery(id+"F15.wireOp",EDGE,"E13.right"),sQuery(id+"F15.wireOp",EDGE,"E14.bottom"),sQuery(id+"F15.wireOp",EDGE,"E14.top"),sQuery(id+"F15.wireOp",EDGE,"E14.left"),sQuery(id+"F15.wireOp",EDGE,"E14.right"),sQuery(id+"F15.wireOp",EDGE,"E15.MirrorCS"),sQuery(id+"F15.wireOp",EDGE,"E16.MirrorCS"),sQuery(id+"F15.wireOp",EDGE,"E17.MirrorCS"),sQuery(id+"F15.wireOp",EDGE,"E18.MirrorCS"),sQuery(id+"F15.wireOp",EDGE,"E19.MirrorCS"),sQuery(id+"F15.wireOp",EDGE,"E20.MirrorCS"),sQuery(id+"F15.wireOp",EDGE,"E21.MirrorCS"),sQuery(id+"F15.wireOp",EDGE,"E22.MirrorCS"),sQuery(id+"F15.wireOp",EDGE,"E23.MirrorCS"),sQuery(id+"F15.wireOp",EDGE,"E24.MirrorCS"),sQuery(id+"F15.wireOp",EDGE,"E25.MirrorCS"),sQuery(id+"F15.wireOp",EDGE,"E26.MirrorCS")])]}),"instanceName":"1"}),"instanceName":"1"});
            var Q70;
            Q70=makeQuery(id+"F21.opPattern","COPY",BODY,{"derivedFrom":makeQuery(id+"F18.opPattern","COPY",BODY,{"derivedFrom":makeQuery(id+"F16.opExtrude","SWEPT_BODY",BODY,{"disambiguationData":[OSD([sQuery(id+"F15.wireOp",EDGE,"E13.bottom"),sQuery(id+"F15.wireOp",EDGE,"E13.top"),sQuery(id+"F15.wireOp",EDGE,"E13.left"),sQuery(id+"F15.wireOp",EDGE,"E13.right"),sQuery(id+"F15.wireOp",EDGE,"E14.bottom"),sQuery(id+"F15.wireOp",EDGE,"E14.top"),sQuery(id+"F15.wireOp",EDGE,"E14.left"),sQuery(id+"F15.wireOp",EDGE,"E14.right"),sQuery(id+"F15.wireOp",EDGE,"E15.MirrorCS"),sQuery(id+"F15.wireOp",EDGE,"E16.MirrorCS"),sQuery(id+"F15.wireOp",EDGE,"E17.MirrorCS"),sQuery(id+"F15.wireOp",EDGE,"E18.MirrorCS"),sQuery(id+"F15.wireOp",EDGE,"E19.MirrorCS"),sQuery(id+"F15.wireOp",EDGE,"E20.MirrorCS"),sQuery(id+"F15.wireOp",EDGE,"E21.MirrorCS"),sQuery(id+"F15.wireOp",EDGE,"E22.MirrorCS"),sQuery(id+"F15.wireOp",EDGE,"E23.MirrorCS"),sQuery(id+"F15.wireOp",EDGE,"E24.MirrorCS"),sQuery(id+"F15.wireOp",EDGE,"E25.MirrorCS"),sQuery(id+"F15.wireOp",EDGE,"E26.MirrorCS")])]}),"instanceName":"1"}),"instanceName":"1"});
            var Q71;
            Q71=makeQuery(id+"F21.opPattern","COPY",BODY,{"derivedFrom":makeQuery(id+"F18.opPattern","COPY",BODY,{"derivedFrom":makeQuery(id+"F17.opPattern","COPY",BODY,{"derivedFrom":makeQuery(id+"F16.opExtrude","SWEPT_BODY",BODY,{"disambiguationData":[OSD([sQuery(id+"F15.wireOp",EDGE,"E13.bottom"),sQuery(id+"F15.wireOp",EDGE,"E13.top"),sQuery(id+"F15.wireOp",EDGE,"E13.left"),sQuery(id+"F15.wireOp",EDGE,"E13.right"),sQuery(id+"F15.wireOp",EDGE,"E14.bottom"),sQuery(id+"F15.wireOp",EDGE,"E14.top"),sQuery(id+"F15.wireOp",EDGE,"E14.left"),sQuery(id+"F15.wireOp",EDGE,"E14.right"),sQuery(id+"F15.wireOp",EDGE,"E15.MirrorCS"),sQuery(id+"F15.wireOp",EDGE,"E16.MirrorCS"),sQuery(id+"F15.wireOp",EDGE,"E17.MirrorCS"),sQuery(id+"F15.wireOp",EDGE,"E18.MirrorCS"),sQuery(id+"F15.wireOp",EDGE,"E19.MirrorCS"),sQuery(id+"F15.wireOp",EDGE,"E20.MirrorCS"),sQuery(id+"F15.wireOp",EDGE,"E21.MirrorCS"),sQuery(id+"F15.wireOp",EDGE,"E22.MirrorCS"),sQuery(id+"F15.wireOp",EDGE,"E23.MirrorCS"),sQuery(id+"F15.wireOp",EDGE,"E24.MirrorCS"),sQuery(id+"F15.wireOp",EDGE,"E25.MirrorCS"),sQuery(id+"F15.wireOp",EDGE,"E26.MirrorCS")])]}),"instanceName":"1"}),"instanceName":"1"}),"instanceName":"1"});
            var Q72;
            Q72=makeQuery(id+"F21.opPattern","COPY",BODY,{"derivedFrom":makeQuery(id+"F19.opPattern","COPY",BODY,{"derivedFrom":makeQuery(id+"F16.opExtrude","SWEPT_BODY",BODY,{"disambiguationData":[OSD([sQuery(id+"F15.wireOp",EDGE,"E13.bottom"),sQuery(id+"F15.wireOp",EDGE,"E13.top"),sQuery(id+"F15.wireOp",EDGE,"E13.left"),sQuery(id+"F15.wireOp",EDGE,"E13.right"),sQuery(id+"F15.wireOp",EDGE,"E14.bottom"),sQuery(id+"F15.wireOp",EDGE,"E14.top"),sQuery(id+"F15.wireOp",EDGE,"E14.left"),sQuery(id+"F15.wireOp",EDGE,"E14.right"),sQuery(id+"F15.wireOp",EDGE,"E15.MirrorCS"),sQuery(id+"F15.wireOp",EDGE,"E16.MirrorCS"),sQuery(id+"F15.wireOp",EDGE,"E17.MirrorCS"),sQuery(id+"F15.wireOp",EDGE,"E18.MirrorCS"),sQuery(id+"F15.wireOp",EDGE,"E19.MirrorCS"),sQuery(id+"F15.wireOp",EDGE,"E20.MirrorCS"),sQuery(id+"F15.wireOp",EDGE,"E21.MirrorCS"),sQuery(id+"F15.wireOp",EDGE,"E22.MirrorCS"),sQuery(id+"F15.wireOp",EDGE,"E23.MirrorCS"),sQuery(id+"F15.wireOp",EDGE,"E24.MirrorCS"),sQuery(id+"F15.wireOp",EDGE,"E25.MirrorCS"),sQuery(id+"F15.wireOp",EDGE,"E26.MirrorCS")])]}),"instanceName":"1"}),"instanceName":"1"});
            var Q73;
            Q73=makeQuery(id+"F21.opPattern","COPY",BODY,{"derivedFrom":makeQuery(id+"F19.opPattern","COPY",BODY,{"derivedFrom":makeQuery(id+"F17.opPattern","COPY",BODY,{"derivedFrom":makeQuery(id+"F16.opExtrude","SWEPT_BODY",BODY,{"disambiguationData":[OSD([sQuery(id+"F15.wireOp",EDGE,"E13.bottom"),sQuery(id+"F15.wireOp",EDGE,"E13.top"),sQuery(id+"F15.wireOp",EDGE,"E13.left"),sQuery(id+"F15.wireOp",EDGE,"E13.right"),sQuery(id+"F15.wireOp",EDGE,"E14.bottom"),sQuery(id+"F15.wireOp",EDGE,"E14.top"),sQuery(id+"F15.wireOp",EDGE,"E14.left"),sQuery(id+"F15.wireOp",EDGE,"E14.right"),sQuery(id+"F15.wireOp",EDGE,"E15.MirrorCS"),sQuery(id+"F15.wireOp",EDGE,"E16.MirrorCS"),sQuery(id+"F15.wireOp",EDGE,"E17.MirrorCS"),sQuery(id+"F15.wireOp",EDGE,"E18.MirrorCS"),sQuery(id+"F15.wireOp",EDGE,"E19.MirrorCS"),sQuery(id+"F15.wireOp",EDGE,"E20.MirrorCS"),sQuery(id+"F15.wireOp",EDGE,"E21.MirrorCS"),sQuery(id+"F15.wireOp",EDGE,"E22.MirrorCS"),sQuery(id+"F15.wireOp",EDGE,"E23.MirrorCS"),sQuery(id+"F15.wireOp",EDGE,"E24.MirrorCS"),sQuery(id+"F15.wireOp",EDGE,"E25.MirrorCS"),sQuery(id+"F15.wireOp",EDGE,"E26.MirrorCS")])]}),"instanceName":"1"}),"instanceName":"1"}),"instanceName":"1"});
            var Q74;
            Q74=makeQuery(id+"F21.opPattern","COPY",BODY,{"derivedFrom":makeQuery(id+"F19.opPattern","COPY",BODY,{"derivedFrom":makeQuery(id+"F18.opPattern","COPY",BODY,{"derivedFrom":makeQuery(id+"F16.opExtrude","SWEPT_BODY",BODY,{"disambiguationData":[OSD([sQuery(id+"F15.wireOp",EDGE,"E13.bottom"),sQuery(id+"F15.wireOp",EDGE,"E13.top"),sQuery(id+"F15.wireOp",EDGE,"E13.left"),sQuery(id+"F15.wireOp",EDGE,"E13.right"),sQuery(id+"F15.wireOp",EDGE,"E14.bottom"),sQuery(id+"F15.wireOp",EDGE,"E14.top"),sQuery(id+"F15.wireOp",EDGE,"E14.left"),sQuery(id+"F15.wireOp",EDGE,"E14.right"),sQuery(id+"F15.wireOp",EDGE,"E15.MirrorCS"),sQuery(id+"F15.wireOp",EDGE,"E16.MirrorCS"),sQuery(id+"F15.wireOp",EDGE,"E17.MirrorCS"),sQuery(id+"F15.wireOp",EDGE,"E18.MirrorCS"),sQuery(id+"F15.wireOp",EDGE,"E19.MirrorCS"),sQuery(id+"F15.wireOp",EDGE,"E20.MirrorCS"),sQuery(id+"F15.wireOp",EDGE,"E21.MirrorCS"),sQuery(id+"F15.wireOp",EDGE,"E22.MirrorCS"),sQuery(id+"F15.wireOp",EDGE,"E23.MirrorCS"),sQuery(id+"F15.wireOp",EDGE,"E24.MirrorCS"),sQuery(id+"F15.wireOp",EDGE,"E25.MirrorCS"),sQuery(id+"F15.wireOp",EDGE,"E26.MirrorCS")])]}),"instanceName":"1"}),"instanceName":"1"}),"instanceName":"1"});
            var Q75;
            Q75=makeQuery(id+"F21.opPattern","COPY",BODY,{"derivedFrom":makeQuery(id+"F19.opPattern","COPY",BODY,{"derivedFrom":makeQuery(id+"F18.opPattern","COPY",BODY,{"derivedFrom":makeQuery(id+"F17.opPattern","COPY",BODY,{"derivedFrom":makeQuery(id+"F16.opExtrude","SWEPT_BODY",BODY,{"disambiguationData":[OSD([sQuery(id+"F15.wireOp",EDGE,"E13.bottom"),sQuery(id+"F15.wireOp",EDGE,"E13.top"),sQuery(id+"F15.wireOp",EDGE,"E13.left"),sQuery(id+"F15.wireOp",EDGE,"E13.right"),sQuery(id+"F15.wireOp",EDGE,"E14.bottom"),sQuery(id+"F15.wireOp",EDGE,"E14.top"),sQuery(id+"F15.wireOp",EDGE,"E14.left"),sQuery(id+"F15.wireOp",EDGE,"E14.right"),sQuery(id+"F15.wireOp",EDGE,"E15.MirrorCS"),sQuery(id+"F15.wireOp",EDGE,"E16.MirrorCS"),sQuery(id+"F15.wireOp",EDGE,"E17.MirrorCS"),sQuery(id+"F15.wireOp",EDGE,"E18.MirrorCS"),sQuery(id+"F15.wireOp",EDGE,"E19.MirrorCS"),sQuery(id+"F15.wireOp",EDGE,"E20.MirrorCS"),sQuery(id+"F15.wireOp",EDGE,"E21.MirrorCS"),sQuery(id+"F15.wireOp",EDGE,"E22.MirrorCS"),sQuery(id+"F15.wireOp",EDGE,"E23.MirrorCS"),sQuery(id+"F15.wireOp",EDGE,"E24.MirrorCS"),sQuery(id+"F15.wireOp",EDGE,"E25.MirrorCS"),sQuery(id+"F15.wireOp",EDGE,"E26.MirrorCS")])]}),"instanceName":"1"}),"instanceName":"1"}),"instanceName":"1"}),"instanceName":"1"});
            var Q76;
            Q76=makeQuery(id+"F22.opPattern","COPY",BODY,{"derivedFrom":makeQuery(id+"F19.opPattern","COPY",BODY,{"derivedFrom":makeQuery(id+"F16.opExtrude","SWEPT_BODY",BODY,{"disambiguationData":[OSD([sQuery(id+"F15.wireOp",EDGE,"E13.bottom"),sQuery(id+"F15.wireOp",EDGE,"E13.top"),sQuery(id+"F15.wireOp",EDGE,"E13.left"),sQuery(id+"F15.wireOp",EDGE,"E13.right"),sQuery(id+"F15.wireOp",EDGE,"E14.bottom"),sQuery(id+"F15.wireOp",EDGE,"E14.top"),sQuery(id+"F15.wireOp",EDGE,"E14.left"),sQuery(id+"F15.wireOp",EDGE,"E14.right"),sQuery(id+"F15.wireOp",EDGE,"E15.MirrorCS"),sQuery(id+"F15.wireOp",EDGE,"E16.MirrorCS"),sQuery(id+"F15.wireOp",EDGE,"E17.MirrorCS"),sQuery(id+"F15.wireOp",EDGE,"E18.MirrorCS"),sQuery(id+"F15.wireOp",EDGE,"E19.MirrorCS"),sQuery(id+"F15.wireOp",EDGE,"E20.MirrorCS"),sQuery(id+"F15.wireOp",EDGE,"E21.MirrorCS"),sQuery(id+"F15.wireOp",EDGE,"E22.MirrorCS"),sQuery(id+"F15.wireOp",EDGE,"E23.MirrorCS"),sQuery(id+"F15.wireOp",EDGE,"E24.MirrorCS"),sQuery(id+"F15.wireOp",EDGE,"E25.MirrorCS"),sQuery(id+"F15.wireOp",EDGE,"E26.MirrorCS")])]}),"instanceName":"1"}),"instanceName":"1"});
            var Q77;
            Q77=makeQuery(id+"F22.opPattern","COPY",BODY,{"derivedFrom":makeQuery(id+"F19.opPattern","COPY",BODY,{"derivedFrom":makeQuery(id+"F17.opPattern","COPY",BODY,{"derivedFrom":makeQuery(id+"F16.opExtrude","SWEPT_BODY",BODY,{"disambiguationData":[OSD([sQuery(id+"F15.wireOp",EDGE,"E13.bottom"),sQuery(id+"F15.wireOp",EDGE,"E13.top"),sQuery(id+"F15.wireOp",EDGE,"E13.left"),sQuery(id+"F15.wireOp",EDGE,"E13.right"),sQuery(id+"F15.wireOp",EDGE,"E14.bottom"),sQuery(id+"F15.wireOp",EDGE,"E14.top"),sQuery(id+"F15.wireOp",EDGE,"E14.left"),sQuery(id+"F15.wireOp",EDGE,"E14.right"),sQuery(id+"F15.wireOp",EDGE,"E15.MirrorCS"),sQuery(id+"F15.wireOp",EDGE,"E16.MirrorCS"),sQuery(id+"F15.wireOp",EDGE,"E17.MirrorCS"),sQuery(id+"F15.wireOp",EDGE,"E18.MirrorCS"),sQuery(id+"F15.wireOp",EDGE,"E19.MirrorCS"),sQuery(id+"F15.wireOp",EDGE,"E20.MirrorCS"),sQuery(id+"F15.wireOp",EDGE,"E21.MirrorCS"),sQuery(id+"F15.wireOp",EDGE,"E22.MirrorCS"),sQuery(id+"F15.wireOp",EDGE,"E23.MirrorCS"),sQuery(id+"F15.wireOp",EDGE,"E24.MirrorCS"),sQuery(id+"F15.wireOp",EDGE,"E25.MirrorCS"),sQuery(id+"F15.wireOp",EDGE,"E26.MirrorCS")])]}),"instanceName":"1"}),"instanceName":"1"}),"instanceName":"1"});
            var Q78;
            Q78=makeQuery(id+"F22.opPattern","COPY",BODY,{"derivedFrom":makeQuery(id+"F19.opPattern","COPY",BODY,{"derivedFrom":makeQuery(id+"F18.opPattern","COPY",BODY,{"derivedFrom":makeQuery(id+"F16.opExtrude","SWEPT_BODY",BODY,{"disambiguationData":[OSD([sQuery(id+"F15.wireOp",EDGE,"E13.bottom"),sQuery(id+"F15.wireOp",EDGE,"E13.top"),sQuery(id+"F15.wireOp",EDGE,"E13.left"),sQuery(id+"F15.wireOp",EDGE,"E13.right"),sQuery(id+"F15.wireOp",EDGE,"E14.bottom"),sQuery(id+"F15.wireOp",EDGE,"E14.top"),sQuery(id+"F15.wireOp",EDGE,"E14.left"),sQuery(id+"F15.wireOp",EDGE,"E14.right"),sQuery(id+"F15.wireOp",EDGE,"E15.MirrorCS"),sQuery(id+"F15.wireOp",EDGE,"E16.MirrorCS"),sQuery(id+"F15.wireOp",EDGE,"E17.MirrorCS"),sQuery(id+"F15.wireOp",EDGE,"E18.MirrorCS"),sQuery(id+"F15.wireOp",EDGE,"E19.MirrorCS"),sQuery(id+"F15.wireOp",EDGE,"E20.MirrorCS"),sQuery(id+"F15.wireOp",EDGE,"E21.MirrorCS"),sQuery(id+"F15.wireOp",EDGE,"E22.MirrorCS"),sQuery(id+"F15.wireOp",EDGE,"E23.MirrorCS"),sQuery(id+"F15.wireOp",EDGE,"E24.MirrorCS"),sQuery(id+"F15.wireOp",EDGE,"E25.MirrorCS"),sQuery(id+"F15.wireOp",EDGE,"E26.MirrorCS")])]}),"instanceName":"1"}),"instanceName":"1"}),"instanceName":"1"});
            var Q79;
            Q79=makeQuery(id+"F22.opPattern","COPY",BODY,{"derivedFrom":makeQuery(id+"F19.opPattern","COPY",BODY,{"derivedFrom":makeQuery(id+"F18.opPattern","COPY",BODY,{"derivedFrom":makeQuery(id+"F17.opPattern","COPY",BODY,{"derivedFrom":makeQuery(id+"F16.opExtrude","SWEPT_BODY",BODY,{"disambiguationData":[OSD([sQuery(id+"F15.wireOp",EDGE,"E13.bottom"),sQuery(id+"F15.wireOp",EDGE,"E13.top"),sQuery(id+"F15.wireOp",EDGE,"E13.left"),sQuery(id+"F15.wireOp",EDGE,"E13.right"),sQuery(id+"F15.wireOp",EDGE,"E14.bottom"),sQuery(id+"F15.wireOp",EDGE,"E14.top"),sQuery(id+"F15.wireOp",EDGE,"E14.left"),sQuery(id+"F15.wireOp",EDGE,"E14.right"),sQuery(id+"F15.wireOp",EDGE,"E15.MirrorCS"),sQuery(id+"F15.wireOp",EDGE,"E16.MirrorCS"),sQuery(id+"F15.wireOp",EDGE,"E17.MirrorCS"),sQuery(id+"F15.wireOp",EDGE,"E18.MirrorCS"),sQuery(id+"F15.wireOp",EDGE,"E19.MirrorCS"),sQuery(id+"F15.wireOp",EDGE,"E20.MirrorCS"),sQuery(id+"F15.wireOp",EDGE,"E21.MirrorCS"),sQuery(id+"F15.wireOp",EDGE,"E22.MirrorCS"),sQuery(id+"F15.wireOp",EDGE,"E23.MirrorCS"),sQuery(id+"F15.wireOp",EDGE,"E24.MirrorCS"),sQuery(id+"F15.wireOp",EDGE,"E25.MirrorCS"),sQuery(id+"F15.wireOp",EDGE,"E26.MirrorCS")])]}),"instanceName":"1"}),"instanceName":"1"}),"instanceName":"1"}),"instanceName":"1"});
            var Q80;
            Q80=makeQuery(id+"F22.opPattern","COPY",BODY,{"derivedFrom":makeQuery(id+"F20.opPattern","COPY",BODY,{"derivedFrom":makeQuery(id+"F16.opExtrude","SWEPT_BODY",BODY,{"disambiguationData":[OSD([sQuery(id+"F15.wireOp",EDGE,"E13.bottom"),sQuery(id+"F15.wireOp",EDGE,"E13.top"),sQuery(id+"F15.wireOp",EDGE,"E13.left"),sQuery(id+"F15.wireOp",EDGE,"E13.right"),sQuery(id+"F15.wireOp",EDGE,"E14.bottom"),sQuery(id+"F15.wireOp",EDGE,"E14.top"),sQuery(id+"F15.wireOp",EDGE,"E14.left"),sQuery(id+"F15.wireOp",EDGE,"E14.right"),sQuery(id+"F15.wireOp",EDGE,"E15.MirrorCS"),sQuery(id+"F15.wireOp",EDGE,"E16.MirrorCS"),sQuery(id+"F15.wireOp",EDGE,"E17.MirrorCS"),sQuery(id+"F15.wireOp",EDGE,"E18.MirrorCS"),sQuery(id+"F15.wireOp",EDGE,"E19.MirrorCS"),sQuery(id+"F15.wireOp",EDGE,"E20.MirrorCS"),sQuery(id+"F15.wireOp",EDGE,"E21.MirrorCS"),sQuery(id+"F15.wireOp",EDGE,"E22.MirrorCS"),sQuery(id+"F15.wireOp",EDGE,"E23.MirrorCS"),sQuery(id+"F15.wireOp",EDGE,"E24.MirrorCS"),sQuery(id+"F15.wireOp",EDGE,"E25.MirrorCS"),sQuery(id+"F15.wireOp",EDGE,"E26.MirrorCS")])]}),"instanceName":"1"}),"instanceName":"1"});
            var Q81;
            Q81=makeQuery(id+"F22.opPattern","COPY",BODY,{"derivedFrom":makeQuery(id+"F20.opPattern","COPY",BODY,{"derivedFrom":makeQuery(id+"F17.opPattern","COPY",BODY,{"derivedFrom":makeQuery(id+"F16.opExtrude","SWEPT_BODY",BODY,{"disambiguationData":[OSD([sQuery(id+"F15.wireOp",EDGE,"E13.bottom"),sQuery(id+"F15.wireOp",EDGE,"E13.top"),sQuery(id+"F15.wireOp",EDGE,"E13.left"),sQuery(id+"F15.wireOp",EDGE,"E13.right"),sQuery(id+"F15.wireOp",EDGE,"E14.bottom"),sQuery(id+"F15.wireOp",EDGE,"E14.top"),sQuery(id+"F15.wireOp",EDGE,"E14.left"),sQuery(id+"F15.wireOp",EDGE,"E14.right"),sQuery(id+"F15.wireOp",EDGE,"E15.MirrorCS"),sQuery(id+"F15.wireOp",EDGE,"E16.MirrorCS"),sQuery(id+"F15.wireOp",EDGE,"E17.MirrorCS"),sQuery(id+"F15.wireOp",EDGE,"E18.MirrorCS"),sQuery(id+"F15.wireOp",EDGE,"E19.MirrorCS"),sQuery(id+"F15.wireOp",EDGE,"E20.MirrorCS"),sQuery(id+"F15.wireOp",EDGE,"E21.MirrorCS"),sQuery(id+"F15.wireOp",EDGE,"E22.MirrorCS"),sQuery(id+"F15.wireOp",EDGE,"E23.MirrorCS"),sQuery(id+"F15.wireOp",EDGE,"E24.MirrorCS"),sQuery(id+"F15.wireOp",EDGE,"E25.MirrorCS"),sQuery(id+"F15.wireOp",EDGE,"E26.MirrorCS")])]}),"instanceName":"1"}),"instanceName":"1"}),"instanceName":"1"});
            var Q82;
            Q82=makeQuery(id+"F22.opPattern","COPY",BODY,{"derivedFrom":makeQuery(id+"F20.opPattern","COPY",BODY,{"derivedFrom":makeQuery(id+"F18.opPattern","COPY",BODY,{"derivedFrom":makeQuery(id+"F16.opExtrude","SWEPT_BODY",BODY,{"disambiguationData":[OSD([sQuery(id+"F15.wireOp",EDGE,"E13.bottom"),sQuery(id+"F15.wireOp",EDGE,"E13.top"),sQuery(id+"F15.wireOp",EDGE,"E13.left"),sQuery(id+"F15.wireOp",EDGE,"E13.right"),sQuery(id+"F15.wireOp",EDGE,"E14.bottom"),sQuery(id+"F15.wireOp",EDGE,"E14.top"),sQuery(id+"F15.wireOp",EDGE,"E14.left"),sQuery(id+"F15.wireOp",EDGE,"E14.right"),sQuery(id+"F15.wireOp",EDGE,"E15.MirrorCS"),sQuery(id+"F15.wireOp",EDGE,"E16.MirrorCS"),sQuery(id+"F15.wireOp",EDGE,"E17.MirrorCS"),sQuery(id+"F15.wireOp",EDGE,"E18.MirrorCS"),sQuery(id+"F15.wireOp",EDGE,"E19.MirrorCS"),sQuery(id+"F15.wireOp",EDGE,"E20.MirrorCS"),sQuery(id+"F15.wireOp",EDGE,"E21.MirrorCS"),sQuery(id+"F15.wireOp",EDGE,"E22.MirrorCS"),sQuery(id+"F15.wireOp",EDGE,"E23.MirrorCS"),sQuery(id+"F15.wireOp",EDGE,"E24.MirrorCS"),sQuery(id+"F15.wireOp",EDGE,"E25.MirrorCS"),sQuery(id+"F15.wireOp",EDGE,"E26.MirrorCS")])]}),"instanceName":"1"}),"instanceName":"1"}),"instanceName":"1"});
            var Q83;
            Q83=makeQuery(id+"F22.opPattern","COPY",BODY,{"derivedFrom":makeQuery(id+"F20.opPattern","COPY",BODY,{"derivedFrom":makeQuery(id+"F18.opPattern","COPY",BODY,{"derivedFrom":makeQuery(id+"F17.opPattern","COPY",BODY,{"derivedFrom":makeQuery(id+"F16.opExtrude","SWEPT_BODY",BODY,{"disambiguationData":[OSD([sQuery(id+"F15.wireOp",EDGE,"E13.bottom"),sQuery(id+"F15.wireOp",EDGE,"E13.top"),sQuery(id+"F15.wireOp",EDGE,"E13.left"),sQuery(id+"F15.wireOp",EDGE,"E13.right"),sQuery(id+"F15.wireOp",EDGE,"E14.bottom"),sQuery(id+"F15.wireOp",EDGE,"E14.top"),sQuery(id+"F15.wireOp",EDGE,"E14.left"),sQuery(id+"F15.wireOp",EDGE,"E14.right"),sQuery(id+"F15.wireOp",EDGE,"E15.MirrorCS"),sQuery(id+"F15.wireOp",EDGE,"E16.MirrorCS"),sQuery(id+"F15.wireOp",EDGE,"E17.MirrorCS"),sQuery(id+"F15.wireOp",EDGE,"E18.MirrorCS"),sQuery(id+"F15.wireOp",EDGE,"E19.MirrorCS"),sQuery(id+"F15.wireOp",EDGE,"E20.MirrorCS"),sQuery(id+"F15.wireOp",EDGE,"E21.MirrorCS"),sQuery(id+"F15.wireOp",EDGE,"E22.MirrorCS"),sQuery(id+"F15.wireOp",EDGE,"E23.MirrorCS"),sQuery(id+"F15.wireOp",EDGE,"E24.MirrorCS"),sQuery(id+"F15.wireOp",EDGE,"E25.MirrorCS"),sQuery(id+"F15.wireOp",EDGE,"E26.MirrorCS")])]}),"instanceName":"1"}),"instanceName":"1"}),"instanceName":"1"}),"instanceName":"1"});
            var Q84;
            Q84=makeQuery(id+"F22.opPattern","COPY",BODY,{"derivedFrom":makeQuery(id+"F20.opPattern","COPY",BODY,{"derivedFrom":makeQuery(id+"F19.opPattern","COPY",BODY,{"derivedFrom":makeQuery(id+"F16.opExtrude","SWEPT_BODY",BODY,{"disambiguationData":[OSD([sQuery(id+"F15.wireOp",EDGE,"E13.bottom"),sQuery(id+"F15.wireOp",EDGE,"E13.top"),sQuery(id+"F15.wireOp",EDGE,"E13.left"),sQuery(id+"F15.wireOp",EDGE,"E13.right"),sQuery(id+"F15.wireOp",EDGE,"E14.bottom"),sQuery(id+"F15.wireOp",EDGE,"E14.top"),sQuery(id+"F15.wireOp",EDGE,"E14.left"),sQuery(id+"F15.wireOp",EDGE,"E14.right"),sQuery(id+"F15.wireOp",EDGE,"E15.MirrorCS"),sQuery(id+"F15.wireOp",EDGE,"E16.MirrorCS"),sQuery(id+"F15.wireOp",EDGE,"E17.MirrorCS"),sQuery(id+"F15.wireOp",EDGE,"E18.MirrorCS"),sQuery(id+"F15.wireOp",EDGE,"E19.MirrorCS"),sQuery(id+"F15.wireOp",EDGE,"E20.MirrorCS"),sQuery(id+"F15.wireOp",EDGE,"E21.MirrorCS"),sQuery(id+"F15.wireOp",EDGE,"E22.MirrorCS"),sQuery(id+"F15.wireOp",EDGE,"E23.MirrorCS"),sQuery(id+"F15.wireOp",EDGE,"E24.MirrorCS"),sQuery(id+"F15.wireOp",EDGE,"E25.MirrorCS"),sQuery(id+"F15.wireOp",EDGE,"E26.MirrorCS")])]}),"instanceName":"1"}),"instanceName":"1"}),"instanceName":"1"});
            var Q85;
            Q85=makeQuery(id+"F22.opPattern","COPY",BODY,{"derivedFrom":makeQuery(id+"F20.opPattern","COPY",BODY,{"derivedFrom":makeQuery(id+"F19.opPattern","COPY",BODY,{"derivedFrom":makeQuery(id+"F17.opPattern","COPY",BODY,{"derivedFrom":makeQuery(id+"F16.opExtrude","SWEPT_BODY",BODY,{"disambiguationData":[OSD([sQuery(id+"F15.wireOp",EDGE,"E13.bottom"),sQuery(id+"F15.wireOp",EDGE,"E13.top"),sQuery(id+"F15.wireOp",EDGE,"E13.left"),sQuery(id+"F15.wireOp",EDGE,"E13.right"),sQuery(id+"F15.wireOp",EDGE,"E14.bottom"),sQuery(id+"F15.wireOp",EDGE,"E14.top"),sQuery(id+"F15.wireOp",EDGE,"E14.left"),sQuery(id+"F15.wireOp",EDGE,"E14.right"),sQuery(id+"F15.wireOp",EDGE,"E15.MirrorCS"),sQuery(id+"F15.wireOp",EDGE,"E16.MirrorCS"),sQuery(id+"F15.wireOp",EDGE,"E17.MirrorCS"),sQuery(id+"F15.wireOp",EDGE,"E18.MirrorCS"),sQuery(id+"F15.wireOp",EDGE,"E19.MirrorCS"),sQuery(id+"F15.wireOp",EDGE,"E20.MirrorCS"),sQuery(id+"F15.wireOp",EDGE,"E21.MirrorCS"),sQuery(id+"F15.wireOp",EDGE,"E22.MirrorCS"),sQuery(id+"F15.wireOp",EDGE,"E23.MirrorCS"),sQuery(id+"F15.wireOp",EDGE,"E24.MirrorCS"),sQuery(id+"F15.wireOp",EDGE,"E25.MirrorCS"),sQuery(id+"F15.wireOp",EDGE,"E26.MirrorCS")])]}),"instanceName":"1"}),"instanceName":"1"}),"instanceName":"1"}),"instanceName":"1"});
            var Q86;
            Q86=makeQuery(id+"F22.opPattern","COPY",BODY,{"derivedFrom":makeQuery(id+"F20.opPattern","COPY",BODY,{"derivedFrom":makeQuery(id+"F19.opPattern","COPY",BODY,{"derivedFrom":makeQuery(id+"F18.opPattern","COPY",BODY,{"derivedFrom":makeQuery(id+"F16.opExtrude","SWEPT_BODY",BODY,{"disambiguationData":[OSD([sQuery(id+"F15.wireOp",EDGE,"E13.bottom"),sQuery(id+"F15.wireOp",EDGE,"E13.top"),sQuery(id+"F15.wireOp",EDGE,"E13.left"),sQuery(id+"F15.wireOp",EDGE,"E13.right"),sQuery(id+"F15.wireOp",EDGE,"E14.bottom"),sQuery(id+"F15.wireOp",EDGE,"E14.top"),sQuery(id+"F15.wireOp",EDGE,"E14.left"),sQuery(id+"F15.wireOp",EDGE,"E14.right"),sQuery(id+"F15.wireOp",EDGE,"E15.MirrorCS"),sQuery(id+"F15.wireOp",EDGE,"E16.MirrorCS"),sQuery(id+"F15.wireOp",EDGE,"E17.MirrorCS"),sQuery(id+"F15.wireOp",EDGE,"E18.MirrorCS"),sQuery(id+"F15.wireOp",EDGE,"E19.MirrorCS"),sQuery(id+"F15.wireOp",EDGE,"E20.MirrorCS"),sQuery(id+"F15.wireOp",EDGE,"E21.MirrorCS"),sQuery(id+"F15.wireOp",EDGE,"E22.MirrorCS"),sQuery(id+"F15.wireOp",EDGE,"E23.MirrorCS"),sQuery(id+"F15.wireOp",EDGE,"E24.MirrorCS"),sQuery(id+"F15.wireOp",EDGE,"E25.MirrorCS"),sQuery(id+"F15.wireOp",EDGE,"E26.MirrorCS")])]}),"instanceName":"1"}),"instanceName":"1"}),"instanceName":"1"}),"instanceName":"1"});
            var Q87;
            Q87=makeQuery(id+"F22.opPattern","COPY",BODY,{"derivedFrom":makeQuery(id+"F20.opPattern","COPY",BODY,{"derivedFrom":makeQuery(id+"F19.opPattern","COPY",BODY,{"derivedFrom":makeQuery(id+"F18.opPattern","COPY",BODY,{"derivedFrom":makeQuery(id+"F17.opPattern","COPY",BODY,{"derivedFrom":makeQuery(id+"F16.opExtrude","SWEPT_BODY",BODY,{"disambiguationData":[OSD([sQuery(id+"F15.wireOp",EDGE,"E13.bottom"),sQuery(id+"F15.wireOp",EDGE,"E13.top"),sQuery(id+"F15.wireOp",EDGE,"E13.left"),sQuery(id+"F15.wireOp",EDGE,"E13.right"),sQuery(id+"F15.wireOp",EDGE,"E14.bottom"),sQuery(id+"F15.wireOp",EDGE,"E14.top"),sQuery(id+"F15.wireOp",EDGE,"E14.left"),sQuery(id+"F15.wireOp",EDGE,"E14.right"),sQuery(id+"F15.wireOp",EDGE,"E15.MirrorCS"),sQuery(id+"F15.wireOp",EDGE,"E16.MirrorCS"),sQuery(id+"F15.wireOp",EDGE,"E17.MirrorCS"),sQuery(id+"F15.wireOp",EDGE,"E18.MirrorCS"),sQuery(id+"F15.wireOp",EDGE,"E19.MirrorCS"),sQuery(id+"F15.wireOp",EDGE,"E20.MirrorCS"),sQuery(id+"F15.wireOp",EDGE,"E21.MirrorCS"),sQuery(id+"F15.wireOp",EDGE,"E22.MirrorCS"),sQuery(id+"F15.wireOp",EDGE,"E23.MirrorCS"),sQuery(id+"F15.wireOp",EDGE,"E24.MirrorCS"),sQuery(id+"F15.wireOp",EDGE,"E25.MirrorCS"),sQuery(id+"F15.wireOp",EDGE,"E26.MirrorCS")])]}),"instanceName":"1"}),"instanceName":"1"}),"instanceName":"1"}),"instanceName":"1"}),"instanceName":"1"});
            var Q88;
            Q88=makeQuery(id+"F22.opPattern","COPY",BODY,{"derivedFrom":makeQuery(id+"F21.opPattern","COPY",BODY,{"derivedFrom":makeQuery(id+"F16.opExtrude","SWEPT_BODY",BODY,{"disambiguationData":[OSD([sQuery(id+"F15.wireOp",EDGE,"E13.bottom"),sQuery(id+"F15.wireOp",EDGE,"E13.top"),sQuery(id+"F15.wireOp",EDGE,"E13.left"),sQuery(id+"F15.wireOp",EDGE,"E13.right"),sQuery(id+"F15.wireOp",EDGE,"E14.bottom"),sQuery(id+"F15.wireOp",EDGE,"E14.top"),sQuery(id+"F15.wireOp",EDGE,"E14.left"),sQuery(id+"F15.wireOp",EDGE,"E14.right"),sQuery(id+"F15.wireOp",EDGE,"E15.MirrorCS"),sQuery(id+"F15.wireOp",EDGE,"E16.MirrorCS"),sQuery(id+"F15.wireOp",EDGE,"E17.MirrorCS"),sQuery(id+"F15.wireOp",EDGE,"E18.MirrorCS"),sQuery(id+"F15.wireOp",EDGE,"E19.MirrorCS"),sQuery(id+"F15.wireOp",EDGE,"E20.MirrorCS"),sQuery(id+"F15.wireOp",EDGE,"E21.MirrorCS"),sQuery(id+"F15.wireOp",EDGE,"E22.MirrorCS"),sQuery(id+"F15.wireOp",EDGE,"E23.MirrorCS"),sQuery(id+"F15.wireOp",EDGE,"E24.MirrorCS"),sQuery(id+"F15.wireOp",EDGE,"E25.MirrorCS"),sQuery(id+"F15.wireOp",EDGE,"E26.MirrorCS")])]}),"instanceName":"1"}),"instanceName":"1"});
            var Q89;
            Q89=makeQuery(id+"F22.opPattern","COPY",BODY,{"derivedFrom":makeQuery(id+"F21.opPattern","COPY",BODY,{"derivedFrom":makeQuery(id+"F17.opPattern","COPY",BODY,{"derivedFrom":makeQuery(id+"F16.opExtrude","SWEPT_BODY",BODY,{"disambiguationData":[OSD([sQuery(id+"F15.wireOp",EDGE,"E13.bottom"),sQuery(id+"F15.wireOp",EDGE,"E13.top"),sQuery(id+"F15.wireOp",EDGE,"E13.left"),sQuery(id+"F15.wireOp",EDGE,"E13.right"),sQuery(id+"F15.wireOp",EDGE,"E14.bottom"),sQuery(id+"F15.wireOp",EDGE,"E14.top"),sQuery(id+"F15.wireOp",EDGE,"E14.left"),sQuery(id+"F15.wireOp",EDGE,"E14.right"),sQuery(id+"F15.wireOp",EDGE,"E15.MirrorCS"),sQuery(id+"F15.wireOp",EDGE,"E16.MirrorCS"),sQuery(id+"F15.wireOp",EDGE,"E17.MirrorCS"),sQuery(id+"F15.wireOp",EDGE,"E18.MirrorCS"),sQuery(id+"F15.wireOp",EDGE,"E19.MirrorCS"),sQuery(id+"F15.wireOp",EDGE,"E20.MirrorCS"),sQuery(id+"F15.wireOp",EDGE,"E21.MirrorCS"),sQuery(id+"F15.wireOp",EDGE,"E22.MirrorCS"),sQuery(id+"F15.wireOp",EDGE,"E23.MirrorCS"),sQuery(id+"F15.wireOp",EDGE,"E24.MirrorCS"),sQuery(id+"F15.wireOp",EDGE,"E25.MirrorCS"),sQuery(id+"F15.wireOp",EDGE,"E26.MirrorCS")])]}),"instanceName":"1"}),"instanceName":"1"}),"instanceName":"1"});
            var Q90;
            Q90=makeQuery(id+"F22.opPattern","COPY",BODY,{"derivedFrom":makeQuery(id+"F21.opPattern","COPY",BODY,{"derivedFrom":makeQuery(id+"F18.opPattern","COPY",BODY,{"derivedFrom":makeQuery(id+"F16.opExtrude","SWEPT_BODY",BODY,{"disambiguationData":[OSD([sQuery(id+"F15.wireOp",EDGE,"E13.bottom"),sQuery(id+"F15.wireOp",EDGE,"E13.top"),sQuery(id+"F15.wireOp",EDGE,"E13.left"),sQuery(id+"F15.wireOp",EDGE,"E13.right"),sQuery(id+"F15.wireOp",EDGE,"E14.bottom"),sQuery(id+"F15.wireOp",EDGE,"E14.top"),sQuery(id+"F15.wireOp",EDGE,"E14.left"),sQuery(id+"F15.wireOp",EDGE,"E14.right"),sQuery(id+"F15.wireOp",EDGE,"E15.MirrorCS"),sQuery(id+"F15.wireOp",EDGE,"E16.MirrorCS"),sQuery(id+"F15.wireOp",EDGE,"E17.MirrorCS"),sQuery(id+"F15.wireOp",EDGE,"E18.MirrorCS"),sQuery(id+"F15.wireOp",EDGE,"E19.MirrorCS"),sQuery(id+"F15.wireOp",EDGE,"E20.MirrorCS"),sQuery(id+"F15.wireOp",EDGE,"E21.MirrorCS"),sQuery(id+"F15.wireOp",EDGE,"E22.MirrorCS"),sQuery(id+"F15.wireOp",EDGE,"E23.MirrorCS"),sQuery(id+"F15.wireOp",EDGE,"E24.MirrorCS"),sQuery(id+"F15.wireOp",EDGE,"E25.MirrorCS"),sQuery(id+"F15.wireOp",EDGE,"E26.MirrorCS")])]}),"instanceName":"1"}),"instanceName":"1"}),"instanceName":"1"});
            var Q91;
            Q91=makeQuery(id+"F22.opPattern","COPY",BODY,{"derivedFrom":makeQuery(id+"F21.opPattern","COPY",BODY,{"derivedFrom":makeQuery(id+"F18.opPattern","COPY",BODY,{"derivedFrom":makeQuery(id+"F17.opPattern","COPY",BODY,{"derivedFrom":makeQuery(id+"F16.opExtrude","SWEPT_BODY",BODY,{"disambiguationData":[OSD([sQuery(id+"F15.wireOp",EDGE,"E13.bottom"),sQuery(id+"F15.wireOp",EDGE,"E13.top"),sQuery(id+"F15.wireOp",EDGE,"E13.left"),sQuery(id+"F15.wireOp",EDGE,"E13.right"),sQuery(id+"F15.wireOp",EDGE,"E14.bottom"),sQuery(id+"F15.wireOp",EDGE,"E14.top"),sQuery(id+"F15.wireOp",EDGE,"E14.left"),sQuery(id+"F15.wireOp",EDGE,"E14.right"),sQuery(id+"F15.wireOp",EDGE,"E15.MirrorCS"),sQuery(id+"F15.wireOp",EDGE,"E16.MirrorCS"),sQuery(id+"F15.wireOp",EDGE,"E17.MirrorCS"),sQuery(id+"F15.wireOp",EDGE,"E18.MirrorCS"),sQuery(id+"F15.wireOp",EDGE,"E19.MirrorCS"),sQuery(id+"F15.wireOp",EDGE,"E20.MirrorCS"),sQuery(id+"F15.wireOp",EDGE,"E21.MirrorCS"),sQuery(id+"F15.wireOp",EDGE,"E22.MirrorCS"),sQuery(id+"F15.wireOp",EDGE,"E23.MirrorCS"),sQuery(id+"F15.wireOp",EDGE,"E24.MirrorCS"),sQuery(id+"F15.wireOp",EDGE,"E25.MirrorCS"),sQuery(id+"F15.wireOp",EDGE,"E26.MirrorCS")])]}),"instanceName":"1"}),"instanceName":"1"}),"instanceName":"1"}),"instanceName":"1"});
            var Q92;
            Q92=makeQuery(id+"F22.opPattern","COPY",BODY,{"derivedFrom":makeQuery(id+"F21.opPattern","COPY",BODY,{"derivedFrom":makeQuery(id+"F19.opPattern","COPY",BODY,{"derivedFrom":makeQuery(id+"F16.opExtrude","SWEPT_BODY",BODY,{"disambiguationData":[OSD([sQuery(id+"F15.wireOp",EDGE,"E13.bottom"),sQuery(id+"F15.wireOp",EDGE,"E13.top"),sQuery(id+"F15.wireOp",EDGE,"E13.left"),sQuery(id+"F15.wireOp",EDGE,"E13.right"),sQuery(id+"F15.wireOp",EDGE,"E14.bottom"),sQuery(id+"F15.wireOp",EDGE,"E14.top"),sQuery(id+"F15.wireOp",EDGE,"E14.left"),sQuery(id+"F15.wireOp",EDGE,"E14.right"),sQuery(id+"F15.wireOp",EDGE,"E15.MirrorCS"),sQuery(id+"F15.wireOp",EDGE,"E16.MirrorCS"),sQuery(id+"F15.wireOp",EDGE,"E17.MirrorCS"),sQuery(id+"F15.wireOp",EDGE,"E18.MirrorCS"),sQuery(id+"F15.wireOp",EDGE,"E19.MirrorCS"),sQuery(id+"F15.wireOp",EDGE,"E20.MirrorCS"),sQuery(id+"F15.wireOp",EDGE,"E21.MirrorCS"),sQuery(id+"F15.wireOp",EDGE,"E22.MirrorCS"),sQuery(id+"F15.wireOp",EDGE,"E23.MirrorCS"),sQuery(id+"F15.wireOp",EDGE,"E24.MirrorCS"),sQuery(id+"F15.wireOp",EDGE,"E25.MirrorCS"),sQuery(id+"F15.wireOp",EDGE,"E26.MirrorCS")])]}),"instanceName":"1"}),"instanceName":"1"}),"instanceName":"1"});
            var Q93;
            Q93=makeQuery(id+"F22.opPattern","COPY",BODY,{"derivedFrom":makeQuery(id+"F21.opPattern","COPY",BODY,{"derivedFrom":makeQuery(id+"F19.opPattern","COPY",BODY,{"derivedFrom":makeQuery(id+"F17.opPattern","COPY",BODY,{"derivedFrom":makeQuery(id+"F16.opExtrude","SWEPT_BODY",BODY,{"disambiguationData":[OSD([sQuery(id+"F15.wireOp",EDGE,"E13.bottom"),sQuery(id+"F15.wireOp",EDGE,"E13.top"),sQuery(id+"F15.wireOp",EDGE,"E13.left"),sQuery(id+"F15.wireOp",EDGE,"E13.right"),sQuery(id+"F15.wireOp",EDGE,"E14.bottom"),sQuery(id+"F15.wireOp",EDGE,"E14.top"),sQuery(id+"F15.wireOp",EDGE,"E14.left"),sQuery(id+"F15.wireOp",EDGE,"E14.right"),sQuery(id+"F15.wireOp",EDGE,"E15.MirrorCS"),sQuery(id+"F15.wireOp",EDGE,"E16.MirrorCS"),sQuery(id+"F15.wireOp",EDGE,"E17.MirrorCS"),sQuery(id+"F15.wireOp",EDGE,"E18.MirrorCS"),sQuery(id+"F15.wireOp",EDGE,"E19.MirrorCS"),sQuery(id+"F15.wireOp",EDGE,"E20.MirrorCS"),sQuery(id+"F15.wireOp",EDGE,"E21.MirrorCS"),sQuery(id+"F15.wireOp",EDGE,"E22.MirrorCS"),sQuery(id+"F15.wireOp",EDGE,"E23.MirrorCS"),sQuery(id+"F15.wireOp",EDGE,"E24.MirrorCS"),sQuery(id+"F15.wireOp",EDGE,"E25.MirrorCS"),sQuery(id+"F15.wireOp",EDGE,"E26.MirrorCS")])]}),"instanceName":"1"}),"instanceName":"1"}),"instanceName":"1"}),"instanceName":"1"});
            var Q94;
            Q94=makeQuery(id+"F22.opPattern","COPY",BODY,{"derivedFrom":makeQuery(id+"F21.opPattern","COPY",BODY,{"derivedFrom":makeQuery(id+"F19.opPattern","COPY",BODY,{"derivedFrom":makeQuery(id+"F18.opPattern","COPY",BODY,{"derivedFrom":makeQuery(id+"F16.opExtrude","SWEPT_BODY",BODY,{"disambiguationData":[OSD([sQuery(id+"F15.wireOp",EDGE,"E13.bottom"),sQuery(id+"F15.wireOp",EDGE,"E13.top"),sQuery(id+"F15.wireOp",EDGE,"E13.left"),sQuery(id+"F15.wireOp",EDGE,"E13.right"),sQuery(id+"F15.wireOp",EDGE,"E14.bottom"),sQuery(id+"F15.wireOp",EDGE,"E14.top"),sQuery(id+"F15.wireOp",EDGE,"E14.left"),sQuery(id+"F15.wireOp",EDGE,"E14.right"),sQuery(id+"F15.wireOp",EDGE,"E15.MirrorCS"),sQuery(id+"F15.wireOp",EDGE,"E16.MirrorCS"),sQuery(id+"F15.wireOp",EDGE,"E17.MirrorCS"),sQuery(id+"F15.wireOp",EDGE,"E18.MirrorCS"),sQuery(id+"F15.wireOp",EDGE,"E19.MirrorCS"),sQuery(id+"F15.wireOp",EDGE,"E20.MirrorCS"),sQuery(id+"F15.wireOp",EDGE,"E21.MirrorCS"),sQuery(id+"F15.wireOp",EDGE,"E22.MirrorCS"),sQuery(id+"F15.wireOp",EDGE,"E23.MirrorCS"),sQuery(id+"F15.wireOp",EDGE,"E24.MirrorCS"),sQuery(id+"F15.wireOp",EDGE,"E25.MirrorCS"),sQuery(id+"F15.wireOp",EDGE,"E26.MirrorCS")])]}),"instanceName":"1"}),"instanceName":"1"}),"instanceName":"1"}),"instanceName":"1"});
            var Q95;
            Q95=makeQuery(id+"F22.opPattern","COPY",BODY,{"derivedFrom":makeQuery(id+"F21.opPattern","COPY",BODY,{"derivedFrom":makeQuery(id+"F19.opPattern","COPY",BODY,{"derivedFrom":makeQuery(id+"F18.opPattern","COPY",BODY,{"derivedFrom":makeQuery(id+"F17.opPattern","COPY",BODY,{"derivedFrom":makeQuery(id+"F16.opExtrude","SWEPT_BODY",BODY,{"disambiguationData":[OSD([sQuery(id+"F15.wireOp",EDGE,"E13.bottom"),sQuery(id+"F15.wireOp",EDGE,"E13.top"),sQuery(id+"F15.wireOp",EDGE,"E13.left"),sQuery(id+"F15.wireOp",EDGE,"E13.right"),sQuery(id+"F15.wireOp",EDGE,"E14.bottom"),sQuery(id+"F15.wireOp",EDGE,"E14.top"),sQuery(id+"F15.wireOp",EDGE,"E14.left"),sQuery(id+"F15.wireOp",EDGE,"E14.right"),sQuery(id+"F15.wireOp",EDGE,"E15.MirrorCS"),sQuery(id+"F15.wireOp",EDGE,"E16.MirrorCS"),sQuery(id+"F15.wireOp",EDGE,"E17.MirrorCS"),sQuery(id+"F15.wireOp",EDGE,"E18.MirrorCS"),sQuery(id+"F15.wireOp",EDGE,"E19.MirrorCS"),sQuery(id+"F15.wireOp",EDGE,"E20.MirrorCS"),sQuery(id+"F15.wireOp",EDGE,"E21.MirrorCS"),sQuery(id+"F15.wireOp",EDGE,"E22.MirrorCS"),sQuery(id+"F15.wireOp",EDGE,"E23.MirrorCS"),sQuery(id+"F15.wireOp",EDGE,"E24.MirrorCS"),sQuery(id+"F15.wireOp",EDGE,"E25.MirrorCS"),sQuery(id+"F15.wireOp",EDGE,"E26.MirrorCS")])]}),"instanceName":"1"}),"instanceName":"1"}),"instanceName":"1"}),"instanceName":"1"}),"instanceName":"1"});
            var Q96;
            Q96=makeQuery(id+"F23.opPattern","COPY",BODY,{"derivedFrom":makeQuery(id+"F19.opPattern","COPY",BODY,{"derivedFrom":makeQuery(id+"F16.opExtrude","SWEPT_BODY",BODY,{"disambiguationData":[OSD([sQuery(id+"F15.wireOp",EDGE,"E13.bottom"),sQuery(id+"F15.wireOp",EDGE,"E13.top"),sQuery(id+"F15.wireOp",EDGE,"E13.left"),sQuery(id+"F15.wireOp",EDGE,"E13.right"),sQuery(id+"F15.wireOp",EDGE,"E14.bottom"),sQuery(id+"F15.wireOp",EDGE,"E14.top"),sQuery(id+"F15.wireOp",EDGE,"E14.left"),sQuery(id+"F15.wireOp",EDGE,"E14.right"),sQuery(id+"F15.wireOp",EDGE,"E15.MirrorCS"),sQuery(id+"F15.wireOp",EDGE,"E16.MirrorCS"),sQuery(id+"F15.wireOp",EDGE,"E17.MirrorCS"),sQuery(id+"F15.wireOp",EDGE,"E18.MirrorCS"),sQuery(id+"F15.wireOp",EDGE,"E19.MirrorCS"),sQuery(id+"F15.wireOp",EDGE,"E20.MirrorCS"),sQuery(id+"F15.wireOp",EDGE,"E21.MirrorCS"),sQuery(id+"F15.wireOp",EDGE,"E22.MirrorCS"),sQuery(id+"F15.wireOp",EDGE,"E23.MirrorCS"),sQuery(id+"F15.wireOp",EDGE,"E24.MirrorCS"),sQuery(id+"F15.wireOp",EDGE,"E25.MirrorCS"),sQuery(id+"F15.wireOp",EDGE,"E26.MirrorCS")])]}),"instanceName":"1"}),"instanceName":"1"});
            var Q97;
            Q97=makeQuery(id+"F23.opPattern","COPY",BODY,{"derivedFrom":makeQuery(id+"F19.opPattern","COPY",BODY,{"derivedFrom":makeQuery(id+"F17.opPattern","COPY",BODY,{"derivedFrom":makeQuery(id+"F16.opExtrude","SWEPT_BODY",BODY,{"disambiguationData":[OSD([sQuery(id+"F15.wireOp",EDGE,"E13.bottom"),sQuery(id+"F15.wireOp",EDGE,"E13.top"),sQuery(id+"F15.wireOp",EDGE,"E13.left"),sQuery(id+"F15.wireOp",EDGE,"E13.right"),sQuery(id+"F15.wireOp",EDGE,"E14.bottom"),sQuery(id+"F15.wireOp",EDGE,"E14.top"),sQuery(id+"F15.wireOp",EDGE,"E14.left"),sQuery(id+"F15.wireOp",EDGE,"E14.right"),sQuery(id+"F15.wireOp",EDGE,"E15.MirrorCS"),sQuery(id+"F15.wireOp",EDGE,"E16.MirrorCS"),sQuery(id+"F15.wireOp",EDGE,"E17.MirrorCS"),sQuery(id+"F15.wireOp",EDGE,"E18.MirrorCS"),sQuery(id+"F15.wireOp",EDGE,"E19.MirrorCS"),sQuery(id+"F15.wireOp",EDGE,"E20.MirrorCS"),sQuery(id+"F15.wireOp",EDGE,"E21.MirrorCS"),sQuery(id+"F15.wireOp",EDGE,"E22.MirrorCS"),sQuery(id+"F15.wireOp",EDGE,"E23.MirrorCS"),sQuery(id+"F15.wireOp",EDGE,"E24.MirrorCS"),sQuery(id+"F15.wireOp",EDGE,"E25.MirrorCS"),sQuery(id+"F15.wireOp",EDGE,"E26.MirrorCS")])]}),"instanceName":"1"}),"instanceName":"1"}),"instanceName":"1"});
            var Q98;
            Q98=makeQuery(id+"F23.opPattern","COPY",BODY,{"derivedFrom":makeQuery(id+"F19.opPattern","COPY",BODY,{"derivedFrom":makeQuery(id+"F18.opPattern","COPY",BODY,{"derivedFrom":makeQuery(id+"F16.opExtrude","SWEPT_BODY",BODY,{"disambiguationData":[OSD([sQuery(id+"F15.wireOp",EDGE,"E13.bottom"),sQuery(id+"F15.wireOp",EDGE,"E13.top"),sQuery(id+"F15.wireOp",EDGE,"E13.left"),sQuery(id+"F15.wireOp",EDGE,"E13.right"),sQuery(id+"F15.wireOp",EDGE,"E14.bottom"),sQuery(id+"F15.wireOp",EDGE,"E14.top"),sQuery(id+"F15.wireOp",EDGE,"E14.left"),sQuery(id+"F15.wireOp",EDGE,"E14.right"),sQuery(id+"F15.wireOp",EDGE,"E15.MirrorCS"),sQuery(id+"F15.wireOp",EDGE,"E16.MirrorCS"),sQuery(id+"F15.wireOp",EDGE,"E17.MirrorCS"),sQuery(id+"F15.wireOp",EDGE,"E18.MirrorCS"),sQuery(id+"F15.wireOp",EDGE,"E19.MirrorCS"),sQuery(id+"F15.wireOp",EDGE,"E20.MirrorCS"),sQuery(id+"F15.wireOp",EDGE,"E21.MirrorCS"),sQuery(id+"F15.wireOp",EDGE,"E22.MirrorCS"),sQuery(id+"F15.wireOp",EDGE,"E23.MirrorCS"),sQuery(id+"F15.wireOp",EDGE,"E24.MirrorCS"),sQuery(id+"F15.wireOp",EDGE,"E25.MirrorCS"),sQuery(id+"F15.wireOp",EDGE,"E26.MirrorCS")])]}),"instanceName":"1"}),"instanceName":"1"}),"instanceName":"1"});
            var Q99;
            Q99=makeQuery(id+"F23.opPattern","COPY",BODY,{"derivedFrom":makeQuery(id+"F19.opPattern","COPY",BODY,{"derivedFrom":makeQuery(id+"F18.opPattern","COPY",BODY,{"derivedFrom":makeQuery(id+"F17.opPattern","COPY",BODY,{"derivedFrom":makeQuery(id+"F16.opExtrude","SWEPT_BODY",BODY,{"disambiguationData":[OSD([sQuery(id+"F15.wireOp",EDGE,"E13.bottom"),sQuery(id+"F15.wireOp",EDGE,"E13.top"),sQuery(id+"F15.wireOp",EDGE,"E13.left"),sQuery(id+"F15.wireOp",EDGE,"E13.right"),sQuery(id+"F15.wireOp",EDGE,"E14.bottom"),sQuery(id+"F15.wireOp",EDGE,"E14.top"),sQuery(id+"F15.wireOp",EDGE,"E14.left"),sQuery(id+"F15.wireOp",EDGE,"E14.right"),sQuery(id+"F15.wireOp",EDGE,"E15.MirrorCS"),sQuery(id+"F15.wireOp",EDGE,"E16.MirrorCS"),sQuery(id+"F15.wireOp",EDGE,"E17.MirrorCS"),sQuery(id+"F15.wireOp",EDGE,"E18.MirrorCS"),sQuery(id+"F15.wireOp",EDGE,"E19.MirrorCS"),sQuery(id+"F15.wireOp",EDGE,"E20.MirrorCS"),sQuery(id+"F15.wireOp",EDGE,"E21.MirrorCS"),sQuery(id+"F15.wireOp",EDGE,"E22.MirrorCS"),sQuery(id+"F15.wireOp",EDGE,"E23.MirrorCS"),sQuery(id+"F15.wireOp",EDGE,"E24.MirrorCS"),sQuery(id+"F15.wireOp",EDGE,"E25.MirrorCS"),sQuery(id+"F15.wireOp",EDGE,"E26.MirrorCS")])]}),"instanceName":"1"}),"instanceName":"1"}),"instanceName":"1"}),"instanceName":"1"});
            var Q100;
            Q100=makeQuery(id+"F23.opPattern","COPY",BODY,{"derivedFrom":makeQuery(id+"F20.opPattern","COPY",BODY,{"derivedFrom":makeQuery(id+"F16.opExtrude","SWEPT_BODY",BODY,{"disambiguationData":[OSD([sQuery(id+"F15.wireOp",EDGE,"E13.bottom"),sQuery(id+"F15.wireOp",EDGE,"E13.top"),sQuery(id+"F15.wireOp",EDGE,"E13.left"),sQuery(id+"F15.wireOp",EDGE,"E13.right"),sQuery(id+"F15.wireOp",EDGE,"E14.bottom"),sQuery(id+"F15.wireOp",EDGE,"E14.top"),sQuery(id+"F15.wireOp",EDGE,"E14.left"),sQuery(id+"F15.wireOp",EDGE,"E14.right"),sQuery(id+"F15.wireOp",EDGE,"E15.MirrorCS"),sQuery(id+"F15.wireOp",EDGE,"E16.MirrorCS"),sQuery(id+"F15.wireOp",EDGE,"E17.MirrorCS"),sQuery(id+"F15.wireOp",EDGE,"E18.MirrorCS"),sQuery(id+"F15.wireOp",EDGE,"E19.MirrorCS"),sQuery(id+"F15.wireOp",EDGE,"E20.MirrorCS"),sQuery(id+"F15.wireOp",EDGE,"E21.MirrorCS"),sQuery(id+"F15.wireOp",EDGE,"E22.MirrorCS"),sQuery(id+"F15.wireOp",EDGE,"E23.MirrorCS"),sQuery(id+"F15.wireOp",EDGE,"E24.MirrorCS"),sQuery(id+"F15.wireOp",EDGE,"E25.MirrorCS"),sQuery(id+"F15.wireOp",EDGE,"E26.MirrorCS")])]}),"instanceName":"1"}),"instanceName":"1"});
            var Q101;
            Q101=makeQuery(id+"F23.opPattern","COPY",BODY,{"derivedFrom":makeQuery(id+"F20.opPattern","COPY",BODY,{"derivedFrom":makeQuery(id+"F17.opPattern","COPY",BODY,{"derivedFrom":makeQuery(id+"F16.opExtrude","SWEPT_BODY",BODY,{"disambiguationData":[OSD([sQuery(id+"F15.wireOp",EDGE,"E13.bottom"),sQuery(id+"F15.wireOp",EDGE,"E13.top"),sQuery(id+"F15.wireOp",EDGE,"E13.left"),sQuery(id+"F15.wireOp",EDGE,"E13.right"),sQuery(id+"F15.wireOp",EDGE,"E14.bottom"),sQuery(id+"F15.wireOp",EDGE,"E14.top"),sQuery(id+"F15.wireOp",EDGE,"E14.left"),sQuery(id+"F15.wireOp",EDGE,"E14.right"),sQuery(id+"F15.wireOp",EDGE,"E15.MirrorCS"),sQuery(id+"F15.wireOp",EDGE,"E16.MirrorCS"),sQuery(id+"F15.wireOp",EDGE,"E17.MirrorCS"),sQuery(id+"F15.wireOp",EDGE,"E18.MirrorCS"),sQuery(id+"F15.wireOp",EDGE,"E19.MirrorCS"),sQuery(id+"F15.wireOp",EDGE,"E20.MirrorCS"),sQuery(id+"F15.wireOp",EDGE,"E21.MirrorCS"),sQuery(id+"F15.wireOp",EDGE,"E22.MirrorCS"),sQuery(id+"F15.wireOp",EDGE,"E23.MirrorCS"),sQuery(id+"F15.wireOp",EDGE,"E24.MirrorCS"),sQuery(id+"F15.wireOp",EDGE,"E25.MirrorCS"),sQuery(id+"F15.wireOp",EDGE,"E26.MirrorCS")])]}),"instanceName":"1"}),"instanceName":"1"}),"instanceName":"1"});
            var Q102;
            Q102=makeQuery(id+"F23.opPattern","COPY",BODY,{"derivedFrom":makeQuery(id+"F20.opPattern","COPY",BODY,{"derivedFrom":makeQuery(id+"F18.opPattern","COPY",BODY,{"derivedFrom":makeQuery(id+"F16.opExtrude","SWEPT_BODY",BODY,{"disambiguationData":[OSD([sQuery(id+"F15.wireOp",EDGE,"E13.bottom"),sQuery(id+"F15.wireOp",EDGE,"E13.top"),sQuery(id+"F15.wireOp",EDGE,"E13.left"),sQuery(id+"F15.wireOp",EDGE,"E13.right"),sQuery(id+"F15.wireOp",EDGE,"E14.bottom"),sQuery(id+"F15.wireOp",EDGE,"E14.top"),sQuery(id+"F15.wireOp",EDGE,"E14.left"),sQuery(id+"F15.wireOp",EDGE,"E14.right"),sQuery(id+"F15.wireOp",EDGE,"E15.MirrorCS"),sQuery(id+"F15.wireOp",EDGE,"E16.MirrorCS"),sQuery(id+"F15.wireOp",EDGE,"E17.MirrorCS"),sQuery(id+"F15.wireOp",EDGE,"E18.MirrorCS"),sQuery(id+"F15.wireOp",EDGE,"E19.MirrorCS"),sQuery(id+"F15.wireOp",EDGE,"E20.MirrorCS"),sQuery(id+"F15.wireOp",EDGE,"E21.MirrorCS"),sQuery(id+"F15.wireOp",EDGE,"E22.MirrorCS"),sQuery(id+"F15.wireOp",EDGE,"E23.MirrorCS"),sQuery(id+"F15.wireOp",EDGE,"E24.MirrorCS"),sQuery(id+"F15.wireOp",EDGE,"E25.MirrorCS"),sQuery(id+"F15.wireOp",EDGE,"E26.MirrorCS")])]}),"instanceName":"1"}),"instanceName":"1"}),"instanceName":"1"});
            var Q103;
            Q103=makeQuery(id+"F23.opPattern","COPY",BODY,{"derivedFrom":makeQuery(id+"F20.opPattern","COPY",BODY,{"derivedFrom":makeQuery(id+"F18.opPattern","COPY",BODY,{"derivedFrom":makeQuery(id+"F17.opPattern","COPY",BODY,{"derivedFrom":makeQuery(id+"F16.opExtrude","SWEPT_BODY",BODY,{"disambiguationData":[OSD([sQuery(id+"F15.wireOp",EDGE,"E13.bottom"),sQuery(id+"F15.wireOp",EDGE,"E13.top"),sQuery(id+"F15.wireOp",EDGE,"E13.left"),sQuery(id+"F15.wireOp",EDGE,"E13.right"),sQuery(id+"F15.wireOp",EDGE,"E14.bottom"),sQuery(id+"F15.wireOp",EDGE,"E14.top"),sQuery(id+"F15.wireOp",EDGE,"E14.left"),sQuery(id+"F15.wireOp",EDGE,"E14.right"),sQuery(id+"F15.wireOp",EDGE,"E15.MirrorCS"),sQuery(id+"F15.wireOp",EDGE,"E16.MirrorCS"),sQuery(id+"F15.wireOp",EDGE,"E17.MirrorCS"),sQuery(id+"F15.wireOp",EDGE,"E18.MirrorCS"),sQuery(id+"F15.wireOp",EDGE,"E19.MirrorCS"),sQuery(id+"F15.wireOp",EDGE,"E20.MirrorCS"),sQuery(id+"F15.wireOp",EDGE,"E21.MirrorCS"),sQuery(id+"F15.wireOp",EDGE,"E22.MirrorCS"),sQuery(id+"F15.wireOp",EDGE,"E23.MirrorCS"),sQuery(id+"F15.wireOp",EDGE,"E24.MirrorCS"),sQuery(id+"F15.wireOp",EDGE,"E25.MirrorCS"),sQuery(id+"F15.wireOp",EDGE,"E26.MirrorCS")])]}),"instanceName":"1"}),"instanceName":"1"}),"instanceName":"1"}),"instanceName":"1"});
            var Q104;
            Q104=makeQuery(id+"F23.opPattern","COPY",BODY,{"derivedFrom":makeQuery(id+"F20.opPattern","COPY",BODY,{"derivedFrom":makeQuery(id+"F19.opPattern","COPY",BODY,{"derivedFrom":makeQuery(id+"F16.opExtrude","SWEPT_BODY",BODY,{"disambiguationData":[OSD([sQuery(id+"F15.wireOp",EDGE,"E13.bottom"),sQuery(id+"F15.wireOp",EDGE,"E13.top"),sQuery(id+"F15.wireOp",EDGE,"E13.left"),sQuery(id+"F15.wireOp",EDGE,"E13.right"),sQuery(id+"F15.wireOp",EDGE,"E14.bottom"),sQuery(id+"F15.wireOp",EDGE,"E14.top"),sQuery(id+"F15.wireOp",EDGE,"E14.left"),sQuery(id+"F15.wireOp",EDGE,"E14.right"),sQuery(id+"F15.wireOp",EDGE,"E15.MirrorCS"),sQuery(id+"F15.wireOp",EDGE,"E16.MirrorCS"),sQuery(id+"F15.wireOp",EDGE,"E17.MirrorCS"),sQuery(id+"F15.wireOp",EDGE,"E18.MirrorCS"),sQuery(id+"F15.wireOp",EDGE,"E19.MirrorCS"),sQuery(id+"F15.wireOp",EDGE,"E20.MirrorCS"),sQuery(id+"F15.wireOp",EDGE,"E21.MirrorCS"),sQuery(id+"F15.wireOp",EDGE,"E22.MirrorCS"),sQuery(id+"F15.wireOp",EDGE,"E23.MirrorCS"),sQuery(id+"F15.wireOp",EDGE,"E24.MirrorCS"),sQuery(id+"F15.wireOp",EDGE,"E25.MirrorCS"),sQuery(id+"F15.wireOp",EDGE,"E26.MirrorCS")])]}),"instanceName":"1"}),"instanceName":"1"}),"instanceName":"1"});
            var Q105;
            Q105=makeQuery(id+"F23.opPattern","COPY",BODY,{"derivedFrom":makeQuery(id+"F20.opPattern","COPY",BODY,{"derivedFrom":makeQuery(id+"F19.opPattern","COPY",BODY,{"derivedFrom":makeQuery(id+"F17.opPattern","COPY",BODY,{"derivedFrom":makeQuery(id+"F16.opExtrude","SWEPT_BODY",BODY,{"disambiguationData":[OSD([sQuery(id+"F15.wireOp",EDGE,"E13.bottom"),sQuery(id+"F15.wireOp",EDGE,"E13.top"),sQuery(id+"F15.wireOp",EDGE,"E13.left"),sQuery(id+"F15.wireOp",EDGE,"E13.right"),sQuery(id+"F15.wireOp",EDGE,"E14.bottom"),sQuery(id+"F15.wireOp",EDGE,"E14.top"),sQuery(id+"F15.wireOp",EDGE,"E14.left"),sQuery(id+"F15.wireOp",EDGE,"E14.right"),sQuery(id+"F15.wireOp",EDGE,"E15.MirrorCS"),sQuery(id+"F15.wireOp",EDGE,"E16.MirrorCS"),sQuery(id+"F15.wireOp",EDGE,"E17.MirrorCS"),sQuery(id+"F15.wireOp",EDGE,"E18.MirrorCS"),sQuery(id+"F15.wireOp",EDGE,"E19.MirrorCS"),sQuery(id+"F15.wireOp",EDGE,"E20.MirrorCS"),sQuery(id+"F15.wireOp",EDGE,"E21.MirrorCS"),sQuery(id+"F15.wireOp",EDGE,"E22.MirrorCS"),sQuery(id+"F15.wireOp",EDGE,"E23.MirrorCS"),sQuery(id+"F15.wireOp",EDGE,"E24.MirrorCS"),sQuery(id+"F15.wireOp",EDGE,"E25.MirrorCS"),sQuery(id+"F15.wireOp",EDGE,"E26.MirrorCS")])]}),"instanceName":"1"}),"instanceName":"1"}),"instanceName":"1"}),"instanceName":"1"});
            var Q106;
            Q106=makeQuery(id+"F23.opPattern","COPY",BODY,{"derivedFrom":makeQuery(id+"F20.opPattern","COPY",BODY,{"derivedFrom":makeQuery(id+"F19.opPattern","COPY",BODY,{"derivedFrom":makeQuery(id+"F18.opPattern","COPY",BODY,{"derivedFrom":makeQuery(id+"F16.opExtrude","SWEPT_BODY",BODY,{"disambiguationData":[OSD([sQuery(id+"F15.wireOp",EDGE,"E13.bottom"),sQuery(id+"F15.wireOp",EDGE,"E13.top"),sQuery(id+"F15.wireOp",EDGE,"E13.left"),sQuery(id+"F15.wireOp",EDGE,"E13.right"),sQuery(id+"F15.wireOp",EDGE,"E14.bottom"),sQuery(id+"F15.wireOp",EDGE,"E14.top"),sQuery(id+"F15.wireOp",EDGE,"E14.left"),sQuery(id+"F15.wireOp",EDGE,"E14.right"),sQuery(id+"F15.wireOp",EDGE,"E15.MirrorCS"),sQuery(id+"F15.wireOp",EDGE,"E16.MirrorCS"),sQuery(id+"F15.wireOp",EDGE,"E17.MirrorCS"),sQuery(id+"F15.wireOp",EDGE,"E18.MirrorCS"),sQuery(id+"F15.wireOp",EDGE,"E19.MirrorCS"),sQuery(id+"F15.wireOp",EDGE,"E20.MirrorCS"),sQuery(id+"F15.wireOp",EDGE,"E21.MirrorCS"),sQuery(id+"F15.wireOp",EDGE,"E22.MirrorCS"),sQuery(id+"F15.wireOp",EDGE,"E23.MirrorCS"),sQuery(id+"F15.wireOp",EDGE,"E24.MirrorCS"),sQuery(id+"F15.wireOp",EDGE,"E25.MirrorCS"),sQuery(id+"F15.wireOp",EDGE,"E26.MirrorCS")])]}),"instanceName":"1"}),"instanceName":"1"}),"instanceName":"1"}),"instanceName":"1"});
            var Q107;
            Q107=makeQuery(id+"F23.opPattern","COPY",BODY,{"derivedFrom":makeQuery(id+"F20.opPattern","COPY",BODY,{"derivedFrom":makeQuery(id+"F19.opPattern","COPY",BODY,{"derivedFrom":makeQuery(id+"F18.opPattern","COPY",BODY,{"derivedFrom":makeQuery(id+"F17.opPattern","COPY",BODY,{"derivedFrom":makeQuery(id+"F16.opExtrude","SWEPT_BODY",BODY,{"disambiguationData":[OSD([sQuery(id+"F15.wireOp",EDGE,"E13.bottom"),sQuery(id+"F15.wireOp",EDGE,"E13.top"),sQuery(id+"F15.wireOp",EDGE,"E13.left"),sQuery(id+"F15.wireOp",EDGE,"E13.right"),sQuery(id+"F15.wireOp",EDGE,"E14.bottom"),sQuery(id+"F15.wireOp",EDGE,"E14.top"),sQuery(id+"F15.wireOp",EDGE,"E14.left"),sQuery(id+"F15.wireOp",EDGE,"E14.right"),sQuery(id+"F15.wireOp",EDGE,"E15.MirrorCS"),sQuery(id+"F15.wireOp",EDGE,"E16.MirrorCS"),sQuery(id+"F15.wireOp",EDGE,"E17.MirrorCS"),sQuery(id+"F15.wireOp",EDGE,"E18.MirrorCS"),sQuery(id+"F15.wireOp",EDGE,"E19.MirrorCS"),sQuery(id+"F15.wireOp",EDGE,"E20.MirrorCS"),sQuery(id+"F15.wireOp",EDGE,"E21.MirrorCS"),sQuery(id+"F15.wireOp",EDGE,"E22.MirrorCS"),sQuery(id+"F15.wireOp",EDGE,"E23.MirrorCS"),sQuery(id+"F15.wireOp",EDGE,"E24.MirrorCS"),sQuery(id+"F15.wireOp",EDGE,"E25.MirrorCS"),sQuery(id+"F15.wireOp",EDGE,"E26.MirrorCS")])]}),"instanceName":"1"}),"instanceName":"1"}),"instanceName":"1"}),"instanceName":"1"}),"instanceName":"1"});
            var Q108;
            Q108=makeQuery(id+"F23.opPattern","COPY",BODY,{"derivedFrom":makeQuery(id+"F21.opPattern","COPY",BODY,{"derivedFrom":makeQuery(id+"F16.opExtrude","SWEPT_BODY",BODY,{"disambiguationData":[OSD([sQuery(id+"F15.wireOp",EDGE,"E13.bottom"),sQuery(id+"F15.wireOp",EDGE,"E13.top"),sQuery(id+"F15.wireOp",EDGE,"E13.left"),sQuery(id+"F15.wireOp",EDGE,"E13.right"),sQuery(id+"F15.wireOp",EDGE,"E14.bottom"),sQuery(id+"F15.wireOp",EDGE,"E14.top"),sQuery(id+"F15.wireOp",EDGE,"E14.left"),sQuery(id+"F15.wireOp",EDGE,"E14.right"),sQuery(id+"F15.wireOp",EDGE,"E15.MirrorCS"),sQuery(id+"F15.wireOp",EDGE,"E16.MirrorCS"),sQuery(id+"F15.wireOp",EDGE,"E17.MirrorCS"),sQuery(id+"F15.wireOp",EDGE,"E18.MirrorCS"),sQuery(id+"F15.wireOp",EDGE,"E19.MirrorCS"),sQuery(id+"F15.wireOp",EDGE,"E20.MirrorCS"),sQuery(id+"F15.wireOp",EDGE,"E21.MirrorCS"),sQuery(id+"F15.wireOp",EDGE,"E22.MirrorCS"),sQuery(id+"F15.wireOp",EDGE,"E23.MirrorCS"),sQuery(id+"F15.wireOp",EDGE,"E24.MirrorCS"),sQuery(id+"F15.wireOp",EDGE,"E25.MirrorCS"),sQuery(id+"F15.wireOp",EDGE,"E26.MirrorCS")])]}),"instanceName":"1"}),"instanceName":"1"});
            var Q109;
            Q109=makeQuery(id+"F23.opPattern","COPY",BODY,{"derivedFrom":makeQuery(id+"F21.opPattern","COPY",BODY,{"derivedFrom":makeQuery(id+"F17.opPattern","COPY",BODY,{"derivedFrom":makeQuery(id+"F16.opExtrude","SWEPT_BODY",BODY,{"disambiguationData":[OSD([sQuery(id+"F15.wireOp",EDGE,"E13.bottom"),sQuery(id+"F15.wireOp",EDGE,"E13.top"),sQuery(id+"F15.wireOp",EDGE,"E13.left"),sQuery(id+"F15.wireOp",EDGE,"E13.right"),sQuery(id+"F15.wireOp",EDGE,"E14.bottom"),sQuery(id+"F15.wireOp",EDGE,"E14.top"),sQuery(id+"F15.wireOp",EDGE,"E14.left"),sQuery(id+"F15.wireOp",EDGE,"E14.right"),sQuery(id+"F15.wireOp",EDGE,"E15.MirrorCS"),sQuery(id+"F15.wireOp",EDGE,"E16.MirrorCS"),sQuery(id+"F15.wireOp",EDGE,"E17.MirrorCS"),sQuery(id+"F15.wireOp",EDGE,"E18.MirrorCS"),sQuery(id+"F15.wireOp",EDGE,"E19.MirrorCS"),sQuery(id+"F15.wireOp",EDGE,"E20.MirrorCS"),sQuery(id+"F15.wireOp",EDGE,"E21.MirrorCS"),sQuery(id+"F15.wireOp",EDGE,"E22.MirrorCS"),sQuery(id+"F15.wireOp",EDGE,"E23.MirrorCS"),sQuery(id+"F15.wireOp",EDGE,"E24.MirrorCS"),sQuery(id+"F15.wireOp",EDGE,"E25.MirrorCS"),sQuery(id+"F15.wireOp",EDGE,"E26.MirrorCS")])]}),"instanceName":"1"}),"instanceName":"1"}),"instanceName":"1"});
            var Q110;
            Q110=makeQuery(id+"F23.opPattern","COPY",BODY,{"derivedFrom":makeQuery(id+"F21.opPattern","COPY",BODY,{"derivedFrom":makeQuery(id+"F18.opPattern","COPY",BODY,{"derivedFrom":makeQuery(id+"F16.opExtrude","SWEPT_BODY",BODY,{"disambiguationData":[OSD([sQuery(id+"F15.wireOp",EDGE,"E13.bottom"),sQuery(id+"F15.wireOp",EDGE,"E13.top"),sQuery(id+"F15.wireOp",EDGE,"E13.left"),sQuery(id+"F15.wireOp",EDGE,"E13.right"),sQuery(id+"F15.wireOp",EDGE,"E14.bottom"),sQuery(id+"F15.wireOp",EDGE,"E14.top"),sQuery(id+"F15.wireOp",EDGE,"E14.left"),sQuery(id+"F15.wireOp",EDGE,"E14.right"),sQuery(id+"F15.wireOp",EDGE,"E15.MirrorCS"),sQuery(id+"F15.wireOp",EDGE,"E16.MirrorCS"),sQuery(id+"F15.wireOp",EDGE,"E17.MirrorCS"),sQuery(id+"F15.wireOp",EDGE,"E18.MirrorCS"),sQuery(id+"F15.wireOp",EDGE,"E19.MirrorCS"),sQuery(id+"F15.wireOp",EDGE,"E20.MirrorCS"),sQuery(id+"F15.wireOp",EDGE,"E21.MirrorCS"),sQuery(id+"F15.wireOp",EDGE,"E22.MirrorCS"),sQuery(id+"F15.wireOp",EDGE,"E23.MirrorCS"),sQuery(id+"F15.wireOp",EDGE,"E24.MirrorCS"),sQuery(id+"F15.wireOp",EDGE,"E25.MirrorCS"),sQuery(id+"F15.wireOp",EDGE,"E26.MirrorCS")])]}),"instanceName":"1"}),"instanceName":"1"}),"instanceName":"1"});
            var Q111;
            Q111=makeQuery(id+"F23.opPattern","COPY",BODY,{"derivedFrom":makeQuery(id+"F21.opPattern","COPY",BODY,{"derivedFrom":makeQuery(id+"F18.opPattern","COPY",BODY,{"derivedFrom":makeQuery(id+"F17.opPattern","COPY",BODY,{"derivedFrom":makeQuery(id+"F16.opExtrude","SWEPT_BODY",BODY,{"disambiguationData":[OSD([sQuery(id+"F15.wireOp",EDGE,"E13.bottom"),sQuery(id+"F15.wireOp",EDGE,"E13.top"),sQuery(id+"F15.wireOp",EDGE,"E13.left"),sQuery(id+"F15.wireOp",EDGE,"E13.right"),sQuery(id+"F15.wireOp",EDGE,"E14.bottom"),sQuery(id+"F15.wireOp",EDGE,"E14.top"),sQuery(id+"F15.wireOp",EDGE,"E14.left"),sQuery(id+"F15.wireOp",EDGE,"E14.right"),sQuery(id+"F15.wireOp",EDGE,"E15.MirrorCS"),sQuery(id+"F15.wireOp",EDGE,"E16.MirrorCS"),sQuery(id+"F15.wireOp",EDGE,"E17.MirrorCS"),sQuery(id+"F15.wireOp",EDGE,"E18.MirrorCS"),sQuery(id+"F15.wireOp",EDGE,"E19.MirrorCS"),sQuery(id+"F15.wireOp",EDGE,"E20.MirrorCS"),sQuery(id+"F15.wireOp",EDGE,"E21.MirrorCS"),sQuery(id+"F15.wireOp",EDGE,"E22.MirrorCS"),sQuery(id+"F15.wireOp",EDGE,"E23.MirrorCS"),sQuery(id+"F15.wireOp",EDGE,"E24.MirrorCS"),sQuery(id+"F15.wireOp",EDGE,"E25.MirrorCS"),sQuery(id+"F15.wireOp",EDGE,"E26.MirrorCS")])]}),"instanceName":"1"}),"instanceName":"1"}),"instanceName":"1"}),"instanceName":"1"});
            var Q112;
            Q112=makeQuery(id+"F23.opPattern","COPY",BODY,{"derivedFrom":makeQuery(id+"F21.opPattern","COPY",BODY,{"derivedFrom":makeQuery(id+"F19.opPattern","COPY",BODY,{"derivedFrom":makeQuery(id+"F16.opExtrude","SWEPT_BODY",BODY,{"disambiguationData":[OSD([sQuery(id+"F15.wireOp",EDGE,"E13.bottom"),sQuery(id+"F15.wireOp",EDGE,"E13.top"),sQuery(id+"F15.wireOp",EDGE,"E13.left"),sQuery(id+"F15.wireOp",EDGE,"E13.right"),sQuery(id+"F15.wireOp",EDGE,"E14.bottom"),sQuery(id+"F15.wireOp",EDGE,"E14.top"),sQuery(id+"F15.wireOp",EDGE,"E14.left"),sQuery(id+"F15.wireOp",EDGE,"E14.right"),sQuery(id+"F15.wireOp",EDGE,"E15.MirrorCS"),sQuery(id+"F15.wireOp",EDGE,"E16.MirrorCS"),sQuery(id+"F15.wireOp",EDGE,"E17.MirrorCS"),sQuery(id+"F15.wireOp",EDGE,"E18.MirrorCS"),sQuery(id+"F15.wireOp",EDGE,"E19.MirrorCS"),sQuery(id+"F15.wireOp",EDGE,"E20.MirrorCS"),sQuery(id+"F15.wireOp",EDGE,"E21.MirrorCS"),sQuery(id+"F15.wireOp",EDGE,"E22.MirrorCS"),sQuery(id+"F15.wireOp",EDGE,"E23.MirrorCS"),sQuery(id+"F15.wireOp",EDGE,"E24.MirrorCS"),sQuery(id+"F15.wireOp",EDGE,"E25.MirrorCS"),sQuery(id+"F15.wireOp",EDGE,"E26.MirrorCS")])]}),"instanceName":"1"}),"instanceName":"1"}),"instanceName":"1"});
            var Q113;
            Q113=makeQuery(id+"F23.opPattern","COPY",BODY,{"derivedFrom":makeQuery(id+"F21.opPattern","COPY",BODY,{"derivedFrom":makeQuery(id+"F19.opPattern","COPY",BODY,{"derivedFrom":makeQuery(id+"F17.opPattern","COPY",BODY,{"derivedFrom":makeQuery(id+"F16.opExtrude","SWEPT_BODY",BODY,{"disambiguationData":[OSD([sQuery(id+"F15.wireOp",EDGE,"E13.bottom"),sQuery(id+"F15.wireOp",EDGE,"E13.top"),sQuery(id+"F15.wireOp",EDGE,"E13.left"),sQuery(id+"F15.wireOp",EDGE,"E13.right"),sQuery(id+"F15.wireOp",EDGE,"E14.bottom"),sQuery(id+"F15.wireOp",EDGE,"E14.top"),sQuery(id+"F15.wireOp",EDGE,"E14.left"),sQuery(id+"F15.wireOp",EDGE,"E14.right"),sQuery(id+"F15.wireOp",EDGE,"E15.MirrorCS"),sQuery(id+"F15.wireOp",EDGE,"E16.MirrorCS"),sQuery(id+"F15.wireOp",EDGE,"E17.MirrorCS"),sQuery(id+"F15.wireOp",EDGE,"E18.MirrorCS"),sQuery(id+"F15.wireOp",EDGE,"E19.MirrorCS"),sQuery(id+"F15.wireOp",EDGE,"E20.MirrorCS"),sQuery(id+"F15.wireOp",EDGE,"E21.MirrorCS"),sQuery(id+"F15.wireOp",EDGE,"E22.MirrorCS"),sQuery(id+"F15.wireOp",EDGE,"E23.MirrorCS"),sQuery(id+"F15.wireOp",EDGE,"E24.MirrorCS"),sQuery(id+"F15.wireOp",EDGE,"E25.MirrorCS"),sQuery(id+"F15.wireOp",EDGE,"E26.MirrorCS")])]}),"instanceName":"1"}),"instanceName":"1"}),"instanceName":"1"}),"instanceName":"1"});
            var Q114;
            Q114=makeQuery(id+"F23.opPattern","COPY",BODY,{"derivedFrom":makeQuery(id+"F21.opPattern","COPY",BODY,{"derivedFrom":makeQuery(id+"F19.opPattern","COPY",BODY,{"derivedFrom":makeQuery(id+"F18.opPattern","COPY",BODY,{"derivedFrom":makeQuery(id+"F16.opExtrude","SWEPT_BODY",BODY,{"disambiguationData":[OSD([sQuery(id+"F15.wireOp",EDGE,"E13.bottom"),sQuery(id+"F15.wireOp",EDGE,"E13.top"),sQuery(id+"F15.wireOp",EDGE,"E13.left"),sQuery(id+"F15.wireOp",EDGE,"E13.right"),sQuery(id+"F15.wireOp",EDGE,"E14.bottom"),sQuery(id+"F15.wireOp",EDGE,"E14.top"),sQuery(id+"F15.wireOp",EDGE,"E14.left"),sQuery(id+"F15.wireOp",EDGE,"E14.right"),sQuery(id+"F15.wireOp",EDGE,"E15.MirrorCS"),sQuery(id+"F15.wireOp",EDGE,"E16.MirrorCS"),sQuery(id+"F15.wireOp",EDGE,"E17.MirrorCS"),sQuery(id+"F15.wireOp",EDGE,"E18.MirrorCS"),sQuery(id+"F15.wireOp",EDGE,"E19.MirrorCS"),sQuery(id+"F15.wireOp",EDGE,"E20.MirrorCS"),sQuery(id+"F15.wireOp",EDGE,"E21.MirrorCS"),sQuery(id+"F15.wireOp",EDGE,"E22.MirrorCS"),sQuery(id+"F15.wireOp",EDGE,"E23.MirrorCS"),sQuery(id+"F15.wireOp",EDGE,"E24.MirrorCS"),sQuery(id+"F15.wireOp",EDGE,"E25.MirrorCS"),sQuery(id+"F15.wireOp",EDGE,"E26.MirrorCS")])]}),"instanceName":"1"}),"instanceName":"1"}),"instanceName":"1"}),"instanceName":"1"});
            var Q115;
            Q115=makeQuery(id+"F23.opPattern","COPY",BODY,{"derivedFrom":makeQuery(id+"F21.opPattern","COPY",BODY,{"derivedFrom":makeQuery(id+"F19.opPattern","COPY",BODY,{"derivedFrom":makeQuery(id+"F18.opPattern","COPY",BODY,{"derivedFrom":makeQuery(id+"F17.opPattern","COPY",BODY,{"derivedFrom":makeQuery(id+"F16.opExtrude","SWEPT_BODY",BODY,{"disambiguationData":[OSD([sQuery(id+"F15.wireOp",EDGE,"E13.bottom"),sQuery(id+"F15.wireOp",EDGE,"E13.top"),sQuery(id+"F15.wireOp",EDGE,"E13.left"),sQuery(id+"F15.wireOp",EDGE,"E13.right"),sQuery(id+"F15.wireOp",EDGE,"E14.bottom"),sQuery(id+"F15.wireOp",EDGE,"E14.top"),sQuery(id+"F15.wireOp",EDGE,"E14.left"),sQuery(id+"F15.wireOp",EDGE,"E14.right"),sQuery(id+"F15.wireOp",EDGE,"E15.MirrorCS"),sQuery(id+"F15.wireOp",EDGE,"E16.MirrorCS"),sQuery(id+"F15.wireOp",EDGE,"E17.MirrorCS"),sQuery(id+"F15.wireOp",EDGE,"E18.MirrorCS"),sQuery(id+"F15.wireOp",EDGE,"E19.MirrorCS"),sQuery(id+"F15.wireOp",EDGE,"E20.MirrorCS"),sQuery(id+"F15.wireOp",EDGE,"E21.MirrorCS"),sQuery(id+"F15.wireOp",EDGE,"E22.MirrorCS"),sQuery(id+"F15.wireOp",EDGE,"E23.MirrorCS"),sQuery(id+"F15.wireOp",EDGE,"E24.MirrorCS"),sQuery(id+"F15.wireOp",EDGE,"E25.MirrorCS"),sQuery(id+"F15.wireOp",EDGE,"E26.MirrorCS")])]}),"instanceName":"1"}),"instanceName":"1"}),"instanceName":"1"}),"instanceName":"1"}),"instanceName":"1"});
            var Q116;
            Q116=makeQuery(id+"F23.opPattern","COPY",BODY,{"derivedFrom":makeQuery(id+"F22.opPattern","COPY",BODY,{"derivedFrom":makeQuery(id+"F19.opPattern","COPY",BODY,{"derivedFrom":makeQuery(id+"F16.opExtrude","SWEPT_BODY",BODY,{"disambiguationData":[OSD([sQuery(id+"F15.wireOp",EDGE,"E13.bottom"),sQuery(id+"F15.wireOp",EDGE,"E13.top"),sQuery(id+"F15.wireOp",EDGE,"E13.left"),sQuery(id+"F15.wireOp",EDGE,"E13.right"),sQuery(id+"F15.wireOp",EDGE,"E14.bottom"),sQuery(id+"F15.wireOp",EDGE,"E14.top"),sQuery(id+"F15.wireOp",EDGE,"E14.left"),sQuery(id+"F15.wireOp",EDGE,"E14.right"),sQuery(id+"F15.wireOp",EDGE,"E15.MirrorCS"),sQuery(id+"F15.wireOp",EDGE,"E16.MirrorCS"),sQuery(id+"F15.wireOp",EDGE,"E17.MirrorCS"),sQuery(id+"F15.wireOp",EDGE,"E18.MirrorCS"),sQuery(id+"F15.wireOp",EDGE,"E19.MirrorCS"),sQuery(id+"F15.wireOp",EDGE,"E20.MirrorCS"),sQuery(id+"F15.wireOp",EDGE,"E21.MirrorCS"),sQuery(id+"F15.wireOp",EDGE,"E22.MirrorCS"),sQuery(id+"F15.wireOp",EDGE,"E23.MirrorCS"),sQuery(id+"F15.wireOp",EDGE,"E24.MirrorCS"),sQuery(id+"F15.wireOp",EDGE,"E25.MirrorCS"),sQuery(id+"F15.wireOp",EDGE,"E26.MirrorCS")])]}),"instanceName":"1"}),"instanceName":"1"}),"instanceName":"1"});
            var Q117;
            Q117=makeQuery(id+"F23.opPattern","COPY",BODY,{"derivedFrom":makeQuery(id+"F22.opPattern","COPY",BODY,{"derivedFrom":makeQuery(id+"F19.opPattern","COPY",BODY,{"derivedFrom":makeQuery(id+"F17.opPattern","COPY",BODY,{"derivedFrom":makeQuery(id+"F16.opExtrude","SWEPT_BODY",BODY,{"disambiguationData":[OSD([sQuery(id+"F15.wireOp",EDGE,"E13.bottom"),sQuery(id+"F15.wireOp",EDGE,"E13.top"),sQuery(id+"F15.wireOp",EDGE,"E13.left"),sQuery(id+"F15.wireOp",EDGE,"E13.right"),sQuery(id+"F15.wireOp",EDGE,"E14.bottom"),sQuery(id+"F15.wireOp",EDGE,"E14.top"),sQuery(id+"F15.wireOp",EDGE,"E14.left"),sQuery(id+"F15.wireOp",EDGE,"E14.right"),sQuery(id+"F15.wireOp",EDGE,"E15.MirrorCS"),sQuery(id+"F15.wireOp",EDGE,"E16.MirrorCS"),sQuery(id+"F15.wireOp",EDGE,"E17.MirrorCS"),sQuery(id+"F15.wireOp",EDGE,"E18.MirrorCS"),sQuery(id+"F15.wireOp",EDGE,"E19.MirrorCS"),sQuery(id+"F15.wireOp",EDGE,"E20.MirrorCS"),sQuery(id+"F15.wireOp",EDGE,"E21.MirrorCS"),sQuery(id+"F15.wireOp",EDGE,"E22.MirrorCS"),sQuery(id+"F15.wireOp",EDGE,"E23.MirrorCS"),sQuery(id+"F15.wireOp",EDGE,"E24.MirrorCS"),sQuery(id+"F15.wireOp",EDGE,"E25.MirrorCS"),sQuery(id+"F15.wireOp",EDGE,"E26.MirrorCS")])]}),"instanceName":"1"}),"instanceName":"1"}),"instanceName":"1"}),"instanceName":"1"});
            var Q118;
            Q118=makeQuery(id+"F23.opPattern","COPY",BODY,{"derivedFrom":makeQuery(id+"F22.opPattern","COPY",BODY,{"derivedFrom":makeQuery(id+"F19.opPattern","COPY",BODY,{"derivedFrom":makeQuery(id+"F18.opPattern","COPY",BODY,{"derivedFrom":makeQuery(id+"F16.opExtrude","SWEPT_BODY",BODY,{"disambiguationData":[OSD([sQuery(id+"F15.wireOp",EDGE,"E13.bottom"),sQuery(id+"F15.wireOp",EDGE,"E13.top"),sQuery(id+"F15.wireOp",EDGE,"E13.left"),sQuery(id+"F15.wireOp",EDGE,"E13.right"),sQuery(id+"F15.wireOp",EDGE,"E14.bottom"),sQuery(id+"F15.wireOp",EDGE,"E14.top"),sQuery(id+"F15.wireOp",EDGE,"E14.left"),sQuery(id+"F15.wireOp",EDGE,"E14.right"),sQuery(id+"F15.wireOp",EDGE,"E15.MirrorCS"),sQuery(id+"F15.wireOp",EDGE,"E16.MirrorCS"),sQuery(id+"F15.wireOp",EDGE,"E17.MirrorCS"),sQuery(id+"F15.wireOp",EDGE,"E18.MirrorCS"),sQuery(id+"F15.wireOp",EDGE,"E19.MirrorCS"),sQuery(id+"F15.wireOp",EDGE,"E20.MirrorCS"),sQuery(id+"F15.wireOp",EDGE,"E21.MirrorCS"),sQuery(id+"F15.wireOp",EDGE,"E22.MirrorCS"),sQuery(id+"F15.wireOp",EDGE,"E23.MirrorCS"),sQuery(id+"F15.wireOp",EDGE,"E24.MirrorCS"),sQuery(id+"F15.wireOp",EDGE,"E25.MirrorCS"),sQuery(id+"F15.wireOp",EDGE,"E26.MirrorCS")])]}),"instanceName":"1"}),"instanceName":"1"}),"instanceName":"1"}),"instanceName":"1"});
            var Q119;
            Q119=makeQuery(id+"F23.opPattern","COPY",BODY,{"derivedFrom":makeQuery(id+"F22.opPattern","COPY",BODY,{"derivedFrom":makeQuery(id+"F19.opPattern","COPY",BODY,{"derivedFrom":makeQuery(id+"F18.opPattern","COPY",BODY,{"derivedFrom":makeQuery(id+"F17.opPattern","COPY",BODY,{"derivedFrom":makeQuery(id+"F16.opExtrude","SWEPT_BODY",BODY,{"disambiguationData":[OSD([sQuery(id+"F15.wireOp",EDGE,"E13.bottom"),sQuery(id+"F15.wireOp",EDGE,"E13.top"),sQuery(id+"F15.wireOp",EDGE,"E13.left"),sQuery(id+"F15.wireOp",EDGE,"E13.right"),sQuery(id+"F15.wireOp",EDGE,"E14.bottom"),sQuery(id+"F15.wireOp",EDGE,"E14.top"),sQuery(id+"F15.wireOp",EDGE,"E14.left"),sQuery(id+"F15.wireOp",EDGE,"E14.right"),sQuery(id+"F15.wireOp",EDGE,"E15.MirrorCS"),sQuery(id+"F15.wireOp",EDGE,"E16.MirrorCS"),sQuery(id+"F15.wireOp",EDGE,"E17.MirrorCS"),sQuery(id+"F15.wireOp",EDGE,"E18.MirrorCS"),sQuery(id+"F15.wireOp",EDGE,"E19.MirrorCS"),sQuery(id+"F15.wireOp",EDGE,"E20.MirrorCS"),sQuery(id+"F15.wireOp",EDGE,"E21.MirrorCS"),sQuery(id+"F15.wireOp",EDGE,"E22.MirrorCS"),sQuery(id+"F15.wireOp",EDGE,"E23.MirrorCS"),sQuery(id+"F15.wireOp",EDGE,"E24.MirrorCS"),sQuery(id+"F15.wireOp",EDGE,"E25.MirrorCS"),sQuery(id+"F15.wireOp",EDGE,"E26.MirrorCS")])]}),"instanceName":"1"}),"instanceName":"1"}),"instanceName":"1"}),"instanceName":"1"}),"instanceName":"1"});
            var Q120;
            Q120=makeQuery(id+"F23.opPattern","COPY",BODY,{"derivedFrom":makeQuery(id+"F22.opPattern","COPY",BODY,{"derivedFrom":makeQuery(id+"F20.opPattern","COPY",BODY,{"derivedFrom":makeQuery(id+"F16.opExtrude","SWEPT_BODY",BODY,{"disambiguationData":[OSD([sQuery(id+"F15.wireOp",EDGE,"E13.bottom"),sQuery(id+"F15.wireOp",EDGE,"E13.top"),sQuery(id+"F15.wireOp",EDGE,"E13.left"),sQuery(id+"F15.wireOp",EDGE,"E13.right"),sQuery(id+"F15.wireOp",EDGE,"E14.bottom"),sQuery(id+"F15.wireOp",EDGE,"E14.top"),sQuery(id+"F15.wireOp",EDGE,"E14.left"),sQuery(id+"F15.wireOp",EDGE,"E14.right"),sQuery(id+"F15.wireOp",EDGE,"E15.MirrorCS"),sQuery(id+"F15.wireOp",EDGE,"E16.MirrorCS"),sQuery(id+"F15.wireOp",EDGE,"E17.MirrorCS"),sQuery(id+"F15.wireOp",EDGE,"E18.MirrorCS"),sQuery(id+"F15.wireOp",EDGE,"E19.MirrorCS"),sQuery(id+"F15.wireOp",EDGE,"E20.MirrorCS"),sQuery(id+"F15.wireOp",EDGE,"E21.MirrorCS"),sQuery(id+"F15.wireOp",EDGE,"E22.MirrorCS"),sQuery(id+"F15.wireOp",EDGE,"E23.MirrorCS"),sQuery(id+"F15.wireOp",EDGE,"E24.MirrorCS"),sQuery(id+"F15.wireOp",EDGE,"E25.MirrorCS"),sQuery(id+"F15.wireOp",EDGE,"E26.MirrorCS")])]}),"instanceName":"1"}),"instanceName":"1"}),"instanceName":"1"});
            var Q121;
            Q121=makeQuery(id+"F23.opPattern","COPY",BODY,{"derivedFrom":makeQuery(id+"F22.opPattern","COPY",BODY,{"derivedFrom":makeQuery(id+"F20.opPattern","COPY",BODY,{"derivedFrom":makeQuery(id+"F17.opPattern","COPY",BODY,{"derivedFrom":makeQuery(id+"F16.opExtrude","SWEPT_BODY",BODY,{"disambiguationData":[OSD([sQuery(id+"F15.wireOp",EDGE,"E13.bottom"),sQuery(id+"F15.wireOp",EDGE,"E13.top"),sQuery(id+"F15.wireOp",EDGE,"E13.left"),sQuery(id+"F15.wireOp",EDGE,"E13.right"),sQuery(id+"F15.wireOp",EDGE,"E14.bottom"),sQuery(id+"F15.wireOp",EDGE,"E14.top"),sQuery(id+"F15.wireOp",EDGE,"E14.left"),sQuery(id+"F15.wireOp",EDGE,"E14.right"),sQuery(id+"F15.wireOp",EDGE,"E15.MirrorCS"),sQuery(id+"F15.wireOp",EDGE,"E16.MirrorCS"),sQuery(id+"F15.wireOp",EDGE,"E17.MirrorCS"),sQuery(id+"F15.wireOp",EDGE,"E18.MirrorCS"),sQuery(id+"F15.wireOp",EDGE,"E19.MirrorCS"),sQuery(id+"F15.wireOp",EDGE,"E20.MirrorCS"),sQuery(id+"F15.wireOp",EDGE,"E21.MirrorCS"),sQuery(id+"F15.wireOp",EDGE,"E22.MirrorCS"),sQuery(id+"F15.wireOp",EDGE,"E23.MirrorCS"),sQuery(id+"F15.wireOp",EDGE,"E24.MirrorCS"),sQuery(id+"F15.wireOp",EDGE,"E25.MirrorCS"),sQuery(id+"F15.wireOp",EDGE,"E26.MirrorCS")])]}),"instanceName":"1"}),"instanceName":"1"}),"instanceName":"1"}),"instanceName":"1"});
            var Q122;
            Q122=makeQuery(id+"F23.opPattern","COPY",BODY,{"derivedFrom":makeQuery(id+"F22.opPattern","COPY",BODY,{"derivedFrom":makeQuery(id+"F20.opPattern","COPY",BODY,{"derivedFrom":makeQuery(id+"F18.opPattern","COPY",BODY,{"derivedFrom":makeQuery(id+"F16.opExtrude","SWEPT_BODY",BODY,{"disambiguationData":[OSD([sQuery(id+"F15.wireOp",EDGE,"E13.bottom"),sQuery(id+"F15.wireOp",EDGE,"E13.top"),sQuery(id+"F15.wireOp",EDGE,"E13.left"),sQuery(id+"F15.wireOp",EDGE,"E13.right"),sQuery(id+"F15.wireOp",EDGE,"E14.bottom"),sQuery(id+"F15.wireOp",EDGE,"E14.top"),sQuery(id+"F15.wireOp",EDGE,"E14.left"),sQuery(id+"F15.wireOp",EDGE,"E14.right"),sQuery(id+"F15.wireOp",EDGE,"E15.MirrorCS"),sQuery(id+"F15.wireOp",EDGE,"E16.MirrorCS"),sQuery(id+"F15.wireOp",EDGE,"E17.MirrorCS"),sQuery(id+"F15.wireOp",EDGE,"E18.MirrorCS"),sQuery(id+"F15.wireOp",EDGE,"E19.MirrorCS"),sQuery(id+"F15.wireOp",EDGE,"E20.MirrorCS"),sQuery(id+"F15.wireOp",EDGE,"E21.MirrorCS"),sQuery(id+"F15.wireOp",EDGE,"E22.MirrorCS"),sQuery(id+"F15.wireOp",EDGE,"E23.MirrorCS"),sQuery(id+"F15.wireOp",EDGE,"E24.MirrorCS"),sQuery(id+"F15.wireOp",EDGE,"E25.MirrorCS"),sQuery(id+"F15.wireOp",EDGE,"E26.MirrorCS")])]}),"instanceName":"1"}),"instanceName":"1"}),"instanceName":"1"}),"instanceName":"1"});
            var Q123;
            Q123=makeQuery(id+"F23.opPattern","COPY",BODY,{"derivedFrom":makeQuery(id+"F22.opPattern","COPY",BODY,{"derivedFrom":makeQuery(id+"F20.opPattern","COPY",BODY,{"derivedFrom":makeQuery(id+"F18.opPattern","COPY",BODY,{"derivedFrom":makeQuery(id+"F17.opPattern","COPY",BODY,{"derivedFrom":makeQuery(id+"F16.opExtrude","SWEPT_BODY",BODY,{"disambiguationData":[OSD([sQuery(id+"F15.wireOp",EDGE,"E13.bottom"),sQuery(id+"F15.wireOp",EDGE,"E13.top"),sQuery(id+"F15.wireOp",EDGE,"E13.left"),sQuery(id+"F15.wireOp",EDGE,"E13.right"),sQuery(id+"F15.wireOp",EDGE,"E14.bottom"),sQuery(id+"F15.wireOp",EDGE,"E14.top"),sQuery(id+"F15.wireOp",EDGE,"E14.left"),sQuery(id+"F15.wireOp",EDGE,"E14.right"),sQuery(id+"F15.wireOp",EDGE,"E15.MirrorCS"),sQuery(id+"F15.wireOp",EDGE,"E16.MirrorCS"),sQuery(id+"F15.wireOp",EDGE,"E17.MirrorCS"),sQuery(id+"F15.wireOp",EDGE,"E18.MirrorCS"),sQuery(id+"F15.wireOp",EDGE,"E19.MirrorCS"),sQuery(id+"F15.wireOp",EDGE,"E20.MirrorCS"),sQuery(id+"F15.wireOp",EDGE,"E21.MirrorCS"),sQuery(id+"F15.wireOp",EDGE,"E22.MirrorCS"),sQuery(id+"F15.wireOp",EDGE,"E23.MirrorCS"),sQuery(id+"F15.wireOp",EDGE,"E24.MirrorCS"),sQuery(id+"F15.wireOp",EDGE,"E25.MirrorCS"),sQuery(id+"F15.wireOp",EDGE,"E26.MirrorCS")])]}),"instanceName":"1"}),"instanceName":"1"}),"instanceName":"1"}),"instanceName":"1"}),"instanceName":"1"});
            var Q124;
            Q124=makeQuery(id+"F23.opPattern","COPY",BODY,{"derivedFrom":makeQuery(id+"F22.opPattern","COPY",BODY,{"derivedFrom":makeQuery(id+"F20.opPattern","COPY",BODY,{"derivedFrom":makeQuery(id+"F19.opPattern","COPY",BODY,{"derivedFrom":makeQuery(id+"F16.opExtrude","SWEPT_BODY",BODY,{"disambiguationData":[OSD([sQuery(id+"F15.wireOp",EDGE,"E13.bottom"),sQuery(id+"F15.wireOp",EDGE,"E13.top"),sQuery(id+"F15.wireOp",EDGE,"E13.left"),sQuery(id+"F15.wireOp",EDGE,"E13.right"),sQuery(id+"F15.wireOp",EDGE,"E14.bottom"),sQuery(id+"F15.wireOp",EDGE,"E14.top"),sQuery(id+"F15.wireOp",EDGE,"E14.left"),sQuery(id+"F15.wireOp",EDGE,"E14.right"),sQuery(id+"F15.wireOp",EDGE,"E15.MirrorCS"),sQuery(id+"F15.wireOp",EDGE,"E16.MirrorCS"),sQuery(id+"F15.wireOp",EDGE,"E17.MirrorCS"),sQuery(id+"F15.wireOp",EDGE,"E18.MirrorCS"),sQuery(id+"F15.wireOp",EDGE,"E19.MirrorCS"),sQuery(id+"F15.wireOp",EDGE,"E20.MirrorCS"),sQuery(id+"F15.wireOp",EDGE,"E21.MirrorCS"),sQuery(id+"F15.wireOp",EDGE,"E22.MirrorCS"),sQuery(id+"F15.wireOp",EDGE,"E23.MirrorCS"),sQuery(id+"F15.wireOp",EDGE,"E24.MirrorCS"),sQuery(id+"F15.wireOp",EDGE,"E25.MirrorCS"),sQuery(id+"F15.wireOp",EDGE,"E26.MirrorCS")])]}),"instanceName":"1"}),"instanceName":"1"}),"instanceName":"1"}),"instanceName":"1"});
            var Q125;
            Q125=makeQuery(id+"F23.opPattern","COPY",BODY,{"derivedFrom":makeQuery(id+"F22.opPattern","COPY",BODY,{"derivedFrom":makeQuery(id+"F20.opPattern","COPY",BODY,{"derivedFrom":makeQuery(id+"F19.opPattern","COPY",BODY,{"derivedFrom":makeQuery(id+"F17.opPattern","COPY",BODY,{"derivedFrom":makeQuery(id+"F16.opExtrude","SWEPT_BODY",BODY,{"disambiguationData":[OSD([sQuery(id+"F15.wireOp",EDGE,"E13.bottom"),sQuery(id+"F15.wireOp",EDGE,"E13.top"),sQuery(id+"F15.wireOp",EDGE,"E13.left"),sQuery(id+"F15.wireOp",EDGE,"E13.right"),sQuery(id+"F15.wireOp",EDGE,"E14.bottom"),sQuery(id+"F15.wireOp",EDGE,"E14.top"),sQuery(id+"F15.wireOp",EDGE,"E14.left"),sQuery(id+"F15.wireOp",EDGE,"E14.right"),sQuery(id+"F15.wireOp",EDGE,"E15.MirrorCS"),sQuery(id+"F15.wireOp",EDGE,"E16.MirrorCS"),sQuery(id+"F15.wireOp",EDGE,"E17.MirrorCS"),sQuery(id+"F15.wireOp",EDGE,"E18.MirrorCS"),sQuery(id+"F15.wireOp",EDGE,"E19.MirrorCS"),sQuery(id+"F15.wireOp",EDGE,"E20.MirrorCS"),sQuery(id+"F15.wireOp",EDGE,"E21.MirrorCS"),sQuery(id+"F15.wireOp",EDGE,"E22.MirrorCS"),sQuery(id+"F15.wireOp",EDGE,"E23.MirrorCS"),sQuery(id+"F15.wireOp",EDGE,"E24.MirrorCS"),sQuery(id+"F15.wireOp",EDGE,"E25.MirrorCS"),sQuery(id+"F15.wireOp",EDGE,"E26.MirrorCS")])]}),"instanceName":"1"}),"instanceName":"1"}),"instanceName":"1"}),"instanceName":"1"}),"instanceName":"1"});
            var Q126;
            Q126=makeQuery(id+"F23.opPattern","COPY",BODY,{"derivedFrom":makeQuery(id+"F22.opPattern","COPY",BODY,{"derivedFrom":makeQuery(id+"F20.opPattern","COPY",BODY,{"derivedFrom":makeQuery(id+"F19.opPattern","COPY",BODY,{"derivedFrom":makeQuery(id+"F18.opPattern","COPY",BODY,{"derivedFrom":makeQuery(id+"F16.opExtrude","SWEPT_BODY",BODY,{"disambiguationData":[OSD([sQuery(id+"F15.wireOp",EDGE,"E13.bottom"),sQuery(id+"F15.wireOp",EDGE,"E13.top"),sQuery(id+"F15.wireOp",EDGE,"E13.left"),sQuery(id+"F15.wireOp",EDGE,"E13.right"),sQuery(id+"F15.wireOp",EDGE,"E14.bottom"),sQuery(id+"F15.wireOp",EDGE,"E14.top"),sQuery(id+"F15.wireOp",EDGE,"E14.left"),sQuery(id+"F15.wireOp",EDGE,"E14.right"),sQuery(id+"F15.wireOp",EDGE,"E15.MirrorCS"),sQuery(id+"F15.wireOp",EDGE,"E16.MirrorCS"),sQuery(id+"F15.wireOp",EDGE,"E17.MirrorCS"),sQuery(id+"F15.wireOp",EDGE,"E18.MirrorCS"),sQuery(id+"F15.wireOp",EDGE,"E19.MirrorCS"),sQuery(id+"F15.wireOp",EDGE,"E20.MirrorCS"),sQuery(id+"F15.wireOp",EDGE,"E21.MirrorCS"),sQuery(id+"F15.wireOp",EDGE,"E22.MirrorCS"),sQuery(id+"F15.wireOp",EDGE,"E23.MirrorCS"),sQuery(id+"F15.wireOp",EDGE,"E24.MirrorCS"),sQuery(id+"F15.wireOp",EDGE,"E25.MirrorCS"),sQuery(id+"F15.wireOp",EDGE,"E26.MirrorCS")])]}),"instanceName":"1"}),"instanceName":"1"}),"instanceName":"1"}),"instanceName":"1"}),"instanceName":"1"});
            var Q127;
            Q127=makeQuery(id+"F23.opPattern","COPY",BODY,{"derivedFrom":makeQuery(id+"F22.opPattern","COPY",BODY,{"derivedFrom":makeQuery(id+"F20.opPattern","COPY",BODY,{"derivedFrom":makeQuery(id+"F19.opPattern","COPY",BODY,{"derivedFrom":makeQuery(id+"F18.opPattern","COPY",BODY,{"derivedFrom":makeQuery(id+"F17.opPattern","COPY",BODY,{"derivedFrom":makeQuery(id+"F16.opExtrude","SWEPT_BODY",BODY,{"disambiguationData":[OSD([sQuery(id+"F15.wireOp",EDGE,"E13.bottom"),sQuery(id+"F15.wireOp",EDGE,"E13.top"),sQuery(id+"F15.wireOp",EDGE,"E13.left"),sQuery(id+"F15.wireOp",EDGE,"E13.right"),sQuery(id+"F15.wireOp",EDGE,"E14.bottom"),sQuery(id+"F15.wireOp",EDGE,"E14.top"),sQuery(id+"F15.wireOp",EDGE,"E14.left"),sQuery(id+"F15.wireOp",EDGE,"E14.right"),sQuery(id+"F15.wireOp",EDGE,"E15.MirrorCS"),sQuery(id+"F15.wireOp",EDGE,"E16.MirrorCS"),sQuery(id+"F15.wireOp",EDGE,"E17.MirrorCS"),sQuery(id+"F15.wireOp",EDGE,"E18.MirrorCS"),sQuery(id+"F15.wireOp",EDGE,"E19.MirrorCS"),sQuery(id+"F15.wireOp",EDGE,"E20.MirrorCS"),sQuery(id+"F15.wireOp",EDGE,"E21.MirrorCS"),sQuery(id+"F15.wireOp",EDGE,"E22.MirrorCS"),sQuery(id+"F15.wireOp",EDGE,"E23.MirrorCS"),sQuery(id+"F15.wireOp",EDGE,"E24.MirrorCS"),sQuery(id+"F15.wireOp",EDGE,"E25.MirrorCS"),sQuery(id+"F15.wireOp",EDGE,"E26.MirrorCS")])]}),"instanceName":"1"}),"instanceName":"1"}),"instanceName":"1"}),"instanceName":"1"}),"instanceName":"1"}),"instanceName":"1"});
            var Q128;
            Q128=makeQuery(id+"F23.opPattern","COPY",BODY,{"derivedFrom":makeQuery(id+"F22.opPattern","COPY",BODY,{"derivedFrom":makeQuery(id+"F21.opPattern","COPY",BODY,{"derivedFrom":makeQuery(id+"F16.opExtrude","SWEPT_BODY",BODY,{"disambiguationData":[OSD([sQuery(id+"F15.wireOp",EDGE,"E13.bottom"),sQuery(id+"F15.wireOp",EDGE,"E13.top"),sQuery(id+"F15.wireOp",EDGE,"E13.left"),sQuery(id+"F15.wireOp",EDGE,"E13.right"),sQuery(id+"F15.wireOp",EDGE,"E14.bottom"),sQuery(id+"F15.wireOp",EDGE,"E14.top"),sQuery(id+"F15.wireOp",EDGE,"E14.left"),sQuery(id+"F15.wireOp",EDGE,"E14.right"),sQuery(id+"F15.wireOp",EDGE,"E15.MirrorCS"),sQuery(id+"F15.wireOp",EDGE,"E16.MirrorCS"),sQuery(id+"F15.wireOp",EDGE,"E17.MirrorCS"),sQuery(id+"F15.wireOp",EDGE,"E18.MirrorCS"),sQuery(id+"F15.wireOp",EDGE,"E19.MirrorCS"),sQuery(id+"F15.wireOp",EDGE,"E20.MirrorCS"),sQuery(id+"F15.wireOp",EDGE,"E21.MirrorCS"),sQuery(id+"F15.wireOp",EDGE,"E22.MirrorCS"),sQuery(id+"F15.wireOp",EDGE,"E23.MirrorCS"),sQuery(id+"F15.wireOp",EDGE,"E24.MirrorCS"),sQuery(id+"F15.wireOp",EDGE,"E25.MirrorCS"),sQuery(id+"F15.wireOp",EDGE,"E26.MirrorCS")])]}),"instanceName":"1"}),"instanceName":"1"}),"instanceName":"1"});
            var Q129;
            Q129=makeQuery(id+"F23.opPattern","COPY",BODY,{"derivedFrom":makeQuery(id+"F22.opPattern","COPY",BODY,{"derivedFrom":makeQuery(id+"F21.opPattern","COPY",BODY,{"derivedFrom":makeQuery(id+"F17.opPattern","COPY",BODY,{"derivedFrom":makeQuery(id+"F16.opExtrude","SWEPT_BODY",BODY,{"disambiguationData":[OSD([sQuery(id+"F15.wireOp",EDGE,"E13.bottom"),sQuery(id+"F15.wireOp",EDGE,"E13.top"),sQuery(id+"F15.wireOp",EDGE,"E13.left"),sQuery(id+"F15.wireOp",EDGE,"E13.right"),sQuery(id+"F15.wireOp",EDGE,"E14.bottom"),sQuery(id+"F15.wireOp",EDGE,"E14.top"),sQuery(id+"F15.wireOp",EDGE,"E14.left"),sQuery(id+"F15.wireOp",EDGE,"E14.right"),sQuery(id+"F15.wireOp",EDGE,"E15.MirrorCS"),sQuery(id+"F15.wireOp",EDGE,"E16.MirrorCS"),sQuery(id+"F15.wireOp",EDGE,"E17.MirrorCS"),sQuery(id+"F15.wireOp",EDGE,"E18.MirrorCS"),sQuery(id+"F15.wireOp",EDGE,"E19.MirrorCS"),sQuery(id+"F15.wireOp",EDGE,"E20.MirrorCS"),sQuery(id+"F15.wireOp",EDGE,"E21.MirrorCS"),sQuery(id+"F15.wireOp",EDGE,"E22.MirrorCS"),sQuery(id+"F15.wireOp",EDGE,"E23.MirrorCS"),sQuery(id+"F15.wireOp",EDGE,"E24.MirrorCS"),sQuery(id+"F15.wireOp",EDGE,"E25.MirrorCS"),sQuery(id+"F15.wireOp",EDGE,"E26.MirrorCS")])]}),"instanceName":"1"}),"instanceName":"1"}),"instanceName":"1"}),"instanceName":"1"});
            var Q130;
            Q130=makeQuery(id+"F23.opPattern","COPY",BODY,{"derivedFrom":makeQuery(id+"F22.opPattern","COPY",BODY,{"derivedFrom":makeQuery(id+"F21.opPattern","COPY",BODY,{"derivedFrom":makeQuery(id+"F18.opPattern","COPY",BODY,{"derivedFrom":makeQuery(id+"F16.opExtrude","SWEPT_BODY",BODY,{"disambiguationData":[OSD([sQuery(id+"F15.wireOp",EDGE,"E13.bottom"),sQuery(id+"F15.wireOp",EDGE,"E13.top"),sQuery(id+"F15.wireOp",EDGE,"E13.left"),sQuery(id+"F15.wireOp",EDGE,"E13.right"),sQuery(id+"F15.wireOp",EDGE,"E14.bottom"),sQuery(id+"F15.wireOp",EDGE,"E14.top"),sQuery(id+"F15.wireOp",EDGE,"E14.left"),sQuery(id+"F15.wireOp",EDGE,"E14.right"),sQuery(id+"F15.wireOp",EDGE,"E15.MirrorCS"),sQuery(id+"F15.wireOp",EDGE,"E16.MirrorCS"),sQuery(id+"F15.wireOp",EDGE,"E17.MirrorCS"),sQuery(id+"F15.wireOp",EDGE,"E18.MirrorCS"),sQuery(id+"F15.wireOp",EDGE,"E19.MirrorCS"),sQuery(id+"F15.wireOp",EDGE,"E20.MirrorCS"),sQuery(id+"F15.wireOp",EDGE,"E21.MirrorCS"),sQuery(id+"F15.wireOp",EDGE,"E22.MirrorCS"),sQuery(id+"F15.wireOp",EDGE,"E23.MirrorCS"),sQuery(id+"F15.wireOp",EDGE,"E24.MirrorCS"),sQuery(id+"F15.wireOp",EDGE,"E25.MirrorCS"),sQuery(id+"F15.wireOp",EDGE,"E26.MirrorCS")])]}),"instanceName":"1"}),"instanceName":"1"}),"instanceName":"1"}),"instanceName":"1"});
            var Q131;
            Q131=makeQuery(id+"F23.opPattern","COPY",BODY,{"derivedFrom":makeQuery(id+"F22.opPattern","COPY",BODY,{"derivedFrom":makeQuery(id+"F21.opPattern","COPY",BODY,{"derivedFrom":makeQuery(id+"F18.opPattern","COPY",BODY,{"derivedFrom":makeQuery(id+"F17.opPattern","COPY",BODY,{"derivedFrom":makeQuery(id+"F16.opExtrude","SWEPT_BODY",BODY,{"disambiguationData":[OSD([sQuery(id+"F15.wireOp",EDGE,"E13.bottom"),sQuery(id+"F15.wireOp",EDGE,"E13.top"),sQuery(id+"F15.wireOp",EDGE,"E13.left"),sQuery(id+"F15.wireOp",EDGE,"E13.right"),sQuery(id+"F15.wireOp",EDGE,"E14.bottom"),sQuery(id+"F15.wireOp",EDGE,"E14.top"),sQuery(id+"F15.wireOp",EDGE,"E14.left"),sQuery(id+"F15.wireOp",EDGE,"E14.right"),sQuery(id+"F15.wireOp",EDGE,"E15.MirrorCS"),sQuery(id+"F15.wireOp",EDGE,"E16.MirrorCS"),sQuery(id+"F15.wireOp",EDGE,"E17.MirrorCS"),sQuery(id+"F15.wireOp",EDGE,"E18.MirrorCS"),sQuery(id+"F15.wireOp",EDGE,"E19.MirrorCS"),sQuery(id+"F15.wireOp",EDGE,"E20.MirrorCS"),sQuery(id+"F15.wireOp",EDGE,"E21.MirrorCS"),sQuery(id+"F15.wireOp",EDGE,"E22.MirrorCS"),sQuery(id+"F15.wireOp",EDGE,"E23.MirrorCS"),sQuery(id+"F15.wireOp",EDGE,"E24.MirrorCS"),sQuery(id+"F15.wireOp",EDGE,"E25.MirrorCS"),sQuery(id+"F15.wireOp",EDGE,"E26.MirrorCS")])]}),"instanceName":"1"}),"instanceName":"1"}),"instanceName":"1"}),"instanceName":"1"}),"instanceName":"1"});
            var Q132;
            Q132=makeQuery(id+"F23.opPattern","COPY",BODY,{"derivedFrom":makeQuery(id+"F22.opPattern","COPY",BODY,{"derivedFrom":makeQuery(id+"F21.opPattern","COPY",BODY,{"derivedFrom":makeQuery(id+"F19.opPattern","COPY",BODY,{"derivedFrom":makeQuery(id+"F16.opExtrude","SWEPT_BODY",BODY,{"disambiguationData":[OSD([sQuery(id+"F15.wireOp",EDGE,"E13.bottom"),sQuery(id+"F15.wireOp",EDGE,"E13.top"),sQuery(id+"F15.wireOp",EDGE,"E13.left"),sQuery(id+"F15.wireOp",EDGE,"E13.right"),sQuery(id+"F15.wireOp",EDGE,"E14.bottom"),sQuery(id+"F15.wireOp",EDGE,"E14.top"),sQuery(id+"F15.wireOp",EDGE,"E14.left"),sQuery(id+"F15.wireOp",EDGE,"E14.right"),sQuery(id+"F15.wireOp",EDGE,"E15.MirrorCS"),sQuery(id+"F15.wireOp",EDGE,"E16.MirrorCS"),sQuery(id+"F15.wireOp",EDGE,"E17.MirrorCS"),sQuery(id+"F15.wireOp",EDGE,"E18.MirrorCS"),sQuery(id+"F15.wireOp",EDGE,"E19.MirrorCS"),sQuery(id+"F15.wireOp",EDGE,"E20.MirrorCS"),sQuery(id+"F15.wireOp",EDGE,"E21.MirrorCS"),sQuery(id+"F15.wireOp",EDGE,"E22.MirrorCS"),sQuery(id+"F15.wireOp",EDGE,"E23.MirrorCS"),sQuery(id+"F15.wireOp",EDGE,"E24.MirrorCS"),sQuery(id+"F15.wireOp",EDGE,"E25.MirrorCS"),sQuery(id+"F15.wireOp",EDGE,"E26.MirrorCS")])]}),"instanceName":"1"}),"instanceName":"1"}),"instanceName":"1"}),"instanceName":"1"});
            var Q133;
            Q133=makeQuery(id+"F23.opPattern","COPY",BODY,{"derivedFrom":makeQuery(id+"F22.opPattern","COPY",BODY,{"derivedFrom":makeQuery(id+"F21.opPattern","COPY",BODY,{"derivedFrom":makeQuery(id+"F19.opPattern","COPY",BODY,{"derivedFrom":makeQuery(id+"F17.opPattern","COPY",BODY,{"derivedFrom":makeQuery(id+"F16.opExtrude","SWEPT_BODY",BODY,{"disambiguationData":[OSD([sQuery(id+"F15.wireOp",EDGE,"E13.bottom"),sQuery(id+"F15.wireOp",EDGE,"E13.top"),sQuery(id+"F15.wireOp",EDGE,"E13.left"),sQuery(id+"F15.wireOp",EDGE,"E13.right"),sQuery(id+"F15.wireOp",EDGE,"E14.bottom"),sQuery(id+"F15.wireOp",EDGE,"E14.top"),sQuery(id+"F15.wireOp",EDGE,"E14.left"),sQuery(id+"F15.wireOp",EDGE,"E14.right"),sQuery(id+"F15.wireOp",EDGE,"E15.MirrorCS"),sQuery(id+"F15.wireOp",EDGE,"E16.MirrorCS"),sQuery(id+"F15.wireOp",EDGE,"E17.MirrorCS"),sQuery(id+"F15.wireOp",EDGE,"E18.MirrorCS"),sQuery(id+"F15.wireOp",EDGE,"E19.MirrorCS"),sQuery(id+"F15.wireOp",EDGE,"E20.MirrorCS"),sQuery(id+"F15.wireOp",EDGE,"E21.MirrorCS"),sQuery(id+"F15.wireOp",EDGE,"E22.MirrorCS"),sQuery(id+"F15.wireOp",EDGE,"E23.MirrorCS"),sQuery(id+"F15.wireOp",EDGE,"E24.MirrorCS"),sQuery(id+"F15.wireOp",EDGE,"E25.MirrorCS"),sQuery(id+"F15.wireOp",EDGE,"E26.MirrorCS")])]}),"instanceName":"1"}),"instanceName":"1"}),"instanceName":"1"}),"instanceName":"1"}),"instanceName":"1"});
            var Q134;
            Q134=makeQuery(id+"F23.opPattern","COPY",BODY,{"derivedFrom":makeQuery(id+"F22.opPattern","COPY",BODY,{"derivedFrom":makeQuery(id+"F21.opPattern","COPY",BODY,{"derivedFrom":makeQuery(id+"F19.opPattern","COPY",BODY,{"derivedFrom":makeQuery(id+"F18.opPattern","COPY",BODY,{"derivedFrom":makeQuery(id+"F16.opExtrude","SWEPT_BODY",BODY,{"disambiguationData":[OSD([sQuery(id+"F15.wireOp",EDGE,"E13.bottom"),sQuery(id+"F15.wireOp",EDGE,"E13.top"),sQuery(id+"F15.wireOp",EDGE,"E13.left"),sQuery(id+"F15.wireOp",EDGE,"E13.right"),sQuery(id+"F15.wireOp",EDGE,"E14.bottom"),sQuery(id+"F15.wireOp",EDGE,"E14.top"),sQuery(id+"F15.wireOp",EDGE,"E14.left"),sQuery(id+"F15.wireOp",EDGE,"E14.right"),sQuery(id+"F15.wireOp",EDGE,"E15.MirrorCS"),sQuery(id+"F15.wireOp",EDGE,"E16.MirrorCS"),sQuery(id+"F15.wireOp",EDGE,"E17.MirrorCS"),sQuery(id+"F15.wireOp",EDGE,"E18.MirrorCS"),sQuery(id+"F15.wireOp",EDGE,"E19.MirrorCS"),sQuery(id+"F15.wireOp",EDGE,"E20.MirrorCS"),sQuery(id+"F15.wireOp",EDGE,"E21.MirrorCS"),sQuery(id+"F15.wireOp",EDGE,"E22.MirrorCS"),sQuery(id+"F15.wireOp",EDGE,"E23.MirrorCS"),sQuery(id+"F15.wireOp",EDGE,"E24.MirrorCS"),sQuery(id+"F15.wireOp",EDGE,"E25.MirrorCS"),sQuery(id+"F15.wireOp",EDGE,"E26.MirrorCS")])]}),"instanceName":"1"}),"instanceName":"1"}),"instanceName":"1"}),"instanceName":"1"}),"instanceName":"1"});
            var Q135;
            Q135=makeQuery(id+"F23.opPattern","COPY",BODY,{"derivedFrom":makeQuery(id+"F22.opPattern","COPY",BODY,{"derivedFrom":makeQuery(id+"F21.opPattern","COPY",BODY,{"derivedFrom":makeQuery(id+"F19.opPattern","COPY",BODY,{"derivedFrom":makeQuery(id+"F18.opPattern","COPY",BODY,{"derivedFrom":makeQuery(id+"F17.opPattern","COPY",BODY,{"derivedFrom":makeQuery(id+"F16.opExtrude","SWEPT_BODY",BODY,{"disambiguationData":[OSD([sQuery(id+"F15.wireOp",EDGE,"E13.bottom"),sQuery(id+"F15.wireOp",EDGE,"E13.top"),sQuery(id+"F15.wireOp",EDGE,"E13.left"),sQuery(id+"F15.wireOp",EDGE,"E13.right"),sQuery(id+"F15.wireOp",EDGE,"E14.bottom"),sQuery(id+"F15.wireOp",EDGE,"E14.top"),sQuery(id+"F15.wireOp",EDGE,"E14.left"),sQuery(id+"F15.wireOp",EDGE,"E14.right"),sQuery(id+"F15.wireOp",EDGE,"E15.MirrorCS"),sQuery(id+"F15.wireOp",EDGE,"E16.MirrorCS"),sQuery(id+"F15.wireOp",EDGE,"E17.MirrorCS"),sQuery(id+"F15.wireOp",EDGE,"E18.MirrorCS"),sQuery(id+"F15.wireOp",EDGE,"E19.MirrorCS"),sQuery(id+"F15.wireOp",EDGE,"E20.MirrorCS"),sQuery(id+"F15.wireOp",EDGE,"E21.MirrorCS"),sQuery(id+"F15.wireOp",EDGE,"E22.MirrorCS"),sQuery(id+"F15.wireOp",EDGE,"E23.MirrorCS"),sQuery(id+"F15.wireOp",EDGE,"E24.MirrorCS"),sQuery(id+"F15.wireOp",EDGE,"E25.MirrorCS"),sQuery(id+"F15.wireOp",EDGE,"E26.MirrorCS")])]}),"instanceName":"1"}),"instanceName":"1"}),"instanceName":"1"}),"instanceName":"1"}),"instanceName":"1"}),"instanceName":"1"});
            var Q136;
            Q136=makeQuery(id+"F24.opPattern","COPY",BODY,{"derivedFrom":makeQuery(id+"F19.opPattern","COPY",BODY,{"derivedFrom":makeQuery(id+"F16.opExtrude","SWEPT_BODY",BODY,{"disambiguationData":[OSD([sQuery(id+"F15.wireOp",EDGE,"E13.bottom"),sQuery(id+"F15.wireOp",EDGE,"E13.top"),sQuery(id+"F15.wireOp",EDGE,"E13.left"),sQuery(id+"F15.wireOp",EDGE,"E13.right"),sQuery(id+"F15.wireOp",EDGE,"E14.bottom"),sQuery(id+"F15.wireOp",EDGE,"E14.top"),sQuery(id+"F15.wireOp",EDGE,"E14.left"),sQuery(id+"F15.wireOp",EDGE,"E14.right"),sQuery(id+"F15.wireOp",EDGE,"E15.MirrorCS"),sQuery(id+"F15.wireOp",EDGE,"E16.MirrorCS"),sQuery(id+"F15.wireOp",EDGE,"E17.MirrorCS"),sQuery(id+"F15.wireOp",EDGE,"E18.MirrorCS"),sQuery(id+"F15.wireOp",EDGE,"E19.MirrorCS"),sQuery(id+"F15.wireOp",EDGE,"E20.MirrorCS"),sQuery(id+"F15.wireOp",EDGE,"E21.MirrorCS"),sQuery(id+"F15.wireOp",EDGE,"E22.MirrorCS"),sQuery(id+"F15.wireOp",EDGE,"E23.MirrorCS"),sQuery(id+"F15.wireOp",EDGE,"E24.MirrorCS"),sQuery(id+"F15.wireOp",EDGE,"E25.MirrorCS"),sQuery(id+"F15.wireOp",EDGE,"E26.MirrorCS")])]}),"instanceName":"1"}),"instanceName":"1"});
            var Q137;
            Q137=makeQuery(id+"F24.opPattern","COPY",BODY,{"derivedFrom":makeQuery(id+"F19.opPattern","COPY",BODY,{"derivedFrom":makeQuery(id+"F17.opPattern","COPY",BODY,{"derivedFrom":makeQuery(id+"F16.opExtrude","SWEPT_BODY",BODY,{"disambiguationData":[OSD([sQuery(id+"F15.wireOp",EDGE,"E13.bottom"),sQuery(id+"F15.wireOp",EDGE,"E13.top"),sQuery(id+"F15.wireOp",EDGE,"E13.left"),sQuery(id+"F15.wireOp",EDGE,"E13.right"),sQuery(id+"F15.wireOp",EDGE,"E14.bottom"),sQuery(id+"F15.wireOp",EDGE,"E14.top"),sQuery(id+"F15.wireOp",EDGE,"E14.left"),sQuery(id+"F15.wireOp",EDGE,"E14.right"),sQuery(id+"F15.wireOp",EDGE,"E15.MirrorCS"),sQuery(id+"F15.wireOp",EDGE,"E16.MirrorCS"),sQuery(id+"F15.wireOp",EDGE,"E17.MirrorCS"),sQuery(id+"F15.wireOp",EDGE,"E18.MirrorCS"),sQuery(id+"F15.wireOp",EDGE,"E19.MirrorCS"),sQuery(id+"F15.wireOp",EDGE,"E20.MirrorCS"),sQuery(id+"F15.wireOp",EDGE,"E21.MirrorCS"),sQuery(id+"F15.wireOp",EDGE,"E22.MirrorCS"),sQuery(id+"F15.wireOp",EDGE,"E23.MirrorCS"),sQuery(id+"F15.wireOp",EDGE,"E24.MirrorCS"),sQuery(id+"F15.wireOp",EDGE,"E25.MirrorCS"),sQuery(id+"F15.wireOp",EDGE,"E26.MirrorCS")])]}),"instanceName":"1"}),"instanceName":"1"}),"instanceName":"1"});
            var Q138;
            Q138=makeQuery(id+"F24.opPattern","COPY",BODY,{"derivedFrom":makeQuery(id+"F19.opPattern","COPY",BODY,{"derivedFrom":makeQuery(id+"F18.opPattern","COPY",BODY,{"derivedFrom":makeQuery(id+"F16.opExtrude","SWEPT_BODY",BODY,{"disambiguationData":[OSD([sQuery(id+"F15.wireOp",EDGE,"E13.bottom"),sQuery(id+"F15.wireOp",EDGE,"E13.top"),sQuery(id+"F15.wireOp",EDGE,"E13.left"),sQuery(id+"F15.wireOp",EDGE,"E13.right"),sQuery(id+"F15.wireOp",EDGE,"E14.bottom"),sQuery(id+"F15.wireOp",EDGE,"E14.top"),sQuery(id+"F15.wireOp",EDGE,"E14.left"),sQuery(id+"F15.wireOp",EDGE,"E14.right"),sQuery(id+"F15.wireOp",EDGE,"E15.MirrorCS"),sQuery(id+"F15.wireOp",EDGE,"E16.MirrorCS"),sQuery(id+"F15.wireOp",EDGE,"E17.MirrorCS"),sQuery(id+"F15.wireOp",EDGE,"E18.MirrorCS"),sQuery(id+"F15.wireOp",EDGE,"E19.MirrorCS"),sQuery(id+"F15.wireOp",EDGE,"E20.MirrorCS"),sQuery(id+"F15.wireOp",EDGE,"E21.MirrorCS"),sQuery(id+"F15.wireOp",EDGE,"E22.MirrorCS"),sQuery(id+"F15.wireOp",EDGE,"E23.MirrorCS"),sQuery(id+"F15.wireOp",EDGE,"E24.MirrorCS"),sQuery(id+"F15.wireOp",EDGE,"E25.MirrorCS"),sQuery(id+"F15.wireOp",EDGE,"E26.MirrorCS")])]}),"instanceName":"1"}),"instanceName":"1"}),"instanceName":"1"});
            var Q139;
            Q139=makeQuery(id+"F24.opPattern","COPY",BODY,{"derivedFrom":makeQuery(id+"F19.opPattern","COPY",BODY,{"derivedFrom":makeQuery(id+"F18.opPattern","COPY",BODY,{"derivedFrom":makeQuery(id+"F17.opPattern","COPY",BODY,{"derivedFrom":makeQuery(id+"F16.opExtrude","SWEPT_BODY",BODY,{"disambiguationData":[OSD([sQuery(id+"F15.wireOp",EDGE,"E13.bottom"),sQuery(id+"F15.wireOp",EDGE,"E13.top"),sQuery(id+"F15.wireOp",EDGE,"E13.left"),sQuery(id+"F15.wireOp",EDGE,"E13.right"),sQuery(id+"F15.wireOp",EDGE,"E14.bottom"),sQuery(id+"F15.wireOp",EDGE,"E14.top"),sQuery(id+"F15.wireOp",EDGE,"E14.left"),sQuery(id+"F15.wireOp",EDGE,"E14.right"),sQuery(id+"F15.wireOp",EDGE,"E15.MirrorCS"),sQuery(id+"F15.wireOp",EDGE,"E16.MirrorCS"),sQuery(id+"F15.wireOp",EDGE,"E17.MirrorCS"),sQuery(id+"F15.wireOp",EDGE,"E18.MirrorCS"),sQuery(id+"F15.wireOp",EDGE,"E19.MirrorCS"),sQuery(id+"F15.wireOp",EDGE,"E20.MirrorCS"),sQuery(id+"F15.wireOp",EDGE,"E21.MirrorCS"),sQuery(id+"F15.wireOp",EDGE,"E22.MirrorCS"),sQuery(id+"F15.wireOp",EDGE,"E23.MirrorCS"),sQuery(id+"F15.wireOp",EDGE,"E24.MirrorCS"),sQuery(id+"F15.wireOp",EDGE,"E25.MirrorCS"),sQuery(id+"F15.wireOp",EDGE,"E26.MirrorCS")])]}),"instanceName":"1"}),"instanceName":"1"}),"instanceName":"1"}),"instanceName":"1"});
            var Q140;
            Q140=makeQuery(id+"F24.opPattern","COPY",BODY,{"derivedFrom":makeQuery(id+"F20.opPattern","COPY",BODY,{"derivedFrom":makeQuery(id+"F16.opExtrude","SWEPT_BODY",BODY,{"disambiguationData":[OSD([sQuery(id+"F15.wireOp",EDGE,"E13.bottom"),sQuery(id+"F15.wireOp",EDGE,"E13.top"),sQuery(id+"F15.wireOp",EDGE,"E13.left"),sQuery(id+"F15.wireOp",EDGE,"E13.right"),sQuery(id+"F15.wireOp",EDGE,"E14.bottom"),sQuery(id+"F15.wireOp",EDGE,"E14.top"),sQuery(id+"F15.wireOp",EDGE,"E14.left"),sQuery(id+"F15.wireOp",EDGE,"E14.right"),sQuery(id+"F15.wireOp",EDGE,"E15.MirrorCS"),sQuery(id+"F15.wireOp",EDGE,"E16.MirrorCS"),sQuery(id+"F15.wireOp",EDGE,"E17.MirrorCS"),sQuery(id+"F15.wireOp",EDGE,"E18.MirrorCS"),sQuery(id+"F15.wireOp",EDGE,"E19.MirrorCS"),sQuery(id+"F15.wireOp",EDGE,"E20.MirrorCS"),sQuery(id+"F15.wireOp",EDGE,"E21.MirrorCS"),sQuery(id+"F15.wireOp",EDGE,"E22.MirrorCS"),sQuery(id+"F15.wireOp",EDGE,"E23.MirrorCS"),sQuery(id+"F15.wireOp",EDGE,"E24.MirrorCS"),sQuery(id+"F15.wireOp",EDGE,"E25.MirrorCS"),sQuery(id+"F15.wireOp",EDGE,"E26.MirrorCS")])]}),"instanceName":"1"}),"instanceName":"1"});
            var Q141;
            Q141=makeQuery(id+"F24.opPattern","COPY",BODY,{"derivedFrom":makeQuery(id+"F20.opPattern","COPY",BODY,{"derivedFrom":makeQuery(id+"F17.opPattern","COPY",BODY,{"derivedFrom":makeQuery(id+"F16.opExtrude","SWEPT_BODY",BODY,{"disambiguationData":[OSD([sQuery(id+"F15.wireOp",EDGE,"E13.bottom"),sQuery(id+"F15.wireOp",EDGE,"E13.top"),sQuery(id+"F15.wireOp",EDGE,"E13.left"),sQuery(id+"F15.wireOp",EDGE,"E13.right"),sQuery(id+"F15.wireOp",EDGE,"E14.bottom"),sQuery(id+"F15.wireOp",EDGE,"E14.top"),sQuery(id+"F15.wireOp",EDGE,"E14.left"),sQuery(id+"F15.wireOp",EDGE,"E14.right"),sQuery(id+"F15.wireOp",EDGE,"E15.MirrorCS"),sQuery(id+"F15.wireOp",EDGE,"E16.MirrorCS"),sQuery(id+"F15.wireOp",EDGE,"E17.MirrorCS"),sQuery(id+"F15.wireOp",EDGE,"E18.MirrorCS"),sQuery(id+"F15.wireOp",EDGE,"E19.MirrorCS"),sQuery(id+"F15.wireOp",EDGE,"E20.MirrorCS"),sQuery(id+"F15.wireOp",EDGE,"E21.MirrorCS"),sQuery(id+"F15.wireOp",EDGE,"E22.MirrorCS"),sQuery(id+"F15.wireOp",EDGE,"E23.MirrorCS"),sQuery(id+"F15.wireOp",EDGE,"E24.MirrorCS"),sQuery(id+"F15.wireOp",EDGE,"E25.MirrorCS"),sQuery(id+"F15.wireOp",EDGE,"E26.MirrorCS")])]}),"instanceName":"1"}),"instanceName":"1"}),"instanceName":"1"});
            var Q142;
            Q142=makeQuery(id+"F24.opPattern","COPY",BODY,{"derivedFrom":makeQuery(id+"F20.opPattern","COPY",BODY,{"derivedFrom":makeQuery(id+"F18.opPattern","COPY",BODY,{"derivedFrom":makeQuery(id+"F16.opExtrude","SWEPT_BODY",BODY,{"disambiguationData":[OSD([sQuery(id+"F15.wireOp",EDGE,"E13.bottom"),sQuery(id+"F15.wireOp",EDGE,"E13.top"),sQuery(id+"F15.wireOp",EDGE,"E13.left"),sQuery(id+"F15.wireOp",EDGE,"E13.right"),sQuery(id+"F15.wireOp",EDGE,"E14.bottom"),sQuery(id+"F15.wireOp",EDGE,"E14.top"),sQuery(id+"F15.wireOp",EDGE,"E14.left"),sQuery(id+"F15.wireOp",EDGE,"E14.right"),sQuery(id+"F15.wireOp",EDGE,"E15.MirrorCS"),sQuery(id+"F15.wireOp",EDGE,"E16.MirrorCS"),sQuery(id+"F15.wireOp",EDGE,"E17.MirrorCS"),sQuery(id+"F15.wireOp",EDGE,"E18.MirrorCS"),sQuery(id+"F15.wireOp",EDGE,"E19.MirrorCS"),sQuery(id+"F15.wireOp",EDGE,"E20.MirrorCS"),sQuery(id+"F15.wireOp",EDGE,"E21.MirrorCS"),sQuery(id+"F15.wireOp",EDGE,"E22.MirrorCS"),sQuery(id+"F15.wireOp",EDGE,"E23.MirrorCS"),sQuery(id+"F15.wireOp",EDGE,"E24.MirrorCS"),sQuery(id+"F15.wireOp",EDGE,"E25.MirrorCS"),sQuery(id+"F15.wireOp",EDGE,"E26.MirrorCS")])]}),"instanceName":"1"}),"instanceName":"1"}),"instanceName":"1"});
            var Q143;
            Q143=makeQuery(id+"F24.opPattern","COPY",BODY,{"derivedFrom":makeQuery(id+"F20.opPattern","COPY",BODY,{"derivedFrom":makeQuery(id+"F18.opPattern","COPY",BODY,{"derivedFrom":makeQuery(id+"F17.opPattern","COPY",BODY,{"derivedFrom":makeQuery(id+"F16.opExtrude","SWEPT_BODY",BODY,{"disambiguationData":[OSD([sQuery(id+"F15.wireOp",EDGE,"E13.bottom"),sQuery(id+"F15.wireOp",EDGE,"E13.top"),sQuery(id+"F15.wireOp",EDGE,"E13.left"),sQuery(id+"F15.wireOp",EDGE,"E13.right"),sQuery(id+"F15.wireOp",EDGE,"E14.bottom"),sQuery(id+"F15.wireOp",EDGE,"E14.top"),sQuery(id+"F15.wireOp",EDGE,"E14.left"),sQuery(id+"F15.wireOp",EDGE,"E14.right"),sQuery(id+"F15.wireOp",EDGE,"E15.MirrorCS"),sQuery(id+"F15.wireOp",EDGE,"E16.MirrorCS"),sQuery(id+"F15.wireOp",EDGE,"E17.MirrorCS"),sQuery(id+"F15.wireOp",EDGE,"E18.MirrorCS"),sQuery(id+"F15.wireOp",EDGE,"E19.MirrorCS"),sQuery(id+"F15.wireOp",EDGE,"E20.MirrorCS"),sQuery(id+"F15.wireOp",EDGE,"E21.MirrorCS"),sQuery(id+"F15.wireOp",EDGE,"E22.MirrorCS"),sQuery(id+"F15.wireOp",EDGE,"E23.MirrorCS"),sQuery(id+"F15.wireOp",EDGE,"E24.MirrorCS"),sQuery(id+"F15.wireOp",EDGE,"E25.MirrorCS"),sQuery(id+"F15.wireOp",EDGE,"E26.MirrorCS")])]}),"instanceName":"1"}),"instanceName":"1"}),"instanceName":"1"}),"instanceName":"1"});
            var Q144;
            Q144=makeQuery(id+"F24.opPattern","COPY",BODY,{"derivedFrom":makeQuery(id+"F20.opPattern","COPY",BODY,{"derivedFrom":makeQuery(id+"F19.opPattern","COPY",BODY,{"derivedFrom":makeQuery(id+"F16.opExtrude","SWEPT_BODY",BODY,{"disambiguationData":[OSD([sQuery(id+"F15.wireOp",EDGE,"E13.bottom"),sQuery(id+"F15.wireOp",EDGE,"E13.top"),sQuery(id+"F15.wireOp",EDGE,"E13.left"),sQuery(id+"F15.wireOp",EDGE,"E13.right"),sQuery(id+"F15.wireOp",EDGE,"E14.bottom"),sQuery(id+"F15.wireOp",EDGE,"E14.top"),sQuery(id+"F15.wireOp",EDGE,"E14.left"),sQuery(id+"F15.wireOp",EDGE,"E14.right"),sQuery(id+"F15.wireOp",EDGE,"E15.MirrorCS"),sQuery(id+"F15.wireOp",EDGE,"E16.MirrorCS"),sQuery(id+"F15.wireOp",EDGE,"E17.MirrorCS"),sQuery(id+"F15.wireOp",EDGE,"E18.MirrorCS"),sQuery(id+"F15.wireOp",EDGE,"E19.MirrorCS"),sQuery(id+"F15.wireOp",EDGE,"E20.MirrorCS"),sQuery(id+"F15.wireOp",EDGE,"E21.MirrorCS"),sQuery(id+"F15.wireOp",EDGE,"E22.MirrorCS"),sQuery(id+"F15.wireOp",EDGE,"E23.MirrorCS"),sQuery(id+"F15.wireOp",EDGE,"E24.MirrorCS"),sQuery(id+"F15.wireOp",EDGE,"E25.MirrorCS"),sQuery(id+"F15.wireOp",EDGE,"E26.MirrorCS")])]}),"instanceName":"1"}),"instanceName":"1"}),"instanceName":"1"});
            var Q145;
            Q145=makeQuery(id+"F24.opPattern","COPY",BODY,{"derivedFrom":makeQuery(id+"F20.opPattern","COPY",BODY,{"derivedFrom":makeQuery(id+"F19.opPattern","COPY",BODY,{"derivedFrom":makeQuery(id+"F17.opPattern","COPY",BODY,{"derivedFrom":makeQuery(id+"F16.opExtrude","SWEPT_BODY",BODY,{"disambiguationData":[OSD([sQuery(id+"F15.wireOp",EDGE,"E13.bottom"),sQuery(id+"F15.wireOp",EDGE,"E13.top"),sQuery(id+"F15.wireOp",EDGE,"E13.left"),sQuery(id+"F15.wireOp",EDGE,"E13.right"),sQuery(id+"F15.wireOp",EDGE,"E14.bottom"),sQuery(id+"F15.wireOp",EDGE,"E14.top"),sQuery(id+"F15.wireOp",EDGE,"E14.left"),sQuery(id+"F15.wireOp",EDGE,"E14.right"),sQuery(id+"F15.wireOp",EDGE,"E15.MirrorCS"),sQuery(id+"F15.wireOp",EDGE,"E16.MirrorCS"),sQuery(id+"F15.wireOp",EDGE,"E17.MirrorCS"),sQuery(id+"F15.wireOp",EDGE,"E18.MirrorCS"),sQuery(id+"F15.wireOp",EDGE,"E19.MirrorCS"),sQuery(id+"F15.wireOp",EDGE,"E20.MirrorCS"),sQuery(id+"F15.wireOp",EDGE,"E21.MirrorCS"),sQuery(id+"F15.wireOp",EDGE,"E22.MirrorCS"),sQuery(id+"F15.wireOp",EDGE,"E23.MirrorCS"),sQuery(id+"F15.wireOp",EDGE,"E24.MirrorCS"),sQuery(id+"F15.wireOp",EDGE,"E25.MirrorCS"),sQuery(id+"F15.wireOp",EDGE,"E26.MirrorCS")])]}),"instanceName":"1"}),"instanceName":"1"}),"instanceName":"1"}),"instanceName":"1"});
            var Q146;
            Q146=makeQuery(id+"F24.opPattern","COPY",BODY,{"derivedFrom":makeQuery(id+"F20.opPattern","COPY",BODY,{"derivedFrom":makeQuery(id+"F19.opPattern","COPY",BODY,{"derivedFrom":makeQuery(id+"F18.opPattern","COPY",BODY,{"derivedFrom":makeQuery(id+"F16.opExtrude","SWEPT_BODY",BODY,{"disambiguationData":[OSD([sQuery(id+"F15.wireOp",EDGE,"E13.bottom"),sQuery(id+"F15.wireOp",EDGE,"E13.top"),sQuery(id+"F15.wireOp",EDGE,"E13.left"),sQuery(id+"F15.wireOp",EDGE,"E13.right"),sQuery(id+"F15.wireOp",EDGE,"E14.bottom"),sQuery(id+"F15.wireOp",EDGE,"E14.top"),sQuery(id+"F15.wireOp",EDGE,"E14.left"),sQuery(id+"F15.wireOp",EDGE,"E14.right"),sQuery(id+"F15.wireOp",EDGE,"E15.MirrorCS"),sQuery(id+"F15.wireOp",EDGE,"E16.MirrorCS"),sQuery(id+"F15.wireOp",EDGE,"E17.MirrorCS"),sQuery(id+"F15.wireOp",EDGE,"E18.MirrorCS"),sQuery(id+"F15.wireOp",EDGE,"E19.MirrorCS"),sQuery(id+"F15.wireOp",EDGE,"E20.MirrorCS"),sQuery(id+"F15.wireOp",EDGE,"E21.MirrorCS"),sQuery(id+"F15.wireOp",EDGE,"E22.MirrorCS"),sQuery(id+"F15.wireOp",EDGE,"E23.MirrorCS"),sQuery(id+"F15.wireOp",EDGE,"E24.MirrorCS"),sQuery(id+"F15.wireOp",EDGE,"E25.MirrorCS"),sQuery(id+"F15.wireOp",EDGE,"E26.MirrorCS")])]}),"instanceName":"1"}),"instanceName":"1"}),"instanceName":"1"}),"instanceName":"1"});
            var Q147;
            Q147=makeQuery(id+"F24.opPattern","COPY",BODY,{"derivedFrom":makeQuery(id+"F20.opPattern","COPY",BODY,{"derivedFrom":makeQuery(id+"F19.opPattern","COPY",BODY,{"derivedFrom":makeQuery(id+"F18.opPattern","COPY",BODY,{"derivedFrom":makeQuery(id+"F17.opPattern","COPY",BODY,{"derivedFrom":makeQuery(id+"F16.opExtrude","SWEPT_BODY",BODY,{"disambiguationData":[OSD([sQuery(id+"F15.wireOp",EDGE,"E13.bottom"),sQuery(id+"F15.wireOp",EDGE,"E13.top"),sQuery(id+"F15.wireOp",EDGE,"E13.left"),sQuery(id+"F15.wireOp",EDGE,"E13.right"),sQuery(id+"F15.wireOp",EDGE,"E14.bottom"),sQuery(id+"F15.wireOp",EDGE,"E14.top"),sQuery(id+"F15.wireOp",EDGE,"E14.left"),sQuery(id+"F15.wireOp",EDGE,"E14.right"),sQuery(id+"F15.wireOp",EDGE,"E15.MirrorCS"),sQuery(id+"F15.wireOp",EDGE,"E16.MirrorCS"),sQuery(id+"F15.wireOp",EDGE,"E17.MirrorCS"),sQuery(id+"F15.wireOp",EDGE,"E18.MirrorCS"),sQuery(id+"F15.wireOp",EDGE,"E19.MirrorCS"),sQuery(id+"F15.wireOp",EDGE,"E20.MirrorCS"),sQuery(id+"F15.wireOp",EDGE,"E21.MirrorCS"),sQuery(id+"F15.wireOp",EDGE,"E22.MirrorCS"),sQuery(id+"F15.wireOp",EDGE,"E23.MirrorCS"),sQuery(id+"F15.wireOp",EDGE,"E24.MirrorCS"),sQuery(id+"F15.wireOp",EDGE,"E25.MirrorCS"),sQuery(id+"F15.wireOp",EDGE,"E26.MirrorCS")])]}),"instanceName":"1"}),"instanceName":"1"}),"instanceName":"1"}),"instanceName":"1"}),"instanceName":"1"});
            var Q148;
            Q148=makeQuery(id+"F24.opPattern","COPY",BODY,{"derivedFrom":makeQuery(id+"F21.opPattern","COPY",BODY,{"derivedFrom":makeQuery(id+"F16.opExtrude","SWEPT_BODY",BODY,{"disambiguationData":[OSD([sQuery(id+"F15.wireOp",EDGE,"E13.bottom"),sQuery(id+"F15.wireOp",EDGE,"E13.top"),sQuery(id+"F15.wireOp",EDGE,"E13.left"),sQuery(id+"F15.wireOp",EDGE,"E13.right"),sQuery(id+"F15.wireOp",EDGE,"E14.bottom"),sQuery(id+"F15.wireOp",EDGE,"E14.top"),sQuery(id+"F15.wireOp",EDGE,"E14.left"),sQuery(id+"F15.wireOp",EDGE,"E14.right"),sQuery(id+"F15.wireOp",EDGE,"E15.MirrorCS"),sQuery(id+"F15.wireOp",EDGE,"E16.MirrorCS"),sQuery(id+"F15.wireOp",EDGE,"E17.MirrorCS"),sQuery(id+"F15.wireOp",EDGE,"E18.MirrorCS"),sQuery(id+"F15.wireOp",EDGE,"E19.MirrorCS"),sQuery(id+"F15.wireOp",EDGE,"E20.MirrorCS"),sQuery(id+"F15.wireOp",EDGE,"E21.MirrorCS"),sQuery(id+"F15.wireOp",EDGE,"E22.MirrorCS"),sQuery(id+"F15.wireOp",EDGE,"E23.MirrorCS"),sQuery(id+"F15.wireOp",EDGE,"E24.MirrorCS"),sQuery(id+"F15.wireOp",EDGE,"E25.MirrorCS"),sQuery(id+"F15.wireOp",EDGE,"E26.MirrorCS")])]}),"instanceName":"1"}),"instanceName":"1"});
            var Q149;
            Q149=makeQuery(id+"F24.opPattern","COPY",BODY,{"derivedFrom":makeQuery(id+"F21.opPattern","COPY",BODY,{"derivedFrom":makeQuery(id+"F17.opPattern","COPY",BODY,{"derivedFrom":makeQuery(id+"F16.opExtrude","SWEPT_BODY",BODY,{"disambiguationData":[OSD([sQuery(id+"F15.wireOp",EDGE,"E13.bottom"),sQuery(id+"F15.wireOp",EDGE,"E13.top"),sQuery(id+"F15.wireOp",EDGE,"E13.left"),sQuery(id+"F15.wireOp",EDGE,"E13.right"),sQuery(id+"F15.wireOp",EDGE,"E14.bottom"),sQuery(id+"F15.wireOp",EDGE,"E14.top"),sQuery(id+"F15.wireOp",EDGE,"E14.left"),sQuery(id+"F15.wireOp",EDGE,"E14.right"),sQuery(id+"F15.wireOp",EDGE,"E15.MirrorCS"),sQuery(id+"F15.wireOp",EDGE,"E16.MirrorCS"),sQuery(id+"F15.wireOp",EDGE,"E17.MirrorCS"),sQuery(id+"F15.wireOp",EDGE,"E18.MirrorCS"),sQuery(id+"F15.wireOp",EDGE,"E19.MirrorCS"),sQuery(id+"F15.wireOp",EDGE,"E20.MirrorCS"),sQuery(id+"F15.wireOp",EDGE,"E21.MirrorCS"),sQuery(id+"F15.wireOp",EDGE,"E22.MirrorCS"),sQuery(id+"F15.wireOp",EDGE,"E23.MirrorCS"),sQuery(id+"F15.wireOp",EDGE,"E24.MirrorCS"),sQuery(id+"F15.wireOp",EDGE,"E25.MirrorCS"),sQuery(id+"F15.wireOp",EDGE,"E26.MirrorCS")])]}),"instanceName":"1"}),"instanceName":"1"}),"instanceName":"1"});
            var Q150;
            Q150=makeQuery(id+"F24.opPattern","COPY",BODY,{"derivedFrom":makeQuery(id+"F21.opPattern","COPY",BODY,{"derivedFrom":makeQuery(id+"F18.opPattern","COPY",BODY,{"derivedFrom":makeQuery(id+"F16.opExtrude","SWEPT_BODY",BODY,{"disambiguationData":[OSD([sQuery(id+"F15.wireOp",EDGE,"E13.bottom"),sQuery(id+"F15.wireOp",EDGE,"E13.top"),sQuery(id+"F15.wireOp",EDGE,"E13.left"),sQuery(id+"F15.wireOp",EDGE,"E13.right"),sQuery(id+"F15.wireOp",EDGE,"E14.bottom"),sQuery(id+"F15.wireOp",EDGE,"E14.top"),sQuery(id+"F15.wireOp",EDGE,"E14.left"),sQuery(id+"F15.wireOp",EDGE,"E14.right"),sQuery(id+"F15.wireOp",EDGE,"E15.MirrorCS"),sQuery(id+"F15.wireOp",EDGE,"E16.MirrorCS"),sQuery(id+"F15.wireOp",EDGE,"E17.MirrorCS"),sQuery(id+"F15.wireOp",EDGE,"E18.MirrorCS"),sQuery(id+"F15.wireOp",EDGE,"E19.MirrorCS"),sQuery(id+"F15.wireOp",EDGE,"E20.MirrorCS"),sQuery(id+"F15.wireOp",EDGE,"E21.MirrorCS"),sQuery(id+"F15.wireOp",EDGE,"E22.MirrorCS"),sQuery(id+"F15.wireOp",EDGE,"E23.MirrorCS"),sQuery(id+"F15.wireOp",EDGE,"E24.MirrorCS"),sQuery(id+"F15.wireOp",EDGE,"E25.MirrorCS"),sQuery(id+"F15.wireOp",EDGE,"E26.MirrorCS")])]}),"instanceName":"1"}),"instanceName":"1"}),"instanceName":"1"});
            var Q151;
            Q151=makeQuery(id+"F24.opPattern","COPY",BODY,{"derivedFrom":makeQuery(id+"F21.opPattern","COPY",BODY,{"derivedFrom":makeQuery(id+"F18.opPattern","COPY",BODY,{"derivedFrom":makeQuery(id+"F17.opPattern","COPY",BODY,{"derivedFrom":makeQuery(id+"F16.opExtrude","SWEPT_BODY",BODY,{"disambiguationData":[OSD([sQuery(id+"F15.wireOp",EDGE,"E13.bottom"),sQuery(id+"F15.wireOp",EDGE,"E13.top"),sQuery(id+"F15.wireOp",EDGE,"E13.left"),sQuery(id+"F15.wireOp",EDGE,"E13.right"),sQuery(id+"F15.wireOp",EDGE,"E14.bottom"),sQuery(id+"F15.wireOp",EDGE,"E14.top"),sQuery(id+"F15.wireOp",EDGE,"E14.left"),sQuery(id+"F15.wireOp",EDGE,"E14.right"),sQuery(id+"F15.wireOp",EDGE,"E15.MirrorCS"),sQuery(id+"F15.wireOp",EDGE,"E16.MirrorCS"),sQuery(id+"F15.wireOp",EDGE,"E17.MirrorCS"),sQuery(id+"F15.wireOp",EDGE,"E18.MirrorCS"),sQuery(id+"F15.wireOp",EDGE,"E19.MirrorCS"),sQuery(id+"F15.wireOp",EDGE,"E20.MirrorCS"),sQuery(id+"F15.wireOp",EDGE,"E21.MirrorCS"),sQuery(id+"F15.wireOp",EDGE,"E22.MirrorCS"),sQuery(id+"F15.wireOp",EDGE,"E23.MirrorCS"),sQuery(id+"F15.wireOp",EDGE,"E24.MirrorCS"),sQuery(id+"F15.wireOp",EDGE,"E25.MirrorCS"),sQuery(id+"F15.wireOp",EDGE,"E26.MirrorCS")])]}),"instanceName":"1"}),"instanceName":"1"}),"instanceName":"1"}),"instanceName":"1"});
            var Q152;
            Q152=makeQuery(id+"F24.opPattern","COPY",BODY,{"derivedFrom":makeQuery(id+"F21.opPattern","COPY",BODY,{"derivedFrom":makeQuery(id+"F19.opPattern","COPY",BODY,{"derivedFrom":makeQuery(id+"F16.opExtrude","SWEPT_BODY",BODY,{"disambiguationData":[OSD([sQuery(id+"F15.wireOp",EDGE,"E13.bottom"),sQuery(id+"F15.wireOp",EDGE,"E13.top"),sQuery(id+"F15.wireOp",EDGE,"E13.left"),sQuery(id+"F15.wireOp",EDGE,"E13.right"),sQuery(id+"F15.wireOp",EDGE,"E14.bottom"),sQuery(id+"F15.wireOp",EDGE,"E14.top"),sQuery(id+"F15.wireOp",EDGE,"E14.left"),sQuery(id+"F15.wireOp",EDGE,"E14.right"),sQuery(id+"F15.wireOp",EDGE,"E15.MirrorCS"),sQuery(id+"F15.wireOp",EDGE,"E16.MirrorCS"),sQuery(id+"F15.wireOp",EDGE,"E17.MirrorCS"),sQuery(id+"F15.wireOp",EDGE,"E18.MirrorCS"),sQuery(id+"F15.wireOp",EDGE,"E19.MirrorCS"),sQuery(id+"F15.wireOp",EDGE,"E20.MirrorCS"),sQuery(id+"F15.wireOp",EDGE,"E21.MirrorCS"),sQuery(id+"F15.wireOp",EDGE,"E22.MirrorCS"),sQuery(id+"F15.wireOp",EDGE,"E23.MirrorCS"),sQuery(id+"F15.wireOp",EDGE,"E24.MirrorCS"),sQuery(id+"F15.wireOp",EDGE,"E25.MirrorCS"),sQuery(id+"F15.wireOp",EDGE,"E26.MirrorCS")])]}),"instanceName":"1"}),"instanceName":"1"}),"instanceName":"1"});
            var Q153;
            Q153=makeQuery(id+"F24.opPattern","COPY",BODY,{"derivedFrom":makeQuery(id+"F21.opPattern","COPY",BODY,{"derivedFrom":makeQuery(id+"F19.opPattern","COPY",BODY,{"derivedFrom":makeQuery(id+"F17.opPattern","COPY",BODY,{"derivedFrom":makeQuery(id+"F16.opExtrude","SWEPT_BODY",BODY,{"disambiguationData":[OSD([sQuery(id+"F15.wireOp",EDGE,"E13.bottom"),sQuery(id+"F15.wireOp",EDGE,"E13.top"),sQuery(id+"F15.wireOp",EDGE,"E13.left"),sQuery(id+"F15.wireOp",EDGE,"E13.right"),sQuery(id+"F15.wireOp",EDGE,"E14.bottom"),sQuery(id+"F15.wireOp",EDGE,"E14.top"),sQuery(id+"F15.wireOp",EDGE,"E14.left"),sQuery(id+"F15.wireOp",EDGE,"E14.right"),sQuery(id+"F15.wireOp",EDGE,"E15.MirrorCS"),sQuery(id+"F15.wireOp",EDGE,"E16.MirrorCS"),sQuery(id+"F15.wireOp",EDGE,"E17.MirrorCS"),sQuery(id+"F15.wireOp",EDGE,"E18.MirrorCS"),sQuery(id+"F15.wireOp",EDGE,"E19.MirrorCS"),sQuery(id+"F15.wireOp",EDGE,"E20.MirrorCS"),sQuery(id+"F15.wireOp",EDGE,"E21.MirrorCS"),sQuery(id+"F15.wireOp",EDGE,"E22.MirrorCS"),sQuery(id+"F15.wireOp",EDGE,"E23.MirrorCS"),sQuery(id+"F15.wireOp",EDGE,"E24.MirrorCS"),sQuery(id+"F15.wireOp",EDGE,"E25.MirrorCS"),sQuery(id+"F15.wireOp",EDGE,"E26.MirrorCS")])]}),"instanceName":"1"}),"instanceName":"1"}),"instanceName":"1"}),"instanceName":"1"});
            var Q154;
            Q154=makeQuery(id+"F24.opPattern","COPY",BODY,{"derivedFrom":makeQuery(id+"F21.opPattern","COPY",BODY,{"derivedFrom":makeQuery(id+"F19.opPattern","COPY",BODY,{"derivedFrom":makeQuery(id+"F18.opPattern","COPY",BODY,{"derivedFrom":makeQuery(id+"F16.opExtrude","SWEPT_BODY",BODY,{"disambiguationData":[OSD([sQuery(id+"F15.wireOp",EDGE,"E13.bottom"),sQuery(id+"F15.wireOp",EDGE,"E13.top"),sQuery(id+"F15.wireOp",EDGE,"E13.left"),sQuery(id+"F15.wireOp",EDGE,"E13.right"),sQuery(id+"F15.wireOp",EDGE,"E14.bottom"),sQuery(id+"F15.wireOp",EDGE,"E14.top"),sQuery(id+"F15.wireOp",EDGE,"E14.left"),sQuery(id+"F15.wireOp",EDGE,"E14.right"),sQuery(id+"F15.wireOp",EDGE,"E15.MirrorCS"),sQuery(id+"F15.wireOp",EDGE,"E16.MirrorCS"),sQuery(id+"F15.wireOp",EDGE,"E17.MirrorCS"),sQuery(id+"F15.wireOp",EDGE,"E18.MirrorCS"),sQuery(id+"F15.wireOp",EDGE,"E19.MirrorCS"),sQuery(id+"F15.wireOp",EDGE,"E20.MirrorCS"),sQuery(id+"F15.wireOp",EDGE,"E21.MirrorCS"),sQuery(id+"F15.wireOp",EDGE,"E22.MirrorCS"),sQuery(id+"F15.wireOp",EDGE,"E23.MirrorCS"),sQuery(id+"F15.wireOp",EDGE,"E24.MirrorCS"),sQuery(id+"F15.wireOp",EDGE,"E25.MirrorCS"),sQuery(id+"F15.wireOp",EDGE,"E26.MirrorCS")])]}),"instanceName":"1"}),"instanceName":"1"}),"instanceName":"1"}),"instanceName":"1"});
            var Q155;
            Q155=makeQuery(id+"F24.opPattern","COPY",BODY,{"derivedFrom":makeQuery(id+"F21.opPattern","COPY",BODY,{"derivedFrom":makeQuery(id+"F19.opPattern","COPY",BODY,{"derivedFrom":makeQuery(id+"F18.opPattern","COPY",BODY,{"derivedFrom":makeQuery(id+"F17.opPattern","COPY",BODY,{"derivedFrom":makeQuery(id+"F16.opExtrude","SWEPT_BODY",BODY,{"disambiguationData":[OSD([sQuery(id+"F15.wireOp",EDGE,"E13.bottom"),sQuery(id+"F15.wireOp",EDGE,"E13.top"),sQuery(id+"F15.wireOp",EDGE,"E13.left"),sQuery(id+"F15.wireOp",EDGE,"E13.right"),sQuery(id+"F15.wireOp",EDGE,"E14.bottom"),sQuery(id+"F15.wireOp",EDGE,"E14.top"),sQuery(id+"F15.wireOp",EDGE,"E14.left"),sQuery(id+"F15.wireOp",EDGE,"E14.right"),sQuery(id+"F15.wireOp",EDGE,"E15.MirrorCS"),sQuery(id+"F15.wireOp",EDGE,"E16.MirrorCS"),sQuery(id+"F15.wireOp",EDGE,"E17.MirrorCS"),sQuery(id+"F15.wireOp",EDGE,"E18.MirrorCS"),sQuery(id+"F15.wireOp",EDGE,"E19.MirrorCS"),sQuery(id+"F15.wireOp",EDGE,"E20.MirrorCS"),sQuery(id+"F15.wireOp",EDGE,"E21.MirrorCS"),sQuery(id+"F15.wireOp",EDGE,"E22.MirrorCS"),sQuery(id+"F15.wireOp",EDGE,"E23.MirrorCS"),sQuery(id+"F15.wireOp",EDGE,"E24.MirrorCS"),sQuery(id+"F15.wireOp",EDGE,"E25.MirrorCS"),sQuery(id+"F15.wireOp",EDGE,"E26.MirrorCS")])]}),"instanceName":"1"}),"instanceName":"1"}),"instanceName":"1"}),"instanceName":"1"}),"instanceName":"1"});
            var Q156;
            Q156=makeQuery(id+"F24.opPattern","COPY",BODY,{"derivedFrom":makeQuery(id+"F22.opPattern","COPY",BODY,{"derivedFrom":makeQuery(id+"F19.opPattern","COPY",BODY,{"derivedFrom":makeQuery(id+"F16.opExtrude","SWEPT_BODY",BODY,{"disambiguationData":[OSD([sQuery(id+"F15.wireOp",EDGE,"E13.bottom"),sQuery(id+"F15.wireOp",EDGE,"E13.top"),sQuery(id+"F15.wireOp",EDGE,"E13.left"),sQuery(id+"F15.wireOp",EDGE,"E13.right"),sQuery(id+"F15.wireOp",EDGE,"E14.bottom"),sQuery(id+"F15.wireOp",EDGE,"E14.top"),sQuery(id+"F15.wireOp",EDGE,"E14.left"),sQuery(id+"F15.wireOp",EDGE,"E14.right"),sQuery(id+"F15.wireOp",EDGE,"E15.MirrorCS"),sQuery(id+"F15.wireOp",EDGE,"E16.MirrorCS"),sQuery(id+"F15.wireOp",EDGE,"E17.MirrorCS"),sQuery(id+"F15.wireOp",EDGE,"E18.MirrorCS"),sQuery(id+"F15.wireOp",EDGE,"E19.MirrorCS"),sQuery(id+"F15.wireOp",EDGE,"E20.MirrorCS"),sQuery(id+"F15.wireOp",EDGE,"E21.MirrorCS"),sQuery(id+"F15.wireOp",EDGE,"E22.MirrorCS"),sQuery(id+"F15.wireOp",EDGE,"E23.MirrorCS"),sQuery(id+"F15.wireOp",EDGE,"E24.MirrorCS"),sQuery(id+"F15.wireOp",EDGE,"E25.MirrorCS"),sQuery(id+"F15.wireOp",EDGE,"E26.MirrorCS")])]}),"instanceName":"1"}),"instanceName":"1"}),"instanceName":"1"});
            var Q157;
            Q157=makeQuery(id+"F24.opPattern","COPY",BODY,{"derivedFrom":makeQuery(id+"F22.opPattern","COPY",BODY,{"derivedFrom":makeQuery(id+"F19.opPattern","COPY",BODY,{"derivedFrom":makeQuery(id+"F17.opPattern","COPY",BODY,{"derivedFrom":makeQuery(id+"F16.opExtrude","SWEPT_BODY",BODY,{"disambiguationData":[OSD([sQuery(id+"F15.wireOp",EDGE,"E13.bottom"),sQuery(id+"F15.wireOp",EDGE,"E13.top"),sQuery(id+"F15.wireOp",EDGE,"E13.left"),sQuery(id+"F15.wireOp",EDGE,"E13.right"),sQuery(id+"F15.wireOp",EDGE,"E14.bottom"),sQuery(id+"F15.wireOp",EDGE,"E14.top"),sQuery(id+"F15.wireOp",EDGE,"E14.left"),sQuery(id+"F15.wireOp",EDGE,"E14.right"),sQuery(id+"F15.wireOp",EDGE,"E15.MirrorCS"),sQuery(id+"F15.wireOp",EDGE,"E16.MirrorCS"),sQuery(id+"F15.wireOp",EDGE,"E17.MirrorCS"),sQuery(id+"F15.wireOp",EDGE,"E18.MirrorCS"),sQuery(id+"F15.wireOp",EDGE,"E19.MirrorCS"),sQuery(id+"F15.wireOp",EDGE,"E20.MirrorCS"),sQuery(id+"F15.wireOp",EDGE,"E21.MirrorCS"),sQuery(id+"F15.wireOp",EDGE,"E22.MirrorCS"),sQuery(id+"F15.wireOp",EDGE,"E23.MirrorCS"),sQuery(id+"F15.wireOp",EDGE,"E24.MirrorCS"),sQuery(id+"F15.wireOp",EDGE,"E25.MirrorCS"),sQuery(id+"F15.wireOp",EDGE,"E26.MirrorCS")])]}),"instanceName":"1"}),"instanceName":"1"}),"instanceName":"1"}),"instanceName":"1"});
            var Q158;
            Q158=makeQuery(id+"F24.opPattern","COPY",BODY,{"derivedFrom":makeQuery(id+"F22.opPattern","COPY",BODY,{"derivedFrom":makeQuery(id+"F19.opPattern","COPY",BODY,{"derivedFrom":makeQuery(id+"F18.opPattern","COPY",BODY,{"derivedFrom":makeQuery(id+"F16.opExtrude","SWEPT_BODY",BODY,{"disambiguationData":[OSD([sQuery(id+"F15.wireOp",EDGE,"E13.bottom"),sQuery(id+"F15.wireOp",EDGE,"E13.top"),sQuery(id+"F15.wireOp",EDGE,"E13.left"),sQuery(id+"F15.wireOp",EDGE,"E13.right"),sQuery(id+"F15.wireOp",EDGE,"E14.bottom"),sQuery(id+"F15.wireOp",EDGE,"E14.top"),sQuery(id+"F15.wireOp",EDGE,"E14.left"),sQuery(id+"F15.wireOp",EDGE,"E14.right"),sQuery(id+"F15.wireOp",EDGE,"E15.MirrorCS"),sQuery(id+"F15.wireOp",EDGE,"E16.MirrorCS"),sQuery(id+"F15.wireOp",EDGE,"E17.MirrorCS"),sQuery(id+"F15.wireOp",EDGE,"E18.MirrorCS"),sQuery(id+"F15.wireOp",EDGE,"E19.MirrorCS"),sQuery(id+"F15.wireOp",EDGE,"E20.MirrorCS"),sQuery(id+"F15.wireOp",EDGE,"E21.MirrorCS"),sQuery(id+"F15.wireOp",EDGE,"E22.MirrorCS"),sQuery(id+"F15.wireOp",EDGE,"E23.MirrorCS"),sQuery(id+"F15.wireOp",EDGE,"E24.MirrorCS"),sQuery(id+"F15.wireOp",EDGE,"E25.MirrorCS"),sQuery(id+"F15.wireOp",EDGE,"E26.MirrorCS")])]}),"instanceName":"1"}),"instanceName":"1"}),"instanceName":"1"}),"instanceName":"1"});
            var Q159;
            Q159=makeQuery(id+"F24.opPattern","COPY",BODY,{"derivedFrom":makeQuery(id+"F22.opPattern","COPY",BODY,{"derivedFrom":makeQuery(id+"F19.opPattern","COPY",BODY,{"derivedFrom":makeQuery(id+"F18.opPattern","COPY",BODY,{"derivedFrom":makeQuery(id+"F17.opPattern","COPY",BODY,{"derivedFrom":makeQuery(id+"F16.opExtrude","SWEPT_BODY",BODY,{"disambiguationData":[OSD([sQuery(id+"F15.wireOp",EDGE,"E13.bottom"),sQuery(id+"F15.wireOp",EDGE,"E13.top"),sQuery(id+"F15.wireOp",EDGE,"E13.left"),sQuery(id+"F15.wireOp",EDGE,"E13.right"),sQuery(id+"F15.wireOp",EDGE,"E14.bottom"),sQuery(id+"F15.wireOp",EDGE,"E14.top"),sQuery(id+"F15.wireOp",EDGE,"E14.left"),sQuery(id+"F15.wireOp",EDGE,"E14.right"),sQuery(id+"F15.wireOp",EDGE,"E15.MirrorCS"),sQuery(id+"F15.wireOp",EDGE,"E16.MirrorCS"),sQuery(id+"F15.wireOp",EDGE,"E17.MirrorCS"),sQuery(id+"F15.wireOp",EDGE,"E18.MirrorCS"),sQuery(id+"F15.wireOp",EDGE,"E19.MirrorCS"),sQuery(id+"F15.wireOp",EDGE,"E20.MirrorCS"),sQuery(id+"F15.wireOp",EDGE,"E21.MirrorCS"),sQuery(id+"F15.wireOp",EDGE,"E22.MirrorCS"),sQuery(id+"F15.wireOp",EDGE,"E23.MirrorCS"),sQuery(id+"F15.wireOp",EDGE,"E24.MirrorCS"),sQuery(id+"F15.wireOp",EDGE,"E25.MirrorCS"),sQuery(id+"F15.wireOp",EDGE,"E26.MirrorCS")])]}),"instanceName":"1"}),"instanceName":"1"}),"instanceName":"1"}),"instanceName":"1"}),"instanceName":"1"});
            var Q160;
            Q160=makeQuery(id+"F24.opPattern","COPY",BODY,{"derivedFrom":makeQuery(id+"F22.opPattern","COPY",BODY,{"derivedFrom":makeQuery(id+"F20.opPattern","COPY",BODY,{"derivedFrom":makeQuery(id+"F16.opExtrude","SWEPT_BODY",BODY,{"disambiguationData":[OSD([sQuery(id+"F15.wireOp",EDGE,"E13.bottom"),sQuery(id+"F15.wireOp",EDGE,"E13.top"),sQuery(id+"F15.wireOp",EDGE,"E13.left"),sQuery(id+"F15.wireOp",EDGE,"E13.right"),sQuery(id+"F15.wireOp",EDGE,"E14.bottom"),sQuery(id+"F15.wireOp",EDGE,"E14.top"),sQuery(id+"F15.wireOp",EDGE,"E14.left"),sQuery(id+"F15.wireOp",EDGE,"E14.right"),sQuery(id+"F15.wireOp",EDGE,"E15.MirrorCS"),sQuery(id+"F15.wireOp",EDGE,"E16.MirrorCS"),sQuery(id+"F15.wireOp",EDGE,"E17.MirrorCS"),sQuery(id+"F15.wireOp",EDGE,"E18.MirrorCS"),sQuery(id+"F15.wireOp",EDGE,"E19.MirrorCS"),sQuery(id+"F15.wireOp",EDGE,"E20.MirrorCS"),sQuery(id+"F15.wireOp",EDGE,"E21.MirrorCS"),sQuery(id+"F15.wireOp",EDGE,"E22.MirrorCS"),sQuery(id+"F15.wireOp",EDGE,"E23.MirrorCS"),sQuery(id+"F15.wireOp",EDGE,"E24.MirrorCS"),sQuery(id+"F15.wireOp",EDGE,"E25.MirrorCS"),sQuery(id+"F15.wireOp",EDGE,"E26.MirrorCS")])]}),"instanceName":"1"}),"instanceName":"1"}),"instanceName":"1"});
            var Q161;
            Q161=makeQuery(id+"F24.opPattern","COPY",BODY,{"derivedFrom":makeQuery(id+"F22.opPattern","COPY",BODY,{"derivedFrom":makeQuery(id+"F20.opPattern","COPY",BODY,{"derivedFrom":makeQuery(id+"F17.opPattern","COPY",BODY,{"derivedFrom":makeQuery(id+"F16.opExtrude","SWEPT_BODY",BODY,{"disambiguationData":[OSD([sQuery(id+"F15.wireOp",EDGE,"E13.bottom"),sQuery(id+"F15.wireOp",EDGE,"E13.top"),sQuery(id+"F15.wireOp",EDGE,"E13.left"),sQuery(id+"F15.wireOp",EDGE,"E13.right"),sQuery(id+"F15.wireOp",EDGE,"E14.bottom"),sQuery(id+"F15.wireOp",EDGE,"E14.top"),sQuery(id+"F15.wireOp",EDGE,"E14.left"),sQuery(id+"F15.wireOp",EDGE,"E14.right"),sQuery(id+"F15.wireOp",EDGE,"E15.MirrorCS"),sQuery(id+"F15.wireOp",EDGE,"E16.MirrorCS"),sQuery(id+"F15.wireOp",EDGE,"E17.MirrorCS"),sQuery(id+"F15.wireOp",EDGE,"E18.MirrorCS"),sQuery(id+"F15.wireOp",EDGE,"E19.MirrorCS"),sQuery(id+"F15.wireOp",EDGE,"E20.MirrorCS"),sQuery(id+"F15.wireOp",EDGE,"E21.MirrorCS"),sQuery(id+"F15.wireOp",EDGE,"E22.MirrorCS"),sQuery(id+"F15.wireOp",EDGE,"E23.MirrorCS"),sQuery(id+"F15.wireOp",EDGE,"E24.MirrorCS"),sQuery(id+"F15.wireOp",EDGE,"E25.MirrorCS"),sQuery(id+"F15.wireOp",EDGE,"E26.MirrorCS")])]}),"instanceName":"1"}),"instanceName":"1"}),"instanceName":"1"}),"instanceName":"1"});
            var Q162;
            Q162=makeQuery(id+"F24.opPattern","COPY",BODY,{"derivedFrom":makeQuery(id+"F22.opPattern","COPY",BODY,{"derivedFrom":makeQuery(id+"F20.opPattern","COPY",BODY,{"derivedFrom":makeQuery(id+"F18.opPattern","COPY",BODY,{"derivedFrom":makeQuery(id+"F16.opExtrude","SWEPT_BODY",BODY,{"disambiguationData":[OSD([sQuery(id+"F15.wireOp",EDGE,"E13.bottom"),sQuery(id+"F15.wireOp",EDGE,"E13.top"),sQuery(id+"F15.wireOp",EDGE,"E13.left"),sQuery(id+"F15.wireOp",EDGE,"E13.right"),sQuery(id+"F15.wireOp",EDGE,"E14.bottom"),sQuery(id+"F15.wireOp",EDGE,"E14.top"),sQuery(id+"F15.wireOp",EDGE,"E14.left"),sQuery(id+"F15.wireOp",EDGE,"E14.right"),sQuery(id+"F15.wireOp",EDGE,"E15.MirrorCS"),sQuery(id+"F15.wireOp",EDGE,"E16.MirrorCS"),sQuery(id+"F15.wireOp",EDGE,"E17.MirrorCS"),sQuery(id+"F15.wireOp",EDGE,"E18.MirrorCS"),sQuery(id+"F15.wireOp",EDGE,"E19.MirrorCS"),sQuery(id+"F15.wireOp",EDGE,"E20.MirrorCS"),sQuery(id+"F15.wireOp",EDGE,"E21.MirrorCS"),sQuery(id+"F15.wireOp",EDGE,"E22.MirrorCS"),sQuery(id+"F15.wireOp",EDGE,"E23.MirrorCS"),sQuery(id+"F15.wireOp",EDGE,"E24.MirrorCS"),sQuery(id+"F15.wireOp",EDGE,"E25.MirrorCS"),sQuery(id+"F15.wireOp",EDGE,"E26.MirrorCS")])]}),"instanceName":"1"}),"instanceName":"1"}),"instanceName":"1"}),"instanceName":"1"});
            var Q163;
            Q163=makeQuery(id+"F24.opPattern","COPY",BODY,{"derivedFrom":makeQuery(id+"F22.opPattern","COPY",BODY,{"derivedFrom":makeQuery(id+"F20.opPattern","COPY",BODY,{"derivedFrom":makeQuery(id+"F18.opPattern","COPY",BODY,{"derivedFrom":makeQuery(id+"F17.opPattern","COPY",BODY,{"derivedFrom":makeQuery(id+"F16.opExtrude","SWEPT_BODY",BODY,{"disambiguationData":[OSD([sQuery(id+"F15.wireOp",EDGE,"E13.bottom"),sQuery(id+"F15.wireOp",EDGE,"E13.top"),sQuery(id+"F15.wireOp",EDGE,"E13.left"),sQuery(id+"F15.wireOp",EDGE,"E13.right"),sQuery(id+"F15.wireOp",EDGE,"E14.bottom"),sQuery(id+"F15.wireOp",EDGE,"E14.top"),sQuery(id+"F15.wireOp",EDGE,"E14.left"),sQuery(id+"F15.wireOp",EDGE,"E14.right"),sQuery(id+"F15.wireOp",EDGE,"E15.MirrorCS"),sQuery(id+"F15.wireOp",EDGE,"E16.MirrorCS"),sQuery(id+"F15.wireOp",EDGE,"E17.MirrorCS"),sQuery(id+"F15.wireOp",EDGE,"E18.MirrorCS"),sQuery(id+"F15.wireOp",EDGE,"E19.MirrorCS"),sQuery(id+"F15.wireOp",EDGE,"E20.MirrorCS"),sQuery(id+"F15.wireOp",EDGE,"E21.MirrorCS"),sQuery(id+"F15.wireOp",EDGE,"E22.MirrorCS"),sQuery(id+"F15.wireOp",EDGE,"E23.MirrorCS"),sQuery(id+"F15.wireOp",EDGE,"E24.MirrorCS"),sQuery(id+"F15.wireOp",EDGE,"E25.MirrorCS"),sQuery(id+"F15.wireOp",EDGE,"E26.MirrorCS")])]}),"instanceName":"1"}),"instanceName":"1"}),"instanceName":"1"}),"instanceName":"1"}),"instanceName":"1"});
            var Q164;
            Q164=makeQuery(id+"F24.opPattern","COPY",BODY,{"derivedFrom":makeQuery(id+"F22.opPattern","COPY",BODY,{"derivedFrom":makeQuery(id+"F20.opPattern","COPY",BODY,{"derivedFrom":makeQuery(id+"F19.opPattern","COPY",BODY,{"derivedFrom":makeQuery(id+"F16.opExtrude","SWEPT_BODY",BODY,{"disambiguationData":[OSD([sQuery(id+"F15.wireOp",EDGE,"E13.bottom"),sQuery(id+"F15.wireOp",EDGE,"E13.top"),sQuery(id+"F15.wireOp",EDGE,"E13.left"),sQuery(id+"F15.wireOp",EDGE,"E13.right"),sQuery(id+"F15.wireOp",EDGE,"E14.bottom"),sQuery(id+"F15.wireOp",EDGE,"E14.top"),sQuery(id+"F15.wireOp",EDGE,"E14.left"),sQuery(id+"F15.wireOp",EDGE,"E14.right"),sQuery(id+"F15.wireOp",EDGE,"E15.MirrorCS"),sQuery(id+"F15.wireOp",EDGE,"E16.MirrorCS"),sQuery(id+"F15.wireOp",EDGE,"E17.MirrorCS"),sQuery(id+"F15.wireOp",EDGE,"E18.MirrorCS"),sQuery(id+"F15.wireOp",EDGE,"E19.MirrorCS"),sQuery(id+"F15.wireOp",EDGE,"E20.MirrorCS"),sQuery(id+"F15.wireOp",EDGE,"E21.MirrorCS"),sQuery(id+"F15.wireOp",EDGE,"E22.MirrorCS"),sQuery(id+"F15.wireOp",EDGE,"E23.MirrorCS"),sQuery(id+"F15.wireOp",EDGE,"E24.MirrorCS"),sQuery(id+"F15.wireOp",EDGE,"E25.MirrorCS"),sQuery(id+"F15.wireOp",EDGE,"E26.MirrorCS")])]}),"instanceName":"1"}),"instanceName":"1"}),"instanceName":"1"}),"instanceName":"1"});
            var Q165;
            Q165=makeQuery(id+"F24.opPattern","COPY",BODY,{"derivedFrom":makeQuery(id+"F22.opPattern","COPY",BODY,{"derivedFrom":makeQuery(id+"F20.opPattern","COPY",BODY,{"derivedFrom":makeQuery(id+"F19.opPattern","COPY",BODY,{"derivedFrom":makeQuery(id+"F17.opPattern","COPY",BODY,{"derivedFrom":makeQuery(id+"F16.opExtrude","SWEPT_BODY",BODY,{"disambiguationData":[OSD([sQuery(id+"F15.wireOp",EDGE,"E13.bottom"),sQuery(id+"F15.wireOp",EDGE,"E13.top"),sQuery(id+"F15.wireOp",EDGE,"E13.left"),sQuery(id+"F15.wireOp",EDGE,"E13.right"),sQuery(id+"F15.wireOp",EDGE,"E14.bottom"),sQuery(id+"F15.wireOp",EDGE,"E14.top"),sQuery(id+"F15.wireOp",EDGE,"E14.left"),sQuery(id+"F15.wireOp",EDGE,"E14.right"),sQuery(id+"F15.wireOp",EDGE,"E15.MirrorCS"),sQuery(id+"F15.wireOp",EDGE,"E16.MirrorCS"),sQuery(id+"F15.wireOp",EDGE,"E17.MirrorCS"),sQuery(id+"F15.wireOp",EDGE,"E18.MirrorCS"),sQuery(id+"F15.wireOp",EDGE,"E19.MirrorCS"),sQuery(id+"F15.wireOp",EDGE,"E20.MirrorCS"),sQuery(id+"F15.wireOp",EDGE,"E21.MirrorCS"),sQuery(id+"F15.wireOp",EDGE,"E22.MirrorCS"),sQuery(id+"F15.wireOp",EDGE,"E23.MirrorCS"),sQuery(id+"F15.wireOp",EDGE,"E24.MirrorCS"),sQuery(id+"F15.wireOp",EDGE,"E25.MirrorCS"),sQuery(id+"F15.wireOp",EDGE,"E26.MirrorCS")])]}),"instanceName":"1"}),"instanceName":"1"}),"instanceName":"1"}),"instanceName":"1"}),"instanceName":"1"});
            var Q166;
            Q166=makeQuery(id+"F24.opPattern","COPY",BODY,{"derivedFrom":makeQuery(id+"F22.opPattern","COPY",BODY,{"derivedFrom":makeQuery(id+"F20.opPattern","COPY",BODY,{"derivedFrom":makeQuery(id+"F19.opPattern","COPY",BODY,{"derivedFrom":makeQuery(id+"F18.opPattern","COPY",BODY,{"derivedFrom":makeQuery(id+"F16.opExtrude","SWEPT_BODY",BODY,{"disambiguationData":[OSD([sQuery(id+"F15.wireOp",EDGE,"E13.bottom"),sQuery(id+"F15.wireOp",EDGE,"E13.top"),sQuery(id+"F15.wireOp",EDGE,"E13.left"),sQuery(id+"F15.wireOp",EDGE,"E13.right"),sQuery(id+"F15.wireOp",EDGE,"E14.bottom"),sQuery(id+"F15.wireOp",EDGE,"E14.top"),sQuery(id+"F15.wireOp",EDGE,"E14.left"),sQuery(id+"F15.wireOp",EDGE,"E14.right"),sQuery(id+"F15.wireOp",EDGE,"E15.MirrorCS"),sQuery(id+"F15.wireOp",EDGE,"E16.MirrorCS"),sQuery(id+"F15.wireOp",EDGE,"E17.MirrorCS"),sQuery(id+"F15.wireOp",EDGE,"E18.MirrorCS"),sQuery(id+"F15.wireOp",EDGE,"E19.MirrorCS"),sQuery(id+"F15.wireOp",EDGE,"E20.MirrorCS"),sQuery(id+"F15.wireOp",EDGE,"E21.MirrorCS"),sQuery(id+"F15.wireOp",EDGE,"E22.MirrorCS"),sQuery(id+"F15.wireOp",EDGE,"E23.MirrorCS"),sQuery(id+"F15.wireOp",EDGE,"E24.MirrorCS"),sQuery(id+"F15.wireOp",EDGE,"E25.MirrorCS"),sQuery(id+"F15.wireOp",EDGE,"E26.MirrorCS")])]}),"instanceName":"1"}),"instanceName":"1"}),"instanceName":"1"}),"instanceName":"1"}),"instanceName":"1"});
            var Q167;
            Q167=makeQuery(id+"F24.opPattern","COPY",BODY,{"derivedFrom":makeQuery(id+"F22.opPattern","COPY",BODY,{"derivedFrom":makeQuery(id+"F20.opPattern","COPY",BODY,{"derivedFrom":makeQuery(id+"F19.opPattern","COPY",BODY,{"derivedFrom":makeQuery(id+"F18.opPattern","COPY",BODY,{"derivedFrom":makeQuery(id+"F17.opPattern","COPY",BODY,{"derivedFrom":makeQuery(id+"F16.opExtrude","SWEPT_BODY",BODY,{"disambiguationData":[OSD([sQuery(id+"F15.wireOp",EDGE,"E13.bottom"),sQuery(id+"F15.wireOp",EDGE,"E13.top"),sQuery(id+"F15.wireOp",EDGE,"E13.left"),sQuery(id+"F15.wireOp",EDGE,"E13.right"),sQuery(id+"F15.wireOp",EDGE,"E14.bottom"),sQuery(id+"F15.wireOp",EDGE,"E14.top"),sQuery(id+"F15.wireOp",EDGE,"E14.left"),sQuery(id+"F15.wireOp",EDGE,"E14.right"),sQuery(id+"F15.wireOp",EDGE,"E15.MirrorCS"),sQuery(id+"F15.wireOp",EDGE,"E16.MirrorCS"),sQuery(id+"F15.wireOp",EDGE,"E17.MirrorCS"),sQuery(id+"F15.wireOp",EDGE,"E18.MirrorCS"),sQuery(id+"F15.wireOp",EDGE,"E19.MirrorCS"),sQuery(id+"F15.wireOp",EDGE,"E20.MirrorCS"),sQuery(id+"F15.wireOp",EDGE,"E21.MirrorCS"),sQuery(id+"F15.wireOp",EDGE,"E22.MirrorCS"),sQuery(id+"F15.wireOp",EDGE,"E23.MirrorCS"),sQuery(id+"F15.wireOp",EDGE,"E24.MirrorCS"),sQuery(id+"F15.wireOp",EDGE,"E25.MirrorCS"),sQuery(id+"F15.wireOp",EDGE,"E26.MirrorCS")])]}),"instanceName":"1"}),"instanceName":"1"}),"instanceName":"1"}),"instanceName":"1"}),"instanceName":"1"}),"instanceName":"1"});
            var Q168;
            Q168=makeQuery(id+"F24.opPattern","COPY",BODY,{"derivedFrom":makeQuery(id+"F22.opPattern","COPY",BODY,{"derivedFrom":makeQuery(id+"F21.opPattern","COPY",BODY,{"derivedFrom":makeQuery(id+"F16.opExtrude","SWEPT_BODY",BODY,{"disambiguationData":[OSD([sQuery(id+"F15.wireOp",EDGE,"E13.bottom"),sQuery(id+"F15.wireOp",EDGE,"E13.top"),sQuery(id+"F15.wireOp",EDGE,"E13.left"),sQuery(id+"F15.wireOp",EDGE,"E13.right"),sQuery(id+"F15.wireOp",EDGE,"E14.bottom"),sQuery(id+"F15.wireOp",EDGE,"E14.top"),sQuery(id+"F15.wireOp",EDGE,"E14.left"),sQuery(id+"F15.wireOp",EDGE,"E14.right"),sQuery(id+"F15.wireOp",EDGE,"E15.MirrorCS"),sQuery(id+"F15.wireOp",EDGE,"E16.MirrorCS"),sQuery(id+"F15.wireOp",EDGE,"E17.MirrorCS"),sQuery(id+"F15.wireOp",EDGE,"E18.MirrorCS"),sQuery(id+"F15.wireOp",EDGE,"E19.MirrorCS"),sQuery(id+"F15.wireOp",EDGE,"E20.MirrorCS"),sQuery(id+"F15.wireOp",EDGE,"E21.MirrorCS"),sQuery(id+"F15.wireOp",EDGE,"E22.MirrorCS"),sQuery(id+"F15.wireOp",EDGE,"E23.MirrorCS"),sQuery(id+"F15.wireOp",EDGE,"E24.MirrorCS"),sQuery(id+"F15.wireOp",EDGE,"E25.MirrorCS"),sQuery(id+"F15.wireOp",EDGE,"E26.MirrorCS")])]}),"instanceName":"1"}),"instanceName":"1"}),"instanceName":"1"});
            var Q169;
            Q169=makeQuery(id+"F24.opPattern","COPY",BODY,{"derivedFrom":makeQuery(id+"F22.opPattern","COPY",BODY,{"derivedFrom":makeQuery(id+"F21.opPattern","COPY",BODY,{"derivedFrom":makeQuery(id+"F17.opPattern","COPY",BODY,{"derivedFrom":makeQuery(id+"F16.opExtrude","SWEPT_BODY",BODY,{"disambiguationData":[OSD([sQuery(id+"F15.wireOp",EDGE,"E13.bottom"),sQuery(id+"F15.wireOp",EDGE,"E13.top"),sQuery(id+"F15.wireOp",EDGE,"E13.left"),sQuery(id+"F15.wireOp",EDGE,"E13.right"),sQuery(id+"F15.wireOp",EDGE,"E14.bottom"),sQuery(id+"F15.wireOp",EDGE,"E14.top"),sQuery(id+"F15.wireOp",EDGE,"E14.left"),sQuery(id+"F15.wireOp",EDGE,"E14.right"),sQuery(id+"F15.wireOp",EDGE,"E15.MirrorCS"),sQuery(id+"F15.wireOp",EDGE,"E16.MirrorCS"),sQuery(id+"F15.wireOp",EDGE,"E17.MirrorCS"),sQuery(id+"F15.wireOp",EDGE,"E18.MirrorCS"),sQuery(id+"F15.wireOp",EDGE,"E19.MirrorCS"),sQuery(id+"F15.wireOp",EDGE,"E20.MirrorCS"),sQuery(id+"F15.wireOp",EDGE,"E21.MirrorCS"),sQuery(id+"F15.wireOp",EDGE,"E22.MirrorCS"),sQuery(id+"F15.wireOp",EDGE,"E23.MirrorCS"),sQuery(id+"F15.wireOp",EDGE,"E24.MirrorCS"),sQuery(id+"F15.wireOp",EDGE,"E25.MirrorCS"),sQuery(id+"F15.wireOp",EDGE,"E26.MirrorCS")])]}),"instanceName":"1"}),"instanceName":"1"}),"instanceName":"1"}),"instanceName":"1"});
            var Q170;
            Q170=makeQuery(id+"F24.opPattern","COPY",BODY,{"derivedFrom":makeQuery(id+"F22.opPattern","COPY",BODY,{"derivedFrom":makeQuery(id+"F21.opPattern","COPY",BODY,{"derivedFrom":makeQuery(id+"F18.opPattern","COPY",BODY,{"derivedFrom":makeQuery(id+"F16.opExtrude","SWEPT_BODY",BODY,{"disambiguationData":[OSD([sQuery(id+"F15.wireOp",EDGE,"E13.bottom"),sQuery(id+"F15.wireOp",EDGE,"E13.top"),sQuery(id+"F15.wireOp",EDGE,"E13.left"),sQuery(id+"F15.wireOp",EDGE,"E13.right"),sQuery(id+"F15.wireOp",EDGE,"E14.bottom"),sQuery(id+"F15.wireOp",EDGE,"E14.top"),sQuery(id+"F15.wireOp",EDGE,"E14.left"),sQuery(id+"F15.wireOp",EDGE,"E14.right"),sQuery(id+"F15.wireOp",EDGE,"E15.MirrorCS"),sQuery(id+"F15.wireOp",EDGE,"E16.MirrorCS"),sQuery(id+"F15.wireOp",EDGE,"E17.MirrorCS"),sQuery(id+"F15.wireOp",EDGE,"E18.MirrorCS"),sQuery(id+"F15.wireOp",EDGE,"E19.MirrorCS"),sQuery(id+"F15.wireOp",EDGE,"E20.MirrorCS"),sQuery(id+"F15.wireOp",EDGE,"E21.MirrorCS"),sQuery(id+"F15.wireOp",EDGE,"E22.MirrorCS"),sQuery(id+"F15.wireOp",EDGE,"E23.MirrorCS"),sQuery(id+"F15.wireOp",EDGE,"E24.MirrorCS"),sQuery(id+"F15.wireOp",EDGE,"E25.MirrorCS"),sQuery(id+"F15.wireOp",EDGE,"E26.MirrorCS")])]}),"instanceName":"1"}),"instanceName":"1"}),"instanceName":"1"}),"instanceName":"1"});
            var Q171;
            Q171=makeQuery(id+"F24.opPattern","COPY",BODY,{"derivedFrom":makeQuery(id+"F22.opPattern","COPY",BODY,{"derivedFrom":makeQuery(id+"F21.opPattern","COPY",BODY,{"derivedFrom":makeQuery(id+"F18.opPattern","COPY",BODY,{"derivedFrom":makeQuery(id+"F17.opPattern","COPY",BODY,{"derivedFrom":makeQuery(id+"F16.opExtrude","SWEPT_BODY",BODY,{"disambiguationData":[OSD([sQuery(id+"F15.wireOp",EDGE,"E13.bottom"),sQuery(id+"F15.wireOp",EDGE,"E13.top"),sQuery(id+"F15.wireOp",EDGE,"E13.left"),sQuery(id+"F15.wireOp",EDGE,"E13.right"),sQuery(id+"F15.wireOp",EDGE,"E14.bottom"),sQuery(id+"F15.wireOp",EDGE,"E14.top"),sQuery(id+"F15.wireOp",EDGE,"E14.left"),sQuery(id+"F15.wireOp",EDGE,"E14.right"),sQuery(id+"F15.wireOp",EDGE,"E15.MirrorCS"),sQuery(id+"F15.wireOp",EDGE,"E16.MirrorCS"),sQuery(id+"F15.wireOp",EDGE,"E17.MirrorCS"),sQuery(id+"F15.wireOp",EDGE,"E18.MirrorCS"),sQuery(id+"F15.wireOp",EDGE,"E19.MirrorCS"),sQuery(id+"F15.wireOp",EDGE,"E20.MirrorCS"),sQuery(id+"F15.wireOp",EDGE,"E21.MirrorCS"),sQuery(id+"F15.wireOp",EDGE,"E22.MirrorCS"),sQuery(id+"F15.wireOp",EDGE,"E23.MirrorCS"),sQuery(id+"F15.wireOp",EDGE,"E24.MirrorCS"),sQuery(id+"F15.wireOp",EDGE,"E25.MirrorCS"),sQuery(id+"F15.wireOp",EDGE,"E26.MirrorCS")])]}),"instanceName":"1"}),"instanceName":"1"}),"instanceName":"1"}),"instanceName":"1"}),"instanceName":"1"});
            var Q172;
            Q172=makeQuery(id+"F24.opPattern","COPY",BODY,{"derivedFrom":makeQuery(id+"F22.opPattern","COPY",BODY,{"derivedFrom":makeQuery(id+"F21.opPattern","COPY",BODY,{"derivedFrom":makeQuery(id+"F19.opPattern","COPY",BODY,{"derivedFrom":makeQuery(id+"F16.opExtrude","SWEPT_BODY",BODY,{"disambiguationData":[OSD([sQuery(id+"F15.wireOp",EDGE,"E13.bottom"),sQuery(id+"F15.wireOp",EDGE,"E13.top"),sQuery(id+"F15.wireOp",EDGE,"E13.left"),sQuery(id+"F15.wireOp",EDGE,"E13.right"),sQuery(id+"F15.wireOp",EDGE,"E14.bottom"),sQuery(id+"F15.wireOp",EDGE,"E14.top"),sQuery(id+"F15.wireOp",EDGE,"E14.left"),sQuery(id+"F15.wireOp",EDGE,"E14.right"),sQuery(id+"F15.wireOp",EDGE,"E15.MirrorCS"),sQuery(id+"F15.wireOp",EDGE,"E16.MirrorCS"),sQuery(id+"F15.wireOp",EDGE,"E17.MirrorCS"),sQuery(id+"F15.wireOp",EDGE,"E18.MirrorCS"),sQuery(id+"F15.wireOp",EDGE,"E19.MirrorCS"),sQuery(id+"F15.wireOp",EDGE,"E20.MirrorCS"),sQuery(id+"F15.wireOp",EDGE,"E21.MirrorCS"),sQuery(id+"F15.wireOp",EDGE,"E22.MirrorCS"),sQuery(id+"F15.wireOp",EDGE,"E23.MirrorCS"),sQuery(id+"F15.wireOp",EDGE,"E24.MirrorCS"),sQuery(id+"F15.wireOp",EDGE,"E25.MirrorCS"),sQuery(id+"F15.wireOp",EDGE,"E26.MirrorCS")])]}),"instanceName":"1"}),"instanceName":"1"}),"instanceName":"1"}),"instanceName":"1"});
            var Q173;
            Q173=makeQuery(id+"F24.opPattern","COPY",BODY,{"derivedFrom":makeQuery(id+"F22.opPattern","COPY",BODY,{"derivedFrom":makeQuery(id+"F21.opPattern","COPY",BODY,{"derivedFrom":makeQuery(id+"F19.opPattern","COPY",BODY,{"derivedFrom":makeQuery(id+"F17.opPattern","COPY",BODY,{"derivedFrom":makeQuery(id+"F16.opExtrude","SWEPT_BODY",BODY,{"disambiguationData":[OSD([sQuery(id+"F15.wireOp",EDGE,"E13.bottom"),sQuery(id+"F15.wireOp",EDGE,"E13.top"),sQuery(id+"F15.wireOp",EDGE,"E13.left"),sQuery(id+"F15.wireOp",EDGE,"E13.right"),sQuery(id+"F15.wireOp",EDGE,"E14.bottom"),sQuery(id+"F15.wireOp",EDGE,"E14.top"),sQuery(id+"F15.wireOp",EDGE,"E14.left"),sQuery(id+"F15.wireOp",EDGE,"E14.right"),sQuery(id+"F15.wireOp",EDGE,"E15.MirrorCS"),sQuery(id+"F15.wireOp",EDGE,"E16.MirrorCS"),sQuery(id+"F15.wireOp",EDGE,"E17.MirrorCS"),sQuery(id+"F15.wireOp",EDGE,"E18.MirrorCS"),sQuery(id+"F15.wireOp",EDGE,"E19.MirrorCS"),sQuery(id+"F15.wireOp",EDGE,"E20.MirrorCS"),sQuery(id+"F15.wireOp",EDGE,"E21.MirrorCS"),sQuery(id+"F15.wireOp",EDGE,"E22.MirrorCS"),sQuery(id+"F15.wireOp",EDGE,"E23.MirrorCS"),sQuery(id+"F15.wireOp",EDGE,"E24.MirrorCS"),sQuery(id+"F15.wireOp",EDGE,"E25.MirrorCS"),sQuery(id+"F15.wireOp",EDGE,"E26.MirrorCS")])]}),"instanceName":"1"}),"instanceName":"1"}),"instanceName":"1"}),"instanceName":"1"}),"instanceName":"1"});
            var Q174;
            Q174=makeQuery(id+"F24.opPattern","COPY",BODY,{"derivedFrom":makeQuery(id+"F22.opPattern","COPY",BODY,{"derivedFrom":makeQuery(id+"F21.opPattern","COPY",BODY,{"derivedFrom":makeQuery(id+"F19.opPattern","COPY",BODY,{"derivedFrom":makeQuery(id+"F18.opPattern","COPY",BODY,{"derivedFrom":makeQuery(id+"F16.opExtrude","SWEPT_BODY",BODY,{"disambiguationData":[OSD([sQuery(id+"F15.wireOp",EDGE,"E13.bottom"),sQuery(id+"F15.wireOp",EDGE,"E13.top"),sQuery(id+"F15.wireOp",EDGE,"E13.left"),sQuery(id+"F15.wireOp",EDGE,"E13.right"),sQuery(id+"F15.wireOp",EDGE,"E14.bottom"),sQuery(id+"F15.wireOp",EDGE,"E14.top"),sQuery(id+"F15.wireOp",EDGE,"E14.left"),sQuery(id+"F15.wireOp",EDGE,"E14.right"),sQuery(id+"F15.wireOp",EDGE,"E15.MirrorCS"),sQuery(id+"F15.wireOp",EDGE,"E16.MirrorCS"),sQuery(id+"F15.wireOp",EDGE,"E17.MirrorCS"),sQuery(id+"F15.wireOp",EDGE,"E18.MirrorCS"),sQuery(id+"F15.wireOp",EDGE,"E19.MirrorCS"),sQuery(id+"F15.wireOp",EDGE,"E20.MirrorCS"),sQuery(id+"F15.wireOp",EDGE,"E21.MirrorCS"),sQuery(id+"F15.wireOp",EDGE,"E22.MirrorCS"),sQuery(id+"F15.wireOp",EDGE,"E23.MirrorCS"),sQuery(id+"F15.wireOp",EDGE,"E24.MirrorCS"),sQuery(id+"F15.wireOp",EDGE,"E25.MirrorCS"),sQuery(id+"F15.wireOp",EDGE,"E26.MirrorCS")])]}),"instanceName":"1"}),"instanceName":"1"}),"instanceName":"1"}),"instanceName":"1"}),"instanceName":"1"});
            var Q175;
            Q175=makeQuery(id+"F24.opPattern","COPY",BODY,{"derivedFrom":makeQuery(id+"F22.opPattern","COPY",BODY,{"derivedFrom":makeQuery(id+"F21.opPattern","COPY",BODY,{"derivedFrom":makeQuery(id+"F19.opPattern","COPY",BODY,{"derivedFrom":makeQuery(id+"F18.opPattern","COPY",BODY,{"derivedFrom":makeQuery(id+"F17.opPattern","COPY",BODY,{"derivedFrom":makeQuery(id+"F16.opExtrude","SWEPT_BODY",BODY,{"disambiguationData":[OSD([sQuery(id+"F15.wireOp",EDGE,"E13.bottom"),sQuery(id+"F15.wireOp",EDGE,"E13.top"),sQuery(id+"F15.wireOp",EDGE,"E13.left"),sQuery(id+"F15.wireOp",EDGE,"E13.right"),sQuery(id+"F15.wireOp",EDGE,"E14.bottom"),sQuery(id+"F15.wireOp",EDGE,"E14.top"),sQuery(id+"F15.wireOp",EDGE,"E14.left"),sQuery(id+"F15.wireOp",EDGE,"E14.right"),sQuery(id+"F15.wireOp",EDGE,"E15.MirrorCS"),sQuery(id+"F15.wireOp",EDGE,"E16.MirrorCS"),sQuery(id+"F15.wireOp",EDGE,"E17.MirrorCS"),sQuery(id+"F15.wireOp",EDGE,"E18.MirrorCS"),sQuery(id+"F15.wireOp",EDGE,"E19.MirrorCS"),sQuery(id+"F15.wireOp",EDGE,"E20.MirrorCS"),sQuery(id+"F15.wireOp",EDGE,"E21.MirrorCS"),sQuery(id+"F15.wireOp",EDGE,"E22.MirrorCS"),sQuery(id+"F15.wireOp",EDGE,"E23.MirrorCS"),sQuery(id+"F15.wireOp",EDGE,"E24.MirrorCS"),sQuery(id+"F15.wireOp",EDGE,"E25.MirrorCS"),sQuery(id+"F15.wireOp",EDGE,"E26.MirrorCS")])]}),"instanceName":"1"}),"instanceName":"1"}),"instanceName":"1"}),"instanceName":"1"}),"instanceName":"1"}),"instanceName":"1"});
            var Q176;
            Q176=makeQuery(id+"F24.opPattern","COPY",BODY,{"derivedFrom":makeQuery(id+"F23.opPattern","COPY",BODY,{"derivedFrom":makeQuery(id+"F19.opPattern","COPY",BODY,{"derivedFrom":makeQuery(id+"F16.opExtrude","SWEPT_BODY",BODY,{"disambiguationData":[OSD([sQuery(id+"F15.wireOp",EDGE,"E13.bottom"),sQuery(id+"F15.wireOp",EDGE,"E13.top"),sQuery(id+"F15.wireOp",EDGE,"E13.left"),sQuery(id+"F15.wireOp",EDGE,"E13.right"),sQuery(id+"F15.wireOp",EDGE,"E14.bottom"),sQuery(id+"F15.wireOp",EDGE,"E14.top"),sQuery(id+"F15.wireOp",EDGE,"E14.left"),sQuery(id+"F15.wireOp",EDGE,"E14.right"),sQuery(id+"F15.wireOp",EDGE,"E15.MirrorCS"),sQuery(id+"F15.wireOp",EDGE,"E16.MirrorCS"),sQuery(id+"F15.wireOp",EDGE,"E17.MirrorCS"),sQuery(id+"F15.wireOp",EDGE,"E18.MirrorCS"),sQuery(id+"F15.wireOp",EDGE,"E19.MirrorCS"),sQuery(id+"F15.wireOp",EDGE,"E20.MirrorCS"),sQuery(id+"F15.wireOp",EDGE,"E21.MirrorCS"),sQuery(id+"F15.wireOp",EDGE,"E22.MirrorCS"),sQuery(id+"F15.wireOp",EDGE,"E23.MirrorCS"),sQuery(id+"F15.wireOp",EDGE,"E24.MirrorCS"),sQuery(id+"F15.wireOp",EDGE,"E25.MirrorCS"),sQuery(id+"F15.wireOp",EDGE,"E26.MirrorCS")])]}),"instanceName":"1"}),"instanceName":"1"}),"instanceName":"1"});
            var Q177;
            Q177=makeQuery(id+"F24.opPattern","COPY",BODY,{"derivedFrom":makeQuery(id+"F23.opPattern","COPY",BODY,{"derivedFrom":makeQuery(id+"F19.opPattern","COPY",BODY,{"derivedFrom":makeQuery(id+"F17.opPattern","COPY",BODY,{"derivedFrom":makeQuery(id+"F16.opExtrude","SWEPT_BODY",BODY,{"disambiguationData":[OSD([sQuery(id+"F15.wireOp",EDGE,"E13.bottom"),sQuery(id+"F15.wireOp",EDGE,"E13.top"),sQuery(id+"F15.wireOp",EDGE,"E13.left"),sQuery(id+"F15.wireOp",EDGE,"E13.right"),sQuery(id+"F15.wireOp",EDGE,"E14.bottom"),sQuery(id+"F15.wireOp",EDGE,"E14.top"),sQuery(id+"F15.wireOp",EDGE,"E14.left"),sQuery(id+"F15.wireOp",EDGE,"E14.right"),sQuery(id+"F15.wireOp",EDGE,"E15.MirrorCS"),sQuery(id+"F15.wireOp",EDGE,"E16.MirrorCS"),sQuery(id+"F15.wireOp",EDGE,"E17.MirrorCS"),sQuery(id+"F15.wireOp",EDGE,"E18.MirrorCS"),sQuery(id+"F15.wireOp",EDGE,"E19.MirrorCS"),sQuery(id+"F15.wireOp",EDGE,"E20.MirrorCS"),sQuery(id+"F15.wireOp",EDGE,"E21.MirrorCS"),sQuery(id+"F15.wireOp",EDGE,"E22.MirrorCS"),sQuery(id+"F15.wireOp",EDGE,"E23.MirrorCS"),sQuery(id+"F15.wireOp",EDGE,"E24.MirrorCS"),sQuery(id+"F15.wireOp",EDGE,"E25.MirrorCS"),sQuery(id+"F15.wireOp",EDGE,"E26.MirrorCS")])]}),"instanceName":"1"}),"instanceName":"1"}),"instanceName":"1"}),"instanceName":"1"});
            var Q178;
            Q178=makeQuery(id+"F24.opPattern","COPY",BODY,{"derivedFrom":makeQuery(id+"F23.opPattern","COPY",BODY,{"derivedFrom":makeQuery(id+"F19.opPattern","COPY",BODY,{"derivedFrom":makeQuery(id+"F18.opPattern","COPY",BODY,{"derivedFrom":makeQuery(id+"F16.opExtrude","SWEPT_BODY",BODY,{"disambiguationData":[OSD([sQuery(id+"F15.wireOp",EDGE,"E13.bottom"),sQuery(id+"F15.wireOp",EDGE,"E13.top"),sQuery(id+"F15.wireOp",EDGE,"E13.left"),sQuery(id+"F15.wireOp",EDGE,"E13.right"),sQuery(id+"F15.wireOp",EDGE,"E14.bottom"),sQuery(id+"F15.wireOp",EDGE,"E14.top"),sQuery(id+"F15.wireOp",EDGE,"E14.left"),sQuery(id+"F15.wireOp",EDGE,"E14.right"),sQuery(id+"F15.wireOp",EDGE,"E15.MirrorCS"),sQuery(id+"F15.wireOp",EDGE,"E16.MirrorCS"),sQuery(id+"F15.wireOp",EDGE,"E17.MirrorCS"),sQuery(id+"F15.wireOp",EDGE,"E18.MirrorCS"),sQuery(id+"F15.wireOp",EDGE,"E19.MirrorCS"),sQuery(id+"F15.wireOp",EDGE,"E20.MirrorCS"),sQuery(id+"F15.wireOp",EDGE,"E21.MirrorCS"),sQuery(id+"F15.wireOp",EDGE,"E22.MirrorCS"),sQuery(id+"F15.wireOp",EDGE,"E23.MirrorCS"),sQuery(id+"F15.wireOp",EDGE,"E24.MirrorCS"),sQuery(id+"F15.wireOp",EDGE,"E25.MirrorCS"),sQuery(id+"F15.wireOp",EDGE,"E26.MirrorCS")])]}),"instanceName":"1"}),"instanceName":"1"}),"instanceName":"1"}),"instanceName":"1"});
            var Q179;
            Q179=makeQuery(id+"F24.opPattern","COPY",BODY,{"derivedFrom":makeQuery(id+"F23.opPattern","COPY",BODY,{"derivedFrom":makeQuery(id+"F19.opPattern","COPY",BODY,{"derivedFrom":makeQuery(id+"F18.opPattern","COPY",BODY,{"derivedFrom":makeQuery(id+"F17.opPattern","COPY",BODY,{"derivedFrom":makeQuery(id+"F16.opExtrude","SWEPT_BODY",BODY,{"disambiguationData":[OSD([sQuery(id+"F15.wireOp",EDGE,"E13.bottom"),sQuery(id+"F15.wireOp",EDGE,"E13.top"),sQuery(id+"F15.wireOp",EDGE,"E13.left"),sQuery(id+"F15.wireOp",EDGE,"E13.right"),sQuery(id+"F15.wireOp",EDGE,"E14.bottom"),sQuery(id+"F15.wireOp",EDGE,"E14.top"),sQuery(id+"F15.wireOp",EDGE,"E14.left"),sQuery(id+"F15.wireOp",EDGE,"E14.right"),sQuery(id+"F15.wireOp",EDGE,"E15.MirrorCS"),sQuery(id+"F15.wireOp",EDGE,"E16.MirrorCS"),sQuery(id+"F15.wireOp",EDGE,"E17.MirrorCS"),sQuery(id+"F15.wireOp",EDGE,"E18.MirrorCS"),sQuery(id+"F15.wireOp",EDGE,"E19.MirrorCS"),sQuery(id+"F15.wireOp",EDGE,"E20.MirrorCS"),sQuery(id+"F15.wireOp",EDGE,"E21.MirrorCS"),sQuery(id+"F15.wireOp",EDGE,"E22.MirrorCS"),sQuery(id+"F15.wireOp",EDGE,"E23.MirrorCS"),sQuery(id+"F15.wireOp",EDGE,"E24.MirrorCS"),sQuery(id+"F15.wireOp",EDGE,"E25.MirrorCS"),sQuery(id+"F15.wireOp",EDGE,"E26.MirrorCS")])]}),"instanceName":"1"}),"instanceName":"1"}),"instanceName":"1"}),"instanceName":"1"}),"instanceName":"1"});
            var Q180;
            Q180=makeQuery(id+"F24.opPattern","COPY",BODY,{"derivedFrom":makeQuery(id+"F23.opPattern","COPY",BODY,{"derivedFrom":makeQuery(id+"F20.opPattern","COPY",BODY,{"derivedFrom":makeQuery(id+"F16.opExtrude","SWEPT_BODY",BODY,{"disambiguationData":[OSD([sQuery(id+"F15.wireOp",EDGE,"E13.bottom"),sQuery(id+"F15.wireOp",EDGE,"E13.top"),sQuery(id+"F15.wireOp",EDGE,"E13.left"),sQuery(id+"F15.wireOp",EDGE,"E13.right"),sQuery(id+"F15.wireOp",EDGE,"E14.bottom"),sQuery(id+"F15.wireOp",EDGE,"E14.top"),sQuery(id+"F15.wireOp",EDGE,"E14.left"),sQuery(id+"F15.wireOp",EDGE,"E14.right"),sQuery(id+"F15.wireOp",EDGE,"E15.MirrorCS"),sQuery(id+"F15.wireOp",EDGE,"E16.MirrorCS"),sQuery(id+"F15.wireOp",EDGE,"E17.MirrorCS"),sQuery(id+"F15.wireOp",EDGE,"E18.MirrorCS"),sQuery(id+"F15.wireOp",EDGE,"E19.MirrorCS"),sQuery(id+"F15.wireOp",EDGE,"E20.MirrorCS"),sQuery(id+"F15.wireOp",EDGE,"E21.MirrorCS"),sQuery(id+"F15.wireOp",EDGE,"E22.MirrorCS"),sQuery(id+"F15.wireOp",EDGE,"E23.MirrorCS"),sQuery(id+"F15.wireOp",EDGE,"E24.MirrorCS"),sQuery(id+"F15.wireOp",EDGE,"E25.MirrorCS"),sQuery(id+"F15.wireOp",EDGE,"E26.MirrorCS")])]}),"instanceName":"1"}),"instanceName":"1"}),"instanceName":"1"});
            var Q181;
            Q181=makeQuery(id+"F24.opPattern","COPY",BODY,{"derivedFrom":makeQuery(id+"F23.opPattern","COPY",BODY,{"derivedFrom":makeQuery(id+"F20.opPattern","COPY",BODY,{"derivedFrom":makeQuery(id+"F17.opPattern","COPY",BODY,{"derivedFrom":makeQuery(id+"F16.opExtrude","SWEPT_BODY",BODY,{"disambiguationData":[OSD([sQuery(id+"F15.wireOp",EDGE,"E13.bottom"),sQuery(id+"F15.wireOp",EDGE,"E13.top"),sQuery(id+"F15.wireOp",EDGE,"E13.left"),sQuery(id+"F15.wireOp",EDGE,"E13.right"),sQuery(id+"F15.wireOp",EDGE,"E14.bottom"),sQuery(id+"F15.wireOp",EDGE,"E14.top"),sQuery(id+"F15.wireOp",EDGE,"E14.left"),sQuery(id+"F15.wireOp",EDGE,"E14.right"),sQuery(id+"F15.wireOp",EDGE,"E15.MirrorCS"),sQuery(id+"F15.wireOp",EDGE,"E16.MirrorCS"),sQuery(id+"F15.wireOp",EDGE,"E17.MirrorCS"),sQuery(id+"F15.wireOp",EDGE,"E18.MirrorCS"),sQuery(id+"F15.wireOp",EDGE,"E19.MirrorCS"),sQuery(id+"F15.wireOp",EDGE,"E20.MirrorCS"),sQuery(id+"F15.wireOp",EDGE,"E21.MirrorCS"),sQuery(id+"F15.wireOp",EDGE,"E22.MirrorCS"),sQuery(id+"F15.wireOp",EDGE,"E23.MirrorCS"),sQuery(id+"F15.wireOp",EDGE,"E24.MirrorCS"),sQuery(id+"F15.wireOp",EDGE,"E25.MirrorCS"),sQuery(id+"F15.wireOp",EDGE,"E26.MirrorCS")])]}),"instanceName":"1"}),"instanceName":"1"}),"instanceName":"1"}),"instanceName":"1"});
            var Q182;
            Q182=makeQuery(id+"F24.opPattern","COPY",BODY,{"derivedFrom":makeQuery(id+"F23.opPattern","COPY",BODY,{"derivedFrom":makeQuery(id+"F20.opPattern","COPY",BODY,{"derivedFrom":makeQuery(id+"F18.opPattern","COPY",BODY,{"derivedFrom":makeQuery(id+"F16.opExtrude","SWEPT_BODY",BODY,{"disambiguationData":[OSD([sQuery(id+"F15.wireOp",EDGE,"E13.bottom"),sQuery(id+"F15.wireOp",EDGE,"E13.top"),sQuery(id+"F15.wireOp",EDGE,"E13.left"),sQuery(id+"F15.wireOp",EDGE,"E13.right"),sQuery(id+"F15.wireOp",EDGE,"E14.bottom"),sQuery(id+"F15.wireOp",EDGE,"E14.top"),sQuery(id+"F15.wireOp",EDGE,"E14.left"),sQuery(id+"F15.wireOp",EDGE,"E14.right"),sQuery(id+"F15.wireOp",EDGE,"E15.MirrorCS"),sQuery(id+"F15.wireOp",EDGE,"E16.MirrorCS"),sQuery(id+"F15.wireOp",EDGE,"E17.MirrorCS"),sQuery(id+"F15.wireOp",EDGE,"E18.MirrorCS"),sQuery(id+"F15.wireOp",EDGE,"E19.MirrorCS"),sQuery(id+"F15.wireOp",EDGE,"E20.MirrorCS"),sQuery(id+"F15.wireOp",EDGE,"E21.MirrorCS"),sQuery(id+"F15.wireOp",EDGE,"E22.MirrorCS"),sQuery(id+"F15.wireOp",EDGE,"E23.MirrorCS"),sQuery(id+"F15.wireOp",EDGE,"E24.MirrorCS"),sQuery(id+"F15.wireOp",EDGE,"E25.MirrorCS"),sQuery(id+"F15.wireOp",EDGE,"E26.MirrorCS")])]}),"instanceName":"1"}),"instanceName":"1"}),"instanceName":"1"}),"instanceName":"1"});
            var Q183;
            Q183=makeQuery(id+"F24.opPattern","COPY",BODY,{"derivedFrom":makeQuery(id+"F23.opPattern","COPY",BODY,{"derivedFrom":makeQuery(id+"F20.opPattern","COPY",BODY,{"derivedFrom":makeQuery(id+"F18.opPattern","COPY",BODY,{"derivedFrom":makeQuery(id+"F17.opPattern","COPY",BODY,{"derivedFrom":makeQuery(id+"F16.opExtrude","SWEPT_BODY",BODY,{"disambiguationData":[OSD([sQuery(id+"F15.wireOp",EDGE,"E13.bottom"),sQuery(id+"F15.wireOp",EDGE,"E13.top"),sQuery(id+"F15.wireOp",EDGE,"E13.left"),sQuery(id+"F15.wireOp",EDGE,"E13.right"),sQuery(id+"F15.wireOp",EDGE,"E14.bottom"),sQuery(id+"F15.wireOp",EDGE,"E14.top"),sQuery(id+"F15.wireOp",EDGE,"E14.left"),sQuery(id+"F15.wireOp",EDGE,"E14.right"),sQuery(id+"F15.wireOp",EDGE,"E15.MirrorCS"),sQuery(id+"F15.wireOp",EDGE,"E16.MirrorCS"),sQuery(id+"F15.wireOp",EDGE,"E17.MirrorCS"),sQuery(id+"F15.wireOp",EDGE,"E18.MirrorCS"),sQuery(id+"F15.wireOp",EDGE,"E19.MirrorCS"),sQuery(id+"F15.wireOp",EDGE,"E20.MirrorCS"),sQuery(id+"F15.wireOp",EDGE,"E21.MirrorCS"),sQuery(id+"F15.wireOp",EDGE,"E22.MirrorCS"),sQuery(id+"F15.wireOp",EDGE,"E23.MirrorCS"),sQuery(id+"F15.wireOp",EDGE,"E24.MirrorCS"),sQuery(id+"F15.wireOp",EDGE,"E25.MirrorCS"),sQuery(id+"F15.wireOp",EDGE,"E26.MirrorCS")])]}),"instanceName":"1"}),"instanceName":"1"}),"instanceName":"1"}),"instanceName":"1"}),"instanceName":"1"});
            var Q184;
            Q184=makeQuery(id+"F24.opPattern","COPY",BODY,{"derivedFrom":makeQuery(id+"F23.opPattern","COPY",BODY,{"derivedFrom":makeQuery(id+"F20.opPattern","COPY",BODY,{"derivedFrom":makeQuery(id+"F19.opPattern","COPY",BODY,{"derivedFrom":makeQuery(id+"F16.opExtrude","SWEPT_BODY",BODY,{"disambiguationData":[OSD([sQuery(id+"F15.wireOp",EDGE,"E13.bottom"),sQuery(id+"F15.wireOp",EDGE,"E13.top"),sQuery(id+"F15.wireOp",EDGE,"E13.left"),sQuery(id+"F15.wireOp",EDGE,"E13.right"),sQuery(id+"F15.wireOp",EDGE,"E14.bottom"),sQuery(id+"F15.wireOp",EDGE,"E14.top"),sQuery(id+"F15.wireOp",EDGE,"E14.left"),sQuery(id+"F15.wireOp",EDGE,"E14.right"),sQuery(id+"F15.wireOp",EDGE,"E15.MirrorCS"),sQuery(id+"F15.wireOp",EDGE,"E16.MirrorCS"),sQuery(id+"F15.wireOp",EDGE,"E17.MirrorCS"),sQuery(id+"F15.wireOp",EDGE,"E18.MirrorCS"),sQuery(id+"F15.wireOp",EDGE,"E19.MirrorCS"),sQuery(id+"F15.wireOp",EDGE,"E20.MirrorCS"),sQuery(id+"F15.wireOp",EDGE,"E21.MirrorCS"),sQuery(id+"F15.wireOp",EDGE,"E22.MirrorCS"),sQuery(id+"F15.wireOp",EDGE,"E23.MirrorCS"),sQuery(id+"F15.wireOp",EDGE,"E24.MirrorCS"),sQuery(id+"F15.wireOp",EDGE,"E25.MirrorCS"),sQuery(id+"F15.wireOp",EDGE,"E26.MirrorCS")])]}),"instanceName":"1"}),"instanceName":"1"}),"instanceName":"1"}),"instanceName":"1"});
            var Q185;
            Q185=makeQuery(id+"F24.opPattern","COPY",BODY,{"derivedFrom":makeQuery(id+"F23.opPattern","COPY",BODY,{"derivedFrom":makeQuery(id+"F20.opPattern","COPY",BODY,{"derivedFrom":makeQuery(id+"F19.opPattern","COPY",BODY,{"derivedFrom":makeQuery(id+"F17.opPattern","COPY",BODY,{"derivedFrom":makeQuery(id+"F16.opExtrude","SWEPT_BODY",BODY,{"disambiguationData":[OSD([sQuery(id+"F15.wireOp",EDGE,"E13.bottom"),sQuery(id+"F15.wireOp",EDGE,"E13.top"),sQuery(id+"F15.wireOp",EDGE,"E13.left"),sQuery(id+"F15.wireOp",EDGE,"E13.right"),sQuery(id+"F15.wireOp",EDGE,"E14.bottom"),sQuery(id+"F15.wireOp",EDGE,"E14.top"),sQuery(id+"F15.wireOp",EDGE,"E14.left"),sQuery(id+"F15.wireOp",EDGE,"E14.right"),sQuery(id+"F15.wireOp",EDGE,"E15.MirrorCS"),sQuery(id+"F15.wireOp",EDGE,"E16.MirrorCS"),sQuery(id+"F15.wireOp",EDGE,"E17.MirrorCS"),sQuery(id+"F15.wireOp",EDGE,"E18.MirrorCS"),sQuery(id+"F15.wireOp",EDGE,"E19.MirrorCS"),sQuery(id+"F15.wireOp",EDGE,"E20.MirrorCS"),sQuery(id+"F15.wireOp",EDGE,"E21.MirrorCS"),sQuery(id+"F15.wireOp",EDGE,"E22.MirrorCS"),sQuery(id+"F15.wireOp",EDGE,"E23.MirrorCS"),sQuery(id+"F15.wireOp",EDGE,"E24.MirrorCS"),sQuery(id+"F15.wireOp",EDGE,"E25.MirrorCS"),sQuery(id+"F15.wireOp",EDGE,"E26.MirrorCS")])]}),"instanceName":"1"}),"instanceName":"1"}),"instanceName":"1"}),"instanceName":"1"}),"instanceName":"1"});
            var Q186;
            Q186=makeQuery(id+"F24.opPattern","COPY",BODY,{"derivedFrom":makeQuery(id+"F23.opPattern","COPY",BODY,{"derivedFrom":makeQuery(id+"F20.opPattern","COPY",BODY,{"derivedFrom":makeQuery(id+"F19.opPattern","COPY",BODY,{"derivedFrom":makeQuery(id+"F18.opPattern","COPY",BODY,{"derivedFrom":makeQuery(id+"F16.opExtrude","SWEPT_BODY",BODY,{"disambiguationData":[OSD([sQuery(id+"F15.wireOp",EDGE,"E13.bottom"),sQuery(id+"F15.wireOp",EDGE,"E13.top"),sQuery(id+"F15.wireOp",EDGE,"E13.left"),sQuery(id+"F15.wireOp",EDGE,"E13.right"),sQuery(id+"F15.wireOp",EDGE,"E14.bottom"),sQuery(id+"F15.wireOp",EDGE,"E14.top"),sQuery(id+"F15.wireOp",EDGE,"E14.left"),sQuery(id+"F15.wireOp",EDGE,"E14.right"),sQuery(id+"F15.wireOp",EDGE,"E15.MirrorCS"),sQuery(id+"F15.wireOp",EDGE,"E16.MirrorCS"),sQuery(id+"F15.wireOp",EDGE,"E17.MirrorCS"),sQuery(id+"F15.wireOp",EDGE,"E18.MirrorCS"),sQuery(id+"F15.wireOp",EDGE,"E19.MirrorCS"),sQuery(id+"F15.wireOp",EDGE,"E20.MirrorCS"),sQuery(id+"F15.wireOp",EDGE,"E21.MirrorCS"),sQuery(id+"F15.wireOp",EDGE,"E22.MirrorCS"),sQuery(id+"F15.wireOp",EDGE,"E23.MirrorCS"),sQuery(id+"F15.wireOp",EDGE,"E24.MirrorCS"),sQuery(id+"F15.wireOp",EDGE,"E25.MirrorCS"),sQuery(id+"F15.wireOp",EDGE,"E26.MirrorCS")])]}),"instanceName":"1"}),"instanceName":"1"}),"instanceName":"1"}),"instanceName":"1"}),"instanceName":"1"});
            var Q187;
            Q187=makeQuery(id+"F24.opPattern","COPY",BODY,{"derivedFrom":makeQuery(id+"F23.opPattern","COPY",BODY,{"derivedFrom":makeQuery(id+"F20.opPattern","COPY",BODY,{"derivedFrom":makeQuery(id+"F19.opPattern","COPY",BODY,{"derivedFrom":makeQuery(id+"F18.opPattern","COPY",BODY,{"derivedFrom":makeQuery(id+"F17.opPattern","COPY",BODY,{"derivedFrom":makeQuery(id+"F16.opExtrude","SWEPT_BODY",BODY,{"disambiguationData":[OSD([sQuery(id+"F15.wireOp",EDGE,"E13.bottom"),sQuery(id+"F15.wireOp",EDGE,"E13.top"),sQuery(id+"F15.wireOp",EDGE,"E13.left"),sQuery(id+"F15.wireOp",EDGE,"E13.right"),sQuery(id+"F15.wireOp",EDGE,"E14.bottom"),sQuery(id+"F15.wireOp",EDGE,"E14.top"),sQuery(id+"F15.wireOp",EDGE,"E14.left"),sQuery(id+"F15.wireOp",EDGE,"E14.right"),sQuery(id+"F15.wireOp",EDGE,"E15.MirrorCS"),sQuery(id+"F15.wireOp",EDGE,"E16.MirrorCS"),sQuery(id+"F15.wireOp",EDGE,"E17.MirrorCS"),sQuery(id+"F15.wireOp",EDGE,"E18.MirrorCS"),sQuery(id+"F15.wireOp",EDGE,"E19.MirrorCS"),sQuery(id+"F15.wireOp",EDGE,"E20.MirrorCS"),sQuery(id+"F15.wireOp",EDGE,"E21.MirrorCS"),sQuery(id+"F15.wireOp",EDGE,"E22.MirrorCS"),sQuery(id+"F15.wireOp",EDGE,"E23.MirrorCS"),sQuery(id+"F15.wireOp",EDGE,"E24.MirrorCS"),sQuery(id+"F15.wireOp",EDGE,"E25.MirrorCS"),sQuery(id+"F15.wireOp",EDGE,"E26.MirrorCS")])]}),"instanceName":"1"}),"instanceName":"1"}),"instanceName":"1"}),"instanceName":"1"}),"instanceName":"1"}),"instanceName":"1"});
            var Q188;
            Q188=makeQuery(id+"F24.opPattern","COPY",BODY,{"derivedFrom":makeQuery(id+"F23.opPattern","COPY",BODY,{"derivedFrom":makeQuery(id+"F21.opPattern","COPY",BODY,{"derivedFrom":makeQuery(id+"F16.opExtrude","SWEPT_BODY",BODY,{"disambiguationData":[OSD([sQuery(id+"F15.wireOp",EDGE,"E13.bottom"),sQuery(id+"F15.wireOp",EDGE,"E13.top"),sQuery(id+"F15.wireOp",EDGE,"E13.left"),sQuery(id+"F15.wireOp",EDGE,"E13.right"),sQuery(id+"F15.wireOp",EDGE,"E14.bottom"),sQuery(id+"F15.wireOp",EDGE,"E14.top"),sQuery(id+"F15.wireOp",EDGE,"E14.left"),sQuery(id+"F15.wireOp",EDGE,"E14.right"),sQuery(id+"F15.wireOp",EDGE,"E15.MirrorCS"),sQuery(id+"F15.wireOp",EDGE,"E16.MirrorCS"),sQuery(id+"F15.wireOp",EDGE,"E17.MirrorCS"),sQuery(id+"F15.wireOp",EDGE,"E18.MirrorCS"),sQuery(id+"F15.wireOp",EDGE,"E19.MirrorCS"),sQuery(id+"F15.wireOp",EDGE,"E20.MirrorCS"),sQuery(id+"F15.wireOp",EDGE,"E21.MirrorCS"),sQuery(id+"F15.wireOp",EDGE,"E22.MirrorCS"),sQuery(id+"F15.wireOp",EDGE,"E23.MirrorCS"),sQuery(id+"F15.wireOp",EDGE,"E24.MirrorCS"),sQuery(id+"F15.wireOp",EDGE,"E25.MirrorCS"),sQuery(id+"F15.wireOp",EDGE,"E26.MirrorCS")])]}),"instanceName":"1"}),"instanceName":"1"}),"instanceName":"1"});
            var Q189;
            Q189=makeQuery(id+"F24.opPattern","COPY",BODY,{"derivedFrom":makeQuery(id+"F23.opPattern","COPY",BODY,{"derivedFrom":makeQuery(id+"F21.opPattern","COPY",BODY,{"derivedFrom":makeQuery(id+"F17.opPattern","COPY",BODY,{"derivedFrom":makeQuery(id+"F16.opExtrude","SWEPT_BODY",BODY,{"disambiguationData":[OSD([sQuery(id+"F15.wireOp",EDGE,"E13.bottom"),sQuery(id+"F15.wireOp",EDGE,"E13.top"),sQuery(id+"F15.wireOp",EDGE,"E13.left"),sQuery(id+"F15.wireOp",EDGE,"E13.right"),sQuery(id+"F15.wireOp",EDGE,"E14.bottom"),sQuery(id+"F15.wireOp",EDGE,"E14.top"),sQuery(id+"F15.wireOp",EDGE,"E14.left"),sQuery(id+"F15.wireOp",EDGE,"E14.right"),sQuery(id+"F15.wireOp",EDGE,"E15.MirrorCS"),sQuery(id+"F15.wireOp",EDGE,"E16.MirrorCS"),sQuery(id+"F15.wireOp",EDGE,"E17.MirrorCS"),sQuery(id+"F15.wireOp",EDGE,"E18.MirrorCS"),sQuery(id+"F15.wireOp",EDGE,"E19.MirrorCS"),sQuery(id+"F15.wireOp",EDGE,"E20.MirrorCS"),sQuery(id+"F15.wireOp",EDGE,"E21.MirrorCS"),sQuery(id+"F15.wireOp",EDGE,"E22.MirrorCS"),sQuery(id+"F15.wireOp",EDGE,"E23.MirrorCS"),sQuery(id+"F15.wireOp",EDGE,"E24.MirrorCS"),sQuery(id+"F15.wireOp",EDGE,"E25.MirrorCS"),sQuery(id+"F15.wireOp",EDGE,"E26.MirrorCS")])]}),"instanceName":"1"}),"instanceName":"1"}),"instanceName":"1"}),"instanceName":"1"});
            var Q190;
            Q190=makeQuery(id+"F24.opPattern","COPY",BODY,{"derivedFrom":makeQuery(id+"F23.opPattern","COPY",BODY,{"derivedFrom":makeQuery(id+"F21.opPattern","COPY",BODY,{"derivedFrom":makeQuery(id+"F18.opPattern","COPY",BODY,{"derivedFrom":makeQuery(id+"F16.opExtrude","SWEPT_BODY",BODY,{"disambiguationData":[OSD([sQuery(id+"F15.wireOp",EDGE,"E13.bottom"),sQuery(id+"F15.wireOp",EDGE,"E13.top"),sQuery(id+"F15.wireOp",EDGE,"E13.left"),sQuery(id+"F15.wireOp",EDGE,"E13.right"),sQuery(id+"F15.wireOp",EDGE,"E14.bottom"),sQuery(id+"F15.wireOp",EDGE,"E14.top"),sQuery(id+"F15.wireOp",EDGE,"E14.left"),sQuery(id+"F15.wireOp",EDGE,"E14.right"),sQuery(id+"F15.wireOp",EDGE,"E15.MirrorCS"),sQuery(id+"F15.wireOp",EDGE,"E16.MirrorCS"),sQuery(id+"F15.wireOp",EDGE,"E17.MirrorCS"),sQuery(id+"F15.wireOp",EDGE,"E18.MirrorCS"),sQuery(id+"F15.wireOp",EDGE,"E19.MirrorCS"),sQuery(id+"F15.wireOp",EDGE,"E20.MirrorCS"),sQuery(id+"F15.wireOp",EDGE,"E21.MirrorCS"),sQuery(id+"F15.wireOp",EDGE,"E22.MirrorCS"),sQuery(id+"F15.wireOp",EDGE,"E23.MirrorCS"),sQuery(id+"F15.wireOp",EDGE,"E24.MirrorCS"),sQuery(id+"F15.wireOp",EDGE,"E25.MirrorCS"),sQuery(id+"F15.wireOp",EDGE,"E26.MirrorCS")])]}),"instanceName":"1"}),"instanceName":"1"}),"instanceName":"1"}),"instanceName":"1"});
            var Q191;
            Q191=makeQuery(id+"F24.opPattern","COPY",BODY,{"derivedFrom":makeQuery(id+"F23.opPattern","COPY",BODY,{"derivedFrom":makeQuery(id+"F21.opPattern","COPY",BODY,{"derivedFrom":makeQuery(id+"F18.opPattern","COPY",BODY,{"derivedFrom":makeQuery(id+"F17.opPattern","COPY",BODY,{"derivedFrom":makeQuery(id+"F16.opExtrude","SWEPT_BODY",BODY,{"disambiguationData":[OSD([sQuery(id+"F15.wireOp",EDGE,"E13.bottom"),sQuery(id+"F15.wireOp",EDGE,"E13.top"),sQuery(id+"F15.wireOp",EDGE,"E13.left"),sQuery(id+"F15.wireOp",EDGE,"E13.right"),sQuery(id+"F15.wireOp",EDGE,"E14.bottom"),sQuery(id+"F15.wireOp",EDGE,"E14.top"),sQuery(id+"F15.wireOp",EDGE,"E14.left"),sQuery(id+"F15.wireOp",EDGE,"E14.right"),sQuery(id+"F15.wireOp",EDGE,"E15.MirrorCS"),sQuery(id+"F15.wireOp",EDGE,"E16.MirrorCS"),sQuery(id+"F15.wireOp",EDGE,"E17.MirrorCS"),sQuery(id+"F15.wireOp",EDGE,"E18.MirrorCS"),sQuery(id+"F15.wireOp",EDGE,"E19.MirrorCS"),sQuery(id+"F15.wireOp",EDGE,"E20.MirrorCS"),sQuery(id+"F15.wireOp",EDGE,"E21.MirrorCS"),sQuery(id+"F15.wireOp",EDGE,"E22.MirrorCS"),sQuery(id+"F15.wireOp",EDGE,"E23.MirrorCS"),sQuery(id+"F15.wireOp",EDGE,"E24.MirrorCS"),sQuery(id+"F15.wireOp",EDGE,"E25.MirrorCS"),sQuery(id+"F15.wireOp",EDGE,"E26.MirrorCS")])]}),"instanceName":"1"}),"instanceName":"1"}),"instanceName":"1"}),"instanceName":"1"}),"instanceName":"1"});
            var Q192;
            Q192=makeQuery(id+"F24.opPattern","COPY",BODY,{"derivedFrom":makeQuery(id+"F23.opPattern","COPY",BODY,{"derivedFrom":makeQuery(id+"F21.opPattern","COPY",BODY,{"derivedFrom":makeQuery(id+"F19.opPattern","COPY",BODY,{"derivedFrom":makeQuery(id+"F16.opExtrude","SWEPT_BODY",BODY,{"disambiguationData":[OSD([sQuery(id+"F15.wireOp",EDGE,"E13.bottom"),sQuery(id+"F15.wireOp",EDGE,"E13.top"),sQuery(id+"F15.wireOp",EDGE,"E13.left"),sQuery(id+"F15.wireOp",EDGE,"E13.right"),sQuery(id+"F15.wireOp",EDGE,"E14.bottom"),sQuery(id+"F15.wireOp",EDGE,"E14.top"),sQuery(id+"F15.wireOp",EDGE,"E14.left"),sQuery(id+"F15.wireOp",EDGE,"E14.right"),sQuery(id+"F15.wireOp",EDGE,"E15.MirrorCS"),sQuery(id+"F15.wireOp",EDGE,"E16.MirrorCS"),sQuery(id+"F15.wireOp",EDGE,"E17.MirrorCS"),sQuery(id+"F15.wireOp",EDGE,"E18.MirrorCS"),sQuery(id+"F15.wireOp",EDGE,"E19.MirrorCS"),sQuery(id+"F15.wireOp",EDGE,"E20.MirrorCS"),sQuery(id+"F15.wireOp",EDGE,"E21.MirrorCS"),sQuery(id+"F15.wireOp",EDGE,"E22.MirrorCS"),sQuery(id+"F15.wireOp",EDGE,"E23.MirrorCS"),sQuery(id+"F15.wireOp",EDGE,"E24.MirrorCS"),sQuery(id+"F15.wireOp",EDGE,"E25.MirrorCS"),sQuery(id+"F15.wireOp",EDGE,"E26.MirrorCS")])]}),"instanceName":"1"}),"instanceName":"1"}),"instanceName":"1"}),"instanceName":"1"});
            var Q193;
            Q193=makeQuery(id+"F24.opPattern","COPY",BODY,{"derivedFrom":makeQuery(id+"F23.opPattern","COPY",BODY,{"derivedFrom":makeQuery(id+"F21.opPattern","COPY",BODY,{"derivedFrom":makeQuery(id+"F19.opPattern","COPY",BODY,{"derivedFrom":makeQuery(id+"F17.opPattern","COPY",BODY,{"derivedFrom":makeQuery(id+"F16.opExtrude","SWEPT_BODY",BODY,{"disambiguationData":[OSD([sQuery(id+"F15.wireOp",EDGE,"E13.bottom"),sQuery(id+"F15.wireOp",EDGE,"E13.top"),sQuery(id+"F15.wireOp",EDGE,"E13.left"),sQuery(id+"F15.wireOp",EDGE,"E13.right"),sQuery(id+"F15.wireOp",EDGE,"E14.bottom"),sQuery(id+"F15.wireOp",EDGE,"E14.top"),sQuery(id+"F15.wireOp",EDGE,"E14.left"),sQuery(id+"F15.wireOp",EDGE,"E14.right"),sQuery(id+"F15.wireOp",EDGE,"E15.MirrorCS"),sQuery(id+"F15.wireOp",EDGE,"E16.MirrorCS"),sQuery(id+"F15.wireOp",EDGE,"E17.MirrorCS"),sQuery(id+"F15.wireOp",EDGE,"E18.MirrorCS"),sQuery(id+"F15.wireOp",EDGE,"E19.MirrorCS"),sQuery(id+"F15.wireOp",EDGE,"E20.MirrorCS"),sQuery(id+"F15.wireOp",EDGE,"E21.MirrorCS"),sQuery(id+"F15.wireOp",EDGE,"E22.MirrorCS"),sQuery(id+"F15.wireOp",EDGE,"E23.MirrorCS"),sQuery(id+"F15.wireOp",EDGE,"E24.MirrorCS"),sQuery(id+"F15.wireOp",EDGE,"E25.MirrorCS"),sQuery(id+"F15.wireOp",EDGE,"E26.MirrorCS")])]}),"instanceName":"1"}),"instanceName":"1"}),"instanceName":"1"}),"instanceName":"1"}),"instanceName":"1"});
            var Q194;
            Q194=makeQuery(id+"F24.opPattern","COPY",BODY,{"derivedFrom":makeQuery(id+"F23.opPattern","COPY",BODY,{"derivedFrom":makeQuery(id+"F21.opPattern","COPY",BODY,{"derivedFrom":makeQuery(id+"F19.opPattern","COPY",BODY,{"derivedFrom":makeQuery(id+"F18.opPattern","COPY",BODY,{"derivedFrom":makeQuery(id+"F16.opExtrude","SWEPT_BODY",BODY,{"disambiguationData":[OSD([sQuery(id+"F15.wireOp",EDGE,"E13.bottom"),sQuery(id+"F15.wireOp",EDGE,"E13.top"),sQuery(id+"F15.wireOp",EDGE,"E13.left"),sQuery(id+"F15.wireOp",EDGE,"E13.right"),sQuery(id+"F15.wireOp",EDGE,"E14.bottom"),sQuery(id+"F15.wireOp",EDGE,"E14.top"),sQuery(id+"F15.wireOp",EDGE,"E14.left"),sQuery(id+"F15.wireOp",EDGE,"E14.right"),sQuery(id+"F15.wireOp",EDGE,"E15.MirrorCS"),sQuery(id+"F15.wireOp",EDGE,"E16.MirrorCS"),sQuery(id+"F15.wireOp",EDGE,"E17.MirrorCS"),sQuery(id+"F15.wireOp",EDGE,"E18.MirrorCS"),sQuery(id+"F15.wireOp",EDGE,"E19.MirrorCS"),sQuery(id+"F15.wireOp",EDGE,"E20.MirrorCS"),sQuery(id+"F15.wireOp",EDGE,"E21.MirrorCS"),sQuery(id+"F15.wireOp",EDGE,"E22.MirrorCS"),sQuery(id+"F15.wireOp",EDGE,"E23.MirrorCS"),sQuery(id+"F15.wireOp",EDGE,"E24.MirrorCS"),sQuery(id+"F15.wireOp",EDGE,"E25.MirrorCS"),sQuery(id+"F15.wireOp",EDGE,"E26.MirrorCS")])]}),"instanceName":"1"}),"instanceName":"1"}),"instanceName":"1"}),"instanceName":"1"}),"instanceName":"1"});
            var Q195;
            Q195=makeQuery(id+"F24.opPattern","COPY",BODY,{"derivedFrom":makeQuery(id+"F23.opPattern","COPY",BODY,{"derivedFrom":makeQuery(id+"F21.opPattern","COPY",BODY,{"derivedFrom":makeQuery(id+"F19.opPattern","COPY",BODY,{"derivedFrom":makeQuery(id+"F18.opPattern","COPY",BODY,{"derivedFrom":makeQuery(id+"F17.opPattern","COPY",BODY,{"derivedFrom":makeQuery(id+"F16.opExtrude","SWEPT_BODY",BODY,{"disambiguationData":[OSD([sQuery(id+"F15.wireOp",EDGE,"E13.bottom"),sQuery(id+"F15.wireOp",EDGE,"E13.top"),sQuery(id+"F15.wireOp",EDGE,"E13.left"),sQuery(id+"F15.wireOp",EDGE,"E13.right"),sQuery(id+"F15.wireOp",EDGE,"E14.bottom"),sQuery(id+"F15.wireOp",EDGE,"E14.top"),sQuery(id+"F15.wireOp",EDGE,"E14.left"),sQuery(id+"F15.wireOp",EDGE,"E14.right"),sQuery(id+"F15.wireOp",EDGE,"E15.MirrorCS"),sQuery(id+"F15.wireOp",EDGE,"E16.MirrorCS"),sQuery(id+"F15.wireOp",EDGE,"E17.MirrorCS"),sQuery(id+"F15.wireOp",EDGE,"E18.MirrorCS"),sQuery(id+"F15.wireOp",EDGE,"E19.MirrorCS"),sQuery(id+"F15.wireOp",EDGE,"E20.MirrorCS"),sQuery(id+"F15.wireOp",EDGE,"E21.MirrorCS"),sQuery(id+"F15.wireOp",EDGE,"E22.MirrorCS"),sQuery(id+"F15.wireOp",EDGE,"E23.MirrorCS"),sQuery(id+"F15.wireOp",EDGE,"E24.MirrorCS"),sQuery(id+"F15.wireOp",EDGE,"E25.MirrorCS"),sQuery(id+"F15.wireOp",EDGE,"E26.MirrorCS")])]}),"instanceName":"1"}),"instanceName":"1"}),"instanceName":"1"}),"instanceName":"1"}),"instanceName":"1"}),"instanceName":"1"});
            var Q196;
            Q196=makeQuery(id+"F24.opPattern","COPY",BODY,{"derivedFrom":makeQuery(id+"F23.opPattern","COPY",BODY,{"derivedFrom":makeQuery(id+"F22.opPattern","COPY",BODY,{"derivedFrom":makeQuery(id+"F19.opPattern","COPY",BODY,{"derivedFrom":makeQuery(id+"F16.opExtrude","SWEPT_BODY",BODY,{"disambiguationData":[OSD([sQuery(id+"F15.wireOp",EDGE,"E13.bottom"),sQuery(id+"F15.wireOp",EDGE,"E13.top"),sQuery(id+"F15.wireOp",EDGE,"E13.left"),sQuery(id+"F15.wireOp",EDGE,"E13.right"),sQuery(id+"F15.wireOp",EDGE,"E14.bottom"),sQuery(id+"F15.wireOp",EDGE,"E14.top"),sQuery(id+"F15.wireOp",EDGE,"E14.left"),sQuery(id+"F15.wireOp",EDGE,"E14.right"),sQuery(id+"F15.wireOp",EDGE,"E15.MirrorCS"),sQuery(id+"F15.wireOp",EDGE,"E16.MirrorCS"),sQuery(id+"F15.wireOp",EDGE,"E17.MirrorCS"),sQuery(id+"F15.wireOp",EDGE,"E18.MirrorCS"),sQuery(id+"F15.wireOp",EDGE,"E19.MirrorCS"),sQuery(id+"F15.wireOp",EDGE,"E20.MirrorCS"),sQuery(id+"F15.wireOp",EDGE,"E21.MirrorCS"),sQuery(id+"F15.wireOp",EDGE,"E22.MirrorCS"),sQuery(id+"F15.wireOp",EDGE,"E23.MirrorCS"),sQuery(id+"F15.wireOp",EDGE,"E24.MirrorCS"),sQuery(id+"F15.wireOp",EDGE,"E25.MirrorCS"),sQuery(id+"F15.wireOp",EDGE,"E26.MirrorCS")])]}),"instanceName":"1"}),"instanceName":"1"}),"instanceName":"1"}),"instanceName":"1"});
            var Q197;
            Q197=makeQuery(id+"F24.opPattern","COPY",BODY,{"derivedFrom":makeQuery(id+"F23.opPattern","COPY",BODY,{"derivedFrom":makeQuery(id+"F22.opPattern","COPY",BODY,{"derivedFrom":makeQuery(id+"F19.opPattern","COPY",BODY,{"derivedFrom":makeQuery(id+"F17.opPattern","COPY",BODY,{"derivedFrom":makeQuery(id+"F16.opExtrude","SWEPT_BODY",BODY,{"disambiguationData":[OSD([sQuery(id+"F15.wireOp",EDGE,"E13.bottom"),sQuery(id+"F15.wireOp",EDGE,"E13.top"),sQuery(id+"F15.wireOp",EDGE,"E13.left"),sQuery(id+"F15.wireOp",EDGE,"E13.right"),sQuery(id+"F15.wireOp",EDGE,"E14.bottom"),sQuery(id+"F15.wireOp",EDGE,"E14.top"),sQuery(id+"F15.wireOp",EDGE,"E14.left"),sQuery(id+"F15.wireOp",EDGE,"E14.right"),sQuery(id+"F15.wireOp",EDGE,"E15.MirrorCS"),sQuery(id+"F15.wireOp",EDGE,"E16.MirrorCS"),sQuery(id+"F15.wireOp",EDGE,"E17.MirrorCS"),sQuery(id+"F15.wireOp",EDGE,"E18.MirrorCS"),sQuery(id+"F15.wireOp",EDGE,"E19.MirrorCS"),sQuery(id+"F15.wireOp",EDGE,"E20.MirrorCS"),sQuery(id+"F15.wireOp",EDGE,"E21.MirrorCS"),sQuery(id+"F15.wireOp",EDGE,"E22.MirrorCS"),sQuery(id+"F15.wireOp",EDGE,"E23.MirrorCS"),sQuery(id+"F15.wireOp",EDGE,"E24.MirrorCS"),sQuery(id+"F15.wireOp",EDGE,"E25.MirrorCS"),sQuery(id+"F15.wireOp",EDGE,"E26.MirrorCS")])]}),"instanceName":"1"}),"instanceName":"1"}),"instanceName":"1"}),"instanceName":"1"}),"instanceName":"1"});
            var Q198;
            Q198=makeQuery(id+"F24.opPattern","COPY",BODY,{"derivedFrom":makeQuery(id+"F23.opPattern","COPY",BODY,{"derivedFrom":makeQuery(id+"F22.opPattern","COPY",BODY,{"derivedFrom":makeQuery(id+"F19.opPattern","COPY",BODY,{"derivedFrom":makeQuery(id+"F18.opPattern","COPY",BODY,{"derivedFrom":makeQuery(id+"F16.opExtrude","SWEPT_BODY",BODY,{"disambiguationData":[OSD([sQuery(id+"F15.wireOp",EDGE,"E13.bottom"),sQuery(id+"F15.wireOp",EDGE,"E13.top"),sQuery(id+"F15.wireOp",EDGE,"E13.left"),sQuery(id+"F15.wireOp",EDGE,"E13.right"),sQuery(id+"F15.wireOp",EDGE,"E14.bottom"),sQuery(id+"F15.wireOp",EDGE,"E14.top"),sQuery(id+"F15.wireOp",EDGE,"E14.left"),sQuery(id+"F15.wireOp",EDGE,"E14.right"),sQuery(id+"F15.wireOp",EDGE,"E15.MirrorCS"),sQuery(id+"F15.wireOp",EDGE,"E16.MirrorCS"),sQuery(id+"F15.wireOp",EDGE,"E17.MirrorCS"),sQuery(id+"F15.wireOp",EDGE,"E18.MirrorCS"),sQuery(id+"F15.wireOp",EDGE,"E19.MirrorCS"),sQuery(id+"F15.wireOp",EDGE,"E20.MirrorCS"),sQuery(id+"F15.wireOp",EDGE,"E21.MirrorCS"),sQuery(id+"F15.wireOp",EDGE,"E22.MirrorCS"),sQuery(id+"F15.wireOp",EDGE,"E23.MirrorCS"),sQuery(id+"F15.wireOp",EDGE,"E24.MirrorCS"),sQuery(id+"F15.wireOp",EDGE,"E25.MirrorCS"),sQuery(id+"F15.wireOp",EDGE,"E26.MirrorCS")])]}),"instanceName":"1"}),"instanceName":"1"}),"instanceName":"1"}),"instanceName":"1"}),"instanceName":"1"});
            var Q199;
            Q199=makeQuery(id+"F24.opPattern","COPY",BODY,{"derivedFrom":makeQuery(id+"F23.opPattern","COPY",BODY,{"derivedFrom":makeQuery(id+"F22.opPattern","COPY",BODY,{"derivedFrom":makeQuery(id+"F19.opPattern","COPY",BODY,{"derivedFrom":makeQuery(id+"F18.opPattern","COPY",BODY,{"derivedFrom":makeQuery(id+"F17.opPattern","COPY",BODY,{"derivedFrom":makeQuery(id+"F16.opExtrude","SWEPT_BODY",BODY,{"disambiguationData":[OSD([sQuery(id+"F15.wireOp",EDGE,"E13.bottom"),sQuery(id+"F15.wireOp",EDGE,"E13.top"),sQuery(id+"F15.wireOp",EDGE,"E13.left"),sQuery(id+"F15.wireOp",EDGE,"E13.right"),sQuery(id+"F15.wireOp",EDGE,"E14.bottom"),sQuery(id+"F15.wireOp",EDGE,"E14.top"),sQuery(id+"F15.wireOp",EDGE,"E14.left"),sQuery(id+"F15.wireOp",EDGE,"E14.right"),sQuery(id+"F15.wireOp",EDGE,"E15.MirrorCS"),sQuery(id+"F15.wireOp",EDGE,"E16.MirrorCS"),sQuery(id+"F15.wireOp",EDGE,"E17.MirrorCS"),sQuery(id+"F15.wireOp",EDGE,"E18.MirrorCS"),sQuery(id+"F15.wireOp",EDGE,"E19.MirrorCS"),sQuery(id+"F15.wireOp",EDGE,"E20.MirrorCS"),sQuery(id+"F15.wireOp",EDGE,"E21.MirrorCS"),sQuery(id+"F15.wireOp",EDGE,"E22.MirrorCS"),sQuery(id+"F15.wireOp",EDGE,"E23.MirrorCS"),sQuery(id+"F15.wireOp",EDGE,"E24.MirrorCS"),sQuery(id+"F15.wireOp",EDGE,"E25.MirrorCS"),sQuery(id+"F15.wireOp",EDGE,"E26.MirrorCS")])]}),"instanceName":"1"}),"instanceName":"1"}),"instanceName":"1"}),"instanceName":"1"}),"instanceName":"1"}),"instanceName":"1"});
            var Q200;
            Q200=makeQuery(id+"F24.opPattern","COPY",BODY,{"derivedFrom":makeQuery(id+"F23.opPattern","COPY",BODY,{"derivedFrom":makeQuery(id+"F22.opPattern","COPY",BODY,{"derivedFrom":makeQuery(id+"F20.opPattern","COPY",BODY,{"derivedFrom":makeQuery(id+"F16.opExtrude","SWEPT_BODY",BODY,{"disambiguationData":[OSD([sQuery(id+"F15.wireOp",EDGE,"E13.bottom"),sQuery(id+"F15.wireOp",EDGE,"E13.top"),sQuery(id+"F15.wireOp",EDGE,"E13.left"),sQuery(id+"F15.wireOp",EDGE,"E13.right"),sQuery(id+"F15.wireOp",EDGE,"E14.bottom"),sQuery(id+"F15.wireOp",EDGE,"E14.top"),sQuery(id+"F15.wireOp",EDGE,"E14.left"),sQuery(id+"F15.wireOp",EDGE,"E14.right"),sQuery(id+"F15.wireOp",EDGE,"E15.MirrorCS"),sQuery(id+"F15.wireOp",EDGE,"E16.MirrorCS"),sQuery(id+"F15.wireOp",EDGE,"E17.MirrorCS"),sQuery(id+"F15.wireOp",EDGE,"E18.MirrorCS"),sQuery(id+"F15.wireOp",EDGE,"E19.MirrorCS"),sQuery(id+"F15.wireOp",EDGE,"E20.MirrorCS"),sQuery(id+"F15.wireOp",EDGE,"E21.MirrorCS"),sQuery(id+"F15.wireOp",EDGE,"E22.MirrorCS"),sQuery(id+"F15.wireOp",EDGE,"E23.MirrorCS"),sQuery(id+"F15.wireOp",EDGE,"E24.MirrorCS"),sQuery(id+"F15.wireOp",EDGE,"E25.MirrorCS"),sQuery(id+"F15.wireOp",EDGE,"E26.MirrorCS")])]}),"instanceName":"1"}),"instanceName":"1"}),"instanceName":"1"}),"instanceName":"1"});
            var Q201;
            Q201=makeQuery(id+"F24.opPattern","COPY",BODY,{"derivedFrom":makeQuery(id+"F23.opPattern","COPY",BODY,{"derivedFrom":makeQuery(id+"F22.opPattern","COPY",BODY,{"derivedFrom":makeQuery(id+"F20.opPattern","COPY",BODY,{"derivedFrom":makeQuery(id+"F17.opPattern","COPY",BODY,{"derivedFrom":makeQuery(id+"F16.opExtrude","SWEPT_BODY",BODY,{"disambiguationData":[OSD([sQuery(id+"F15.wireOp",EDGE,"E13.bottom"),sQuery(id+"F15.wireOp",EDGE,"E13.top"),sQuery(id+"F15.wireOp",EDGE,"E13.left"),sQuery(id+"F15.wireOp",EDGE,"E13.right"),sQuery(id+"F15.wireOp",EDGE,"E14.bottom"),sQuery(id+"F15.wireOp",EDGE,"E14.top"),sQuery(id+"F15.wireOp",EDGE,"E14.left"),sQuery(id+"F15.wireOp",EDGE,"E14.right"),sQuery(id+"F15.wireOp",EDGE,"E15.MirrorCS"),sQuery(id+"F15.wireOp",EDGE,"E16.MirrorCS"),sQuery(id+"F15.wireOp",EDGE,"E17.MirrorCS"),sQuery(id+"F15.wireOp",EDGE,"E18.MirrorCS"),sQuery(id+"F15.wireOp",EDGE,"E19.MirrorCS"),sQuery(id+"F15.wireOp",EDGE,"E20.MirrorCS"),sQuery(id+"F15.wireOp",EDGE,"E21.MirrorCS"),sQuery(id+"F15.wireOp",EDGE,"E22.MirrorCS"),sQuery(id+"F15.wireOp",EDGE,"E23.MirrorCS"),sQuery(id+"F15.wireOp",EDGE,"E24.MirrorCS"),sQuery(id+"F15.wireOp",EDGE,"E25.MirrorCS"),sQuery(id+"F15.wireOp",EDGE,"E26.MirrorCS")])]}),"instanceName":"1"}),"instanceName":"1"}),"instanceName":"1"}),"instanceName":"1"}),"instanceName":"1"});
            var Q202;
            Q202=makeQuery(id+"F24.opPattern","COPY",BODY,{"derivedFrom":makeQuery(id+"F23.opPattern","COPY",BODY,{"derivedFrom":makeQuery(id+"F22.opPattern","COPY",BODY,{"derivedFrom":makeQuery(id+"F20.opPattern","COPY",BODY,{"derivedFrom":makeQuery(id+"F18.opPattern","COPY",BODY,{"derivedFrom":makeQuery(id+"F16.opExtrude","SWEPT_BODY",BODY,{"disambiguationData":[OSD([sQuery(id+"F15.wireOp",EDGE,"E13.bottom"),sQuery(id+"F15.wireOp",EDGE,"E13.top"),sQuery(id+"F15.wireOp",EDGE,"E13.left"),sQuery(id+"F15.wireOp",EDGE,"E13.right"),sQuery(id+"F15.wireOp",EDGE,"E14.bottom"),sQuery(id+"F15.wireOp",EDGE,"E14.top"),sQuery(id+"F15.wireOp",EDGE,"E14.left"),sQuery(id+"F15.wireOp",EDGE,"E14.right"),sQuery(id+"F15.wireOp",EDGE,"E15.MirrorCS"),sQuery(id+"F15.wireOp",EDGE,"E16.MirrorCS"),sQuery(id+"F15.wireOp",EDGE,"E17.MirrorCS"),sQuery(id+"F15.wireOp",EDGE,"E18.MirrorCS"),sQuery(id+"F15.wireOp",EDGE,"E19.MirrorCS"),sQuery(id+"F15.wireOp",EDGE,"E20.MirrorCS"),sQuery(id+"F15.wireOp",EDGE,"E21.MirrorCS"),sQuery(id+"F15.wireOp",EDGE,"E22.MirrorCS"),sQuery(id+"F15.wireOp",EDGE,"E23.MirrorCS"),sQuery(id+"F15.wireOp",EDGE,"E24.MirrorCS"),sQuery(id+"F15.wireOp",EDGE,"E25.MirrorCS"),sQuery(id+"F15.wireOp",EDGE,"E26.MirrorCS")])]}),"instanceName":"1"}),"instanceName":"1"}),"instanceName":"1"}),"instanceName":"1"}),"instanceName":"1"});
            var Q203;
            Q203=makeQuery(id+"F24.opPattern","COPY",BODY,{"derivedFrom":makeQuery(id+"F23.opPattern","COPY",BODY,{"derivedFrom":makeQuery(id+"F22.opPattern","COPY",BODY,{"derivedFrom":makeQuery(id+"F20.opPattern","COPY",BODY,{"derivedFrom":makeQuery(id+"F18.opPattern","COPY",BODY,{"derivedFrom":makeQuery(id+"F17.opPattern","COPY",BODY,{"derivedFrom":makeQuery(id+"F16.opExtrude","SWEPT_BODY",BODY,{"disambiguationData":[OSD([sQuery(id+"F15.wireOp",EDGE,"E13.bottom"),sQuery(id+"F15.wireOp",EDGE,"E13.top"),sQuery(id+"F15.wireOp",EDGE,"E13.left"),sQuery(id+"F15.wireOp",EDGE,"E13.right"),sQuery(id+"F15.wireOp",EDGE,"E14.bottom"),sQuery(id+"F15.wireOp",EDGE,"E14.top"),sQuery(id+"F15.wireOp",EDGE,"E14.left"),sQuery(id+"F15.wireOp",EDGE,"E14.right"),sQuery(id+"F15.wireOp",EDGE,"E15.MirrorCS"),sQuery(id+"F15.wireOp",EDGE,"E16.MirrorCS"),sQuery(id+"F15.wireOp",EDGE,"E17.MirrorCS"),sQuery(id+"F15.wireOp",EDGE,"E18.MirrorCS"),sQuery(id+"F15.wireOp",EDGE,"E19.MirrorCS"),sQuery(id+"F15.wireOp",EDGE,"E20.MirrorCS"),sQuery(id+"F15.wireOp",EDGE,"E21.MirrorCS"),sQuery(id+"F15.wireOp",EDGE,"E22.MirrorCS"),sQuery(id+"F15.wireOp",EDGE,"E23.MirrorCS"),sQuery(id+"F15.wireOp",EDGE,"E24.MirrorCS"),sQuery(id+"F15.wireOp",EDGE,"E25.MirrorCS"),sQuery(id+"F15.wireOp",EDGE,"E26.MirrorCS")])]}),"instanceName":"1"}),"instanceName":"1"}),"instanceName":"1"}),"instanceName":"1"}),"instanceName":"1"}),"instanceName":"1"});
            var Q204;
            Q204=makeQuery(id+"F24.opPattern","COPY",BODY,{"derivedFrom":makeQuery(id+"F23.opPattern","COPY",BODY,{"derivedFrom":makeQuery(id+"F22.opPattern","COPY",BODY,{"derivedFrom":makeQuery(id+"F20.opPattern","COPY",BODY,{"derivedFrom":makeQuery(id+"F19.opPattern","COPY",BODY,{"derivedFrom":makeQuery(id+"F16.opExtrude","SWEPT_BODY",BODY,{"disambiguationData":[OSD([sQuery(id+"F15.wireOp",EDGE,"E13.bottom"),sQuery(id+"F15.wireOp",EDGE,"E13.top"),sQuery(id+"F15.wireOp",EDGE,"E13.left"),sQuery(id+"F15.wireOp",EDGE,"E13.right"),sQuery(id+"F15.wireOp",EDGE,"E14.bottom"),sQuery(id+"F15.wireOp",EDGE,"E14.top"),sQuery(id+"F15.wireOp",EDGE,"E14.left"),sQuery(id+"F15.wireOp",EDGE,"E14.right"),sQuery(id+"F15.wireOp",EDGE,"E15.MirrorCS"),sQuery(id+"F15.wireOp",EDGE,"E16.MirrorCS"),sQuery(id+"F15.wireOp",EDGE,"E17.MirrorCS"),sQuery(id+"F15.wireOp",EDGE,"E18.MirrorCS"),sQuery(id+"F15.wireOp",EDGE,"E19.MirrorCS"),sQuery(id+"F15.wireOp",EDGE,"E20.MirrorCS"),sQuery(id+"F15.wireOp",EDGE,"E21.MirrorCS"),sQuery(id+"F15.wireOp",EDGE,"E22.MirrorCS"),sQuery(id+"F15.wireOp",EDGE,"E23.MirrorCS"),sQuery(id+"F15.wireOp",EDGE,"E24.MirrorCS"),sQuery(id+"F15.wireOp",EDGE,"E25.MirrorCS"),sQuery(id+"F15.wireOp",EDGE,"E26.MirrorCS")])]}),"instanceName":"1"}),"instanceName":"1"}),"instanceName":"1"}),"instanceName":"1"}),"instanceName":"1"});
            var Q205;
            Q205=makeQuery(id+"F24.opPattern","COPY",BODY,{"derivedFrom":makeQuery(id+"F23.opPattern","COPY",BODY,{"derivedFrom":makeQuery(id+"F22.opPattern","COPY",BODY,{"derivedFrom":makeQuery(id+"F20.opPattern","COPY",BODY,{"derivedFrom":makeQuery(id+"F19.opPattern","COPY",BODY,{"derivedFrom":makeQuery(id+"F17.opPattern","COPY",BODY,{"derivedFrom":makeQuery(id+"F16.opExtrude","SWEPT_BODY",BODY,{"disambiguationData":[OSD([sQuery(id+"F15.wireOp",EDGE,"E13.bottom"),sQuery(id+"F15.wireOp",EDGE,"E13.top"),sQuery(id+"F15.wireOp",EDGE,"E13.left"),sQuery(id+"F15.wireOp",EDGE,"E13.right"),sQuery(id+"F15.wireOp",EDGE,"E14.bottom"),sQuery(id+"F15.wireOp",EDGE,"E14.top"),sQuery(id+"F15.wireOp",EDGE,"E14.left"),sQuery(id+"F15.wireOp",EDGE,"E14.right"),sQuery(id+"F15.wireOp",EDGE,"E15.MirrorCS"),sQuery(id+"F15.wireOp",EDGE,"E16.MirrorCS"),sQuery(id+"F15.wireOp",EDGE,"E17.MirrorCS"),sQuery(id+"F15.wireOp",EDGE,"E18.MirrorCS"),sQuery(id+"F15.wireOp",EDGE,"E19.MirrorCS"),sQuery(id+"F15.wireOp",EDGE,"E20.MirrorCS"),sQuery(id+"F15.wireOp",EDGE,"E21.MirrorCS"),sQuery(id+"F15.wireOp",EDGE,"E22.MirrorCS"),sQuery(id+"F15.wireOp",EDGE,"E23.MirrorCS"),sQuery(id+"F15.wireOp",EDGE,"E24.MirrorCS"),sQuery(id+"F15.wireOp",EDGE,"E25.MirrorCS"),sQuery(id+"F15.wireOp",EDGE,"E26.MirrorCS")])]}),"instanceName":"1"}),"instanceName":"1"}),"instanceName":"1"}),"instanceName":"1"}),"instanceName":"1"}),"instanceName":"1"});
            var Q206;
            Q206=makeQuery(id+"F24.opPattern","COPY",BODY,{"derivedFrom":makeQuery(id+"F23.opPattern","COPY",BODY,{"derivedFrom":makeQuery(id+"F22.opPattern","COPY",BODY,{"derivedFrom":makeQuery(id+"F20.opPattern","COPY",BODY,{"derivedFrom":makeQuery(id+"F19.opPattern","COPY",BODY,{"derivedFrom":makeQuery(id+"F18.opPattern","COPY",BODY,{"derivedFrom":makeQuery(id+"F16.opExtrude","SWEPT_BODY",BODY,{"disambiguationData":[OSD([sQuery(id+"F15.wireOp",EDGE,"E13.bottom"),sQuery(id+"F15.wireOp",EDGE,"E13.top"),sQuery(id+"F15.wireOp",EDGE,"E13.left"),sQuery(id+"F15.wireOp",EDGE,"E13.right"),sQuery(id+"F15.wireOp",EDGE,"E14.bottom"),sQuery(id+"F15.wireOp",EDGE,"E14.top"),sQuery(id+"F15.wireOp",EDGE,"E14.left"),sQuery(id+"F15.wireOp",EDGE,"E14.right"),sQuery(id+"F15.wireOp",EDGE,"E15.MirrorCS"),sQuery(id+"F15.wireOp",EDGE,"E16.MirrorCS"),sQuery(id+"F15.wireOp",EDGE,"E17.MirrorCS"),sQuery(id+"F15.wireOp",EDGE,"E18.MirrorCS"),sQuery(id+"F15.wireOp",EDGE,"E19.MirrorCS"),sQuery(id+"F15.wireOp",EDGE,"E20.MirrorCS"),sQuery(id+"F15.wireOp",EDGE,"E21.MirrorCS"),sQuery(id+"F15.wireOp",EDGE,"E22.MirrorCS"),sQuery(id+"F15.wireOp",EDGE,"E23.MirrorCS"),sQuery(id+"F15.wireOp",EDGE,"E24.MirrorCS"),sQuery(id+"F15.wireOp",EDGE,"E25.MirrorCS"),sQuery(id+"F15.wireOp",EDGE,"E26.MirrorCS")])]}),"instanceName":"1"}),"instanceName":"1"}),"instanceName":"1"}),"instanceName":"1"}),"instanceName":"1"}),"instanceName":"1"});
            var Q207;
            Q207=makeQuery(id+"F24.opPattern","COPY",BODY,{"derivedFrom":makeQuery(id+"F23.opPattern","COPY",BODY,{"derivedFrom":makeQuery(id+"F22.opPattern","COPY",BODY,{"derivedFrom":makeQuery(id+"F20.opPattern","COPY",BODY,{"derivedFrom":makeQuery(id+"F19.opPattern","COPY",BODY,{"derivedFrom":makeQuery(id+"F18.opPattern","COPY",BODY,{"derivedFrom":makeQuery(id+"F17.opPattern","COPY",BODY,{"derivedFrom":makeQuery(id+"F16.opExtrude","SWEPT_BODY",BODY,{"disambiguationData":[OSD([sQuery(id+"F15.wireOp",EDGE,"E13.bottom"),sQuery(id+"F15.wireOp",EDGE,"E13.top"),sQuery(id+"F15.wireOp",EDGE,"E13.left"),sQuery(id+"F15.wireOp",EDGE,"E13.right"),sQuery(id+"F15.wireOp",EDGE,"E14.bottom"),sQuery(id+"F15.wireOp",EDGE,"E14.top"),sQuery(id+"F15.wireOp",EDGE,"E14.left"),sQuery(id+"F15.wireOp",EDGE,"E14.right"),sQuery(id+"F15.wireOp",EDGE,"E15.MirrorCS"),sQuery(id+"F15.wireOp",EDGE,"E16.MirrorCS"),sQuery(id+"F15.wireOp",EDGE,"E17.MirrorCS"),sQuery(id+"F15.wireOp",EDGE,"E18.MirrorCS"),sQuery(id+"F15.wireOp",EDGE,"E19.MirrorCS"),sQuery(id+"F15.wireOp",EDGE,"E20.MirrorCS"),sQuery(id+"F15.wireOp",EDGE,"E21.MirrorCS"),sQuery(id+"F15.wireOp",EDGE,"E22.MirrorCS"),sQuery(id+"F15.wireOp",EDGE,"E23.MirrorCS"),sQuery(id+"F15.wireOp",EDGE,"E24.MirrorCS"),sQuery(id+"F15.wireOp",EDGE,"E25.MirrorCS"),sQuery(id+"F15.wireOp",EDGE,"E26.MirrorCS")])]}),"instanceName":"1"}),"instanceName":"1"}),"instanceName":"1"}),"instanceName":"1"}),"instanceName":"1"}),"instanceName":"1"}),"instanceName":"1"});
            var Q208;
            Q208=makeQuery(id+"F24.opPattern","COPY",BODY,{"derivedFrom":makeQuery(id+"F23.opPattern","COPY",BODY,{"derivedFrom":makeQuery(id+"F22.opPattern","COPY",BODY,{"derivedFrom":makeQuery(id+"F21.opPattern","COPY",BODY,{"derivedFrom":makeQuery(id+"F16.opExtrude","SWEPT_BODY",BODY,{"disambiguationData":[OSD([sQuery(id+"F15.wireOp",EDGE,"E13.bottom"),sQuery(id+"F15.wireOp",EDGE,"E13.top"),sQuery(id+"F15.wireOp",EDGE,"E13.left"),sQuery(id+"F15.wireOp",EDGE,"E13.right"),sQuery(id+"F15.wireOp",EDGE,"E14.bottom"),sQuery(id+"F15.wireOp",EDGE,"E14.top"),sQuery(id+"F15.wireOp",EDGE,"E14.left"),sQuery(id+"F15.wireOp",EDGE,"E14.right"),sQuery(id+"F15.wireOp",EDGE,"E15.MirrorCS"),sQuery(id+"F15.wireOp",EDGE,"E16.MirrorCS"),sQuery(id+"F15.wireOp",EDGE,"E17.MirrorCS"),sQuery(id+"F15.wireOp",EDGE,"E18.MirrorCS"),sQuery(id+"F15.wireOp",EDGE,"E19.MirrorCS"),sQuery(id+"F15.wireOp",EDGE,"E20.MirrorCS"),sQuery(id+"F15.wireOp",EDGE,"E21.MirrorCS"),sQuery(id+"F15.wireOp",EDGE,"E22.MirrorCS"),sQuery(id+"F15.wireOp",EDGE,"E23.MirrorCS"),sQuery(id+"F15.wireOp",EDGE,"E24.MirrorCS"),sQuery(id+"F15.wireOp",EDGE,"E25.MirrorCS"),sQuery(id+"F15.wireOp",EDGE,"E26.MirrorCS")])]}),"instanceName":"1"}),"instanceName":"1"}),"instanceName":"1"}),"instanceName":"1"});
            var Q209;
            Q209=makeQuery(id+"F24.opPattern","COPY",BODY,{"derivedFrom":makeQuery(id+"F23.opPattern","COPY",BODY,{"derivedFrom":makeQuery(id+"F22.opPattern","COPY",BODY,{"derivedFrom":makeQuery(id+"F21.opPattern","COPY",BODY,{"derivedFrom":makeQuery(id+"F17.opPattern","COPY",BODY,{"derivedFrom":makeQuery(id+"F16.opExtrude","SWEPT_BODY",BODY,{"disambiguationData":[OSD([sQuery(id+"F15.wireOp",EDGE,"E13.bottom"),sQuery(id+"F15.wireOp",EDGE,"E13.top"),sQuery(id+"F15.wireOp",EDGE,"E13.left"),sQuery(id+"F15.wireOp",EDGE,"E13.right"),sQuery(id+"F15.wireOp",EDGE,"E14.bottom"),sQuery(id+"F15.wireOp",EDGE,"E14.top"),sQuery(id+"F15.wireOp",EDGE,"E14.left"),sQuery(id+"F15.wireOp",EDGE,"E14.right"),sQuery(id+"F15.wireOp",EDGE,"E15.MirrorCS"),sQuery(id+"F15.wireOp",EDGE,"E16.MirrorCS"),sQuery(id+"F15.wireOp",EDGE,"E17.MirrorCS"),sQuery(id+"F15.wireOp",EDGE,"E18.MirrorCS"),sQuery(id+"F15.wireOp",EDGE,"E19.MirrorCS"),sQuery(id+"F15.wireOp",EDGE,"E20.MirrorCS"),sQuery(id+"F15.wireOp",EDGE,"E21.MirrorCS"),sQuery(id+"F15.wireOp",EDGE,"E22.MirrorCS"),sQuery(id+"F15.wireOp",EDGE,"E23.MirrorCS"),sQuery(id+"F15.wireOp",EDGE,"E24.MirrorCS"),sQuery(id+"F15.wireOp",EDGE,"E25.MirrorCS"),sQuery(id+"F15.wireOp",EDGE,"E26.MirrorCS")])]}),"instanceName":"1"}),"instanceName":"1"}),"instanceName":"1"}),"instanceName":"1"}),"instanceName":"1"});
            var Q210;
            Q210=makeQuery(id+"F24.opPattern","COPY",BODY,{"derivedFrom":makeQuery(id+"F23.opPattern","COPY",BODY,{"derivedFrom":makeQuery(id+"F22.opPattern","COPY",BODY,{"derivedFrom":makeQuery(id+"F21.opPattern","COPY",BODY,{"derivedFrom":makeQuery(id+"F18.opPattern","COPY",BODY,{"derivedFrom":makeQuery(id+"F16.opExtrude","SWEPT_BODY",BODY,{"disambiguationData":[OSD([sQuery(id+"F15.wireOp",EDGE,"E13.bottom"),sQuery(id+"F15.wireOp",EDGE,"E13.top"),sQuery(id+"F15.wireOp",EDGE,"E13.left"),sQuery(id+"F15.wireOp",EDGE,"E13.right"),sQuery(id+"F15.wireOp",EDGE,"E14.bottom"),sQuery(id+"F15.wireOp",EDGE,"E14.top"),sQuery(id+"F15.wireOp",EDGE,"E14.left"),sQuery(id+"F15.wireOp",EDGE,"E14.right"),sQuery(id+"F15.wireOp",EDGE,"E15.MirrorCS"),sQuery(id+"F15.wireOp",EDGE,"E16.MirrorCS"),sQuery(id+"F15.wireOp",EDGE,"E17.MirrorCS"),sQuery(id+"F15.wireOp",EDGE,"E18.MirrorCS"),sQuery(id+"F15.wireOp",EDGE,"E19.MirrorCS"),sQuery(id+"F15.wireOp",EDGE,"E20.MirrorCS"),sQuery(id+"F15.wireOp",EDGE,"E21.MirrorCS"),sQuery(id+"F15.wireOp",EDGE,"E22.MirrorCS"),sQuery(id+"F15.wireOp",EDGE,"E23.MirrorCS"),sQuery(id+"F15.wireOp",EDGE,"E24.MirrorCS"),sQuery(id+"F15.wireOp",EDGE,"E25.MirrorCS"),sQuery(id+"F15.wireOp",EDGE,"E26.MirrorCS")])]}),"instanceName":"1"}),"instanceName":"1"}),"instanceName":"1"}),"instanceName":"1"}),"instanceName":"1"});
            var Q211;
            Q211=makeQuery(id+"F24.opPattern","COPY",BODY,{"derivedFrom":makeQuery(id+"F23.opPattern","COPY",BODY,{"derivedFrom":makeQuery(id+"F22.opPattern","COPY",BODY,{"derivedFrom":makeQuery(id+"F21.opPattern","COPY",BODY,{"derivedFrom":makeQuery(id+"F18.opPattern","COPY",BODY,{"derivedFrom":makeQuery(id+"F17.opPattern","COPY",BODY,{"derivedFrom":makeQuery(id+"F16.opExtrude","SWEPT_BODY",BODY,{"disambiguationData":[OSD([sQuery(id+"F15.wireOp",EDGE,"E13.bottom"),sQuery(id+"F15.wireOp",EDGE,"E13.top"),sQuery(id+"F15.wireOp",EDGE,"E13.left"),sQuery(id+"F15.wireOp",EDGE,"E13.right"),sQuery(id+"F15.wireOp",EDGE,"E14.bottom"),sQuery(id+"F15.wireOp",EDGE,"E14.top"),sQuery(id+"F15.wireOp",EDGE,"E14.left"),sQuery(id+"F15.wireOp",EDGE,"E14.right"),sQuery(id+"F15.wireOp",EDGE,"E15.MirrorCS"),sQuery(id+"F15.wireOp",EDGE,"E16.MirrorCS"),sQuery(id+"F15.wireOp",EDGE,"E17.MirrorCS"),sQuery(id+"F15.wireOp",EDGE,"E18.MirrorCS"),sQuery(id+"F15.wireOp",EDGE,"E19.MirrorCS"),sQuery(id+"F15.wireOp",EDGE,"E20.MirrorCS"),sQuery(id+"F15.wireOp",EDGE,"E21.MirrorCS"),sQuery(id+"F15.wireOp",EDGE,"E22.MirrorCS"),sQuery(id+"F15.wireOp",EDGE,"E23.MirrorCS"),sQuery(id+"F15.wireOp",EDGE,"E24.MirrorCS"),sQuery(id+"F15.wireOp",EDGE,"E25.MirrorCS"),sQuery(id+"F15.wireOp",EDGE,"E26.MirrorCS")])]}),"instanceName":"1"}),"instanceName":"1"}),"instanceName":"1"}),"instanceName":"1"}),"instanceName":"1"}),"instanceName":"1"});
            var Q212;
            Q212=makeQuery(id+"F24.opPattern","COPY",BODY,{"derivedFrom":makeQuery(id+"F23.opPattern","COPY",BODY,{"derivedFrom":makeQuery(id+"F22.opPattern","COPY",BODY,{"derivedFrom":makeQuery(id+"F21.opPattern","COPY",BODY,{"derivedFrom":makeQuery(id+"F19.opPattern","COPY",BODY,{"derivedFrom":makeQuery(id+"F16.opExtrude","SWEPT_BODY",BODY,{"disambiguationData":[OSD([sQuery(id+"F15.wireOp",EDGE,"E13.bottom"),sQuery(id+"F15.wireOp",EDGE,"E13.top"),sQuery(id+"F15.wireOp",EDGE,"E13.left"),sQuery(id+"F15.wireOp",EDGE,"E13.right"),sQuery(id+"F15.wireOp",EDGE,"E14.bottom"),sQuery(id+"F15.wireOp",EDGE,"E14.top"),sQuery(id+"F15.wireOp",EDGE,"E14.left"),sQuery(id+"F15.wireOp",EDGE,"E14.right"),sQuery(id+"F15.wireOp",EDGE,"E15.MirrorCS"),sQuery(id+"F15.wireOp",EDGE,"E16.MirrorCS"),sQuery(id+"F15.wireOp",EDGE,"E17.MirrorCS"),sQuery(id+"F15.wireOp",EDGE,"E18.MirrorCS"),sQuery(id+"F15.wireOp",EDGE,"E19.MirrorCS"),sQuery(id+"F15.wireOp",EDGE,"E20.MirrorCS"),sQuery(id+"F15.wireOp",EDGE,"E21.MirrorCS"),sQuery(id+"F15.wireOp",EDGE,"E22.MirrorCS"),sQuery(id+"F15.wireOp",EDGE,"E23.MirrorCS"),sQuery(id+"F15.wireOp",EDGE,"E24.MirrorCS"),sQuery(id+"F15.wireOp",EDGE,"E25.MirrorCS"),sQuery(id+"F15.wireOp",EDGE,"E26.MirrorCS")])]}),"instanceName":"1"}),"instanceName":"1"}),"instanceName":"1"}),"instanceName":"1"}),"instanceName":"1"});
            var Q213;
            Q213=makeQuery(id+"F24.opPattern","COPY",BODY,{"derivedFrom":makeQuery(id+"F23.opPattern","COPY",BODY,{"derivedFrom":makeQuery(id+"F22.opPattern","COPY",BODY,{"derivedFrom":makeQuery(id+"F21.opPattern","COPY",BODY,{"derivedFrom":makeQuery(id+"F19.opPattern","COPY",BODY,{"derivedFrom":makeQuery(id+"F17.opPattern","COPY",BODY,{"derivedFrom":makeQuery(id+"F16.opExtrude","SWEPT_BODY",BODY,{"disambiguationData":[OSD([sQuery(id+"F15.wireOp",EDGE,"E13.bottom"),sQuery(id+"F15.wireOp",EDGE,"E13.top"),sQuery(id+"F15.wireOp",EDGE,"E13.left"),sQuery(id+"F15.wireOp",EDGE,"E13.right"),sQuery(id+"F15.wireOp",EDGE,"E14.bottom"),sQuery(id+"F15.wireOp",EDGE,"E14.top"),sQuery(id+"F15.wireOp",EDGE,"E14.left"),sQuery(id+"F15.wireOp",EDGE,"E14.right"),sQuery(id+"F15.wireOp",EDGE,"E15.MirrorCS"),sQuery(id+"F15.wireOp",EDGE,"E16.MirrorCS"),sQuery(id+"F15.wireOp",EDGE,"E17.MirrorCS"),sQuery(id+"F15.wireOp",EDGE,"E18.MirrorCS"),sQuery(id+"F15.wireOp",EDGE,"E19.MirrorCS"),sQuery(id+"F15.wireOp",EDGE,"E20.MirrorCS"),sQuery(id+"F15.wireOp",EDGE,"E21.MirrorCS"),sQuery(id+"F15.wireOp",EDGE,"E22.MirrorCS"),sQuery(id+"F15.wireOp",EDGE,"E23.MirrorCS"),sQuery(id+"F15.wireOp",EDGE,"E24.MirrorCS"),sQuery(id+"F15.wireOp",EDGE,"E25.MirrorCS"),sQuery(id+"F15.wireOp",EDGE,"E26.MirrorCS")])]}),"instanceName":"1"}),"instanceName":"1"}),"instanceName":"1"}),"instanceName":"1"}),"instanceName":"1"}),"instanceName":"1"});
            var Q214;
            Q214=makeQuery(id+"F24.opPattern","COPY",BODY,{"derivedFrom":makeQuery(id+"F23.opPattern","COPY",BODY,{"derivedFrom":makeQuery(id+"F22.opPattern","COPY",BODY,{"derivedFrom":makeQuery(id+"F21.opPattern","COPY",BODY,{"derivedFrom":makeQuery(id+"F19.opPattern","COPY",BODY,{"derivedFrom":makeQuery(id+"F18.opPattern","COPY",BODY,{"derivedFrom":makeQuery(id+"F16.opExtrude","SWEPT_BODY",BODY,{"disambiguationData":[OSD([sQuery(id+"F15.wireOp",EDGE,"E13.bottom"),sQuery(id+"F15.wireOp",EDGE,"E13.top"),sQuery(id+"F15.wireOp",EDGE,"E13.left"),sQuery(id+"F15.wireOp",EDGE,"E13.right"),sQuery(id+"F15.wireOp",EDGE,"E14.bottom"),sQuery(id+"F15.wireOp",EDGE,"E14.top"),sQuery(id+"F15.wireOp",EDGE,"E14.left"),sQuery(id+"F15.wireOp",EDGE,"E14.right"),sQuery(id+"F15.wireOp",EDGE,"E15.MirrorCS"),sQuery(id+"F15.wireOp",EDGE,"E16.MirrorCS"),sQuery(id+"F15.wireOp",EDGE,"E17.MirrorCS"),sQuery(id+"F15.wireOp",EDGE,"E18.MirrorCS"),sQuery(id+"F15.wireOp",EDGE,"E19.MirrorCS"),sQuery(id+"F15.wireOp",EDGE,"E20.MirrorCS"),sQuery(id+"F15.wireOp",EDGE,"E21.MirrorCS"),sQuery(id+"F15.wireOp",EDGE,"E22.MirrorCS"),sQuery(id+"F15.wireOp",EDGE,"E23.MirrorCS"),sQuery(id+"F15.wireOp",EDGE,"E24.MirrorCS"),sQuery(id+"F15.wireOp",EDGE,"E25.MirrorCS"),sQuery(id+"F15.wireOp",EDGE,"E26.MirrorCS")])]}),"instanceName":"1"}),"instanceName":"1"}),"instanceName":"1"}),"instanceName":"1"}),"instanceName":"1"}),"instanceName":"1"});
            var Q215;
            Q215=makeQuery(id+"F24.opPattern","COPY",BODY,{"derivedFrom":makeQuery(id+"F23.opPattern","COPY",BODY,{"derivedFrom":makeQuery(id+"F22.opPattern","COPY",BODY,{"derivedFrom":makeQuery(id+"F21.opPattern","COPY",BODY,{"derivedFrom":makeQuery(id+"F19.opPattern","COPY",BODY,{"derivedFrom":makeQuery(id+"F18.opPattern","COPY",BODY,{"derivedFrom":makeQuery(id+"F17.opPattern","COPY",BODY,{"derivedFrom":makeQuery(id+"F16.opExtrude","SWEPT_BODY",BODY,{"disambiguationData":[OSD([sQuery(id+"F15.wireOp",EDGE,"E13.bottom"),sQuery(id+"F15.wireOp",EDGE,"E13.top"),sQuery(id+"F15.wireOp",EDGE,"E13.left"),sQuery(id+"F15.wireOp",EDGE,"E13.right"),sQuery(id+"F15.wireOp",EDGE,"E14.bottom"),sQuery(id+"F15.wireOp",EDGE,"E14.top"),sQuery(id+"F15.wireOp",EDGE,"E14.left"),sQuery(id+"F15.wireOp",EDGE,"E14.right"),sQuery(id+"F15.wireOp",EDGE,"E15.MirrorCS"),sQuery(id+"F15.wireOp",EDGE,"E16.MirrorCS"),sQuery(id+"F15.wireOp",EDGE,"E17.MirrorCS"),sQuery(id+"F15.wireOp",EDGE,"E18.MirrorCS"),sQuery(id+"F15.wireOp",EDGE,"E19.MirrorCS"),sQuery(id+"F15.wireOp",EDGE,"E20.MirrorCS"),sQuery(id+"F15.wireOp",EDGE,"E21.MirrorCS"),sQuery(id+"F15.wireOp",EDGE,"E22.MirrorCS"),sQuery(id+"F15.wireOp",EDGE,"E23.MirrorCS"),sQuery(id+"F15.wireOp",EDGE,"E24.MirrorCS"),sQuery(id+"F15.wireOp",EDGE,"E25.MirrorCS"),sQuery(id+"F15.wireOp",EDGE,"E26.MirrorCS")])]}),"instanceName":"1"}),"instanceName":"1"}),"instanceName":"1"}),"instanceName":"1"}),"instanceName":"1"}),"instanceName":"1"}),"instanceName":"1"});
            var Q216;
            Q216=makeQuery(id+"F16.opExtrude","SWEPT_BODY",BODY,{"disambiguationData":[OSD([sQuery(id+"F15.wireOp",EDGE,"E13.bottom"),sQuery(id+"F15.wireOp",EDGE,"E13.top"),sQuery(id+"F15.wireOp",EDGE,"E13.left"),sQuery(id+"F15.wireOp",EDGE,"E13.right"),sQuery(id+"F15.wireOp",EDGE,"E14.bottom"),sQuery(id+"F15.wireOp",EDGE,"E14.top"),sQuery(id+"F15.wireOp",EDGE,"E14.left"),sQuery(id+"F15.wireOp",EDGE,"E14.right"),sQuery(id+"F15.wireOp",EDGE,"E15.MirrorCS"),sQuery(id+"F15.wireOp",EDGE,"E16.MirrorCS"),sQuery(id+"F15.wireOp",EDGE,"E17.MirrorCS"),sQuery(id+"F15.wireOp",EDGE,"E18.MirrorCS"),sQuery(id+"F15.wireOp",EDGE,"E19.MirrorCS"),sQuery(id+"F15.wireOp",EDGE,"E20.MirrorCS"),sQuery(id+"F15.wireOp",EDGE,"E21.MirrorCS"),sQuery(id+"F15.wireOp",EDGE,"E22.MirrorCS"),sQuery(id+"F15.wireOp",EDGE,"E23.MirrorCS"),sQuery(id+"F15.wireOp",EDGE,"E24.MirrorCS"),sQuery(id+"F15.wireOp",EDGE,"E25.MirrorCS"),sQuery(id+"F15.wireOp",EDGE,"E26.MirrorCS")])]});
            var Q217;
            Q217=makeQuery(id+"F17.opPattern","COPY",BODY,{"derivedFrom":makeQuery(id+"F16.opExtrude","SWEPT_BODY",BODY,{"disambiguationData":[OSD([sQuery(id+"F15.wireOp",EDGE,"E13.bottom"),sQuery(id+"F15.wireOp",EDGE,"E13.top"),sQuery(id+"F15.wireOp",EDGE,"E13.left"),sQuery(id+"F15.wireOp",EDGE,"E13.right"),sQuery(id+"F15.wireOp",EDGE,"E14.bottom"),sQuery(id+"F15.wireOp",EDGE,"E14.top"),sQuery(id+"F15.wireOp",EDGE,"E14.left"),sQuery(id+"F15.wireOp",EDGE,"E14.right"),sQuery(id+"F15.wireOp",EDGE,"E15.MirrorCS"),sQuery(id+"F15.wireOp",EDGE,"E16.MirrorCS"),sQuery(id+"F15.wireOp",EDGE,"E17.MirrorCS"),sQuery(id+"F15.wireOp",EDGE,"E18.MirrorCS"),sQuery(id+"F15.wireOp",EDGE,"E19.MirrorCS"),sQuery(id+"F15.wireOp",EDGE,"E20.MirrorCS"),sQuery(id+"F15.wireOp",EDGE,"E21.MirrorCS"),sQuery(id+"F15.wireOp",EDGE,"E22.MirrorCS"),sQuery(id+"F15.wireOp",EDGE,"E23.MirrorCS"),sQuery(id+"F15.wireOp",EDGE,"E24.MirrorCS"),sQuery(id+"F15.wireOp",EDGE,"E25.MirrorCS"),sQuery(id+"F15.wireOp",EDGE,"E26.MirrorCS")])]}),"instanceName":"1"});
            var Q218;
            Q218=makeQuery(id+"F18.opPattern","COPY",BODY,{"derivedFrom":makeQuery(id+"F16.opExtrude","SWEPT_BODY",BODY,{"disambiguationData":[OSD([sQuery(id+"F15.wireOp",EDGE,"E13.bottom"),sQuery(id+"F15.wireOp",EDGE,"E13.top"),sQuery(id+"F15.wireOp",EDGE,"E13.left"),sQuery(id+"F15.wireOp",EDGE,"E13.right"),sQuery(id+"F15.wireOp",EDGE,"E14.bottom"),sQuery(id+"F15.wireOp",EDGE,"E14.top"),sQuery(id+"F15.wireOp",EDGE,"E14.left"),sQuery(id+"F15.wireOp",EDGE,"E14.right"),sQuery(id+"F15.wireOp",EDGE,"E15.MirrorCS"),sQuery(id+"F15.wireOp",EDGE,"E16.MirrorCS"),sQuery(id+"F15.wireOp",EDGE,"E17.MirrorCS"),sQuery(id+"F15.wireOp",EDGE,"E18.MirrorCS"),sQuery(id+"F15.wireOp",EDGE,"E19.MirrorCS"),sQuery(id+"F15.wireOp",EDGE,"E20.MirrorCS"),sQuery(id+"F15.wireOp",EDGE,"E21.MirrorCS"),sQuery(id+"F15.wireOp",EDGE,"E22.MirrorCS"),sQuery(id+"F15.wireOp",EDGE,"E23.MirrorCS"),sQuery(id+"F15.wireOp",EDGE,"E24.MirrorCS"),sQuery(id+"F15.wireOp",EDGE,"E25.MirrorCS"),sQuery(id+"F15.wireOp",EDGE,"E26.MirrorCS")])]}),"instanceName":"1"});
            var Q219;
            Q219=makeQuery(id+"F18.opPattern","COPY",BODY,{"derivedFrom":makeQuery(id+"F17.opPattern","COPY",BODY,{"derivedFrom":makeQuery(id+"F16.opExtrude","SWEPT_BODY",BODY,{"disambiguationData":[OSD([sQuery(id+"F15.wireOp",EDGE,"E13.bottom"),sQuery(id+"F15.wireOp",EDGE,"E13.top"),sQuery(id+"F15.wireOp",EDGE,"E13.left"),sQuery(id+"F15.wireOp",EDGE,"E13.right"),sQuery(id+"F15.wireOp",EDGE,"E14.bottom"),sQuery(id+"F15.wireOp",EDGE,"E14.top"),sQuery(id+"F15.wireOp",EDGE,"E14.left"),sQuery(id+"F15.wireOp",EDGE,"E14.right"),sQuery(id+"F15.wireOp",EDGE,"E15.MirrorCS"),sQuery(id+"F15.wireOp",EDGE,"E16.MirrorCS"),sQuery(id+"F15.wireOp",EDGE,"E17.MirrorCS"),sQuery(id+"F15.wireOp",EDGE,"E18.MirrorCS"),sQuery(id+"F15.wireOp",EDGE,"E19.MirrorCS"),sQuery(id+"F15.wireOp",EDGE,"E20.MirrorCS"),sQuery(id+"F15.wireOp",EDGE,"E21.MirrorCS"),sQuery(id+"F15.wireOp",EDGE,"E22.MirrorCS"),sQuery(id+"F15.wireOp",EDGE,"E23.MirrorCS"),sQuery(id+"F15.wireOp",EDGE,"E24.MirrorCS"),sQuery(id+"F15.wireOp",EDGE,"E25.MirrorCS"),sQuery(id+"F15.wireOp",EDGE,"E26.MirrorCS")])]}),"instanceName":"1"}),"instanceName":"1"});
            var Q220;
            Q220=makeQuery(id+"F22.opPattern","COPY",BODY,{"derivedFrom":makeQuery(id+"F16.opExtrude","SWEPT_BODY",BODY,{"disambiguationData":[OSD([sQuery(id+"F15.wireOp",EDGE,"E13.bottom"),sQuery(id+"F15.wireOp",EDGE,"E13.top"),sQuery(id+"F15.wireOp",EDGE,"E13.left"),sQuery(id+"F15.wireOp",EDGE,"E13.right"),sQuery(id+"F15.wireOp",EDGE,"E14.bottom"),sQuery(id+"F15.wireOp",EDGE,"E14.top"),sQuery(id+"F15.wireOp",EDGE,"E14.left"),sQuery(id+"F15.wireOp",EDGE,"E14.right"),sQuery(id+"F15.wireOp",EDGE,"E15.MirrorCS"),sQuery(id+"F15.wireOp",EDGE,"E16.MirrorCS"),sQuery(id+"F15.wireOp",EDGE,"E17.MirrorCS"),sQuery(id+"F15.wireOp",EDGE,"E18.MirrorCS"),sQuery(id+"F15.wireOp",EDGE,"E19.MirrorCS"),sQuery(id+"F15.wireOp",EDGE,"E20.MirrorCS"),sQuery(id+"F15.wireOp",EDGE,"E21.MirrorCS"),sQuery(id+"F15.wireOp",EDGE,"E22.MirrorCS"),sQuery(id+"F15.wireOp",EDGE,"E23.MirrorCS"),sQuery(id+"F15.wireOp",EDGE,"E24.MirrorCS"),sQuery(id+"F15.wireOp",EDGE,"E25.MirrorCS"),sQuery(id+"F15.wireOp",EDGE,"E26.MirrorCS")])]}),"instanceName":"1"});
            var Q221;
            Q221=makeQuery(id+"F22.opPattern","COPY",BODY,{"derivedFrom":makeQuery(id+"F17.opPattern","COPY",BODY,{"derivedFrom":makeQuery(id+"F16.opExtrude","SWEPT_BODY",BODY,{"disambiguationData":[OSD([sQuery(id+"F15.wireOp",EDGE,"E13.bottom"),sQuery(id+"F15.wireOp",EDGE,"E13.top"),sQuery(id+"F15.wireOp",EDGE,"E13.left"),sQuery(id+"F15.wireOp",EDGE,"E13.right"),sQuery(id+"F15.wireOp",EDGE,"E14.bottom"),sQuery(id+"F15.wireOp",EDGE,"E14.top"),sQuery(id+"F15.wireOp",EDGE,"E14.left"),sQuery(id+"F15.wireOp",EDGE,"E14.right"),sQuery(id+"F15.wireOp",EDGE,"E15.MirrorCS"),sQuery(id+"F15.wireOp",EDGE,"E16.MirrorCS"),sQuery(id+"F15.wireOp",EDGE,"E17.MirrorCS"),sQuery(id+"F15.wireOp",EDGE,"E18.MirrorCS"),sQuery(id+"F15.wireOp",EDGE,"E19.MirrorCS"),sQuery(id+"F15.wireOp",EDGE,"E20.MirrorCS"),sQuery(id+"F15.wireOp",EDGE,"E21.MirrorCS"),sQuery(id+"F15.wireOp",EDGE,"E22.MirrorCS"),sQuery(id+"F15.wireOp",EDGE,"E23.MirrorCS"),sQuery(id+"F15.wireOp",EDGE,"E24.MirrorCS"),sQuery(id+"F15.wireOp",EDGE,"E25.MirrorCS"),sQuery(id+"F15.wireOp",EDGE,"E26.MirrorCS")])]}),"instanceName":"1"}),"instanceName":"1"});
            var Q222;
            Q222=makeQuery(id+"F22.opPattern","COPY",BODY,{"derivedFrom":makeQuery(id+"F18.opPattern","COPY",BODY,{"derivedFrom":makeQuery(id+"F16.opExtrude","SWEPT_BODY",BODY,{"disambiguationData":[OSD([sQuery(id+"F15.wireOp",EDGE,"E13.bottom"),sQuery(id+"F15.wireOp",EDGE,"E13.top"),sQuery(id+"F15.wireOp",EDGE,"E13.left"),sQuery(id+"F15.wireOp",EDGE,"E13.right"),sQuery(id+"F15.wireOp",EDGE,"E14.bottom"),sQuery(id+"F15.wireOp",EDGE,"E14.top"),sQuery(id+"F15.wireOp",EDGE,"E14.left"),sQuery(id+"F15.wireOp",EDGE,"E14.right"),sQuery(id+"F15.wireOp",EDGE,"E15.MirrorCS"),sQuery(id+"F15.wireOp",EDGE,"E16.MirrorCS"),sQuery(id+"F15.wireOp",EDGE,"E17.MirrorCS"),sQuery(id+"F15.wireOp",EDGE,"E18.MirrorCS"),sQuery(id+"F15.wireOp",EDGE,"E19.MirrorCS"),sQuery(id+"F15.wireOp",EDGE,"E20.MirrorCS"),sQuery(id+"F15.wireOp",EDGE,"E21.MirrorCS"),sQuery(id+"F15.wireOp",EDGE,"E22.MirrorCS"),sQuery(id+"F15.wireOp",EDGE,"E23.MirrorCS"),sQuery(id+"F15.wireOp",EDGE,"E24.MirrorCS"),sQuery(id+"F15.wireOp",EDGE,"E25.MirrorCS"),sQuery(id+"F15.wireOp",EDGE,"E26.MirrorCS")])]}),"instanceName":"1"}),"instanceName":"1"});
            var Q223;
            Q223=makeQuery(id+"F22.opPattern","COPY",BODY,{"derivedFrom":makeQuery(id+"F18.opPattern","COPY",BODY,{"derivedFrom":makeQuery(id+"F17.opPattern","COPY",BODY,{"derivedFrom":makeQuery(id+"F16.opExtrude","SWEPT_BODY",BODY,{"disambiguationData":[OSD([sQuery(id+"F15.wireOp",EDGE,"E13.bottom"),sQuery(id+"F15.wireOp",EDGE,"E13.top"),sQuery(id+"F15.wireOp",EDGE,"E13.left"),sQuery(id+"F15.wireOp",EDGE,"E13.right"),sQuery(id+"F15.wireOp",EDGE,"E14.bottom"),sQuery(id+"F15.wireOp",EDGE,"E14.top"),sQuery(id+"F15.wireOp",EDGE,"E14.left"),sQuery(id+"F15.wireOp",EDGE,"E14.right"),sQuery(id+"F15.wireOp",EDGE,"E15.MirrorCS"),sQuery(id+"F15.wireOp",EDGE,"E16.MirrorCS"),sQuery(id+"F15.wireOp",EDGE,"E17.MirrorCS"),sQuery(id+"F15.wireOp",EDGE,"E18.MirrorCS"),sQuery(id+"F15.wireOp",EDGE,"E19.MirrorCS"),sQuery(id+"F15.wireOp",EDGE,"E20.MirrorCS"),sQuery(id+"F15.wireOp",EDGE,"E21.MirrorCS"),sQuery(id+"F15.wireOp",EDGE,"E22.MirrorCS"),sQuery(id+"F15.wireOp",EDGE,"E23.MirrorCS"),sQuery(id+"F15.wireOp",EDGE,"E24.MirrorCS"),sQuery(id+"F15.wireOp",EDGE,"E25.MirrorCS"),sQuery(id+"F15.wireOp",EDGE,"E26.MirrorCS")])]}),"instanceName":"1"}),"instanceName":"1"}),"instanceName":"1"});
            var Q224;
            Q224=makeQuery(id+"F23.opPattern","COPY",BODY,{"derivedFrom":makeQuery(id+"F16.opExtrude","SWEPT_BODY",BODY,{"disambiguationData":[OSD([sQuery(id+"F15.wireOp",EDGE,"E13.bottom"),sQuery(id+"F15.wireOp",EDGE,"E13.top"),sQuery(id+"F15.wireOp",EDGE,"E13.left"),sQuery(id+"F15.wireOp",EDGE,"E13.right"),sQuery(id+"F15.wireOp",EDGE,"E14.bottom"),sQuery(id+"F15.wireOp",EDGE,"E14.top"),sQuery(id+"F15.wireOp",EDGE,"E14.left"),sQuery(id+"F15.wireOp",EDGE,"E14.right"),sQuery(id+"F15.wireOp",EDGE,"E15.MirrorCS"),sQuery(id+"F15.wireOp",EDGE,"E16.MirrorCS"),sQuery(id+"F15.wireOp",EDGE,"E17.MirrorCS"),sQuery(id+"F15.wireOp",EDGE,"E18.MirrorCS"),sQuery(id+"F15.wireOp",EDGE,"E19.MirrorCS"),sQuery(id+"F15.wireOp",EDGE,"E20.MirrorCS"),sQuery(id+"F15.wireOp",EDGE,"E21.MirrorCS"),sQuery(id+"F15.wireOp",EDGE,"E22.MirrorCS"),sQuery(id+"F15.wireOp",EDGE,"E23.MirrorCS"),sQuery(id+"F15.wireOp",EDGE,"E24.MirrorCS"),sQuery(id+"F15.wireOp",EDGE,"E25.MirrorCS"),sQuery(id+"F15.wireOp",EDGE,"E26.MirrorCS")])]}),"instanceName":"1"});
            var Q225;
            Q225=makeQuery(id+"F23.opPattern","COPY",BODY,{"derivedFrom":makeQuery(id+"F17.opPattern","COPY",BODY,{"derivedFrom":makeQuery(id+"F16.opExtrude","SWEPT_BODY",BODY,{"disambiguationData":[OSD([sQuery(id+"F15.wireOp",EDGE,"E13.bottom"),sQuery(id+"F15.wireOp",EDGE,"E13.top"),sQuery(id+"F15.wireOp",EDGE,"E13.left"),sQuery(id+"F15.wireOp",EDGE,"E13.right"),sQuery(id+"F15.wireOp",EDGE,"E14.bottom"),sQuery(id+"F15.wireOp",EDGE,"E14.top"),sQuery(id+"F15.wireOp",EDGE,"E14.left"),sQuery(id+"F15.wireOp",EDGE,"E14.right"),sQuery(id+"F15.wireOp",EDGE,"E15.MirrorCS"),sQuery(id+"F15.wireOp",EDGE,"E16.MirrorCS"),sQuery(id+"F15.wireOp",EDGE,"E17.MirrorCS"),sQuery(id+"F15.wireOp",EDGE,"E18.MirrorCS"),sQuery(id+"F15.wireOp",EDGE,"E19.MirrorCS"),sQuery(id+"F15.wireOp",EDGE,"E20.MirrorCS"),sQuery(id+"F15.wireOp",EDGE,"E21.MirrorCS"),sQuery(id+"F15.wireOp",EDGE,"E22.MirrorCS"),sQuery(id+"F15.wireOp",EDGE,"E23.MirrorCS"),sQuery(id+"F15.wireOp",EDGE,"E24.MirrorCS"),sQuery(id+"F15.wireOp",EDGE,"E25.MirrorCS"),sQuery(id+"F15.wireOp",EDGE,"E26.MirrorCS")])]}),"instanceName":"1"}),"instanceName":"1"});
            var Q226;
            Q226=makeQuery(id+"F23.opPattern","COPY",BODY,{"derivedFrom":makeQuery(id+"F18.opPattern","COPY",BODY,{"derivedFrom":makeQuery(id+"F16.opExtrude","SWEPT_BODY",BODY,{"disambiguationData":[OSD([sQuery(id+"F15.wireOp",EDGE,"E13.bottom"),sQuery(id+"F15.wireOp",EDGE,"E13.top"),sQuery(id+"F15.wireOp",EDGE,"E13.left"),sQuery(id+"F15.wireOp",EDGE,"E13.right"),sQuery(id+"F15.wireOp",EDGE,"E14.bottom"),sQuery(id+"F15.wireOp",EDGE,"E14.top"),sQuery(id+"F15.wireOp",EDGE,"E14.left"),sQuery(id+"F15.wireOp",EDGE,"E14.right"),sQuery(id+"F15.wireOp",EDGE,"E15.MirrorCS"),sQuery(id+"F15.wireOp",EDGE,"E16.MirrorCS"),sQuery(id+"F15.wireOp",EDGE,"E17.MirrorCS"),sQuery(id+"F15.wireOp",EDGE,"E18.MirrorCS"),sQuery(id+"F15.wireOp",EDGE,"E19.MirrorCS"),sQuery(id+"F15.wireOp",EDGE,"E20.MirrorCS"),sQuery(id+"F15.wireOp",EDGE,"E21.MirrorCS"),sQuery(id+"F15.wireOp",EDGE,"E22.MirrorCS"),sQuery(id+"F15.wireOp",EDGE,"E23.MirrorCS"),sQuery(id+"F15.wireOp",EDGE,"E24.MirrorCS"),sQuery(id+"F15.wireOp",EDGE,"E25.MirrorCS"),sQuery(id+"F15.wireOp",EDGE,"E26.MirrorCS")])]}),"instanceName":"1"}),"instanceName":"1"});
            var Q227;
            Q227=makeQuery(id+"F23.opPattern","COPY",BODY,{"derivedFrom":makeQuery(id+"F18.opPattern","COPY",BODY,{"derivedFrom":makeQuery(id+"F17.opPattern","COPY",BODY,{"derivedFrom":makeQuery(id+"F16.opExtrude","SWEPT_BODY",BODY,{"disambiguationData":[OSD([sQuery(id+"F15.wireOp",EDGE,"E13.bottom"),sQuery(id+"F15.wireOp",EDGE,"E13.top"),sQuery(id+"F15.wireOp",EDGE,"E13.left"),sQuery(id+"F15.wireOp",EDGE,"E13.right"),sQuery(id+"F15.wireOp",EDGE,"E14.bottom"),sQuery(id+"F15.wireOp",EDGE,"E14.top"),sQuery(id+"F15.wireOp",EDGE,"E14.left"),sQuery(id+"F15.wireOp",EDGE,"E14.right"),sQuery(id+"F15.wireOp",EDGE,"E15.MirrorCS"),sQuery(id+"F15.wireOp",EDGE,"E16.MirrorCS"),sQuery(id+"F15.wireOp",EDGE,"E17.MirrorCS"),sQuery(id+"F15.wireOp",EDGE,"E18.MirrorCS"),sQuery(id+"F15.wireOp",EDGE,"E19.MirrorCS"),sQuery(id+"F15.wireOp",EDGE,"E20.MirrorCS"),sQuery(id+"F15.wireOp",EDGE,"E21.MirrorCS"),sQuery(id+"F15.wireOp",EDGE,"E22.MirrorCS"),sQuery(id+"F15.wireOp",EDGE,"E23.MirrorCS"),sQuery(id+"F15.wireOp",EDGE,"E24.MirrorCS"),sQuery(id+"F15.wireOp",EDGE,"E25.MirrorCS"),sQuery(id+"F15.wireOp",EDGE,"E26.MirrorCS")])]}),"instanceName":"1"}),"instanceName":"1"}),"instanceName":"1"});
            var Q228;
            Q228=makeQuery(id+"F23.opPattern","COPY",BODY,{"derivedFrom":makeQuery(id+"F22.opPattern","COPY",BODY,{"derivedFrom":makeQuery(id+"F16.opExtrude","SWEPT_BODY",BODY,{"disambiguationData":[OSD([sQuery(id+"F15.wireOp",EDGE,"E13.bottom"),sQuery(id+"F15.wireOp",EDGE,"E13.top"),sQuery(id+"F15.wireOp",EDGE,"E13.left"),sQuery(id+"F15.wireOp",EDGE,"E13.right"),sQuery(id+"F15.wireOp",EDGE,"E14.bottom"),sQuery(id+"F15.wireOp",EDGE,"E14.top"),sQuery(id+"F15.wireOp",EDGE,"E14.left"),sQuery(id+"F15.wireOp",EDGE,"E14.right"),sQuery(id+"F15.wireOp",EDGE,"E15.MirrorCS"),sQuery(id+"F15.wireOp",EDGE,"E16.MirrorCS"),sQuery(id+"F15.wireOp",EDGE,"E17.MirrorCS"),sQuery(id+"F15.wireOp",EDGE,"E18.MirrorCS"),sQuery(id+"F15.wireOp",EDGE,"E19.MirrorCS"),sQuery(id+"F15.wireOp",EDGE,"E20.MirrorCS"),sQuery(id+"F15.wireOp",EDGE,"E21.MirrorCS"),sQuery(id+"F15.wireOp",EDGE,"E22.MirrorCS"),sQuery(id+"F15.wireOp",EDGE,"E23.MirrorCS"),sQuery(id+"F15.wireOp",EDGE,"E24.MirrorCS"),sQuery(id+"F15.wireOp",EDGE,"E25.MirrorCS"),sQuery(id+"F15.wireOp",EDGE,"E26.MirrorCS")])]}),"instanceName":"1"}),"instanceName":"1"});
            var Q229;
            Q229=makeQuery(id+"F23.opPattern","COPY",BODY,{"derivedFrom":makeQuery(id+"F22.opPattern","COPY",BODY,{"derivedFrom":makeQuery(id+"F17.opPattern","COPY",BODY,{"derivedFrom":makeQuery(id+"F16.opExtrude","SWEPT_BODY",BODY,{"disambiguationData":[OSD([sQuery(id+"F15.wireOp",EDGE,"E13.bottom"),sQuery(id+"F15.wireOp",EDGE,"E13.top"),sQuery(id+"F15.wireOp",EDGE,"E13.left"),sQuery(id+"F15.wireOp",EDGE,"E13.right"),sQuery(id+"F15.wireOp",EDGE,"E14.bottom"),sQuery(id+"F15.wireOp",EDGE,"E14.top"),sQuery(id+"F15.wireOp",EDGE,"E14.left"),sQuery(id+"F15.wireOp",EDGE,"E14.right"),sQuery(id+"F15.wireOp",EDGE,"E15.MirrorCS"),sQuery(id+"F15.wireOp",EDGE,"E16.MirrorCS"),sQuery(id+"F15.wireOp",EDGE,"E17.MirrorCS"),sQuery(id+"F15.wireOp",EDGE,"E18.MirrorCS"),sQuery(id+"F15.wireOp",EDGE,"E19.MirrorCS"),sQuery(id+"F15.wireOp",EDGE,"E20.MirrorCS"),sQuery(id+"F15.wireOp",EDGE,"E21.MirrorCS"),sQuery(id+"F15.wireOp",EDGE,"E22.MirrorCS"),sQuery(id+"F15.wireOp",EDGE,"E23.MirrorCS"),sQuery(id+"F15.wireOp",EDGE,"E24.MirrorCS"),sQuery(id+"F15.wireOp",EDGE,"E25.MirrorCS"),sQuery(id+"F15.wireOp",EDGE,"E26.MirrorCS")])]}),"instanceName":"1"}),"instanceName":"1"}),"instanceName":"1"});
            var Q230;
            Q230=makeQuery(id+"F23.opPattern","COPY",BODY,{"derivedFrom":makeQuery(id+"F22.opPattern","COPY",BODY,{"derivedFrom":makeQuery(id+"F18.opPattern","COPY",BODY,{"derivedFrom":makeQuery(id+"F16.opExtrude","SWEPT_BODY",BODY,{"disambiguationData":[OSD([sQuery(id+"F15.wireOp",EDGE,"E13.bottom"),sQuery(id+"F15.wireOp",EDGE,"E13.top"),sQuery(id+"F15.wireOp",EDGE,"E13.left"),sQuery(id+"F15.wireOp",EDGE,"E13.right"),sQuery(id+"F15.wireOp",EDGE,"E14.bottom"),sQuery(id+"F15.wireOp",EDGE,"E14.top"),sQuery(id+"F15.wireOp",EDGE,"E14.left"),sQuery(id+"F15.wireOp",EDGE,"E14.right"),sQuery(id+"F15.wireOp",EDGE,"E15.MirrorCS"),sQuery(id+"F15.wireOp",EDGE,"E16.MirrorCS"),sQuery(id+"F15.wireOp",EDGE,"E17.MirrorCS"),sQuery(id+"F15.wireOp",EDGE,"E18.MirrorCS"),sQuery(id+"F15.wireOp",EDGE,"E19.MirrorCS"),sQuery(id+"F15.wireOp",EDGE,"E20.MirrorCS"),sQuery(id+"F15.wireOp",EDGE,"E21.MirrorCS"),sQuery(id+"F15.wireOp",EDGE,"E22.MirrorCS"),sQuery(id+"F15.wireOp",EDGE,"E23.MirrorCS"),sQuery(id+"F15.wireOp",EDGE,"E24.MirrorCS"),sQuery(id+"F15.wireOp",EDGE,"E25.MirrorCS"),sQuery(id+"F15.wireOp",EDGE,"E26.MirrorCS")])]}),"instanceName":"1"}),"instanceName":"1"}),"instanceName":"1"});
            var Q231;
            Q231=makeQuery(id+"F23.opPattern","COPY",BODY,{"derivedFrom":makeQuery(id+"F22.opPattern","COPY",BODY,{"derivedFrom":makeQuery(id+"F18.opPattern","COPY",BODY,{"derivedFrom":makeQuery(id+"F17.opPattern","COPY",BODY,{"derivedFrom":makeQuery(id+"F16.opExtrude","SWEPT_BODY",BODY,{"disambiguationData":[OSD([sQuery(id+"F15.wireOp",EDGE,"E13.bottom"),sQuery(id+"F15.wireOp",EDGE,"E13.top"),sQuery(id+"F15.wireOp",EDGE,"E13.left"),sQuery(id+"F15.wireOp",EDGE,"E13.right"),sQuery(id+"F15.wireOp",EDGE,"E14.bottom"),sQuery(id+"F15.wireOp",EDGE,"E14.top"),sQuery(id+"F15.wireOp",EDGE,"E14.left"),sQuery(id+"F15.wireOp",EDGE,"E14.right"),sQuery(id+"F15.wireOp",EDGE,"E15.MirrorCS"),sQuery(id+"F15.wireOp",EDGE,"E16.MirrorCS"),sQuery(id+"F15.wireOp",EDGE,"E17.MirrorCS"),sQuery(id+"F15.wireOp",EDGE,"E18.MirrorCS"),sQuery(id+"F15.wireOp",EDGE,"E19.MirrorCS"),sQuery(id+"F15.wireOp",EDGE,"E20.MirrorCS"),sQuery(id+"F15.wireOp",EDGE,"E21.MirrorCS"),sQuery(id+"F15.wireOp",EDGE,"E22.MirrorCS"),sQuery(id+"F15.wireOp",EDGE,"E23.MirrorCS"),sQuery(id+"F15.wireOp",EDGE,"E24.MirrorCS"),sQuery(id+"F15.wireOp",EDGE,"E25.MirrorCS"),sQuery(id+"F15.wireOp",EDGE,"E26.MirrorCS")])]}),"instanceName":"1"}),"instanceName":"1"}),"instanceName":"1"}),"instanceName":"1"});
            var Q232;
            Q232=makeQuery(id+"F24.opPattern","COPY",BODY,{"derivedFrom":makeQuery(id+"F16.opExtrude","SWEPT_BODY",BODY,{"disambiguationData":[OSD([sQuery(id+"F15.wireOp",EDGE,"E13.bottom"),sQuery(id+"F15.wireOp",EDGE,"E13.top"),sQuery(id+"F15.wireOp",EDGE,"E13.left"),sQuery(id+"F15.wireOp",EDGE,"E13.right"),sQuery(id+"F15.wireOp",EDGE,"E14.bottom"),sQuery(id+"F15.wireOp",EDGE,"E14.top"),sQuery(id+"F15.wireOp",EDGE,"E14.left"),sQuery(id+"F15.wireOp",EDGE,"E14.right"),sQuery(id+"F15.wireOp",EDGE,"E15.MirrorCS"),sQuery(id+"F15.wireOp",EDGE,"E16.MirrorCS"),sQuery(id+"F15.wireOp",EDGE,"E17.MirrorCS"),sQuery(id+"F15.wireOp",EDGE,"E18.MirrorCS"),sQuery(id+"F15.wireOp",EDGE,"E19.MirrorCS"),sQuery(id+"F15.wireOp",EDGE,"E20.MirrorCS"),sQuery(id+"F15.wireOp",EDGE,"E21.MirrorCS"),sQuery(id+"F15.wireOp",EDGE,"E22.MirrorCS"),sQuery(id+"F15.wireOp",EDGE,"E23.MirrorCS"),sQuery(id+"F15.wireOp",EDGE,"E24.MirrorCS"),sQuery(id+"F15.wireOp",EDGE,"E25.MirrorCS"),sQuery(id+"F15.wireOp",EDGE,"E26.MirrorCS")])]}),"instanceName":"1"});
            var Q233;
            Q233=makeQuery(id+"F24.opPattern","COPY",BODY,{"derivedFrom":makeQuery(id+"F17.opPattern","COPY",BODY,{"derivedFrom":makeQuery(id+"F16.opExtrude","SWEPT_BODY",BODY,{"disambiguationData":[OSD([sQuery(id+"F15.wireOp",EDGE,"E13.bottom"),sQuery(id+"F15.wireOp",EDGE,"E13.top"),sQuery(id+"F15.wireOp",EDGE,"E13.left"),sQuery(id+"F15.wireOp",EDGE,"E13.right"),sQuery(id+"F15.wireOp",EDGE,"E14.bottom"),sQuery(id+"F15.wireOp",EDGE,"E14.top"),sQuery(id+"F15.wireOp",EDGE,"E14.left"),sQuery(id+"F15.wireOp",EDGE,"E14.right"),sQuery(id+"F15.wireOp",EDGE,"E15.MirrorCS"),sQuery(id+"F15.wireOp",EDGE,"E16.MirrorCS"),sQuery(id+"F15.wireOp",EDGE,"E17.MirrorCS"),sQuery(id+"F15.wireOp",EDGE,"E18.MirrorCS"),sQuery(id+"F15.wireOp",EDGE,"E19.MirrorCS"),sQuery(id+"F15.wireOp",EDGE,"E20.MirrorCS"),sQuery(id+"F15.wireOp",EDGE,"E21.MirrorCS"),sQuery(id+"F15.wireOp",EDGE,"E22.MirrorCS"),sQuery(id+"F15.wireOp",EDGE,"E23.MirrorCS"),sQuery(id+"F15.wireOp",EDGE,"E24.MirrorCS"),sQuery(id+"F15.wireOp",EDGE,"E25.MirrorCS"),sQuery(id+"F15.wireOp",EDGE,"E26.MirrorCS")])]}),"instanceName":"1"}),"instanceName":"1"});
            var Q234;
            Q234=makeQuery(id+"F24.opPattern","COPY",BODY,{"derivedFrom":makeQuery(id+"F18.opPattern","COPY",BODY,{"derivedFrom":makeQuery(id+"F16.opExtrude","SWEPT_BODY",BODY,{"disambiguationData":[OSD([sQuery(id+"F15.wireOp",EDGE,"E13.bottom"),sQuery(id+"F15.wireOp",EDGE,"E13.top"),sQuery(id+"F15.wireOp",EDGE,"E13.left"),sQuery(id+"F15.wireOp",EDGE,"E13.right"),sQuery(id+"F15.wireOp",EDGE,"E14.bottom"),sQuery(id+"F15.wireOp",EDGE,"E14.top"),sQuery(id+"F15.wireOp",EDGE,"E14.left"),sQuery(id+"F15.wireOp",EDGE,"E14.right"),sQuery(id+"F15.wireOp",EDGE,"E15.MirrorCS"),sQuery(id+"F15.wireOp",EDGE,"E16.MirrorCS"),sQuery(id+"F15.wireOp",EDGE,"E17.MirrorCS"),sQuery(id+"F15.wireOp",EDGE,"E18.MirrorCS"),sQuery(id+"F15.wireOp",EDGE,"E19.MirrorCS"),sQuery(id+"F15.wireOp",EDGE,"E20.MirrorCS"),sQuery(id+"F15.wireOp",EDGE,"E21.MirrorCS"),sQuery(id+"F15.wireOp",EDGE,"E22.MirrorCS"),sQuery(id+"F15.wireOp",EDGE,"E23.MirrorCS"),sQuery(id+"F15.wireOp",EDGE,"E24.MirrorCS"),sQuery(id+"F15.wireOp",EDGE,"E25.MirrorCS"),sQuery(id+"F15.wireOp",EDGE,"E26.MirrorCS")])]}),"instanceName":"1"}),"instanceName":"1"});
            var Q235;
            Q235=makeQuery(id+"F24.opPattern","COPY",BODY,{"derivedFrom":makeQuery(id+"F18.opPattern","COPY",BODY,{"derivedFrom":makeQuery(id+"F17.opPattern","COPY",BODY,{"derivedFrom":makeQuery(id+"F16.opExtrude","SWEPT_BODY",BODY,{"disambiguationData":[OSD([sQuery(id+"F15.wireOp",EDGE,"E13.bottom"),sQuery(id+"F15.wireOp",EDGE,"E13.top"),sQuery(id+"F15.wireOp",EDGE,"E13.left"),sQuery(id+"F15.wireOp",EDGE,"E13.right"),sQuery(id+"F15.wireOp",EDGE,"E14.bottom"),sQuery(id+"F15.wireOp",EDGE,"E14.top"),sQuery(id+"F15.wireOp",EDGE,"E14.left"),sQuery(id+"F15.wireOp",EDGE,"E14.right"),sQuery(id+"F15.wireOp",EDGE,"E15.MirrorCS"),sQuery(id+"F15.wireOp",EDGE,"E16.MirrorCS"),sQuery(id+"F15.wireOp",EDGE,"E17.MirrorCS"),sQuery(id+"F15.wireOp",EDGE,"E18.MirrorCS"),sQuery(id+"F15.wireOp",EDGE,"E19.MirrorCS"),sQuery(id+"F15.wireOp",EDGE,"E20.MirrorCS"),sQuery(id+"F15.wireOp",EDGE,"E21.MirrorCS"),sQuery(id+"F15.wireOp",EDGE,"E22.MirrorCS"),sQuery(id+"F15.wireOp",EDGE,"E23.MirrorCS"),sQuery(id+"F15.wireOp",EDGE,"E24.MirrorCS"),sQuery(id+"F15.wireOp",EDGE,"E25.MirrorCS"),sQuery(id+"F15.wireOp",EDGE,"E26.MirrorCS")])]}),"instanceName":"1"}),"instanceName":"1"}),"instanceName":"1"});
            var Q236;
            Q236=makeQuery(id+"F24.opPattern","COPY",BODY,{"derivedFrom":makeQuery(id+"F22.opPattern","COPY",BODY,{"derivedFrom":makeQuery(id+"F16.opExtrude","SWEPT_BODY",BODY,{"disambiguationData":[OSD([sQuery(id+"F15.wireOp",EDGE,"E13.bottom"),sQuery(id+"F15.wireOp",EDGE,"E13.top"),sQuery(id+"F15.wireOp",EDGE,"E13.left"),sQuery(id+"F15.wireOp",EDGE,"E13.right"),sQuery(id+"F15.wireOp",EDGE,"E14.bottom"),sQuery(id+"F15.wireOp",EDGE,"E14.top"),sQuery(id+"F15.wireOp",EDGE,"E14.left"),sQuery(id+"F15.wireOp",EDGE,"E14.right"),sQuery(id+"F15.wireOp",EDGE,"E15.MirrorCS"),sQuery(id+"F15.wireOp",EDGE,"E16.MirrorCS"),sQuery(id+"F15.wireOp",EDGE,"E17.MirrorCS"),sQuery(id+"F15.wireOp",EDGE,"E18.MirrorCS"),sQuery(id+"F15.wireOp",EDGE,"E19.MirrorCS"),sQuery(id+"F15.wireOp",EDGE,"E20.MirrorCS"),sQuery(id+"F15.wireOp",EDGE,"E21.MirrorCS"),sQuery(id+"F15.wireOp",EDGE,"E22.MirrorCS"),sQuery(id+"F15.wireOp",EDGE,"E23.MirrorCS"),sQuery(id+"F15.wireOp",EDGE,"E24.MirrorCS"),sQuery(id+"F15.wireOp",EDGE,"E25.MirrorCS"),sQuery(id+"F15.wireOp",EDGE,"E26.MirrorCS")])]}),"instanceName":"1"}),"instanceName":"1"});
            var Q237;
            Q237=makeQuery(id+"F24.opPattern","COPY",BODY,{"derivedFrom":makeQuery(id+"F22.opPattern","COPY",BODY,{"derivedFrom":makeQuery(id+"F17.opPattern","COPY",BODY,{"derivedFrom":makeQuery(id+"F16.opExtrude","SWEPT_BODY",BODY,{"disambiguationData":[OSD([sQuery(id+"F15.wireOp",EDGE,"E13.bottom"),sQuery(id+"F15.wireOp",EDGE,"E13.top"),sQuery(id+"F15.wireOp",EDGE,"E13.left"),sQuery(id+"F15.wireOp",EDGE,"E13.right"),sQuery(id+"F15.wireOp",EDGE,"E14.bottom"),sQuery(id+"F15.wireOp",EDGE,"E14.top"),sQuery(id+"F15.wireOp",EDGE,"E14.left"),sQuery(id+"F15.wireOp",EDGE,"E14.right"),sQuery(id+"F15.wireOp",EDGE,"E15.MirrorCS"),sQuery(id+"F15.wireOp",EDGE,"E16.MirrorCS"),sQuery(id+"F15.wireOp",EDGE,"E17.MirrorCS"),sQuery(id+"F15.wireOp",EDGE,"E18.MirrorCS"),sQuery(id+"F15.wireOp",EDGE,"E19.MirrorCS"),sQuery(id+"F15.wireOp",EDGE,"E20.MirrorCS"),sQuery(id+"F15.wireOp",EDGE,"E21.MirrorCS"),sQuery(id+"F15.wireOp",EDGE,"E22.MirrorCS"),sQuery(id+"F15.wireOp",EDGE,"E23.MirrorCS"),sQuery(id+"F15.wireOp",EDGE,"E24.MirrorCS"),sQuery(id+"F15.wireOp",EDGE,"E25.MirrorCS"),sQuery(id+"F15.wireOp",EDGE,"E26.MirrorCS")])]}),"instanceName":"1"}),"instanceName":"1"}),"instanceName":"1"});
            var Q238;
            Q238=makeQuery(id+"F24.opPattern","COPY",BODY,{"derivedFrom":makeQuery(id+"F22.opPattern","COPY",BODY,{"derivedFrom":makeQuery(id+"F18.opPattern","COPY",BODY,{"derivedFrom":makeQuery(id+"F16.opExtrude","SWEPT_BODY",BODY,{"disambiguationData":[OSD([sQuery(id+"F15.wireOp",EDGE,"E13.bottom"),sQuery(id+"F15.wireOp",EDGE,"E13.top"),sQuery(id+"F15.wireOp",EDGE,"E13.left"),sQuery(id+"F15.wireOp",EDGE,"E13.right"),sQuery(id+"F15.wireOp",EDGE,"E14.bottom"),sQuery(id+"F15.wireOp",EDGE,"E14.top"),sQuery(id+"F15.wireOp",EDGE,"E14.left"),sQuery(id+"F15.wireOp",EDGE,"E14.right"),sQuery(id+"F15.wireOp",EDGE,"E15.MirrorCS"),sQuery(id+"F15.wireOp",EDGE,"E16.MirrorCS"),sQuery(id+"F15.wireOp",EDGE,"E17.MirrorCS"),sQuery(id+"F15.wireOp",EDGE,"E18.MirrorCS"),sQuery(id+"F15.wireOp",EDGE,"E19.MirrorCS"),sQuery(id+"F15.wireOp",EDGE,"E20.MirrorCS"),sQuery(id+"F15.wireOp",EDGE,"E21.MirrorCS"),sQuery(id+"F15.wireOp",EDGE,"E22.MirrorCS"),sQuery(id+"F15.wireOp",EDGE,"E23.MirrorCS"),sQuery(id+"F15.wireOp",EDGE,"E24.MirrorCS"),sQuery(id+"F15.wireOp",EDGE,"E25.MirrorCS"),sQuery(id+"F15.wireOp",EDGE,"E26.MirrorCS")])]}),"instanceName":"1"}),"instanceName":"1"}),"instanceName":"1"});
            var Q239;
            Q239=makeQuery(id+"F24.opPattern","COPY",BODY,{"derivedFrom":makeQuery(id+"F22.opPattern","COPY",BODY,{"derivedFrom":makeQuery(id+"F18.opPattern","COPY",BODY,{"derivedFrom":makeQuery(id+"F17.opPattern","COPY",BODY,{"derivedFrom":makeQuery(id+"F16.opExtrude","SWEPT_BODY",BODY,{"disambiguationData":[OSD([sQuery(id+"F15.wireOp",EDGE,"E13.bottom"),sQuery(id+"F15.wireOp",EDGE,"E13.top"),sQuery(id+"F15.wireOp",EDGE,"E13.left"),sQuery(id+"F15.wireOp",EDGE,"E13.right"),sQuery(id+"F15.wireOp",EDGE,"E14.bottom"),sQuery(id+"F15.wireOp",EDGE,"E14.top"),sQuery(id+"F15.wireOp",EDGE,"E14.left"),sQuery(id+"F15.wireOp",EDGE,"E14.right"),sQuery(id+"F15.wireOp",EDGE,"E15.MirrorCS"),sQuery(id+"F15.wireOp",EDGE,"E16.MirrorCS"),sQuery(id+"F15.wireOp",EDGE,"E17.MirrorCS"),sQuery(id+"F15.wireOp",EDGE,"E18.MirrorCS"),sQuery(id+"F15.wireOp",EDGE,"E19.MirrorCS"),sQuery(id+"F15.wireOp",EDGE,"E20.MirrorCS"),sQuery(id+"F15.wireOp",EDGE,"E21.MirrorCS"),sQuery(id+"F15.wireOp",EDGE,"E22.MirrorCS"),sQuery(id+"F15.wireOp",EDGE,"E23.MirrorCS"),sQuery(id+"F15.wireOp",EDGE,"E24.MirrorCS"),sQuery(id+"F15.wireOp",EDGE,"E25.MirrorCS"),sQuery(id+"F15.wireOp",EDGE,"E26.MirrorCS")])]}),"instanceName":"1"}),"instanceName":"1"}),"instanceName":"1"}),"instanceName":"1"});
            var Q240;
            Q240=makeQuery(id+"F24.opPattern","COPY",BODY,{"derivedFrom":makeQuery(id+"F23.opPattern","COPY",BODY,{"derivedFrom":makeQuery(id+"F16.opExtrude","SWEPT_BODY",BODY,{"disambiguationData":[OSD([sQuery(id+"F15.wireOp",EDGE,"E13.bottom"),sQuery(id+"F15.wireOp",EDGE,"E13.top"),sQuery(id+"F15.wireOp",EDGE,"E13.left"),sQuery(id+"F15.wireOp",EDGE,"E13.right"),sQuery(id+"F15.wireOp",EDGE,"E14.bottom"),sQuery(id+"F15.wireOp",EDGE,"E14.top"),sQuery(id+"F15.wireOp",EDGE,"E14.left"),sQuery(id+"F15.wireOp",EDGE,"E14.right"),sQuery(id+"F15.wireOp",EDGE,"E15.MirrorCS"),sQuery(id+"F15.wireOp",EDGE,"E16.MirrorCS"),sQuery(id+"F15.wireOp",EDGE,"E17.MirrorCS"),sQuery(id+"F15.wireOp",EDGE,"E18.MirrorCS"),sQuery(id+"F15.wireOp",EDGE,"E19.MirrorCS"),sQuery(id+"F15.wireOp",EDGE,"E20.MirrorCS"),sQuery(id+"F15.wireOp",EDGE,"E21.MirrorCS"),sQuery(id+"F15.wireOp",EDGE,"E22.MirrorCS"),sQuery(id+"F15.wireOp",EDGE,"E23.MirrorCS"),sQuery(id+"F15.wireOp",EDGE,"E24.MirrorCS"),sQuery(id+"F15.wireOp",EDGE,"E25.MirrorCS"),sQuery(id+"F15.wireOp",EDGE,"E26.MirrorCS")])]}),"instanceName":"1"}),"instanceName":"1"});
            var Q241;
            Q241=makeQuery(id+"F24.opPattern","COPY",BODY,{"derivedFrom":makeQuery(id+"F23.opPattern","COPY",BODY,{"derivedFrom":makeQuery(id+"F17.opPattern","COPY",BODY,{"derivedFrom":makeQuery(id+"F16.opExtrude","SWEPT_BODY",BODY,{"disambiguationData":[OSD([sQuery(id+"F15.wireOp",EDGE,"E13.bottom"),sQuery(id+"F15.wireOp",EDGE,"E13.top"),sQuery(id+"F15.wireOp",EDGE,"E13.left"),sQuery(id+"F15.wireOp",EDGE,"E13.right"),sQuery(id+"F15.wireOp",EDGE,"E14.bottom"),sQuery(id+"F15.wireOp",EDGE,"E14.top"),sQuery(id+"F15.wireOp",EDGE,"E14.left"),sQuery(id+"F15.wireOp",EDGE,"E14.right"),sQuery(id+"F15.wireOp",EDGE,"E15.MirrorCS"),sQuery(id+"F15.wireOp",EDGE,"E16.MirrorCS"),sQuery(id+"F15.wireOp",EDGE,"E17.MirrorCS"),sQuery(id+"F15.wireOp",EDGE,"E18.MirrorCS"),sQuery(id+"F15.wireOp",EDGE,"E19.MirrorCS"),sQuery(id+"F15.wireOp",EDGE,"E20.MirrorCS"),sQuery(id+"F15.wireOp",EDGE,"E21.MirrorCS"),sQuery(id+"F15.wireOp",EDGE,"E22.MirrorCS"),sQuery(id+"F15.wireOp",EDGE,"E23.MirrorCS"),sQuery(id+"F15.wireOp",EDGE,"E24.MirrorCS"),sQuery(id+"F15.wireOp",EDGE,"E25.MirrorCS"),sQuery(id+"F15.wireOp",EDGE,"E26.MirrorCS")])]}),"instanceName":"1"}),"instanceName":"1"}),"instanceName":"1"});
            var Q242;
            Q242=makeQuery(id+"F24.opPattern","COPY",BODY,{"derivedFrom":makeQuery(id+"F23.opPattern","COPY",BODY,{"derivedFrom":makeQuery(id+"F18.opPattern","COPY",BODY,{"derivedFrom":makeQuery(id+"F16.opExtrude","SWEPT_BODY",BODY,{"disambiguationData":[OSD([sQuery(id+"F15.wireOp",EDGE,"E13.bottom"),sQuery(id+"F15.wireOp",EDGE,"E13.top"),sQuery(id+"F15.wireOp",EDGE,"E13.left"),sQuery(id+"F15.wireOp",EDGE,"E13.right"),sQuery(id+"F15.wireOp",EDGE,"E14.bottom"),sQuery(id+"F15.wireOp",EDGE,"E14.top"),sQuery(id+"F15.wireOp",EDGE,"E14.left"),sQuery(id+"F15.wireOp",EDGE,"E14.right"),sQuery(id+"F15.wireOp",EDGE,"E15.MirrorCS"),sQuery(id+"F15.wireOp",EDGE,"E16.MirrorCS"),sQuery(id+"F15.wireOp",EDGE,"E17.MirrorCS"),sQuery(id+"F15.wireOp",EDGE,"E18.MirrorCS"),sQuery(id+"F15.wireOp",EDGE,"E19.MirrorCS"),sQuery(id+"F15.wireOp",EDGE,"E20.MirrorCS"),sQuery(id+"F15.wireOp",EDGE,"E21.MirrorCS"),sQuery(id+"F15.wireOp",EDGE,"E22.MirrorCS"),sQuery(id+"F15.wireOp",EDGE,"E23.MirrorCS"),sQuery(id+"F15.wireOp",EDGE,"E24.MirrorCS"),sQuery(id+"F15.wireOp",EDGE,"E25.MirrorCS"),sQuery(id+"F15.wireOp",EDGE,"E26.MirrorCS")])]}),"instanceName":"1"}),"instanceName":"1"}),"instanceName":"1"});
            var Q243;
            Q243=makeQuery(id+"F24.opPattern","COPY",BODY,{"derivedFrom":makeQuery(id+"F23.opPattern","COPY",BODY,{"derivedFrom":makeQuery(id+"F18.opPattern","COPY",BODY,{"derivedFrom":makeQuery(id+"F17.opPattern","COPY",BODY,{"derivedFrom":makeQuery(id+"F16.opExtrude","SWEPT_BODY",BODY,{"disambiguationData":[OSD([sQuery(id+"F15.wireOp",EDGE,"E13.bottom"),sQuery(id+"F15.wireOp",EDGE,"E13.top"),sQuery(id+"F15.wireOp",EDGE,"E13.left"),sQuery(id+"F15.wireOp",EDGE,"E13.right"),sQuery(id+"F15.wireOp",EDGE,"E14.bottom"),sQuery(id+"F15.wireOp",EDGE,"E14.top"),sQuery(id+"F15.wireOp",EDGE,"E14.left"),sQuery(id+"F15.wireOp",EDGE,"E14.right"),sQuery(id+"F15.wireOp",EDGE,"E15.MirrorCS"),sQuery(id+"F15.wireOp",EDGE,"E16.MirrorCS"),sQuery(id+"F15.wireOp",EDGE,"E17.MirrorCS"),sQuery(id+"F15.wireOp",EDGE,"E18.MirrorCS"),sQuery(id+"F15.wireOp",EDGE,"E19.MirrorCS"),sQuery(id+"F15.wireOp",EDGE,"E20.MirrorCS"),sQuery(id+"F15.wireOp",EDGE,"E21.MirrorCS"),sQuery(id+"F15.wireOp",EDGE,"E22.MirrorCS"),sQuery(id+"F15.wireOp",EDGE,"E23.MirrorCS"),sQuery(id+"F15.wireOp",EDGE,"E24.MirrorCS"),sQuery(id+"F15.wireOp",EDGE,"E25.MirrorCS"),sQuery(id+"F15.wireOp",EDGE,"E26.MirrorCS")])]}),"instanceName":"1"}),"instanceName":"1"}),"instanceName":"1"}),"instanceName":"1"});
            var Q244;
            Q244=makeQuery(id+"F24.opPattern","COPY",BODY,{"derivedFrom":makeQuery(id+"F23.opPattern","COPY",BODY,{"derivedFrom":makeQuery(id+"F22.opPattern","COPY",BODY,{"derivedFrom":makeQuery(id+"F16.opExtrude","SWEPT_BODY",BODY,{"disambiguationData":[OSD([sQuery(id+"F15.wireOp",EDGE,"E13.bottom"),sQuery(id+"F15.wireOp",EDGE,"E13.top"),sQuery(id+"F15.wireOp",EDGE,"E13.left"),sQuery(id+"F15.wireOp",EDGE,"E13.right"),sQuery(id+"F15.wireOp",EDGE,"E14.bottom"),sQuery(id+"F15.wireOp",EDGE,"E14.top"),sQuery(id+"F15.wireOp",EDGE,"E14.left"),sQuery(id+"F15.wireOp",EDGE,"E14.right"),sQuery(id+"F15.wireOp",EDGE,"E15.MirrorCS"),sQuery(id+"F15.wireOp",EDGE,"E16.MirrorCS"),sQuery(id+"F15.wireOp",EDGE,"E17.MirrorCS"),sQuery(id+"F15.wireOp",EDGE,"E18.MirrorCS"),sQuery(id+"F15.wireOp",EDGE,"E19.MirrorCS"),sQuery(id+"F15.wireOp",EDGE,"E20.MirrorCS"),sQuery(id+"F15.wireOp",EDGE,"E21.MirrorCS"),sQuery(id+"F15.wireOp",EDGE,"E22.MirrorCS"),sQuery(id+"F15.wireOp",EDGE,"E23.MirrorCS"),sQuery(id+"F15.wireOp",EDGE,"E24.MirrorCS"),sQuery(id+"F15.wireOp",EDGE,"E25.MirrorCS"),sQuery(id+"F15.wireOp",EDGE,"E26.MirrorCS")])]}),"instanceName":"1"}),"instanceName":"1"}),"instanceName":"1"});
            var Q245;
            Q245=makeQuery(id+"F24.opPattern","COPY",BODY,{"derivedFrom":makeQuery(id+"F23.opPattern","COPY",BODY,{"derivedFrom":makeQuery(id+"F22.opPattern","COPY",BODY,{"derivedFrom":makeQuery(id+"F17.opPattern","COPY",BODY,{"derivedFrom":makeQuery(id+"F16.opExtrude","SWEPT_BODY",BODY,{"disambiguationData":[OSD([sQuery(id+"F15.wireOp",EDGE,"E13.bottom"),sQuery(id+"F15.wireOp",EDGE,"E13.top"),sQuery(id+"F15.wireOp",EDGE,"E13.left"),sQuery(id+"F15.wireOp",EDGE,"E13.right"),sQuery(id+"F15.wireOp",EDGE,"E14.bottom"),sQuery(id+"F15.wireOp",EDGE,"E14.top"),sQuery(id+"F15.wireOp",EDGE,"E14.left"),sQuery(id+"F15.wireOp",EDGE,"E14.right"),sQuery(id+"F15.wireOp",EDGE,"E15.MirrorCS"),sQuery(id+"F15.wireOp",EDGE,"E16.MirrorCS"),sQuery(id+"F15.wireOp",EDGE,"E17.MirrorCS"),sQuery(id+"F15.wireOp",EDGE,"E18.MirrorCS"),sQuery(id+"F15.wireOp",EDGE,"E19.MirrorCS"),sQuery(id+"F15.wireOp",EDGE,"E20.MirrorCS"),sQuery(id+"F15.wireOp",EDGE,"E21.MirrorCS"),sQuery(id+"F15.wireOp",EDGE,"E22.MirrorCS"),sQuery(id+"F15.wireOp",EDGE,"E23.MirrorCS"),sQuery(id+"F15.wireOp",EDGE,"E24.MirrorCS"),sQuery(id+"F15.wireOp",EDGE,"E25.MirrorCS"),sQuery(id+"F15.wireOp",EDGE,"E26.MirrorCS")])]}),"instanceName":"1"}),"instanceName":"1"}),"instanceName":"1"}),"instanceName":"1"});
            var Q246;
            Q246=makeQuery(id+"F24.opPattern","COPY",BODY,{"derivedFrom":makeQuery(id+"F23.opPattern","COPY",BODY,{"derivedFrom":makeQuery(id+"F22.opPattern","COPY",BODY,{"derivedFrom":makeQuery(id+"F18.opPattern","COPY",BODY,{"derivedFrom":makeQuery(id+"F16.opExtrude","SWEPT_BODY",BODY,{"disambiguationData":[OSD([sQuery(id+"F15.wireOp",EDGE,"E13.bottom"),sQuery(id+"F15.wireOp",EDGE,"E13.top"),sQuery(id+"F15.wireOp",EDGE,"E13.left"),sQuery(id+"F15.wireOp",EDGE,"E13.right"),sQuery(id+"F15.wireOp",EDGE,"E14.bottom"),sQuery(id+"F15.wireOp",EDGE,"E14.top"),sQuery(id+"F15.wireOp",EDGE,"E14.left"),sQuery(id+"F15.wireOp",EDGE,"E14.right"),sQuery(id+"F15.wireOp",EDGE,"E15.MirrorCS"),sQuery(id+"F15.wireOp",EDGE,"E16.MirrorCS"),sQuery(id+"F15.wireOp",EDGE,"E17.MirrorCS"),sQuery(id+"F15.wireOp",EDGE,"E18.MirrorCS"),sQuery(id+"F15.wireOp",EDGE,"E19.MirrorCS"),sQuery(id+"F15.wireOp",EDGE,"E20.MirrorCS"),sQuery(id+"F15.wireOp",EDGE,"E21.MirrorCS"),sQuery(id+"F15.wireOp",EDGE,"E22.MirrorCS"),sQuery(id+"F15.wireOp",EDGE,"E23.MirrorCS"),sQuery(id+"F15.wireOp",EDGE,"E24.MirrorCS"),sQuery(id+"F15.wireOp",EDGE,"E25.MirrorCS"),sQuery(id+"F15.wireOp",EDGE,"E26.MirrorCS")])]}),"instanceName":"1"}),"instanceName":"1"}),"instanceName":"1"}),"instanceName":"1"});
            var Q247;
            Q247=makeQuery(id+"F24.opPattern","COPY",BODY,{"derivedFrom":makeQuery(id+"F23.opPattern","COPY",BODY,{"derivedFrom":makeQuery(id+"F22.opPattern","COPY",BODY,{"derivedFrom":makeQuery(id+"F18.opPattern","COPY",BODY,{"derivedFrom":makeQuery(id+"F17.opPattern","COPY",BODY,{"derivedFrom":makeQuery(id+"F16.opExtrude","SWEPT_BODY",BODY,{"disambiguationData":[OSD([sQuery(id+"F15.wireOp",EDGE,"E13.bottom"),sQuery(id+"F15.wireOp",EDGE,"E13.top"),sQuery(id+"F15.wireOp",EDGE,"E13.left"),sQuery(id+"F15.wireOp",EDGE,"E13.right"),sQuery(id+"F15.wireOp",EDGE,"E14.bottom"),sQuery(id+"F15.wireOp",EDGE,"E14.top"),sQuery(id+"F15.wireOp",EDGE,"E14.left"),sQuery(id+"F15.wireOp",EDGE,"E14.right"),sQuery(id+"F15.wireOp",EDGE,"E15.MirrorCS"),sQuery(id+"F15.wireOp",EDGE,"E16.MirrorCS"),sQuery(id+"F15.wireOp",EDGE,"E17.MirrorCS"),sQuery(id+"F15.wireOp",EDGE,"E18.MirrorCS"),sQuery(id+"F15.wireOp",EDGE,"E19.MirrorCS"),sQuery(id+"F15.wireOp",EDGE,"E20.MirrorCS"),sQuery(id+"F15.wireOp",EDGE,"E21.MirrorCS"),sQuery(id+"F15.wireOp",EDGE,"E22.MirrorCS"),sQuery(id+"F15.wireOp",EDGE,"E23.MirrorCS"),sQuery(id+"F15.wireOp",EDGE,"E24.MirrorCS"),sQuery(id+"F15.wireOp",EDGE,"E25.MirrorCS"),sQuery(id+"F15.wireOp",EDGE,"E26.MirrorCS")])]}),"instanceName":"1"}),"instanceName":"1"}),"instanceName":"1"}),"instanceName":"1"}),"instanceName":"1"});
            transform(context, id + "F25", {"entities" : qUnion([Q0, Q1, Q2, Q3, Q4, Q5, Q6, Q7, Q8, Q9, Q10, Q11, Q12, Q13, Q14, Q15, Q16, Q17, Q18, Q19, Q20, Q21, Q22, Q23, Q24, Q25, Q26, Q27, Q28, Q29, Q30, Q31, Q32, Q33, Q34, Q35, Q36, Q37, Q38, Q39, Q40, Q41, Q42, Q43, Q44, Q45, Q46, Q47, Q48, Q49, Q50, Q51, Q52, Q53, Q54, Q55, Q56, Q57, Q58, Q59, Q60, Q61, Q62, Q63, Q64, Q65, Q66, Q67, Q68, Q69, Q70, Q71, Q72, Q73, Q74, Q75, Q76, Q77, Q78, Q79, Q80, Q81, Q82, Q83, Q84, Q85, Q86, Q87, Q88, Q89, Q90, Q91, Q92, Q93, Q94, Q95, Q96, Q97, Q98, Q99, Q100, Q101, Q102, Q103, Q104, Q105, Q106, Q107, Q108, Q109, Q110, Q111, Q112, Q113, Q114, Q115, Q116, Q117, Q118, Q119, Q120, Q121, Q122, Q123, Q124, Q125, Q126, Q127, Q128, Q129, Q130, Q131, Q132, Q133, Q134, Q135, Q136, Q137, Q138, Q139, Q140, Q141, Q142, Q143, Q144, Q145, Q146, Q147, Q148, Q149, Q150, Q151, Q152, Q153, Q154, Q155, Q156, Q157, Q158, Q159, Q160, Q161, Q162, Q163, Q164, Q165, Q166, Q167, Q168, Q169, Q170, Q171, Q172, Q173, Q174, Q175, Q176, Q177, Q178, Q179, Q180, Q181, Q182, Q183, Q184, Q185, Q186, Q187, Q188, Q189, Q190, Q191, Q192, Q193, Q194, Q195, Q196, Q197, Q198, Q199, Q200, Q201, Q202, Q203, Q204, Q205, Q206, Q207, Q208, Q209, Q210, Q211, Q212, Q213, Q214, Q215, Q216, Q217, Q218, Q219, Q220, Q221, Q222, Q223, Q224, Q225, Q226, Q227, Q228, Q229, Q230, Q231, Q232, Q233, Q234, Q235, Q236, Q237, Q238, Q239, Q240, Q241, Q242, Q243, Q244, Q245, Q246, Q247]), "transformType" : TransformType.TRANSLATION_3D, "dx" : -320 * mm, "dy" : 0 * mm, "dz" : 0 * mm, "makeCopy" : true});
        }
    });
